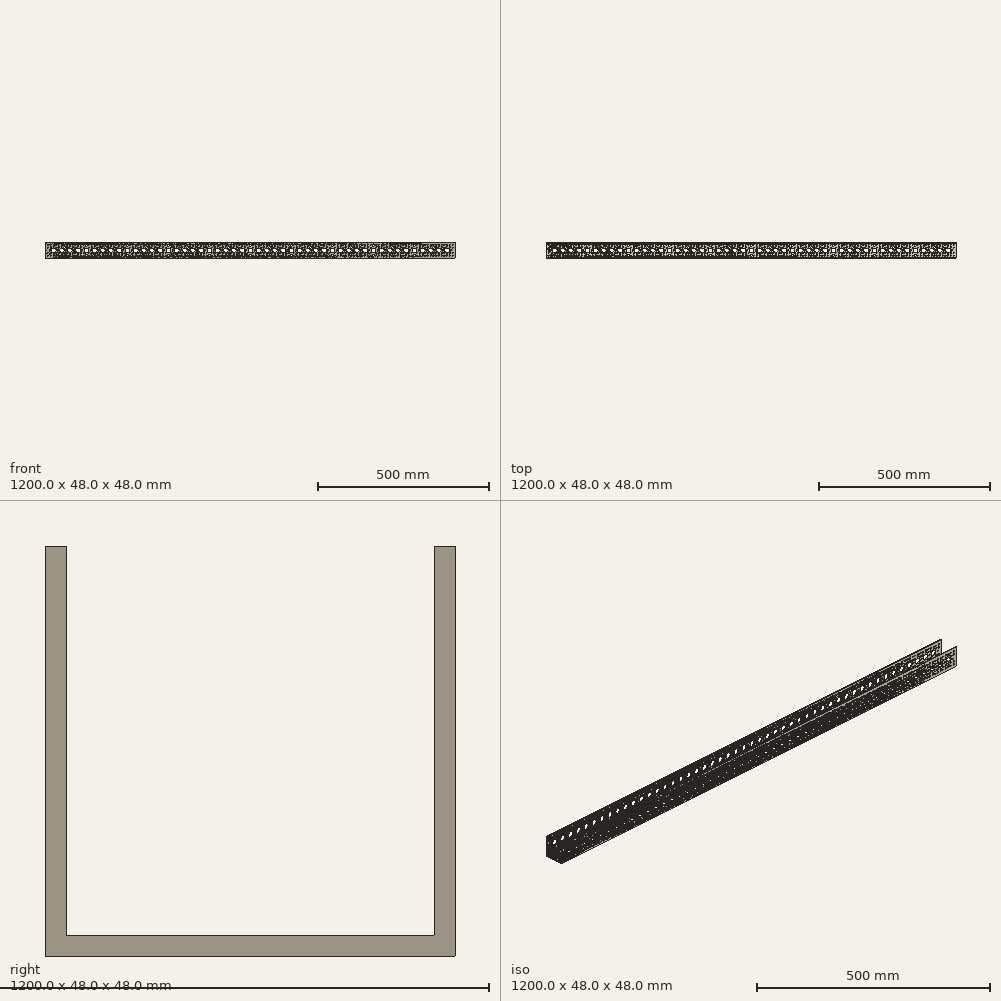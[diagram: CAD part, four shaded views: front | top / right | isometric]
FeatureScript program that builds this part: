
annotation { "Feature Type Name" : "Feature", "Feature Type Description" : "" }
export const myFeature = defineFeature(function(context is Context, id is Id, definition is map)
    precondition{}
    {
        {
            var Q0;
            Q0=qCreatedBy(makeId("Right.planeOp"),FACE);
            var sketch = newSketch(context, id + "F0", { "sketchPlane" : qUnion([Q0]) });
            skLineSegment(sketch, "E0.bottom", {"start": v(24, 24) * mm, "end": v(21.5, 24) * mm});
            skLineSegment(sketch, "E0.top", {"start": v(24, -24) * mm, "end": v(-24, -24) * mm});
            skLineSegment(sketch, "E0.left", {"start": v(24, 24) * mm, "end": v(24, -24) * mm});
            skLineSegment(sketch, "E0.right", {"start": v(-24, 24) * mm, "end": v(-24, -24) * mm});
            skPoint(sketch, "E0.middle", {"position": v(0, 0) * mm});
            skLineSegment(sketch, "E1.top", {"start": v(-21.5, -21.5) * mm, "end": v(21.5, -21.5) * mm});
            skLineSegment(sketch, "E1.left", {"start": v(-21.5, 24) * mm, "end": v(-21.5, -21.5) * mm});
            skLineSegment(sketch, "E1.right", {"start": v(21.5, 24) * mm, "end": v(21.5, -21.5) * mm});
            skLineSegment(sketch, "E2.trimOffspring", {"start": v(-21.5, 24) * mm, "end": v(-24, 24) * mm});
            skSolve(sketch);
        }
        {
            var Q0;
            Q0=qSketchRegion(id+"F0",true);
            extrude(context, id + "F1", {"entities" : qUnion([Q0]), "depth" : 48 * mm, "offsetDistance" : 25 * mm});
        }
        {
            var Q0;
            Q0=qSketchRegion(id+"F0",true);
            extrude(context, id + "F2", {"entities" : qUnion([Q0]), "depth" : 72 * mm, "offsetDistance" : 25 * mm});
        }
        {
            var Q0;
            Q0=qSketchRegion(id+"F0",true);
            extrude(context, id + "F3", {"entities" : qUnion([Q0]), "depth" : 96 * mm, "offsetDistance" : 25 * mm});
        }
        {
            var Q0;
            Q0=qSketchRegion(id+"F0",true);
            extrude(context, id + "F4", {"entities" : qUnion([Q0]), "depth" : 120 * mm, "offsetDistance" : 25 * mm});
        }
        {
            var Q0;
            Q0=qSketchRegion(id+"F0",true);
            extrude(context, id + "F5", {"entities" : qUnion([Q0]), "depth" : 144 * mm, "offsetDistance" : 25 * mm});
        }
        {
            var Q0;
            Q0=qSketchRegion(id+"F0",true);
            extrude(context, id + "F6", {"entities" : qUnion([Q0]), "depth" : 192 * mm, "offsetDistance" : 25 * mm});
        }
        {
            var Q0;
            Q0=qSketchRegion(id+"F0",true);
            extrude(context, id + "F7", {"entities" : qUnion([Q0]), "depth" : 240 * mm, "offsetDistance" : 25 * mm});
        }
        {
            var Q0;
            Q0=qSketchRegion(id+"F0",true);
            extrude(context, id + "F8", {"entities" : qUnion([Q0]), "depth" : 288 * mm, "offsetDistance" : 25 * mm});
        }
        {
            var Q0;
            Q0=qSketchRegion(id+"F0",true);
            extrude(context, id + "F9", {"entities" : qUnion([Q0]), "depth" : 336 * mm, "offsetDistance" : 25 * mm});
        }
        {
            var Q0;
            Q0=qSketchRegion(id+"F0",true);
            extrude(context, id + "F10", {"entities" : qUnion([Q0]), "depth" : 384 * mm, "offsetDistance" : 25 * mm});
        }
        {
            var Q0;
            Q0=qSketchRegion(id+"F0",true);
            extrude(context, id + "F11", {"entities" : qUnion([Q0]), "depth" : 432 * mm, "offsetDistance" : 25 * mm});
        }
        {
            var Q0;
            Q0=qSketchRegion(id+"F0",true);
            extrude(context, id + "F12", {"entities" : qUnion([Q0]), "depth" : 528 * mm, "offsetDistance" : 25 * mm});
        }
        {
            var Q0;
            Q0=qSketchRegion(id+"F0",true);
            extrude(context, id + "F13", {"entities" : qUnion([Q0]), "depth" : 624 * mm, "offsetDistance" : 25 * mm});
        }
        {
            var Q0;
            Q0=qSketchRegion(id+"F0",true);
            extrude(context, id + "F14", {"entities" : qUnion([Q0]), "depth" : 720 * mm, "offsetDistance" : 25 * mm});
        }
        {
            var Q0;
            Q0=qSketchRegion(id+"F0",true);
            extrude(context, id + "F15", {"entities" : qUnion([Q0]), "depth" : 816 * mm, "offsetDistance" : 25 * mm});
        }
        {
            var Q0;
            Q0=qSketchRegion(id+"F0",true);
            extrude(context, id + "F16", {"entities" : qUnion([Q0]), "depth" : 912 * mm, "offsetDistance" : 25 * mm});
        }
        {
            var Q0;
            Q0=qSketchRegion(id+"F0",true);
            extrude(context, id + "F17", {"entities" : qUnion([Q0]), "depth" : 1008 * mm, "offsetDistance" : 25 * mm});
        }
        {
            var Q0;
            Q0=qSketchRegion(id+"F0",true);
            extrude(context, id + "F18", {"entities" : qUnion([Q0]), "depth" : 1104 * mm, "offsetDistance" : 25 * mm});
        }
        {
            var Q0;
            Q0=qSketchRegion(id+"F0",true);
            extrude(context, id + "F19", {"entities" : qUnion([Q0]), "depth" : 1200 * mm, "offsetDistance" : 25 * mm});
        }
        {
            var Q0;
            Q0=qCreatedBy(makeId("Front.planeOp"),FACE);
            var sketch = newSketch(context, id + "F20", { "sketchPlane" : qUnion([Q0]) });
            skCircle(sketch, "E3", {"center": v(24, 0) * mm, "radius": 7 * mm});
            skLineSegment(sketch, "E4.0", {"start": v(48, 24) * mm, "end": v(0, 24) * mm, "construction": true});
            skLineSegment(sketch, "E5.0", {"start": v(48, -24) * mm, "end": v(0, -24) * mm, "construction": true});
            skLineSegment(sketch, "E6", {"start": v(24, 0) * mm, "end": v(24, 24) * mm, "construction": true});
            skLineSegment(sketch, "E7", {"start": v(24, 24) * mm, "end": v(24, -24) * mm, "construction": true});
            skArc(sketch, "E8", {"start": v(26, 16) * mm, "mid": v(24, 18) * mm, "end": v(22, 16) * mm});
            skArc(sketch, "E9", {"start": v(22, 12) * mm, "mid": v(24, 10) * mm, "end": v(26, 12) * mm});
            skLineSegment(sketch, "E10", {"start": v(22, 16) * mm, "end": v(22, 12) * mm});
            skLineSegment(sketch, "E11", {"start": v(26, 16) * mm, "end": v(26, 12) * mm});
            skArc(sketch, "E12", {"start": v(26, -12) * mm, "mid": v(24, -10) * mm, "end": v(22, -12) * mm});
            skArc(sketch, "E13", {"start": v(22, -16) * mm, "mid": v(24, -18) * mm, "end": v(26, -16) * mm});
            skLineSegment(sketch, "E14", {"start": v(22, -12) * mm, "end": v(22, -16) * mm});
            skLineSegment(sketch, "E15", {"start": v(26, -16) * mm, "end": v(26, -12) * mm});
            skLineSegment(sketch, "E16", {"start": v(0, -24) * mm, "end": v(24, 0) * mm, "construction": true});
            skLineSegment(sketch, "E17", {"start": v(0, 24) * mm, "end": v(24, 0) * mm, "construction": true});
            skArc(sketch, "E18", {"start": v(14.1, -7.07) * mm, "mid": v(14.1, -9.9) * mm, "end": v(16.93, -9.9) * mm});
            skArc(sketch, "E19", {"start": v(17.41, -9.41) * mm, "mid": v(17.41, -6.59) * mm, "end": v(14.59, -6.59) * mm});
            skArc(sketch, "E20", {"start": v(14.59, 6.59) * mm, "mid": v(17.41, 6.59) * mm, "end": v(17.41, 9.41) * mm});
            skArc(sketch, "E21", {"start": v(16.93, 9.9) * mm, "mid": v(14.1, 9.9) * mm, "end": v(14.1, 7.07) * mm});
            skLineSegment(sketch, "E22", {"start": v(15.51, 8.49) * mm, "end": v(16.93, 9.9) * mm, "construction": true});
            skLineSegment(sketch, "E23", {"start": v(15.51, 8.49) * mm, "end": v(14.1, 7.07) * mm, "construction": true});
            skLineSegment(sketch, "E24", {"start": v(17.41, 9.41) * mm, "end": v(14.59, 6.59) * mm, "construction": true});
            skLineSegment(sketch, "E25", {"start": v(16.93, 9.9) * mm, "end": v(17.41, 9.41) * mm});
            skLineSegment(sketch, "E26", {"start": v(14.1, 7.07) * mm, "end": v(14.59, 6.59) * mm});
            skLineSegment(sketch, "E27", {"start": v(14.1, -7.07) * mm, "end": v(16.93, -9.9) * mm, "construction": true});
            skLineSegment(sketch, "E28", {"start": v(14.59, -6.59) * mm, "end": v(17.41, -9.41) * mm, "construction": true});
            skLineSegment(sketch, "E29", {"start": v(14.1, -7.07) * mm, "end": v(14.59, -6.59) * mm});
            skLineSegment(sketch, "E30", {"start": v(16.93, -9.9) * mm, "end": v(17.41, -9.41) * mm});
            skCircle(sketch, "E31", {"center": v(8, 16) * mm, "radius": 2 * mm});
            skCircle(sketch, "E32", {"center": v(8, -16) * mm, "radius": 2 * mm});
            skCircle(sketch, "E33", {"center": v(12, 0) * mm, "radius": 2 * mm});
            skLineSegment(sketch, "E34", {"start": v(8, 16) * mm, "end": v(24, 16) * mm, "construction": true});
            skLineSegment(sketch, "E35", {"start": v(8, -16) * mm, "end": v(24, -16) * mm, "construction": true});
            skCircle(sketch, "E36", {"center": v(16, 16) * mm, "radius": 2 * mm});
            skCircle(sketch, "E37", {"center": v(16, -16) * mm, "radius": 2 * mm});
            skLineSegment(sketch, "E38", {"start": v(0, 0) * mm, "end": v(24, -24) * mm, "construction": true});
            skLineSegment(sketch, "E39", {"start": v(24, 24) * mm, "end": v(0, 0) * mm, "construction": true});
            skArc(sketch, "E40", {"start": v(6.59, 9.41) * mm, "mid": v(6.59, 6.59) * mm, "end": v(9.41, 6.59) * mm});
            skArc(sketch, "E41", {"start": v(9.9, 7.07) * mm, "mid": v(9.9, 9.9) * mm, "end": v(7.07, 9.9) * mm});
            skArc(sketch, "E42", {"start": v(7.07, -9.9) * mm, "mid": v(9.9, -9.9) * mm, "end": v(9.9, -7.07) * mm});
            skArc(sketch, "E43", {"start": v(9.41, -6.59) * mm, "mid": v(6.59, -6.59) * mm, "end": v(6.59, -9.41) * mm});
            skLineSegment(sketch, "E44", {"start": v(7.07, 9.9) * mm, "end": v(9.9, 7.07) * mm, "construction": true});
            skLineSegment(sketch, "E45", {"start": v(6.59, 9.41) * mm, "end": v(9.41, 6.59) * mm, "construction": true});
            skLineSegment(sketch, "E46", {"start": v(9.41, -6.59) * mm, "end": v(6.59, -9.41) * mm, "construction": true});
            skLineSegment(sketch, "E47", {"start": v(9.9, -7.07) * mm, "end": v(7.07, -9.9) * mm, "construction": true});
            skLineSegment(sketch, "E48", {"start": v(9.41, -6.59) * mm, "end": v(9.9, -7.07) * mm});
            skLineSegment(sketch, "E49", {"start": v(6.59, -9.41) * mm, "end": v(7.07, -9.9) * mm});
            skLineSegment(sketch, "E50", {"start": v(7.07, 9.9) * mm, "end": v(6.59, 9.41) * mm});
            skLineSegment(sketch, "E51", {"start": v(9.9, 7.07) * mm, "end": v(9.41, 6.59) * mm});
            skArc(sketch, "E52.1.0.0", {"start": v(50, 16) * mm, "mid": v(48, 18) * mm, "end": v(46, 16) * mm});
            skLineSegment(sketch, "E52.1.0.1", {"start": v(50, 16) * mm, "end": v(50, 12) * mm});
            skLineSegment(sketch, "E52.1.0.2", {"start": v(46, 16) * mm, "end": v(46, 12) * mm});
            skArc(sketch, "E52.1.0.3", {"start": v(46, 12) * mm, "mid": v(48, 10) * mm, "end": v(50, 12) * mm});
            skCircle(sketch, "E52.1.0.4", {"center": v(40, 16) * mm, "radius": 2 * mm});
            skCircle(sketch, "E52.1.0.5", {"center": v(32, 16) * mm, "radius": 2 * mm});
            skArc(sketch, "E52.1.0.6", {"start": v(33.9, 7.07) * mm, "mid": v(33.9, 9.9) * mm, "end": v(31.07, 9.9) * mm});
            skArc(sketch, "E52.1.0.7", {"start": v(30.59, 9.41) * mm, "mid": v(30.59, 6.59) * mm, "end": v(33.41, 6.59) * mm});
            skLineSegment(sketch, "E52.1.0.8", {"start": v(31.07, 9.9) * mm, "end": v(30.59, 9.41) * mm});
            skLineSegment(sketch, "E52.1.0.9", {"start": v(33.9, 7.07) * mm, "end": v(33.41, 6.59) * mm});
            skArc(sketch, "E52.1.0.10", {"start": v(40.93, 9.9) * mm, "mid": v(38.1, 9.9) * mm, "end": v(38.1, 7.07) * mm});
            skLineSegment(sketch, "E52.1.0.11", {"start": v(40.93, 9.9) * mm, "end": v(41.41, 9.41) * mm});
            skArc(sketch, "E52.1.0.12", {"start": v(38.59, 6.59) * mm, "mid": v(41.41, 6.59) * mm, "end": v(41.41, 9.41) * mm});
            skLineSegment(sketch, "E52.1.0.13", {"start": v(38.1, 7.07) * mm, "end": v(38.59, 6.59) * mm});
            skCircle(sketch, "E52.1.0.14", {"center": v(48, 0) * mm, "radius": 7 * mm});
            skArc(sketch, "E52.1.0.15", {"start": v(31.07, -9.9) * mm, "mid": v(33.9, -9.9) * mm, "end": v(33.9, -7.07) * mm});
            skArc(sketch, "E52.1.0.16", {"start": v(33.41, -6.59) * mm, "mid": v(30.59, -6.59) * mm, "end": v(30.59, -9.41) * mm});
            skLineSegment(sketch, "E52.1.0.17", {"start": v(33.41, -6.59) * mm, "end": v(33.9, -7.07) * mm});
            skLineSegment(sketch, "E52.1.0.18", {"start": v(30.59, -9.41) * mm, "end": v(31.07, -9.9) * mm});
            skArc(sketch, "E52.1.0.19", {"start": v(38.1, -7.07) * mm, "mid": v(38.1, -9.9) * mm, "end": v(40.93, -9.9) * mm});
            skLineSegment(sketch, "E52.1.0.20", {"start": v(40.93, -9.9) * mm, "end": v(41.41, -9.41) * mm});
            skArc(sketch, "E52.1.0.21", {"start": v(41.41, -9.41) * mm, "mid": v(41.41, -6.59) * mm, "end": v(38.59, -6.59) * mm});
            skCircle(sketch, "E52.1.0.22", {"center": v(40, -16) * mm, "radius": 2 * mm});
            skCircle(sketch, "E52.1.0.23", {"center": v(32, -16) * mm, "radius": 2 * mm});
            skLineSegment(sketch, "E52.1.0.24", {"start": v(38.1, -7.07) * mm, "end": v(38.59, -6.59) * mm});
            skCircle(sketch, "E52.1.0.25", {"center": v(36, 0) * mm, "radius": 2 * mm});
            skArc(sketch, "E52.1.0.26", {"start": v(50, -12) * mm, "mid": v(48, -10) * mm, "end": v(46, -12) * mm});
            skArc(sketch, "E52.1.0.27", {"start": v(46, -16) * mm, "mid": v(48, -18) * mm, "end": v(50, -16) * mm});
            skLineSegment(sketch, "E52.1.0.28", {"start": v(46, -12) * mm, "end": v(46, -16) * mm});
            skLineSegment(sketch, "E52.1.0.29", {"start": v(50, -16) * mm, "end": v(50, -12) * mm});
            skArc(sketch, "E52.2.0.0", {"start": v(74, 16) * mm, "mid": v(72, 18) * mm, "end": v(70, 16) * mm});
            skLineSegment(sketch, "E52.2.0.1", {"start": v(74, 16) * mm, "end": v(74, 12) * mm});
            skLineSegment(sketch, "E52.2.0.2", {"start": v(70, 16) * mm, "end": v(70, 12) * mm});
            skArc(sketch, "E52.2.0.3", {"start": v(70, 12) * mm, "mid": v(72, 10) * mm, "end": v(74, 12) * mm});
            skCircle(sketch, "E52.2.0.4", {"center": v(64, 16) * mm, "radius": 2 * mm});
            skCircle(sketch, "E52.2.0.5", {"center": v(56, 16) * mm, "radius": 2 * mm});
            skArc(sketch, "E52.2.0.6", {"start": v(57.9, 7.07) * mm, "mid": v(57.9, 9.9) * mm, "end": v(55.07, 9.9) * mm});
            skArc(sketch, "E52.2.0.7", {"start": v(54.59, 9.41) * mm, "mid": v(54.59, 6.59) * mm, "end": v(57.41, 6.59) * mm});
            skLineSegment(sketch, "E52.2.0.8", {"start": v(55.07, 9.9) * mm, "end": v(54.59, 9.41) * mm});
            skLineSegment(sketch, "E52.2.0.9", {"start": v(57.9, 7.07) * mm, "end": v(57.41, 6.59) * mm});
            skArc(sketch, "E52.2.0.10", {"start": v(64.93, 9.9) * mm, "mid": v(62.1, 9.9) * mm, "end": v(62.1, 7.07) * mm});
            skLineSegment(sketch, "E52.2.0.11", {"start": v(64.93, 9.9) * mm, "end": v(65.41, 9.41) * mm});
            skArc(sketch, "E52.2.0.12", {"start": v(62.59, 6.59) * mm, "mid": v(65.41, 6.59) * mm, "end": v(65.41, 9.41) * mm});
            skLineSegment(sketch, "E52.2.0.13", {"start": v(62.1, 7.07) * mm, "end": v(62.59, 6.59) * mm});
            skCircle(sketch, "E52.2.0.14", {"center": v(72, 0) * mm, "radius": 7 * mm});
            skArc(sketch, "E52.2.0.15", {"start": v(55.07, -9.9) * mm, "mid": v(57.9, -9.9) * mm, "end": v(57.9, -7.07) * mm});
            skArc(sketch, "E52.2.0.16", {"start": v(57.41, -6.59) * mm, "mid": v(54.59, -6.59) * mm, "end": v(54.59, -9.41) * mm});
            skLineSegment(sketch, "E52.2.0.17", {"start": v(57.41, -6.59) * mm, "end": v(57.9, -7.07) * mm});
            skLineSegment(sketch, "E52.2.0.18", {"start": v(54.59, -9.41) * mm, "end": v(55.07, -9.9) * mm});
            skArc(sketch, "E52.2.0.19", {"start": v(62.1, -7.07) * mm, "mid": v(62.1, -9.9) * mm, "end": v(64.93, -9.9) * mm});
            skLineSegment(sketch, "E52.2.0.20", {"start": v(64.93, -9.9) * mm, "end": v(65.41, -9.41) * mm});
            skArc(sketch, "E52.2.0.21", {"start": v(65.41, -9.41) * mm, "mid": v(65.41, -6.59) * mm, "end": v(62.59, -6.59) * mm});
            skCircle(sketch, "E52.2.0.22", {"center": v(64, -16) * mm, "radius": 2 * mm});
            skCircle(sketch, "E52.2.0.23", {"center": v(56, -16) * mm, "radius": 2 * mm});
            skLineSegment(sketch, "E52.2.0.24", {"start": v(62.1, -7.07) * mm, "end": v(62.59, -6.59) * mm});
            skCircle(sketch, "E52.2.0.25", {"center": v(60, 0) * mm, "radius": 2 * mm});
            skArc(sketch, "E52.2.0.26", {"start": v(74, -12) * mm, "mid": v(72, -10) * mm, "end": v(70, -12) * mm});
            skArc(sketch, "E52.2.0.27", {"start": v(70, -16) * mm, "mid": v(72, -18) * mm, "end": v(74, -16) * mm});
            skLineSegment(sketch, "E52.2.0.28", {"start": v(70, -12) * mm, "end": v(70, -16) * mm});
            skLineSegment(sketch, "E52.2.0.29", {"start": v(74, -16) * mm, "end": v(74, -12) * mm});
            skArc(sketch, "E52.3.0.0", {"start": v(98, 16) * mm, "mid": v(96, 18) * mm, "end": v(94, 16) * mm});
            skLineSegment(sketch, "E52.3.0.1", {"start": v(98, 16) * mm, "end": v(98, 12) * mm});
            skLineSegment(sketch, "E52.3.0.2", {"start": v(94, 16) * mm, "end": v(94, 12) * mm});
            skArc(sketch, "E52.3.0.3", {"start": v(94, 12) * mm, "mid": v(96, 10) * mm, "end": v(98, 12) * mm});
            skCircle(sketch, "E52.3.0.4", {"center": v(88, 16) * mm, "radius": 2 * mm});
            skCircle(sketch, "E52.3.0.5", {"center": v(80, 16) * mm, "radius": 2 * mm});
            skArc(sketch, "E52.3.0.6", {"start": v(81.9, 7.07) * mm, "mid": v(81.9, 9.9) * mm, "end": v(79.07, 9.9) * mm});
            skArc(sketch, "E52.3.0.7", {"start": v(78.59, 9.41) * mm, "mid": v(78.59, 6.59) * mm, "end": v(81.41, 6.59) * mm});
            skLineSegment(sketch, "E52.3.0.8", {"start": v(79.07, 9.9) * mm, "end": v(78.59, 9.41) * mm});
            skLineSegment(sketch, "E52.3.0.9", {"start": v(81.9, 7.07) * mm, "end": v(81.41, 6.59) * mm});
            skArc(sketch, "E52.3.0.10", {"start": v(88.93, 9.9) * mm, "mid": v(86.1, 9.9) * mm, "end": v(86.1, 7.07) * mm});
            skLineSegment(sketch, "E52.3.0.11", {"start": v(88.93, 9.9) * mm, "end": v(89.41, 9.41) * mm});
            skArc(sketch, "E52.3.0.12", {"start": v(86.59, 6.59) * mm, "mid": v(89.41, 6.59) * mm, "end": v(89.41, 9.41) * mm});
            skLineSegment(sketch, "E52.3.0.13", {"start": v(86.1, 7.07) * mm, "end": v(86.59, 6.59) * mm});
            skCircle(sketch, "E52.3.0.14", {"center": v(96, 0) * mm, "radius": 7 * mm});
            skArc(sketch, "E52.3.0.15", {"start": v(79.07, -9.9) * mm, "mid": v(81.9, -9.9) * mm, "end": v(81.9, -7.07) * mm});
            skArc(sketch, "E52.3.0.16", {"start": v(81.41, -6.59) * mm, "mid": v(78.59, -6.59) * mm, "end": v(78.59, -9.41) * mm});
            skLineSegment(sketch, "E52.3.0.17", {"start": v(81.41, -6.59) * mm, "end": v(81.9, -7.07) * mm});
            skLineSegment(sketch, "E52.3.0.18", {"start": v(78.59, -9.41) * mm, "end": v(79.07, -9.9) * mm});
            skArc(sketch, "E52.3.0.19", {"start": v(86.1, -7.07) * mm, "mid": v(86.1, -9.9) * mm, "end": v(88.93, -9.9) * mm});
            skLineSegment(sketch, "E52.3.0.20", {"start": v(88.93, -9.9) * mm, "end": v(89.41, -9.41) * mm});
            skArc(sketch, "E52.3.0.21", {"start": v(89.41, -9.41) * mm, "mid": v(89.41, -6.59) * mm, "end": v(86.59, -6.59) * mm});
            skCircle(sketch, "E52.3.0.22", {"center": v(88, -16) * mm, "radius": 2 * mm});
            skCircle(sketch, "E52.3.0.23", {"center": v(80, -16) * mm, "radius": 2 * mm});
            skLineSegment(sketch, "E52.3.0.24", {"start": v(86.1, -7.07) * mm, "end": v(86.59, -6.59) * mm});
            skCircle(sketch, "E52.3.0.25", {"center": v(84, 0) * mm, "radius": 2 * mm});
            skArc(sketch, "E52.3.0.26", {"start": v(98, -12) * mm, "mid": v(96, -10) * mm, "end": v(94, -12) * mm});
            skArc(sketch, "E52.3.0.27", {"start": v(94, -16) * mm, "mid": v(96, -18) * mm, "end": v(98, -16) * mm});
            skLineSegment(sketch, "E52.3.0.28", {"start": v(94, -12) * mm, "end": v(94, -16) * mm});
            skLineSegment(sketch, "E52.3.0.29", {"start": v(98, -16) * mm, "end": v(98, -12) * mm});
            skArc(sketch, "E52.4.0.0", {"start": v(122, 16) * mm, "mid": v(120, 18) * mm, "end": v(118, 16) * mm});
            skLineSegment(sketch, "E52.4.0.1", {"start": v(122, 16) * mm, "end": v(122, 12) * mm});
            skLineSegment(sketch, "E52.4.0.2", {"start": v(118, 16) * mm, "end": v(118, 12) * mm});
            skArc(sketch, "E52.4.0.3", {"start": v(118, 12) * mm, "mid": v(120, 10) * mm, "end": v(122, 12) * mm});
            skCircle(sketch, "E52.4.0.4", {"center": v(112, 16) * mm, "radius": 2 * mm});
            skCircle(sketch, "E52.4.0.5", {"center": v(104, 16) * mm, "radius": 2 * mm});
            skArc(sketch, "E52.4.0.6", {"start": v(105.9, 7.07) * mm, "mid": v(105.9, 9.9) * mm, "end": v(103.07, 9.9) * mm});
            skArc(sketch, "E52.4.0.7", {"start": v(102.59, 9.41) * mm, "mid": v(102.59, 6.59) * mm, "end": v(105.41, 6.59) * mm});
            skLineSegment(sketch, "E52.4.0.8", {"start": v(103.07, 9.9) * mm, "end": v(102.59, 9.41) * mm});
            skLineSegment(sketch, "E52.4.0.9", {"start": v(105.9, 7.07) * mm, "end": v(105.41, 6.59) * mm});
            skArc(sketch, "E52.4.0.10", {"start": v(112.93, 9.9) * mm, "mid": v(110.1, 9.9) * mm, "end": v(110.1, 7.07) * mm});
            skLineSegment(sketch, "E52.4.0.11", {"start": v(112.93, 9.9) * mm, "end": v(113.41, 9.41) * mm});
            skArc(sketch, "E52.4.0.12", {"start": v(110.59, 6.59) * mm, "mid": v(113.41, 6.59) * mm, "end": v(113.41, 9.41) * mm});
            skLineSegment(sketch, "E52.4.0.13", {"start": v(110.1, 7.07) * mm, "end": v(110.59, 6.59) * mm});
            skCircle(sketch, "E52.4.0.14", {"center": v(120, 0) * mm, "radius": 7 * mm});
            skArc(sketch, "E52.4.0.15", {"start": v(103.07, -9.9) * mm, "mid": v(105.9, -9.9) * mm, "end": v(105.9, -7.07) * mm});
            skArc(sketch, "E52.4.0.16", {"start": v(105.41, -6.59) * mm, "mid": v(102.59, -6.59) * mm, "end": v(102.59, -9.41) * mm});
            skLineSegment(sketch, "E52.4.0.17", {"start": v(105.41, -6.59) * mm, "end": v(105.9, -7.07) * mm});
            skLineSegment(sketch, "E52.4.0.18", {"start": v(102.59, -9.41) * mm, "end": v(103.07, -9.9) * mm});
            skArc(sketch, "E52.4.0.19", {"start": v(110.1, -7.07) * mm, "mid": v(110.1, -9.9) * mm, "end": v(112.93, -9.9) * mm});
            skLineSegment(sketch, "E52.4.0.20", {"start": v(112.93, -9.9) * mm, "end": v(113.41, -9.41) * mm});
            skArc(sketch, "E52.4.0.21", {"start": v(113.41, -9.41) * mm, "mid": v(113.41, -6.59) * mm, "end": v(110.59, -6.59) * mm});
            skCircle(sketch, "E52.4.0.22", {"center": v(112, -16) * mm, "radius": 2 * mm});
            skCircle(sketch, "E52.4.0.23", {"center": v(104, -16) * mm, "radius": 2 * mm});
            skLineSegment(sketch, "E52.4.0.24", {"start": v(110.1, -7.07) * mm, "end": v(110.59, -6.59) * mm});
            skCircle(sketch, "E52.4.0.25", {"center": v(108, 0) * mm, "radius": 2 * mm});
            skArc(sketch, "E52.4.0.26", {"start": v(122, -12) * mm, "mid": v(120, -10) * mm, "end": v(118, -12) * mm});
            skArc(sketch, "E52.4.0.27", {"start": v(118, -16) * mm, "mid": v(120, -18) * mm, "end": v(122, -16) * mm});
            skLineSegment(sketch, "E52.4.0.28", {"start": v(118, -12) * mm, "end": v(118, -16) * mm});
            skLineSegment(sketch, "E52.4.0.29", {"start": v(122, -16) * mm, "end": v(122, -12) * mm});
            skArc(sketch, "E52.5.0.0", {"start": v(146, 16) * mm, "mid": v(144, 18) * mm, "end": v(142, 16) * mm});
            skLineSegment(sketch, "E52.5.0.1", {"start": v(146, 16) * mm, "end": v(146, 12) * mm});
            skLineSegment(sketch, "E52.5.0.2", {"start": v(142, 16) * mm, "end": v(142, 12) * mm});
            skArc(sketch, "E52.5.0.3", {"start": v(142, 12) * mm, "mid": v(144, 10) * mm, "end": v(146, 12) * mm});
            skCircle(sketch, "E52.5.0.4", {"center": v(136, 16) * mm, "radius": 2 * mm});
            skCircle(sketch, "E52.5.0.5", {"center": v(128, 16) * mm, "radius": 2 * mm});
            skArc(sketch, "E52.5.0.6", {"start": v(129.9, 7.07) * mm, "mid": v(129.9, 9.9) * mm, "end": v(127.07, 9.9) * mm});
            skArc(sketch, "E52.5.0.7", {"start": v(126.59, 9.41) * mm, "mid": v(126.59, 6.59) * mm, "end": v(129.41, 6.59) * mm});
            skLineSegment(sketch, "E52.5.0.8", {"start": v(127.07, 9.9) * mm, "end": v(126.59, 9.41) * mm});
            skLineSegment(sketch, "E52.5.0.9", {"start": v(129.9, 7.07) * mm, "end": v(129.41, 6.59) * mm});
            skArc(sketch, "E52.5.0.10", {"start": v(136.93, 9.9) * mm, "mid": v(134.1, 9.9) * mm, "end": v(134.1, 7.07) * mm});
            skLineSegment(sketch, "E52.5.0.11", {"start": v(136.93, 9.9) * mm, "end": v(137.41, 9.41) * mm});
            skArc(sketch, "E52.5.0.12", {"start": v(134.59, 6.59) * mm, "mid": v(137.41, 6.59) * mm, "end": v(137.41, 9.41) * mm});
            skLineSegment(sketch, "E52.5.0.13", {"start": v(134.1, 7.07) * mm, "end": v(134.59, 6.59) * mm});
            skCircle(sketch, "E52.5.0.14", {"center": v(144, 0) * mm, "radius": 7 * mm});
            skArc(sketch, "E52.5.0.15", {"start": v(127.07, -9.9) * mm, "mid": v(129.9, -9.9) * mm, "end": v(129.9, -7.07) * mm});
            skArc(sketch, "E52.5.0.16", {"start": v(129.41, -6.59) * mm, "mid": v(126.59, -6.59) * mm, "end": v(126.59, -9.41) * mm});
            skLineSegment(sketch, "E52.5.0.17", {"start": v(129.41, -6.59) * mm, "end": v(129.9, -7.07) * mm});
            skLineSegment(sketch, "E52.5.0.18", {"start": v(126.59, -9.41) * mm, "end": v(127.07, -9.9) * mm});
            skArc(sketch, "E52.5.0.19", {"start": v(134.1, -7.07) * mm, "mid": v(134.1, -9.9) * mm, "end": v(136.93, -9.9) * mm});
            skLineSegment(sketch, "E52.5.0.20", {"start": v(136.93, -9.9) * mm, "end": v(137.41, -9.41) * mm});
            skArc(sketch, "E52.5.0.21", {"start": v(137.41, -9.41) * mm, "mid": v(137.41, -6.59) * mm, "end": v(134.59, -6.59) * mm});
            skCircle(sketch, "E52.5.0.22", {"center": v(136, -16) * mm, "radius": 2 * mm});
            skCircle(sketch, "E52.5.0.23", {"center": v(128, -16) * mm, "radius": 2 * mm});
            skLineSegment(sketch, "E52.5.0.24", {"start": v(134.1, -7.07) * mm, "end": v(134.59, -6.59) * mm});
            skCircle(sketch, "E52.5.0.25", {"center": v(132, 0) * mm, "radius": 2 * mm});
            skArc(sketch, "E52.5.0.26", {"start": v(146, -12) * mm, "mid": v(144, -10) * mm, "end": v(142, -12) * mm});
            skArc(sketch, "E52.5.0.27", {"start": v(142, -16) * mm, "mid": v(144, -18) * mm, "end": v(146, -16) * mm});
            skLineSegment(sketch, "E52.5.0.28", {"start": v(142, -12) * mm, "end": v(142, -16) * mm});
            skLineSegment(sketch, "E52.5.0.29", {"start": v(146, -16) * mm, "end": v(146, -12) * mm});
            skArc(sketch, "E52.6.0.0", {"start": v(170, 16) * mm, "mid": v(168, 18) * mm, "end": v(166, 16) * mm});
            skLineSegment(sketch, "E52.6.0.1", {"start": v(170, 16) * mm, "end": v(170, 12) * mm});
            skLineSegment(sketch, "E52.6.0.2", {"start": v(166, 16) * mm, "end": v(166, 12) * mm});
            skArc(sketch, "E52.6.0.3", {"start": v(166, 12) * mm, "mid": v(168, 10) * mm, "end": v(170, 12) * mm});
            skCircle(sketch, "E52.6.0.4", {"center": v(160, 16) * mm, "radius": 2 * mm});
            skCircle(sketch, "E52.6.0.5", {"center": v(152, 16) * mm, "radius": 2 * mm});
            skArc(sketch, "E52.6.0.6", {"start": v(153.9, 7.07) * mm, "mid": v(153.9, 9.9) * mm, "end": v(151.07, 9.9) * mm});
            skArc(sketch, "E52.6.0.7", {"start": v(150.59, 9.41) * mm, "mid": v(150.59, 6.59) * mm, "end": v(153.41, 6.59) * mm});
            skLineSegment(sketch, "E52.6.0.8", {"start": v(151.07, 9.9) * mm, "end": v(150.59, 9.41) * mm});
            skLineSegment(sketch, "E52.6.0.9", {"start": v(153.9, 7.07) * mm, "end": v(153.41, 6.59) * mm});
            skArc(sketch, "E52.6.0.10", {"start": v(160.93, 9.9) * mm, "mid": v(158.1, 9.9) * mm, "end": v(158.1, 7.07) * mm});
            skLineSegment(sketch, "E52.6.0.11", {"start": v(160.93, 9.9) * mm, "end": v(161.41, 9.41) * mm});
            skArc(sketch, "E52.6.0.12", {"start": v(158.59, 6.59) * mm, "mid": v(161.41, 6.59) * mm, "end": v(161.41, 9.41) * mm});
            skLineSegment(sketch, "E52.6.0.13", {"start": v(158.1, 7.07) * mm, "end": v(158.59, 6.59) * mm});
            skCircle(sketch, "E52.6.0.14", {"center": v(168, 0) * mm, "radius": 7 * mm});
            skArc(sketch, "E52.6.0.15", {"start": v(151.07, -9.9) * mm, "mid": v(153.9, -9.9) * mm, "end": v(153.9, -7.07) * mm});
            skArc(sketch, "E52.6.0.16", {"start": v(153.41, -6.59) * mm, "mid": v(150.59, -6.59) * mm, "end": v(150.59, -9.41) * mm});
            skLineSegment(sketch, "E52.6.0.17", {"start": v(153.41, -6.59) * mm, "end": v(153.9, -7.07) * mm});
            skLineSegment(sketch, "E52.6.0.18", {"start": v(150.59, -9.41) * mm, "end": v(151.07, -9.9) * mm});
            skArc(sketch, "E52.6.0.19", {"start": v(158.1, -7.07) * mm, "mid": v(158.1, -9.9) * mm, "end": v(160.93, -9.9) * mm});
            skLineSegment(sketch, "E52.6.0.20", {"start": v(160.93, -9.9) * mm, "end": v(161.41, -9.41) * mm});
            skArc(sketch, "E52.6.0.21", {"start": v(161.41, -9.41) * mm, "mid": v(161.41, -6.59) * mm, "end": v(158.59, -6.59) * mm});
            skCircle(sketch, "E52.6.0.22", {"center": v(160, -16) * mm, "radius": 2 * mm});
            skCircle(sketch, "E52.6.0.23", {"center": v(152, -16) * mm, "radius": 2 * mm});
            skLineSegment(sketch, "E52.6.0.24", {"start": v(158.1, -7.07) * mm, "end": v(158.59, -6.59) * mm});
            skCircle(sketch, "E52.6.0.25", {"center": v(156, 0) * mm, "radius": 2 * mm});
            skArc(sketch, "E52.6.0.26", {"start": v(170, -12) * mm, "mid": v(168, -10) * mm, "end": v(166, -12) * mm});
            skArc(sketch, "E52.6.0.27", {"start": v(166, -16) * mm, "mid": v(168, -18) * mm, "end": v(170, -16) * mm});
            skLineSegment(sketch, "E52.6.0.28", {"start": v(166, -12) * mm, "end": v(166, -16) * mm});
            skLineSegment(sketch, "E52.6.0.29", {"start": v(170, -16) * mm, "end": v(170, -12) * mm});
            skArc(sketch, "E52.7.0.0", {"start": v(194, 16) * mm, "mid": v(192, 18) * mm, "end": v(190, 16) * mm});
            skLineSegment(sketch, "E52.7.0.1", {"start": v(194, 16) * mm, "end": v(194, 12) * mm});
            skLineSegment(sketch, "E52.7.0.2", {"start": v(190, 16) * mm, "end": v(190, 12) * mm});
            skArc(sketch, "E52.7.0.3", {"start": v(190, 12) * mm, "mid": v(192, 10) * mm, "end": v(194, 12) * mm});
            skCircle(sketch, "E52.7.0.4", {"center": v(184, 16) * mm, "radius": 2 * mm});
            skCircle(sketch, "E52.7.0.5", {"center": v(176, 16) * mm, "radius": 2 * mm});
            skArc(sketch, "E52.7.0.6", {"start": v(177.9, 7.07) * mm, "mid": v(177.9, 9.9) * mm, "end": v(175.07, 9.9) * mm});
            skArc(sketch, "E52.7.0.7", {"start": v(174.59, 9.41) * mm, "mid": v(174.59, 6.59) * mm, "end": v(177.41, 6.59) * mm});
            skLineSegment(sketch, "E52.7.0.8", {"start": v(175.07, 9.9) * mm, "end": v(174.59, 9.41) * mm});
            skLineSegment(sketch, "E52.7.0.9", {"start": v(177.9, 7.07) * mm, "end": v(177.41, 6.59) * mm});
            skArc(sketch, "E52.7.0.10", {"start": v(184.93, 9.9) * mm, "mid": v(182.1, 9.9) * mm, "end": v(182.1, 7.07) * mm});
            skLineSegment(sketch, "E52.7.0.11", {"start": v(184.93, 9.9) * mm, "end": v(185.41, 9.41) * mm});
            skArc(sketch, "E52.7.0.12", {"start": v(182.59, 6.59) * mm, "mid": v(185.41, 6.59) * mm, "end": v(185.41, 9.41) * mm});
            skLineSegment(sketch, "E52.7.0.13", {"start": v(182.1, 7.07) * mm, "end": v(182.59, 6.59) * mm});
            skCircle(sketch, "E52.7.0.14", {"center": v(192, 0) * mm, "radius": 7 * mm});
            skArc(sketch, "E52.7.0.15", {"start": v(175.07, -9.9) * mm, "mid": v(177.9, -9.9) * mm, "end": v(177.9, -7.07) * mm});
            skArc(sketch, "E52.7.0.16", {"start": v(177.41, -6.59) * mm, "mid": v(174.59, -6.59) * mm, "end": v(174.59, -9.41) * mm});
            skLineSegment(sketch, "E52.7.0.17", {"start": v(177.41, -6.59) * mm, "end": v(177.9, -7.07) * mm});
            skLineSegment(sketch, "E52.7.0.18", {"start": v(174.59, -9.41) * mm, "end": v(175.07, -9.9) * mm});
            skArc(sketch, "E52.7.0.19", {"start": v(182.1, -7.07) * mm, "mid": v(182.1, -9.9) * mm, "end": v(184.93, -9.9) * mm});
            skLineSegment(sketch, "E52.7.0.20", {"start": v(184.93, -9.9) * mm, "end": v(185.41, -9.41) * mm});
            skArc(sketch, "E52.7.0.21", {"start": v(185.41, -9.41) * mm, "mid": v(185.41, -6.59) * mm, "end": v(182.59, -6.59) * mm});
            skCircle(sketch, "E52.7.0.22", {"center": v(184, -16) * mm, "radius": 2 * mm});
            skCircle(sketch, "E52.7.0.23", {"center": v(176, -16) * mm, "radius": 2 * mm});
            skLineSegment(sketch, "E52.7.0.24", {"start": v(182.1, -7.07) * mm, "end": v(182.59, -6.59) * mm});
            skCircle(sketch, "E52.7.0.25", {"center": v(180, 0) * mm, "radius": 2 * mm});
            skArc(sketch, "E52.7.0.26", {"start": v(194, -12) * mm, "mid": v(192, -10) * mm, "end": v(190, -12) * mm});
            skArc(sketch, "E52.7.0.27", {"start": v(190, -16) * mm, "mid": v(192, -18) * mm, "end": v(194, -16) * mm});
            skLineSegment(sketch, "E52.7.0.28", {"start": v(190, -12) * mm, "end": v(190, -16) * mm});
            skLineSegment(sketch, "E52.7.0.29", {"start": v(194, -16) * mm, "end": v(194, -12) * mm});
            skArc(sketch, "E52.8.0.0", {"start": v(218, 16) * mm, "mid": v(216, 18) * mm, "end": v(214, 16) * mm});
            skLineSegment(sketch, "E52.8.0.1", {"start": v(218, 16) * mm, "end": v(218, 12) * mm});
            skLineSegment(sketch, "E52.8.0.2", {"start": v(214, 16) * mm, "end": v(214, 12) * mm});
            skArc(sketch, "E52.8.0.3", {"start": v(214, 12) * mm, "mid": v(216, 10) * mm, "end": v(218, 12) * mm});
            skCircle(sketch, "E52.8.0.4", {"center": v(208, 16) * mm, "radius": 2 * mm});
            skCircle(sketch, "E52.8.0.5", {"center": v(200, 16) * mm, "radius": 2 * mm});
            skArc(sketch, "E52.8.0.6", {"start": v(201.9, 7.07) * mm, "mid": v(201.9, 9.9) * mm, "end": v(199.07, 9.9) * mm});
            skArc(sketch, "E52.8.0.7", {"start": v(198.59, 9.41) * mm, "mid": v(198.59, 6.59) * mm, "end": v(201.41, 6.59) * mm});
            skLineSegment(sketch, "E52.8.0.8", {"start": v(199.07, 9.9) * mm, "end": v(198.59, 9.41) * mm});
            skLineSegment(sketch, "E52.8.0.9", {"start": v(201.9, 7.07) * mm, "end": v(201.41, 6.59) * mm});
            skArc(sketch, "E52.8.0.10", {"start": v(208.93, 9.9) * mm, "mid": v(206.1, 9.9) * mm, "end": v(206.1, 7.07) * mm});
            skLineSegment(sketch, "E52.8.0.11", {"start": v(208.93, 9.9) * mm, "end": v(209.41, 9.41) * mm});
            skArc(sketch, "E52.8.0.12", {"start": v(206.59, 6.59) * mm, "mid": v(209.41, 6.59) * mm, "end": v(209.41, 9.41) * mm});
            skLineSegment(sketch, "E52.8.0.13", {"start": v(206.1, 7.07) * mm, "end": v(206.59, 6.59) * mm});
            skCircle(sketch, "E52.8.0.14", {"center": v(216, 0) * mm, "radius": 7 * mm});
            skArc(sketch, "E52.8.0.15", {"start": v(199.07, -9.9) * mm, "mid": v(201.9, -9.9) * mm, "end": v(201.9, -7.07) * mm});
            skArc(sketch, "E52.8.0.16", {"start": v(201.41, -6.59) * mm, "mid": v(198.59, -6.59) * mm, "end": v(198.59, -9.41) * mm});
            skLineSegment(sketch, "E52.8.0.17", {"start": v(201.41, -6.59) * mm, "end": v(201.9, -7.07) * mm});
            skLineSegment(sketch, "E52.8.0.18", {"start": v(198.59, -9.41) * mm, "end": v(199.07, -9.9) * mm});
            skArc(sketch, "E52.8.0.19", {"start": v(206.1, -7.07) * mm, "mid": v(206.1, -9.9) * mm, "end": v(208.93, -9.9) * mm});
            skLineSegment(sketch, "E52.8.0.20", {"start": v(208.93, -9.9) * mm, "end": v(209.41, -9.41) * mm});
            skArc(sketch, "E52.8.0.21", {"start": v(209.41, -9.41) * mm, "mid": v(209.41, -6.59) * mm, "end": v(206.59, -6.59) * mm});
            skCircle(sketch, "E52.8.0.22", {"center": v(208, -16) * mm, "radius": 2 * mm});
            skCircle(sketch, "E52.8.0.23", {"center": v(200, -16) * mm, "radius": 2 * mm});
            skLineSegment(sketch, "E52.8.0.24", {"start": v(206.1, -7.07) * mm, "end": v(206.59, -6.59) * mm});
            skCircle(sketch, "E52.8.0.25", {"center": v(204, 0) * mm, "radius": 2 * mm});
            skArc(sketch, "E52.8.0.26", {"start": v(218, -12) * mm, "mid": v(216, -10) * mm, "end": v(214, -12) * mm});
            skArc(sketch, "E52.8.0.27", {"start": v(214, -16) * mm, "mid": v(216, -18) * mm, "end": v(218, -16) * mm});
            skLineSegment(sketch, "E52.8.0.28", {"start": v(214, -12) * mm, "end": v(214, -16) * mm});
            skLineSegment(sketch, "E52.8.0.29", {"start": v(218, -16) * mm, "end": v(218, -12) * mm});
            skArc(sketch, "E52.9.0.0", {"start": v(242, 16) * mm, "mid": v(240, 18) * mm, "end": v(238, 16) * mm});
            skLineSegment(sketch, "E52.9.0.1", {"start": v(242, 16) * mm, "end": v(242, 12) * mm});
            skLineSegment(sketch, "E52.9.0.2", {"start": v(238, 16) * mm, "end": v(238, 12) * mm});
            skArc(sketch, "E52.9.0.3", {"start": v(238, 12) * mm, "mid": v(240, 10) * mm, "end": v(242, 12) * mm});
            skCircle(sketch, "E52.9.0.4", {"center": v(232, 16) * mm, "radius": 2 * mm});
            skCircle(sketch, "E52.9.0.5", {"center": v(224, 16) * mm, "radius": 2 * mm});
            skArc(sketch, "E52.9.0.6", {"start": v(225.9, 7.07) * mm, "mid": v(225.9, 9.9) * mm, "end": v(223.07, 9.9) * mm});
            skArc(sketch, "E52.9.0.7", {"start": v(222.59, 9.41) * mm, "mid": v(222.59, 6.59) * mm, "end": v(225.41, 6.59) * mm});
            skLineSegment(sketch, "E52.9.0.8", {"start": v(223.07, 9.9) * mm, "end": v(222.59, 9.41) * mm});
            skLineSegment(sketch, "E52.9.0.9", {"start": v(225.9, 7.07) * mm, "end": v(225.41, 6.59) * mm});
            skArc(sketch, "E52.9.0.10", {"start": v(232.93, 9.9) * mm, "mid": v(230.1, 9.9) * mm, "end": v(230.1, 7.07) * mm});
            skLineSegment(sketch, "E52.9.0.11", {"start": v(232.93, 9.9) * mm, "end": v(233.41, 9.41) * mm});
            skArc(sketch, "E52.9.0.12", {"start": v(230.59, 6.59) * mm, "mid": v(233.41, 6.59) * mm, "end": v(233.41, 9.41) * mm});
            skLineSegment(sketch, "E52.9.0.13", {"start": v(230.1, 7.07) * mm, "end": v(230.59, 6.59) * mm});
            skCircle(sketch, "E52.9.0.14", {"center": v(240, 0) * mm, "radius": 7 * mm});
            skArc(sketch, "E52.9.0.15", {"start": v(223.07, -9.9) * mm, "mid": v(225.9, -9.9) * mm, "end": v(225.9, -7.07) * mm});
            skArc(sketch, "E52.9.0.16", {"start": v(225.41, -6.59) * mm, "mid": v(222.59, -6.59) * mm, "end": v(222.59, -9.41) * mm});
            skLineSegment(sketch, "E52.9.0.17", {"start": v(225.41, -6.59) * mm, "end": v(225.9, -7.07) * mm});
            skLineSegment(sketch, "E52.9.0.18", {"start": v(222.59, -9.41) * mm, "end": v(223.07, -9.9) * mm});
            skArc(sketch, "E52.9.0.19", {"start": v(230.1, -7.07) * mm, "mid": v(230.1, -9.9) * mm, "end": v(232.93, -9.9) * mm});
            skLineSegment(sketch, "E52.9.0.20", {"start": v(232.93, -9.9) * mm, "end": v(233.41, -9.41) * mm});
            skArc(sketch, "E52.9.0.21", {"start": v(233.41, -9.41) * mm, "mid": v(233.41, -6.59) * mm, "end": v(230.59, -6.59) * mm});
            skCircle(sketch, "E52.9.0.22", {"center": v(232, -16) * mm, "radius": 2 * mm});
            skCircle(sketch, "E52.9.0.23", {"center": v(224, -16) * mm, "radius": 2 * mm});
            skLineSegment(sketch, "E52.9.0.24", {"start": v(230.1, -7.07) * mm, "end": v(230.59, -6.59) * mm});
            skCircle(sketch, "E52.9.0.25", {"center": v(228, 0) * mm, "radius": 2 * mm});
            skArc(sketch, "E52.9.0.26", {"start": v(242, -12) * mm, "mid": v(240, -10) * mm, "end": v(238, -12) * mm});
            skArc(sketch, "E52.9.0.27", {"start": v(238, -16) * mm, "mid": v(240, -18) * mm, "end": v(242, -16) * mm});
            skLineSegment(sketch, "E52.9.0.28", {"start": v(238, -12) * mm, "end": v(238, -16) * mm});
            skLineSegment(sketch, "E52.9.0.29", {"start": v(242, -16) * mm, "end": v(242, -12) * mm});
            skArc(sketch, "E52.10.0.0", {"start": v(266, 16) * mm, "mid": v(264, 18) * mm, "end": v(262, 16) * mm});
            skLineSegment(sketch, "E52.10.0.1", {"start": v(266, 16) * mm, "end": v(266, 12) * mm});
            skLineSegment(sketch, "E52.10.0.2", {"start": v(262, 16) * mm, "end": v(262, 12) * mm});
            skArc(sketch, "E52.10.0.3", {"start": v(262, 12) * mm, "mid": v(264, 10) * mm, "end": v(266, 12) * mm});
            skCircle(sketch, "E52.10.0.4", {"center": v(256, 16) * mm, "radius": 2 * mm});
            skCircle(sketch, "E52.10.0.5", {"center": v(248, 16) * mm, "radius": 2 * mm});
            skArc(sketch, "E52.10.0.6", {"start": v(249.9, 7.07) * mm, "mid": v(249.9, 9.9) * mm, "end": v(247.07, 9.9) * mm});
            skArc(sketch, "E52.10.0.7", {"start": v(246.59, 9.41) * mm, "mid": v(246.59, 6.59) * mm, "end": v(249.41, 6.59) * mm});
            skLineSegment(sketch, "E52.10.0.8", {"start": v(247.07, 9.9) * mm, "end": v(246.59, 9.41) * mm});
            skLineSegment(sketch, "E52.10.0.9", {"start": v(249.9, 7.07) * mm, "end": v(249.41, 6.59) * mm});
            skArc(sketch, "E52.10.0.10", {"start": v(256.93, 9.9) * mm, "mid": v(254.1, 9.9) * mm, "end": v(254.1, 7.07) * mm});
            skLineSegment(sketch, "E52.10.0.11", {"start": v(256.93, 9.9) * mm, "end": v(257.41, 9.41) * mm});
            skArc(sketch, "E52.10.0.12", {"start": v(254.59, 6.59) * mm, "mid": v(257.41, 6.59) * mm, "end": v(257.41, 9.41) * mm});
            skLineSegment(sketch, "E52.10.0.13", {"start": v(254.1, 7.07) * mm, "end": v(254.59, 6.59) * mm});
            skCircle(sketch, "E52.10.0.14", {"center": v(264, 0) * mm, "radius": 7 * mm});
            skArc(sketch, "E52.10.0.15", {"start": v(247.07, -9.9) * mm, "mid": v(249.9, -9.9) * mm, "end": v(249.9, -7.07) * mm});
            skArc(sketch, "E52.10.0.16", {"start": v(249.41, -6.59) * mm, "mid": v(246.59, -6.59) * mm, "end": v(246.59, -9.41) * mm});
            skLineSegment(sketch, "E52.10.0.17", {"start": v(249.41, -6.59) * mm, "end": v(249.9, -7.07) * mm});
            skLineSegment(sketch, "E52.10.0.18", {"start": v(246.59, -9.41) * mm, "end": v(247.07, -9.9) * mm});
            skArc(sketch, "E52.10.0.19", {"start": v(254.1, -7.07) * mm, "mid": v(254.1, -9.9) * mm, "end": v(256.93, -9.9) * mm});
            skLineSegment(sketch, "E52.10.0.20", {"start": v(256.93, -9.9) * mm, "end": v(257.41, -9.41) * mm});
            skArc(sketch, "E52.10.0.21", {"start": v(257.41, -9.41) * mm, "mid": v(257.41, -6.59) * mm, "end": v(254.59, -6.59) * mm});
            skCircle(sketch, "E52.10.0.22", {"center": v(256, -16) * mm, "radius": 2 * mm});
            skCircle(sketch, "E52.10.0.23", {"center": v(248, -16) * mm, "radius": 2 * mm});
            skLineSegment(sketch, "E52.10.0.24", {"start": v(254.1, -7.07) * mm, "end": v(254.59, -6.59) * mm});
            skCircle(sketch, "E52.10.0.25", {"center": v(252, 0) * mm, "radius": 2 * mm});
            skArc(sketch, "E52.10.0.26", {"start": v(266, -12) * mm, "mid": v(264, -10) * mm, "end": v(262, -12) * mm});
            skArc(sketch, "E52.10.0.27", {"start": v(262, -16) * mm, "mid": v(264, -18) * mm, "end": v(266, -16) * mm});
            skLineSegment(sketch, "E52.10.0.28", {"start": v(262, -12) * mm, "end": v(262, -16) * mm});
            skLineSegment(sketch, "E52.10.0.29", {"start": v(266, -16) * mm, "end": v(266, -12) * mm});
            skArc(sketch, "E52.11.0.0", {"start": v(290, 16) * mm, "mid": v(288, 18) * mm, "end": v(286, 16) * mm});
            skLineSegment(sketch, "E52.11.0.1", {"start": v(290, 16) * mm, "end": v(290, 12) * mm});
            skLineSegment(sketch, "E52.11.0.2", {"start": v(286, 16) * mm, "end": v(286, 12) * mm});
            skArc(sketch, "E52.11.0.3", {"start": v(286, 12) * mm, "mid": v(288, 10) * mm, "end": v(290, 12) * mm});
            skCircle(sketch, "E52.11.0.4", {"center": v(280, 16) * mm, "radius": 2 * mm});
            skCircle(sketch, "E52.11.0.5", {"center": v(272, 16) * mm, "radius": 2 * mm});
            skArc(sketch, "E52.11.0.6", {"start": v(273.9, 7.07) * mm, "mid": v(273.9, 9.9) * mm, "end": v(271.07, 9.9) * mm});
            skArc(sketch, "E52.11.0.7", {"start": v(270.59, 9.41) * mm, "mid": v(270.59, 6.59) * mm, "end": v(273.41, 6.59) * mm});
            skLineSegment(sketch, "E52.11.0.8", {"start": v(271.07, 9.9) * mm, "end": v(270.59, 9.41) * mm});
            skLineSegment(sketch, "E52.11.0.9", {"start": v(273.9, 7.07) * mm, "end": v(273.41, 6.59) * mm});
            skArc(sketch, "E52.11.0.10", {"start": v(280.93, 9.9) * mm, "mid": v(278.1, 9.9) * mm, "end": v(278.1, 7.07) * mm});
            skLineSegment(sketch, "E52.11.0.11", {"start": v(280.93, 9.9) * mm, "end": v(281.41, 9.41) * mm});
            skArc(sketch, "E52.11.0.12", {"start": v(278.59, 6.59) * mm, "mid": v(281.41, 6.59) * mm, "end": v(281.41, 9.41) * mm});
            skLineSegment(sketch, "E52.11.0.13", {"start": v(278.1, 7.07) * mm, "end": v(278.59, 6.59) * mm});
            skCircle(sketch, "E52.11.0.14", {"center": v(288, 0) * mm, "radius": 7 * mm});
            skArc(sketch, "E52.11.0.15", {"start": v(271.07, -9.9) * mm, "mid": v(273.9, -9.9) * mm, "end": v(273.9, -7.07) * mm});
            skArc(sketch, "E52.11.0.16", {"start": v(273.41, -6.59) * mm, "mid": v(270.59, -6.59) * mm, "end": v(270.59, -9.41) * mm});
            skLineSegment(sketch, "E52.11.0.17", {"start": v(273.41, -6.59) * mm, "end": v(273.9, -7.07) * mm});
            skLineSegment(sketch, "E52.11.0.18", {"start": v(270.59, -9.41) * mm, "end": v(271.07, -9.9) * mm});
            skArc(sketch, "E52.11.0.19", {"start": v(278.1, -7.07) * mm, "mid": v(278.1, -9.9) * mm, "end": v(280.93, -9.9) * mm});
            skLineSegment(sketch, "E52.11.0.20", {"start": v(280.93, -9.9) * mm, "end": v(281.41, -9.41) * mm});
            skArc(sketch, "E52.11.0.21", {"start": v(281.41, -9.41) * mm, "mid": v(281.41, -6.59) * mm, "end": v(278.59, -6.59) * mm});
            skCircle(sketch, "E52.11.0.22", {"center": v(280, -16) * mm, "radius": 2 * mm});
            skCircle(sketch, "E52.11.0.23", {"center": v(272, -16) * mm, "radius": 2 * mm});
            skLineSegment(sketch, "E52.11.0.24", {"start": v(278.1, -7.07) * mm, "end": v(278.59, -6.59) * mm});
            skCircle(sketch, "E52.11.0.25", {"center": v(276, 0) * mm, "radius": 2 * mm});
            skArc(sketch, "E52.11.0.26", {"start": v(290, -12) * mm, "mid": v(288, -10) * mm, "end": v(286, -12) * mm});
            skArc(sketch, "E52.11.0.27", {"start": v(286, -16) * mm, "mid": v(288, -18) * mm, "end": v(290, -16) * mm});
            skLineSegment(sketch, "E52.11.0.28", {"start": v(286, -12) * mm, "end": v(286, -16) * mm});
            skLineSegment(sketch, "E52.11.0.29", {"start": v(290, -16) * mm, "end": v(290, -12) * mm});
            skArc(sketch, "E52.12.0.0", {"start": v(314, 16) * mm, "mid": v(312, 18) * mm, "end": v(310, 16) * mm});
            skLineSegment(sketch, "E52.12.0.1", {"start": v(314, 16) * mm, "end": v(314, 12) * mm});
            skLineSegment(sketch, "E52.12.0.2", {"start": v(310, 16) * mm, "end": v(310, 12) * mm});
            skArc(sketch, "E52.12.0.3", {"start": v(310, 12) * mm, "mid": v(312, 10) * mm, "end": v(314, 12) * mm});
            skCircle(sketch, "E52.12.0.4", {"center": v(304, 16) * mm, "radius": 2 * mm});
            skCircle(sketch, "E52.12.0.5", {"center": v(296, 16) * mm, "radius": 2 * mm});
            skArc(sketch, "E52.12.0.6", {"start": v(297.9, 7.07) * mm, "mid": v(297.9, 9.9) * mm, "end": v(295.07, 9.9) * mm});
            skArc(sketch, "E52.12.0.7", {"start": v(294.59, 9.41) * mm, "mid": v(294.59, 6.59) * mm, "end": v(297.41, 6.59) * mm});
            skLineSegment(sketch, "E52.12.0.8", {"start": v(295.07, 9.9) * mm, "end": v(294.59, 9.41) * mm});
            skLineSegment(sketch, "E52.12.0.9", {"start": v(297.9, 7.07) * mm, "end": v(297.41, 6.59) * mm});
            skArc(sketch, "E52.12.0.10", {"start": v(304.93, 9.9) * mm, "mid": v(302.1, 9.9) * mm, "end": v(302.1, 7.07) * mm});
            skLineSegment(sketch, "E52.12.0.11", {"start": v(304.93, 9.9) * mm, "end": v(305.41, 9.41) * mm});
            skArc(sketch, "E52.12.0.12", {"start": v(302.59, 6.59) * mm, "mid": v(305.41, 6.59) * mm, "end": v(305.41, 9.41) * mm});
            skLineSegment(sketch, "E52.12.0.13", {"start": v(302.1, 7.07) * mm, "end": v(302.59, 6.59) * mm});
            skCircle(sketch, "E52.12.0.14", {"center": v(312, 0) * mm, "radius": 7 * mm});
            skArc(sketch, "E52.12.0.15", {"start": v(295.07, -9.9) * mm, "mid": v(297.9, -9.9) * mm, "end": v(297.9, -7.07) * mm});
            skArc(sketch, "E52.12.0.16", {"start": v(297.41, -6.59) * mm, "mid": v(294.59, -6.59) * mm, "end": v(294.59, -9.41) * mm});
            skLineSegment(sketch, "E52.12.0.17", {"start": v(297.41, -6.59) * mm, "end": v(297.9, -7.07) * mm});
            skLineSegment(sketch, "E52.12.0.18", {"start": v(294.59, -9.41) * mm, "end": v(295.07, -9.9) * mm});
            skArc(sketch, "E52.12.0.19", {"start": v(302.1, -7.07) * mm, "mid": v(302.1, -9.9) * mm, "end": v(304.93, -9.9) * mm});
            skLineSegment(sketch, "E52.12.0.20", {"start": v(304.93, -9.9) * mm, "end": v(305.41, -9.41) * mm});
            skArc(sketch, "E52.12.0.21", {"start": v(305.41, -9.41) * mm, "mid": v(305.41, -6.59) * mm, "end": v(302.59, -6.59) * mm});
            skCircle(sketch, "E52.12.0.22", {"center": v(304, -16) * mm, "radius": 2 * mm});
            skCircle(sketch, "E52.12.0.23", {"center": v(296, -16) * mm, "radius": 2 * mm});
            skLineSegment(sketch, "E52.12.0.24", {"start": v(302.1, -7.07) * mm, "end": v(302.59, -6.59) * mm});
            skCircle(sketch, "E52.12.0.25", {"center": v(300, 0) * mm, "radius": 2 * mm});
            skArc(sketch, "E52.12.0.26", {"start": v(314, -12) * mm, "mid": v(312, -10) * mm, "end": v(310, -12) * mm});
            skArc(sketch, "E52.12.0.27", {"start": v(310, -16) * mm, "mid": v(312, -18) * mm, "end": v(314, -16) * mm});
            skLineSegment(sketch, "E52.12.0.28", {"start": v(310, -12) * mm, "end": v(310, -16) * mm});
            skLineSegment(sketch, "E52.12.0.29", {"start": v(314, -16) * mm, "end": v(314, -12) * mm});
            skArc(sketch, "E52.13.0.0", {"start": v(338, 16) * mm, "mid": v(336, 18) * mm, "end": v(334, 16) * mm});
            skLineSegment(sketch, "E52.13.0.1", {"start": v(338, 16) * mm, "end": v(338, 12) * mm});
            skLineSegment(sketch, "E52.13.0.2", {"start": v(334, 16) * mm, "end": v(334, 12) * mm});
            skArc(sketch, "E52.13.0.3", {"start": v(334, 12) * mm, "mid": v(336, 10) * mm, "end": v(338, 12) * mm});
            skCircle(sketch, "E52.13.0.4", {"center": v(328, 16) * mm, "radius": 2 * mm});
            skCircle(sketch, "E52.13.0.5", {"center": v(320, 16) * mm, "radius": 2 * mm});
            skArc(sketch, "E52.13.0.6", {"start": v(321.9, 7.07) * mm, "mid": v(321.9, 9.9) * mm, "end": v(319.07, 9.9) * mm});
            skArc(sketch, "E52.13.0.7", {"start": v(318.59, 9.41) * mm, "mid": v(318.59, 6.59) * mm, "end": v(321.41, 6.59) * mm});
            skLineSegment(sketch, "E52.13.0.8", {"start": v(319.07, 9.9) * mm, "end": v(318.59, 9.41) * mm});
            skLineSegment(sketch, "E52.13.0.9", {"start": v(321.9, 7.07) * mm, "end": v(321.41, 6.59) * mm});
            skArc(sketch, "E52.13.0.10", {"start": v(328.93, 9.9) * mm, "mid": v(326.1, 9.9) * mm, "end": v(326.1, 7.07) * mm});
            skLineSegment(sketch, "E52.13.0.11", {"start": v(328.93, 9.9) * mm, "end": v(329.41, 9.41) * mm});
            skArc(sketch, "E52.13.0.12", {"start": v(326.59, 6.59) * mm, "mid": v(329.41, 6.59) * mm, "end": v(329.41, 9.41) * mm});
            skLineSegment(sketch, "E52.13.0.13", {"start": v(326.1, 7.07) * mm, "end": v(326.59, 6.59) * mm});
            skCircle(sketch, "E52.13.0.14", {"center": v(336, 0) * mm, "radius": 7 * mm});
            skArc(sketch, "E52.13.0.15", {"start": v(319.07, -9.9) * mm, "mid": v(321.9, -9.9) * mm, "end": v(321.9, -7.07) * mm});
            skArc(sketch, "E52.13.0.16", {"start": v(321.41, -6.59) * mm, "mid": v(318.59, -6.59) * mm, "end": v(318.59, -9.41) * mm});
            skLineSegment(sketch, "E52.13.0.17", {"start": v(321.41, -6.59) * mm, "end": v(321.9, -7.07) * mm});
            skLineSegment(sketch, "E52.13.0.18", {"start": v(318.59, -9.41) * mm, "end": v(319.07, -9.9) * mm});
            skArc(sketch, "E52.13.0.19", {"start": v(326.1, -7.07) * mm, "mid": v(326.1, -9.9) * mm, "end": v(328.93, -9.9) * mm});
            skLineSegment(sketch, "E52.13.0.20", {"start": v(328.93, -9.9) * mm, "end": v(329.41, -9.41) * mm});
            skArc(sketch, "E52.13.0.21", {"start": v(329.41, -9.41) * mm, "mid": v(329.41, -6.59) * mm, "end": v(326.59, -6.59) * mm});
            skCircle(sketch, "E52.13.0.22", {"center": v(328, -16) * mm, "radius": 2 * mm});
            skCircle(sketch, "E52.13.0.23", {"center": v(320, -16) * mm, "radius": 2 * mm});
            skLineSegment(sketch, "E52.13.0.24", {"start": v(326.1, -7.07) * mm, "end": v(326.59, -6.59) * mm});
            skCircle(sketch, "E52.13.0.25", {"center": v(324, 0) * mm, "radius": 2 * mm});
            skArc(sketch, "E52.13.0.26", {"start": v(338, -12) * mm, "mid": v(336, -10) * mm, "end": v(334, -12) * mm});
            skArc(sketch, "E52.13.0.27", {"start": v(334, -16) * mm, "mid": v(336, -18) * mm, "end": v(338, -16) * mm});
            skLineSegment(sketch, "E52.13.0.28", {"start": v(334, -12) * mm, "end": v(334, -16) * mm});
            skLineSegment(sketch, "E52.13.0.29", {"start": v(338, -16) * mm, "end": v(338, -12) * mm});
            skArc(sketch, "E52.14.0.0", {"start": v(362, 16) * mm, "mid": v(360, 18) * mm, "end": v(358, 16) * mm});
            skLineSegment(sketch, "E52.14.0.1", {"start": v(362, 16) * mm, "end": v(362, 12) * mm});
            skLineSegment(sketch, "E52.14.0.2", {"start": v(358, 16) * mm, "end": v(358, 12) * mm});
            skArc(sketch, "E52.14.0.3", {"start": v(358, 12) * mm, "mid": v(360, 10) * mm, "end": v(362, 12) * mm});
            skCircle(sketch, "E52.14.0.4", {"center": v(352, 16) * mm, "radius": 2 * mm});
            skCircle(sketch, "E52.14.0.5", {"center": v(344, 16) * mm, "radius": 2 * mm});
            skArc(sketch, "E52.14.0.6", {"start": v(345.9, 7.07) * mm, "mid": v(345.9, 9.9) * mm, "end": v(343.07, 9.9) * mm});
            skArc(sketch, "E52.14.0.7", {"start": v(342.59, 9.41) * mm, "mid": v(342.59, 6.59) * mm, "end": v(345.41, 6.59) * mm});
            skLineSegment(sketch, "E52.14.0.8", {"start": v(343.07, 9.9) * mm, "end": v(342.59, 9.41) * mm});
            skLineSegment(sketch, "E52.14.0.9", {"start": v(345.9, 7.07) * mm, "end": v(345.41, 6.59) * mm});
            skArc(sketch, "E52.14.0.10", {"start": v(352.93, 9.9) * mm, "mid": v(350.1, 9.9) * mm, "end": v(350.1, 7.07) * mm});
            skLineSegment(sketch, "E52.14.0.11", {"start": v(352.93, 9.9) * mm, "end": v(353.41, 9.41) * mm});
            skArc(sketch, "E52.14.0.12", {"start": v(350.59, 6.59) * mm, "mid": v(353.41, 6.59) * mm, "end": v(353.41, 9.41) * mm});
            skLineSegment(sketch, "E52.14.0.13", {"start": v(350.1, 7.07) * mm, "end": v(350.59, 6.59) * mm});
            skCircle(sketch, "E52.14.0.14", {"center": v(360, 0) * mm, "radius": 7 * mm});
            skArc(sketch, "E52.14.0.15", {"start": v(343.07, -9.9) * mm, "mid": v(345.9, -9.9) * mm, "end": v(345.9, -7.07) * mm});
            skArc(sketch, "E52.14.0.16", {"start": v(345.41, -6.59) * mm, "mid": v(342.59, -6.59) * mm, "end": v(342.59, -9.41) * mm});
            skLineSegment(sketch, "E52.14.0.17", {"start": v(345.41, -6.59) * mm, "end": v(345.9, -7.07) * mm});
            skLineSegment(sketch, "E52.14.0.18", {"start": v(342.59, -9.41) * mm, "end": v(343.07, -9.9) * mm});
            skArc(sketch, "E52.14.0.19", {"start": v(350.1, -7.07) * mm, "mid": v(350.1, -9.9) * mm, "end": v(352.93, -9.9) * mm});
            skLineSegment(sketch, "E52.14.0.20", {"start": v(352.93, -9.9) * mm, "end": v(353.41, -9.41) * mm});
            skArc(sketch, "E52.14.0.21", {"start": v(353.41, -9.41) * mm, "mid": v(353.41, -6.59) * mm, "end": v(350.59, -6.59) * mm});
            skCircle(sketch, "E52.14.0.22", {"center": v(352, -16) * mm, "radius": 2 * mm});
            skCircle(sketch, "E52.14.0.23", {"center": v(344, -16) * mm, "radius": 2 * mm});
            skLineSegment(sketch, "E52.14.0.24", {"start": v(350.1, -7.07) * mm, "end": v(350.59, -6.59) * mm});
            skCircle(sketch, "E52.14.0.25", {"center": v(348, 0) * mm, "radius": 2 * mm});
            skArc(sketch, "E52.14.0.26", {"start": v(362, -12) * mm, "mid": v(360, -10) * mm, "end": v(358, -12) * mm});
            skArc(sketch, "E52.14.0.27", {"start": v(358, -16) * mm, "mid": v(360, -18) * mm, "end": v(362, -16) * mm});
            skLineSegment(sketch, "E52.14.0.28", {"start": v(358, -12) * mm, "end": v(358, -16) * mm});
            skLineSegment(sketch, "E52.14.0.29", {"start": v(362, -16) * mm, "end": v(362, -12) * mm});
            skArc(sketch, "E52.15.0.0", {"start": v(386, 16) * mm, "mid": v(384, 18) * mm, "end": v(382, 16) * mm});
            skLineSegment(sketch, "E52.15.0.1", {"start": v(386, 16) * mm, "end": v(386, 12) * mm});
            skLineSegment(sketch, "E52.15.0.2", {"start": v(382, 16) * mm, "end": v(382, 12) * mm});
            skArc(sketch, "E52.15.0.3", {"start": v(382, 12) * mm, "mid": v(384, 10) * mm, "end": v(386, 12) * mm});
            skCircle(sketch, "E52.15.0.4", {"center": v(376, 16) * mm, "radius": 2 * mm});
            skCircle(sketch, "E52.15.0.5", {"center": v(368, 16) * mm, "radius": 2 * mm});
            skArc(sketch, "E52.15.0.6", {"start": v(369.9, 7.07) * mm, "mid": v(369.9, 9.9) * mm, "end": v(367.07, 9.9) * mm});
            skArc(sketch, "E52.15.0.7", {"start": v(366.59, 9.41) * mm, "mid": v(366.59, 6.59) * mm, "end": v(369.41, 6.59) * mm});
            skLineSegment(sketch, "E52.15.0.8", {"start": v(367.07, 9.9) * mm, "end": v(366.59, 9.41) * mm});
            skLineSegment(sketch, "E52.15.0.9", {"start": v(369.9, 7.07) * mm, "end": v(369.41, 6.59) * mm});
            skArc(sketch, "E52.15.0.10", {"start": v(376.93, 9.9) * mm, "mid": v(374.1, 9.9) * mm, "end": v(374.1, 7.07) * mm});
            skLineSegment(sketch, "E52.15.0.11", {"start": v(376.93, 9.9) * mm, "end": v(377.41, 9.41) * mm});
            skArc(sketch, "E52.15.0.12", {"start": v(374.59, 6.59) * mm, "mid": v(377.41, 6.59) * mm, "end": v(377.41, 9.41) * mm});
            skLineSegment(sketch, "E52.15.0.13", {"start": v(374.1, 7.07) * mm, "end": v(374.59, 6.59) * mm});
            skCircle(sketch, "E52.15.0.14", {"center": v(384, 0) * mm, "radius": 7 * mm});
            skArc(sketch, "E52.15.0.15", {"start": v(367.07, -9.9) * mm, "mid": v(369.9, -9.9) * mm, "end": v(369.9, -7.07) * mm});
            skArc(sketch, "E52.15.0.16", {"start": v(369.41, -6.59) * mm, "mid": v(366.59, -6.59) * mm, "end": v(366.59, -9.41) * mm});
            skLineSegment(sketch, "E52.15.0.17", {"start": v(369.41, -6.59) * mm, "end": v(369.9, -7.07) * mm});
            skLineSegment(sketch, "E52.15.0.18", {"start": v(366.59, -9.41) * mm, "end": v(367.07, -9.9) * mm});
            skArc(sketch, "E52.15.0.19", {"start": v(374.1, -7.07) * mm, "mid": v(374.1, -9.9) * mm, "end": v(376.93, -9.9) * mm});
            skLineSegment(sketch, "E52.15.0.20", {"start": v(376.93, -9.9) * mm, "end": v(377.41, -9.41) * mm});
            skArc(sketch, "E52.15.0.21", {"start": v(377.41, -9.41) * mm, "mid": v(377.41, -6.59) * mm, "end": v(374.59, -6.59) * mm});
            skCircle(sketch, "E52.15.0.22", {"center": v(376, -16) * mm, "radius": 2 * mm});
            skCircle(sketch, "E52.15.0.23", {"center": v(368, -16) * mm, "radius": 2 * mm});
            skLineSegment(sketch, "E52.15.0.24", {"start": v(374.1, -7.07) * mm, "end": v(374.59, -6.59) * mm});
            skCircle(sketch, "E52.15.0.25", {"center": v(372, 0) * mm, "radius": 2 * mm});
            skArc(sketch, "E52.15.0.26", {"start": v(386, -12) * mm, "mid": v(384, -10) * mm, "end": v(382, -12) * mm});
            skArc(sketch, "E52.15.0.27", {"start": v(382, -16) * mm, "mid": v(384, -18) * mm, "end": v(386, -16) * mm});
            skLineSegment(sketch, "E52.15.0.28", {"start": v(382, -12) * mm, "end": v(382, -16) * mm});
            skLineSegment(sketch, "E52.15.0.29", {"start": v(386, -16) * mm, "end": v(386, -12) * mm});
            skArc(sketch, "E52.16.0.0", {"start": v(410, 16) * mm, "mid": v(408, 18) * mm, "end": v(406, 16) * mm});
            skLineSegment(sketch, "E52.16.0.1", {"start": v(410, 16) * mm, "end": v(410, 12) * mm});
            skLineSegment(sketch, "E52.16.0.2", {"start": v(406, 16) * mm, "end": v(406, 12) * mm});
            skArc(sketch, "E52.16.0.3", {"start": v(406, 12) * mm, "mid": v(408, 10) * mm, "end": v(410, 12) * mm});
            skCircle(sketch, "E52.16.0.4", {"center": v(400, 16) * mm, "radius": 2 * mm});
            skCircle(sketch, "E52.16.0.5", {"center": v(392, 16) * mm, "radius": 2 * mm});
            skArc(sketch, "E52.16.0.6", {"start": v(393.9, 7.07) * mm, "mid": v(393.9, 9.9) * mm, "end": v(391.07, 9.9) * mm});
            skArc(sketch, "E52.16.0.7", {"start": v(390.59, 9.41) * mm, "mid": v(390.59, 6.59) * mm, "end": v(393.41, 6.59) * mm});
            skLineSegment(sketch, "E52.16.0.8", {"start": v(391.07, 9.9) * mm, "end": v(390.59, 9.41) * mm});
            skLineSegment(sketch, "E52.16.0.9", {"start": v(393.9, 7.07) * mm, "end": v(393.41, 6.59) * mm});
            skArc(sketch, "E52.16.0.10", {"start": v(400.93, 9.9) * mm, "mid": v(398.1, 9.9) * mm, "end": v(398.1, 7.07) * mm});
            skLineSegment(sketch, "E52.16.0.11", {"start": v(400.93, 9.9) * mm, "end": v(401.41, 9.41) * mm});
            skArc(sketch, "E52.16.0.12", {"start": v(398.59, 6.59) * mm, "mid": v(401.41, 6.59) * mm, "end": v(401.41, 9.41) * mm});
            skLineSegment(sketch, "E52.16.0.13", {"start": v(398.1, 7.07) * mm, "end": v(398.59, 6.59) * mm});
            skCircle(sketch, "E52.16.0.14", {"center": v(408, 0) * mm, "radius": 7 * mm});
            skArc(sketch, "E52.16.0.15", {"start": v(391.07, -9.9) * mm, "mid": v(393.9, -9.9) * mm, "end": v(393.9, -7.07) * mm});
            skArc(sketch, "E52.16.0.16", {"start": v(393.41, -6.59) * mm, "mid": v(390.59, -6.59) * mm, "end": v(390.59, -9.41) * mm});
            skLineSegment(sketch, "E52.16.0.17", {"start": v(393.41, -6.59) * mm, "end": v(393.9, -7.07) * mm});
            skLineSegment(sketch, "E52.16.0.18", {"start": v(390.59, -9.41) * mm, "end": v(391.07, -9.9) * mm});
            skArc(sketch, "E52.16.0.19", {"start": v(398.1, -7.07) * mm, "mid": v(398.1, -9.9) * mm, "end": v(400.93, -9.9) * mm});
            skLineSegment(sketch, "E52.16.0.20", {"start": v(400.93, -9.9) * mm, "end": v(401.41, -9.41) * mm});
            skArc(sketch, "E52.16.0.21", {"start": v(401.41, -9.41) * mm, "mid": v(401.41, -6.59) * mm, "end": v(398.59, -6.59) * mm});
            skCircle(sketch, "E52.16.0.22", {"center": v(400, -16) * mm, "radius": 2 * mm});
            skCircle(sketch, "E52.16.0.23", {"center": v(392, -16) * mm, "radius": 2 * mm});
            skLineSegment(sketch, "E52.16.0.24", {"start": v(398.1, -7.07) * mm, "end": v(398.59, -6.59) * mm});
            skCircle(sketch, "E52.16.0.25", {"center": v(396, 0) * mm, "radius": 2 * mm});
            skArc(sketch, "E52.16.0.26", {"start": v(410, -12) * mm, "mid": v(408, -10) * mm, "end": v(406, -12) * mm});
            skArc(sketch, "E52.16.0.27", {"start": v(406, -16) * mm, "mid": v(408, -18) * mm, "end": v(410, -16) * mm});
            skLineSegment(sketch, "E52.16.0.28", {"start": v(406, -12) * mm, "end": v(406, -16) * mm});
            skLineSegment(sketch, "E52.16.0.29", {"start": v(410, -16) * mm, "end": v(410, -12) * mm});
            skArc(sketch, "E52.17.0.0", {"start": v(434, 16) * mm, "mid": v(432, 18) * mm, "end": v(430, 16) * mm});
            skLineSegment(sketch, "E52.17.0.1", {"start": v(434, 16) * mm, "end": v(434, 12) * mm});
            skLineSegment(sketch, "E52.17.0.2", {"start": v(430, 16) * mm, "end": v(430, 12) * mm});
            skArc(sketch, "E52.17.0.3", {"start": v(430, 12) * mm, "mid": v(432, 10) * mm, "end": v(434, 12) * mm});
            skCircle(sketch, "E52.17.0.4", {"center": v(424, 16) * mm, "radius": 2 * mm});
            skCircle(sketch, "E52.17.0.5", {"center": v(416, 16) * mm, "radius": 2 * mm});
            skArc(sketch, "E52.17.0.6", {"start": v(417.9, 7.07) * mm, "mid": v(417.9, 9.9) * mm, "end": v(415.07, 9.9) * mm});
            skArc(sketch, "E52.17.0.7", {"start": v(414.59, 9.41) * mm, "mid": v(414.59, 6.59) * mm, "end": v(417.41, 6.59) * mm});
            skLineSegment(sketch, "E52.17.0.8", {"start": v(415.07, 9.9) * mm, "end": v(414.59, 9.41) * mm});
            skLineSegment(sketch, "E52.17.0.9", {"start": v(417.9, 7.07) * mm, "end": v(417.41, 6.59) * mm});
            skArc(sketch, "E52.17.0.10", {"start": v(424.93, 9.9) * mm, "mid": v(422.1, 9.9) * mm, "end": v(422.1, 7.07) * mm});
            skLineSegment(sketch, "E52.17.0.11", {"start": v(424.93, 9.9) * mm, "end": v(425.41, 9.41) * mm});
            skArc(sketch, "E52.17.0.12", {"start": v(422.59, 6.59) * mm, "mid": v(425.41, 6.59) * mm, "end": v(425.41, 9.41) * mm});
            skLineSegment(sketch, "E52.17.0.13", {"start": v(422.1, 7.07) * mm, "end": v(422.59, 6.59) * mm});
            skCircle(sketch, "E52.17.0.14", {"center": v(432, 0) * mm, "radius": 7 * mm});
            skArc(sketch, "E52.17.0.15", {"start": v(415.07, -9.9) * mm, "mid": v(417.9, -9.9) * mm, "end": v(417.9, -7.07) * mm});
            skArc(sketch, "E52.17.0.16", {"start": v(417.41, -6.59) * mm, "mid": v(414.59, -6.59) * mm, "end": v(414.59, -9.41) * mm});
            skLineSegment(sketch, "E52.17.0.17", {"start": v(417.41, -6.59) * mm, "end": v(417.9, -7.07) * mm});
            skLineSegment(sketch, "E52.17.0.18", {"start": v(414.59, -9.41) * mm, "end": v(415.07, -9.9) * mm});
            skArc(sketch, "E52.17.0.19", {"start": v(422.1, -7.07) * mm, "mid": v(422.1, -9.9) * mm, "end": v(424.93, -9.9) * mm});
            skLineSegment(sketch, "E52.17.0.20", {"start": v(424.93, -9.9) * mm, "end": v(425.41, -9.41) * mm});
            skArc(sketch, "E52.17.0.21", {"start": v(425.41, -9.41) * mm, "mid": v(425.41, -6.59) * mm, "end": v(422.59, -6.59) * mm});
            skCircle(sketch, "E52.17.0.22", {"center": v(424, -16) * mm, "radius": 2 * mm});
            skCircle(sketch, "E52.17.0.23", {"center": v(416, -16) * mm, "radius": 2 * mm});
            skLineSegment(sketch, "E52.17.0.24", {"start": v(422.1, -7.07) * mm, "end": v(422.59, -6.59) * mm});
            skCircle(sketch, "E52.17.0.25", {"center": v(420, 0) * mm, "radius": 2 * mm});
            skArc(sketch, "E52.17.0.26", {"start": v(434, -12) * mm, "mid": v(432, -10) * mm, "end": v(430, -12) * mm});
            skArc(sketch, "E52.17.0.27", {"start": v(430, -16) * mm, "mid": v(432, -18) * mm, "end": v(434, -16) * mm});
            skLineSegment(sketch, "E52.17.0.28", {"start": v(430, -12) * mm, "end": v(430, -16) * mm});
            skLineSegment(sketch, "E52.17.0.29", {"start": v(434, -16) * mm, "end": v(434, -12) * mm});
            skArc(sketch, "E52.18.0.0", {"start": v(458, 16) * mm, "mid": v(456, 18) * mm, "end": v(454, 16) * mm});
            skLineSegment(sketch, "E52.18.0.1", {"start": v(458, 16) * mm, "end": v(458, 12) * mm});
            skLineSegment(sketch, "E52.18.0.2", {"start": v(454, 16) * mm, "end": v(454, 12) * mm});
            skArc(sketch, "E52.18.0.3", {"start": v(454, 12) * mm, "mid": v(456, 10) * mm, "end": v(458, 12) * mm});
            skCircle(sketch, "E52.18.0.4", {"center": v(448, 16) * mm, "radius": 2 * mm});
            skCircle(sketch, "E52.18.0.5", {"center": v(440, 16) * mm, "radius": 2 * mm});
            skArc(sketch, "E52.18.0.6", {"start": v(441.9, 7.07) * mm, "mid": v(441.9, 9.9) * mm, "end": v(439.07, 9.9) * mm});
            skArc(sketch, "E52.18.0.7", {"start": v(438.59, 9.41) * mm, "mid": v(438.59, 6.59) * mm, "end": v(441.41, 6.59) * mm});
            skLineSegment(sketch, "E52.18.0.8", {"start": v(439.07, 9.9) * mm, "end": v(438.59, 9.41) * mm});
            skLineSegment(sketch, "E52.18.0.9", {"start": v(441.9, 7.07) * mm, "end": v(441.41, 6.59) * mm});
            skArc(sketch, "E52.18.0.10", {"start": v(448.93, 9.9) * mm, "mid": v(446.1, 9.9) * mm, "end": v(446.1, 7.07) * mm});
            skLineSegment(sketch, "E52.18.0.11", {"start": v(448.93, 9.9) * mm, "end": v(449.41, 9.41) * mm});
            skArc(sketch, "E52.18.0.12", {"start": v(446.59, 6.59) * mm, "mid": v(449.41, 6.59) * mm, "end": v(449.41, 9.41) * mm});
            skLineSegment(sketch, "E52.18.0.13", {"start": v(446.1, 7.07) * mm, "end": v(446.59, 6.59) * mm});
            skCircle(sketch, "E52.18.0.14", {"center": v(456, 0) * mm, "radius": 7 * mm});
            skArc(sketch, "E52.18.0.15", {"start": v(439.07, -9.9) * mm, "mid": v(441.9, -9.9) * mm, "end": v(441.9, -7.07) * mm});
            skArc(sketch, "E52.18.0.16", {"start": v(441.41, -6.59) * mm, "mid": v(438.59, -6.59) * mm, "end": v(438.59, -9.41) * mm});
            skLineSegment(sketch, "E52.18.0.17", {"start": v(441.41, -6.59) * mm, "end": v(441.9, -7.07) * mm});
            skLineSegment(sketch, "E52.18.0.18", {"start": v(438.59, -9.41) * mm, "end": v(439.07, -9.9) * mm});
            skArc(sketch, "E52.18.0.19", {"start": v(446.1, -7.07) * mm, "mid": v(446.1, -9.9) * mm, "end": v(448.93, -9.9) * mm});
            skLineSegment(sketch, "E52.18.0.20", {"start": v(448.93, -9.9) * mm, "end": v(449.41, -9.41) * mm});
            skArc(sketch, "E52.18.0.21", {"start": v(449.41, -9.41) * mm, "mid": v(449.41, -6.59) * mm, "end": v(446.59, -6.59) * mm});
            skCircle(sketch, "E52.18.0.22", {"center": v(448, -16) * mm, "radius": 2 * mm});
            skCircle(sketch, "E52.18.0.23", {"center": v(440, -16) * mm, "radius": 2 * mm});
            skLineSegment(sketch, "E52.18.0.24", {"start": v(446.1, -7.07) * mm, "end": v(446.59, -6.59) * mm});
            skCircle(sketch, "E52.18.0.25", {"center": v(444, 0) * mm, "radius": 2 * mm});
            skArc(sketch, "E52.18.0.26", {"start": v(458, -12) * mm, "mid": v(456, -10) * mm, "end": v(454, -12) * mm});
            skArc(sketch, "E52.18.0.27", {"start": v(454, -16) * mm, "mid": v(456, -18) * mm, "end": v(458, -16) * mm});
            skLineSegment(sketch, "E52.18.0.28", {"start": v(454, -12) * mm, "end": v(454, -16) * mm});
            skLineSegment(sketch, "E52.18.0.29", {"start": v(458, -16) * mm, "end": v(458, -12) * mm});
            skArc(sketch, "E52.19.0.0", {"start": v(482, 16) * mm, "mid": v(480, 18) * mm, "end": v(478, 16) * mm});
            skLineSegment(sketch, "E52.19.0.1", {"start": v(482, 16) * mm, "end": v(482, 12) * mm});
            skLineSegment(sketch, "E52.19.0.2", {"start": v(478, 16) * mm, "end": v(478, 12) * mm});
            skArc(sketch, "E52.19.0.3", {"start": v(478, 12) * mm, "mid": v(480, 10) * mm, "end": v(482, 12) * mm});
            skCircle(sketch, "E52.19.0.4", {"center": v(472, 16) * mm, "radius": 2 * mm});
            skCircle(sketch, "E52.19.0.5", {"center": v(464, 16) * mm, "radius": 2 * mm});
            skArc(sketch, "E52.19.0.6", {"start": v(465.9, 7.07) * mm, "mid": v(465.9, 9.9) * mm, "end": v(463.07, 9.9) * mm});
            skArc(sketch, "E52.19.0.7", {"start": v(462.59, 9.41) * mm, "mid": v(462.59, 6.59) * mm, "end": v(465.41, 6.59) * mm});
            skLineSegment(sketch, "E52.19.0.8", {"start": v(463.07, 9.9) * mm, "end": v(462.59, 9.41) * mm});
            skLineSegment(sketch, "E52.19.0.9", {"start": v(465.9, 7.07) * mm, "end": v(465.41, 6.59) * mm});
            skArc(sketch, "E52.19.0.10", {"start": v(472.93, 9.9) * mm, "mid": v(470.1, 9.9) * mm, "end": v(470.1, 7.07) * mm});
            skLineSegment(sketch, "E52.19.0.11", {"start": v(472.93, 9.9) * mm, "end": v(473.41, 9.41) * mm});
            skArc(sketch, "E52.19.0.12", {"start": v(470.59, 6.59) * mm, "mid": v(473.41, 6.59) * mm, "end": v(473.41, 9.41) * mm});
            skLineSegment(sketch, "E52.19.0.13", {"start": v(470.1, 7.07) * mm, "end": v(470.59, 6.59) * mm});
            skCircle(sketch, "E52.19.0.14", {"center": v(480, 0) * mm, "radius": 7 * mm});
            skArc(sketch, "E52.19.0.15", {"start": v(463.07, -9.9) * mm, "mid": v(465.9, -9.9) * mm, "end": v(465.9, -7.07) * mm});
            skArc(sketch, "E52.19.0.16", {"start": v(465.41, -6.59) * mm, "mid": v(462.59, -6.59) * mm, "end": v(462.59, -9.41) * mm});
            skLineSegment(sketch, "E52.19.0.17", {"start": v(465.41, -6.59) * mm, "end": v(465.9, -7.07) * mm});
            skLineSegment(sketch, "E52.19.0.18", {"start": v(462.59, -9.41) * mm, "end": v(463.07, -9.9) * mm});
            skArc(sketch, "E52.19.0.19", {"start": v(470.1, -7.07) * mm, "mid": v(470.1, -9.9) * mm, "end": v(472.93, -9.9) * mm});
            skLineSegment(sketch, "E52.19.0.20", {"start": v(472.93, -9.9) * mm, "end": v(473.41, -9.41) * mm});
            skArc(sketch, "E52.19.0.21", {"start": v(473.41, -9.41) * mm, "mid": v(473.41, -6.59) * mm, "end": v(470.59, -6.59) * mm});
            skCircle(sketch, "E52.19.0.22", {"center": v(472, -16) * mm, "radius": 2 * mm});
            skCircle(sketch, "E52.19.0.23", {"center": v(464, -16) * mm, "radius": 2 * mm});
            skLineSegment(sketch, "E52.19.0.24", {"start": v(470.1, -7.07) * mm, "end": v(470.59, -6.59) * mm});
            skCircle(sketch, "E52.19.0.25", {"center": v(468, 0) * mm, "radius": 2 * mm});
            skArc(sketch, "E52.19.0.26", {"start": v(482, -12) * mm, "mid": v(480, -10) * mm, "end": v(478, -12) * mm});
            skArc(sketch, "E52.19.0.27", {"start": v(478, -16) * mm, "mid": v(480, -18) * mm, "end": v(482, -16) * mm});
            skLineSegment(sketch, "E52.19.0.28", {"start": v(478, -12) * mm, "end": v(478, -16) * mm});
            skLineSegment(sketch, "E52.19.0.29", {"start": v(482, -16) * mm, "end": v(482, -12) * mm});
            skArc(sketch, "E52.20.0.0", {"start": v(506, 16) * mm, "mid": v(504, 18) * mm, "end": v(502, 16) * mm});
            skLineSegment(sketch, "E52.20.0.1", {"start": v(506, 16) * mm, "end": v(506, 12) * mm});
            skLineSegment(sketch, "E52.20.0.2", {"start": v(502, 16) * mm, "end": v(502, 12) * mm});
            skArc(sketch, "E52.20.0.3", {"start": v(502, 12) * mm, "mid": v(504, 10) * mm, "end": v(506, 12) * mm});
            skCircle(sketch, "E52.20.0.4", {"center": v(496, 16) * mm, "radius": 2 * mm});
            skCircle(sketch, "E52.20.0.5", {"center": v(488, 16) * mm, "radius": 2 * mm});
            skArc(sketch, "E52.20.0.6", {"start": v(489.9, 7.07) * mm, "mid": v(489.9, 9.9) * mm, "end": v(487.07, 9.9) * mm});
            skArc(sketch, "E52.20.0.7", {"start": v(486.59, 9.41) * mm, "mid": v(486.59, 6.59) * mm, "end": v(489.41, 6.59) * mm});
            skLineSegment(sketch, "E52.20.0.8", {"start": v(487.07, 9.9) * mm, "end": v(486.59, 9.41) * mm});
            skLineSegment(sketch, "E52.20.0.9", {"start": v(489.9, 7.07) * mm, "end": v(489.41, 6.59) * mm});
            skArc(sketch, "E52.20.0.10", {"start": v(496.93, 9.9) * mm, "mid": v(494.1, 9.9) * mm, "end": v(494.1, 7.07) * mm});
            skLineSegment(sketch, "E52.20.0.11", {"start": v(496.93, 9.9) * mm, "end": v(497.41, 9.41) * mm});
            skArc(sketch, "E52.20.0.12", {"start": v(494.59, 6.59) * mm, "mid": v(497.41, 6.59) * mm, "end": v(497.41, 9.41) * mm});
            skLineSegment(sketch, "E52.20.0.13", {"start": v(494.1, 7.07) * mm, "end": v(494.59, 6.59) * mm});
            skCircle(sketch, "E52.20.0.14", {"center": v(504, 0) * mm, "radius": 7 * mm});
            skArc(sketch, "E52.20.0.15", {"start": v(487.07, -9.9) * mm, "mid": v(489.9, -9.9) * mm, "end": v(489.9, -7.07) * mm});
            skArc(sketch, "E52.20.0.16", {"start": v(489.41, -6.59) * mm, "mid": v(486.59, -6.59) * mm, "end": v(486.59, -9.41) * mm});
            skLineSegment(sketch, "E52.20.0.17", {"start": v(489.41, -6.59) * mm, "end": v(489.9, -7.07) * mm});
            skLineSegment(sketch, "E52.20.0.18", {"start": v(486.59, -9.41) * mm, "end": v(487.07, -9.9) * mm});
            skArc(sketch, "E52.20.0.19", {"start": v(494.1, -7.07) * mm, "mid": v(494.1, -9.9) * mm, "end": v(496.93, -9.9) * mm});
            skLineSegment(sketch, "E52.20.0.20", {"start": v(496.93, -9.9) * mm, "end": v(497.41, -9.41) * mm});
            skArc(sketch, "E52.20.0.21", {"start": v(497.41, -9.41) * mm, "mid": v(497.41, -6.59) * mm, "end": v(494.59, -6.59) * mm});
            skCircle(sketch, "E52.20.0.22", {"center": v(496, -16) * mm, "radius": 2 * mm});
            skCircle(sketch, "E52.20.0.23", {"center": v(488, -16) * mm, "radius": 2 * mm});
            skLineSegment(sketch, "E52.20.0.24", {"start": v(494.1, -7.07) * mm, "end": v(494.59, -6.59) * mm});
            skCircle(sketch, "E52.20.0.25", {"center": v(492, 0) * mm, "radius": 2 * mm});
            skArc(sketch, "E52.20.0.26", {"start": v(506, -12) * mm, "mid": v(504, -10) * mm, "end": v(502, -12) * mm});
            skArc(sketch, "E52.20.0.27", {"start": v(502, -16) * mm, "mid": v(504, -18) * mm, "end": v(506, -16) * mm});
            skLineSegment(sketch, "E52.20.0.28", {"start": v(502, -12) * mm, "end": v(502, -16) * mm});
            skLineSegment(sketch, "E52.20.0.29", {"start": v(506, -16) * mm, "end": v(506, -12) * mm});
            skArc(sketch, "E52.21.0.0", {"start": v(530, 16) * mm, "mid": v(528, 18) * mm, "end": v(526, 16) * mm});
            skLineSegment(sketch, "E52.21.0.1", {"start": v(530, 16) * mm, "end": v(530, 12) * mm});
            skLineSegment(sketch, "E52.21.0.2", {"start": v(526, 16) * mm, "end": v(526, 12) * mm});
            skArc(sketch, "E52.21.0.3", {"start": v(526, 12) * mm, "mid": v(528, 10) * mm, "end": v(530, 12) * mm});
            skCircle(sketch, "E52.21.0.4", {"center": v(520, 16) * mm, "radius": 2 * mm});
            skCircle(sketch, "E52.21.0.5", {"center": v(512, 16) * mm, "radius": 2 * mm});
            skArc(sketch, "E52.21.0.6", {"start": v(513.9, 7.07) * mm, "mid": v(513.9, 9.9) * mm, "end": v(511.07, 9.9) * mm});
            skArc(sketch, "E52.21.0.7", {"start": v(510.59, 9.41) * mm, "mid": v(510.59, 6.59) * mm, "end": v(513.41, 6.59) * mm});
            skLineSegment(sketch, "E52.21.0.8", {"start": v(511.07, 9.9) * mm, "end": v(510.59, 9.41) * mm});
            skLineSegment(sketch, "E52.21.0.9", {"start": v(513.9, 7.07) * mm, "end": v(513.41, 6.59) * mm});
            skArc(sketch, "E52.21.0.10", {"start": v(520.93, 9.9) * mm, "mid": v(518.1, 9.9) * mm, "end": v(518.1, 7.07) * mm});
            skLineSegment(sketch, "E52.21.0.11", {"start": v(520.93, 9.9) * mm, "end": v(521.41, 9.41) * mm});
            skArc(sketch, "E52.21.0.12", {"start": v(518.59, 6.59) * mm, "mid": v(521.41, 6.59) * mm, "end": v(521.41, 9.41) * mm});
            skLineSegment(sketch, "E52.21.0.13", {"start": v(518.1, 7.07) * mm, "end": v(518.59, 6.59) * mm});
            skCircle(sketch, "E52.21.0.14", {"center": v(528, 0) * mm, "radius": 7 * mm});
            skArc(sketch, "E52.21.0.15", {"start": v(511.07, -9.9) * mm, "mid": v(513.9, -9.9) * mm, "end": v(513.9, -7.07) * mm});
            skArc(sketch, "E52.21.0.16", {"start": v(513.41, -6.59) * mm, "mid": v(510.59, -6.59) * mm, "end": v(510.59, -9.41) * mm});
            skLineSegment(sketch, "E52.21.0.17", {"start": v(513.41, -6.59) * mm, "end": v(513.9, -7.07) * mm});
            skLineSegment(sketch, "E52.21.0.18", {"start": v(510.59, -9.41) * mm, "end": v(511.07, -9.9) * mm});
            skArc(sketch, "E52.21.0.19", {"start": v(518.1, -7.07) * mm, "mid": v(518.1, -9.9) * mm, "end": v(520.93, -9.9) * mm});
            skLineSegment(sketch, "E52.21.0.20", {"start": v(520.93, -9.9) * mm, "end": v(521.41, -9.41) * mm});
            skArc(sketch, "E52.21.0.21", {"start": v(521.41, -9.41) * mm, "mid": v(521.41, -6.59) * mm, "end": v(518.59, -6.59) * mm});
            skCircle(sketch, "E52.21.0.22", {"center": v(520, -16) * mm, "radius": 2 * mm});
            skCircle(sketch, "E52.21.0.23", {"center": v(512, -16) * mm, "radius": 2 * mm});
            skLineSegment(sketch, "E52.21.0.24", {"start": v(518.1, -7.07) * mm, "end": v(518.59, -6.59) * mm});
            skCircle(sketch, "E52.21.0.25", {"center": v(516, 0) * mm, "radius": 2 * mm});
            skArc(sketch, "E52.21.0.26", {"start": v(530, -12) * mm, "mid": v(528, -10) * mm, "end": v(526, -12) * mm});
            skArc(sketch, "E52.21.0.27", {"start": v(526, -16) * mm, "mid": v(528, -18) * mm, "end": v(530, -16) * mm});
            skLineSegment(sketch, "E52.21.0.28", {"start": v(526, -12) * mm, "end": v(526, -16) * mm});
            skLineSegment(sketch, "E52.21.0.29", {"start": v(530, -16) * mm, "end": v(530, -12) * mm});
            skArc(sketch, "E52.22.0.0", {"start": v(554, 16) * mm, "mid": v(552, 18) * mm, "end": v(550, 16) * mm});
            skLineSegment(sketch, "E52.22.0.1", {"start": v(554, 16) * mm, "end": v(554, 12) * mm});
            skLineSegment(sketch, "E52.22.0.2", {"start": v(550, 16) * mm, "end": v(550, 12) * mm});
            skArc(sketch, "E52.22.0.3", {"start": v(550, 12) * mm, "mid": v(552, 10) * mm, "end": v(554, 12) * mm});
            skCircle(sketch, "E52.22.0.4", {"center": v(544, 16) * mm, "radius": 2 * mm});
            skCircle(sketch, "E52.22.0.5", {"center": v(536, 16) * mm, "radius": 2 * mm});
            skArc(sketch, "E52.22.0.6", {"start": v(537.9, 7.07) * mm, "mid": v(537.9, 9.9) * mm, "end": v(535.07, 9.9) * mm});
            skArc(sketch, "E52.22.0.7", {"start": v(534.59, 9.41) * mm, "mid": v(534.59, 6.59) * mm, "end": v(537.41, 6.59) * mm});
            skLineSegment(sketch, "E52.22.0.8", {"start": v(535.07, 9.9) * mm, "end": v(534.59, 9.41) * mm});
            skLineSegment(sketch, "E52.22.0.9", {"start": v(537.9, 7.07) * mm, "end": v(537.41, 6.59) * mm});
            skArc(sketch, "E52.22.0.10", {"start": v(544.93, 9.9) * mm, "mid": v(542.1, 9.9) * mm, "end": v(542.1, 7.07) * mm});
            skLineSegment(sketch, "E52.22.0.11", {"start": v(544.93, 9.9) * mm, "end": v(545.41, 9.41) * mm});
            skArc(sketch, "E52.22.0.12", {"start": v(542.59, 6.59) * mm, "mid": v(545.41, 6.59) * mm, "end": v(545.41, 9.41) * mm});
            skLineSegment(sketch, "E52.22.0.13", {"start": v(542.1, 7.07) * mm, "end": v(542.59, 6.59) * mm});
            skCircle(sketch, "E52.22.0.14", {"center": v(552, 0) * mm, "radius": 7 * mm});
            skArc(sketch, "E52.22.0.15", {"start": v(535.07, -9.9) * mm, "mid": v(537.9, -9.9) * mm, "end": v(537.9, -7.07) * mm});
            skArc(sketch, "E52.22.0.16", {"start": v(537.41, -6.59) * mm, "mid": v(534.59, -6.59) * mm, "end": v(534.59, -9.41) * mm});
            skLineSegment(sketch, "E52.22.0.17", {"start": v(537.41, -6.59) * mm, "end": v(537.9, -7.07) * mm});
            skLineSegment(sketch, "E52.22.0.18", {"start": v(534.59, -9.41) * mm, "end": v(535.07, -9.9) * mm});
            skArc(sketch, "E52.22.0.19", {"start": v(542.1, -7.07) * mm, "mid": v(542.1, -9.9) * mm, "end": v(544.93, -9.9) * mm});
            skLineSegment(sketch, "E52.22.0.20", {"start": v(544.93, -9.9) * mm, "end": v(545.41, -9.41) * mm});
            skArc(sketch, "E52.22.0.21", {"start": v(545.41, -9.41) * mm, "mid": v(545.41, -6.59) * mm, "end": v(542.59, -6.59) * mm});
            skCircle(sketch, "E52.22.0.22", {"center": v(544, -16) * mm, "radius": 2 * mm});
            skCircle(sketch, "E52.22.0.23", {"center": v(536, -16) * mm, "radius": 2 * mm});
            skLineSegment(sketch, "E52.22.0.24", {"start": v(542.1, -7.07) * mm, "end": v(542.59, -6.59) * mm});
            skCircle(sketch, "E52.22.0.25", {"center": v(540, 0) * mm, "radius": 2 * mm});
            skArc(sketch, "E52.22.0.26", {"start": v(554, -12) * mm, "mid": v(552, -10) * mm, "end": v(550, -12) * mm});
            skArc(sketch, "E52.22.0.27", {"start": v(550, -16) * mm, "mid": v(552, -18) * mm, "end": v(554, -16) * mm});
            skLineSegment(sketch, "E52.22.0.28", {"start": v(550, -12) * mm, "end": v(550, -16) * mm});
            skLineSegment(sketch, "E52.22.0.29", {"start": v(554, -16) * mm, "end": v(554, -12) * mm});
            skArc(sketch, "E52.23.0.0", {"start": v(578, 16) * mm, "mid": v(576, 18) * mm, "end": v(574, 16) * mm});
            skLineSegment(sketch, "E52.23.0.1", {"start": v(578, 16) * mm, "end": v(578, 12) * mm});
            skLineSegment(sketch, "E52.23.0.2", {"start": v(574, 16) * mm, "end": v(574, 12) * mm});
            skArc(sketch, "E52.23.0.3", {"start": v(574, 12) * mm, "mid": v(576, 10) * mm, "end": v(578, 12) * mm});
            skCircle(sketch, "E52.23.0.4", {"center": v(568, 16) * mm, "radius": 2 * mm});
            skCircle(sketch, "E52.23.0.5", {"center": v(560, 16) * mm, "radius": 2 * mm});
            skArc(sketch, "E52.23.0.6", {"start": v(561.9, 7.07) * mm, "mid": v(561.9, 9.9) * mm, "end": v(559.07, 9.9) * mm});
            skArc(sketch, "E52.23.0.7", {"start": v(558.59, 9.41) * mm, "mid": v(558.59, 6.59) * mm, "end": v(561.41, 6.59) * mm});
            skLineSegment(sketch, "E52.23.0.8", {"start": v(559.07, 9.9) * mm, "end": v(558.59, 9.41) * mm});
            skLineSegment(sketch, "E52.23.0.9", {"start": v(561.9, 7.07) * mm, "end": v(561.41, 6.59) * mm});
            skArc(sketch, "E52.23.0.10", {"start": v(568.93, 9.9) * mm, "mid": v(566.1, 9.9) * mm, "end": v(566.1, 7.07) * mm});
            skLineSegment(sketch, "E52.23.0.11", {"start": v(568.93, 9.9) * mm, "end": v(569.41, 9.41) * mm});
            skArc(sketch, "E52.23.0.12", {"start": v(566.59, 6.59) * mm, "mid": v(569.41, 6.59) * mm, "end": v(569.41, 9.41) * mm});
            skLineSegment(sketch, "E52.23.0.13", {"start": v(566.1, 7.07) * mm, "end": v(566.59, 6.59) * mm});
            skCircle(sketch, "E52.23.0.14", {"center": v(576, 0) * mm, "radius": 7 * mm});
            skArc(sketch, "E52.23.0.15", {"start": v(559.07, -9.9) * mm, "mid": v(561.9, -9.9) * mm, "end": v(561.9, -7.07) * mm});
            skArc(sketch, "E52.23.0.16", {"start": v(561.41, -6.59) * mm, "mid": v(558.59, -6.59) * mm, "end": v(558.59, -9.41) * mm});
            skLineSegment(sketch, "E52.23.0.17", {"start": v(561.41, -6.59) * mm, "end": v(561.9, -7.07) * mm});
            skLineSegment(sketch, "E52.23.0.18", {"start": v(558.59, -9.41) * mm, "end": v(559.07, -9.9) * mm});
            skArc(sketch, "E52.23.0.19", {"start": v(566.1, -7.07) * mm, "mid": v(566.1, -9.9) * mm, "end": v(568.93, -9.9) * mm});
            skLineSegment(sketch, "E52.23.0.20", {"start": v(568.93, -9.9) * mm, "end": v(569.41, -9.41) * mm});
            skArc(sketch, "E52.23.0.21", {"start": v(569.41, -9.41) * mm, "mid": v(569.41, -6.59) * mm, "end": v(566.59, -6.59) * mm});
            skCircle(sketch, "E52.23.0.22", {"center": v(568, -16) * mm, "radius": 2 * mm});
            skCircle(sketch, "E52.23.0.23", {"center": v(560, -16) * mm, "radius": 2 * mm});
            skLineSegment(sketch, "E52.23.0.24", {"start": v(566.1, -7.07) * mm, "end": v(566.59, -6.59) * mm});
            skCircle(sketch, "E52.23.0.25", {"center": v(564, 0) * mm, "radius": 2 * mm});
            skArc(sketch, "E52.23.0.26", {"start": v(578, -12) * mm, "mid": v(576, -10) * mm, "end": v(574, -12) * mm});
            skArc(sketch, "E52.23.0.27", {"start": v(574, -16) * mm, "mid": v(576, -18) * mm, "end": v(578, -16) * mm});
            skLineSegment(sketch, "E52.23.0.28", {"start": v(574, -12) * mm, "end": v(574, -16) * mm});
            skLineSegment(sketch, "E52.23.0.29", {"start": v(578, -16) * mm, "end": v(578, -12) * mm});
            skArc(sketch, "E52.24.0.0", {"start": v(602, 16) * mm, "mid": v(600, 18) * mm, "end": v(598, 16) * mm});
            skLineSegment(sketch, "E52.24.0.1", {"start": v(602, 16) * mm, "end": v(602, 12) * mm});
            skLineSegment(sketch, "E52.24.0.2", {"start": v(598, 16) * mm, "end": v(598, 12) * mm});
            skArc(sketch, "E52.24.0.3", {"start": v(598, 12) * mm, "mid": v(600, 10) * mm, "end": v(602, 12) * mm});
            skCircle(sketch, "E52.24.0.4", {"center": v(592, 16) * mm, "radius": 2 * mm});
            skCircle(sketch, "E52.24.0.5", {"center": v(584, 16) * mm, "radius": 2 * mm});
            skArc(sketch, "E52.24.0.6", {"start": v(585.9, 7.07) * mm, "mid": v(585.9, 9.9) * mm, "end": v(583.07, 9.9) * mm});
            skArc(sketch, "E52.24.0.7", {"start": v(582.59, 9.41) * mm, "mid": v(582.59, 6.59) * mm, "end": v(585.41, 6.59) * mm});
            skLineSegment(sketch, "E52.24.0.8", {"start": v(583.07, 9.9) * mm, "end": v(582.59, 9.41) * mm});
            skLineSegment(sketch, "E52.24.0.9", {"start": v(585.9, 7.07) * mm, "end": v(585.41, 6.59) * mm});
            skArc(sketch, "E52.24.0.10", {"start": v(592.93, 9.9) * mm, "mid": v(590.1, 9.9) * mm, "end": v(590.1, 7.07) * mm});
            skLineSegment(sketch, "E52.24.0.11", {"start": v(592.93, 9.9) * mm, "end": v(593.41, 9.41) * mm});
            skArc(sketch, "E52.24.0.12", {"start": v(590.59, 6.59) * mm, "mid": v(593.41, 6.59) * mm, "end": v(593.41, 9.41) * mm});
            skLineSegment(sketch, "E52.24.0.13", {"start": v(590.1, 7.07) * mm, "end": v(590.59, 6.59) * mm});
            skCircle(sketch, "E52.24.0.14", {"center": v(600, 0) * mm, "radius": 7 * mm});
            skArc(sketch, "E52.24.0.15", {"start": v(583.07, -9.9) * mm, "mid": v(585.9, -9.9) * mm, "end": v(585.9, -7.07) * mm});
            skArc(sketch, "E52.24.0.16", {"start": v(585.41, -6.59) * mm, "mid": v(582.59, -6.59) * mm, "end": v(582.59, -9.41) * mm});
            skLineSegment(sketch, "E52.24.0.17", {"start": v(585.41, -6.59) * mm, "end": v(585.9, -7.07) * mm});
            skLineSegment(sketch, "E52.24.0.18", {"start": v(582.59, -9.41) * mm, "end": v(583.07, -9.9) * mm});
            skArc(sketch, "E52.24.0.19", {"start": v(590.1, -7.07) * mm, "mid": v(590.1, -9.9) * mm, "end": v(592.93, -9.9) * mm});
            skLineSegment(sketch, "E52.24.0.20", {"start": v(592.93, -9.9) * mm, "end": v(593.41, -9.41) * mm});
            skArc(sketch, "E52.24.0.21", {"start": v(593.41, -9.41) * mm, "mid": v(593.41, -6.59) * mm, "end": v(590.59, -6.59) * mm});
            skCircle(sketch, "E52.24.0.22", {"center": v(592, -16) * mm, "radius": 2 * mm});
            skCircle(sketch, "E52.24.0.23", {"center": v(584, -16) * mm, "radius": 2 * mm});
            skLineSegment(sketch, "E52.24.0.24", {"start": v(590.1, -7.07) * mm, "end": v(590.59, -6.59) * mm});
            skCircle(sketch, "E52.24.0.25", {"center": v(588, 0) * mm, "radius": 2 * mm});
            skArc(sketch, "E52.24.0.26", {"start": v(602, -12) * mm, "mid": v(600, -10) * mm, "end": v(598, -12) * mm});
            skArc(sketch, "E52.24.0.27", {"start": v(598, -16) * mm, "mid": v(600, -18) * mm, "end": v(602, -16) * mm});
            skLineSegment(sketch, "E52.24.0.28", {"start": v(598, -12) * mm, "end": v(598, -16) * mm});
            skLineSegment(sketch, "E52.24.0.29", {"start": v(602, -16) * mm, "end": v(602, -12) * mm});
            skArc(sketch, "E52.25.0.0", {"start": v(626, 16) * mm, "mid": v(624, 18) * mm, "end": v(622, 16) * mm});
            skLineSegment(sketch, "E52.25.0.1", {"start": v(626, 16) * mm, "end": v(626, 12) * mm});
            skLineSegment(sketch, "E52.25.0.2", {"start": v(622, 16) * mm, "end": v(622, 12) * mm});
            skArc(sketch, "E52.25.0.3", {"start": v(622, 12) * mm, "mid": v(624, 10) * mm, "end": v(626, 12) * mm});
            skCircle(sketch, "E52.25.0.4", {"center": v(616, 16) * mm, "radius": 2 * mm});
            skCircle(sketch, "E52.25.0.5", {"center": v(608, 16) * mm, "radius": 2 * mm});
            skArc(sketch, "E52.25.0.6", {"start": v(609.9, 7.07) * mm, "mid": v(609.9, 9.9) * mm, "end": v(607.07, 9.9) * mm});
            skArc(sketch, "E52.25.0.7", {"start": v(606.59, 9.41) * mm, "mid": v(606.59, 6.59) * mm, "end": v(609.41, 6.59) * mm});
            skLineSegment(sketch, "E52.25.0.8", {"start": v(607.07, 9.9) * mm, "end": v(606.59, 9.41) * mm});
            skLineSegment(sketch, "E52.25.0.9", {"start": v(609.9, 7.07) * mm, "end": v(609.41, 6.59) * mm});
            skArc(sketch, "E52.25.0.10", {"start": v(616.93, 9.9) * mm, "mid": v(614.1, 9.9) * mm, "end": v(614.1, 7.07) * mm});
            skLineSegment(sketch, "E52.25.0.11", {"start": v(616.93, 9.9) * mm, "end": v(617.41, 9.41) * mm});
            skArc(sketch, "E52.25.0.12", {"start": v(614.59, 6.59) * mm, "mid": v(617.41, 6.59) * mm, "end": v(617.41, 9.41) * mm});
            skLineSegment(sketch, "E52.25.0.13", {"start": v(614.1, 7.07) * mm, "end": v(614.59, 6.59) * mm});
            skCircle(sketch, "E52.25.0.14", {"center": v(624, 0) * mm, "radius": 7 * mm});
            skArc(sketch, "E52.25.0.15", {"start": v(607.07, -9.9) * mm, "mid": v(609.9, -9.9) * mm, "end": v(609.9, -7.07) * mm});
            skArc(sketch, "E52.25.0.16", {"start": v(609.41, -6.59) * mm, "mid": v(606.59, -6.59) * mm, "end": v(606.59, -9.41) * mm});
            skLineSegment(sketch, "E52.25.0.17", {"start": v(609.41, -6.59) * mm, "end": v(609.9, -7.07) * mm});
            skLineSegment(sketch, "E52.25.0.18", {"start": v(606.59, -9.41) * mm, "end": v(607.07, -9.9) * mm});
            skArc(sketch, "E52.25.0.19", {"start": v(614.1, -7.07) * mm, "mid": v(614.1, -9.9) * mm, "end": v(616.93, -9.9) * mm});
            skLineSegment(sketch, "E52.25.0.20", {"start": v(616.93, -9.9) * mm, "end": v(617.41, -9.41) * mm});
            skArc(sketch, "E52.25.0.21", {"start": v(617.41, -9.41) * mm, "mid": v(617.41, -6.59) * mm, "end": v(614.59, -6.59) * mm});
            skCircle(sketch, "E52.25.0.22", {"center": v(616, -16) * mm, "radius": 2 * mm});
            skCircle(sketch, "E52.25.0.23", {"center": v(608, -16) * mm, "radius": 2 * mm});
            skLineSegment(sketch, "E52.25.0.24", {"start": v(614.1, -7.07) * mm, "end": v(614.59, -6.59) * mm});
            skCircle(sketch, "E52.25.0.25", {"center": v(612, 0) * mm, "radius": 2 * mm});
            skArc(sketch, "E52.25.0.26", {"start": v(626, -12) * mm, "mid": v(624, -10) * mm, "end": v(622, -12) * mm});
            skArc(sketch, "E52.25.0.27", {"start": v(622, -16) * mm, "mid": v(624, -18) * mm, "end": v(626, -16) * mm});
            skLineSegment(sketch, "E52.25.0.28", {"start": v(622, -12) * mm, "end": v(622, -16) * mm});
            skLineSegment(sketch, "E52.25.0.29", {"start": v(626, -16) * mm, "end": v(626, -12) * mm});
            skArc(sketch, "E52.26.0.0", {"start": v(650, 16) * mm, "mid": v(648, 18) * mm, "end": v(646, 16) * mm});
            skLineSegment(sketch, "E52.26.0.1", {"start": v(650, 16) * mm, "end": v(650, 12) * mm});
            skLineSegment(sketch, "E52.26.0.2", {"start": v(646, 16) * mm, "end": v(646, 12) * mm});
            skArc(sketch, "E52.26.0.3", {"start": v(646, 12) * mm, "mid": v(648, 10) * mm, "end": v(650, 12) * mm});
            skCircle(sketch, "E52.26.0.4", {"center": v(640, 16) * mm, "radius": 2 * mm});
            skCircle(sketch, "E52.26.0.5", {"center": v(632, 16) * mm, "radius": 2 * mm});
            skArc(sketch, "E52.26.0.6", {"start": v(633.9, 7.07) * mm, "mid": v(633.9, 9.9) * mm, "end": v(631.07, 9.9) * mm});
            skArc(sketch, "E52.26.0.7", {"start": v(630.59, 9.41) * mm, "mid": v(630.59, 6.59) * mm, "end": v(633.41, 6.59) * mm});
            skLineSegment(sketch, "E52.26.0.8", {"start": v(631.07, 9.9) * mm, "end": v(630.59, 9.41) * mm});
            skLineSegment(sketch, "E52.26.0.9", {"start": v(633.9, 7.07) * mm, "end": v(633.41, 6.59) * mm});
            skArc(sketch, "E52.26.0.10", {"start": v(640.93, 9.9) * mm, "mid": v(638.1, 9.9) * mm, "end": v(638.1, 7.07) * mm});
            skLineSegment(sketch, "E52.26.0.11", {"start": v(640.93, 9.9) * mm, "end": v(641.41, 9.41) * mm});
            skArc(sketch, "E52.26.0.12", {"start": v(638.59, 6.59) * mm, "mid": v(641.41, 6.59) * mm, "end": v(641.41, 9.41) * mm});
            skLineSegment(sketch, "E52.26.0.13", {"start": v(638.1, 7.07) * mm, "end": v(638.59, 6.59) * mm});
            skCircle(sketch, "E52.26.0.14", {"center": v(648, 0) * mm, "radius": 7 * mm});
            skArc(sketch, "E52.26.0.15", {"start": v(631.07, -9.9) * mm, "mid": v(633.9, -9.9) * mm, "end": v(633.9, -7.07) * mm});
            skArc(sketch, "E52.26.0.16", {"start": v(633.41, -6.59) * mm, "mid": v(630.59, -6.59) * mm, "end": v(630.59, -9.41) * mm});
            skLineSegment(sketch, "E52.26.0.17", {"start": v(633.41, -6.59) * mm, "end": v(633.9, -7.07) * mm});
            skLineSegment(sketch, "E52.26.0.18", {"start": v(630.59, -9.41) * mm, "end": v(631.07, -9.9) * mm});
            skArc(sketch, "E52.26.0.19", {"start": v(638.1, -7.07) * mm, "mid": v(638.1, -9.9) * mm, "end": v(640.93, -9.9) * mm});
            skLineSegment(sketch, "E52.26.0.20", {"start": v(640.93, -9.9) * mm, "end": v(641.41, -9.41) * mm});
            skArc(sketch, "E52.26.0.21", {"start": v(641.41, -9.41) * mm, "mid": v(641.41, -6.59) * mm, "end": v(638.59, -6.59) * mm});
            skCircle(sketch, "E52.26.0.22", {"center": v(640, -16) * mm, "radius": 2 * mm});
            skCircle(sketch, "E52.26.0.23", {"center": v(632, -16) * mm, "radius": 2 * mm});
            skLineSegment(sketch, "E52.26.0.24", {"start": v(638.1, -7.07) * mm, "end": v(638.59, -6.59) * mm});
            skCircle(sketch, "E52.26.0.25", {"center": v(636, 0) * mm, "radius": 2 * mm});
            skArc(sketch, "E52.26.0.26", {"start": v(650, -12) * mm, "mid": v(648, -10) * mm, "end": v(646, -12) * mm});
            skArc(sketch, "E52.26.0.27", {"start": v(646, -16) * mm, "mid": v(648, -18) * mm, "end": v(650, -16) * mm});
            skLineSegment(sketch, "E52.26.0.28", {"start": v(646, -12) * mm, "end": v(646, -16) * mm});
            skLineSegment(sketch, "E52.26.0.29", {"start": v(650, -16) * mm, "end": v(650, -12) * mm});
            skArc(sketch, "E52.27.0.0", {"start": v(674, 16) * mm, "mid": v(672, 18) * mm, "end": v(670, 16) * mm});
            skLineSegment(sketch, "E52.27.0.1", {"start": v(674, 16) * mm, "end": v(674, 12) * mm});
            skLineSegment(sketch, "E52.27.0.2", {"start": v(670, 16) * mm, "end": v(670, 12) * mm});
            skArc(sketch, "E52.27.0.3", {"start": v(670, 12) * mm, "mid": v(672, 10) * mm, "end": v(674, 12) * mm});
            skCircle(sketch, "E52.27.0.4", {"center": v(664, 16) * mm, "radius": 2 * mm});
            skCircle(sketch, "E52.27.0.5", {"center": v(656, 16) * mm, "radius": 2 * mm});
            skArc(sketch, "E52.27.0.6", {"start": v(657.9, 7.07) * mm, "mid": v(657.9, 9.9) * mm, "end": v(655.07, 9.9) * mm});
            skArc(sketch, "E52.27.0.7", {"start": v(654.59, 9.41) * mm, "mid": v(654.59, 6.59) * mm, "end": v(657.41, 6.59) * mm});
            skLineSegment(sketch, "E52.27.0.8", {"start": v(655.07, 9.9) * mm, "end": v(654.59, 9.41) * mm});
            skLineSegment(sketch, "E52.27.0.9", {"start": v(657.9, 7.07) * mm, "end": v(657.41, 6.59) * mm});
            skArc(sketch, "E52.27.0.10", {"start": v(664.93, 9.9) * mm, "mid": v(662.1, 9.9) * mm, "end": v(662.1, 7.07) * mm});
            skLineSegment(sketch, "E52.27.0.11", {"start": v(664.93, 9.9) * mm, "end": v(665.41, 9.41) * mm});
            skArc(sketch, "E52.27.0.12", {"start": v(662.59, 6.59) * mm, "mid": v(665.41, 6.59) * mm, "end": v(665.41, 9.41) * mm});
            skLineSegment(sketch, "E52.27.0.13", {"start": v(662.1, 7.07) * mm, "end": v(662.59, 6.59) * mm});
            skCircle(sketch, "E52.27.0.14", {"center": v(672, 0) * mm, "radius": 7 * mm});
            skArc(sketch, "E52.27.0.15", {"start": v(655.07, -9.9) * mm, "mid": v(657.9, -9.9) * mm, "end": v(657.9, -7.07) * mm});
            skArc(sketch, "E52.27.0.16", {"start": v(657.41, -6.59) * mm, "mid": v(654.59, -6.59) * mm, "end": v(654.59, -9.41) * mm});
            skLineSegment(sketch, "E52.27.0.17", {"start": v(657.41, -6.59) * mm, "end": v(657.9, -7.07) * mm});
            skLineSegment(sketch, "E52.27.0.18", {"start": v(654.59, -9.41) * mm, "end": v(655.07, -9.9) * mm});
            skArc(sketch, "E52.27.0.19", {"start": v(662.1, -7.07) * mm, "mid": v(662.1, -9.9) * mm, "end": v(664.93, -9.9) * mm});
            skLineSegment(sketch, "E52.27.0.20", {"start": v(664.93, -9.9) * mm, "end": v(665.41, -9.41) * mm});
            skArc(sketch, "E52.27.0.21", {"start": v(665.41, -9.41) * mm, "mid": v(665.41, -6.59) * mm, "end": v(662.59, -6.59) * mm});
            skCircle(sketch, "E52.27.0.22", {"center": v(664, -16) * mm, "radius": 2 * mm});
            skCircle(sketch, "E52.27.0.23", {"center": v(656, -16) * mm, "radius": 2 * mm});
            skLineSegment(sketch, "E52.27.0.24", {"start": v(662.1, -7.07) * mm, "end": v(662.59, -6.59) * mm});
            skCircle(sketch, "E52.27.0.25", {"center": v(660, 0) * mm, "radius": 2 * mm});
            skArc(sketch, "E52.27.0.26", {"start": v(674, -12) * mm, "mid": v(672, -10) * mm, "end": v(670, -12) * mm});
            skArc(sketch, "E52.27.0.27", {"start": v(670, -16) * mm, "mid": v(672, -18) * mm, "end": v(674, -16) * mm});
            skLineSegment(sketch, "E52.27.0.28", {"start": v(670, -12) * mm, "end": v(670, -16) * mm});
            skLineSegment(sketch, "E52.27.0.29", {"start": v(674, -16) * mm, "end": v(674, -12) * mm});
            skArc(sketch, "E52.28.0.0", {"start": v(698, 16) * mm, "mid": v(696, 18) * mm, "end": v(694, 16) * mm});
            skLineSegment(sketch, "E52.28.0.1", {"start": v(698, 16) * mm, "end": v(698, 12) * mm});
            skLineSegment(sketch, "E52.28.0.2", {"start": v(694, 16) * mm, "end": v(694, 12) * mm});
            skArc(sketch, "E52.28.0.3", {"start": v(694, 12) * mm, "mid": v(696, 10) * mm, "end": v(698, 12) * mm});
            skCircle(sketch, "E52.28.0.4", {"center": v(688, 16) * mm, "radius": 2 * mm});
            skCircle(sketch, "E52.28.0.5", {"center": v(680, 16) * mm, "radius": 2 * mm});
            skArc(sketch, "E52.28.0.6", {"start": v(681.9, 7.07) * mm, "mid": v(681.9, 9.9) * mm, "end": v(679.07, 9.9) * mm});
            skArc(sketch, "E52.28.0.7", {"start": v(678.59, 9.41) * mm, "mid": v(678.59, 6.59) * mm, "end": v(681.41, 6.59) * mm});
            skLineSegment(sketch, "E52.28.0.8", {"start": v(679.07, 9.9) * mm, "end": v(678.59, 9.41) * mm});
            skLineSegment(sketch, "E52.28.0.9", {"start": v(681.9, 7.07) * mm, "end": v(681.41, 6.59) * mm});
            skArc(sketch, "E52.28.0.10", {"start": v(688.93, 9.9) * mm, "mid": v(686.1, 9.9) * mm, "end": v(686.1, 7.07) * mm});
            skLineSegment(sketch, "E52.28.0.11", {"start": v(688.93, 9.9) * mm, "end": v(689.41, 9.41) * mm});
            skArc(sketch, "E52.28.0.12", {"start": v(686.59, 6.59) * mm, "mid": v(689.41, 6.59) * mm, "end": v(689.41, 9.41) * mm});
            skLineSegment(sketch, "E52.28.0.13", {"start": v(686.1, 7.07) * mm, "end": v(686.59, 6.59) * mm});
            skCircle(sketch, "E52.28.0.14", {"center": v(696, 0) * mm, "radius": 7 * mm});
            skArc(sketch, "E52.28.0.15", {"start": v(679.07, -9.9) * mm, "mid": v(681.9, -9.9) * mm, "end": v(681.9, -7.07) * mm});
            skArc(sketch, "E52.28.0.16", {"start": v(681.41, -6.59) * mm, "mid": v(678.59, -6.59) * mm, "end": v(678.59, -9.41) * mm});
            skLineSegment(sketch, "E52.28.0.17", {"start": v(681.41, -6.59) * mm, "end": v(681.9, -7.07) * mm});
            skLineSegment(sketch, "E52.28.0.18", {"start": v(678.59, -9.41) * mm, "end": v(679.07, -9.9) * mm});
            skArc(sketch, "E52.28.0.19", {"start": v(686.1, -7.07) * mm, "mid": v(686.1, -9.9) * mm, "end": v(688.93, -9.9) * mm});
            skLineSegment(sketch, "E52.28.0.20", {"start": v(688.93, -9.9) * mm, "end": v(689.41, -9.41) * mm});
            skArc(sketch, "E52.28.0.21", {"start": v(689.41, -9.41) * mm, "mid": v(689.41, -6.59) * mm, "end": v(686.59, -6.59) * mm});
            skCircle(sketch, "E52.28.0.22", {"center": v(688, -16) * mm, "radius": 2 * mm});
            skCircle(sketch, "E52.28.0.23", {"center": v(680, -16) * mm, "radius": 2 * mm});
            skLineSegment(sketch, "E52.28.0.24", {"start": v(686.1, -7.07) * mm, "end": v(686.59, -6.59) * mm});
            skCircle(sketch, "E52.28.0.25", {"center": v(684, 0) * mm, "radius": 2 * mm});
            skArc(sketch, "E52.28.0.26", {"start": v(698, -12) * mm, "mid": v(696, -10) * mm, "end": v(694, -12) * mm});
            skArc(sketch, "E52.28.0.27", {"start": v(694, -16) * mm, "mid": v(696, -18) * mm, "end": v(698, -16) * mm});
            skLineSegment(sketch, "E52.28.0.28", {"start": v(694, -12) * mm, "end": v(694, -16) * mm});
            skLineSegment(sketch, "E52.28.0.29", {"start": v(698, -16) * mm, "end": v(698, -12) * mm});
            skArc(sketch, "E52.29.0.0", {"start": v(722, 16) * mm, "mid": v(720, 18) * mm, "end": v(718, 16) * mm});
            skLineSegment(sketch, "E52.29.0.1", {"start": v(722, 16) * mm, "end": v(722, 12) * mm});
            skLineSegment(sketch, "E52.29.0.2", {"start": v(718, 16) * mm, "end": v(718, 12) * mm});
            skArc(sketch, "E52.29.0.3", {"start": v(718, 12) * mm, "mid": v(720, 10) * mm, "end": v(722, 12) * mm});
            skCircle(sketch, "E52.29.0.4", {"center": v(712, 16) * mm, "radius": 2 * mm});
            skCircle(sketch, "E52.29.0.5", {"center": v(704, 16) * mm, "radius": 2 * mm});
            skArc(sketch, "E52.29.0.6", {"start": v(705.9, 7.07) * mm, "mid": v(705.9, 9.9) * mm, "end": v(703.07, 9.9) * mm});
            skArc(sketch, "E52.29.0.7", {"start": v(702.59, 9.41) * mm, "mid": v(702.59, 6.59) * mm, "end": v(705.41, 6.59) * mm});
            skLineSegment(sketch, "E52.29.0.8", {"start": v(703.07, 9.9) * mm, "end": v(702.59, 9.41) * mm});
            skLineSegment(sketch, "E52.29.0.9", {"start": v(705.9, 7.07) * mm, "end": v(705.41, 6.59) * mm});
            skArc(sketch, "E52.29.0.10", {"start": v(712.93, 9.9) * mm, "mid": v(710.1, 9.9) * mm, "end": v(710.1, 7.07) * mm});
            skLineSegment(sketch, "E52.29.0.11", {"start": v(712.93, 9.9) * mm, "end": v(713.41, 9.41) * mm});
            skArc(sketch, "E52.29.0.12", {"start": v(710.59, 6.59) * mm, "mid": v(713.41, 6.59) * mm, "end": v(713.41, 9.41) * mm});
            skLineSegment(sketch, "E52.29.0.13", {"start": v(710.1, 7.07) * mm, "end": v(710.59, 6.59) * mm});
            skCircle(sketch, "E52.29.0.14", {"center": v(720, 0) * mm, "radius": 7 * mm});
            skArc(sketch, "E52.29.0.15", {"start": v(703.07, -9.9) * mm, "mid": v(705.9, -9.9) * mm, "end": v(705.9, -7.07) * mm});
            skArc(sketch, "E52.29.0.16", {"start": v(705.41, -6.59) * mm, "mid": v(702.59, -6.59) * mm, "end": v(702.59, -9.41) * mm});
            skLineSegment(sketch, "E52.29.0.17", {"start": v(705.41, -6.59) * mm, "end": v(705.9, -7.07) * mm});
            skLineSegment(sketch, "E52.29.0.18", {"start": v(702.59, -9.41) * mm, "end": v(703.07, -9.9) * mm});
            skArc(sketch, "E52.29.0.19", {"start": v(710.1, -7.07) * mm, "mid": v(710.1, -9.9) * mm, "end": v(712.93, -9.9) * mm});
            skLineSegment(sketch, "E52.29.0.20", {"start": v(712.93, -9.9) * mm, "end": v(713.41, -9.41) * mm});
            skArc(sketch, "E52.29.0.21", {"start": v(713.41, -9.41) * mm, "mid": v(713.41, -6.59) * mm, "end": v(710.59, -6.59) * mm});
            skCircle(sketch, "E52.29.0.22", {"center": v(712, -16) * mm, "radius": 2 * mm});
            skCircle(sketch, "E52.29.0.23", {"center": v(704, -16) * mm, "radius": 2 * mm});
            skLineSegment(sketch, "E52.29.0.24", {"start": v(710.1, -7.07) * mm, "end": v(710.59, -6.59) * mm});
            skCircle(sketch, "E52.29.0.25", {"center": v(708, 0) * mm, "radius": 2 * mm});
            skArc(sketch, "E52.29.0.26", {"start": v(722, -12) * mm, "mid": v(720, -10) * mm, "end": v(718, -12) * mm});
            skArc(sketch, "E52.29.0.27", {"start": v(718, -16) * mm, "mid": v(720, -18) * mm, "end": v(722, -16) * mm});
            skLineSegment(sketch, "E52.29.0.28", {"start": v(718, -12) * mm, "end": v(718, -16) * mm});
            skLineSegment(sketch, "E52.29.0.29", {"start": v(722, -16) * mm, "end": v(722, -12) * mm});
            skArc(sketch, "E52.30.0.0", {"start": v(746, 16) * mm, "mid": v(744, 18) * mm, "end": v(742, 16) * mm});
            skLineSegment(sketch, "E52.30.0.1", {"start": v(746, 16) * mm, "end": v(746, 12) * mm});
            skLineSegment(sketch, "E52.30.0.2", {"start": v(742, 16) * mm, "end": v(742, 12) * mm});
            skArc(sketch, "E52.30.0.3", {"start": v(742, 12) * mm, "mid": v(744, 10) * mm, "end": v(746, 12) * mm});
            skCircle(sketch, "E52.30.0.4", {"center": v(736, 16) * mm, "radius": 2 * mm});
            skCircle(sketch, "E52.30.0.5", {"center": v(728, 16) * mm, "radius": 2 * mm});
            skArc(sketch, "E52.30.0.6", {"start": v(729.9, 7.07) * mm, "mid": v(729.9, 9.9) * mm, "end": v(727.07, 9.9) * mm});
            skArc(sketch, "E52.30.0.7", {"start": v(726.59, 9.41) * mm, "mid": v(726.59, 6.59) * mm, "end": v(729.41, 6.59) * mm});
            skLineSegment(sketch, "E52.30.0.8", {"start": v(727.07, 9.9) * mm, "end": v(726.59, 9.41) * mm});
            skLineSegment(sketch, "E52.30.0.9", {"start": v(729.9, 7.07) * mm, "end": v(729.41, 6.59) * mm});
            skArc(sketch, "E52.30.0.10", {"start": v(736.93, 9.9) * mm, "mid": v(734.1, 9.9) * mm, "end": v(734.1, 7.07) * mm});
            skLineSegment(sketch, "E52.30.0.11", {"start": v(736.93, 9.9) * mm, "end": v(737.41, 9.41) * mm});
            skArc(sketch, "E52.30.0.12", {"start": v(734.59, 6.59) * mm, "mid": v(737.41, 6.59) * mm, "end": v(737.41, 9.41) * mm});
            skLineSegment(sketch, "E52.30.0.13", {"start": v(734.1, 7.07) * mm, "end": v(734.59, 6.59) * mm});
            skCircle(sketch, "E52.30.0.14", {"center": v(744, 0) * mm, "radius": 7 * mm});
            skArc(sketch, "E52.30.0.15", {"start": v(727.07, -9.9) * mm, "mid": v(729.9, -9.9) * mm, "end": v(729.9, -7.07) * mm});
            skArc(sketch, "E52.30.0.16", {"start": v(729.41, -6.59) * mm, "mid": v(726.59, -6.59) * mm, "end": v(726.59, -9.41) * mm});
            skLineSegment(sketch, "E52.30.0.17", {"start": v(729.41, -6.59) * mm, "end": v(729.9, -7.07) * mm});
            skLineSegment(sketch, "E52.30.0.18", {"start": v(726.59, -9.41) * mm, "end": v(727.07, -9.9) * mm});
            skArc(sketch, "E52.30.0.19", {"start": v(734.1, -7.07) * mm, "mid": v(734.1, -9.9) * mm, "end": v(736.93, -9.9) * mm});
            skLineSegment(sketch, "E52.30.0.20", {"start": v(736.93, -9.9) * mm, "end": v(737.41, -9.41) * mm});
            skArc(sketch, "E52.30.0.21", {"start": v(737.41, -9.41) * mm, "mid": v(737.41, -6.59) * mm, "end": v(734.59, -6.59) * mm});
            skCircle(sketch, "E52.30.0.22", {"center": v(736, -16) * mm, "radius": 2 * mm});
            skCircle(sketch, "E52.30.0.23", {"center": v(728, -16) * mm, "radius": 2 * mm});
            skLineSegment(sketch, "E52.30.0.24", {"start": v(734.1, -7.07) * mm, "end": v(734.59, -6.59) * mm});
            skCircle(sketch, "E52.30.0.25", {"center": v(732, 0) * mm, "radius": 2 * mm});
            skArc(sketch, "E52.30.0.26", {"start": v(746, -12) * mm, "mid": v(744, -10) * mm, "end": v(742, -12) * mm});
            skArc(sketch, "E52.30.0.27", {"start": v(742, -16) * mm, "mid": v(744, -18) * mm, "end": v(746, -16) * mm});
            skLineSegment(sketch, "E52.30.0.28", {"start": v(742, -12) * mm, "end": v(742, -16) * mm});
            skLineSegment(sketch, "E52.30.0.29", {"start": v(746, -16) * mm, "end": v(746, -12) * mm});
            skArc(sketch, "E52.31.0.0", {"start": v(770, 16) * mm, "mid": v(768, 18) * mm, "end": v(766, 16) * mm});
            skLineSegment(sketch, "E52.31.0.1", {"start": v(770, 16) * mm, "end": v(770, 12) * mm});
            skLineSegment(sketch, "E52.31.0.2", {"start": v(766, 16) * mm, "end": v(766, 12) * mm});
            skArc(sketch, "E52.31.0.3", {"start": v(766, 12) * mm, "mid": v(768, 10) * mm, "end": v(770, 12) * mm});
            skCircle(sketch, "E52.31.0.4", {"center": v(760, 16) * mm, "radius": 2 * mm});
            skCircle(sketch, "E52.31.0.5", {"center": v(752, 16) * mm, "radius": 2 * mm});
            skArc(sketch, "E52.31.0.6", {"start": v(753.9, 7.07) * mm, "mid": v(753.9, 9.9) * mm, "end": v(751.07, 9.9) * mm});
            skArc(sketch, "E52.31.0.7", {"start": v(750.59, 9.41) * mm, "mid": v(750.59, 6.59) * mm, "end": v(753.41, 6.59) * mm});
            skLineSegment(sketch, "E52.31.0.8", {"start": v(751.07, 9.9) * mm, "end": v(750.59, 9.41) * mm});
            skLineSegment(sketch, "E52.31.0.9", {"start": v(753.9, 7.07) * mm, "end": v(753.41, 6.59) * mm});
            skArc(sketch, "E52.31.0.10", {"start": v(760.93, 9.9) * mm, "mid": v(758.1, 9.9) * mm, "end": v(758.1, 7.07) * mm});
            skLineSegment(sketch, "E52.31.0.11", {"start": v(760.93, 9.9) * mm, "end": v(761.41, 9.41) * mm});
            skArc(sketch, "E52.31.0.12", {"start": v(758.59, 6.59) * mm, "mid": v(761.41, 6.59) * mm, "end": v(761.41, 9.41) * mm});
            skLineSegment(sketch, "E52.31.0.13", {"start": v(758.1, 7.07) * mm, "end": v(758.59, 6.59) * mm});
            skCircle(sketch, "E52.31.0.14", {"center": v(768, 0) * mm, "radius": 7 * mm});
            skArc(sketch, "E52.31.0.15", {"start": v(751.07, -9.9) * mm, "mid": v(753.9, -9.9) * mm, "end": v(753.9, -7.07) * mm});
            skArc(sketch, "E52.31.0.16", {"start": v(753.41, -6.59) * mm, "mid": v(750.59, -6.59) * mm, "end": v(750.59, -9.41) * mm});
            skLineSegment(sketch, "E52.31.0.17", {"start": v(753.41, -6.59) * mm, "end": v(753.9, -7.07) * mm});
            skLineSegment(sketch, "E52.31.0.18", {"start": v(750.59, -9.41) * mm, "end": v(751.07, -9.9) * mm});
            skArc(sketch, "E52.31.0.19", {"start": v(758.1, -7.07) * mm, "mid": v(758.1, -9.9) * mm, "end": v(760.93, -9.9) * mm});
            skLineSegment(sketch, "E52.31.0.20", {"start": v(760.93, -9.9) * mm, "end": v(761.41, -9.41) * mm});
            skArc(sketch, "E52.31.0.21", {"start": v(761.41, -9.41) * mm, "mid": v(761.41, -6.59) * mm, "end": v(758.59, -6.59) * mm});
            skCircle(sketch, "E52.31.0.22", {"center": v(760, -16) * mm, "radius": 2 * mm});
            skCircle(sketch, "E52.31.0.23", {"center": v(752, -16) * mm, "radius": 2 * mm});
            skLineSegment(sketch, "E52.31.0.24", {"start": v(758.1, -7.07) * mm, "end": v(758.59, -6.59) * mm});
            skCircle(sketch, "E52.31.0.25", {"center": v(756, 0) * mm, "radius": 2 * mm});
            skArc(sketch, "E52.31.0.26", {"start": v(770, -12) * mm, "mid": v(768, -10) * mm, "end": v(766, -12) * mm});
            skArc(sketch, "E52.31.0.27", {"start": v(766, -16) * mm, "mid": v(768, -18) * mm, "end": v(770, -16) * mm});
            skLineSegment(sketch, "E52.31.0.28", {"start": v(766, -12) * mm, "end": v(766, -16) * mm});
            skLineSegment(sketch, "E52.31.0.29", {"start": v(770, -16) * mm, "end": v(770, -12) * mm});
            skArc(sketch, "E52.32.0.0", {"start": v(794, 16) * mm, "mid": v(792, 18) * mm, "end": v(790, 16) * mm});
            skLineSegment(sketch, "E52.32.0.1", {"start": v(794, 16) * mm, "end": v(794, 12) * mm});
            skLineSegment(sketch, "E52.32.0.2", {"start": v(790, 16) * mm, "end": v(790, 12) * mm});
            skArc(sketch, "E52.32.0.3", {"start": v(790, 12) * mm, "mid": v(792, 10) * mm, "end": v(794, 12) * mm});
            skCircle(sketch, "E52.32.0.4", {"center": v(784, 16) * mm, "radius": 2 * mm});
            skCircle(sketch, "E52.32.0.5", {"center": v(776, 16) * mm, "radius": 2 * mm});
            skArc(sketch, "E52.32.0.6", {"start": v(777.9, 7.07) * mm, "mid": v(777.9, 9.9) * mm, "end": v(775.07, 9.9) * mm});
            skArc(sketch, "E52.32.0.7", {"start": v(774.59, 9.41) * mm, "mid": v(774.59, 6.59) * mm, "end": v(777.41, 6.59) * mm});
            skLineSegment(sketch, "E52.32.0.8", {"start": v(775.07, 9.9) * mm, "end": v(774.59, 9.41) * mm});
            skLineSegment(sketch, "E52.32.0.9", {"start": v(777.9, 7.07) * mm, "end": v(777.41, 6.59) * mm});
            skArc(sketch, "E52.32.0.10", {"start": v(784.93, 9.9) * mm, "mid": v(782.1, 9.9) * mm, "end": v(782.1, 7.07) * mm});
            skLineSegment(sketch, "E52.32.0.11", {"start": v(784.93, 9.9) * mm, "end": v(785.41, 9.41) * mm});
            skArc(sketch, "E52.32.0.12", {"start": v(782.59, 6.59) * mm, "mid": v(785.41, 6.59) * mm, "end": v(785.41, 9.41) * mm});
            skLineSegment(sketch, "E52.32.0.13", {"start": v(782.1, 7.07) * mm, "end": v(782.59, 6.59) * mm});
            skCircle(sketch, "E52.32.0.14", {"center": v(792, 0) * mm, "radius": 7 * mm});
            skArc(sketch, "E52.32.0.15", {"start": v(775.07, -9.9) * mm, "mid": v(777.9, -9.9) * mm, "end": v(777.9, -7.07) * mm});
            skArc(sketch, "E52.32.0.16", {"start": v(777.41, -6.59) * mm, "mid": v(774.59, -6.59) * mm, "end": v(774.59, -9.41) * mm});
            skLineSegment(sketch, "E52.32.0.17", {"start": v(777.41, -6.59) * mm, "end": v(777.9, -7.07) * mm});
            skLineSegment(sketch, "E52.32.0.18", {"start": v(774.59, -9.41) * mm, "end": v(775.07, -9.9) * mm});
            skArc(sketch, "E52.32.0.19", {"start": v(782.1, -7.07) * mm, "mid": v(782.1, -9.9) * mm, "end": v(784.93, -9.9) * mm});
            skLineSegment(sketch, "E52.32.0.20", {"start": v(784.93, -9.9) * mm, "end": v(785.41, -9.41) * mm});
            skArc(sketch, "E52.32.0.21", {"start": v(785.41, -9.41) * mm, "mid": v(785.41, -6.59) * mm, "end": v(782.59, -6.59) * mm});
            skCircle(sketch, "E52.32.0.22", {"center": v(784, -16) * mm, "radius": 2 * mm});
            skCircle(sketch, "E52.32.0.23", {"center": v(776, -16) * mm, "radius": 2 * mm});
            skLineSegment(sketch, "E52.32.0.24", {"start": v(782.1, -7.07) * mm, "end": v(782.59, -6.59) * mm});
            skCircle(sketch, "E52.32.0.25", {"center": v(780, 0) * mm, "radius": 2 * mm});
            skArc(sketch, "E52.32.0.26", {"start": v(794, -12) * mm, "mid": v(792, -10) * mm, "end": v(790, -12) * mm});
            skArc(sketch, "E52.32.0.27", {"start": v(790, -16) * mm, "mid": v(792, -18) * mm, "end": v(794, -16) * mm});
            skLineSegment(sketch, "E52.32.0.28", {"start": v(790, -12) * mm, "end": v(790, -16) * mm});
            skLineSegment(sketch, "E52.32.0.29", {"start": v(794, -16) * mm, "end": v(794, -12) * mm});
            skArc(sketch, "E52.33.0.0", {"start": v(818, 16) * mm, "mid": v(816, 18) * mm, "end": v(814, 16) * mm});
            skLineSegment(sketch, "E52.33.0.1", {"start": v(818, 16) * mm, "end": v(818, 12) * mm});
            skLineSegment(sketch, "E52.33.0.2", {"start": v(814, 16) * mm, "end": v(814, 12) * mm});
            skArc(sketch, "E52.33.0.3", {"start": v(814, 12) * mm, "mid": v(816, 10) * mm, "end": v(818, 12) * mm});
            skCircle(sketch, "E52.33.0.4", {"center": v(808, 16) * mm, "radius": 2 * mm});
            skCircle(sketch, "E52.33.0.5", {"center": v(800, 16) * mm, "radius": 2 * mm});
            skArc(sketch, "E52.33.0.6", {"start": v(801.9, 7.07) * mm, "mid": v(801.9, 9.9) * mm, "end": v(799.07, 9.9) * mm});
            skArc(sketch, "E52.33.0.7", {"start": v(798.59, 9.41) * mm, "mid": v(798.59, 6.59) * mm, "end": v(801.41, 6.59) * mm});
            skLineSegment(sketch, "E52.33.0.8", {"start": v(799.07, 9.9) * mm, "end": v(798.59, 9.41) * mm});
            skLineSegment(sketch, "E52.33.0.9", {"start": v(801.9, 7.07) * mm, "end": v(801.41, 6.59) * mm});
            skArc(sketch, "E52.33.0.10", {"start": v(808.93, 9.9) * mm, "mid": v(806.1, 9.9) * mm, "end": v(806.1, 7.07) * mm});
            skLineSegment(sketch, "E52.33.0.11", {"start": v(808.93, 9.9) * mm, "end": v(809.41, 9.41) * mm});
            skArc(sketch, "E52.33.0.12", {"start": v(806.59, 6.59) * mm, "mid": v(809.41, 6.59) * mm, "end": v(809.41, 9.41) * mm});
            skLineSegment(sketch, "E52.33.0.13", {"start": v(806.1, 7.07) * mm, "end": v(806.59, 6.59) * mm});
            skCircle(sketch, "E52.33.0.14", {"center": v(816, 0) * mm, "radius": 7 * mm});
            skArc(sketch, "E52.33.0.15", {"start": v(799.07, -9.9) * mm, "mid": v(801.9, -9.9) * mm, "end": v(801.9, -7.07) * mm});
            skArc(sketch, "E52.33.0.16", {"start": v(801.41, -6.59) * mm, "mid": v(798.59, -6.59) * mm, "end": v(798.59, -9.41) * mm});
            skLineSegment(sketch, "E52.33.0.17", {"start": v(801.41, -6.59) * mm, "end": v(801.9, -7.07) * mm});
            skLineSegment(sketch, "E52.33.0.18", {"start": v(798.59, -9.41) * mm, "end": v(799.07, -9.9) * mm});
            skArc(sketch, "E52.33.0.19", {"start": v(806.1, -7.07) * mm, "mid": v(806.1, -9.9) * mm, "end": v(808.93, -9.9) * mm});
            skLineSegment(sketch, "E52.33.0.20", {"start": v(808.93, -9.9) * mm, "end": v(809.41, -9.41) * mm});
            skArc(sketch, "E52.33.0.21", {"start": v(809.41, -9.41) * mm, "mid": v(809.41, -6.59) * mm, "end": v(806.59, -6.59) * mm});
            skCircle(sketch, "E52.33.0.22", {"center": v(808, -16) * mm, "radius": 2 * mm});
            skCircle(sketch, "E52.33.0.23", {"center": v(800, -16) * mm, "radius": 2 * mm});
            skLineSegment(sketch, "E52.33.0.24", {"start": v(806.1, -7.07) * mm, "end": v(806.59, -6.59) * mm});
            skCircle(sketch, "E52.33.0.25", {"center": v(804, 0) * mm, "radius": 2 * mm});
            skArc(sketch, "E52.33.0.26", {"start": v(818, -12) * mm, "mid": v(816, -10) * mm, "end": v(814, -12) * mm});
            skArc(sketch, "E52.33.0.27", {"start": v(814, -16) * mm, "mid": v(816, -18) * mm, "end": v(818, -16) * mm});
            skLineSegment(sketch, "E52.33.0.28", {"start": v(814, -12) * mm, "end": v(814, -16) * mm});
            skLineSegment(sketch, "E52.33.0.29", {"start": v(818, -16) * mm, "end": v(818, -12) * mm});
            skArc(sketch, "E52.34.0.0", {"start": v(842, 16) * mm, "mid": v(840, 18) * mm, "end": v(838, 16) * mm});
            skLineSegment(sketch, "E52.34.0.1", {"start": v(842, 16) * mm, "end": v(842, 12) * mm});
            skLineSegment(sketch, "E52.34.0.2", {"start": v(838, 16) * mm, "end": v(838, 12) * mm});
            skArc(sketch, "E52.34.0.3", {"start": v(838, 12) * mm, "mid": v(840, 10) * mm, "end": v(842, 12) * mm});
            skCircle(sketch, "E52.34.0.4", {"center": v(832, 16) * mm, "radius": 2 * mm});
            skCircle(sketch, "E52.34.0.5", {"center": v(824, 16) * mm, "radius": 2 * mm});
            skArc(sketch, "E52.34.0.6", {"start": v(825.9, 7.07) * mm, "mid": v(825.9, 9.9) * mm, "end": v(823.07, 9.9) * mm});
            skArc(sketch, "E52.34.0.7", {"start": v(822.59, 9.41) * mm, "mid": v(822.59, 6.59) * mm, "end": v(825.41, 6.59) * mm});
            skLineSegment(sketch, "E52.34.0.8", {"start": v(823.07, 9.9) * mm, "end": v(822.59, 9.41) * mm});
            skLineSegment(sketch, "E52.34.0.9", {"start": v(825.9, 7.07) * mm, "end": v(825.41, 6.59) * mm});
            skArc(sketch, "E52.34.0.10", {"start": v(832.93, 9.9) * mm, "mid": v(830.1, 9.9) * mm, "end": v(830.1, 7.07) * mm});
            skLineSegment(sketch, "E52.34.0.11", {"start": v(832.93, 9.9) * mm, "end": v(833.41, 9.41) * mm});
            skArc(sketch, "E52.34.0.12", {"start": v(830.59, 6.59) * mm, "mid": v(833.41, 6.59) * mm, "end": v(833.41, 9.41) * mm});
            skLineSegment(sketch, "E52.34.0.13", {"start": v(830.1, 7.07) * mm, "end": v(830.59, 6.59) * mm});
            skCircle(sketch, "E52.34.0.14", {"center": v(840, 0) * mm, "radius": 7 * mm});
            skArc(sketch, "E52.34.0.15", {"start": v(823.07, -9.9) * mm, "mid": v(825.9, -9.9) * mm, "end": v(825.9, -7.07) * mm});
            skArc(sketch, "E52.34.0.16", {"start": v(825.41, -6.59) * mm, "mid": v(822.59, -6.59) * mm, "end": v(822.59, -9.41) * mm});
            skLineSegment(sketch, "E52.34.0.17", {"start": v(825.41, -6.59) * mm, "end": v(825.9, -7.07) * mm});
            skLineSegment(sketch, "E52.34.0.18", {"start": v(822.59, -9.41) * mm, "end": v(823.07, -9.9) * mm});
            skArc(sketch, "E52.34.0.19", {"start": v(830.1, -7.07) * mm, "mid": v(830.1, -9.9) * mm, "end": v(832.93, -9.9) * mm});
            skLineSegment(sketch, "E52.34.0.20", {"start": v(832.93, -9.9) * mm, "end": v(833.41, -9.41) * mm});
            skArc(sketch, "E52.34.0.21", {"start": v(833.41, -9.41) * mm, "mid": v(833.41, -6.59) * mm, "end": v(830.59, -6.59) * mm});
            skCircle(sketch, "E52.34.0.22", {"center": v(832, -16) * mm, "radius": 2 * mm});
            skCircle(sketch, "E52.34.0.23", {"center": v(824, -16) * mm, "radius": 2 * mm});
            skLineSegment(sketch, "E52.34.0.24", {"start": v(830.1, -7.07) * mm, "end": v(830.59, -6.59) * mm});
            skCircle(sketch, "E52.34.0.25", {"center": v(828, 0) * mm, "radius": 2 * mm});
            skArc(sketch, "E52.34.0.26", {"start": v(842, -12) * mm, "mid": v(840, -10) * mm, "end": v(838, -12) * mm});
            skArc(sketch, "E52.34.0.27", {"start": v(838, -16) * mm, "mid": v(840, -18) * mm, "end": v(842, -16) * mm});
            skLineSegment(sketch, "E52.34.0.28", {"start": v(838, -12) * mm, "end": v(838, -16) * mm});
            skLineSegment(sketch, "E52.34.0.29", {"start": v(842, -16) * mm, "end": v(842, -12) * mm});
            skArc(sketch, "E52.35.0.0", {"start": v(866, 16) * mm, "mid": v(864, 18) * mm, "end": v(862, 16) * mm});
            skLineSegment(sketch, "E52.35.0.1", {"start": v(866, 16) * mm, "end": v(866, 12) * mm});
            skLineSegment(sketch, "E52.35.0.2", {"start": v(862, 16) * mm, "end": v(862, 12) * mm});
            skArc(sketch, "E52.35.0.3", {"start": v(862, 12) * mm, "mid": v(864, 10) * mm, "end": v(866, 12) * mm});
            skCircle(sketch, "E52.35.0.4", {"center": v(856, 16) * mm, "radius": 2 * mm});
            skCircle(sketch, "E52.35.0.5", {"center": v(848, 16) * mm, "radius": 2 * mm});
            skArc(sketch, "E52.35.0.6", {"start": v(849.9, 7.07) * mm, "mid": v(849.9, 9.9) * mm, "end": v(847.07, 9.9) * mm});
            skArc(sketch, "E52.35.0.7", {"start": v(846.59, 9.41) * mm, "mid": v(846.59, 6.59) * mm, "end": v(849.41, 6.59) * mm});
            skLineSegment(sketch, "E52.35.0.8", {"start": v(847.07, 9.9) * mm, "end": v(846.59, 9.41) * mm});
            skLineSegment(sketch, "E52.35.0.9", {"start": v(849.9, 7.07) * mm, "end": v(849.41, 6.59) * mm});
            skArc(sketch, "E52.35.0.10", {"start": v(856.93, 9.9) * mm, "mid": v(854.1, 9.9) * mm, "end": v(854.1, 7.07) * mm});
            skLineSegment(sketch, "E52.35.0.11", {"start": v(856.93, 9.9) * mm, "end": v(857.41, 9.41) * mm});
            skArc(sketch, "E52.35.0.12", {"start": v(854.59, 6.59) * mm, "mid": v(857.41, 6.59) * mm, "end": v(857.41, 9.41) * mm});
            skLineSegment(sketch, "E52.35.0.13", {"start": v(854.1, 7.07) * mm, "end": v(854.59, 6.59) * mm});
            skCircle(sketch, "E52.35.0.14", {"center": v(864, 0) * mm, "radius": 7 * mm});
            skArc(sketch, "E52.35.0.15", {"start": v(847.07, -9.9) * mm, "mid": v(849.9, -9.9) * mm, "end": v(849.9, -7.07) * mm});
            skArc(sketch, "E52.35.0.16", {"start": v(849.41, -6.59) * mm, "mid": v(846.59, -6.59) * mm, "end": v(846.59, -9.41) * mm});
            skLineSegment(sketch, "E52.35.0.17", {"start": v(849.41, -6.59) * mm, "end": v(849.9, -7.07) * mm});
            skLineSegment(sketch, "E52.35.0.18", {"start": v(846.59, -9.41) * mm, "end": v(847.07, -9.9) * mm});
            skArc(sketch, "E52.35.0.19", {"start": v(854.1, -7.07) * mm, "mid": v(854.1, -9.9) * mm, "end": v(856.93, -9.9) * mm});
            skLineSegment(sketch, "E52.35.0.20", {"start": v(856.93, -9.9) * mm, "end": v(857.41, -9.41) * mm});
            skArc(sketch, "E52.35.0.21", {"start": v(857.41, -9.41) * mm, "mid": v(857.41, -6.59) * mm, "end": v(854.59, -6.59) * mm});
            skCircle(sketch, "E52.35.0.22", {"center": v(856, -16) * mm, "radius": 2 * mm});
            skCircle(sketch, "E52.35.0.23", {"center": v(848, -16) * mm, "radius": 2 * mm});
            skLineSegment(sketch, "E52.35.0.24", {"start": v(854.1, -7.07) * mm, "end": v(854.59, -6.59) * mm});
            skCircle(sketch, "E52.35.0.25", {"center": v(852, 0) * mm, "radius": 2 * mm});
            skArc(sketch, "E52.35.0.26", {"start": v(866, -12) * mm, "mid": v(864, -10) * mm, "end": v(862, -12) * mm});
            skArc(sketch, "E52.35.0.27", {"start": v(862, -16) * mm, "mid": v(864, -18) * mm, "end": v(866, -16) * mm});
            skLineSegment(sketch, "E52.35.0.28", {"start": v(862, -12) * mm, "end": v(862, -16) * mm});
            skLineSegment(sketch, "E52.35.0.29", {"start": v(866, -16) * mm, "end": v(866, -12) * mm});
            skArc(sketch, "E52.36.0.0", {"start": v(890, 16) * mm, "mid": v(888, 18) * mm, "end": v(886, 16) * mm});
            skLineSegment(sketch, "E52.36.0.1", {"start": v(890, 16) * mm, "end": v(890, 12) * mm});
            skLineSegment(sketch, "E52.36.0.2", {"start": v(886, 16) * mm, "end": v(886, 12) * mm});
            skArc(sketch, "E52.36.0.3", {"start": v(886, 12) * mm, "mid": v(888, 10) * mm, "end": v(890, 12) * mm});
            skCircle(sketch, "E52.36.0.4", {"center": v(880, 16) * mm, "radius": 2 * mm});
            skCircle(sketch, "E52.36.0.5", {"center": v(872, 16) * mm, "radius": 2 * mm});
            skArc(sketch, "E52.36.0.6", {"start": v(873.9, 7.07) * mm, "mid": v(873.9, 9.9) * mm, "end": v(871.07, 9.9) * mm});
            skArc(sketch, "E52.36.0.7", {"start": v(870.59, 9.41) * mm, "mid": v(870.59, 6.59) * mm, "end": v(873.41, 6.59) * mm});
            skLineSegment(sketch, "E52.36.0.8", {"start": v(871.07, 9.9) * mm, "end": v(870.59, 9.41) * mm});
            skLineSegment(sketch, "E52.36.0.9", {"start": v(873.9, 7.07) * mm, "end": v(873.41, 6.59) * mm});
            skArc(sketch, "E52.36.0.10", {"start": v(880.93, 9.9) * mm, "mid": v(878.1, 9.9) * mm, "end": v(878.1, 7.07) * mm});
            skLineSegment(sketch, "E52.36.0.11", {"start": v(880.93, 9.9) * mm, "end": v(881.41, 9.41) * mm});
            skArc(sketch, "E52.36.0.12", {"start": v(878.59, 6.59) * mm, "mid": v(881.41, 6.59) * mm, "end": v(881.41, 9.41) * mm});
            skLineSegment(sketch, "E52.36.0.13", {"start": v(878.1, 7.07) * mm, "end": v(878.59, 6.59) * mm});
            skCircle(sketch, "E52.36.0.14", {"center": v(888, 0) * mm, "radius": 7 * mm});
            skArc(sketch, "E52.36.0.15", {"start": v(871.07, -9.9) * mm, "mid": v(873.9, -9.9) * mm, "end": v(873.9, -7.07) * mm});
            skArc(sketch, "E52.36.0.16", {"start": v(873.41, -6.59) * mm, "mid": v(870.59, -6.59) * mm, "end": v(870.59, -9.41) * mm});
            skLineSegment(sketch, "E52.36.0.17", {"start": v(873.41, -6.59) * mm, "end": v(873.9, -7.07) * mm});
            skLineSegment(sketch, "E52.36.0.18", {"start": v(870.59, -9.41) * mm, "end": v(871.07, -9.9) * mm});
            skArc(sketch, "E52.36.0.19", {"start": v(878.1, -7.07) * mm, "mid": v(878.1, -9.9) * mm, "end": v(880.93, -9.9) * mm});
            skLineSegment(sketch, "E52.36.0.20", {"start": v(880.93, -9.9) * mm, "end": v(881.41, -9.41) * mm});
            skArc(sketch, "E52.36.0.21", {"start": v(881.41, -9.41) * mm, "mid": v(881.41, -6.59) * mm, "end": v(878.59, -6.59) * mm});
            skCircle(sketch, "E52.36.0.22", {"center": v(880, -16) * mm, "radius": 2 * mm});
            skCircle(sketch, "E52.36.0.23", {"center": v(872, -16) * mm, "radius": 2 * mm});
            skLineSegment(sketch, "E52.36.0.24", {"start": v(878.1, -7.07) * mm, "end": v(878.59, -6.59) * mm});
            skCircle(sketch, "E52.36.0.25", {"center": v(876, 0) * mm, "radius": 2 * mm});
            skArc(sketch, "E52.36.0.26", {"start": v(890, -12) * mm, "mid": v(888, -10) * mm, "end": v(886, -12) * mm});
            skArc(sketch, "E52.36.0.27", {"start": v(886, -16) * mm, "mid": v(888, -18) * mm, "end": v(890, -16) * mm});
            skLineSegment(sketch, "E52.36.0.28", {"start": v(886, -12) * mm, "end": v(886, -16) * mm});
            skLineSegment(sketch, "E52.36.0.29", {"start": v(890, -16) * mm, "end": v(890, -12) * mm});
            skArc(sketch, "E52.37.0.0", {"start": v(914, 16) * mm, "mid": v(912, 18) * mm, "end": v(910, 16) * mm});
            skLineSegment(sketch, "E52.37.0.1", {"start": v(914, 16) * mm, "end": v(914, 12) * mm});
            skLineSegment(sketch, "E52.37.0.2", {"start": v(910, 16) * mm, "end": v(910, 12) * mm});
            skArc(sketch, "E52.37.0.3", {"start": v(910, 12) * mm, "mid": v(912, 10) * mm, "end": v(914, 12) * mm});
            skCircle(sketch, "E52.37.0.4", {"center": v(904, 16) * mm, "radius": 2 * mm});
            skCircle(sketch, "E52.37.0.5", {"center": v(896, 16) * mm, "radius": 2 * mm});
            skArc(sketch, "E52.37.0.6", {"start": v(897.9, 7.07) * mm, "mid": v(897.9, 9.9) * mm, "end": v(895.07, 9.9) * mm});
            skArc(sketch, "E52.37.0.7", {"start": v(894.59, 9.41) * mm, "mid": v(894.59, 6.59) * mm, "end": v(897.41, 6.59) * mm});
            skLineSegment(sketch, "E52.37.0.8", {"start": v(895.07, 9.9) * mm, "end": v(894.59, 9.41) * mm});
            skLineSegment(sketch, "E52.37.0.9", {"start": v(897.9, 7.07) * mm, "end": v(897.41, 6.59) * mm});
            skArc(sketch, "E52.37.0.10", {"start": v(904.93, 9.9) * mm, "mid": v(902.1, 9.9) * mm, "end": v(902.1, 7.07) * mm});
            skLineSegment(sketch, "E52.37.0.11", {"start": v(904.93, 9.9) * mm, "end": v(905.41, 9.41) * mm});
            skArc(sketch, "E52.37.0.12", {"start": v(902.59, 6.59) * mm, "mid": v(905.41, 6.59) * mm, "end": v(905.41, 9.41) * mm});
            skLineSegment(sketch, "E52.37.0.13", {"start": v(902.1, 7.07) * mm, "end": v(902.59, 6.59) * mm});
            skCircle(sketch, "E52.37.0.14", {"center": v(912, 0) * mm, "radius": 7 * mm});
            skArc(sketch, "E52.37.0.15", {"start": v(895.07, -9.9) * mm, "mid": v(897.9, -9.9) * mm, "end": v(897.9, -7.07) * mm});
            skArc(sketch, "E52.37.0.16", {"start": v(897.41, -6.59) * mm, "mid": v(894.59, -6.59) * mm, "end": v(894.59, -9.41) * mm});
            skLineSegment(sketch, "E52.37.0.17", {"start": v(897.41, -6.59) * mm, "end": v(897.9, -7.07) * mm});
            skLineSegment(sketch, "E52.37.0.18", {"start": v(894.59, -9.41) * mm, "end": v(895.07, -9.9) * mm});
            skArc(sketch, "E52.37.0.19", {"start": v(902.1, -7.07) * mm, "mid": v(902.1, -9.9) * mm, "end": v(904.93, -9.9) * mm});
            skLineSegment(sketch, "E52.37.0.20", {"start": v(904.93, -9.9) * mm, "end": v(905.41, -9.41) * mm});
            skArc(sketch, "E52.37.0.21", {"start": v(905.41, -9.41) * mm, "mid": v(905.41, -6.59) * mm, "end": v(902.59, -6.59) * mm});
            skCircle(sketch, "E52.37.0.22", {"center": v(904, -16) * mm, "radius": 2 * mm});
            skCircle(sketch, "E52.37.0.23", {"center": v(896, -16) * mm, "radius": 2 * mm});
            skLineSegment(sketch, "E52.37.0.24", {"start": v(902.1, -7.07) * mm, "end": v(902.59, -6.59) * mm});
            skCircle(sketch, "E52.37.0.25", {"center": v(900, 0) * mm, "radius": 2 * mm});
            skArc(sketch, "E52.37.0.26", {"start": v(914, -12) * mm, "mid": v(912, -10) * mm, "end": v(910, -12) * mm});
            skArc(sketch, "E52.37.0.27", {"start": v(910, -16) * mm, "mid": v(912, -18) * mm, "end": v(914, -16) * mm});
            skLineSegment(sketch, "E52.37.0.28", {"start": v(910, -12) * mm, "end": v(910, -16) * mm});
            skLineSegment(sketch, "E52.37.0.29", {"start": v(914, -16) * mm, "end": v(914, -12) * mm});
            skArc(sketch, "E52.38.0.0", {"start": v(938, 16) * mm, "mid": v(936, 18) * mm, "end": v(934, 16) * mm});
            skLineSegment(sketch, "E52.38.0.1", {"start": v(938, 16) * mm, "end": v(938, 12) * mm});
            skLineSegment(sketch, "E52.38.0.2", {"start": v(934, 16) * mm, "end": v(934, 12) * mm});
            skArc(sketch, "E52.38.0.3", {"start": v(934, 12) * mm, "mid": v(936, 10) * mm, "end": v(938, 12) * mm});
            skCircle(sketch, "E52.38.0.4", {"center": v(928, 16) * mm, "radius": 2 * mm});
            skCircle(sketch, "E52.38.0.5", {"center": v(920, 16) * mm, "radius": 2 * mm});
            skArc(sketch, "E52.38.0.6", {"start": v(921.9, 7.07) * mm, "mid": v(921.9, 9.9) * mm, "end": v(919.07, 9.9) * mm});
            skArc(sketch, "E52.38.0.7", {"start": v(918.59, 9.41) * mm, "mid": v(918.59, 6.59) * mm, "end": v(921.41, 6.59) * mm});
            skLineSegment(sketch, "E52.38.0.8", {"start": v(919.07, 9.9) * mm, "end": v(918.59, 9.41) * mm});
            skLineSegment(sketch, "E52.38.0.9", {"start": v(921.9, 7.07) * mm, "end": v(921.41, 6.59) * mm});
            skArc(sketch, "E52.38.0.10", {"start": v(928.93, 9.9) * mm, "mid": v(926.1, 9.9) * mm, "end": v(926.1, 7.07) * mm});
            skLineSegment(sketch, "E52.38.0.11", {"start": v(928.93, 9.9) * mm, "end": v(929.41, 9.41) * mm});
            skArc(sketch, "E52.38.0.12", {"start": v(926.59, 6.59) * mm, "mid": v(929.41, 6.59) * mm, "end": v(929.41, 9.41) * mm});
            skLineSegment(sketch, "E52.38.0.13", {"start": v(926.1, 7.07) * mm, "end": v(926.59, 6.59) * mm});
            skCircle(sketch, "E52.38.0.14", {"center": v(936, 0) * mm, "radius": 7 * mm});
            skArc(sketch, "E52.38.0.15", {"start": v(919.07, -9.9) * mm, "mid": v(921.9, -9.9) * mm, "end": v(921.9, -7.07) * mm});
            skArc(sketch, "E52.38.0.16", {"start": v(921.41, -6.59) * mm, "mid": v(918.59, -6.59) * mm, "end": v(918.59, -9.41) * mm});
            skLineSegment(sketch, "E52.38.0.17", {"start": v(921.41, -6.59) * mm, "end": v(921.9, -7.07) * mm});
            skLineSegment(sketch, "E52.38.0.18", {"start": v(918.59, -9.41) * mm, "end": v(919.07, -9.9) * mm});
            skArc(sketch, "E52.38.0.19", {"start": v(926.1, -7.07) * mm, "mid": v(926.1, -9.9) * mm, "end": v(928.93, -9.9) * mm});
            skLineSegment(sketch, "E52.38.0.20", {"start": v(928.93, -9.9) * mm, "end": v(929.41, -9.41) * mm});
            skArc(sketch, "E52.38.0.21", {"start": v(929.41, -9.41) * mm, "mid": v(929.41, -6.59) * mm, "end": v(926.59, -6.59) * mm});
            skCircle(sketch, "E52.38.0.22", {"center": v(928, -16) * mm, "radius": 2 * mm});
            skCircle(sketch, "E52.38.0.23", {"center": v(920, -16) * mm, "radius": 2 * mm});
            skLineSegment(sketch, "E52.38.0.24", {"start": v(926.1, -7.07) * mm, "end": v(926.59, -6.59) * mm});
            skCircle(sketch, "E52.38.0.25", {"center": v(924, 0) * mm, "radius": 2 * mm});
            skArc(sketch, "E52.38.0.26", {"start": v(938, -12) * mm, "mid": v(936, -10) * mm, "end": v(934, -12) * mm});
            skArc(sketch, "E52.38.0.27", {"start": v(934, -16) * mm, "mid": v(936, -18) * mm, "end": v(938, -16) * mm});
            skLineSegment(sketch, "E52.38.0.28", {"start": v(934, -12) * mm, "end": v(934, -16) * mm});
            skLineSegment(sketch, "E52.38.0.29", {"start": v(938, -16) * mm, "end": v(938, -12) * mm});
            skArc(sketch, "E52.39.0.0", {"start": v(962, 16) * mm, "mid": v(960, 18) * mm, "end": v(958, 16) * mm});
            skLineSegment(sketch, "E52.39.0.1", {"start": v(962, 16) * mm, "end": v(962, 12) * mm});
            skLineSegment(sketch, "E52.39.0.2", {"start": v(958, 16) * mm, "end": v(958, 12) * mm});
            skArc(sketch, "E52.39.0.3", {"start": v(958, 12) * mm, "mid": v(960, 10) * mm, "end": v(962, 12) * mm});
            skCircle(sketch, "E52.39.0.4", {"center": v(952, 16) * mm, "radius": 2 * mm});
            skCircle(sketch, "E52.39.0.5", {"center": v(944, 16) * mm, "radius": 2 * mm});
            skArc(sketch, "E52.39.0.6", {"start": v(945.9, 7.07) * mm, "mid": v(945.9, 9.9) * mm, "end": v(943.07, 9.9) * mm});
            skArc(sketch, "E52.39.0.7", {"start": v(942.59, 9.41) * mm, "mid": v(942.59, 6.59) * mm, "end": v(945.41, 6.59) * mm});
            skLineSegment(sketch, "E52.39.0.8", {"start": v(943.07, 9.9) * mm, "end": v(942.59, 9.41) * mm});
            skLineSegment(sketch, "E52.39.0.9", {"start": v(945.9, 7.07) * mm, "end": v(945.41, 6.59) * mm});
            skArc(sketch, "E52.39.0.10", {"start": v(952.93, 9.9) * mm, "mid": v(950.1, 9.9) * mm, "end": v(950.1, 7.07) * mm});
            skLineSegment(sketch, "E52.39.0.11", {"start": v(952.93, 9.9) * mm, "end": v(953.41, 9.41) * mm});
            skArc(sketch, "E52.39.0.12", {"start": v(950.59, 6.59) * mm, "mid": v(953.41, 6.59) * mm, "end": v(953.41, 9.41) * mm});
            skLineSegment(sketch, "E52.39.0.13", {"start": v(950.1, 7.07) * mm, "end": v(950.59, 6.59) * mm});
            skCircle(sketch, "E52.39.0.14", {"center": v(960, 0) * mm, "radius": 7 * mm});
            skArc(sketch, "E52.39.0.15", {"start": v(943.07, -9.9) * mm, "mid": v(945.9, -9.9) * mm, "end": v(945.9, -7.07) * mm});
            skArc(sketch, "E52.39.0.16", {"start": v(945.41, -6.59) * mm, "mid": v(942.59, -6.59) * mm, "end": v(942.59, -9.41) * mm});
            skLineSegment(sketch, "E52.39.0.17", {"start": v(945.41, -6.59) * mm, "end": v(945.9, -7.07) * mm});
            skLineSegment(sketch, "E52.39.0.18", {"start": v(942.59, -9.41) * mm, "end": v(943.07, -9.9) * mm});
            skArc(sketch, "E52.39.0.19", {"start": v(950.1, -7.07) * mm, "mid": v(950.1, -9.9) * mm, "end": v(952.93, -9.9) * mm});
            skLineSegment(sketch, "E52.39.0.20", {"start": v(952.93, -9.9) * mm, "end": v(953.41, -9.41) * mm});
            skArc(sketch, "E52.39.0.21", {"start": v(953.41, -9.41) * mm, "mid": v(953.41, -6.59) * mm, "end": v(950.59, -6.59) * mm});
            skCircle(sketch, "E52.39.0.22", {"center": v(952, -16) * mm, "radius": 2 * mm});
            skCircle(sketch, "E52.39.0.23", {"center": v(944, -16) * mm, "radius": 2 * mm});
            skLineSegment(sketch, "E52.39.0.24", {"start": v(950.1, -7.07) * mm, "end": v(950.59, -6.59) * mm});
            skCircle(sketch, "E52.39.0.25", {"center": v(948, 0) * mm, "radius": 2 * mm});
            skArc(sketch, "E52.39.0.26", {"start": v(962, -12) * mm, "mid": v(960, -10) * mm, "end": v(958, -12) * mm});
            skArc(sketch, "E52.39.0.27", {"start": v(958, -16) * mm, "mid": v(960, -18) * mm, "end": v(962, -16) * mm});
            skLineSegment(sketch, "E52.39.0.28", {"start": v(958, -12) * mm, "end": v(958, -16) * mm});
            skLineSegment(sketch, "E52.39.0.29", {"start": v(962, -16) * mm, "end": v(962, -12) * mm});
            skArc(sketch, "E52.40.0.0", {"start": v(986, 16) * mm, "mid": v(984, 18) * mm, "end": v(982, 16) * mm});
            skLineSegment(sketch, "E52.40.0.1", {"start": v(986, 16) * mm, "end": v(986, 12) * mm});
            skLineSegment(sketch, "E52.40.0.2", {"start": v(982, 16) * mm, "end": v(982, 12) * mm});
            skArc(sketch, "E52.40.0.3", {"start": v(982, 12) * mm, "mid": v(984, 10) * mm, "end": v(986, 12) * mm});
            skCircle(sketch, "E52.40.0.4", {"center": v(976, 16) * mm, "radius": 2 * mm});
            skCircle(sketch, "E52.40.0.5", {"center": v(968, 16) * mm, "radius": 2 * mm});
            skArc(sketch, "E52.40.0.6", {"start": v(969.9, 7.07) * mm, "mid": v(969.9, 9.9) * mm, "end": v(967.07, 9.9) * mm});
            skArc(sketch, "E52.40.0.7", {"start": v(966.59, 9.41) * mm, "mid": v(966.59, 6.59) * mm, "end": v(969.41, 6.59) * mm});
            skLineSegment(sketch, "E52.40.0.8", {"start": v(967.07, 9.9) * mm, "end": v(966.59, 9.41) * mm});
            skLineSegment(sketch, "E52.40.0.9", {"start": v(969.9, 7.07) * mm, "end": v(969.41, 6.59) * mm});
            skArc(sketch, "E52.40.0.10", {"start": v(976.93, 9.9) * mm, "mid": v(974.1, 9.9) * mm, "end": v(974.1, 7.07) * mm});
            skLineSegment(sketch, "E52.40.0.11", {"start": v(976.93, 9.9) * mm, "end": v(977.41, 9.41) * mm});
            skArc(sketch, "E52.40.0.12", {"start": v(974.59, 6.59) * mm, "mid": v(977.41, 6.59) * mm, "end": v(977.41, 9.41) * mm});
            skLineSegment(sketch, "E52.40.0.13", {"start": v(974.1, 7.07) * mm, "end": v(974.59, 6.59) * mm});
            skCircle(sketch, "E52.40.0.14", {"center": v(984, 0) * mm, "radius": 7 * mm});
            skArc(sketch, "E52.40.0.15", {"start": v(967.07, -9.9) * mm, "mid": v(969.9, -9.9) * mm, "end": v(969.9, -7.07) * mm});
            skArc(sketch, "E52.40.0.16", {"start": v(969.41, -6.59) * mm, "mid": v(966.59, -6.59) * mm, "end": v(966.59, -9.41) * mm});
            skLineSegment(sketch, "E52.40.0.17", {"start": v(969.41, -6.59) * mm, "end": v(969.9, -7.07) * mm});
            skLineSegment(sketch, "E52.40.0.18", {"start": v(966.59, -9.41) * mm, "end": v(967.07, -9.9) * mm});
            skArc(sketch, "E52.40.0.19", {"start": v(974.1, -7.07) * mm, "mid": v(974.1, -9.9) * mm, "end": v(976.93, -9.9) * mm});
            skLineSegment(sketch, "E52.40.0.20", {"start": v(976.93, -9.9) * mm, "end": v(977.41, -9.41) * mm});
            skArc(sketch, "E52.40.0.21", {"start": v(977.41, -9.41) * mm, "mid": v(977.41, -6.59) * mm, "end": v(974.59, -6.59) * mm});
            skCircle(sketch, "E52.40.0.22", {"center": v(976, -16) * mm, "radius": 2 * mm});
            skCircle(sketch, "E52.40.0.23", {"center": v(968, -16) * mm, "radius": 2 * mm});
            skLineSegment(sketch, "E52.40.0.24", {"start": v(974.1, -7.07) * mm, "end": v(974.59, -6.59) * mm});
            skCircle(sketch, "E52.40.0.25", {"center": v(972, 0) * mm, "radius": 2 * mm});
            skArc(sketch, "E52.40.0.26", {"start": v(986, -12) * mm, "mid": v(984, -10) * mm, "end": v(982, -12) * mm});
            skArc(sketch, "E52.40.0.27", {"start": v(982, -16) * mm, "mid": v(984, -18) * mm, "end": v(986, -16) * mm});
            skLineSegment(sketch, "E52.40.0.28", {"start": v(982, -12) * mm, "end": v(982, -16) * mm});
            skLineSegment(sketch, "E52.40.0.29", {"start": v(986, -16) * mm, "end": v(986, -12) * mm});
            skArc(sketch, "E52.41.0.0", {"start": v(1010, 16) * mm, "mid": v(1008, 18) * mm, "end": v(1006, 16) * mm});
            skLineSegment(sketch, "E52.41.0.1", {"start": v(1010, 16) * mm, "end": v(1010, 12) * mm});
            skLineSegment(sketch, "E52.41.0.2", {"start": v(1006, 16) * mm, "end": v(1006, 12) * mm});
            skArc(sketch, "E52.41.0.3", {"start": v(1006, 12) * mm, "mid": v(1008, 10) * mm, "end": v(1010, 12) * mm});
            skCircle(sketch, "E52.41.0.4", {"center": v(1000, 16) * mm, "radius": 2 * mm});
            skCircle(sketch, "E52.41.0.5", {"center": v(992, 16) * mm, "radius": 2 * mm});
            skArc(sketch, "E52.41.0.6", {"start": v(993.9, 7.07) * mm, "mid": v(993.9, 9.9) * mm, "end": v(991.07, 9.9) * mm});
            skArc(sketch, "E52.41.0.7", {"start": v(990.59, 9.41) * mm, "mid": v(990.59, 6.59) * mm, "end": v(993.41, 6.59) * mm});
            skLineSegment(sketch, "E52.41.0.8", {"start": v(991.07, 9.9) * mm, "end": v(990.59, 9.41) * mm});
            skLineSegment(sketch, "E52.41.0.9", {"start": v(993.9, 7.07) * mm, "end": v(993.41, 6.59) * mm});
            skArc(sketch, "E52.41.0.10", {"start": v(1000.93, 9.9) * mm, "mid": v(998.1, 9.9) * mm, "end": v(998.1, 7.07) * mm});
            skLineSegment(sketch, "E52.41.0.11", {"start": v(1000.93, 9.9) * mm, "end": v(1001.41, 9.41) * mm});
            skArc(sketch, "E52.41.0.12", {"start": v(998.59, 6.59) * mm, "mid": v(1001.41, 6.59) * mm, "end": v(1001.41, 9.41) * mm});
            skLineSegment(sketch, "E52.41.0.13", {"start": v(998.1, 7.07) * mm, "end": v(998.59, 6.59) * mm});
            skCircle(sketch, "E52.41.0.14", {"center": v(1008, 0) * mm, "radius": 7 * mm});
            skArc(sketch, "E52.41.0.15", {"start": v(991.07, -9.9) * mm, "mid": v(993.9, -9.9) * mm, "end": v(993.9, -7.07) * mm});
            skArc(sketch, "E52.41.0.16", {"start": v(993.41, -6.59) * mm, "mid": v(990.59, -6.59) * mm, "end": v(990.59, -9.41) * mm});
            skLineSegment(sketch, "E52.41.0.17", {"start": v(993.41, -6.59) * mm, "end": v(993.9, -7.07) * mm});
            skLineSegment(sketch, "E52.41.0.18", {"start": v(990.59, -9.41) * mm, "end": v(991.07, -9.9) * mm});
            skArc(sketch, "E52.41.0.19", {"start": v(998.1, -7.07) * mm, "mid": v(998.1, -9.9) * mm, "end": v(1000.93, -9.9) * mm});
            skLineSegment(sketch, "E52.41.0.20", {"start": v(1000.93, -9.9) * mm, "end": v(1001.41, -9.41) * mm});
            skArc(sketch, "E52.41.0.21", {"start": v(1001.41, -9.41) * mm, "mid": v(1001.41, -6.59) * mm, "end": v(998.59, -6.59) * mm});
            skCircle(sketch, "E52.41.0.22", {"center": v(1000, -16) * mm, "radius": 2 * mm});
            skCircle(sketch, "E52.41.0.23", {"center": v(992, -16) * mm, "radius": 2 * mm});
            skLineSegment(sketch, "E52.41.0.24", {"start": v(998.1, -7.07) * mm, "end": v(998.59, -6.59) * mm});
            skCircle(sketch, "E52.41.0.25", {"center": v(996, 0) * mm, "radius": 2 * mm});
            skArc(sketch, "E52.41.0.26", {"start": v(1010, -12) * mm, "mid": v(1008, -10) * mm, "end": v(1006, -12) * mm});
            skArc(sketch, "E52.41.0.27", {"start": v(1006, -16) * mm, "mid": v(1008, -18) * mm, "end": v(1010, -16) * mm});
            skLineSegment(sketch, "E52.41.0.28", {"start": v(1006, -12) * mm, "end": v(1006, -16) * mm});
            skLineSegment(sketch, "E52.41.0.29", {"start": v(1010, -16) * mm, "end": v(1010, -12) * mm});
            skArc(sketch, "E52.42.0.0", {"start": v(1034, 16) * mm, "mid": v(1032, 18) * mm, "end": v(1030, 16) * mm});
            skLineSegment(sketch, "E52.42.0.1", {"start": v(1034, 16) * mm, "end": v(1034, 12) * mm});
            skLineSegment(sketch, "E52.42.0.2", {"start": v(1030, 16) * mm, "end": v(1030, 12) * mm});
            skArc(sketch, "E52.42.0.3", {"start": v(1030, 12) * mm, "mid": v(1032, 10) * mm, "end": v(1034, 12) * mm});
            skCircle(sketch, "E52.42.0.4", {"center": v(1024, 16) * mm, "radius": 2 * mm});
            skCircle(sketch, "E52.42.0.5", {"center": v(1016, 16) * mm, "radius": 2 * mm});
            skArc(sketch, "E52.42.0.6", {"start": v(1017.9, 7.07) * mm, "mid": v(1017.9, 9.9) * mm, "end": v(1015.07, 9.9) * mm});
            skArc(sketch, "E52.42.0.7", {"start": v(1014.59, 9.41) * mm, "mid": v(1014.59, 6.59) * mm, "end": v(1017.41, 6.59) * mm});
            skLineSegment(sketch, "E52.42.0.8", {"start": v(1015.07, 9.9) * mm, "end": v(1014.59, 9.41) * mm});
            skLineSegment(sketch, "E52.42.0.9", {"start": v(1017.9, 7.07) * mm, "end": v(1017.41, 6.59) * mm});
            skArc(sketch, "E52.42.0.10", {"start": v(1024.93, 9.9) * mm, "mid": v(1022.1, 9.9) * mm, "end": v(1022.1, 7.07) * mm});
            skLineSegment(sketch, "E52.42.0.11", {"start": v(1024.93, 9.9) * mm, "end": v(1025.41, 9.41) * mm});
            skArc(sketch, "E52.42.0.12", {"start": v(1022.59, 6.59) * mm, "mid": v(1025.41, 6.59) * mm, "end": v(1025.41, 9.41) * mm});
            skLineSegment(sketch, "E52.42.0.13", {"start": v(1022.1, 7.07) * mm, "end": v(1022.59, 6.59) * mm});
            skCircle(sketch, "E52.42.0.14", {"center": v(1032, 0) * mm, "radius": 7 * mm});
            skArc(sketch, "E52.42.0.15", {"start": v(1015.07, -9.9) * mm, "mid": v(1017.9, -9.9) * mm, "end": v(1017.9, -7.07) * mm});
            skArc(sketch, "E52.42.0.16", {"start": v(1017.41, -6.59) * mm, "mid": v(1014.59, -6.59) * mm, "end": v(1014.59, -9.41) * mm});
            skLineSegment(sketch, "E52.42.0.17", {"start": v(1017.41, -6.59) * mm, "end": v(1017.9, -7.07) * mm});
            skLineSegment(sketch, "E52.42.0.18", {"start": v(1014.59, -9.41) * mm, "end": v(1015.07, -9.9) * mm});
            skArc(sketch, "E52.42.0.19", {"start": v(1022.1, -7.07) * mm, "mid": v(1022.1, -9.9) * mm, "end": v(1024.93, -9.9) * mm});
            skLineSegment(sketch, "E52.42.0.20", {"start": v(1024.93, -9.9) * mm, "end": v(1025.41, -9.41) * mm});
            skArc(sketch, "E52.42.0.21", {"start": v(1025.41, -9.41) * mm, "mid": v(1025.41, -6.59) * mm, "end": v(1022.59, -6.59) * mm});
            skCircle(sketch, "E52.42.0.22", {"center": v(1024, -16) * mm, "radius": 2 * mm});
            skCircle(sketch, "E52.42.0.23", {"center": v(1016, -16) * mm, "radius": 2 * mm});
            skLineSegment(sketch, "E52.42.0.24", {"start": v(1022.1, -7.07) * mm, "end": v(1022.59, -6.59) * mm});
            skCircle(sketch, "E52.42.0.25", {"center": v(1020, 0) * mm, "radius": 2 * mm});
            skArc(sketch, "E52.42.0.26", {"start": v(1034, -12) * mm, "mid": v(1032, -10) * mm, "end": v(1030, -12) * mm});
            skArc(sketch, "E52.42.0.27", {"start": v(1030, -16) * mm, "mid": v(1032, -18) * mm, "end": v(1034, -16) * mm});
            skLineSegment(sketch, "E52.42.0.28", {"start": v(1030, -12) * mm, "end": v(1030, -16) * mm});
            skLineSegment(sketch, "E52.42.0.29", {"start": v(1034, -16) * mm, "end": v(1034, -12) * mm});
            skArc(sketch, "E52.43.0.0", {"start": v(1058, 16) * mm, "mid": v(1056, 18) * mm, "end": v(1054, 16) * mm});
            skLineSegment(sketch, "E52.43.0.1", {"start": v(1058, 16) * mm, "end": v(1058, 12) * mm});
            skLineSegment(sketch, "E52.43.0.2", {"start": v(1054, 16) * mm, "end": v(1054, 12) * mm});
            skArc(sketch, "E52.43.0.3", {"start": v(1054, 12) * mm, "mid": v(1056, 10) * mm, "end": v(1058, 12) * mm});
            skCircle(sketch, "E52.43.0.4", {"center": v(1048, 16) * mm, "radius": 2 * mm});
            skCircle(sketch, "E52.43.0.5", {"center": v(1040, 16) * mm, "radius": 2 * mm});
            skArc(sketch, "E52.43.0.6", {"start": v(1041.9, 7.07) * mm, "mid": v(1041.9, 9.9) * mm, "end": v(1039.07, 9.9) * mm});
            skArc(sketch, "E52.43.0.7", {"start": v(1038.59, 9.41) * mm, "mid": v(1038.59, 6.59) * mm, "end": v(1041.41, 6.59) * mm});
            skLineSegment(sketch, "E52.43.0.8", {"start": v(1039.07, 9.9) * mm, "end": v(1038.59, 9.41) * mm});
            skLineSegment(sketch, "E52.43.0.9", {"start": v(1041.9, 7.07) * mm, "end": v(1041.41, 6.59) * mm});
            skArc(sketch, "E52.43.0.10", {"start": v(1048.93, 9.9) * mm, "mid": v(1046.1, 9.9) * mm, "end": v(1046.1, 7.07) * mm});
            skLineSegment(sketch, "E52.43.0.11", {"start": v(1048.93, 9.9) * mm, "end": v(1049.41, 9.41) * mm});
            skArc(sketch, "E52.43.0.12", {"start": v(1046.59, 6.59) * mm, "mid": v(1049.41, 6.59) * mm, "end": v(1049.41, 9.41) * mm});
            skLineSegment(sketch, "E52.43.0.13", {"start": v(1046.1, 7.07) * mm, "end": v(1046.59, 6.59) * mm});
            skCircle(sketch, "E52.43.0.14", {"center": v(1056, 0) * mm, "radius": 7 * mm});
            skArc(sketch, "E52.43.0.15", {"start": v(1039.07, -9.9) * mm, "mid": v(1041.9, -9.9) * mm, "end": v(1041.9, -7.07) * mm});
            skArc(sketch, "E52.43.0.16", {"start": v(1041.41, -6.59) * mm, "mid": v(1038.59, -6.59) * mm, "end": v(1038.59, -9.41) * mm});
            skLineSegment(sketch, "E52.43.0.17", {"start": v(1041.41, -6.59) * mm, "end": v(1041.9, -7.07) * mm});
            skLineSegment(sketch, "E52.43.0.18", {"start": v(1038.59, -9.41) * mm, "end": v(1039.07, -9.9) * mm});
            skArc(sketch, "E52.43.0.19", {"start": v(1046.1, -7.07) * mm, "mid": v(1046.1, -9.9) * mm, "end": v(1048.93, -9.9) * mm});
            skLineSegment(sketch, "E52.43.0.20", {"start": v(1048.93, -9.9) * mm, "end": v(1049.41, -9.41) * mm});
            skArc(sketch, "E52.43.0.21", {"start": v(1049.41, -9.41) * mm, "mid": v(1049.41, -6.59) * mm, "end": v(1046.59, -6.59) * mm});
            skCircle(sketch, "E52.43.0.22", {"center": v(1048, -16) * mm, "radius": 2 * mm});
            skCircle(sketch, "E52.43.0.23", {"center": v(1040, -16) * mm, "radius": 2 * mm});
            skLineSegment(sketch, "E52.43.0.24", {"start": v(1046.1, -7.07) * mm, "end": v(1046.59, -6.59) * mm});
            skCircle(sketch, "E52.43.0.25", {"center": v(1044, 0) * mm, "radius": 2 * mm});
            skArc(sketch, "E52.43.0.26", {"start": v(1058, -12) * mm, "mid": v(1056, -10) * mm, "end": v(1054, -12) * mm});
            skArc(sketch, "E52.43.0.27", {"start": v(1054, -16) * mm, "mid": v(1056, -18) * mm, "end": v(1058, -16) * mm});
            skLineSegment(sketch, "E52.43.0.28", {"start": v(1054, -12) * mm, "end": v(1054, -16) * mm});
            skLineSegment(sketch, "E52.43.0.29", {"start": v(1058, -16) * mm, "end": v(1058, -12) * mm});
            skArc(sketch, "E52.44.0.0", {"start": v(1082, 16) * mm, "mid": v(1080, 18) * mm, "end": v(1078, 16) * mm});
            skLineSegment(sketch, "E52.44.0.1", {"start": v(1082, 16) * mm, "end": v(1082, 12) * mm});
            skLineSegment(sketch, "E52.44.0.2", {"start": v(1078, 16) * mm, "end": v(1078, 12) * mm});
            skArc(sketch, "E52.44.0.3", {"start": v(1078, 12) * mm, "mid": v(1080, 10) * mm, "end": v(1082, 12) * mm});
            skCircle(sketch, "E52.44.0.4", {"center": v(1072, 16) * mm, "radius": 2 * mm});
            skCircle(sketch, "E52.44.0.5", {"center": v(1064, 16) * mm, "radius": 2 * mm});
            skArc(sketch, "E52.44.0.6", {"start": v(1065.9, 7.07) * mm, "mid": v(1065.9, 9.9) * mm, "end": v(1063.07, 9.9) * mm});
            skArc(sketch, "E52.44.0.7", {"start": v(1062.59, 9.41) * mm, "mid": v(1062.59, 6.59) * mm, "end": v(1065.41, 6.59) * mm});
            skLineSegment(sketch, "E52.44.0.8", {"start": v(1063.07, 9.9) * mm, "end": v(1062.59, 9.41) * mm});
            skLineSegment(sketch, "E52.44.0.9", {"start": v(1065.9, 7.07) * mm, "end": v(1065.41, 6.59) * mm});
            skArc(sketch, "E52.44.0.10", {"start": v(1072.93, 9.9) * mm, "mid": v(1070.1, 9.9) * mm, "end": v(1070.1, 7.07) * mm});
            skLineSegment(sketch, "E52.44.0.11", {"start": v(1072.93, 9.9) * mm, "end": v(1073.41, 9.41) * mm});
            skArc(sketch, "E52.44.0.12", {"start": v(1070.59, 6.59) * mm, "mid": v(1073.41, 6.59) * mm, "end": v(1073.41, 9.41) * mm});
            skLineSegment(sketch, "E52.44.0.13", {"start": v(1070.1, 7.07) * mm, "end": v(1070.59, 6.59) * mm});
            skCircle(sketch, "E52.44.0.14", {"center": v(1080, 0) * mm, "radius": 7 * mm});
            skArc(sketch, "E52.44.0.15", {"start": v(1063.07, -9.9) * mm, "mid": v(1065.9, -9.9) * mm, "end": v(1065.9, -7.07) * mm});
            skArc(sketch, "E52.44.0.16", {"start": v(1065.41, -6.59) * mm, "mid": v(1062.59, -6.59) * mm, "end": v(1062.59, -9.41) * mm});
            skLineSegment(sketch, "E52.44.0.17", {"start": v(1065.41, -6.59) * mm, "end": v(1065.9, -7.07) * mm});
            skLineSegment(sketch, "E52.44.0.18", {"start": v(1062.59, -9.41) * mm, "end": v(1063.07, -9.9) * mm});
            skArc(sketch, "E52.44.0.19", {"start": v(1070.1, -7.07) * mm, "mid": v(1070.1, -9.9) * mm, "end": v(1072.93, -9.9) * mm});
            skLineSegment(sketch, "E52.44.0.20", {"start": v(1072.93, -9.9) * mm, "end": v(1073.41, -9.41) * mm});
            skArc(sketch, "E52.44.0.21", {"start": v(1073.41, -9.41) * mm, "mid": v(1073.41, -6.59) * mm, "end": v(1070.59, -6.59) * mm});
            skCircle(sketch, "E52.44.0.22", {"center": v(1072, -16) * mm, "radius": 2 * mm});
            skCircle(sketch, "E52.44.0.23", {"center": v(1064, -16) * mm, "radius": 2 * mm});
            skLineSegment(sketch, "E52.44.0.24", {"start": v(1070.1, -7.07) * mm, "end": v(1070.59, -6.59) * mm});
            skCircle(sketch, "E52.44.0.25", {"center": v(1068, 0) * mm, "radius": 2 * mm});
            skArc(sketch, "E52.44.0.26", {"start": v(1082, -12) * mm, "mid": v(1080, -10) * mm, "end": v(1078, -12) * mm});
            skArc(sketch, "E52.44.0.27", {"start": v(1078, -16) * mm, "mid": v(1080, -18) * mm, "end": v(1082, -16) * mm});
            skLineSegment(sketch, "E52.44.0.28", {"start": v(1078, -12) * mm, "end": v(1078, -16) * mm});
            skLineSegment(sketch, "E52.44.0.29", {"start": v(1082, -16) * mm, "end": v(1082, -12) * mm});
            skArc(sketch, "E52.45.0.0", {"start": v(1106, 16) * mm, "mid": v(1104, 18) * mm, "end": v(1102, 16) * mm});
            skLineSegment(sketch, "E52.45.0.1", {"start": v(1106, 16) * mm, "end": v(1106, 12) * mm});
            skLineSegment(sketch, "E52.45.0.2", {"start": v(1102, 16) * mm, "end": v(1102, 12) * mm});
            skArc(sketch, "E52.45.0.3", {"start": v(1102, 12) * mm, "mid": v(1104, 10) * mm, "end": v(1106, 12) * mm});
            skCircle(sketch, "E52.45.0.4", {"center": v(1096, 16) * mm, "radius": 2 * mm});
            skCircle(sketch, "E52.45.0.5", {"center": v(1088, 16) * mm, "radius": 2 * mm});
            skArc(sketch, "E52.45.0.6", {"start": v(1089.9, 7.07) * mm, "mid": v(1089.9, 9.9) * mm, "end": v(1087.07, 9.9) * mm});
            skArc(sketch, "E52.45.0.7", {"start": v(1086.59, 9.41) * mm, "mid": v(1086.59, 6.59) * mm, "end": v(1089.41, 6.59) * mm});
            skLineSegment(sketch, "E52.45.0.8", {"start": v(1087.07, 9.9) * mm, "end": v(1086.59, 9.41) * mm});
            skLineSegment(sketch, "E52.45.0.9", {"start": v(1089.9, 7.07) * mm, "end": v(1089.41, 6.59) * mm});
            skArc(sketch, "E52.45.0.10", {"start": v(1096.93, 9.9) * mm, "mid": v(1094.1, 9.9) * mm, "end": v(1094.1, 7.07) * mm});
            skLineSegment(sketch, "E52.45.0.11", {"start": v(1096.93, 9.9) * mm, "end": v(1097.41, 9.41) * mm});
            skArc(sketch, "E52.45.0.12", {"start": v(1094.59, 6.59) * mm, "mid": v(1097.41, 6.59) * mm, "end": v(1097.41, 9.41) * mm});
            skLineSegment(sketch, "E52.45.0.13", {"start": v(1094.1, 7.07) * mm, "end": v(1094.59, 6.59) * mm});
            skCircle(sketch, "E52.45.0.14", {"center": v(1104, 0) * mm, "radius": 7 * mm});
            skArc(sketch, "E52.45.0.15", {"start": v(1087.07, -9.9) * mm, "mid": v(1089.9, -9.9) * mm, "end": v(1089.9, -7.07) * mm});
            skArc(sketch, "E52.45.0.16", {"start": v(1089.41, -6.59) * mm, "mid": v(1086.59, -6.59) * mm, "end": v(1086.59, -9.41) * mm});
            skLineSegment(sketch, "E52.45.0.17", {"start": v(1089.41, -6.59) * mm, "end": v(1089.9, -7.07) * mm});
            skLineSegment(sketch, "E52.45.0.18", {"start": v(1086.59, -9.41) * mm, "end": v(1087.07, -9.9) * mm});
            skArc(sketch, "E52.45.0.19", {"start": v(1094.1, -7.07) * mm, "mid": v(1094.1, -9.9) * mm, "end": v(1096.93, -9.9) * mm});
            skLineSegment(sketch, "E52.45.0.20", {"start": v(1096.93, -9.9) * mm, "end": v(1097.41, -9.41) * mm});
            skArc(sketch, "E52.45.0.21", {"start": v(1097.41, -9.41) * mm, "mid": v(1097.41, -6.59) * mm, "end": v(1094.59, -6.59) * mm});
            skCircle(sketch, "E52.45.0.22", {"center": v(1096, -16) * mm, "radius": 2 * mm});
            skCircle(sketch, "E52.45.0.23", {"center": v(1088, -16) * mm, "radius": 2 * mm});
            skLineSegment(sketch, "E52.45.0.24", {"start": v(1094.1, -7.07) * mm, "end": v(1094.59, -6.59) * mm});
            skCircle(sketch, "E52.45.0.25", {"center": v(1092, 0) * mm, "radius": 2 * mm});
            skArc(sketch, "E52.45.0.26", {"start": v(1106, -12) * mm, "mid": v(1104, -10) * mm, "end": v(1102, -12) * mm});
            skArc(sketch, "E52.45.0.27", {"start": v(1102, -16) * mm, "mid": v(1104, -18) * mm, "end": v(1106, -16) * mm});
            skLineSegment(sketch, "E52.45.0.28", {"start": v(1102, -12) * mm, "end": v(1102, -16) * mm});
            skLineSegment(sketch, "E52.45.0.29", {"start": v(1106, -16) * mm, "end": v(1106, -12) * mm});
            skArc(sketch, "E52.46.0.0", {"start": v(1130, 16) * mm, "mid": v(1128, 18) * mm, "end": v(1126, 16) * mm});
            skLineSegment(sketch, "E52.46.0.1", {"start": v(1130, 16) * mm, "end": v(1130, 12) * mm});
            skLineSegment(sketch, "E52.46.0.2", {"start": v(1126, 16) * mm, "end": v(1126, 12) * mm});
            skArc(sketch, "E52.46.0.3", {"start": v(1126, 12) * mm, "mid": v(1128, 10) * mm, "end": v(1130, 12) * mm});
            skCircle(sketch, "E52.46.0.4", {"center": v(1120, 16) * mm, "radius": 2 * mm});
            skCircle(sketch, "E52.46.0.5", {"center": v(1112, 16) * mm, "radius": 2 * mm});
            skArc(sketch, "E52.46.0.6", {"start": v(1113.9, 7.07) * mm, "mid": v(1113.9, 9.9) * mm, "end": v(1111.07, 9.9) * mm});
            skArc(sketch, "E52.46.0.7", {"start": v(1110.59, 9.41) * mm, "mid": v(1110.59, 6.59) * mm, "end": v(1113.41, 6.59) * mm});
            skLineSegment(sketch, "E52.46.0.8", {"start": v(1111.07, 9.9) * mm, "end": v(1110.59, 9.41) * mm});
            skLineSegment(sketch, "E52.46.0.9", {"start": v(1113.9, 7.07) * mm, "end": v(1113.41, 6.59) * mm});
            skArc(sketch, "E52.46.0.10", {"start": v(1120.93, 9.9) * mm, "mid": v(1118.1, 9.9) * mm, "end": v(1118.1, 7.07) * mm});
            skLineSegment(sketch, "E52.46.0.11", {"start": v(1120.93, 9.9) * mm, "end": v(1121.41, 9.41) * mm});
            skArc(sketch, "E52.46.0.12", {"start": v(1118.59, 6.59) * mm, "mid": v(1121.41, 6.59) * mm, "end": v(1121.41, 9.41) * mm});
            skLineSegment(sketch, "E52.46.0.13", {"start": v(1118.1, 7.07) * mm, "end": v(1118.59, 6.59) * mm});
            skCircle(sketch, "E52.46.0.14", {"center": v(1128, 0) * mm, "radius": 7 * mm});
            skArc(sketch, "E52.46.0.15", {"start": v(1111.07, -9.9) * mm, "mid": v(1113.9, -9.9) * mm, "end": v(1113.9, -7.07) * mm});
            skArc(sketch, "E52.46.0.16", {"start": v(1113.41, -6.59) * mm, "mid": v(1110.59, -6.59) * mm, "end": v(1110.59, -9.41) * mm});
            skLineSegment(sketch, "E52.46.0.17", {"start": v(1113.41, -6.59) * mm, "end": v(1113.9, -7.07) * mm});
            skLineSegment(sketch, "E52.46.0.18", {"start": v(1110.59, -9.41) * mm, "end": v(1111.07, -9.9) * mm});
            skArc(sketch, "E52.46.0.19", {"start": v(1118.1, -7.07) * mm, "mid": v(1118.1, -9.9) * mm, "end": v(1120.93, -9.9) * mm});
            skLineSegment(sketch, "E52.46.0.20", {"start": v(1120.93, -9.9) * mm, "end": v(1121.41, -9.41) * mm});
            skArc(sketch, "E52.46.0.21", {"start": v(1121.41, -9.41) * mm, "mid": v(1121.41, -6.59) * mm, "end": v(1118.59, -6.59) * mm});
            skCircle(sketch, "E52.46.0.22", {"center": v(1120, -16) * mm, "radius": 2 * mm});
            skCircle(sketch, "E52.46.0.23", {"center": v(1112, -16) * mm, "radius": 2 * mm});
            skLineSegment(sketch, "E52.46.0.24", {"start": v(1118.1, -7.07) * mm, "end": v(1118.59, -6.59) * mm});
            skCircle(sketch, "E52.46.0.25", {"center": v(1116, 0) * mm, "radius": 2 * mm});
            skArc(sketch, "E52.46.0.26", {"start": v(1130, -12) * mm, "mid": v(1128, -10) * mm, "end": v(1126, -12) * mm});
            skArc(sketch, "E52.46.0.27", {"start": v(1126, -16) * mm, "mid": v(1128, -18) * mm, "end": v(1130, -16) * mm});
            skLineSegment(sketch, "E52.46.0.28", {"start": v(1126, -12) * mm, "end": v(1126, -16) * mm});
            skLineSegment(sketch, "E52.46.0.29", {"start": v(1130, -16) * mm, "end": v(1130, -12) * mm});
            skArc(sketch, "E52.47.0.0", {"start": v(1154, 16) * mm, "mid": v(1152, 18) * mm, "end": v(1150, 16) * mm});
            skLineSegment(sketch, "E52.47.0.1", {"start": v(1154, 16) * mm, "end": v(1154, 12) * mm});
            skLineSegment(sketch, "E52.47.0.2", {"start": v(1150, 16) * mm, "end": v(1150, 12) * mm});
            skArc(sketch, "E52.47.0.3", {"start": v(1150, 12) * mm, "mid": v(1152, 10) * mm, "end": v(1154, 12) * mm});
            skCircle(sketch, "E52.47.0.4", {"center": v(1144, 16) * mm, "radius": 2 * mm});
            skCircle(sketch, "E52.47.0.5", {"center": v(1136, 16) * mm, "radius": 2 * mm});
            skArc(sketch, "E52.47.0.6", {"start": v(1137.9, 7.07) * mm, "mid": v(1137.9, 9.9) * mm, "end": v(1135.07, 9.9) * mm});
            skArc(sketch, "E52.47.0.7", {"start": v(1134.59, 9.41) * mm, "mid": v(1134.59, 6.59) * mm, "end": v(1137.41, 6.59) * mm});
            skLineSegment(sketch, "E52.47.0.8", {"start": v(1135.07, 9.9) * mm, "end": v(1134.59, 9.41) * mm});
            skLineSegment(sketch, "E52.47.0.9", {"start": v(1137.9, 7.07) * mm, "end": v(1137.41, 6.59) * mm});
            skArc(sketch, "E52.47.0.10", {"start": v(1144.93, 9.9) * mm, "mid": v(1142.1, 9.9) * mm, "end": v(1142.1, 7.07) * mm});
            skLineSegment(sketch, "E52.47.0.11", {"start": v(1144.93, 9.9) * mm, "end": v(1145.41, 9.41) * mm});
            skArc(sketch, "E52.47.0.12", {"start": v(1142.59, 6.59) * mm, "mid": v(1145.41, 6.59) * mm, "end": v(1145.41, 9.41) * mm});
            skLineSegment(sketch, "E52.47.0.13", {"start": v(1142.1, 7.07) * mm, "end": v(1142.59, 6.59) * mm});
            skCircle(sketch, "E52.47.0.14", {"center": v(1152, 0) * mm, "radius": 7 * mm});
            skArc(sketch, "E52.47.0.15", {"start": v(1135.07, -9.9) * mm, "mid": v(1137.9, -9.9) * mm, "end": v(1137.9, -7.07) * mm});
            skArc(sketch, "E52.47.0.16", {"start": v(1137.41, -6.59) * mm, "mid": v(1134.59, -6.59) * mm, "end": v(1134.59, -9.41) * mm});
            skLineSegment(sketch, "E52.47.0.17", {"start": v(1137.41, -6.59) * mm, "end": v(1137.9, -7.07) * mm});
            skLineSegment(sketch, "E52.47.0.18", {"start": v(1134.59, -9.41) * mm, "end": v(1135.07, -9.9) * mm});
            skArc(sketch, "E52.47.0.19", {"start": v(1142.1, -7.07) * mm, "mid": v(1142.1, -9.9) * mm, "end": v(1144.93, -9.9) * mm});
            skLineSegment(sketch, "E52.47.0.20", {"start": v(1144.93, -9.9) * mm, "end": v(1145.41, -9.41) * mm});
            skArc(sketch, "E52.47.0.21", {"start": v(1145.41, -9.41) * mm, "mid": v(1145.41, -6.59) * mm, "end": v(1142.59, -6.59) * mm});
            skCircle(sketch, "E52.47.0.22", {"center": v(1144, -16) * mm, "radius": 2 * mm});
            skCircle(sketch, "E52.47.0.23", {"center": v(1136, -16) * mm, "radius": 2 * mm});
            skLineSegment(sketch, "E52.47.0.24", {"start": v(1142.1, -7.07) * mm, "end": v(1142.59, -6.59) * mm});
            skCircle(sketch, "E52.47.0.25", {"center": v(1140, 0) * mm, "radius": 2 * mm});
            skArc(sketch, "E52.47.0.26", {"start": v(1154, -12) * mm, "mid": v(1152, -10) * mm, "end": v(1150, -12) * mm});
            skArc(sketch, "E52.47.0.27", {"start": v(1150, -16) * mm, "mid": v(1152, -18) * mm, "end": v(1154, -16) * mm});
            skLineSegment(sketch, "E52.47.0.28", {"start": v(1150, -12) * mm, "end": v(1150, -16) * mm});
            skLineSegment(sketch, "E52.47.0.29", {"start": v(1154, -16) * mm, "end": v(1154, -12) * mm});
            skArc(sketch, "E52.48.0.0", {"start": v(1178, 16) * mm, "mid": v(1176, 18) * mm, "end": v(1174, 16) * mm});
            skLineSegment(sketch, "E52.48.0.1", {"start": v(1178, 16) * mm, "end": v(1178, 12) * mm});
            skLineSegment(sketch, "E52.48.0.2", {"start": v(1174, 16) * mm, "end": v(1174, 12) * mm});
            skArc(sketch, "E52.48.0.3", {"start": v(1174, 12) * mm, "mid": v(1176, 10) * mm, "end": v(1178, 12) * mm});
            skCircle(sketch, "E52.48.0.4", {"center": v(1168, 16) * mm, "radius": 2 * mm});
            skCircle(sketch, "E52.48.0.5", {"center": v(1160, 16) * mm, "radius": 2 * mm});
            skArc(sketch, "E52.48.0.6", {"start": v(1161.9, 7.07) * mm, "mid": v(1161.9, 9.9) * mm, "end": v(1159.07, 9.9) * mm});
            skArc(sketch, "E52.48.0.7", {"start": v(1158.59, 9.41) * mm, "mid": v(1158.59, 6.59) * mm, "end": v(1161.41, 6.59) * mm});
            skLineSegment(sketch, "E52.48.0.8", {"start": v(1159.07, 9.9) * mm, "end": v(1158.59, 9.41) * mm});
            skLineSegment(sketch, "E52.48.0.9", {"start": v(1161.9, 7.07) * mm, "end": v(1161.41, 6.59) * mm});
            skArc(sketch, "E52.48.0.10", {"start": v(1168.93, 9.9) * mm, "mid": v(1166.1, 9.9) * mm, "end": v(1166.1, 7.07) * mm});
            skLineSegment(sketch, "E52.48.0.11", {"start": v(1168.93, 9.9) * mm, "end": v(1169.41, 9.41) * mm});
            skArc(sketch, "E52.48.0.12", {"start": v(1166.59, 6.59) * mm, "mid": v(1169.41, 6.59) * mm, "end": v(1169.41, 9.41) * mm});
            skLineSegment(sketch, "E52.48.0.13", {"start": v(1166.1, 7.07) * mm, "end": v(1166.59, 6.59) * mm});
            skCircle(sketch, "E52.48.0.14", {"center": v(1176, 0) * mm, "radius": 7 * mm});
            skArc(sketch, "E52.48.0.15", {"start": v(1159.07, -9.9) * mm, "mid": v(1161.9, -9.9) * mm, "end": v(1161.9, -7.07) * mm});
            skArc(sketch, "E52.48.0.16", {"start": v(1161.41, -6.59) * mm, "mid": v(1158.59, -6.59) * mm, "end": v(1158.59, -9.41) * mm});
            skLineSegment(sketch, "E52.48.0.17", {"start": v(1161.41, -6.59) * mm, "end": v(1161.9, -7.07) * mm});
            skLineSegment(sketch, "E52.48.0.18", {"start": v(1158.59, -9.41) * mm, "end": v(1159.07, -9.9) * mm});
            skArc(sketch, "E52.48.0.19", {"start": v(1166.1, -7.07) * mm, "mid": v(1166.1, -9.9) * mm, "end": v(1168.93, -9.9) * mm});
            skLineSegment(sketch, "E52.48.0.20", {"start": v(1168.93, -9.9) * mm, "end": v(1169.41, -9.41) * mm});
            skArc(sketch, "E52.48.0.21", {"start": v(1169.41, -9.41) * mm, "mid": v(1169.41, -6.59) * mm, "end": v(1166.59, -6.59) * mm});
            skCircle(sketch, "E52.48.0.22", {"center": v(1168, -16) * mm, "radius": 2 * mm});
            skCircle(sketch, "E52.48.0.23", {"center": v(1160, -16) * mm, "radius": 2 * mm});
            skLineSegment(sketch, "E52.48.0.24", {"start": v(1166.1, -7.07) * mm, "end": v(1166.59, -6.59) * mm});
            skCircle(sketch, "E52.48.0.25", {"center": v(1164, 0) * mm, "radius": 2 * mm});
            skArc(sketch, "E52.48.0.26", {"start": v(1178, -12) * mm, "mid": v(1176, -10) * mm, "end": v(1174, -12) * mm});
            skArc(sketch, "E52.48.0.27", {"start": v(1174, -16) * mm, "mid": v(1176, -18) * mm, "end": v(1178, -16) * mm});
            skLineSegment(sketch, "E52.48.0.28", {"start": v(1174, -12) * mm, "end": v(1174, -16) * mm});
            skLineSegment(sketch, "E52.48.0.29", {"start": v(1178, -16) * mm, "end": v(1178, -12) * mm});
            skArc(sketch, "E52.49.0.0", {"start": v(1202, 16) * mm, "mid": v(1200, 18) * mm, "end": v(1198, 16) * mm});
            skLineSegment(sketch, "E52.49.0.1", {"start": v(1202, 16) * mm, "end": v(1202, 12) * mm});
            skLineSegment(sketch, "E52.49.0.2", {"start": v(1198, 16) * mm, "end": v(1198, 12) * mm});
            skArc(sketch, "E52.49.0.3", {"start": v(1198, 12) * mm, "mid": v(1200, 10) * mm, "end": v(1202, 12) * mm});
            skCircle(sketch, "E52.49.0.4", {"center": v(1192, 16) * mm, "radius": 2 * mm});
            skCircle(sketch, "E52.49.0.5", {"center": v(1184, 16) * mm, "radius": 2 * mm});
            skArc(sketch, "E52.49.0.6", {"start": v(1185.9, 7.07) * mm, "mid": v(1185.9, 9.9) * mm, "end": v(1183.07, 9.9) * mm});
            skArc(sketch, "E52.49.0.7", {"start": v(1182.59, 9.41) * mm, "mid": v(1182.59, 6.59) * mm, "end": v(1185.41, 6.59) * mm});
            skLineSegment(sketch, "E52.49.0.8", {"start": v(1183.07, 9.9) * mm, "end": v(1182.59, 9.41) * mm});
            skLineSegment(sketch, "E52.49.0.9", {"start": v(1185.9, 7.07) * mm, "end": v(1185.41, 6.59) * mm});
            skArc(sketch, "E52.49.0.10", {"start": v(1192.93, 9.9) * mm, "mid": v(1190.1, 9.9) * mm, "end": v(1190.1, 7.07) * mm});
            skLineSegment(sketch, "E52.49.0.11", {"start": v(1192.93, 9.9) * mm, "end": v(1193.41, 9.41) * mm});
            skArc(sketch, "E52.49.0.12", {"start": v(1190.59, 6.59) * mm, "mid": v(1193.41, 6.59) * mm, "end": v(1193.41, 9.41) * mm});
            skLineSegment(sketch, "E52.49.0.13", {"start": v(1190.1, 7.07) * mm, "end": v(1190.59, 6.59) * mm});
            skCircle(sketch, "E52.49.0.14", {"center": v(1200, 0) * mm, "radius": 7 * mm});
            skArc(sketch, "E52.49.0.15", {"start": v(1183.07, -9.9) * mm, "mid": v(1185.9, -9.9) * mm, "end": v(1185.9, -7.07) * mm});
            skArc(sketch, "E52.49.0.16", {"start": v(1185.41, -6.59) * mm, "mid": v(1182.59, -6.59) * mm, "end": v(1182.59, -9.41) * mm});
            skLineSegment(sketch, "E52.49.0.17", {"start": v(1185.41, -6.59) * mm, "end": v(1185.9, -7.07) * mm});
            skLineSegment(sketch, "E52.49.0.18", {"start": v(1182.59, -9.41) * mm, "end": v(1183.07, -9.9) * mm});
            skArc(sketch, "E52.49.0.19", {"start": v(1190.1, -7.07) * mm, "mid": v(1190.1, -9.9) * mm, "end": v(1192.93, -9.9) * mm});
            skLineSegment(sketch, "E52.49.0.20", {"start": v(1192.93, -9.9) * mm, "end": v(1193.41, -9.41) * mm});
            skArc(sketch, "E52.49.0.21", {"start": v(1193.41, -9.41) * mm, "mid": v(1193.41, -6.59) * mm, "end": v(1190.59, -6.59) * mm});
            skCircle(sketch, "E52.49.0.22", {"center": v(1192, -16) * mm, "radius": 2 * mm});
            skCircle(sketch, "E52.49.0.23", {"center": v(1184, -16) * mm, "radius": 2 * mm});
            skLineSegment(sketch, "E52.49.0.24", {"start": v(1190.1, -7.07) * mm, "end": v(1190.59, -6.59) * mm});
            skCircle(sketch, "E52.49.0.25", {"center": v(1188, 0) * mm, "radius": 2 * mm});
            skArc(sketch, "E52.49.0.26", {"start": v(1202, -12) * mm, "mid": v(1200, -10) * mm, "end": v(1198, -12) * mm});
            skArc(sketch, "E52.49.0.27", {"start": v(1198, -16) * mm, "mid": v(1200, -18) * mm, "end": v(1202, -16) * mm});
            skLineSegment(sketch, "E52.49.0.28", {"start": v(1198, -12) * mm, "end": v(1198, -16) * mm});
            skLineSegment(sketch, "E52.49.0.29", {"start": v(1202, -16) * mm, "end": v(1202, -12) * mm});
            skLineSegment(sketch, "E52.direction1", {"start": v(8, -16) * mm, "end": v(32, -16) * mm, "construction": true});
            skSolve(sketch);
        }
        {
            var Q0;
            Q0=makeQuery(id+"F20.imprint","IMPRINT",FACE,{"disambiguationData":[TD([[makeQuery(id+"F20.imprint","IMPRINT",EDGE,{"derivedFrom":sQuery(id+"F20.wireOp",EDGE,"E52.1.0.4")}),1.0]])]});
            var Q1;
            Q1=makeQuery(id+"F20.imprint","IMPRINT",FACE,{"disambiguationData":[TD([[makeQuery(id+"F20.imprint","IMPRINT",EDGE,{"derivedFrom":sQuery(id+"F20.wireOp",EDGE,"E52.1.0.10")}),1.0]])]});
            var Q2;
            Q2=makeQuery(id+"F20.imprint","IMPRINT",FACE,{"disambiguationData":[TD([[makeQuery(id+"F20.imprint","IMPRINT",EDGE,{"derivedFrom":sQuery(id+"F20.wireOp",EDGE,"E52.1.0.25")}),1.0]])]});
            var Q3;
            Q3=makeQuery(id+"F20.imprint","IMPRINT",FACE,{"disambiguationData":[TD([[makeQuery(id+"F20.imprint","IMPRINT",EDGE,{"derivedFrom":sQuery(id+"F20.wireOp",EDGE,"E52.1.0.15")}),1.0]])]});
            var Q4;
            Q4=makeQuery(id+"F20.imprint","IMPRINT",FACE,{"disambiguationData":[TD([[makeQuery(id+"F20.imprint","IMPRINT",EDGE,{"derivedFrom":sQuery(id+"F20.wireOp",EDGE,"E52.1.0.23")}),1.0]])]});
            var Q5;
            Q5=makeQuery(id+"F20.imprint","IMPRINT",FACE,{"disambiguationData":[TD([[makeQuery(id+"F20.imprint","IMPRINT",EDGE,{"derivedFrom":sQuery(id+"F20.wireOp",EDGE,"E12")}),1.0]])]});
            var Q6;
            Q6=makeQuery(id+"F20.imprint","IMPRINT",FACE,{"disambiguationData":[TD([[makeQuery(id+"F20.imprint","IMPRINT",EDGE,{"derivedFrom":sQuery(id+"F20.wireOp",EDGE,"E3")}),1.0]])]});
            var Q7;
            Q7=makeQuery(id+"F20.imprint","IMPRINT",FACE,{"disambiguationData":[TD([[makeQuery(id+"F20.imprint","IMPRINT",EDGE,{"derivedFrom":sQuery(id+"F20.wireOp",EDGE,"E8")}),1.0]])]});
            var Q8;
            Q8=makeQuery(id+"F20.imprint","IMPRINT",FACE,{"disambiguationData":[TD([[makeQuery(id+"F20.imprint","IMPRINT",EDGE,{"derivedFrom":sQuery(id+"F20.wireOp",EDGE,"E36")}),1.0]])]});
            var Q9;
            Q9=makeQuery(id+"F20.imprint","IMPRINT",FACE,{"disambiguationData":[TD([[makeQuery(id+"F20.imprint","IMPRINT",EDGE,{"derivedFrom":sQuery(id+"F20.wireOp",EDGE,"E52.1.0.19")}),1.0]])]});
            var Q10;
            Q10=makeQuery(id+"F20.imprint","IMPRINT",FACE,{"disambiguationData":[TD([[makeQuery(id+"F20.imprint","IMPRINT",EDGE,{"derivedFrom":sQuery(id+"F20.wireOp",EDGE,"E52.1.0.6")}),1.0]])]});
            var Q11;
            Q11=makeQuery(id+"F20.imprint","IMPRINT",FACE,{"disambiguationData":[TD([[makeQuery(id+"F20.imprint","IMPRINT",EDGE,{"derivedFrom":sQuery(id+"F20.wireOp",EDGE,"E31")}),1.0]])]});
            var Q12;
            Q12=makeQuery(id+"F20.imprint","IMPRINT",FACE,{"disambiguationData":[TD([[makeQuery(id+"F20.imprint","IMPRINT",EDGE,{"derivedFrom":sQuery(id+"F20.wireOp",EDGE,"E40")}),1.0]])]});
            var Q13;
            Q13=makeQuery(id+"F20.imprint","IMPRINT",FACE,{"disambiguationData":[TD([[makeQuery(id+"F20.imprint","IMPRINT",EDGE,{"derivedFrom":sQuery(id+"F20.wireOp",EDGE,"E42")}),1.0]])]});
            var Q14;
            Q14=makeQuery(id+"F20.imprint","IMPRINT",FACE,{"disambiguationData":[TD([[makeQuery(id+"F20.imprint","IMPRINT",EDGE,{"derivedFrom":sQuery(id+"F20.wireOp",EDGE,"E32")}),1.0]])]});
            var Q15;
            Q15=makeQuery(id+"F20.imprint","IMPRINT",FACE,{"disambiguationData":[TD([[makeQuery(id+"F20.imprint","IMPRINT",EDGE,{"derivedFrom":sQuery(id+"F20.wireOp",EDGE,"E37")}),1.0]])]});
            var Q16;
            Q16=makeQuery(id+"F20.imprint","IMPRINT",FACE,{"disambiguationData":[TD([[makeQuery(id+"F20.imprint","IMPRINT",EDGE,{"derivedFrom":sQuery(id+"F20.wireOp",EDGE,"E18")}),1.0]])]});
            var Q17;
            Q17=makeQuery(id+"F20.imprint","IMPRINT",FACE,{"disambiguationData":[TD([[makeQuery(id+"F20.imprint","IMPRINT",EDGE,{"derivedFrom":sQuery(id+"F20.wireOp",EDGE,"E33")}),1.0]])]});
            var Q18;
            Q18=makeQuery(id+"F20.imprint","IMPRINT",FACE,{"disambiguationData":[TD([[makeQuery(id+"F20.imprint","IMPRINT",EDGE,{"derivedFrom":sQuery(id+"F20.wireOp",EDGE,"E20")}),1.0]])]});
            var Q19;
            Q19=makeQuery(id+"F20.imprint","IMPRINT",FACE,{"disambiguationData":[TD([[makeQuery(id+"F20.imprint","IMPRINT",EDGE,{"derivedFrom":sQuery(id+"F20.wireOp",EDGE,"E52.1.0.5")}),1.0]])]});
            var Q20;
            Q20=makeQuery(id+"F20.imprint","IMPRINT",FACE,{"disambiguationData":[TD([[makeQuery(id+"F20.imprint","IMPRINT",EDGE,{"derivedFrom":sQuery(id+"F20.wireOp",EDGE,"E52.1.0.22")}),1.0]])]});
            extrude(context, id + "F21", {"entities" : qUnion([Q0, Q1, Q2, Q3, Q4, Q5, Q6, Q7, Q8, Q9, Q10, Q11, Q12, Q13, Q14, Q15, Q16, Q17, Q18, Q19, Q20]), "operationType" : NewBodyOperationType.REMOVE, "endBound" : BoundingType.SYMMETRIC, "oppositeDirection" : true, "depth" : 50 * mm, "offsetDistance" : 25 * mm});
        }
        {
            var Q0;
            Q0=makeQuery(id+"F20.imprint","IMPRINT",FACE,{"disambiguationData":[TD([[makeQuery(id+"F20.imprint","IMPRINT",EDGE,{"derivedFrom":sQuery(id+"F20.wireOp",EDGE,"E52.1.0.0")}),1.0]])]});
            var Q1;
            Q1=makeQuery(id+"F20.imprint","IMPRINT",FACE,{"disambiguationData":[TD([[makeQuery(id+"F20.imprint","IMPRINT",EDGE,{"derivedFrom":sQuery(id+"F20.wireOp",EDGE,"E52.2.0.6")}),1.0]])]});
            var Q2;
            Q2=makeQuery(id+"F20.imprint","IMPRINT",FACE,{"disambiguationData":[TD([[makeQuery(id+"F20.imprint","IMPRINT",EDGE,{"derivedFrom":sQuery(id+"F20.wireOp",EDGE,"E52.2.0.5")}),1.0]])]});
            var Q3;
            Q3=makeQuery(id+"F20.imprint","IMPRINT",FACE,{"disambiguationData":[TD([[makeQuery(id+"F20.imprint","IMPRINT",EDGE,{"derivedFrom":sQuery(id+"F20.wireOp",EDGE,"E52.1.0.14")}),1.0]])]});
            var Q4;
            Q4=makeQuery(id+"F20.imprint","IMPRINT",FACE,{"disambiguationData":[TD([[makeQuery(id+"F20.imprint","IMPRINT",EDGE,{"derivedFrom":sQuery(id+"F20.wireOp",EDGE,"E52.1.0.26")}),1.0]])]});
            var Q5;
            Q5=makeQuery(id+"F20.imprint","IMPRINT",FACE,{"disambiguationData":[TD([[makeQuery(id+"F20.imprint","IMPRINT",EDGE,{"derivedFrom":sQuery(id+"F20.wireOp",EDGE,"E52.2.0.23")}),1.0]])]});
            var Q6;
            Q6=makeQuery(id+"F20.imprint","IMPRINT",FACE,{"disambiguationData":[TD([[makeQuery(id+"F20.imprint","IMPRINT",EDGE,{"derivedFrom":sQuery(id+"F20.wireOp",EDGE,"E52.2.0.22")}),1.0]])]});
            var Q7;
            Q7=makeQuery(id+"F20.imprint","IMPRINT",FACE,{"disambiguationData":[TD([[makeQuery(id+"F20.imprint","IMPRINT",EDGE,{"derivedFrom":sQuery(id+"F20.wireOp",EDGE,"E52.2.0.19")}),1.0]])]});
            var Q8;
            Q8=makeQuery(id+"F20.imprint","IMPRINT",FACE,{"disambiguationData":[TD([[makeQuery(id+"F20.imprint","IMPRINT",EDGE,{"derivedFrom":sQuery(id+"F20.wireOp",EDGE,"E52.2.0.15")}),1.0]])]});
            var Q9;
            Q9=makeQuery(id+"F20.imprint","IMPRINT",FACE,{"disambiguationData":[TD([[makeQuery(id+"F20.imprint","IMPRINT",EDGE,{"derivedFrom":sQuery(id+"F20.wireOp",EDGE,"E52.2.0.25")}),1.0]])]});
            var Q10;
            Q10=makeQuery(id+"F20.imprint","IMPRINT",FACE,{"disambiguationData":[TD([[makeQuery(id+"F20.imprint","IMPRINT",EDGE,{"derivedFrom":sQuery(id+"F20.wireOp",EDGE,"E52.2.0.10")}),1.0]])]});
            var Q11;
            Q11=makeQuery(id+"F20.imprint","IMPRINT",FACE,{"disambiguationData":[TD([[makeQuery(id+"F20.imprint","IMPRINT",EDGE,{"derivedFrom":sQuery(id+"F20.wireOp",EDGE,"E52.2.0.4")}),1.0]])]});
            extrude(context, id + "F22", {"entities" : qUnion([Q0, Q1, Q2, Q3, Q4, Q5, Q6, Q7, Q8, Q9, Q10, Q11]), "operationType" : NewBodyOperationType.REMOVE, "endBound" : BoundingType.SYMMETRIC, "oppositeDirection" : true, "depth" : 50 * mm, "offsetDistance" : 25 * mm});
        }
        {
            var Q0;
            Q0=makeQuery(id+"F20.imprint","IMPRINT",FACE,{"disambiguationData":[TD([[makeQuery(id+"F20.imprint","IMPRINT",EDGE,{"derivedFrom":sQuery(id+"F20.wireOp",EDGE,"E52.2.0.26")}),1.0]])]});
            var Q1;
            Q1=makeQuery(id+"F20.imprint","IMPRINT",FACE,{"disambiguationData":[TD([[makeQuery(id+"F20.imprint","IMPRINT",EDGE,{"derivedFrom":sQuery(id+"F20.wireOp",EDGE,"E52.3.0.23")}),1.0]])]});
            var Q2;
            Q2=makeQuery(id+"F20.imprint","IMPRINT",FACE,{"disambiguationData":[TD([[makeQuery(id+"F20.imprint","IMPRINT",EDGE,{"derivedFrom":sQuery(id+"F20.wireOp",EDGE,"E52.3.0.22")}),1.0]])]});
            var Q3;
            Q3=makeQuery(id+"F20.imprint","IMPRINT",FACE,{"disambiguationData":[TD([[makeQuery(id+"F20.imprint","IMPRINT",EDGE,{"derivedFrom":sQuery(id+"F20.wireOp",EDGE,"E52.3.0.19")}),1.0]])]});
            var Q4;
            Q4=makeQuery(id+"F20.imprint","IMPRINT",FACE,{"disambiguationData":[TD([[makeQuery(id+"F20.imprint","IMPRINT",EDGE,{"derivedFrom":sQuery(id+"F20.wireOp",EDGE,"E52.3.0.15")}),1.0]])]});
            var Q5;
            Q5=makeQuery(id+"F20.imprint","IMPRINT",FACE,{"disambiguationData":[TD([[makeQuery(id+"F20.imprint","IMPRINT",EDGE,{"derivedFrom":sQuery(id+"F20.wireOp",EDGE,"E52.2.0.14")}),1.0]])]});
            var Q6;
            Q6=makeQuery(id+"F20.imprint","IMPRINT",FACE,{"disambiguationData":[TD([[makeQuery(id+"F20.imprint","IMPRINT",EDGE,{"derivedFrom":sQuery(id+"F20.wireOp",EDGE,"E52.3.0.25")}),1.0]])]});
            var Q7;
            Q7=makeQuery(id+"F20.imprint","IMPRINT",FACE,{"disambiguationData":[TD([[makeQuery(id+"F20.imprint","IMPRINT",EDGE,{"derivedFrom":sQuery(id+"F20.wireOp",EDGE,"E52.2.0.0")}),1.0]])]});
            var Q8;
            Q8=makeQuery(id+"F20.imprint","IMPRINT",FACE,{"disambiguationData":[TD([[makeQuery(id+"F20.imprint","IMPRINT",EDGE,{"derivedFrom":sQuery(id+"F20.wireOp",EDGE,"E52.3.0.6")}),1.0]])]});
            var Q9;
            Q9=makeQuery(id+"F20.imprint","IMPRINT",FACE,{"disambiguationData":[TD([[makeQuery(id+"F20.imprint","IMPRINT",EDGE,{"derivedFrom":sQuery(id+"F20.wireOp",EDGE,"E52.3.0.5")}),1.0]])]});
            var Q10;
            Q10=makeQuery(id+"F20.imprint","IMPRINT",FACE,{"disambiguationData":[TD([[makeQuery(id+"F20.imprint","IMPRINT",EDGE,{"derivedFrom":sQuery(id+"F20.wireOp",EDGE,"E52.3.0.10")}),1.0]])]});
            var Q11;
            Q11=makeQuery(id+"F20.imprint","IMPRINT",FACE,{"disambiguationData":[TD([[makeQuery(id+"F20.imprint","IMPRINT",EDGE,{"derivedFrom":sQuery(id+"F20.wireOp",EDGE,"E52.3.0.4")}),1.0]])]});
            extrude(context, id + "F23", {"entities" : qUnion([Q0, Q1, Q2, Q3, Q4, Q5, Q6, Q7, Q8, Q9, Q10, Q11]), "operationType" : NewBodyOperationType.REMOVE, "endBound" : BoundingType.SYMMETRIC, "oppositeDirection" : true, "depth" : 50 * mm, "offsetDistance" : 25 * mm});
        }
        {
            var Q0;
            Q0=makeQuery(id+"F20.imprint","IMPRINT",FACE,{"disambiguationData":[TD([[makeQuery(id+"F20.imprint","IMPRINT",EDGE,{"derivedFrom":sQuery(id+"F20.wireOp",EDGE,"E52.3.0.26")}),1.0]])]});
            var Q1;
            Q1=makeQuery(id+"F20.imprint","IMPRINT",FACE,{"disambiguationData":[TD([[makeQuery(id+"F20.imprint","IMPRINT",EDGE,{"derivedFrom":sQuery(id+"F20.wireOp",EDGE,"E52.4.0.23")}),1.0]])]});
            var Q2;
            Q2=makeQuery(id+"F20.imprint","IMPRINT",FACE,{"disambiguationData":[TD([[makeQuery(id+"F20.imprint","IMPRINT",EDGE,{"derivedFrom":sQuery(id+"F20.wireOp",EDGE,"E52.4.0.22")}),1.0]])]});
            var Q3;
            Q3=makeQuery(id+"F20.imprint","IMPRINT",FACE,{"disambiguationData":[TD([[makeQuery(id+"F20.imprint","IMPRINT",EDGE,{"derivedFrom":sQuery(id+"F20.wireOp",EDGE,"E52.4.0.19")}),1.0]])]});
            var Q4;
            Q4=makeQuery(id+"F20.imprint","IMPRINT",FACE,{"disambiguationData":[TD([[makeQuery(id+"F20.imprint","IMPRINT",EDGE,{"derivedFrom":sQuery(id+"F20.wireOp",EDGE,"E52.4.0.15")}),1.0]])]});
            var Q5;
            Q5=makeQuery(id+"F20.imprint","IMPRINT",FACE,{"disambiguationData":[TD([[makeQuery(id+"F20.imprint","IMPRINT",EDGE,{"derivedFrom":sQuery(id+"F20.wireOp",EDGE,"E52.3.0.14")}),1.0]])]});
            var Q6;
            Q6=makeQuery(id+"F20.imprint","IMPRINT",FACE,{"disambiguationData":[TD([[makeQuery(id+"F20.imprint","IMPRINT",EDGE,{"derivedFrom":sQuery(id+"F20.wireOp",EDGE,"E52.3.0.0")}),1.0]])]});
            var Q7;
            Q7=makeQuery(id+"F20.imprint","IMPRINT",FACE,{"disambiguationData":[TD([[makeQuery(id+"F20.imprint","IMPRINT",EDGE,{"derivedFrom":sQuery(id+"F20.wireOp",EDGE,"E52.4.0.5")}),1.0]])]});
            var Q8;
            Q8=makeQuery(id+"F20.imprint","IMPRINT",FACE,{"disambiguationData":[TD([[makeQuery(id+"F20.imprint","IMPRINT",EDGE,{"derivedFrom":sQuery(id+"F20.wireOp",EDGE,"E52.4.0.6")}),1.0]])]});
            var Q9;
            Q9=makeQuery(id+"F20.imprint","IMPRINT",FACE,{"disambiguationData":[TD([[makeQuery(id+"F20.imprint","IMPRINT",EDGE,{"derivedFrom":sQuery(id+"F20.wireOp",EDGE,"E52.4.0.10")}),1.0]])]});
            var Q10;
            Q10=makeQuery(id+"F20.imprint","IMPRINT",FACE,{"disambiguationData":[TD([[makeQuery(id+"F20.imprint","IMPRINT",EDGE,{"derivedFrom":sQuery(id+"F20.wireOp",EDGE,"E52.4.0.4")}),1.0]])]});
            var Q11;
            Q11=makeQuery(id+"F20.imprint","IMPRINT",FACE,{"disambiguationData":[TD([[makeQuery(id+"F20.imprint","IMPRINT",EDGE,{"derivedFrom":sQuery(id+"F20.wireOp",EDGE,"E52.4.0.25")}),1.0]])]});
            extrude(context, id + "F24", {"entities" : qUnion([Q0, Q1, Q2, Q3, Q4, Q5, Q6, Q7, Q8, Q9, Q10, Q11]), "operationType" : NewBodyOperationType.REMOVE, "endBound" : BoundingType.SYMMETRIC, "oppositeDirection" : true, "depth" : 50 * mm, "offsetDistance" : 25 * mm});
        }
        {
            var Q0;
            Q0=makeQuery(id+"F20.imprint","IMPRINT",FACE,{"disambiguationData":[TD([[makeQuery(id+"F20.imprint","IMPRINT",EDGE,{"derivedFrom":sQuery(id+"F20.wireOp",EDGE,"E52.4.0.26")}),1.0]])]});
            var Q1;
            Q1=makeQuery(id+"F20.imprint","IMPRINT",FACE,{"disambiguationData":[TD([[makeQuery(id+"F20.imprint","IMPRINT",EDGE,{"derivedFrom":sQuery(id+"F20.wireOp",EDGE,"E52.5.0.23")}),1.0]])]});
            var Q2;
            Q2=makeQuery(id+"F20.imprint","IMPRINT",FACE,{"disambiguationData":[TD([[makeQuery(id+"F20.imprint","IMPRINT",EDGE,{"derivedFrom":sQuery(id+"F20.wireOp",EDGE,"E52.5.0.22")}),1.0]])]});
            var Q3;
            Q3=makeQuery(id+"F20.imprint","IMPRINT",FACE,{"disambiguationData":[TD([[makeQuery(id+"F20.imprint","IMPRINT",EDGE,{"derivedFrom":sQuery(id+"F20.wireOp",EDGE,"E52.5.0.19")}),1.0]])]});
            var Q4;
            Q4=makeQuery(id+"F20.imprint","IMPRINT",FACE,{"disambiguationData":[TD([[makeQuery(id+"F20.imprint","IMPRINT",EDGE,{"derivedFrom":sQuery(id+"F20.wireOp",EDGE,"E52.5.0.15")}),1.0]])]});
            var Q5;
            Q5=makeQuery(id+"F20.imprint","IMPRINT",FACE,{"disambiguationData":[TD([[makeQuery(id+"F20.imprint","IMPRINT",EDGE,{"derivedFrom":sQuery(id+"F20.wireOp",EDGE,"E52.4.0.14")}),1.0]])]});
            var Q6;
            Q6=makeQuery(id+"F20.imprint","IMPRINT",FACE,{"disambiguationData":[TD([[makeQuery(id+"F20.imprint","IMPRINT",EDGE,{"derivedFrom":sQuery(id+"F20.wireOp",EDGE,"E52.5.0.25")}),1.0]])]});
            var Q7;
            Q7=makeQuery(id+"F20.imprint","IMPRINT",FACE,{"disambiguationData":[TD([[makeQuery(id+"F20.imprint","IMPRINT",EDGE,{"derivedFrom":sQuery(id+"F20.wireOp",EDGE,"E52.5.0.6")}),1.0]])]});
            var Q8;
            Q8=makeQuery(id+"F20.imprint","IMPRINT",FACE,{"disambiguationData":[TD([[makeQuery(id+"F20.imprint","IMPRINT",EDGE,{"derivedFrom":sQuery(id+"F20.wireOp",EDGE,"E52.4.0.0")}),1.0]])]});
            var Q9;
            Q9=makeQuery(id+"F20.imprint","IMPRINT",FACE,{"disambiguationData":[TD([[makeQuery(id+"F20.imprint","IMPRINT",EDGE,{"derivedFrom":sQuery(id+"F20.wireOp",EDGE,"E52.5.0.5")}),1.0]])]});
            var Q10;
            Q10=makeQuery(id+"F20.imprint","IMPRINT",FACE,{"disambiguationData":[TD([[makeQuery(id+"F20.imprint","IMPRINT",EDGE,{"derivedFrom":sQuery(id+"F20.wireOp",EDGE,"E52.5.0.4")}),1.0]])]});
            var Q11;
            Q11=makeQuery(id+"F20.imprint","IMPRINT",FACE,{"disambiguationData":[TD([[makeQuery(id+"F20.imprint","IMPRINT",EDGE,{"derivedFrom":sQuery(id+"F20.wireOp",EDGE,"E52.5.0.10")}),1.0]])]});
            extrude(context, id + "F25", {"entities" : qUnion([Q0, Q1, Q2, Q3, Q4, Q5, Q6, Q7, Q8, Q9, Q10, Q11]), "operationType" : NewBodyOperationType.REMOVE, "endBound" : BoundingType.SYMMETRIC, "oppositeDirection" : true, "depth" : 50 * mm, "offsetDistance" : 25 * mm});
        }
        {
            var Q0;
            Q0=makeQuery(id+"F20.imprint","IMPRINT",FACE,{"disambiguationData":[TD([[makeQuery(id+"F20.imprint","IMPRINT",EDGE,{"derivedFrom":sQuery(id+"F20.wireOp",EDGE,"E52.7.0.22")}),1.0]])]});
            var Q1;
            Q1=makeQuery(id+"F20.imprint","IMPRINT",FACE,{"disambiguationData":[TD([[makeQuery(id+"F20.imprint","IMPRINT",EDGE,{"derivedFrom":sQuery(id+"F20.wireOp",EDGE,"E52.7.0.23")}),1.0]])]});
            var Q2;
            Q2=makeQuery(id+"F20.imprint","IMPRINT",FACE,{"disambiguationData":[TD([[makeQuery(id+"F20.imprint","IMPRINT",EDGE,{"derivedFrom":sQuery(id+"F20.wireOp",EDGE,"E52.6.0.26")}),1.0]])]});
            var Q3;
            Q3=makeQuery(id+"F20.imprint","IMPRINT",FACE,{"disambiguationData":[TD([[makeQuery(id+"F20.imprint","IMPRINT",EDGE,{"derivedFrom":sQuery(id+"F20.wireOp",EDGE,"E52.6.0.22")}),1.0]])]});
            var Q4;
            Q4=makeQuery(id+"F20.imprint","IMPRINT",FACE,{"disambiguationData":[TD([[makeQuery(id+"F20.imprint","IMPRINT",EDGE,{"derivedFrom":sQuery(id+"F20.wireOp",EDGE,"E52.6.0.23")}),1.0]])]});
            var Q5;
            Q5=makeQuery(id+"F20.imprint","IMPRINT",FACE,{"disambiguationData":[TD([[makeQuery(id+"F20.imprint","IMPRINT",EDGE,{"derivedFrom":sQuery(id+"F20.wireOp",EDGE,"E52.5.0.26")}),1.0]])]});
            var Q6;
            Q6=makeQuery(id+"F20.imprint","IMPRINT",FACE,{"disambiguationData":[TD([[makeQuery(id+"F20.imprint","IMPRINT",EDGE,{"derivedFrom":sQuery(id+"F20.wireOp",EDGE,"E52.6.0.15")}),1.0]])]});
            var Q7;
            Q7=makeQuery(id+"F20.imprint","IMPRINT",FACE,{"disambiguationData":[TD([[makeQuery(id+"F20.imprint","IMPRINT",EDGE,{"derivedFrom":sQuery(id+"F20.wireOp",EDGE,"E52.6.0.19")}),1.0]])]});
            var Q8;
            Q8=makeQuery(id+"F20.imprint","IMPRINT",FACE,{"disambiguationData":[TD([[makeQuery(id+"F20.imprint","IMPRINT",EDGE,{"derivedFrom":sQuery(id+"F20.wireOp",EDGE,"E52.7.0.15")}),1.0]])]});
            var Q9;
            Q9=makeQuery(id+"F20.imprint","IMPRINT",FACE,{"disambiguationData":[TD([[makeQuery(id+"F20.imprint","IMPRINT",EDGE,{"derivedFrom":sQuery(id+"F20.wireOp",EDGE,"E52.7.0.19")}),1.0]])]});
            var Q10;
            Q10=makeQuery(id+"F20.imprint","IMPRINT",FACE,{"disambiguationData":[TD([[makeQuery(id+"F20.imprint","IMPRINT",EDGE,{"derivedFrom":sQuery(id+"F20.wireOp",EDGE,"E52.7.0.25")}),1.0]])]});
            var Q11;
            Q11=makeQuery(id+"F20.imprint","IMPRINT",FACE,{"disambiguationData":[TD([[makeQuery(id+"F20.imprint","IMPRINT",EDGE,{"derivedFrom":sQuery(id+"F20.wireOp",EDGE,"E52.6.0.14")}),1.0]])]});
            var Q12;
            Q12=makeQuery(id+"F20.imprint","IMPRINT",FACE,{"disambiguationData":[TD([[makeQuery(id+"F20.imprint","IMPRINT",EDGE,{"derivedFrom":sQuery(id+"F20.wireOp",EDGE,"E52.6.0.25")}),1.0]])]});
            var Q13;
            Q13=makeQuery(id+"F20.imprint","IMPRINT",FACE,{"disambiguationData":[TD([[makeQuery(id+"F20.imprint","IMPRINT",EDGE,{"derivedFrom":sQuery(id+"F20.wireOp",EDGE,"E52.5.0.14")}),1.0]])]});
            var Q14;
            Q14=makeQuery(id+"F20.imprint","IMPRINT",FACE,{"disambiguationData":[TD([[makeQuery(id+"F20.imprint","IMPRINT",EDGE,{"derivedFrom":sQuery(id+"F20.wireOp",EDGE,"E52.5.0.0")}),1.0]])]});
            var Q15;
            Q15=makeQuery(id+"F20.imprint","IMPRINT",FACE,{"disambiguationData":[TD([[makeQuery(id+"F20.imprint","IMPRINT",EDGE,{"derivedFrom":sQuery(id+"F20.wireOp",EDGE,"E52.6.0.6")}),1.0]])]});
            var Q16;
            Q16=makeQuery(id+"F20.imprint","IMPRINT",FACE,{"disambiguationData":[TD([[makeQuery(id+"F20.imprint","IMPRINT",EDGE,{"derivedFrom":sQuery(id+"F20.wireOp",EDGE,"E52.6.0.5")}),1.0]])]});
            var Q17;
            Q17=makeQuery(id+"F20.imprint","IMPRINT",FACE,{"disambiguationData":[TD([[makeQuery(id+"F20.imprint","IMPRINT",EDGE,{"derivedFrom":sQuery(id+"F20.wireOp",EDGE,"E52.6.0.10")}),1.0]])]});
            var Q18;
            Q18=makeQuery(id+"F20.imprint","IMPRINT",FACE,{"disambiguationData":[TD([[makeQuery(id+"F20.imprint","IMPRINT",EDGE,{"derivedFrom":sQuery(id+"F20.wireOp",EDGE,"E52.6.0.4")}),1.0]])]});
            var Q19;
            Q19=makeQuery(id+"F20.imprint","IMPRINT",FACE,{"disambiguationData":[TD([[makeQuery(id+"F20.imprint","IMPRINT",EDGE,{"derivedFrom":sQuery(id+"F20.wireOp",EDGE,"E52.6.0.0")}),1.0]])]});
            var Q20;
            Q20=makeQuery(id+"F20.imprint","IMPRINT",FACE,{"disambiguationData":[TD([[makeQuery(id+"F20.imprint","IMPRINT",EDGE,{"derivedFrom":sQuery(id+"F20.wireOp",EDGE,"E52.7.0.5")}),1.0]])]});
            var Q21;
            Q21=makeQuery(id+"F20.imprint","IMPRINT",FACE,{"disambiguationData":[TD([[makeQuery(id+"F20.imprint","IMPRINT",EDGE,{"derivedFrom":sQuery(id+"F20.wireOp",EDGE,"E52.7.0.6")}),1.0]])]});
            var Q22;
            Q22=makeQuery(id+"F20.imprint","IMPRINT",FACE,{"disambiguationData":[TD([[makeQuery(id+"F20.imprint","IMPRINT",EDGE,{"derivedFrom":sQuery(id+"F20.wireOp",EDGE,"E52.7.0.10")}),1.0]])]});
            var Q23;
            Q23=makeQuery(id+"F20.imprint","IMPRINT",FACE,{"disambiguationData":[TD([[makeQuery(id+"F20.imprint","IMPRINT",EDGE,{"derivedFrom":sQuery(id+"F20.wireOp",EDGE,"E52.7.0.4")}),1.0]])]});
            extrude(context, id + "F26", {"entities" : qUnion([Q0, Q1, Q2, Q3, Q4, Q5, Q6, Q7, Q8, Q9, Q10, Q11, Q12, Q13, Q14, Q15, Q16, Q17, Q18, Q19, Q20, Q21, Q22, Q23]), "operationType" : NewBodyOperationType.REMOVE, "endBound" : BoundingType.SYMMETRIC, "depth" : 50 * mm, "offsetDistance" : 25 * mm});
        }
        {
            var Q0;
            Q0=makeQuery(id+"F20.imprint","IMPRINT",FACE,{"disambiguationData":[TD([[makeQuery(id+"F20.imprint","IMPRINT",EDGE,{"derivedFrom":sQuery(id+"F20.wireOp",EDGE,"E52.7.0.26")}),1.0]])]});
            var Q1;
            Q1=makeQuery(id+"F20.imprint","IMPRINT",FACE,{"disambiguationData":[TD([[makeQuery(id+"F20.imprint","IMPRINT",EDGE,{"derivedFrom":sQuery(id+"F20.wireOp",EDGE,"E52.8.0.23")}),1.0]])]});
            var Q2;
            Q2=makeQuery(id+"F20.imprint","IMPRINT",FACE,{"disambiguationData":[TD([[makeQuery(id+"F20.imprint","IMPRINT",EDGE,{"derivedFrom":sQuery(id+"F20.wireOp",EDGE,"E52.8.0.22")}),1.0]])]});
            var Q3;
            Q3=makeQuery(id+"F20.imprint","IMPRINT",FACE,{"disambiguationData":[TD([[makeQuery(id+"F20.imprint","IMPRINT",EDGE,{"derivedFrom":sQuery(id+"F20.wireOp",EDGE,"E52.8.0.26")}),1.0]])]});
            var Q4;
            Q4=makeQuery(id+"F20.imprint","IMPRINT",FACE,{"disambiguationData":[TD([[makeQuery(id+"F20.imprint","IMPRINT",EDGE,{"derivedFrom":sQuery(id+"F20.wireOp",EDGE,"E52.9.0.23")}),1.0]])]});
            var Q5;
            Q5=makeQuery(id+"F20.imprint","IMPRINT",FACE,{"disambiguationData":[TD([[makeQuery(id+"F20.imprint","IMPRINT",EDGE,{"derivedFrom":sQuery(id+"F20.wireOp",EDGE,"E52.9.0.22")}),1.0]])]});
            var Q6;
            Q6=makeQuery(id+"F20.imprint","IMPRINT",FACE,{"disambiguationData":[TD([[makeQuery(id+"F20.imprint","IMPRINT",EDGE,{"derivedFrom":sQuery(id+"F20.wireOp",EDGE,"E52.9.0.19")}),1.0]])]});
            var Q7;
            Q7=makeQuery(id+"F20.imprint","IMPRINT",FACE,{"disambiguationData":[TD([[makeQuery(id+"F20.imprint","IMPRINT",EDGE,{"derivedFrom":sQuery(id+"F20.wireOp",EDGE,"E52.9.0.15")}),1.0]])]});
            var Q8;
            Q8=makeQuery(id+"F20.imprint","IMPRINT",FACE,{"disambiguationData":[TD([[makeQuery(id+"F20.imprint","IMPRINT",EDGE,{"derivedFrom":sQuery(id+"F20.wireOp",EDGE,"E52.8.0.19")}),1.0]])]});
            var Q9;
            Q9=makeQuery(id+"F20.imprint","IMPRINT",FACE,{"disambiguationData":[TD([[makeQuery(id+"F20.imprint","IMPRINT",EDGE,{"derivedFrom":sQuery(id+"F20.wireOp",EDGE,"E52.8.0.15")}),1.0]])]});
            var Q10;
            Q10=makeQuery(id+"F20.imprint","IMPRINT",FACE,{"disambiguationData":[TD([[makeQuery(id+"F20.imprint","IMPRINT",EDGE,{"derivedFrom":sQuery(id+"F20.wireOp",EDGE,"E52.7.0.14")}),1.0]])]});
            var Q11;
            Q11=makeQuery(id+"F20.imprint","IMPRINT",FACE,{"disambiguationData":[TD([[makeQuery(id+"F20.imprint","IMPRINT",EDGE,{"derivedFrom":sQuery(id+"F20.wireOp",EDGE,"E52.8.0.25")}),1.0]])]});
            var Q12;
            Q12=makeQuery(id+"F20.imprint","IMPRINT",FACE,{"disambiguationData":[TD([[makeQuery(id+"F20.imprint","IMPRINT",EDGE,{"derivedFrom":sQuery(id+"F20.wireOp",EDGE,"E52.8.0.14")}),1.0]])]});
            var Q13;
            Q13=makeQuery(id+"F20.imprint","IMPRINT",FACE,{"disambiguationData":[TD([[makeQuery(id+"F20.imprint","IMPRINT",EDGE,{"derivedFrom":sQuery(id+"F20.wireOp",EDGE,"E52.9.0.25")}),1.0]])]});
            var Q14;
            Q14=makeQuery(id+"F20.imprint","IMPRINT",FACE,{"disambiguationData":[TD([[makeQuery(id+"F20.imprint","IMPRINT",EDGE,{"derivedFrom":sQuery(id+"F20.wireOp",EDGE,"E52.9.0.10")}),1.0]])]});
            var Q15;
            Q15=makeQuery(id+"F20.imprint","IMPRINT",FACE,{"disambiguationData":[TD([[makeQuery(id+"F20.imprint","IMPRINT",EDGE,{"derivedFrom":sQuery(id+"F20.wireOp",EDGE,"E52.9.0.4")}),1.0]])]});
            var Q16;
            Q16=makeQuery(id+"F20.imprint","IMPRINT",FACE,{"disambiguationData":[TD([[makeQuery(id+"F20.imprint","IMPRINT",EDGE,{"derivedFrom":sQuery(id+"F20.wireOp",EDGE,"E52.9.0.6")}),1.0]])]});
            var Q17;
            Q17=makeQuery(id+"F20.imprint","IMPRINT",FACE,{"disambiguationData":[TD([[makeQuery(id+"F20.imprint","IMPRINT",EDGE,{"derivedFrom":sQuery(id+"F20.wireOp",EDGE,"E52.9.0.5")}),1.0]])]});
            var Q18;
            Q18=makeQuery(id+"F20.imprint","IMPRINT",FACE,{"disambiguationData":[TD([[makeQuery(id+"F20.imprint","IMPRINT",EDGE,{"derivedFrom":sQuery(id+"F20.wireOp",EDGE,"E52.8.0.0")}),1.0]])]});
            var Q19;
            Q19=makeQuery(id+"F20.imprint","IMPRINT",FACE,{"disambiguationData":[TD([[makeQuery(id+"F20.imprint","IMPRINT",EDGE,{"derivedFrom":sQuery(id+"F20.wireOp",EDGE,"E52.8.0.10")}),1.0]])]});
            var Q20;
            Q20=makeQuery(id+"F20.imprint","IMPRINT",FACE,{"disambiguationData":[TD([[makeQuery(id+"F20.imprint","IMPRINT",EDGE,{"derivedFrom":sQuery(id+"F20.wireOp",EDGE,"E52.8.0.4")}),1.0]])]});
            var Q21;
            Q21=makeQuery(id+"F20.imprint","IMPRINT",FACE,{"disambiguationData":[TD([[makeQuery(id+"F20.imprint","IMPRINT",EDGE,{"derivedFrom":sQuery(id+"F20.wireOp",EDGE,"E52.8.0.6")}),1.0]])]});
            var Q22;
            Q22=makeQuery(id+"F20.imprint","IMPRINT",FACE,{"disambiguationData":[TD([[makeQuery(id+"F20.imprint","IMPRINT",EDGE,{"derivedFrom":sQuery(id+"F20.wireOp",EDGE,"E52.8.0.5")}),1.0]])]});
            var Q23;
            Q23=makeQuery(id+"F20.imprint","IMPRINT",FACE,{"disambiguationData":[TD([[makeQuery(id+"F20.imprint","IMPRINT",EDGE,{"derivedFrom":sQuery(id+"F20.wireOp",EDGE,"E52.7.0.0")}),1.0]])]});
            extrude(context, id + "F27", {"entities" : qUnion([Q0, Q1, Q2, Q3, Q4, Q5, Q6, Q7, Q8, Q9, Q10, Q11, Q12, Q13, Q14, Q15, Q16, Q17, Q18, Q19, Q20, Q21, Q22, Q23]), "operationType" : NewBodyOperationType.REMOVE, "endBound" : BoundingType.SYMMETRIC, "oppositeDirection" : true, "depth" : 56 * mm, "offsetDistance" : 25 * mm});
        }
        {
            var Q0;
            Q0=makeQuery(id+"F20.imprint","IMPRINT",FACE,{"disambiguationData":[TD([[makeQuery(id+"F20.imprint","IMPRINT",EDGE,{"derivedFrom":sQuery(id+"F20.wireOp",EDGE,"E52.9.0.26")}),1.0]])]});
            var Q1;
            Q1=makeQuery(id+"F20.imprint","IMPRINT",FACE,{"disambiguationData":[TD([[makeQuery(id+"F20.imprint","IMPRINT",EDGE,{"derivedFrom":sQuery(id+"F20.wireOp",EDGE,"E52.10.0.23")}),1.0]])]});
            var Q2;
            Q2=makeQuery(id+"F20.imprint","IMPRINT",FACE,{"disambiguationData":[TD([[makeQuery(id+"F20.imprint","IMPRINT",EDGE,{"derivedFrom":sQuery(id+"F20.wireOp",EDGE,"E52.10.0.22")}),1.0]])]});
            var Q3;
            Q3=makeQuery(id+"F20.imprint","IMPRINT",FACE,{"disambiguationData":[TD([[makeQuery(id+"F20.imprint","IMPRINT",EDGE,{"derivedFrom":sQuery(id+"F20.wireOp",EDGE,"E52.10.0.26")}),1.0]])]});
            var Q4;
            Q4=makeQuery(id+"F20.imprint","IMPRINT",FACE,{"disambiguationData":[TD([[makeQuery(id+"F20.imprint","IMPRINT",EDGE,{"derivedFrom":sQuery(id+"F20.wireOp",EDGE,"E52.11.0.23")}),1.0]])]});
            var Q5;
            Q5=makeQuery(id+"F20.imprint","IMPRINT",FACE,{"disambiguationData":[TD([[makeQuery(id+"F20.imprint","IMPRINT",EDGE,{"derivedFrom":sQuery(id+"F20.wireOp",EDGE,"E52.11.0.22")}),1.0]])]});
            var Q6;
            Q6=makeQuery(id+"F20.imprint","IMPRINT",FACE,{"disambiguationData":[TD([[makeQuery(id+"F20.imprint","IMPRINT",EDGE,{"derivedFrom":sQuery(id+"F20.wireOp",EDGE,"E52.11.0.19")}),1.0]])]});
            var Q7;
            Q7=makeQuery(id+"F20.imprint","IMPRINT",FACE,{"disambiguationData":[TD([[makeQuery(id+"F20.imprint","IMPRINT",EDGE,{"derivedFrom":sQuery(id+"F20.wireOp",EDGE,"E52.11.0.15")}),1.0]])]});
            var Q8;
            Q8=makeQuery(id+"F20.imprint","IMPRINT",FACE,{"disambiguationData":[TD([[makeQuery(id+"F20.imprint","IMPRINT",EDGE,{"derivedFrom":sQuery(id+"F20.wireOp",EDGE,"E52.11.0.25")}),1.0]])]});
            var Q9;
            Q9=makeQuery(id+"F20.imprint","IMPRINT",FACE,{"disambiguationData":[TD([[makeQuery(id+"F20.imprint","IMPRINT",EDGE,{"derivedFrom":sQuery(id+"F20.wireOp",EDGE,"E52.11.0.10")}),1.0]])]});
            var Q10;
            Q10=makeQuery(id+"F20.imprint","IMPRINT",FACE,{"disambiguationData":[TD([[makeQuery(id+"F20.imprint","IMPRINT",EDGE,{"derivedFrom":sQuery(id+"F20.wireOp",EDGE,"E52.11.0.4")}),1.0]])]});
            var Q11;
            Q11=makeQuery(id+"F20.imprint","IMPRINT",FACE,{"disambiguationData":[TD([[makeQuery(id+"F20.imprint","IMPRINT",EDGE,{"derivedFrom":sQuery(id+"F20.wireOp",EDGE,"E52.11.0.6")}),1.0]])]});
            var Q12;
            Q12=makeQuery(id+"F20.imprint","IMPRINT",FACE,{"disambiguationData":[TD([[makeQuery(id+"F20.imprint","IMPRINT",EDGE,{"derivedFrom":sQuery(id+"F20.wireOp",EDGE,"E52.11.0.5")}),1.0]])]});
            var Q13;
            Q13=makeQuery(id+"F20.imprint","IMPRINT",FACE,{"disambiguationData":[TD([[makeQuery(id+"F20.imprint","IMPRINT",EDGE,{"derivedFrom":sQuery(id+"F20.wireOp",EDGE,"E52.10.0.14")}),1.0]])]});
            var Q14;
            Q14=makeQuery(id+"F20.imprint","IMPRINT",FACE,{"disambiguationData":[TD([[makeQuery(id+"F20.imprint","IMPRINT",EDGE,{"derivedFrom":sQuery(id+"F20.wireOp",EDGE,"E52.10.0.0")}),1.0]])]});
            var Q15;
            Q15=makeQuery(id+"F20.imprint","IMPRINT",FACE,{"disambiguationData":[TD([[makeQuery(id+"F20.imprint","IMPRINT",EDGE,{"derivedFrom":sQuery(id+"F20.wireOp",EDGE,"E52.10.0.10")}),1.0]])]});
            var Q16;
            Q16=makeQuery(id+"F20.imprint","IMPRINT",FACE,{"disambiguationData":[TD([[makeQuery(id+"F20.imprint","IMPRINT",EDGE,{"derivedFrom":sQuery(id+"F20.wireOp",EDGE,"E52.10.0.4")}),1.0]])]});
            var Q17;
            Q17=makeQuery(id+"F20.imprint","IMPRINT",FACE,{"disambiguationData":[TD([[makeQuery(id+"F20.imprint","IMPRINT",EDGE,{"derivedFrom":sQuery(id+"F20.wireOp",EDGE,"E52.10.0.25")}),1.0]])]});
            var Q18;
            Q18=makeQuery(id+"F20.imprint","IMPRINT",FACE,{"disambiguationData":[TD([[makeQuery(id+"F20.imprint","IMPRINT",EDGE,{"derivedFrom":sQuery(id+"F20.wireOp",EDGE,"E52.10.0.19")}),1.0]])]});
            var Q19;
            Q19=makeQuery(id+"F20.imprint","IMPRINT",FACE,{"disambiguationData":[TD([[makeQuery(id+"F20.imprint","IMPRINT",EDGE,{"derivedFrom":sQuery(id+"F20.wireOp",EDGE,"E52.10.0.15")}),1.0]])]});
            var Q20;
            Q20=makeQuery(id+"F20.imprint","IMPRINT",FACE,{"disambiguationData":[TD([[makeQuery(id+"F20.imprint","IMPRINT",EDGE,{"derivedFrom":sQuery(id+"F20.wireOp",EDGE,"E52.10.0.6")}),1.0]])]});
            var Q21;
            Q21=makeQuery(id+"F20.imprint","IMPRINT",FACE,{"disambiguationData":[TD([[makeQuery(id+"F20.imprint","IMPRINT",EDGE,{"derivedFrom":sQuery(id+"F20.wireOp",EDGE,"E52.10.0.5")}),1.0]])]});
            var Q22;
            Q22=makeQuery(id+"F20.imprint","IMPRINT",FACE,{"disambiguationData":[TD([[makeQuery(id+"F20.imprint","IMPRINT",EDGE,{"derivedFrom":sQuery(id+"F20.wireOp",EDGE,"E52.9.0.14")}),1.0]])]});
            var Q23;
            Q23=makeQuery(id+"F20.imprint","IMPRINT",FACE,{"disambiguationData":[TD([[makeQuery(id+"F20.imprint","IMPRINT",EDGE,{"derivedFrom":sQuery(id+"F20.wireOp",EDGE,"E52.9.0.0")}),1.0]])]});
            extrude(context, id + "F28", {"entities" : qUnion([Q0, Q1, Q2, Q3, Q4, Q5, Q6, Q7, Q8, Q9, Q10, Q11, Q12, Q13, Q14, Q15, Q16, Q17, Q18, Q19, Q20, Q21, Q22, Q23]), "operationType" : NewBodyOperationType.REMOVE, "endBound" : BoundingType.SYMMETRIC, "oppositeDirection" : true, "depth" : 50 * mm, "offsetDistance" : 25 * mm});
        }
        {
            var Q0;
            Q0=makeQuery(id+"F20.imprint","IMPRINT",FACE,{"disambiguationData":[TD([[makeQuery(id+"F20.imprint","IMPRINT",EDGE,{"derivedFrom":sQuery(id+"F20.wireOp",EDGE,"E52.13.0.22")}),1.0]])]});
            var Q1;
            Q1=makeQuery(id+"F20.imprint","IMPRINT",FACE,{"disambiguationData":[TD([[makeQuery(id+"F20.imprint","IMPRINT",EDGE,{"derivedFrom":sQuery(id+"F20.wireOp",EDGE,"E52.13.0.23")}),1.0]])]});
            var Q2;
            Q2=makeQuery(id+"F20.imprint","IMPRINT",FACE,{"disambiguationData":[TD([[makeQuery(id+"F20.imprint","IMPRINT",EDGE,{"derivedFrom":sQuery(id+"F20.wireOp",EDGE,"E52.12.0.26")}),1.0]])]});
            var Q3;
            Q3=makeQuery(id+"F20.imprint","IMPRINT",FACE,{"disambiguationData":[TD([[makeQuery(id+"F20.imprint","IMPRINT",EDGE,{"derivedFrom":sQuery(id+"F20.wireOp",EDGE,"E52.12.0.22")}),1.0]])]});
            var Q4;
            Q4=makeQuery(id+"F20.imprint","IMPRINT",FACE,{"disambiguationData":[TD([[makeQuery(id+"F20.imprint","IMPRINT",EDGE,{"derivedFrom":sQuery(id+"F20.wireOp",EDGE,"E52.12.0.23")}),1.0]])]});
            var Q5;
            Q5=makeQuery(id+"F20.imprint","IMPRINT",FACE,{"disambiguationData":[TD([[makeQuery(id+"F20.imprint","IMPRINT",EDGE,{"derivedFrom":sQuery(id+"F20.wireOp",EDGE,"E52.11.0.26")}),1.0]])]});
            var Q6;
            Q6=makeQuery(id+"F20.imprint","IMPRINT",FACE,{"disambiguationData":[TD([[makeQuery(id+"F20.imprint","IMPRINT",EDGE,{"derivedFrom":sQuery(id+"F20.wireOp",EDGE,"E52.11.0.14")}),1.0]])]});
            var Q7;
            Q7=makeQuery(id+"F20.imprint","IMPRINT",FACE,{"disambiguationData":[TD([[makeQuery(id+"F20.imprint","IMPRINT",EDGE,{"derivedFrom":sQuery(id+"F20.wireOp",EDGE,"E52.12.0.15")}),1.0]])]});
            var Q8;
            Q8=makeQuery(id+"F20.imprint","IMPRINT",FACE,{"disambiguationData":[TD([[makeQuery(id+"F20.imprint","IMPRINT",EDGE,{"derivedFrom":sQuery(id+"F20.wireOp",EDGE,"E52.12.0.25")}),1.0]])]});
            var Q9;
            Q9=makeQuery(id+"F20.imprint","IMPRINT",FACE,{"disambiguationData":[TD([[makeQuery(id+"F20.imprint","IMPRINT",EDGE,{"derivedFrom":sQuery(id+"F20.wireOp",EDGE,"E52.12.0.19")}),1.0]])]});
            var Q10;
            Q10=makeQuery(id+"F20.imprint","IMPRINT",FACE,{"disambiguationData":[TD([[makeQuery(id+"F20.imprint","IMPRINT",EDGE,{"derivedFrom":sQuery(id+"F20.wireOp",EDGE,"E52.12.0.14")}),1.0]])]});
            var Q11;
            Q11=makeQuery(id+"F20.imprint","IMPRINT",FACE,{"disambiguationData":[TD([[makeQuery(id+"F20.imprint","IMPRINT",EDGE,{"derivedFrom":sQuery(id+"F20.wireOp",EDGE,"E52.13.0.15")}),1.0]])]});
            var Q12;
            Q12=makeQuery(id+"F20.imprint","IMPRINT",FACE,{"disambiguationData":[TD([[makeQuery(id+"F20.imprint","IMPRINT",EDGE,{"derivedFrom":sQuery(id+"F20.wireOp",EDGE,"E52.13.0.25")}),1.0]])]});
            var Q13;
            Q13=makeQuery(id+"F20.imprint","IMPRINT",FACE,{"disambiguationData":[TD([[makeQuery(id+"F20.imprint","IMPRINT",EDGE,{"derivedFrom":sQuery(id+"F20.wireOp",EDGE,"E52.13.0.19")}),1.0]])]});
            var Q14;
            Q14=makeQuery(id+"F20.imprint","IMPRINT",FACE,{"disambiguationData":[TD([[makeQuery(id+"F20.imprint","IMPRINT",EDGE,{"derivedFrom":sQuery(id+"F20.wireOp",EDGE,"E52.13.0.10")}),1.0]])]});
            var Q15;
            Q15=makeQuery(id+"F20.imprint","IMPRINT",FACE,{"disambiguationData":[TD([[makeQuery(id+"F20.imprint","IMPRINT",EDGE,{"derivedFrom":sQuery(id+"F20.wireOp",EDGE,"E52.13.0.4")}),1.0]])]});
            var Q16;
            Q16=makeQuery(id+"F20.imprint","IMPRINT",FACE,{"disambiguationData":[TD([[makeQuery(id+"F20.imprint","IMPRINT",EDGE,{"derivedFrom":sQuery(id+"F20.wireOp",EDGE,"E52.13.0.5")}),1.0]])]});
            var Q17;
            Q17=makeQuery(id+"F20.imprint","IMPRINT",FACE,{"disambiguationData":[TD([[makeQuery(id+"F20.imprint","IMPRINT",EDGE,{"derivedFrom":sQuery(id+"F20.wireOp",EDGE,"E52.13.0.6")}),1.0]])]});
            var Q18;
            Q18=makeQuery(id+"F20.imprint","IMPRINT",FACE,{"disambiguationData":[TD([[makeQuery(id+"F20.imprint","IMPRINT",EDGE,{"derivedFrom":sQuery(id+"F20.wireOp",EDGE,"E52.12.0.0")}),1.0]])]});
            var Q19;
            Q19=makeQuery(id+"F20.imprint","IMPRINT",FACE,{"disambiguationData":[TD([[makeQuery(id+"F20.imprint","IMPRINT",EDGE,{"derivedFrom":sQuery(id+"F20.wireOp",EDGE,"E52.12.0.4")}),1.0]])]});
            var Q20;
            Q20=makeQuery(id+"F20.imprint","IMPRINT",FACE,{"disambiguationData":[TD([[makeQuery(id+"F20.imprint","IMPRINT",EDGE,{"derivedFrom":sQuery(id+"F20.wireOp",EDGE,"E52.12.0.10")}),1.0]])]});
            var Q21;
            Q21=makeQuery(id+"F20.imprint","IMPRINT",FACE,{"disambiguationData":[TD([[makeQuery(id+"F20.imprint","IMPRINT",EDGE,{"derivedFrom":sQuery(id+"F20.wireOp",EDGE,"E52.12.0.6")}),1.0]])]});
            var Q22;
            Q22=makeQuery(id+"F20.imprint","IMPRINT",FACE,{"disambiguationData":[TD([[makeQuery(id+"F20.imprint","IMPRINT",EDGE,{"derivedFrom":sQuery(id+"F20.wireOp",EDGE,"E52.12.0.5")}),1.0]])]});
            var Q23;
            Q23=makeQuery(id+"F20.imprint","IMPRINT",FACE,{"disambiguationData":[TD([[makeQuery(id+"F20.imprint","IMPRINT",EDGE,{"derivedFrom":sQuery(id+"F20.wireOp",EDGE,"E52.11.0.0")}),1.0]])]});
            extrude(context, id + "F29", {"entities" : qUnion([Q0, Q1, Q2, Q3, Q4, Q5, Q6, Q7, Q8, Q9, Q10, Q11, Q12, Q13, Q14, Q15, Q16, Q17, Q18, Q19, Q20, Q21, Q22, Q23]), "operationType" : NewBodyOperationType.REMOVE, "endBound" : BoundingType.SYMMETRIC, "oppositeDirection" : true, "depth" : 50 * mm, "offsetDistance" : 25 * mm});
        }
        {
            var Q0;
            Q0=makeQuery(id+"F20.imprint","IMPRINT",FACE,{"disambiguationData":[TD([[makeQuery(id+"F20.imprint","IMPRINT",EDGE,{"derivedFrom":sQuery(id+"F20.wireOp",EDGE,"E52.15.0.22")}),1.0]])]});
            var Q1;
            Q1=makeQuery(id+"F20.imprint","IMPRINT",FACE,{"disambiguationData":[TD([[makeQuery(id+"F20.imprint","IMPRINT",EDGE,{"derivedFrom":sQuery(id+"F20.wireOp",EDGE,"E52.15.0.23")}),1.0]])]});
            var Q2;
            Q2=makeQuery(id+"F20.imprint","IMPRINT",FACE,{"disambiguationData":[TD([[makeQuery(id+"F20.imprint","IMPRINT",EDGE,{"derivedFrom":sQuery(id+"F20.wireOp",EDGE,"E52.14.0.26")}),1.0]])]});
            var Q3;
            Q3=makeQuery(id+"F20.imprint","IMPRINT",FACE,{"disambiguationData":[TD([[makeQuery(id+"F20.imprint","IMPRINT",EDGE,{"derivedFrom":sQuery(id+"F20.wireOp",EDGE,"E52.14.0.22")}),1.0]])]});
            var Q4;
            Q4=makeQuery(id+"F20.imprint","IMPRINT",FACE,{"disambiguationData":[TD([[makeQuery(id+"F20.imprint","IMPRINT",EDGE,{"derivedFrom":sQuery(id+"F20.wireOp",EDGE,"E52.14.0.23")}),1.0]])]});
            var Q5;
            Q5=makeQuery(id+"F20.imprint","IMPRINT",FACE,{"disambiguationData":[TD([[makeQuery(id+"F20.imprint","IMPRINT",EDGE,{"derivedFrom":sQuery(id+"F20.wireOp",EDGE,"E52.13.0.26")}),1.0]])]});
            var Q6;
            Q6=makeQuery(id+"F20.imprint","IMPRINT",FACE,{"disambiguationData":[TD([[makeQuery(id+"F20.imprint","IMPRINT",EDGE,{"derivedFrom":sQuery(id+"F20.wireOp",EDGE,"E52.13.0.14")}),1.0]])]});
            var Q7;
            Q7=makeQuery(id+"F20.imprint","IMPRINT",FACE,{"disambiguationData":[TD([[makeQuery(id+"F20.imprint","IMPRINT",EDGE,{"derivedFrom":sQuery(id+"F20.wireOp",EDGE,"E52.14.0.15")}),1.0]])]});
            var Q8;
            Q8=makeQuery(id+"F20.imprint","IMPRINT",FACE,{"disambiguationData":[TD([[makeQuery(id+"F20.imprint","IMPRINT",EDGE,{"derivedFrom":sQuery(id+"F20.wireOp",EDGE,"E52.14.0.25")}),1.0]])]});
            var Q9;
            Q9=makeQuery(id+"F20.imprint","IMPRINT",FACE,{"disambiguationData":[TD([[makeQuery(id+"F20.imprint","IMPRINT",EDGE,{"derivedFrom":sQuery(id+"F20.wireOp",EDGE,"E52.14.0.19")}),1.0]])]});
            var Q10;
            Q10=makeQuery(id+"F20.imprint","IMPRINT",FACE,{"disambiguationData":[TD([[makeQuery(id+"F20.imprint","IMPRINT",EDGE,{"derivedFrom":sQuery(id+"F20.wireOp",EDGE,"E52.14.0.14")}),1.0]])]});
            var Q11;
            Q11=makeQuery(id+"F20.imprint","IMPRINT",FACE,{"disambiguationData":[TD([[makeQuery(id+"F20.imprint","IMPRINT",EDGE,{"derivedFrom":sQuery(id+"F20.wireOp",EDGE,"E52.15.0.15")}),1.0]])]});
            var Q12;
            Q12=makeQuery(id+"F20.imprint","IMPRINT",FACE,{"disambiguationData":[TD([[makeQuery(id+"F20.imprint","IMPRINT",EDGE,{"derivedFrom":sQuery(id+"F20.wireOp",EDGE,"E52.15.0.25")}),1.0]])]});
            var Q13;
            Q13=makeQuery(id+"F20.imprint","IMPRINT",FACE,{"disambiguationData":[TD([[makeQuery(id+"F20.imprint","IMPRINT",EDGE,{"derivedFrom":sQuery(id+"F20.wireOp",EDGE,"E52.15.0.19")}),1.0]])]});
            var Q14;
            Q14=makeQuery(id+"F20.imprint","IMPRINT",FACE,{"disambiguationData":[TD([[makeQuery(id+"F20.imprint","IMPRINT",EDGE,{"derivedFrom":sQuery(id+"F20.wireOp",EDGE,"E52.15.0.10")}),1.0]])]});
            var Q15;
            Q15=makeQuery(id+"F20.imprint","IMPRINT",FACE,{"disambiguationData":[TD([[makeQuery(id+"F20.imprint","IMPRINT",EDGE,{"derivedFrom":sQuery(id+"F20.wireOp",EDGE,"E52.15.0.4")}),1.0]])]});
            var Q16;
            Q16=makeQuery(id+"F20.imprint","IMPRINT",FACE,{"disambiguationData":[TD([[makeQuery(id+"F20.imprint","IMPRINT",EDGE,{"derivedFrom":sQuery(id+"F20.wireOp",EDGE,"E52.15.0.5")}),1.0]])]});
            var Q17;
            Q17=makeQuery(id+"F20.imprint","IMPRINT",FACE,{"disambiguationData":[TD([[makeQuery(id+"F20.imprint","IMPRINT",EDGE,{"derivedFrom":sQuery(id+"F20.wireOp",EDGE,"E52.15.0.6")}),1.0]])]});
            var Q18;
            Q18=makeQuery(id+"F20.imprint","IMPRINT",FACE,{"disambiguationData":[TD([[makeQuery(id+"F20.imprint","IMPRINT",EDGE,{"derivedFrom":sQuery(id+"F20.wireOp",EDGE,"E52.14.0.0")}),1.0]])]});
            var Q19;
            Q19=makeQuery(id+"F20.imprint","IMPRINT",FACE,{"disambiguationData":[TD([[makeQuery(id+"F20.imprint","IMPRINT",EDGE,{"derivedFrom":sQuery(id+"F20.wireOp",EDGE,"E52.14.0.4")}),1.0]])]});
            var Q20;
            Q20=makeQuery(id+"F20.imprint","IMPRINT",FACE,{"disambiguationData":[TD([[makeQuery(id+"F20.imprint","IMPRINT",EDGE,{"derivedFrom":sQuery(id+"F20.wireOp",EDGE,"E52.14.0.10")}),1.0]])]});
            var Q21;
            Q21=makeQuery(id+"F20.imprint","IMPRINT",FACE,{"disambiguationData":[TD([[makeQuery(id+"F20.imprint","IMPRINT",EDGE,{"derivedFrom":sQuery(id+"F20.wireOp",EDGE,"E52.14.0.6")}),1.0]])]});
            var Q22;
            Q22=makeQuery(id+"F20.imprint","IMPRINT",FACE,{"disambiguationData":[TD([[makeQuery(id+"F20.imprint","IMPRINT",EDGE,{"derivedFrom":sQuery(id+"F20.wireOp",EDGE,"E52.14.0.5")}),1.0]])]});
            var Q23;
            Q23=makeQuery(id+"F20.imprint","IMPRINT",FACE,{"disambiguationData":[TD([[makeQuery(id+"F20.imprint","IMPRINT",EDGE,{"derivedFrom":sQuery(id+"F20.wireOp",EDGE,"E52.13.0.0")}),1.0]])]});
            extrude(context, id + "F30", {"entities" : qUnion([Q0, Q1, Q2, Q3, Q4, Q5, Q6, Q7, Q8, Q9, Q10, Q11, Q12, Q13, Q14, Q15, Q16, Q17, Q18, Q19, Q20, Q21, Q22, Q23]), "operationType" : NewBodyOperationType.REMOVE, "endBound" : BoundingType.SYMMETRIC, "oppositeDirection" : true, "depth" : 50 * mm, "offsetDistance" : 25 * mm});
        }
        {
            var Q0;
            Q0=makeQuery(id+"F20.imprint","IMPRINT",FACE,{"disambiguationData":[TD([[makeQuery(id+"F20.imprint","IMPRINT",EDGE,{"derivedFrom":sQuery(id+"F20.wireOp",EDGE,"E52.15.0.26")}),1.0]])]});
            var Q1;
            Q1=makeQuery(id+"F20.imprint","IMPRINT",FACE,{"disambiguationData":[TD([[makeQuery(id+"F20.imprint","IMPRINT",EDGE,{"derivedFrom":sQuery(id+"F20.wireOp",EDGE,"E52.16.0.23")}),1.0]])]});
            var Q2;
            Q2=makeQuery(id+"F20.imprint","IMPRINT",FACE,{"disambiguationData":[TD([[makeQuery(id+"F20.imprint","IMPRINT",EDGE,{"derivedFrom":sQuery(id+"F20.wireOp",EDGE,"E52.16.0.22")}),1.0]])]});
            var Q3;
            Q3=makeQuery(id+"F20.imprint","IMPRINT",FACE,{"disambiguationData":[TD([[makeQuery(id+"F20.imprint","IMPRINT",EDGE,{"derivedFrom":sQuery(id+"F20.wireOp",EDGE,"E52.16.0.26")}),1.0]])]});
            var Q4;
            Q4=makeQuery(id+"F20.imprint","IMPRINT",FACE,{"disambiguationData":[TD([[makeQuery(id+"F20.imprint","IMPRINT",EDGE,{"derivedFrom":sQuery(id+"F20.wireOp",EDGE,"E52.17.0.23")}),1.0]])]});
            var Q5;
            Q5=makeQuery(id+"F20.imprint","IMPRINT",FACE,{"disambiguationData":[TD([[makeQuery(id+"F20.imprint","IMPRINT",EDGE,{"derivedFrom":sQuery(id+"F20.wireOp",EDGE,"E52.17.0.22")}),1.0]])]});
            var Q6;
            Q6=makeQuery(id+"F20.imprint","IMPRINT",FACE,{"disambiguationData":[TD([[makeQuery(id+"F20.imprint","IMPRINT",EDGE,{"derivedFrom":sQuery(id+"F20.wireOp",EDGE,"E52.17.0.19")}),1.0]])]});
            var Q7;
            Q7=makeQuery(id+"F20.imprint","IMPRINT",FACE,{"disambiguationData":[TD([[makeQuery(id+"F20.imprint","IMPRINT",EDGE,{"derivedFrom":sQuery(id+"F20.wireOp",EDGE,"E52.17.0.15")}),1.0]])]});
            var Q8;
            Q8=makeQuery(id+"F20.imprint","IMPRINT",FACE,{"disambiguationData":[TD([[makeQuery(id+"F20.imprint","IMPRINT",EDGE,{"derivedFrom":sQuery(id+"F20.wireOp",EDGE,"E52.17.0.25")}),1.0]])]});
            var Q9;
            Q9=makeQuery(id+"F20.imprint","IMPRINT",FACE,{"disambiguationData":[TD([[makeQuery(id+"F20.imprint","IMPRINT",EDGE,{"derivedFrom":sQuery(id+"F20.wireOp",EDGE,"E52.16.0.14")}),1.0]])]});
            var Q10;
            Q10=makeQuery(id+"F20.imprint","IMPRINT",FACE,{"disambiguationData":[TD([[makeQuery(id+"F20.imprint","IMPRINT",EDGE,{"derivedFrom":sQuery(id+"F20.wireOp",EDGE,"E52.16.0.19")}),1.0]])]});
            var Q11;
            Q11=makeQuery(id+"F20.imprint","IMPRINT",FACE,{"disambiguationData":[TD([[makeQuery(id+"F20.imprint","IMPRINT",EDGE,{"derivedFrom":sQuery(id+"F20.wireOp",EDGE,"E52.16.0.25")}),1.0]])]});
            var Q12;
            Q12=makeQuery(id+"F20.imprint","IMPRINT",FACE,{"disambiguationData":[TD([[makeQuery(id+"F20.imprint","IMPRINT",EDGE,{"derivedFrom":sQuery(id+"F20.wireOp",EDGE,"E52.16.0.15")}),1.0]])]});
            var Q13;
            Q13=makeQuery(id+"F20.imprint","IMPRINT",FACE,{"disambiguationData":[TD([[makeQuery(id+"F20.imprint","IMPRINT",EDGE,{"derivedFrom":sQuery(id+"F20.wireOp",EDGE,"E52.15.0.14")}),1.0]])]});
            var Q14;
            Q14=makeQuery(id+"F20.imprint","IMPRINT",FACE,{"disambiguationData":[TD([[makeQuery(id+"F20.imprint","IMPRINT",EDGE,{"derivedFrom":sQuery(id+"F20.wireOp",EDGE,"E52.15.0.0")}),1.0]])]});
            var Q15;
            Q15=makeQuery(id+"F20.imprint","IMPRINT",FACE,{"disambiguationData":[TD([[makeQuery(id+"F20.imprint","IMPRINT",EDGE,{"derivedFrom":sQuery(id+"F20.wireOp",EDGE,"E52.16.0.5")}),1.0]])]});
            var Q16;
            Q16=makeQuery(id+"F20.imprint","IMPRINT",FACE,{"disambiguationData":[TD([[makeQuery(id+"F20.imprint","IMPRINT",EDGE,{"derivedFrom":sQuery(id+"F20.wireOp",EDGE,"E52.16.0.6")}),1.0]])]});
            var Q17;
            Q17=makeQuery(id+"F20.imprint","IMPRINT",FACE,{"disambiguationData":[TD([[makeQuery(id+"F20.imprint","IMPRINT",EDGE,{"derivedFrom":sQuery(id+"F20.wireOp",EDGE,"E52.16.0.10")}),1.0]])]});
            var Q18;
            Q18=makeQuery(id+"F20.imprint","IMPRINT",FACE,{"disambiguationData":[TD([[makeQuery(id+"F20.imprint","IMPRINT",EDGE,{"derivedFrom":sQuery(id+"F20.wireOp",EDGE,"E52.16.0.4")}),1.0]])]});
            var Q19;
            Q19=makeQuery(id+"F20.imprint","IMPRINT",FACE,{"disambiguationData":[TD([[makeQuery(id+"F20.imprint","IMPRINT",EDGE,{"derivedFrom":sQuery(id+"F20.wireOp",EDGE,"E52.16.0.0")}),1.0]])]});
            var Q20;
            Q20=makeQuery(id+"F20.imprint","IMPRINT",FACE,{"disambiguationData":[TD([[makeQuery(id+"F20.imprint","IMPRINT",EDGE,{"derivedFrom":sQuery(id+"F20.wireOp",EDGE,"E52.17.0.5")}),1.0]])]});
            var Q21;
            Q21=makeQuery(id+"F20.imprint","IMPRINT",FACE,{"disambiguationData":[TD([[makeQuery(id+"F20.imprint","IMPRINT",EDGE,{"derivedFrom":sQuery(id+"F20.wireOp",EDGE,"E52.17.0.6")}),1.0]])]});
            var Q22;
            Q22=makeQuery(id+"F20.imprint","IMPRINT",FACE,{"disambiguationData":[TD([[makeQuery(id+"F20.imprint","IMPRINT",EDGE,{"derivedFrom":sQuery(id+"F20.wireOp",EDGE,"E52.17.0.10")}),1.0]])]});
            var Q23;
            Q23=makeQuery(id+"F20.imprint","IMPRINT",FACE,{"disambiguationData":[TD([[makeQuery(id+"F20.imprint","IMPRINT",EDGE,{"derivedFrom":sQuery(id+"F20.wireOp",EDGE,"E52.17.0.4")}),1.0]])]});
            extrude(context, id + "F31", {"entities" : qUnion([Q0, Q1, Q2, Q3, Q4, Q5, Q6, Q7, Q8, Q9, Q10, Q11, Q12, Q13, Q14, Q15, Q16, Q17, Q18, Q19, Q20, Q21, Q22, Q23]), "operationType" : NewBodyOperationType.REMOVE, "endBound" : BoundingType.SYMMETRIC, "oppositeDirection" : true, "depth" : 50 * mm, "offsetDistance" : 25 * mm});
        }
        {
            var Q0;
            Q0=makeQuery(id+"F20.imprint","IMPRINT",FACE,{"disambiguationData":[TD([[makeQuery(id+"F20.imprint","IMPRINT",EDGE,{"derivedFrom":sQuery(id+"F20.wireOp",EDGE,"E52.18.0.19")}),1.0]])]});
            var Q1;
            Q1=makeQuery(id+"F20.imprint","IMPRINT",FACE,{"disambiguationData":[TD([[makeQuery(id+"F20.imprint","IMPRINT",EDGE,{"derivedFrom":sQuery(id+"F20.wireOp",EDGE,"E52.21.0.6")}),1.0]])]});
            var Q2;
            Q2=makeQuery(id+"F20.imprint","IMPRINT",FACE,{"disambiguationData":[TD([[makeQuery(id+"F20.imprint","IMPRINT",EDGE,{"derivedFrom":sQuery(id+"F20.wireOp",EDGE,"E52.19.0.26")}),1.0]])]});
            var Q3;
            Q3=makeQuery(id+"F20.imprint","IMPRINT",FACE,{"disambiguationData":[TD([[makeQuery(id+"F20.imprint","IMPRINT",EDGE,{"derivedFrom":sQuery(id+"F20.wireOp",EDGE,"E52.18.0.14")}),1.0]])]});
            var Q4;
            Q4=makeQuery(id+"F20.imprint","IMPRINT",FACE,{"disambiguationData":[TD([[makeQuery(id+"F20.imprint","IMPRINT",EDGE,{"derivedFrom":sQuery(id+"F20.wireOp",EDGE,"E52.21.0.4")}),1.0]])]});
            var Q5;
            Q5=makeQuery(id+"F20.imprint","IMPRINT",FACE,{"disambiguationData":[TD([[makeQuery(id+"F20.imprint","IMPRINT",EDGE,{"derivedFrom":sQuery(id+"F20.wireOp",EDGE,"E52.19.0.23")}),1.0]])]});
            var Q6;
            Q6=makeQuery(id+"F20.imprint","IMPRINT",FACE,{"disambiguationData":[TD([[makeQuery(id+"F20.imprint","IMPRINT",EDGE,{"derivedFrom":sQuery(id+"F20.wireOp",EDGE,"E52.18.0.15")}),1.0]])]});
            var Q7;
            Q7=makeQuery(id+"F20.imprint","IMPRINT",FACE,{"disambiguationData":[TD([[makeQuery(id+"F20.imprint","IMPRINT",EDGE,{"derivedFrom":sQuery(id+"F20.wireOp",EDGE,"E52.21.0.5")}),1.0]])]});
            var Q8;
            Q8=makeQuery(id+"F20.imprint","IMPRINT",FACE,{"disambiguationData":[TD([[makeQuery(id+"F20.imprint","IMPRINT",EDGE,{"derivedFrom":sQuery(id+"F20.wireOp",EDGE,"E52.19.0.25")}),1.0]])]});
            var Q9;
            Q9=makeQuery(id+"F20.imprint","IMPRINT",FACE,{"disambiguationData":[TD([[makeQuery(id+"F20.imprint","IMPRINT",EDGE,{"derivedFrom":sQuery(id+"F20.wireOp",EDGE,"E52.18.0.22")}),1.0]])]});
            var Q10;
            Q10=makeQuery(id+"F20.imprint","IMPRINT",FACE,{"disambiguationData":[TD([[makeQuery(id+"F20.imprint","IMPRINT",EDGE,{"derivedFrom":sQuery(id+"F20.wireOp",EDGE,"E52.21.0.10")}),1.0]])]});
            var Q11;
            Q11=makeQuery(id+"F20.imprint","IMPRINT",FACE,{"disambiguationData":[TD([[makeQuery(id+"F20.imprint","IMPRINT",EDGE,{"derivedFrom":sQuery(id+"F20.wireOp",EDGE,"E52.20.0.0")}),1.0]])]});
            var Q12;
            Q12=makeQuery(id+"F20.imprint","IMPRINT",FACE,{"disambiguationData":[TD([[makeQuery(id+"F20.imprint","IMPRINT",EDGE,{"derivedFrom":sQuery(id+"F20.wireOp",EDGE,"E52.18.0.23")}),1.0]])]});
            var Q13;
            Q13=makeQuery(id+"F20.imprint","IMPRINT",FACE,{"disambiguationData":[TD([[makeQuery(id+"F20.imprint","IMPRINT",EDGE,{"derivedFrom":sQuery(id+"F20.wireOp",EDGE,"E52.17.0.14")}),1.0]])]});
            var Q14;
            Q14=makeQuery(id+"F20.imprint","IMPRINT",FACE,{"disambiguationData":[TD([[makeQuery(id+"F20.imprint","IMPRINT",EDGE,{"derivedFrom":sQuery(id+"F20.wireOp",EDGE,"E52.20.0.4")}),1.0]])]});
            var Q15;
            Q15=makeQuery(id+"F20.imprint","IMPRINT",FACE,{"disambiguationData":[TD([[makeQuery(id+"F20.imprint","IMPRINT",EDGE,{"derivedFrom":sQuery(id+"F20.wireOp",EDGE,"E52.18.0.25")}),1.0]])]});
            var Q16;
            Q16=makeQuery(id+"F20.imprint","IMPRINT",FACE,{"disambiguationData":[TD([[makeQuery(id+"F20.imprint","IMPRINT",EDGE,{"derivedFrom":sQuery(id+"F20.wireOp",EDGE,"E52.21.0.15")}),1.0]])]});
            var Q17;
            Q17=makeQuery(id+"F20.imprint","IMPRINT",FACE,{"disambiguationData":[TD([[makeQuery(id+"F20.imprint","IMPRINT",EDGE,{"derivedFrom":sQuery(id+"F20.wireOp",EDGE,"E52.20.0.5")}),1.0]])]});
            var Q18;
            Q18=makeQuery(id+"F20.imprint","IMPRINT",FACE,{"disambiguationData":[TD([[makeQuery(id+"F20.imprint","IMPRINT",EDGE,{"derivedFrom":sQuery(id+"F20.wireOp",EDGE,"E52.18.0.26")}),1.0]])]});
            var Q19;
            Q19=makeQuery(id+"F20.imprint","IMPRINT",FACE,{"disambiguationData":[TD([[makeQuery(id+"F20.imprint","IMPRINT",EDGE,{"derivedFrom":sQuery(id+"F20.wireOp",EDGE,"E52.21.0.19")}),1.0]])]});
            var Q20;
            Q20=makeQuery(id+"F20.imprint","IMPRINT",FACE,{"disambiguationData":[TD([[makeQuery(id+"F20.imprint","IMPRINT",EDGE,{"derivedFrom":sQuery(id+"F20.wireOp",EDGE,"E52.20.0.6")}),1.0]])]});
            var Q21;
            Q21=makeQuery(id+"F20.imprint","IMPRINT",FACE,{"disambiguationData":[TD([[makeQuery(id+"F20.imprint","IMPRINT",EDGE,{"derivedFrom":sQuery(id+"F20.wireOp",EDGE,"E52.19.0.0")}),1.0]])]});
            var Q22;
            Q22=makeQuery(id+"F20.imprint","IMPRINT",FACE,{"disambiguationData":[TD([[makeQuery(id+"F20.imprint","IMPRINT",EDGE,{"derivedFrom":sQuery(id+"F20.wireOp",EDGE,"E52.21.0.22")}),1.0]])]});
            var Q23;
            Q23=makeQuery(id+"F20.imprint","IMPRINT",FACE,{"disambiguationData":[TD([[makeQuery(id+"F20.imprint","IMPRINT",EDGE,{"derivedFrom":sQuery(id+"F20.wireOp",EDGE,"E52.20.0.10")}),1.0]])]});
            var Q24;
            Q24=makeQuery(id+"F20.imprint","IMPRINT",FACE,{"disambiguationData":[TD([[makeQuery(id+"F20.imprint","IMPRINT",EDGE,{"derivedFrom":sQuery(id+"F20.wireOp",EDGE,"E52.19.0.4")}),1.0]])]});
            var Q25;
            Q25=makeQuery(id+"F20.imprint","IMPRINT",FACE,{"disambiguationData":[TD([[makeQuery(id+"F20.imprint","IMPRINT",EDGE,{"derivedFrom":sQuery(id+"F20.wireOp",EDGE,"E52.21.0.23")}),1.0]])]});
            var Q26;
            Q26=makeQuery(id+"F20.imprint","IMPRINT",FACE,{"disambiguationData":[TD([[makeQuery(id+"F20.imprint","IMPRINT",EDGE,{"derivedFrom":sQuery(id+"F20.wireOp",EDGE,"E52.20.0.14")}),1.0]])]});
            var Q27;
            Q27=makeQuery(id+"F20.imprint","IMPRINT",FACE,{"disambiguationData":[TD([[makeQuery(id+"F20.imprint","IMPRINT",EDGE,{"derivedFrom":sQuery(id+"F20.wireOp",EDGE,"E52.21.0.25")}),1.0]])]});
            var Q28;
            Q28=makeQuery(id+"F20.imprint","IMPRINT",FACE,{"disambiguationData":[TD([[makeQuery(id+"F20.imprint","IMPRINT",EDGE,{"derivedFrom":sQuery(id+"F20.wireOp",EDGE,"E52.20.0.15")}),1.0]])]});
            var Q29;
            Q29=makeQuery(id+"F20.imprint","IMPRINT",FACE,{"disambiguationData":[TD([[makeQuery(id+"F20.imprint","IMPRINT",EDGE,{"derivedFrom":sQuery(id+"F20.wireOp",EDGE,"E52.19.0.5")}),1.0]])]});
            var Q30;
            Q30=makeQuery(id+"F20.imprint","IMPRINT",FACE,{"disambiguationData":[TD([[makeQuery(id+"F20.imprint","IMPRINT",EDGE,{"derivedFrom":sQuery(id+"F20.wireOp",EDGE,"E52.20.0.19")}),1.0]])]});
            var Q31;
            Q31=makeQuery(id+"F20.imprint","IMPRINT",FACE,{"disambiguationData":[TD([[makeQuery(id+"F20.imprint","IMPRINT",EDGE,{"derivedFrom":sQuery(id+"F20.wireOp",EDGE,"E52.19.0.6")}),1.0]])]});
            var Q32;
            Q32=makeQuery(id+"F20.imprint","IMPRINT",FACE,{"disambiguationData":[TD([[makeQuery(id+"F20.imprint","IMPRINT",EDGE,{"derivedFrom":sQuery(id+"F20.wireOp",EDGE,"E52.17.0.26")}),1.0]])]});
            var Q33;
            Q33=makeQuery(id+"F20.imprint","IMPRINT",FACE,{"disambiguationData":[TD([[makeQuery(id+"F20.imprint","IMPRINT",EDGE,{"derivedFrom":sQuery(id+"F20.wireOp",EDGE,"E52.20.0.22")}),1.0]])]});
            var Q34;
            Q34=makeQuery(id+"F20.imprint","IMPRINT",FACE,{"disambiguationData":[TD([[makeQuery(id+"F20.imprint","IMPRINT",EDGE,{"derivedFrom":sQuery(id+"F20.wireOp",EDGE,"E52.19.0.10")}),1.0]])]});
            var Q35;
            Q35=makeQuery(id+"F20.imprint","IMPRINT",FACE,{"disambiguationData":[TD([[makeQuery(id+"F20.imprint","IMPRINT",EDGE,{"derivedFrom":sQuery(id+"F20.wireOp",EDGE,"E52.18.0.0")}),1.0]])]});
            var Q36;
            Q36=makeQuery(id+"F20.imprint","IMPRINT",FACE,{"disambiguationData":[TD([[makeQuery(id+"F20.imprint","IMPRINT",EDGE,{"derivedFrom":sQuery(id+"F20.wireOp",EDGE,"E52.20.0.23")}),1.0]])]});
            var Q37;
            Q37=makeQuery(id+"F20.imprint","IMPRINT",FACE,{"disambiguationData":[TD([[makeQuery(id+"F20.imprint","IMPRINT",EDGE,{"derivedFrom":sQuery(id+"F20.wireOp",EDGE,"E52.19.0.14")}),1.0]])]});
            var Q38;
            Q38=makeQuery(id+"F20.imprint","IMPRINT",FACE,{"disambiguationData":[TD([[makeQuery(id+"F20.imprint","IMPRINT",EDGE,{"derivedFrom":sQuery(id+"F20.wireOp",EDGE,"E52.18.0.4")}),1.0]])]});
            var Q39;
            Q39=makeQuery(id+"F20.imprint","IMPRINT",FACE,{"disambiguationData":[TD([[makeQuery(id+"F20.imprint","IMPRINT",EDGE,{"derivedFrom":sQuery(id+"F20.wireOp",EDGE,"E52.20.0.25")}),1.0]])]});
            var Q40;
            Q40=makeQuery(id+"F20.imprint","IMPRINT",FACE,{"disambiguationData":[TD([[makeQuery(id+"F20.imprint","IMPRINT",EDGE,{"derivedFrom":sQuery(id+"F20.wireOp",EDGE,"E52.19.0.15")}),1.0]])]});
            var Q41;
            Q41=makeQuery(id+"F20.imprint","IMPRINT",FACE,{"disambiguationData":[TD([[makeQuery(id+"F20.imprint","IMPRINT",EDGE,{"derivedFrom":sQuery(id+"F20.wireOp",EDGE,"E52.18.0.5")}),1.0]])]});
            var Q42;
            Q42=makeQuery(id+"F20.imprint","IMPRINT",FACE,{"disambiguationData":[TD([[makeQuery(id+"F20.imprint","IMPRINT",EDGE,{"derivedFrom":sQuery(id+"F20.wireOp",EDGE,"E52.20.0.26")}),1.0]])]});
            var Q43;
            Q43=makeQuery(id+"F20.imprint","IMPRINT",FACE,{"disambiguationData":[TD([[makeQuery(id+"F20.imprint","IMPRINT",EDGE,{"derivedFrom":sQuery(id+"F20.wireOp",EDGE,"E52.19.0.19")}),1.0]])]});
            var Q44;
            Q44=makeQuery(id+"F20.imprint","IMPRINT",FACE,{"disambiguationData":[TD([[makeQuery(id+"F20.imprint","IMPRINT",EDGE,{"derivedFrom":sQuery(id+"F20.wireOp",EDGE,"E52.18.0.6")}),1.0]])]});
            var Q45;
            Q45=makeQuery(id+"F20.imprint","IMPRINT",FACE,{"disambiguationData":[TD([[makeQuery(id+"F20.imprint","IMPRINT",EDGE,{"derivedFrom":sQuery(id+"F20.wireOp",EDGE,"E52.17.0.0")}),1.0]])]});
            var Q46;
            Q46=makeQuery(id+"F20.imprint","IMPRINT",FACE,{"disambiguationData":[TD([[makeQuery(id+"F20.imprint","IMPRINT",EDGE,{"derivedFrom":sQuery(id+"F20.wireOp",EDGE,"E52.19.0.22")}),1.0]])]});
            var Q47;
            Q47=makeQuery(id+"F20.imprint","IMPRINT",FACE,{"disambiguationData":[TD([[makeQuery(id+"F20.imprint","IMPRINT",EDGE,{"derivedFrom":sQuery(id+"F20.wireOp",EDGE,"E52.18.0.10")}),1.0]])]});
            extrude(context, id + "F32", {"entities" : qUnion([Q0, Q1, Q2, Q3, Q4, Q5, Q6, Q7, Q8, Q9, Q10, Q11, Q12, Q13, Q14, Q15, Q16, Q17, Q18, Q19, Q20, Q21, Q22, Q23, Q24, Q25, Q26, Q27, Q28, Q29, Q30, Q31, Q32, Q33, Q34, Q35, Q36, Q37, Q38, Q39, Q40, Q41, Q42, Q43, Q44, Q45, Q46, Q47]), "operationType" : NewBodyOperationType.REMOVE, "endBound" : BoundingType.SYMMETRIC, "oppositeDirection" : true, "depth" : 56 * mm, "offsetDistance" : 25 * mm});
        }
        {
            var Q0;
            Q0=makeQuery(id+"F20.imprint","IMPRINT",FACE,{"disambiguationData":[TD([[makeQuery(id+"F20.imprint","IMPRINT",EDGE,{"derivedFrom":sQuery(id+"F20.wireOp",EDGE,"E52.21.0.26")}),1.0]])]});
            var Q1;
            Q1=makeQuery(id+"F20.imprint","IMPRINT",FACE,{"disambiguationData":[TD([[makeQuery(id+"F20.imprint","IMPRINT",EDGE,{"derivedFrom":sQuery(id+"F20.wireOp",EDGE,"E52.21.0.14")}),1.0]])]});
            var Q2;
            Q2=makeQuery(id+"F20.imprint","IMPRINT",FACE,{"disambiguationData":[TD([[makeQuery(id+"F20.imprint","IMPRINT",EDGE,{"derivedFrom":sQuery(id+"F20.wireOp",EDGE,"E52.21.0.0")}),1.0]])]});
            var Q3;
            Q3=makeQuery(id+"F20.imprint","IMPRINT",FACE,{"disambiguationData":[TD([[makeQuery(id+"F20.imprint","IMPRINT",EDGE,{"derivedFrom":sQuery(id+"F20.wireOp",EDGE,"E52.22.0.5")}),1.0]])]});
            var Q4;
            Q4=makeQuery(id+"F20.imprint","IMPRINT",FACE,{"disambiguationData":[TD([[makeQuery(id+"F20.imprint","IMPRINT",EDGE,{"derivedFrom":sQuery(id+"F20.wireOp",EDGE,"E52.22.0.6")}),1.0]])]});
            var Q5;
            Q5=makeQuery(id+"F20.imprint","IMPRINT",FACE,{"disambiguationData":[TD([[makeQuery(id+"F20.imprint","IMPRINT",EDGE,{"derivedFrom":sQuery(id+"F20.wireOp",EDGE,"E52.22.0.15")}),1.0]])]});
            var Q6;
            Q6=makeQuery(id+"F20.imprint","IMPRINT",FACE,{"disambiguationData":[TD([[makeQuery(id+"F20.imprint","IMPRINT",EDGE,{"derivedFrom":sQuery(id+"F20.wireOp",EDGE,"E52.22.0.23")}),1.0]])]});
            var Q7;
            Q7=makeQuery(id+"F20.imprint","IMPRINT",FACE,{"disambiguationData":[TD([[makeQuery(id+"F20.imprint","IMPRINT",EDGE,{"derivedFrom":sQuery(id+"F20.wireOp",EDGE,"E52.22.0.22")}),1.0]])]});
            var Q8;
            Q8=makeQuery(id+"F20.imprint","IMPRINT",FACE,{"disambiguationData":[TD([[makeQuery(id+"F20.imprint","IMPRINT",EDGE,{"derivedFrom":sQuery(id+"F20.wireOp",EDGE,"E52.22.0.19")}),1.0]])]});
            var Q9;
            Q9=makeQuery(id+"F20.imprint","IMPRINT",FACE,{"disambiguationData":[TD([[makeQuery(id+"F20.imprint","IMPRINT",EDGE,{"derivedFrom":sQuery(id+"F20.wireOp",EDGE,"E52.22.0.25")}),1.0]])]});
            var Q10;
            Q10=makeQuery(id+"F20.imprint","IMPRINT",FACE,{"disambiguationData":[TD([[makeQuery(id+"F20.imprint","IMPRINT",EDGE,{"derivedFrom":sQuery(id+"F20.wireOp",EDGE,"E52.22.0.10")}),1.0]])]});
            var Q11;
            Q11=makeQuery(id+"F20.imprint","IMPRINT",FACE,{"disambiguationData":[TD([[makeQuery(id+"F20.imprint","IMPRINT",EDGE,{"derivedFrom":sQuery(id+"F20.wireOp",EDGE,"E52.22.0.4")}),1.0]])]});
            var Q12;
            Q12=makeQuery(id+"F20.imprint","IMPRINT",FACE,{"disambiguationData":[TD([[makeQuery(id+"F20.imprint","IMPRINT",EDGE,{"derivedFrom":sQuery(id+"F20.wireOp",EDGE,"E52.22.0.14")}),1.0]])]});
            var Q13;
            Q13=makeQuery(id+"F20.imprint","IMPRINT",FACE,{"disambiguationData":[TD([[makeQuery(id+"F20.imprint","IMPRINT",EDGE,{"derivedFrom":sQuery(id+"F20.wireOp",EDGE,"E52.22.0.0")}),1.0]])]});
            var Q14;
            Q14=makeQuery(id+"F20.imprint","IMPRINT",FACE,{"disambiguationData":[TD([[makeQuery(id+"F20.imprint","IMPRINT",EDGE,{"derivedFrom":sQuery(id+"F20.wireOp",EDGE,"E52.22.0.26")}),1.0]])]});
            var Q15;
            Q15=makeQuery(id+"F20.imprint","IMPRINT",FACE,{"disambiguationData":[TD([[makeQuery(id+"F20.imprint","IMPRINT",EDGE,{"derivedFrom":sQuery(id+"F20.wireOp",EDGE,"E52.23.0.23")}),1.0]])]});
            var Q16;
            Q16=makeQuery(id+"F20.imprint","IMPRINT",FACE,{"disambiguationData":[TD([[makeQuery(id+"F20.imprint","IMPRINT",EDGE,{"derivedFrom":sQuery(id+"F20.wireOp",EDGE,"E52.23.0.15")}),1.0]])]});
            var Q17;
            Q17=makeQuery(id+"F20.imprint","IMPRINT",FACE,{"disambiguationData":[TD([[makeQuery(id+"F20.imprint","IMPRINT",EDGE,{"derivedFrom":sQuery(id+"F20.wireOp",EDGE,"E52.23.0.6")}),1.0]])]});
            var Q18;
            Q18=makeQuery(id+"F20.imprint","IMPRINT",FACE,{"disambiguationData":[TD([[makeQuery(id+"F20.imprint","IMPRINT",EDGE,{"derivedFrom":sQuery(id+"F20.wireOp",EDGE,"E52.23.0.5")}),1.0]])]});
            var Q19;
            Q19=makeQuery(id+"F20.imprint","IMPRINT",FACE,{"disambiguationData":[TD([[makeQuery(id+"F20.imprint","IMPRINT",EDGE,{"derivedFrom":sQuery(id+"F20.wireOp",EDGE,"E52.23.0.25")}),1.0]])]});
            var Q20;
            Q20=makeQuery(id+"F20.imprint","IMPRINT",FACE,{"disambiguationData":[TD([[makeQuery(id+"F20.imprint","IMPRINT",EDGE,{"derivedFrom":sQuery(id+"F20.wireOp",EDGE,"E52.23.0.10")}),1.0]])]});
            var Q21;
            Q21=makeQuery(id+"F20.imprint","IMPRINT",FACE,{"disambiguationData":[TD([[makeQuery(id+"F20.imprint","IMPRINT",EDGE,{"derivedFrom":sQuery(id+"F20.wireOp",EDGE,"E52.23.0.4")}),1.0]])]});
            var Q22;
            Q22=makeQuery(id+"F20.imprint","IMPRINT",FACE,{"disambiguationData":[TD([[makeQuery(id+"F20.imprint","IMPRINT",EDGE,{"derivedFrom":sQuery(id+"F20.wireOp",EDGE,"E52.23.0.19")}),1.0]])]});
            var Q23;
            Q23=makeQuery(id+"F20.imprint","IMPRINT",FACE,{"disambiguationData":[TD([[makeQuery(id+"F20.imprint","IMPRINT",EDGE,{"derivedFrom":sQuery(id+"F20.wireOp",EDGE,"E52.23.0.22")}),1.0]])]});
            var Q24;
            Q24=makeQuery(id+"F20.imprint","IMPRINT",FACE,{"disambiguationData":[TD([[makeQuery(id+"F20.imprint","IMPRINT",EDGE,{"derivedFrom":sQuery(id+"F20.wireOp",EDGE,"E52.23.0.14")}),1.0]])]});
            var Q25;
            Q25=makeQuery(id+"F20.imprint","IMPRINT",FACE,{"disambiguationData":[TD([[makeQuery(id+"F20.imprint","IMPRINT",EDGE,{"derivedFrom":sQuery(id+"F20.wireOp",EDGE,"E52.23.0.0")}),1.0]])]});
            var Q26;
            Q26=makeQuery(id+"F20.imprint","IMPRINT",FACE,{"disambiguationData":[TD([[makeQuery(id+"F20.imprint","IMPRINT",EDGE,{"derivedFrom":sQuery(id+"F20.wireOp",EDGE,"E52.23.0.26")}),1.0]])]});
            var Q27;
            Q27=makeQuery(id+"F20.imprint","IMPRINT",FACE,{"disambiguationData":[TD([[makeQuery(id+"F20.imprint","IMPRINT",EDGE,{"derivedFrom":sQuery(id+"F20.wireOp",EDGE,"E52.24.0.23")}),1.0]])]});
            var Q28;
            Q28=makeQuery(id+"F20.imprint","IMPRINT",FACE,{"disambiguationData":[TD([[makeQuery(id+"F20.imprint","IMPRINT",EDGE,{"derivedFrom":sQuery(id+"F20.wireOp",EDGE,"E52.24.0.15")}),1.0]])]});
            var Q29;
            Q29=makeQuery(id+"F20.imprint","IMPRINT",FACE,{"disambiguationData":[TD([[makeQuery(id+"F20.imprint","IMPRINT",EDGE,{"derivedFrom":sQuery(id+"F20.wireOp",EDGE,"E52.24.0.6")}),1.0]])]});
            var Q30;
            Q30=makeQuery(id+"F20.imprint","IMPRINT",FACE,{"disambiguationData":[TD([[makeQuery(id+"F20.imprint","IMPRINT",EDGE,{"derivedFrom":sQuery(id+"F20.wireOp",EDGE,"E52.24.0.5")}),1.0]])]});
            var Q31;
            Q31=makeQuery(id+"F20.imprint","IMPRINT",FACE,{"disambiguationData":[TD([[makeQuery(id+"F20.imprint","IMPRINT",EDGE,{"derivedFrom":sQuery(id+"F20.wireOp",EDGE,"E52.24.0.25")}),1.0]])]});
            var Q32;
            Q32=makeQuery(id+"F20.imprint","IMPRINT",FACE,{"disambiguationData":[TD([[makeQuery(id+"F20.imprint","IMPRINT",EDGE,{"derivedFrom":sQuery(id+"F20.wireOp",EDGE,"E52.24.0.19")}),1.0]])]});
            var Q33;
            Q33=makeQuery(id+"F20.imprint","IMPRINT",FACE,{"disambiguationData":[TD([[makeQuery(id+"F20.imprint","IMPRINT",EDGE,{"derivedFrom":sQuery(id+"F20.wireOp",EDGE,"E52.24.0.22")}),1.0]])]});
            var Q34;
            Q34=makeQuery(id+"F20.imprint","IMPRINT",FACE,{"disambiguationData":[TD([[makeQuery(id+"F20.imprint","IMPRINT",EDGE,{"derivedFrom":sQuery(id+"F20.wireOp",EDGE,"E52.24.0.10")}),1.0]])]});
            var Q35;
            Q35=makeQuery(id+"F20.imprint","IMPRINT",FACE,{"disambiguationData":[TD([[makeQuery(id+"F20.imprint","IMPRINT",EDGE,{"derivedFrom":sQuery(id+"F20.wireOp",EDGE,"E52.24.0.4")}),1.0]])]});
            var Q36;
            Q36=makeQuery(id+"F20.imprint","IMPRINT",FACE,{"disambiguationData":[TD([[makeQuery(id+"F20.imprint","IMPRINT",EDGE,{"derivedFrom":sQuery(id+"F20.wireOp",EDGE,"E52.24.0.14")}),1.0]])]});
            var Q37;
            Q37=makeQuery(id+"F20.imprint","IMPRINT",FACE,{"disambiguationData":[TD([[makeQuery(id+"F20.imprint","IMPRINT",EDGE,{"derivedFrom":sQuery(id+"F20.wireOp",EDGE,"E52.24.0.0")}),1.0]])]});
            var Q38;
            Q38=makeQuery(id+"F20.imprint","IMPRINT",FACE,{"disambiguationData":[TD([[makeQuery(id+"F20.imprint","IMPRINT",EDGE,{"derivedFrom":sQuery(id+"F20.wireOp",EDGE,"E52.24.0.26")}),1.0]])]});
            var Q39;
            Q39=makeQuery(id+"F20.imprint","IMPRINT",FACE,{"disambiguationData":[TD([[makeQuery(id+"F20.imprint","IMPRINT",EDGE,{"derivedFrom":sQuery(id+"F20.wireOp",EDGE,"E52.25.0.23")}),1.0]])]});
            var Q40;
            Q40=makeQuery(id+"F20.imprint","IMPRINT",FACE,{"disambiguationData":[TD([[makeQuery(id+"F20.imprint","IMPRINT",EDGE,{"derivedFrom":sQuery(id+"F20.wireOp",EDGE,"E52.25.0.15")}),1.0]])]});
            var Q41;
            Q41=makeQuery(id+"F20.imprint","IMPRINT",FACE,{"disambiguationData":[TD([[makeQuery(id+"F20.imprint","IMPRINT",EDGE,{"derivedFrom":sQuery(id+"F20.wireOp",EDGE,"E52.25.0.6")}),1.0]])]});
            var Q42;
            Q42=makeQuery(id+"F20.imprint","IMPRINT",FACE,{"disambiguationData":[TD([[makeQuery(id+"F20.imprint","IMPRINT",EDGE,{"derivedFrom":sQuery(id+"F20.wireOp",EDGE,"E52.25.0.5")}),1.0]])]});
            var Q43;
            Q43=makeQuery(id+"F20.imprint","IMPRINT",FACE,{"disambiguationData":[TD([[makeQuery(id+"F20.imprint","IMPRINT",EDGE,{"derivedFrom":sQuery(id+"F20.wireOp",EDGE,"E52.25.0.25")}),1.0]])]});
            var Q44;
            Q44=makeQuery(id+"F20.imprint","IMPRINT",FACE,{"disambiguationData":[TD([[makeQuery(id+"F20.imprint","IMPRINT",EDGE,{"derivedFrom":sQuery(id+"F20.wireOp",EDGE,"E52.25.0.10")}),1.0]])]});
            var Q45;
            Q45=makeQuery(id+"F20.imprint","IMPRINT",FACE,{"disambiguationData":[TD([[makeQuery(id+"F20.imprint","IMPRINT",EDGE,{"derivedFrom":sQuery(id+"F20.wireOp",EDGE,"E52.25.0.4")}),1.0]])]});
            var Q46;
            Q46=makeQuery(id+"F20.imprint","IMPRINT",FACE,{"disambiguationData":[TD([[makeQuery(id+"F20.imprint","IMPRINT",EDGE,{"derivedFrom":sQuery(id+"F20.wireOp",EDGE,"E52.25.0.22")}),1.0]])]});
            var Q47;
            Q47=makeQuery(id+"F20.imprint","IMPRINT",FACE,{"disambiguationData":[TD([[makeQuery(id+"F20.imprint","IMPRINT",EDGE,{"derivedFrom":sQuery(id+"F20.wireOp",EDGE,"E52.25.0.19")}),1.0]])]});
            extrude(context, id + "F33", {"entities" : qUnion([Q0, Q1, Q2, Q3, Q4, Q5, Q6, Q7, Q8, Q9, Q10, Q11, Q12, Q13, Q14, Q15, Q16, Q17, Q18, Q19, Q20, Q21, Q22, Q23, Q24, Q25, Q26, Q27, Q28, Q29, Q30, Q31, Q32, Q33, Q34, Q35, Q36, Q37, Q38, Q39, Q40, Q41, Q42, Q43, Q44, Q45, Q46, Q47]), "operationType" : NewBodyOperationType.REMOVE, "endBound" : BoundingType.SYMMETRIC, "depth" : 56 * mm, "offsetDistance" : 25 * mm});
        }
        {
            var Q0;
            Q0=makeQuery(id+"F20.imprint","IMPRINT",FACE,{"disambiguationData":[TD([[makeQuery(id+"F20.imprint","IMPRINT",EDGE,{"derivedFrom":sQuery(id+"F20.wireOp",EDGE,"E52.29.0.4")}),1.0]])]});
            var Q1;
            Q1=makeQuery(id+"F20.imprint","IMPRINT",FACE,{"disambiguationData":[TD([[makeQuery(id+"F20.imprint","IMPRINT",EDGE,{"derivedFrom":sQuery(id+"F20.wireOp",EDGE,"E52.26.0.14")}),1.0]])]});
            var Q2;
            Q2=makeQuery(id+"F20.imprint","IMPRINT",FACE,{"disambiguationData":[TD([[makeQuery(id+"F20.imprint","IMPRINT",EDGE,{"derivedFrom":sQuery(id+"F20.wireOp",EDGE,"E52.29.0.5")}),1.0]])]});
            var Q3;
            Q3=makeQuery(id+"F20.imprint","IMPRINT",FACE,{"disambiguationData":[TD([[makeQuery(id+"F20.imprint","IMPRINT",EDGE,{"derivedFrom":sQuery(id+"F20.wireOp",EDGE,"E52.27.0.25")}),1.0]])]});
            var Q4;
            Q4=makeQuery(id+"F20.imprint","IMPRINT",FACE,{"disambiguationData":[TD([[makeQuery(id+"F20.imprint","IMPRINT",EDGE,{"derivedFrom":sQuery(id+"F20.wireOp",EDGE,"E52.26.0.23")}),1.0]])]});
            var Q5;
            Q5=makeQuery(id+"F20.imprint","IMPRINT",FACE,{"disambiguationData":[TD([[makeQuery(id+"F20.imprint","IMPRINT",EDGE,{"derivedFrom":sQuery(id+"F20.wireOp",EDGE,"E52.25.0.14")}),1.0]])]});
            var Q6;
            Q6=makeQuery(id+"F20.imprint","IMPRINT",FACE,{"disambiguationData":[TD([[makeQuery(id+"F20.imprint","IMPRINT",EDGE,{"derivedFrom":sQuery(id+"F20.wireOp",EDGE,"E52.28.0.5")}),1.0]])]});
            var Q7;
            Q7=makeQuery(id+"F20.imprint","IMPRINT",FACE,{"disambiguationData":[TD([[makeQuery(id+"F20.imprint","IMPRINT",EDGE,{"derivedFrom":sQuery(id+"F20.wireOp",EDGE,"E52.26.0.25")}),1.0]])]});
            var Q8;
            Q8=makeQuery(id+"F20.imprint","IMPRINT",FACE,{"disambiguationData":[TD([[makeQuery(id+"F20.imprint","IMPRINT",EDGE,{"derivedFrom":sQuery(id+"F20.wireOp",EDGE,"E52.29.0.23")}),1.0]])]});
            var Q9;
            Q9=makeQuery(id+"F20.imprint","IMPRINT",FACE,{"disambiguationData":[TD([[makeQuery(id+"F20.imprint","IMPRINT",EDGE,{"derivedFrom":sQuery(id+"F20.wireOp",EDGE,"E52.28.0.14")}),1.0]])]});
            var Q10;
            Q10=makeQuery(id+"F20.imprint","IMPRINT",FACE,{"disambiguationData":[TD([[makeQuery(id+"F20.imprint","IMPRINT",EDGE,{"derivedFrom":sQuery(id+"F20.wireOp",EDGE,"E52.27.0.4")}),1.0]])]});
            var Q11;
            Q11=makeQuery(id+"F20.imprint","IMPRINT",FACE,{"disambiguationData":[TD([[makeQuery(id+"F20.imprint","IMPRINT",EDGE,{"derivedFrom":sQuery(id+"F20.wireOp",EDGE,"E52.27.0.5")}),1.0]])]});
            var Q12;
            Q12=makeQuery(id+"F20.imprint","IMPRINT",FACE,{"disambiguationData":[TD([[makeQuery(id+"F20.imprint","IMPRINT",EDGE,{"derivedFrom":sQuery(id+"F20.wireOp",EDGE,"E52.29.0.25")}),1.0]])]});
            var Q13;
            Q13=makeQuery(id+"F20.imprint","IMPRINT",FACE,{"disambiguationData":[TD([[makeQuery(id+"F20.imprint","IMPRINT",EDGE,{"derivedFrom":sQuery(id+"F20.wireOp",EDGE,"E52.28.0.22")}),1.0]])]});
            var Q14;
            Q14=makeQuery(id+"F20.imprint","IMPRINT",FACE,{"disambiguationData":[TD([[makeQuery(id+"F20.imprint","IMPRINT",EDGE,{"derivedFrom":sQuery(id+"F20.wireOp",EDGE,"E52.28.0.23")}),1.0]])]});
            var Q15;
            Q15=makeQuery(id+"F20.imprint","IMPRINT",FACE,{"disambiguationData":[TD([[makeQuery(id+"F20.imprint","IMPRINT",EDGE,{"derivedFrom":sQuery(id+"F20.wireOp",EDGE,"E52.27.0.14")}),1.0]])]});
            var Q16;
            Q16=makeQuery(id+"F20.imprint","IMPRINT",FACE,{"disambiguationData":[TD([[makeQuery(id+"F20.imprint","IMPRINT",EDGE,{"derivedFrom":sQuery(id+"F20.wireOp",EDGE,"E52.26.0.4")}),1.0]])]});
            var Q17;
            Q17=makeQuery(id+"F20.imprint","IMPRINT",FACE,{"disambiguationData":[TD([[makeQuery(id+"F20.imprint","IMPRINT",EDGE,{"derivedFrom":sQuery(id+"F20.wireOp",EDGE,"E52.26.0.5")}),1.0]])]});
            var Q18;
            Q18=makeQuery(id+"F20.imprint","IMPRINT",FACE,{"disambiguationData":[TD([[makeQuery(id+"F20.imprint","IMPRINT",EDGE,{"derivedFrom":sQuery(id+"F20.wireOp",EDGE,"E52.28.0.25")}),1.0]])]});
            var Q19;
            Q19=makeQuery(id+"F20.imprint","IMPRINT",FACE,{"disambiguationData":[TD([[makeQuery(id+"F20.imprint","IMPRINT",EDGE,{"derivedFrom":sQuery(id+"F20.wireOp",EDGE,"E52.27.0.22")}),1.0]])]});
            var Q20;
            Q20=makeQuery(id+"F20.imprint","IMPRINT",FACE,{"disambiguationData":[TD([[makeQuery(id+"F20.imprint","IMPRINT",EDGE,{"derivedFrom":sQuery(id+"F20.wireOp",EDGE,"E52.29.0.6")}),1.0]])]});
            var Q21;
            Q21=makeQuery(id+"F20.imprint","IMPRINT",FACE,{"disambiguationData":[TD([[makeQuery(id+"F20.imprint","IMPRINT",EDGE,{"derivedFrom":sQuery(id+"F20.wireOp",EDGE,"E52.27.0.26")}),1.0]])]});
            var Q22;
            Q22=makeQuery(id+"F20.imprint","IMPRINT",FACE,{"disambiguationData":[TD([[makeQuery(id+"F20.imprint","IMPRINT",EDGE,{"derivedFrom":sQuery(id+"F20.wireOp",EDGE,"E52.26.0.19")}),1.0]])]});
            var Q23;
            Q23=makeQuery(id+"F20.imprint","IMPRINT",FACE,{"disambiguationData":[TD([[makeQuery(id+"F20.imprint","IMPRINT",EDGE,{"derivedFrom":sQuery(id+"F20.wireOp",EDGE,"E52.27.0.23")}),1.0]])]});
            var Q24;
            Q24=makeQuery(id+"F20.imprint","IMPRINT",FACE,{"disambiguationData":[TD([[makeQuery(id+"F20.imprint","IMPRINT",EDGE,{"derivedFrom":sQuery(id+"F20.wireOp",EDGE,"E52.26.0.15")}),1.0]])]});
            var Q25;
            Q25=makeQuery(id+"F20.imprint","IMPRINT",FACE,{"disambiguationData":[TD([[makeQuery(id+"F20.imprint","IMPRINT",EDGE,{"derivedFrom":sQuery(id+"F20.wireOp",EDGE,"E52.29.0.10")}),1.0]])]});
            var Q26;
            Q26=makeQuery(id+"F20.imprint","IMPRINT",FACE,{"disambiguationData":[TD([[makeQuery(id+"F20.imprint","IMPRINT",EDGE,{"derivedFrom":sQuery(id+"F20.wireOp",EDGE,"E52.28.0.0")}),1.0]])]});
            var Q27;
            Q27=makeQuery(id+"F20.imprint","IMPRINT",FACE,{"disambiguationData":[TD([[makeQuery(id+"F20.imprint","IMPRINT",EDGE,{"derivedFrom":sQuery(id+"F20.wireOp",EDGE,"E52.26.0.22")}),1.0]])]});
            var Q28;
            Q28=makeQuery(id+"F20.imprint","IMPRINT",FACE,{"disambiguationData":[TD([[makeQuery(id+"F20.imprint","IMPRINT",EDGE,{"derivedFrom":sQuery(id+"F20.wireOp",EDGE,"E52.28.0.4")}),1.0]])]});
            var Q29;
            Q29=makeQuery(id+"F20.imprint","IMPRINT",FACE,{"disambiguationData":[TD([[makeQuery(id+"F20.imprint","IMPRINT",EDGE,{"derivedFrom":sQuery(id+"F20.wireOp",EDGE,"E52.29.0.15")}),1.0]])]});
            var Q30;
            Q30=makeQuery(id+"F20.imprint","IMPRINT",FACE,{"disambiguationData":[TD([[makeQuery(id+"F20.imprint","IMPRINT",EDGE,{"derivedFrom":sQuery(id+"F20.wireOp",EDGE,"E52.29.0.19")}),1.0]])]});
            var Q31;
            Q31=makeQuery(id+"F20.imprint","IMPRINT",FACE,{"disambiguationData":[TD([[makeQuery(id+"F20.imprint","IMPRINT",EDGE,{"derivedFrom":sQuery(id+"F20.wireOp",EDGE,"E52.28.0.6")}),1.0]])]});
            var Q32;
            Q32=makeQuery(id+"F20.imprint","IMPRINT",FACE,{"disambiguationData":[TD([[makeQuery(id+"F20.imprint","IMPRINT",EDGE,{"derivedFrom":sQuery(id+"F20.wireOp",EDGE,"E52.26.0.26")}),1.0]])]});
            var Q33;
            Q33=makeQuery(id+"F20.imprint","IMPRINT",FACE,{"disambiguationData":[TD([[makeQuery(id+"F20.imprint","IMPRINT",EDGE,{"derivedFrom":sQuery(id+"F20.wireOp",EDGE,"E52.29.0.22")}),1.0]])]});
            var Q34;
            Q34=makeQuery(id+"F20.imprint","IMPRINT",FACE,{"disambiguationData":[TD([[makeQuery(id+"F20.imprint","IMPRINT",EDGE,{"derivedFrom":sQuery(id+"F20.wireOp",EDGE,"E52.28.0.10")}),1.0]])]});
            var Q35;
            Q35=makeQuery(id+"F20.imprint","IMPRINT",FACE,{"disambiguationData":[TD([[makeQuery(id+"F20.imprint","IMPRINT",EDGE,{"derivedFrom":sQuery(id+"F20.wireOp",EDGE,"E52.27.0.0")}),1.0]])]});
            var Q36;
            Q36=makeQuery(id+"F20.imprint","IMPRINT",FACE,{"disambiguationData":[TD([[makeQuery(id+"F20.imprint","IMPRINT",EDGE,{"derivedFrom":sQuery(id+"F20.wireOp",EDGE,"E52.28.0.15")}),1.0]])]});
            var Q37;
            Q37=makeQuery(id+"F20.imprint","IMPRINT",FACE,{"disambiguationData":[TD([[makeQuery(id+"F20.imprint","IMPRINT",EDGE,{"derivedFrom":sQuery(id+"F20.wireOp",EDGE,"E52.27.0.6")}),1.0]])]});
            var Q38;
            Q38=makeQuery(id+"F20.imprint","IMPRINT",FACE,{"disambiguationData":[TD([[makeQuery(id+"F20.imprint","IMPRINT",EDGE,{"derivedFrom":sQuery(id+"F20.wireOp",EDGE,"E52.28.0.19")}),1.0]])]});
            var Q39;
            Q39=makeQuery(id+"F20.imprint","IMPRINT",FACE,{"disambiguationData":[TD([[makeQuery(id+"F20.imprint","IMPRINT",EDGE,{"derivedFrom":sQuery(id+"F20.wireOp",EDGE,"E52.27.0.10")}),1.0]])]});
            var Q40;
            Q40=makeQuery(id+"F20.imprint","IMPRINT",FACE,{"disambiguationData":[TD([[makeQuery(id+"F20.imprint","IMPRINT",EDGE,{"derivedFrom":sQuery(id+"F20.wireOp",EDGE,"E52.26.0.0")}),1.0]])]});
            var Q41;
            Q41=makeQuery(id+"F20.imprint","IMPRINT",FACE,{"disambiguationData":[TD([[makeQuery(id+"F20.imprint","IMPRINT",EDGE,{"derivedFrom":sQuery(id+"F20.wireOp",EDGE,"E52.27.0.15")}),1.0]])]});
            var Q42;
            Q42=makeQuery(id+"F20.imprint","IMPRINT",FACE,{"disambiguationData":[TD([[makeQuery(id+"F20.imprint","IMPRINT",EDGE,{"derivedFrom":sQuery(id+"F20.wireOp",EDGE,"E52.27.0.19")}),1.0]])]});
            var Q43;
            Q43=makeQuery(id+"F20.imprint","IMPRINT",FACE,{"disambiguationData":[TD([[makeQuery(id+"F20.imprint","IMPRINT",EDGE,{"derivedFrom":sQuery(id+"F20.wireOp",EDGE,"E52.26.0.6")}),1.0]])]});
            var Q44;
            Q44=makeQuery(id+"F20.imprint","IMPRINT",FACE,{"disambiguationData":[TD([[makeQuery(id+"F20.imprint","IMPRINT",EDGE,{"derivedFrom":sQuery(id+"F20.wireOp",EDGE,"E52.28.0.26")}),1.0]])]});
            var Q45;
            Q45=makeQuery(id+"F20.imprint","IMPRINT",FACE,{"disambiguationData":[TD([[makeQuery(id+"F20.imprint","IMPRINT",EDGE,{"derivedFrom":sQuery(id+"F20.wireOp",EDGE,"E52.26.0.10")}),1.0]])]});
            var Q46;
            Q46=makeQuery(id+"F20.imprint","IMPRINT",FACE,{"disambiguationData":[TD([[makeQuery(id+"F20.imprint","IMPRINT",EDGE,{"derivedFrom":sQuery(id+"F20.wireOp",EDGE,"E52.25.0.26")}),1.0]])]});
            var Q47;
            Q47=makeQuery(id+"F20.imprint","IMPRINT",FACE,{"disambiguationData":[TD([[makeQuery(id+"F20.imprint","IMPRINT",EDGE,{"derivedFrom":sQuery(id+"F20.wireOp",EDGE,"E52.25.0.0")}),1.0]])]});
            extrude(context, id + "F34", {"entities" : qUnion([Q0, Q1, Q2, Q3, Q4, Q5, Q6, Q7, Q8, Q9, Q10, Q11, Q12, Q13, Q14, Q15, Q16, Q17, Q18, Q19, Q20, Q21, Q22, Q23, Q24, Q25, Q26, Q27, Q28, Q29, Q30, Q31, Q32, Q33, Q34, Q35, Q36, Q37, Q38, Q39, Q40, Q41, Q42, Q43, Q44, Q45, Q46, Q47]), "operationType" : NewBodyOperationType.REMOVE, "endBound" : BoundingType.SYMMETRIC, "oppositeDirection" : true, "depth" : 56 * mm, "offsetDistance" : 25 * mm});
        }
        {
            var Q0;
            Q0=makeQuery(id+"F20.imprint","IMPRINT",FACE,{"disambiguationData":[TD([[makeQuery(id+"F20.imprint","IMPRINT",EDGE,{"derivedFrom":sQuery(id+"F20.wireOp",EDGE,"E52.30.0.14")}),1.0]])]});
            var Q1;
            Q1=makeQuery(id+"F20.imprint","IMPRINT",FACE,{"disambiguationData":[TD([[makeQuery(id+"F20.imprint","IMPRINT",EDGE,{"derivedFrom":sQuery(id+"F20.wireOp",EDGE,"E52.29.0.14")}),1.0]])]});
            var Q2;
            Q2=makeQuery(id+"F20.imprint","IMPRINT",FACE,{"disambiguationData":[TD([[makeQuery(id+"F20.imprint","IMPRINT",EDGE,{"derivedFrom":sQuery(id+"F20.wireOp",EDGE,"E52.32.0.14")}),1.0]])]});
            var Q3;
            Q3=makeQuery(id+"F20.imprint","IMPRINT",FACE,{"disambiguationData":[TD([[makeQuery(id+"F20.imprint","IMPRINT",EDGE,{"derivedFrom":sQuery(id+"F20.wireOp",EDGE,"E52.31.0.14")}),1.0]])]});
            var Q4;
            Q4=makeQuery(id+"F20.imprint","IMPRINT",FACE,{"disambiguationData":[TD([[makeQuery(id+"F20.imprint","IMPRINT",EDGE,{"derivedFrom":sQuery(id+"F20.wireOp",EDGE,"E52.33.0.6")}),1.0]])]});
            var Q5;
            Q5=makeQuery(id+"F20.imprint","IMPRINT",FACE,{"disambiguationData":[TD([[makeQuery(id+"F20.imprint","IMPRINT",EDGE,{"derivedFrom":sQuery(id+"F20.wireOp",EDGE,"E52.31.0.26")}),1.0]])]});
            var Q6;
            Q6=makeQuery(id+"F20.imprint","IMPRINT",FACE,{"disambiguationData":[TD([[makeQuery(id+"F20.imprint","IMPRINT",EDGE,{"derivedFrom":sQuery(id+"F20.wireOp",EDGE,"E52.33.0.4")}),1.0]])]});
            var Q7;
            Q7=makeQuery(id+"F20.imprint","IMPRINT",FACE,{"disambiguationData":[TD([[makeQuery(id+"F20.imprint","IMPRINT",EDGE,{"derivedFrom":sQuery(id+"F20.wireOp",EDGE,"E52.31.0.23")}),1.0]])]});
            var Q8;
            Q8=makeQuery(id+"F20.imprint","IMPRINT",FACE,{"disambiguationData":[TD([[makeQuery(id+"F20.imprint","IMPRINT",EDGE,{"derivedFrom":sQuery(id+"F20.wireOp",EDGE,"E52.33.0.5")}),1.0]])]});
            var Q9;
            Q9=makeQuery(id+"F20.imprint","IMPRINT",FACE,{"disambiguationData":[TD([[makeQuery(id+"F20.imprint","IMPRINT",EDGE,{"derivedFrom":sQuery(id+"F20.wireOp",EDGE,"E52.31.0.25")}),1.0]])]});
            var Q10;
            Q10=makeQuery(id+"F20.imprint","IMPRINT",FACE,{"disambiguationData":[TD([[makeQuery(id+"F20.imprint","IMPRINT",EDGE,{"derivedFrom":sQuery(id+"F20.wireOp",EDGE,"E52.30.0.22")}),1.0]])]});
            var Q11;
            Q11=makeQuery(id+"F20.imprint","IMPRINT",FACE,{"disambiguationData":[TD([[makeQuery(id+"F20.imprint","IMPRINT",EDGE,{"derivedFrom":sQuery(id+"F20.wireOp",EDGE,"E52.32.0.4")}),1.0]])]});
            var Q12;
            Q12=makeQuery(id+"F20.imprint","IMPRINT",FACE,{"disambiguationData":[TD([[makeQuery(id+"F20.imprint","IMPRINT",EDGE,{"derivedFrom":sQuery(id+"F20.wireOp",EDGE,"E52.30.0.23")}),1.0]])]});
            var Q13;
            Q13=makeQuery(id+"F20.imprint","IMPRINT",FACE,{"disambiguationData":[TD([[makeQuery(id+"F20.imprint","IMPRINT",EDGE,{"derivedFrom":sQuery(id+"F20.wireOp",EDGE,"E52.33.0.15")}),1.0]])]});
            var Q14;
            Q14=makeQuery(id+"F20.imprint","IMPRINT",FACE,{"disambiguationData":[TD([[makeQuery(id+"F20.imprint","IMPRINT",EDGE,{"derivedFrom":sQuery(id+"F20.wireOp",EDGE,"E52.32.0.5")}),1.0]])]});
            var Q15;
            Q15=makeQuery(id+"F20.imprint","IMPRINT",FACE,{"disambiguationData":[TD([[makeQuery(id+"F20.imprint","IMPRINT",EDGE,{"derivedFrom":sQuery(id+"F20.wireOp",EDGE,"E52.30.0.25")}),1.0]])]});
            var Q16;
            Q16=makeQuery(id+"F20.imprint","IMPRINT",FACE,{"disambiguationData":[TD([[makeQuery(id+"F20.imprint","IMPRINT",EDGE,{"derivedFrom":sQuery(id+"F20.wireOp",EDGE,"E52.33.0.22")}),1.0]])]});
            var Q17;
            Q17=makeQuery(id+"F20.imprint","IMPRINT",FACE,{"disambiguationData":[TD([[makeQuery(id+"F20.imprint","IMPRINT",EDGE,{"derivedFrom":sQuery(id+"F20.wireOp",EDGE,"E52.32.0.10")}),1.0]])]});
            var Q18;
            Q18=makeQuery(id+"F20.imprint","IMPRINT",FACE,{"disambiguationData":[TD([[makeQuery(id+"F20.imprint","IMPRINT",EDGE,{"derivedFrom":sQuery(id+"F20.wireOp",EDGE,"E52.31.0.0")}),1.0]])]});
            var Q19;
            Q19=makeQuery(id+"F20.imprint","IMPRINT",FACE,{"disambiguationData":[TD([[makeQuery(id+"F20.imprint","IMPRINT",EDGE,{"derivedFrom":sQuery(id+"F20.wireOp",EDGE,"E52.33.0.23")}),1.0]])]});
            var Q20;
            Q20=makeQuery(id+"F20.imprint","IMPRINT",FACE,{"disambiguationData":[TD([[makeQuery(id+"F20.imprint","IMPRINT",EDGE,{"derivedFrom":sQuery(id+"F20.wireOp",EDGE,"E52.31.0.4")}),1.0]])]});
            var Q21;
            Q21=makeQuery(id+"F20.imprint","IMPRINT",FACE,{"disambiguationData":[TD([[makeQuery(id+"F20.imprint","IMPRINT",EDGE,{"derivedFrom":sQuery(id+"F20.wireOp",EDGE,"E52.31.0.5")}),1.0]])]});
            var Q22;
            Q22=makeQuery(id+"F20.imprint","IMPRINT",FACE,{"disambiguationData":[TD([[makeQuery(id+"F20.imprint","IMPRINT",EDGE,{"derivedFrom":sQuery(id+"F20.wireOp",EDGE,"E52.33.0.25")}),1.0]])]});
            var Q23;
            Q23=makeQuery(id+"F20.imprint","IMPRINT",FACE,{"disambiguationData":[TD([[makeQuery(id+"F20.imprint","IMPRINT",EDGE,{"derivedFrom":sQuery(id+"F20.wireOp",EDGE,"E52.32.0.19")}),1.0]])]});
            var Q24;
            Q24=makeQuery(id+"F20.imprint","IMPRINT",FACE,{"disambiguationData":[TD([[makeQuery(id+"F20.imprint","IMPRINT",EDGE,{"derivedFrom":sQuery(id+"F20.wireOp",EDGE,"E52.31.0.6")}),1.0]])]});
            var Q25;
            Q25=makeQuery(id+"F20.imprint","IMPRINT",FACE,{"disambiguationData":[TD([[makeQuery(id+"F20.imprint","IMPRINT",EDGE,{"derivedFrom":sQuery(id+"F20.wireOp",EDGE,"E52.32.0.22")}),1.0]])]});
            var Q26;
            Q26=makeQuery(id+"F20.imprint","IMPRINT",FACE,{"disambiguationData":[TD([[makeQuery(id+"F20.imprint","IMPRINT",EDGE,{"derivedFrom":sQuery(id+"F20.wireOp",EDGE,"E52.32.0.23")}),1.0]])]});
            var Q27;
            Q27=makeQuery(id+"F20.imprint","IMPRINT",FACE,{"disambiguationData":[TD([[makeQuery(id+"F20.imprint","IMPRINT",EDGE,{"derivedFrom":sQuery(id+"F20.wireOp",EDGE,"E52.30.0.4")}),1.0]])]});
            var Q28;
            Q28=makeQuery(id+"F20.imprint","IMPRINT",FACE,{"disambiguationData":[TD([[makeQuery(id+"F20.imprint","IMPRINT",EDGE,{"derivedFrom":sQuery(id+"F20.wireOp",EDGE,"E52.32.0.25")}),1.0]])]});
            var Q29;
            Q29=makeQuery(id+"F20.imprint","IMPRINT",FACE,{"disambiguationData":[TD([[makeQuery(id+"F20.imprint","IMPRINT",EDGE,{"derivedFrom":sQuery(id+"F20.wireOp",EDGE,"E52.31.0.15")}),1.0]])]});
            var Q30;
            Q30=makeQuery(id+"F20.imprint","IMPRINT",FACE,{"disambiguationData":[TD([[makeQuery(id+"F20.imprint","IMPRINT",EDGE,{"derivedFrom":sQuery(id+"F20.wireOp",EDGE,"E52.30.0.5")}),1.0]])]});
            var Q31;
            Q31=makeQuery(id+"F20.imprint","IMPRINT",FACE,{"disambiguationData":[TD([[makeQuery(id+"F20.imprint","IMPRINT",EDGE,{"derivedFrom":sQuery(id+"F20.wireOp",EDGE,"E52.31.0.22")}),1.0]])]});
            var Q32;
            Q32=makeQuery(id+"F20.imprint","IMPRINT",FACE,{"disambiguationData":[TD([[makeQuery(id+"F20.imprint","IMPRINT",EDGE,{"derivedFrom":sQuery(id+"F20.wireOp",EDGE,"E52.30.0.19")}),1.0]])]});
            var Q33;
            Q33=makeQuery(id+"F20.imprint","IMPRINT",FACE,{"disambiguationData":[TD([[makeQuery(id+"F20.imprint","IMPRINT",EDGE,{"derivedFrom":sQuery(id+"F20.wireOp",EDGE,"E52.30.0.15")}),1.0]])]});
            var Q34;
            Q34=makeQuery(id+"F20.imprint","IMPRINT",FACE,{"disambiguationData":[TD([[makeQuery(id+"F20.imprint","IMPRINT",EDGE,{"derivedFrom":sQuery(id+"F20.wireOp",EDGE,"E52.33.0.10")}),1.0]])]});
            var Q35;
            Q35=makeQuery(id+"F20.imprint","IMPRINT",FACE,{"disambiguationData":[TD([[makeQuery(id+"F20.imprint","IMPRINT",EDGE,{"derivedFrom":sQuery(id+"F20.wireOp",EDGE,"E52.32.0.0")}),1.0]])]});
            var Q36;
            Q36=makeQuery(id+"F20.imprint","IMPRINT",FACE,{"disambiguationData":[TD([[makeQuery(id+"F20.imprint","IMPRINT",EDGE,{"derivedFrom":sQuery(id+"F20.wireOp",EDGE,"E52.33.0.19")}),1.0]])]});
            var Q37;
            Q37=makeQuery(id+"F20.imprint","IMPRINT",FACE,{"disambiguationData":[TD([[makeQuery(id+"F20.imprint","IMPRINT",EDGE,{"derivedFrom":sQuery(id+"F20.wireOp",EDGE,"E52.32.0.6")}),1.0]])]});
            var Q38;
            Q38=makeQuery(id+"F20.imprint","IMPRINT",FACE,{"disambiguationData":[TD([[makeQuery(id+"F20.imprint","IMPRINT",EDGE,{"derivedFrom":sQuery(id+"F20.wireOp",EDGE,"E52.30.0.26")}),1.0]])]});
            var Q39;
            Q39=makeQuery(id+"F20.imprint","IMPRINT",FACE,{"disambiguationData":[TD([[makeQuery(id+"F20.imprint","IMPRINT",EDGE,{"derivedFrom":sQuery(id+"F20.wireOp",EDGE,"E52.32.0.15")}),1.0]])]});
            var Q40;
            Q40=makeQuery(id+"F20.imprint","IMPRINT",FACE,{"disambiguationData":[TD([[makeQuery(id+"F20.imprint","IMPRINT",EDGE,{"derivedFrom":sQuery(id+"F20.wireOp",EDGE,"E52.31.0.10")}),1.0]])]});
            var Q41;
            Q41=makeQuery(id+"F20.imprint","IMPRINT",FACE,{"disambiguationData":[TD([[makeQuery(id+"F20.imprint","IMPRINT",EDGE,{"derivedFrom":sQuery(id+"F20.wireOp",EDGE,"E52.30.0.0")}),1.0]])]});
            var Q42;
            Q42=makeQuery(id+"F20.imprint","IMPRINT",FACE,{"disambiguationData":[TD([[makeQuery(id+"F20.imprint","IMPRINT",EDGE,{"derivedFrom":sQuery(id+"F20.wireOp",EDGE,"E52.32.0.26")}),1.0]])]});
            var Q43;
            Q43=makeQuery(id+"F20.imprint","IMPRINT",FACE,{"disambiguationData":[TD([[makeQuery(id+"F20.imprint","IMPRINT",EDGE,{"derivedFrom":sQuery(id+"F20.wireOp",EDGE,"E52.31.0.19")}),1.0]])]});
            var Q44;
            Q44=makeQuery(id+"F20.imprint","IMPRINT",FACE,{"disambiguationData":[TD([[makeQuery(id+"F20.imprint","IMPRINT",EDGE,{"derivedFrom":sQuery(id+"F20.wireOp",EDGE,"E52.30.0.6")}),1.0]])]});
            var Q45;
            Q45=makeQuery(id+"F20.imprint","IMPRINT",FACE,{"disambiguationData":[TD([[makeQuery(id+"F20.imprint","IMPRINT",EDGE,{"derivedFrom":sQuery(id+"F20.wireOp",EDGE,"E52.30.0.10")}),1.0]])]});
            var Q46;
            Q46=makeQuery(id+"F20.imprint","IMPRINT",FACE,{"disambiguationData":[TD([[makeQuery(id+"F20.imprint","IMPRINT",EDGE,{"derivedFrom":sQuery(id+"F20.wireOp",EDGE,"E52.29.0.26")}),1.0]])]});
            var Q47;
            Q47=makeQuery(id+"F20.imprint","IMPRINT",FACE,{"disambiguationData":[TD([[makeQuery(id+"F20.imprint","IMPRINT",EDGE,{"derivedFrom":sQuery(id+"F20.wireOp",EDGE,"E52.29.0.0")}),1.0]])]});
            extrude(context, id + "F35", {"entities" : qUnion([Q0, Q1, Q2, Q3, Q4, Q5, Q6, Q7, Q8, Q9, Q10, Q11, Q12, Q13, Q14, Q15, Q16, Q17, Q18, Q19, Q20, Q21, Q22, Q23, Q24, Q25, Q26, Q27, Q28, Q29, Q30, Q31, Q32, Q33, Q34, Q35, Q36, Q37, Q38, Q39, Q40, Q41, Q42, Q43, Q44, Q45, Q46, Q47]), "operationType" : NewBodyOperationType.REMOVE, "endBound" : BoundingType.SYMMETRIC, "oppositeDirection" : true, "depth" : 50 * mm, "offsetDistance" : 25 * mm});
        }
        {
            var Q0;
            Q0=makeQuery(id+"F20.imprint","IMPRINT",FACE,{"disambiguationData":[TD([[makeQuery(id+"F20.imprint","IMPRINT",EDGE,{"derivedFrom":sQuery(id+"F20.wireOp",EDGE,"E52.34.0.14")}),1.0]])]});
            var Q1;
            Q1=makeQuery(id+"F20.imprint","IMPRINT",FACE,{"disambiguationData":[TD([[makeQuery(id+"F20.imprint","IMPRINT",EDGE,{"derivedFrom":sQuery(id+"F20.wireOp",EDGE,"E52.33.0.14")}),1.0]])]});
            var Q2;
            Q2=makeQuery(id+"F20.imprint","IMPRINT",FACE,{"disambiguationData":[TD([[makeQuery(id+"F20.imprint","IMPRINT",EDGE,{"derivedFrom":sQuery(id+"F20.wireOp",EDGE,"E52.36.0.14")}),1.0]])]});
            var Q3;
            Q3=makeQuery(id+"F20.imprint","IMPRINT",FACE,{"disambiguationData":[TD([[makeQuery(id+"F20.imprint","IMPRINT",EDGE,{"derivedFrom":sQuery(id+"F20.wireOp",EDGE,"E52.35.0.14")}),1.0]])]});
            var Q4;
            Q4=makeQuery(id+"F20.imprint","IMPRINT",FACE,{"disambiguationData":[TD([[makeQuery(id+"F20.imprint","IMPRINT",EDGE,{"derivedFrom":sQuery(id+"F20.wireOp",EDGE,"E52.37.0.4")}),1.0]])]});
            var Q5;
            Q5=makeQuery(id+"F20.imprint","IMPRINT",FACE,{"disambiguationData":[TD([[makeQuery(id+"F20.imprint","IMPRINT",EDGE,{"derivedFrom":sQuery(id+"F20.wireOp",EDGE,"E52.35.0.23")}),1.0]])]});
            var Q6;
            Q6=makeQuery(id+"F20.imprint","IMPRINT",FACE,{"disambiguationData":[TD([[makeQuery(id+"F20.imprint","IMPRINT",EDGE,{"derivedFrom":sQuery(id+"F20.wireOp",EDGE,"E52.37.0.5")}),1.0]])]});
            var Q7;
            Q7=makeQuery(id+"F20.imprint","IMPRINT",FACE,{"disambiguationData":[TD([[makeQuery(id+"F20.imprint","IMPRINT",EDGE,{"derivedFrom":sQuery(id+"F20.wireOp",EDGE,"E52.35.0.25")}),1.0]])]});
            var Q8;
            Q8=makeQuery(id+"F20.imprint","IMPRINT",FACE,{"disambiguationData":[TD([[makeQuery(id+"F20.imprint","IMPRINT",EDGE,{"derivedFrom":sQuery(id+"F20.wireOp",EDGE,"E52.37.0.10")}),1.0]])]});
            var Q9;
            Q9=makeQuery(id+"F20.imprint","IMPRINT",FACE,{"disambiguationData":[TD([[makeQuery(id+"F20.imprint","IMPRINT",EDGE,{"derivedFrom":sQuery(id+"F20.wireOp",EDGE,"E52.36.0.0")}),1.0]])]});
            var Q10;
            Q10=makeQuery(id+"F20.imprint","IMPRINT",FACE,{"disambiguationData":[TD([[makeQuery(id+"F20.imprint","IMPRINT",EDGE,{"derivedFrom":sQuery(id+"F20.wireOp",EDGE,"E52.34.0.22")}),1.0]])]});
            var Q11;
            Q11=makeQuery(id+"F20.imprint","IMPRINT",FACE,{"disambiguationData":[TD([[makeQuery(id+"F20.imprint","IMPRINT",EDGE,{"derivedFrom":sQuery(id+"F20.wireOp",EDGE,"E52.36.0.4")}),1.0]])]});
            var Q12;
            Q12=makeQuery(id+"F20.imprint","IMPRINT",FACE,{"disambiguationData":[TD([[makeQuery(id+"F20.imprint","IMPRINT",EDGE,{"derivedFrom":sQuery(id+"F20.wireOp",EDGE,"E52.34.0.23")}),1.0]])]});
            var Q13;
            Q13=makeQuery(id+"F20.imprint","IMPRINT",FACE,{"disambiguationData":[TD([[makeQuery(id+"F20.imprint","IMPRINT",EDGE,{"derivedFrom":sQuery(id+"F20.wireOp",EDGE,"E52.37.0.15")}),1.0]])]});
            var Q14;
            Q14=makeQuery(id+"F20.imprint","IMPRINT",FACE,{"disambiguationData":[TD([[makeQuery(id+"F20.imprint","IMPRINT",EDGE,{"derivedFrom":sQuery(id+"F20.wireOp",EDGE,"E52.36.0.5")}),1.0]])]});
            var Q15;
            Q15=makeQuery(id+"F20.imprint","IMPRINT",FACE,{"disambiguationData":[TD([[makeQuery(id+"F20.imprint","IMPRINT",EDGE,{"derivedFrom":sQuery(id+"F20.wireOp",EDGE,"E52.34.0.25")}),1.0]])]});
            var Q16;
            Q16=makeQuery(id+"F20.imprint","IMPRINT",FACE,{"disambiguationData":[TD([[makeQuery(id+"F20.imprint","IMPRINT",EDGE,{"derivedFrom":sQuery(id+"F20.wireOp",EDGE,"E52.36.0.6")}),1.0]])]});
            var Q17;
            Q17=makeQuery(id+"F20.imprint","IMPRINT",FACE,{"disambiguationData":[TD([[makeQuery(id+"F20.imprint","IMPRINT",EDGE,{"derivedFrom":sQuery(id+"F20.wireOp",EDGE,"E52.34.0.26")}),1.0]])]});
            var Q18;
            Q18=makeQuery(id+"F20.imprint","IMPRINT",FACE,{"disambiguationData":[TD([[makeQuery(id+"F20.imprint","IMPRINT",EDGE,{"derivedFrom":sQuery(id+"F20.wireOp",EDGE,"E52.37.0.22")}),1.0]])]});
            var Q19;
            Q19=makeQuery(id+"F20.imprint","IMPRINT",FACE,{"disambiguationData":[TD([[makeQuery(id+"F20.imprint","IMPRINT",EDGE,{"derivedFrom":sQuery(id+"F20.wireOp",EDGE,"E52.37.0.23")}),1.0]])]});
            var Q20;
            Q20=makeQuery(id+"F20.imprint","IMPRINT",FACE,{"disambiguationData":[TD([[makeQuery(id+"F20.imprint","IMPRINT",EDGE,{"derivedFrom":sQuery(id+"F20.wireOp",EDGE,"E52.35.0.4")}),1.0]])]});
            var Q21;
            Q21=makeQuery(id+"F20.imprint","IMPRINT",FACE,{"disambiguationData":[TD([[makeQuery(id+"F20.imprint","IMPRINT",EDGE,{"derivedFrom":sQuery(id+"F20.wireOp",EDGE,"E52.35.0.5")}),1.0]])]});
            var Q22;
            Q22=makeQuery(id+"F20.imprint","IMPRINT",FACE,{"disambiguationData":[TD([[makeQuery(id+"F20.imprint","IMPRINT",EDGE,{"derivedFrom":sQuery(id+"F20.wireOp",EDGE,"E52.37.0.25")}),1.0]])]});
            var Q23;
            Q23=makeQuery(id+"F20.imprint","IMPRINT",FACE,{"disambiguationData":[TD([[makeQuery(id+"F20.imprint","IMPRINT",EDGE,{"derivedFrom":sQuery(id+"F20.wireOp",EDGE,"E52.36.0.15")}),1.0]])]});
            var Q24;
            Q24=makeQuery(id+"F20.imprint","IMPRINT",FACE,{"disambiguationData":[TD([[makeQuery(id+"F20.imprint","IMPRINT",EDGE,{"derivedFrom":sQuery(id+"F20.wireOp",EDGE,"E52.34.0.0")}),1.0]])]});
            var Q25;
            Q25=makeQuery(id+"F20.imprint","IMPRINT",FACE,{"disambiguationData":[TD([[makeQuery(id+"F20.imprint","IMPRINT",EDGE,{"derivedFrom":sQuery(id+"F20.wireOp",EDGE,"E52.35.0.10")}),1.0]])]});
            var Q26;
            Q26=makeQuery(id+"F20.imprint","IMPRINT",FACE,{"disambiguationData":[TD([[makeQuery(id+"F20.imprint","IMPRINT",EDGE,{"derivedFrom":sQuery(id+"F20.wireOp",EDGE,"E52.36.0.22")}),1.0]])]});
            var Q27;
            Q27=makeQuery(id+"F20.imprint","IMPRINT",FACE,{"disambiguationData":[TD([[makeQuery(id+"F20.imprint","IMPRINT",EDGE,{"derivedFrom":sQuery(id+"F20.wireOp",EDGE,"E52.34.0.4")}),1.0]])]});
            var Q28;
            Q28=makeQuery(id+"F20.imprint","IMPRINT",FACE,{"disambiguationData":[TD([[makeQuery(id+"F20.imprint","IMPRINT",EDGE,{"derivedFrom":sQuery(id+"F20.wireOp",EDGE,"E52.36.0.23")}),1.0]])]});
            var Q29;
            Q29=makeQuery(id+"F20.imprint","IMPRINT",FACE,{"disambiguationData":[TD([[makeQuery(id+"F20.imprint","IMPRINT",EDGE,{"derivedFrom":sQuery(id+"F20.wireOp",EDGE,"E52.34.0.5")}),1.0]])]});
            var Q30;
            Q30=makeQuery(id+"F20.imprint","IMPRINT",FACE,{"disambiguationData":[TD([[makeQuery(id+"F20.imprint","IMPRINT",EDGE,{"derivedFrom":sQuery(id+"F20.wireOp",EDGE,"E52.36.0.25")}),1.0]])]});
            var Q31;
            Q31=makeQuery(id+"F20.imprint","IMPRINT",FACE,{"disambiguationData":[TD([[makeQuery(id+"F20.imprint","IMPRINT",EDGE,{"derivedFrom":sQuery(id+"F20.wireOp",EDGE,"E52.35.0.19")}),1.0]])]});
            var Q32;
            Q32=makeQuery(id+"F20.imprint","IMPRINT",FACE,{"disambiguationData":[TD([[makeQuery(id+"F20.imprint","IMPRINT",EDGE,{"derivedFrom":sQuery(id+"F20.wireOp",EDGE,"E52.36.0.26")}),1.0]])]});
            var Q33;
            Q33=makeQuery(id+"F20.imprint","IMPRINT",FACE,{"disambiguationData":[TD([[makeQuery(id+"F20.imprint","IMPRINT",EDGE,{"derivedFrom":sQuery(id+"F20.wireOp",EDGE,"E52.34.0.6")}),1.0]])]});
            var Q34;
            Q34=makeQuery(id+"F20.imprint","IMPRINT",FACE,{"disambiguationData":[TD([[makeQuery(id+"F20.imprint","IMPRINT",EDGE,{"derivedFrom":sQuery(id+"F20.wireOp",EDGE,"E52.35.0.22")}),1.0]])]});
            var Q35;
            Q35=makeQuery(id+"F20.imprint","IMPRINT",FACE,{"disambiguationData":[TD([[makeQuery(id+"F20.imprint","IMPRINT",EDGE,{"derivedFrom":sQuery(id+"F20.wireOp",EDGE,"E52.34.0.19")}),1.0]])]});
            var Q36;
            Q36=makeQuery(id+"F20.imprint","IMPRINT",FACE,{"disambiguationData":[TD([[makeQuery(id+"F20.imprint","IMPRINT",EDGE,{"derivedFrom":sQuery(id+"F20.wireOp",EDGE,"E52.37.0.6")}),1.0]])]});
            var Q37;
            Q37=makeQuery(id+"F20.imprint","IMPRINT",FACE,{"disambiguationData":[TD([[makeQuery(id+"F20.imprint","IMPRINT",EDGE,{"derivedFrom":sQuery(id+"F20.wireOp",EDGE,"E52.35.0.26")}),1.0]])]});
            var Q38;
            Q38=makeQuery(id+"F20.imprint","IMPRINT",FACE,{"disambiguationData":[TD([[makeQuery(id+"F20.imprint","IMPRINT",EDGE,{"derivedFrom":sQuery(id+"F20.wireOp",EDGE,"E52.34.0.15")}),1.0]])]});
            var Q39;
            Q39=makeQuery(id+"F20.imprint","IMPRINT",FACE,{"disambiguationData":[TD([[makeQuery(id+"F20.imprint","IMPRINT",EDGE,{"derivedFrom":sQuery(id+"F20.wireOp",EDGE,"E52.37.0.19")}),1.0]])]});
            var Q40;
            Q40=makeQuery(id+"F20.imprint","IMPRINT",FACE,{"disambiguationData":[TD([[makeQuery(id+"F20.imprint","IMPRINT",EDGE,{"derivedFrom":sQuery(id+"F20.wireOp",EDGE,"E52.36.0.10")}),1.0]])]});
            var Q41;
            Q41=makeQuery(id+"F20.imprint","IMPRINT",FACE,{"disambiguationData":[TD([[makeQuery(id+"F20.imprint","IMPRINT",EDGE,{"derivedFrom":sQuery(id+"F20.wireOp",EDGE,"E52.35.0.0")}),1.0]])]});
            var Q42;
            Q42=makeQuery(id+"F20.imprint","IMPRINT",FACE,{"disambiguationData":[TD([[makeQuery(id+"F20.imprint","IMPRINT",EDGE,{"derivedFrom":sQuery(id+"F20.wireOp",EDGE,"E52.35.0.6")}),1.0]])]});
            var Q43;
            Q43=makeQuery(id+"F20.imprint","IMPRINT",FACE,{"disambiguationData":[TD([[makeQuery(id+"F20.imprint","IMPRINT",EDGE,{"derivedFrom":sQuery(id+"F20.wireOp",EDGE,"E52.36.0.19")}),1.0]])]});
            var Q44;
            Q44=makeQuery(id+"F20.imprint","IMPRINT",FACE,{"disambiguationData":[TD([[makeQuery(id+"F20.imprint","IMPRINT",EDGE,{"derivedFrom":sQuery(id+"F20.wireOp",EDGE,"E52.35.0.15")}),1.0]])]});
            var Q45;
            Q45=makeQuery(id+"F20.imprint","IMPRINT",FACE,{"disambiguationData":[TD([[makeQuery(id+"F20.imprint","IMPRINT",EDGE,{"derivedFrom":sQuery(id+"F20.wireOp",EDGE,"E52.34.0.10")}),1.0]])]});
            var Q46;
            Q46=makeQuery(id+"F20.imprint","IMPRINT",FACE,{"disambiguationData":[TD([[makeQuery(id+"F20.imprint","IMPRINT",EDGE,{"derivedFrom":sQuery(id+"F20.wireOp",EDGE,"E52.33.0.26")}),1.0]])]});
            var Q47;
            Q47=makeQuery(id+"F20.imprint","IMPRINT",FACE,{"disambiguationData":[TD([[makeQuery(id+"F20.imprint","IMPRINT",EDGE,{"derivedFrom":sQuery(id+"F20.wireOp",EDGE,"E52.33.0.0")}),1.0]])]});
            extrude(context, id + "F36", {"entities" : qUnion([Q0, Q1, Q2, Q3, Q4, Q5, Q6, Q7, Q8, Q9, Q10, Q11, Q12, Q13, Q14, Q15, Q16, Q17, Q18, Q19, Q20, Q21, Q22, Q23, Q24, Q25, Q26, Q27, Q28, Q29, Q30, Q31, Q32, Q33, Q34, Q35, Q36, Q37, Q38, Q39, Q40, Q41, Q42, Q43, Q44, Q45, Q46, Q47]), "operationType" : NewBodyOperationType.REMOVE, "endBound" : BoundingType.SYMMETRIC, "oppositeDirection" : true, "depth" : 50 * mm, "offsetDistance" : 25 * mm});
        }
        {
            var Q0;
            Q0=makeQuery(id+"F20.imprint","IMPRINT",FACE,{"disambiguationData":[TD([[makeQuery(id+"F20.imprint","IMPRINT",EDGE,{"derivedFrom":sQuery(id+"F20.wireOp",EDGE,"E52.38.0.14")}),1.0]])]});
            var Q1;
            Q1=makeQuery(id+"F20.imprint","IMPRINT",FACE,{"disambiguationData":[TD([[makeQuery(id+"F20.imprint","IMPRINT",EDGE,{"derivedFrom":sQuery(id+"F20.wireOp",EDGE,"E52.37.0.14")}),1.0]])]});
            var Q2;
            Q2=makeQuery(id+"F20.imprint","IMPRINT",FACE,{"disambiguationData":[TD([[makeQuery(id+"F20.imprint","IMPRINT",EDGE,{"derivedFrom":sQuery(id+"F20.wireOp",EDGE,"E52.38.0.23")}),1.0]])]});
            var Q3;
            Q3=makeQuery(id+"F20.imprint","IMPRINT",FACE,{"disambiguationData":[TD([[makeQuery(id+"F20.imprint","IMPRINT",EDGE,{"derivedFrom":sQuery(id+"F20.wireOp",EDGE,"E52.40.0.14")}),1.0]])]});
            var Q4;
            Q4=makeQuery(id+"F20.imprint","IMPRINT",FACE,{"disambiguationData":[TD([[makeQuery(id+"F20.imprint","IMPRINT",EDGE,{"derivedFrom":sQuery(id+"F20.wireOp",EDGE,"E52.39.0.14")}),1.0]])]});
            var Q5;
            Q5=makeQuery(id+"F20.imprint","IMPRINT",FACE,{"disambiguationData":[TD([[makeQuery(id+"F20.imprint","IMPRINT",EDGE,{"derivedFrom":sQuery(id+"F20.wireOp",EDGE,"E52.39.0.26")}),1.0]])]});
            var Q6;
            Q6=makeQuery(id+"F20.imprint","IMPRINT",FACE,{"disambiguationData":[TD([[makeQuery(id+"F20.imprint","IMPRINT",EDGE,{"derivedFrom":sQuery(id+"F20.wireOp",EDGE,"E52.38.0.19")}),1.0]])]});
            var Q7;
            Q7=makeQuery(id+"F20.imprint","IMPRINT",FACE,{"disambiguationData":[TD([[makeQuery(id+"F20.imprint","IMPRINT",EDGE,{"derivedFrom":sQuery(id+"F20.wireOp",EDGE,"E52.41.0.4")}),1.0]])]});
            var Q8;
            Q8=makeQuery(id+"F20.imprint","IMPRINT",FACE,{"disambiguationData":[TD([[makeQuery(id+"F20.imprint","IMPRINT",EDGE,{"derivedFrom":sQuery(id+"F20.wireOp",EDGE,"E52.39.0.23")}),1.0]])]});
            var Q9;
            Q9=makeQuery(id+"F20.imprint","IMPRINT",FACE,{"disambiguationData":[TD([[makeQuery(id+"F20.imprint","IMPRINT",EDGE,{"derivedFrom":sQuery(id+"F20.wireOp",EDGE,"E52.41.0.5")}),1.0]])]});
            var Q10;
            Q10=makeQuery(id+"F20.imprint","IMPRINT",FACE,{"disambiguationData":[TD([[makeQuery(id+"F20.imprint","IMPRINT",EDGE,{"derivedFrom":sQuery(id+"F20.wireOp",EDGE,"E52.39.0.25")}),1.0]])]});
            var Q11;
            Q11=makeQuery(id+"F20.imprint","IMPRINT",FACE,{"disambiguationData":[TD([[makeQuery(id+"F20.imprint","IMPRINT",EDGE,{"derivedFrom":sQuery(id+"F20.wireOp",EDGE,"E52.38.0.15")}),1.0]])]});
            var Q12;
            Q12=makeQuery(id+"F20.imprint","IMPRINT",FACE,{"disambiguationData":[TD([[makeQuery(id+"F20.imprint","IMPRINT",EDGE,{"derivedFrom":sQuery(id+"F20.wireOp",EDGE,"E52.40.0.0")}),1.0]])]});
            var Q13;
            Q13=makeQuery(id+"F20.imprint","IMPRINT",FACE,{"disambiguationData":[TD([[makeQuery(id+"F20.imprint","IMPRINT",EDGE,{"derivedFrom":sQuery(id+"F20.wireOp",EDGE,"E52.38.0.22")}),1.0]])]});
            var Q14;
            Q14=makeQuery(id+"F20.imprint","IMPRINT",FACE,{"disambiguationData":[TD([[makeQuery(id+"F20.imprint","IMPRINT",EDGE,{"derivedFrom":sQuery(id+"F20.wireOp",EDGE,"E52.40.0.4")}),1.0]])]});
            var Q15;
            Q15=makeQuery(id+"F20.imprint","IMPRINT",FACE,{"disambiguationData":[TD([[makeQuery(id+"F20.imprint","IMPRINT",EDGE,{"derivedFrom":sQuery(id+"F20.wireOp",EDGE,"E52.41.0.15")}),1.0]])]});
            var Q16;
            Q16=makeQuery(id+"F20.imprint","IMPRINT",FACE,{"disambiguationData":[TD([[makeQuery(id+"F20.imprint","IMPRINT",EDGE,{"derivedFrom":sQuery(id+"F20.wireOp",EDGE,"E52.40.0.5")}),1.0]])]});
            var Q17;
            Q17=makeQuery(id+"F20.imprint","IMPRINT",FACE,{"disambiguationData":[TD([[makeQuery(id+"F20.imprint","IMPRINT",EDGE,{"derivedFrom":sQuery(id+"F20.wireOp",EDGE,"E52.38.0.25")}),1.0]])]});
            var Q18;
            Q18=makeQuery(id+"F20.imprint","IMPRINT",FACE,{"disambiguationData":[TD([[makeQuery(id+"F20.imprint","IMPRINT",EDGE,{"derivedFrom":sQuery(id+"F20.wireOp",EDGE,"E52.41.0.19")}),1.0]])]});
            var Q19;
            Q19=makeQuery(id+"F20.imprint","IMPRINT",FACE,{"disambiguationData":[TD([[makeQuery(id+"F20.imprint","IMPRINT",EDGE,{"derivedFrom":sQuery(id+"F20.wireOp",EDGE,"E52.40.0.6")}),1.0]])]});
            var Q20;
            Q20=makeQuery(id+"F20.imprint","IMPRINT",FACE,{"disambiguationData":[TD([[makeQuery(id+"F20.imprint","IMPRINT",EDGE,{"derivedFrom":sQuery(id+"F20.wireOp",EDGE,"E52.38.0.26")}),1.0]])]});
            var Q21;
            Q21=makeQuery(id+"F20.imprint","IMPRINT",FACE,{"disambiguationData":[TD([[makeQuery(id+"F20.imprint","IMPRINT",EDGE,{"derivedFrom":sQuery(id+"F20.wireOp",EDGE,"E52.41.0.22")}),1.0]])]});
            var Q22;
            Q22=makeQuery(id+"F20.imprint","IMPRINT",FACE,{"disambiguationData":[TD([[makeQuery(id+"F20.imprint","IMPRINT",EDGE,{"derivedFrom":sQuery(id+"F20.wireOp",EDGE,"E52.40.0.10")}),1.0]])]});
            var Q23;
            Q23=makeQuery(id+"F20.imprint","IMPRINT",FACE,{"disambiguationData":[TD([[makeQuery(id+"F20.imprint","IMPRINT",EDGE,{"derivedFrom":sQuery(id+"F20.wireOp",EDGE,"E52.39.0.0")}),1.0]])]});
            var Q24;
            Q24=makeQuery(id+"F20.imprint","IMPRINT",FACE,{"disambiguationData":[TD([[makeQuery(id+"F20.imprint","IMPRINT",EDGE,{"derivedFrom":sQuery(id+"F20.wireOp",EDGE,"E52.41.0.23")}),1.0]])]});
            var Q25;
            Q25=makeQuery(id+"F20.imprint","IMPRINT",FACE,{"disambiguationData":[TD([[makeQuery(id+"F20.imprint","IMPRINT",EDGE,{"derivedFrom":sQuery(id+"F20.wireOp",EDGE,"E52.39.0.4")}),1.0]])]});
            var Q26;
            Q26=makeQuery(id+"F20.imprint","IMPRINT",FACE,{"disambiguationData":[TD([[makeQuery(id+"F20.imprint","IMPRINT",EDGE,{"derivedFrom":sQuery(id+"F20.wireOp",EDGE,"E52.40.0.15")}),1.0]])]});
            var Q27;
            Q27=makeQuery(id+"F20.imprint","IMPRINT",FACE,{"disambiguationData":[TD([[makeQuery(id+"F20.imprint","IMPRINT",EDGE,{"derivedFrom":sQuery(id+"F20.wireOp",EDGE,"E52.39.0.5")}),1.0]])]});
            var Q28;
            Q28=makeQuery(id+"F20.imprint","IMPRINT",FACE,{"disambiguationData":[TD([[makeQuery(id+"F20.imprint","IMPRINT",EDGE,{"derivedFrom":sQuery(id+"F20.wireOp",EDGE,"E52.41.0.25")}),1.0]])]});
            var Q29;
            Q29=makeQuery(id+"F20.imprint","IMPRINT",FACE,{"disambiguationData":[TD([[makeQuery(id+"F20.imprint","IMPRINT",EDGE,{"derivedFrom":sQuery(id+"F20.wireOp",EDGE,"E52.40.0.19")}),1.0]])]});
            var Q30;
            Q30=makeQuery(id+"F20.imprint","IMPRINT",FACE,{"disambiguationData":[TD([[makeQuery(id+"F20.imprint","IMPRINT",EDGE,{"derivedFrom":sQuery(id+"F20.wireOp",EDGE,"E52.39.0.6")}),1.0]])]});
            var Q31;
            Q31=makeQuery(id+"F20.imprint","IMPRINT",FACE,{"disambiguationData":[TD([[makeQuery(id+"F20.imprint","IMPRINT",EDGE,{"derivedFrom":sQuery(id+"F20.wireOp",EDGE,"E52.40.0.22")}),1.0]])]});
            var Q32;
            Q32=makeQuery(id+"F20.imprint","IMPRINT",FACE,{"disambiguationData":[TD([[makeQuery(id+"F20.imprint","IMPRINT",EDGE,{"derivedFrom":sQuery(id+"F20.wireOp",EDGE,"E52.39.0.10")}),1.0]])]});
            var Q33;
            Q33=makeQuery(id+"F20.imprint","IMPRINT",FACE,{"disambiguationData":[TD([[makeQuery(id+"F20.imprint","IMPRINT",EDGE,{"derivedFrom":sQuery(id+"F20.wireOp",EDGE,"E52.38.0.0")}),1.0]])]});
            var Q34;
            Q34=makeQuery(id+"F20.imprint","IMPRINT",FACE,{"disambiguationData":[TD([[makeQuery(id+"F20.imprint","IMPRINT",EDGE,{"derivedFrom":sQuery(id+"F20.wireOp",EDGE,"E52.40.0.23")}),1.0]])]});
            var Q35;
            Q35=makeQuery(id+"F20.imprint","IMPRINT",FACE,{"disambiguationData":[TD([[makeQuery(id+"F20.imprint","IMPRINT",EDGE,{"derivedFrom":sQuery(id+"F20.wireOp",EDGE,"E52.38.0.4")}),1.0]])]});
            var Q36;
            Q36=makeQuery(id+"F20.imprint","IMPRINT",FACE,{"disambiguationData":[TD([[makeQuery(id+"F20.imprint","IMPRINT",EDGE,{"derivedFrom":sQuery(id+"F20.wireOp",EDGE,"E52.40.0.25")}),1.0]])]});
            var Q37;
            Q37=makeQuery(id+"F20.imprint","IMPRINT",FACE,{"disambiguationData":[TD([[makeQuery(id+"F20.imprint","IMPRINT",EDGE,{"derivedFrom":sQuery(id+"F20.wireOp",EDGE,"E52.39.0.15")}),1.0]])]});
            var Q38;
            Q38=makeQuery(id+"F20.imprint","IMPRINT",FACE,{"disambiguationData":[TD([[makeQuery(id+"F20.imprint","IMPRINT",EDGE,{"derivedFrom":sQuery(id+"F20.wireOp",EDGE,"E52.38.0.5")}),1.0]])]});
            var Q39;
            Q39=makeQuery(id+"F20.imprint","IMPRINT",FACE,{"disambiguationData":[TD([[makeQuery(id+"F20.imprint","IMPRINT",EDGE,{"derivedFrom":sQuery(id+"F20.wireOp",EDGE,"E52.40.0.26")}),1.0]])]});
            var Q40;
            Q40=makeQuery(id+"F20.imprint","IMPRINT",FACE,{"disambiguationData":[TD([[makeQuery(id+"F20.imprint","IMPRINT",EDGE,{"derivedFrom":sQuery(id+"F20.wireOp",EDGE,"E52.39.0.19")}),1.0]])]});
            var Q41;
            Q41=makeQuery(id+"F20.imprint","IMPRINT",FACE,{"disambiguationData":[TD([[makeQuery(id+"F20.imprint","IMPRINT",EDGE,{"derivedFrom":sQuery(id+"F20.wireOp",EDGE,"E52.38.0.6")}),1.0]])]});
            var Q42;
            Q42=makeQuery(id+"F20.imprint","IMPRINT",FACE,{"disambiguationData":[TD([[makeQuery(id+"F20.imprint","IMPRINT",EDGE,{"derivedFrom":sQuery(id+"F20.wireOp",EDGE,"E52.39.0.22")}),1.0]])]});
            var Q43;
            Q43=makeQuery(id+"F20.imprint","IMPRINT",FACE,{"disambiguationData":[TD([[makeQuery(id+"F20.imprint","IMPRINT",EDGE,{"derivedFrom":sQuery(id+"F20.wireOp",EDGE,"E52.38.0.10")}),1.0]])]});
            var Q44;
            Q44=makeQuery(id+"F20.imprint","IMPRINT",FACE,{"disambiguationData":[TD([[makeQuery(id+"F20.imprint","IMPRINT",EDGE,{"derivedFrom":sQuery(id+"F20.wireOp",EDGE,"E52.41.0.6")}),1.0]])]});
            var Q45;
            Q45=makeQuery(id+"F20.imprint","IMPRINT",FACE,{"disambiguationData":[TD([[makeQuery(id+"F20.imprint","IMPRINT",EDGE,{"derivedFrom":sQuery(id+"F20.wireOp",EDGE,"E52.41.0.10")}),1.0]])]});
            var Q46;
            Q46=makeQuery(id+"F20.imprint","IMPRINT",FACE,{"disambiguationData":[TD([[makeQuery(id+"F20.imprint","IMPRINT",EDGE,{"derivedFrom":sQuery(id+"F20.wireOp",EDGE,"E52.37.0.26")}),1.0]])]});
            var Q47;
            Q47=makeQuery(id+"F20.imprint","IMPRINT",FACE,{"disambiguationData":[TD([[makeQuery(id+"F20.imprint","IMPRINT",EDGE,{"derivedFrom":sQuery(id+"F20.wireOp",EDGE,"E52.37.0.0")}),1.0]])]});
            extrude(context, id + "F37", {"entities" : qUnion([Q0, Q1, Q2, Q3, Q4, Q5, Q6, Q7, Q8, Q9, Q10, Q11, Q12, Q13, Q14, Q15, Q16, Q17, Q18, Q19, Q20, Q21, Q22, Q23, Q24, Q25, Q26, Q27, Q28, Q29, Q30, Q31, Q32, Q33, Q34, Q35, Q36, Q37, Q38, Q39, Q40, Q41, Q42, Q43, Q44, Q45, Q46, Q47]), "operationType" : NewBodyOperationType.REMOVE, "endBound" : BoundingType.SYMMETRIC, "depth" : 50 * mm, "offsetDistance" : 25 * mm});
        }
        {
            var Q0;
            Q0=makeQuery(id+"F20.imprint","IMPRINT",FACE,{"disambiguationData":[TD([[makeQuery(id+"F20.imprint","IMPRINT",EDGE,{"derivedFrom":sQuery(id+"F20.wireOp",EDGE,"E52.42.0.14")}),1.0]])]});
            var Q1;
            Q1=makeQuery(id+"F20.imprint","IMPRINT",FACE,{"disambiguationData":[TD([[makeQuery(id+"F20.imprint","IMPRINT",EDGE,{"derivedFrom":sQuery(id+"F20.wireOp",EDGE,"E52.41.0.14")}),1.0]])]});
            var Q2;
            Q2=makeQuery(id+"F20.imprint","IMPRINT",FACE,{"disambiguationData":[TD([[makeQuery(id+"F20.imprint","IMPRINT",EDGE,{"derivedFrom":sQuery(id+"F20.wireOp",EDGE,"E52.44.0.10")}),1.0]])]});
            var Q3;
            Q3=makeQuery(id+"F20.imprint","IMPRINT",FACE,{"disambiguationData":[TD([[makeQuery(id+"F20.imprint","IMPRINT",EDGE,{"derivedFrom":sQuery(id+"F20.wireOp",EDGE,"E52.44.0.14")}),1.0]])]});
            var Q4;
            Q4=makeQuery(id+"F20.imprint","IMPRINT",FACE,{"disambiguationData":[TD([[makeQuery(id+"F20.imprint","IMPRINT",EDGE,{"derivedFrom":sQuery(id+"F20.wireOp",EDGE,"E52.44.0.23")}),1.0]])]});
            var Q5;
            Q5=makeQuery(id+"F20.imprint","IMPRINT",FACE,{"disambiguationData":[TD([[makeQuery(id+"F20.imprint","IMPRINT",EDGE,{"derivedFrom":sQuery(id+"F20.wireOp",EDGE,"E52.43.0.14")}),1.0]])]});
            var Q6;
            Q6=makeQuery(id+"F20.imprint","IMPRINT",FACE,{"disambiguationData":[TD([[makeQuery(id+"F20.imprint","IMPRINT",EDGE,{"derivedFrom":sQuery(id+"F20.wireOp",EDGE,"E52.45.0.6")}),1.0]])]});
            var Q7;
            Q7=makeQuery(id+"F20.imprint","IMPRINT",FACE,{"disambiguationData":[TD([[makeQuery(id+"F20.imprint","IMPRINT",EDGE,{"derivedFrom":sQuery(id+"F20.wireOp",EDGE,"E52.43.0.26")}),1.0]])]});
            var Q8;
            Q8=makeQuery(id+"F20.imprint","IMPRINT",FACE,{"disambiguationData":[TD([[makeQuery(id+"F20.imprint","IMPRINT",EDGE,{"derivedFrom":sQuery(id+"F20.wireOp",EDGE,"E52.45.0.4")}),1.0]])]});
            var Q9;
            Q9=makeQuery(id+"F20.imprint","IMPRINT",FACE,{"disambiguationData":[TD([[makeQuery(id+"F20.imprint","IMPRINT",EDGE,{"derivedFrom":sQuery(id+"F20.wireOp",EDGE,"E52.43.0.23")}),1.0]])]});
            var Q10;
            Q10=makeQuery(id+"F20.imprint","IMPRINT",FACE,{"disambiguationData":[TD([[makeQuery(id+"F20.imprint","IMPRINT",EDGE,{"derivedFrom":sQuery(id+"F20.wireOp",EDGE,"E52.42.0.15")}),1.0]])]});
            var Q11;
            Q11=makeQuery(id+"F20.imprint","IMPRINT",FACE,{"disambiguationData":[TD([[makeQuery(id+"F20.imprint","IMPRINT",EDGE,{"derivedFrom":sQuery(id+"F20.wireOp",EDGE,"E52.45.0.5")}),1.0]])]});
            var Q12;
            Q12=makeQuery(id+"F20.imprint","IMPRINT",FACE,{"disambiguationData":[TD([[makeQuery(id+"F20.imprint","IMPRINT",EDGE,{"derivedFrom":sQuery(id+"F20.wireOp",EDGE,"E52.43.0.25")}),1.0]])]});
            var Q13;
            Q13=makeQuery(id+"F20.imprint","IMPRINT",FACE,{"disambiguationData":[TD([[makeQuery(id+"F20.imprint","IMPRINT",EDGE,{"derivedFrom":sQuery(id+"F20.wireOp",EDGE,"E52.42.0.22")}),1.0]])]});
            var Q14;
            Q14=makeQuery(id+"F20.imprint","IMPRINT",FACE,{"disambiguationData":[TD([[makeQuery(id+"F20.imprint","IMPRINT",EDGE,{"derivedFrom":sQuery(id+"F20.wireOp",EDGE,"E52.45.0.10")}),1.0]])]});
            var Q15;
            Q15=makeQuery(id+"F20.imprint","IMPRINT",FACE,{"disambiguationData":[TD([[makeQuery(id+"F20.imprint","IMPRINT",EDGE,{"derivedFrom":sQuery(id+"F20.wireOp",EDGE,"E52.44.0.0")}),1.0]])]});
            var Q16;
            Q16=makeQuery(id+"F20.imprint","IMPRINT",FACE,{"disambiguationData":[TD([[makeQuery(id+"F20.imprint","IMPRINT",EDGE,{"derivedFrom":sQuery(id+"F20.wireOp",EDGE,"E52.42.0.23")}),1.0]])]});
            var Q17;
            Q17=makeQuery(id+"F20.imprint","IMPRINT",FACE,{"disambiguationData":[TD([[makeQuery(id+"F20.imprint","IMPRINT",EDGE,{"derivedFrom":sQuery(id+"F20.wireOp",EDGE,"E52.44.0.4")}),1.0]])]});
            var Q18;
            Q18=makeQuery(id+"F20.imprint","IMPRINT",FACE,{"disambiguationData":[TD([[makeQuery(id+"F20.imprint","IMPRINT",EDGE,{"derivedFrom":sQuery(id+"F20.wireOp",EDGE,"E52.42.0.25")}),1.0]])]});
            var Q19;
            Q19=makeQuery(id+"F20.imprint","IMPRINT",FACE,{"disambiguationData":[TD([[makeQuery(id+"F20.imprint","IMPRINT",EDGE,{"derivedFrom":sQuery(id+"F20.wireOp",EDGE,"E52.45.0.15")}),1.0]])]});
            var Q20;
            Q20=makeQuery(id+"F20.imprint","IMPRINT",FACE,{"disambiguationData":[TD([[makeQuery(id+"F20.imprint","IMPRINT",EDGE,{"derivedFrom":sQuery(id+"F20.wireOp",EDGE,"E52.44.0.5")}),1.0]])]});
            var Q21;
            Q21=makeQuery(id+"F20.imprint","IMPRINT",FACE,{"disambiguationData":[TD([[makeQuery(id+"F20.imprint","IMPRINT",EDGE,{"derivedFrom":sQuery(id+"F20.wireOp",EDGE,"E52.42.0.26")}),1.0]])]});
            var Q22;
            Q22=makeQuery(id+"F20.imprint","IMPRINT",FACE,{"disambiguationData":[TD([[makeQuery(id+"F20.imprint","IMPRINT",EDGE,{"derivedFrom":sQuery(id+"F20.wireOp",EDGE,"E52.45.0.19")}),1.0]])]});
            var Q23;
            Q23=makeQuery(id+"F20.imprint","IMPRINT",FACE,{"disambiguationData":[TD([[makeQuery(id+"F20.imprint","IMPRINT",EDGE,{"derivedFrom":sQuery(id+"F20.wireOp",EDGE,"E52.44.0.6")}),1.0]])]});
            var Q24;
            Q24=makeQuery(id+"F20.imprint","IMPRINT",FACE,{"disambiguationData":[TD([[makeQuery(id+"F20.imprint","IMPRINT",EDGE,{"derivedFrom":sQuery(id+"F20.wireOp",EDGE,"E52.43.0.0")}),1.0]])]});
            var Q25;
            Q25=makeQuery(id+"F20.imprint","IMPRINT",FACE,{"disambiguationData":[TD([[makeQuery(id+"F20.imprint","IMPRINT",EDGE,{"derivedFrom":sQuery(id+"F20.wireOp",EDGE,"E52.45.0.22")}),1.0]])]});
            var Q26;
            Q26=makeQuery(id+"F20.imprint","IMPRINT",FACE,{"disambiguationData":[TD([[makeQuery(id+"F20.imprint","IMPRINT",EDGE,{"derivedFrom":sQuery(id+"F20.wireOp",EDGE,"E52.43.0.4")}),1.0]])]});
            var Q27;
            Q27=makeQuery(id+"F20.imprint","IMPRINT",FACE,{"disambiguationData":[TD([[makeQuery(id+"F20.imprint","IMPRINT",EDGE,{"derivedFrom":sQuery(id+"F20.wireOp",EDGE,"E52.45.0.23")}),1.0]])]});
            var Q28;
            Q28=makeQuery(id+"F20.imprint","IMPRINT",FACE,{"disambiguationData":[TD([[makeQuery(id+"F20.imprint","IMPRINT",EDGE,{"derivedFrom":sQuery(id+"F20.wireOp",EDGE,"E52.45.0.25")}),1.0]])]});
            var Q29;
            Q29=makeQuery(id+"F20.imprint","IMPRINT",FACE,{"disambiguationData":[TD([[makeQuery(id+"F20.imprint","IMPRINT",EDGE,{"derivedFrom":sQuery(id+"F20.wireOp",EDGE,"E52.44.0.15")}),1.0]])]});
            var Q30;
            Q30=makeQuery(id+"F20.imprint","IMPRINT",FACE,{"disambiguationData":[TD([[makeQuery(id+"F20.imprint","IMPRINT",EDGE,{"derivedFrom":sQuery(id+"F20.wireOp",EDGE,"E52.43.0.5")}),1.0]])]});
            var Q31;
            Q31=makeQuery(id+"F20.imprint","IMPRINT",FACE,{"disambiguationData":[TD([[makeQuery(id+"F20.imprint","IMPRINT",EDGE,{"derivedFrom":sQuery(id+"F20.wireOp",EDGE,"E52.44.0.19")}),1.0]])]});
            var Q32;
            Q32=makeQuery(id+"F20.imprint","IMPRINT",FACE,{"disambiguationData":[TD([[makeQuery(id+"F20.imprint","IMPRINT",EDGE,{"derivedFrom":sQuery(id+"F20.wireOp",EDGE,"E52.43.0.6")}),1.0]])]});
            var Q33;
            Q33=makeQuery(id+"F20.imprint","IMPRINT",FACE,{"disambiguationData":[TD([[makeQuery(id+"F20.imprint","IMPRINT",EDGE,{"derivedFrom":sQuery(id+"F20.wireOp",EDGE,"E52.44.0.22")}),1.0]])]});
            var Q34;
            Q34=makeQuery(id+"F20.imprint","IMPRINT",FACE,{"disambiguationData":[TD([[makeQuery(id+"F20.imprint","IMPRINT",EDGE,{"derivedFrom":sQuery(id+"F20.wireOp",EDGE,"E52.43.0.10")}),1.0]])]});
            var Q35;
            Q35=makeQuery(id+"F20.imprint","IMPRINT",FACE,{"disambiguationData":[TD([[makeQuery(id+"F20.imprint","IMPRINT",EDGE,{"derivedFrom":sQuery(id+"F20.wireOp",EDGE,"E52.42.0.0")}),1.0]])]});
            var Q36;
            Q36=makeQuery(id+"F20.imprint","IMPRINT",FACE,{"disambiguationData":[TD([[makeQuery(id+"F20.imprint","IMPRINT",EDGE,{"derivedFrom":sQuery(id+"F20.wireOp",EDGE,"E52.42.0.4")}),1.0]])]});
            var Q37;
            Q37=makeQuery(id+"F20.imprint","IMPRINT",FACE,{"disambiguationData":[TD([[makeQuery(id+"F20.imprint","IMPRINT",EDGE,{"derivedFrom":sQuery(id+"F20.wireOp",EDGE,"E52.44.0.25")}),1.0]])]});
            var Q38;
            Q38=makeQuery(id+"F20.imprint","IMPRINT",FACE,{"disambiguationData":[TD([[makeQuery(id+"F20.imprint","IMPRINT",EDGE,{"derivedFrom":sQuery(id+"F20.wireOp",EDGE,"E52.43.0.15")}),1.0]])]});
            var Q39;
            Q39=makeQuery(id+"F20.imprint","IMPRINT",FACE,{"disambiguationData":[TD([[makeQuery(id+"F20.imprint","IMPRINT",EDGE,{"derivedFrom":sQuery(id+"F20.wireOp",EDGE,"E52.42.0.5")}),1.0]])]});
            var Q40;
            Q40=makeQuery(id+"F20.imprint","IMPRINT",FACE,{"disambiguationData":[TD([[makeQuery(id+"F20.imprint","IMPRINT",EDGE,{"derivedFrom":sQuery(id+"F20.wireOp",EDGE,"E52.44.0.26")}),1.0]])]});
            var Q41;
            Q41=makeQuery(id+"F20.imprint","IMPRINT",FACE,{"disambiguationData":[TD([[makeQuery(id+"F20.imprint","IMPRINT",EDGE,{"derivedFrom":sQuery(id+"F20.wireOp",EDGE,"E52.43.0.19")}),1.0]])]});
            var Q42;
            Q42=makeQuery(id+"F20.imprint","IMPRINT",FACE,{"disambiguationData":[TD([[makeQuery(id+"F20.imprint","IMPRINT",EDGE,{"derivedFrom":sQuery(id+"F20.wireOp",EDGE,"E52.42.0.6")}),1.0]])]});
            var Q43;
            Q43=makeQuery(id+"F20.imprint","IMPRINT",FACE,{"disambiguationData":[TD([[makeQuery(id+"F20.imprint","IMPRINT",EDGE,{"derivedFrom":sQuery(id+"F20.wireOp",EDGE,"E52.43.0.22")}),1.0]])]});
            var Q44;
            Q44=makeQuery(id+"F20.imprint","IMPRINT",FACE,{"disambiguationData":[TD([[makeQuery(id+"F20.imprint","IMPRINT",EDGE,{"derivedFrom":sQuery(id+"F20.wireOp",EDGE,"E52.42.0.10")}),1.0]])]});
            var Q45;
            Q45=makeQuery(id+"F20.imprint","IMPRINT",FACE,{"disambiguationData":[TD([[makeQuery(id+"F20.imprint","IMPRINT",EDGE,{"derivedFrom":sQuery(id+"F20.wireOp",EDGE,"E52.42.0.19")}),1.0]])]});
            var Q46;
            Q46=makeQuery(id+"F20.imprint","IMPRINT",FACE,{"disambiguationData":[TD([[makeQuery(id+"F20.imprint","IMPRINT",EDGE,{"derivedFrom":sQuery(id+"F20.wireOp",EDGE,"E52.41.0.26")}),1.0]])]});
            var Q47;
            Q47=makeQuery(id+"F20.imprint","IMPRINT",FACE,{"disambiguationData":[TD([[makeQuery(id+"F20.imprint","IMPRINT",EDGE,{"derivedFrom":sQuery(id+"F20.wireOp",EDGE,"E52.41.0.0")}),1.0]])]});
            extrude(context, id + "F38", {"entities" : qUnion([Q0, Q1, Q2, Q3, Q4, Q5, Q6, Q7, Q8, Q9, Q10, Q11, Q12, Q13, Q14, Q15, Q16, Q17, Q18, Q19, Q20, Q21, Q22, Q23, Q24, Q25, Q26, Q27, Q28, Q29, Q30, Q31, Q32, Q33, Q34, Q35, Q36, Q37, Q38, Q39, Q40, Q41, Q42, Q43, Q44, Q45, Q46, Q47]), "operationType" : NewBodyOperationType.REMOVE, "endBound" : BoundingType.SYMMETRIC, "depth" : 50 * mm, "offsetDistance" : 25 * mm});
        }
        {
            var Q0;
            Q0=makeQuery(id+"F20.imprint","IMPRINT",FACE,{"disambiguationData":[TD([[makeQuery(id+"F20.imprint","IMPRINT",EDGE,{"derivedFrom":sQuery(id+"F20.wireOp",EDGE,"E52.47.0.26")}),1.0]])]});
            var Q1;
            Q1=makeQuery(id+"F20.imprint","IMPRINT",FACE,{"disambiguationData":[TD([[makeQuery(id+"F20.imprint","IMPRINT",EDGE,{"derivedFrom":sQuery(id+"F20.wireOp",EDGE,"E52.46.0.19")}),1.0]])]});
            var Q2;
            Q2=makeQuery(id+"F20.imprint","IMPRINT",FACE,{"disambiguationData":[TD([[makeQuery(id+"F20.imprint","IMPRINT",EDGE,{"derivedFrom":sQuery(id+"F20.wireOp",EDGE,"E52.47.0.23")}),1.0]])]});
            var Q3;
            Q3=makeQuery(id+"F20.imprint","IMPRINT",FACE,{"disambiguationData":[TD([[makeQuery(id+"F20.imprint","IMPRINT",EDGE,{"derivedFrom":sQuery(id+"F20.wireOp",EDGE,"E52.46.0.14")}),1.0]])]});
            var Q4;
            Q4=makeQuery(id+"F20.imprint","IMPRINT",FACE,{"disambiguationData":[TD([[makeQuery(id+"F20.imprint","IMPRINT",EDGE,{"derivedFrom":sQuery(id+"F20.wireOp",EDGE,"E52.47.0.25")}),1.0]])]});
            var Q5;
            Q5=makeQuery(id+"F20.imprint","IMPRINT",FACE,{"disambiguationData":[TD([[makeQuery(id+"F20.imprint","IMPRINT",EDGE,{"derivedFrom":sQuery(id+"F20.wireOp",EDGE,"E52.49.0.5")}),1.0]])]});
            var Q6;
            Q6=makeQuery(id+"F20.imprint","IMPRINT",FACE,{"disambiguationData":[TD([[makeQuery(id+"F20.imprint","IMPRINT",EDGE,{"derivedFrom":sQuery(id+"F20.wireOp",EDGE,"E52.48.0.0")}),1.0]])]});
            var Q7;
            Q7=makeQuery(id+"F20.imprint","IMPRINT",FACE,{"disambiguationData":[TD([[makeQuery(id+"F20.imprint","IMPRINT",EDGE,{"derivedFrom":sQuery(id+"F20.wireOp",EDGE,"E52.46.0.22")}),1.0]])]});
            var Q8;
            Q8=makeQuery(id+"F20.imprint","IMPRINT",FACE,{"disambiguationData":[TD([[makeQuery(id+"F20.imprint","IMPRINT",EDGE,{"derivedFrom":sQuery(id+"F20.wireOp",EDGE,"E52.48.0.4")}),1.0]])]});
            var Q9;
            Q9=makeQuery(id+"F20.imprint","IMPRINT",FACE,{"disambiguationData":[TD([[makeQuery(id+"F20.imprint","IMPRINT",EDGE,{"derivedFrom":sQuery(id+"F20.wireOp",EDGE,"E52.45.0.14")}),1.0]])]});
            var Q10;
            Q10=makeQuery(id+"F20.imprint","IMPRINT",FACE,{"disambiguationData":[TD([[makeQuery(id+"F20.imprint","IMPRINT",EDGE,{"derivedFrom":sQuery(id+"F20.wireOp",EDGE,"E52.48.0.5")}),1.0]])]});
            var Q11;
            Q11=makeQuery(id+"F20.imprint","IMPRINT",FACE,{"disambiguationData":[TD([[makeQuery(id+"F20.imprint","IMPRINT",EDGE,{"derivedFrom":sQuery(id+"F20.wireOp",EDGE,"E52.46.0.25")}),1.0]])]});
            var Q12;
            Q12=makeQuery(id+"F20.imprint","IMPRINT",FACE,{"disambiguationData":[TD([[makeQuery(id+"F20.imprint","IMPRINT",EDGE,{"derivedFrom":sQuery(id+"F20.wireOp",EDGE,"E52.46.0.26")}),1.0]])]});
            var Q13;
            Q13=makeQuery(id+"F20.imprint","IMPRINT",FACE,{"disambiguationData":[TD([[makeQuery(id+"F20.imprint","IMPRINT",EDGE,{"derivedFrom":sQuery(id+"F20.wireOp",EDGE,"E52.47.0.0")}),1.0]])]});
            var Q14;
            Q14=makeQuery(id+"F20.imprint","IMPRINT",FACE,{"disambiguationData":[TD([[makeQuery(id+"F20.imprint","IMPRINT",EDGE,{"derivedFrom":sQuery(id+"F20.wireOp",EDGE,"E52.48.0.14")}),1.0]])]});
            var Q15;
            Q15=makeQuery(id+"F20.imprint","IMPRINT",FACE,{"disambiguationData":[TD([[makeQuery(id+"F20.imprint","IMPRINT",EDGE,{"derivedFrom":sQuery(id+"F20.wireOp",EDGE,"E52.47.0.4")}),1.0]])]});
            var Q16;
            Q16=makeQuery(id+"F20.imprint","IMPRINT",FACE,{"disambiguationData":[TD([[makeQuery(id+"F20.imprint","IMPRINT",EDGE,{"derivedFrom":sQuery(id+"F20.wireOp",EDGE,"E52.49.0.23")}),1.0]])]});
            var Q17;
            Q17=makeQuery(id+"F20.imprint","IMPRINT",FACE,{"disambiguationData":[TD([[makeQuery(id+"F20.imprint","IMPRINT",EDGE,{"derivedFrom":sQuery(id+"F20.wireOp",EDGE,"E52.49.0.25")}),1.0]])]});
            var Q18;
            Q18=makeQuery(id+"F20.imprint","IMPRINT",FACE,{"disambiguationData":[TD([[makeQuery(id+"F20.imprint","IMPRINT",EDGE,{"derivedFrom":sQuery(id+"F20.wireOp",EDGE,"E52.48.0.15")}),1.0]])]});
            var Q19;
            Q19=makeQuery(id+"F20.imprint","IMPRINT",FACE,{"disambiguationData":[TD([[makeQuery(id+"F20.imprint","IMPRINT",EDGE,{"derivedFrom":sQuery(id+"F20.wireOp",EDGE,"E52.47.0.5")}),1.0]])]});
            var Q20;
            Q20=makeQuery(id+"F20.imprint","IMPRINT",FACE,{"disambiguationData":[TD([[makeQuery(id+"F20.imprint","IMPRINT",EDGE,{"derivedFrom":sQuery(id+"F20.wireOp",EDGE,"E52.46.0.0")}),1.0]])]});
            var Q21;
            Q21=makeQuery(id+"F20.imprint","IMPRINT",FACE,{"disambiguationData":[TD([[makeQuery(id+"F20.imprint","IMPRINT",EDGE,{"derivedFrom":sQuery(id+"F20.wireOp",EDGE,"E52.46.0.4")}),1.0]])]});
            var Q22;
            Q22=makeQuery(id+"F20.imprint","IMPRINT",FACE,{"disambiguationData":[TD([[makeQuery(id+"F20.imprint","IMPRINT",EDGE,{"derivedFrom":sQuery(id+"F20.wireOp",EDGE,"E52.48.0.23")}),1.0]])]});
            var Q23;
            Q23=makeQuery(id+"F20.imprint","IMPRINT",FACE,{"disambiguationData":[TD([[makeQuery(id+"F20.imprint","IMPRINT",EDGE,{"derivedFrom":sQuery(id+"F20.wireOp",EDGE,"E52.47.0.14")}),1.0]])]});
            var Q24;
            Q24=makeQuery(id+"F20.imprint","IMPRINT",FACE,{"disambiguationData":[TD([[makeQuery(id+"F20.imprint","IMPRINT",EDGE,{"derivedFrom":sQuery(id+"F20.wireOp",EDGE,"E52.46.0.5")}),1.0]])]});
            var Q25;
            Q25=makeQuery(id+"F20.imprint","IMPRINT",FACE,{"disambiguationData":[TD([[makeQuery(id+"F20.imprint","IMPRINT",EDGE,{"derivedFrom":sQuery(id+"F20.wireOp",EDGE,"E52.48.0.25")}),1.0]])]});
            var Q26;
            Q26=makeQuery(id+"F20.imprint","IMPRINT",FACE,{"disambiguationData":[TD([[makeQuery(id+"F20.imprint","IMPRINT",EDGE,{"derivedFrom":sQuery(id+"F20.wireOp",EDGE,"E52.48.0.26")}),1.0]])]});
            var Q27;
            Q27=makeQuery(id+"F20.imprint","IMPRINT",FACE,{"disambiguationData":[TD([[makeQuery(id+"F20.imprint","IMPRINT",EDGE,{"derivedFrom":sQuery(id+"F20.wireOp",EDGE,"E52.47.0.22")}),1.0]])]});
            var Q28;
            Q28=makeQuery(id+"F20.imprint","IMPRINT",FACE,{"disambiguationData":[TD([[makeQuery(id+"F20.imprint","IMPRINT",EDGE,{"derivedFrom":sQuery(id+"F20.wireOp",EDGE,"E52.49.0.6")}),1.0]])]});
            var Q29;
            Q29=makeQuery(id+"F20.imprint","IMPRINT",FACE,{"disambiguationData":[TD([[makeQuery(id+"F20.imprint","IMPRINT",EDGE,{"derivedFrom":sQuery(id+"F20.wireOp",EDGE,"E52.49.0.4")}),1.0]])]});
            var Q30;
            Q30=makeQuery(id+"F20.imprint","IMPRINT",FACE,{"disambiguationData":[TD([[makeQuery(id+"F20.imprint","IMPRINT",EDGE,{"derivedFrom":sQuery(id+"F20.wireOp",EDGE,"E52.46.0.15")}),1.0]])]});
            var Q31;
            Q31=makeQuery(id+"F20.imprint","IMPRINT",FACE,{"disambiguationData":[TD([[makeQuery(id+"F20.imprint","IMPRINT",EDGE,{"derivedFrom":sQuery(id+"F20.wireOp",EDGE,"E52.49.0.10")}),1.0]])]});
            var Q32;
            Q32=makeQuery(id+"F20.imprint","IMPRINT",FACE,{"disambiguationData":[TD([[makeQuery(id+"F20.imprint","IMPRINT",EDGE,{"derivedFrom":sQuery(id+"F20.wireOp",EDGE,"E52.46.0.23")}),1.0]])]});
            var Q33;
            Q33=makeQuery(id+"F20.imprint","IMPRINT",FACE,{"disambiguationData":[TD([[makeQuery(id+"F20.imprint","IMPRINT",EDGE,{"derivedFrom":sQuery(id+"F20.wireOp",EDGE,"E52.49.0.15")}),1.0]])]});
            var Q34;
            Q34=makeQuery(id+"F20.imprint","IMPRINT",FACE,{"disambiguationData":[TD([[makeQuery(id+"F20.imprint","IMPRINT",EDGE,{"derivedFrom":sQuery(id+"F20.wireOp",EDGE,"E52.48.0.6")}),1.0]])]});
            var Q35;
            Q35=makeQuery(id+"F20.imprint","IMPRINT",FACE,{"disambiguationData":[TD([[makeQuery(id+"F20.imprint","IMPRINT",EDGE,{"derivedFrom":sQuery(id+"F20.wireOp",EDGE,"E52.49.0.19")}),1.0]])]});
            var Q36;
            Q36=makeQuery(id+"F20.imprint","IMPRINT",FACE,{"disambiguationData":[TD([[makeQuery(id+"F20.imprint","IMPRINT",EDGE,{"derivedFrom":sQuery(id+"F20.wireOp",EDGE,"E52.48.0.10")}),1.0]])]});
            var Q37;
            Q37=makeQuery(id+"F20.imprint","IMPRINT",FACE,{"disambiguationData":[TD([[makeQuery(id+"F20.imprint","IMPRINT",EDGE,{"derivedFrom":sQuery(id+"F20.wireOp",EDGE,"E52.49.0.22")}),1.0]])]});
            var Q38;
            Q38=makeQuery(id+"F20.imprint","IMPRINT",FACE,{"disambiguationData":[TD([[makeQuery(id+"F20.imprint","IMPRINT",EDGE,{"derivedFrom":sQuery(id+"F20.wireOp",EDGE,"E52.45.0.26")}),1.0]])]});
            var Q39;
            Q39=makeQuery(id+"F20.imprint","IMPRINT",FACE,{"disambiguationData":[TD([[makeQuery(id+"F20.imprint","IMPRINT",EDGE,{"derivedFrom":sQuery(id+"F20.wireOp",EDGE,"E52.48.0.19")}),1.0]])]});
            var Q40;
            Q40=makeQuery(id+"F20.imprint","IMPRINT",FACE,{"disambiguationData":[TD([[makeQuery(id+"F20.imprint","IMPRINT",EDGE,{"derivedFrom":sQuery(id+"F20.wireOp",EDGE,"E52.47.0.6")}),1.0]])]});
            var Q41;
            Q41=makeQuery(id+"F20.imprint","IMPRINT",FACE,{"disambiguationData":[TD([[makeQuery(id+"F20.imprint","IMPRINT",EDGE,{"derivedFrom":sQuery(id+"F20.wireOp",EDGE,"E52.48.0.22")}),1.0]])]});
            var Q42;
            Q42=makeQuery(id+"F20.imprint","IMPRINT",FACE,{"disambiguationData":[TD([[makeQuery(id+"F20.imprint","IMPRINT",EDGE,{"derivedFrom":sQuery(id+"F20.wireOp",EDGE,"E52.47.0.10")}),1.0]])]});
            var Q43;
            Q43=makeQuery(id+"F20.imprint","IMPRINT",FACE,{"disambiguationData":[TD([[makeQuery(id+"F20.imprint","IMPRINT",EDGE,{"derivedFrom":sQuery(id+"F20.wireOp",EDGE,"E52.47.0.15")}),1.0]])]});
            var Q44;
            Q44=makeQuery(id+"F20.imprint","IMPRINT",FACE,{"disambiguationData":[TD([[makeQuery(id+"F20.imprint","IMPRINT",EDGE,{"derivedFrom":sQuery(id+"F20.wireOp",EDGE,"E52.46.0.6")}),1.0]])]});
            var Q45;
            Q45=makeQuery(id+"F20.imprint","IMPRINT",FACE,{"disambiguationData":[TD([[makeQuery(id+"F20.imprint","IMPRINT",EDGE,{"derivedFrom":sQuery(id+"F20.wireOp",EDGE,"E52.47.0.19")}),1.0]])]});
            var Q46;
            Q46=makeQuery(id+"F20.imprint","IMPRINT",FACE,{"disambiguationData":[TD([[makeQuery(id+"F20.imprint","IMPRINT",EDGE,{"derivedFrom":sQuery(id+"F20.wireOp",EDGE,"E52.46.0.10")}),1.0]])]});
            var Q47;
            Q47=makeQuery(id+"F20.imprint","IMPRINT",FACE,{"disambiguationData":[TD([[makeQuery(id+"F20.imprint","IMPRINT",EDGE,{"derivedFrom":sQuery(id+"F20.wireOp",EDGE,"E52.45.0.0")}),1.0]])]});
            extrude(context, id + "F39", {"entities" : qUnion([Q0, Q1, Q2, Q3, Q4, Q5, Q6, Q7, Q8, Q9, Q10, Q11, Q12, Q13, Q14, Q15, Q16, Q17, Q18, Q19, Q20, Q21, Q22, Q23, Q24, Q25, Q26, Q27, Q28, Q29, Q30, Q31, Q32, Q33, Q34, Q35, Q36, Q37, Q38, Q39, Q40, Q41, Q42, Q43, Q44, Q45, Q46, Q47]), "operationType" : NewBodyOperationType.REMOVE, "endBound" : BoundingType.SYMMETRIC, "depth" : 50 * mm, "offsetDistance" : 25 * mm});
        }
        {
            var Q0;
            Q0=qCreatedBy(makeId("Top.planeOp"),FACE);
            var sketch = newSketch(context, id + "F40", { "sketchPlane" : qUnion([Q0]) });
            skPoint(sketch, "E53.0", {"position": v(0, 24) * mm});
            skPoint(sketch, "E54.0", {"position": v(0, -24) * mm});
            skLineSegment(sketch, "E55", {"start": v(0, 24) * mm, "end": v(24, 0) * mm, "construction": true});
            skLineSegment(sketch, "E56", {"start": v(24, 0) * mm, "end": v(0, -24) * mm, "construction": true});
            skCircle(sketch, "E57", {"center": v(8, 16) * mm, "radius": 2 * mm});
            skArc(sketch, "E58", {"start": v(16.93, 9.9) * mm, "mid": v(14.1, 9.9) * mm, "end": v(14.1, 7.07) * mm});
            skArc(sketch, "E59", {"start": v(14.59, 6.59) * mm, "mid": v(17.41, 6.59) * mm, "end": v(17.41, 9.41) * mm});
            skCircle(sketch, "E60", {"center": v(8, -16) * mm, "radius": 2 * mm});
            skArc(sketch, "E61", {"start": v(17.41, -9.41) * mm, "mid": v(17.41, -6.59) * mm, "end": v(14.59, -6.59) * mm});
            skArc(sketch, "E62", {"start": v(14.1, -7.07) * mm, "mid": v(14.1, -9.9) * mm, "end": v(16.93, -9.9) * mm});
            skLineSegment(sketch, "E63", {"start": v(14.1, -7.07) * mm, "end": v(16.93, -9.9) * mm, "construction": true});
            skLineSegment(sketch, "E64", {"start": v(14.59, -6.59) * mm, "end": v(17.41, -9.41) * mm, "construction": true});
            skLineSegment(sketch, "E65", {"start": v(14.1, -7.07) * mm, "end": v(14.59, -6.59) * mm});
            skLineSegment(sketch, "E66", {"start": v(16.93, -9.9) * mm, "end": v(17.41, -9.41) * mm});
            skLineSegment(sketch, "E67", {"start": v(16.93, 9.9) * mm, "end": v(14.1, 7.07) * mm, "construction": true});
            skLineSegment(sketch, "E68", {"start": v(14.59, 6.59) * mm, "end": v(17.41, 9.41) * mm, "construction": true});
            skLineSegment(sketch, "E69", {"start": v(14.1, 7.07) * mm, "end": v(14.59, 6.59) * mm});
            skLineSegment(sketch, "E70", {"start": v(16.93, 9.9) * mm, "end": v(17.41, 9.41) * mm});
            skLineSegment(sketch, "E71", {"start": v(8, 16) * mm, "end": v(16, 16) * mm, "construction": true});
            skLineSegment(sketch, "E72", {"start": v(8, -16) * mm, "end": v(16, -16) * mm, "construction": true});
            skCircle(sketch, "E73", {"center": v(16, -16) * mm, "radius": 2 * mm});
            skCircle(sketch, "E74", {"center": v(12, 0) * mm, "radius": 2 * mm});
            skCircle(sketch, "E75", {"center": v(16, 16) * mm, "radius": 2 * mm});
            skLineSegment(sketch, "E76.bottom", {"start": v(0, 24) * mm, "end": v(24, 24) * mm, "construction": true});
            skLineSegment(sketch, "E76.top", {"start": v(0, 0) * mm, "end": v(24, 0) * mm, "construction": true});
            skLineSegment(sketch, "E76.left", {"start": v(0, 24) * mm, "end": v(0, 0) * mm, "construction": true});
            skLineSegment(sketch, "E76.right", {"start": v(24, 24) * mm, "end": v(24, 0) * mm, "construction": true});
            skLineSegment(sketch, "E77.bottom", {"start": v(24, 0) * mm, "end": v(0, 0) * mm, "construction": true});
            skLineSegment(sketch, "E77.top", {"start": v(24, -24) * mm, "end": v(0, -24) * mm, "construction": true});
            skLineSegment(sketch, "E77.left", {"start": v(24, 0) * mm, "end": v(24, -24) * mm, "construction": true});
            skLineSegment(sketch, "E77.right", {"start": v(0, 0) * mm, "end": v(0, -24) * mm, "construction": true});
            skLineSegment(sketch, "E78", {"start": v(24, 24) * mm, "end": v(0, 0) * mm, "construction": true});
            skLineSegment(sketch, "E79", {"start": v(24, -24) * mm, "end": v(0, 0) * mm, "construction": true});
            skArc(sketch, "E80", {"start": v(7.07, -9.9) * mm, "mid": v(9.9, -9.9) * mm, "end": v(9.9, -7.07) * mm});
            skArc(sketch, "E81", {"start": v(9.9, 7.07) * mm, "mid": v(9.9, 9.9) * mm, "end": v(7.07, 9.9) * mm});
            skArc(sketch, "E82", {"start": v(6.59, 9.41) * mm, "mid": v(6.59, 6.59) * mm, "end": v(9.41, 6.59) * mm});
            skLineSegment(sketch, "E83", {"start": v(7.07, 9.9) * mm, "end": v(9.9, 7.07) * mm, "construction": true});
            skLineSegment(sketch, "E84", {"start": v(6.59, 9.41) * mm, "end": v(9.41, 6.59) * mm, "construction": true});
            skLineSegment(sketch, "E85", {"start": v(7.07, -9.9) * mm, "end": v(9.9, -7.07) * mm, "construction": true});
            skLineSegment(sketch, "E86", {"start": v(9.41, -6.59) * mm, "end": v(6.59, -9.41) * mm, "construction": true});
            skLineSegment(sketch, "E87", {"start": v(9.41, -6.59) * mm, "end": v(9.9, -7.07) * mm});
            skLineSegment(sketch, "E88", {"start": v(6.59, -9.41) * mm, "end": v(7.07, -9.9) * mm});
            skLineSegment(sketch, "E89", {"start": v(6.59, 9.41) * mm, "end": v(7.07, 9.9) * mm});
            skLineSegment(sketch, "E90", {"start": v(9.41, 6.59) * mm, "end": v(9.9, 7.07) * mm});
            skArc(sketch, "E91.trimOffspring", {"start": v(9.41, -6.59) * mm, "mid": v(6.59, -6.59) * mm, "end": v(6.59, -9.41) * mm});
            skArc(sketch, "E92.1.0.0", {"start": v(30.59, 9.41) * mm, "mid": v(30.59, 6.59) * mm, "end": v(33.41, 6.59) * mm});
            skArc(sketch, "E92.1.0.1", {"start": v(33.41, -6.59) * mm, "mid": v(30.59, -6.59) * mm, "end": v(30.59, -9.41) * mm});
            skLineSegment(sketch, "E92.1.0.2", {"start": v(24, 24) * mm, "end": v(48, 24) * mm, "construction": true});
            skLineSegment(sketch, "E92.1.0.3", {"start": v(32, 16) * mm, "end": v(40, 16) * mm, "construction": true});
            skArc(sketch, "E92.1.0.4", {"start": v(31.07, -9.9) * mm, "mid": v(33.9, -9.9) * mm, "end": v(33.9, -7.07) * mm});
            skLineSegment(sketch, "E92.1.0.5", {"start": v(48, 0) * mm, "end": v(24, -24) * mm, "construction": true});
            skCircle(sketch, "E92.1.0.6", {"center": v(40, -16) * mm, "radius": 2 * mm});
            skLineSegment(sketch, "E92.1.0.7", {"start": v(48, -24) * mm, "end": v(24, -24) * mm, "construction": true});
            skCircle(sketch, "E92.1.0.8", {"center": v(32, 16) * mm, "radius": 2 * mm});
            skCircle(sketch, "E92.1.0.9", {"center": v(40, 16) * mm, "radius": 2 * mm});
            skLineSegment(sketch, "E92.1.0.10", {"start": v(48, -24) * mm, "end": v(24, 0) * mm, "construction": true});
            skLineSegment(sketch, "E92.1.0.11", {"start": v(24, 24) * mm, "end": v(48, 0) * mm, "construction": true});
            skLineSegment(sketch, "E92.1.0.12", {"start": v(48, 24) * mm, "end": v(24, 0) * mm, "construction": true});
            skArc(sketch, "E92.1.0.13", {"start": v(40.93, 9.9) * mm, "mid": v(38.1, 9.9) * mm, "end": v(38.1, 7.07) * mm});
            skArc(sketch, "E92.1.0.14", {"start": v(33.9, 7.07) * mm, "mid": v(33.9, 9.9) * mm, "end": v(31.07, 9.9) * mm});
            skArc(sketch, "E92.1.0.15", {"start": v(38.1, -7.07) * mm, "mid": v(38.1, -9.9) * mm, "end": v(40.93, -9.9) * mm});
            skArc(sketch, "E92.1.0.16", {"start": v(38.59, 6.59) * mm, "mid": v(41.41, 6.59) * mm, "end": v(41.41, 9.41) * mm});
            skLineSegment(sketch, "E92.1.0.17", {"start": v(32, -16) * mm, "end": v(40, -16) * mm, "construction": true});
            skLineSegment(sketch, "E92.1.0.18", {"start": v(24, 0) * mm, "end": v(48, 0) * mm, "construction": true});
            skArc(sketch, "E92.1.0.19", {"start": v(41.41, -9.41) * mm, "mid": v(41.41, -6.59) * mm, "end": v(38.59, -6.59) * mm});
            skCircle(sketch, "E92.1.0.20", {"center": v(32, -16) * mm, "radius": 2 * mm});
            skCircle(sketch, "E92.1.0.21", {"center": v(36, 0) * mm, "radius": 2 * mm});
            skPoint(sketch, "E92.1.0.22", {"position": v(32, -8) * mm});
            skLineSegment(sketch, "E92.1.0.23", {"start": v(48, 0) * mm, "end": v(24, 0) * mm, "construction": true});
            skLineSegment(sketch, "E92.1.0.24", {"start": v(38.59, 6.59) * mm, "end": v(41.41, 9.41) * mm, "construction": true});
            skLineSegment(sketch, "E92.1.0.25", {"start": v(38.1, -7.07) * mm, "end": v(40.93, -9.9) * mm, "construction": true});
            skLineSegment(sketch, "E92.1.0.26", {"start": v(30.59, 9.41) * mm, "end": v(33.41, 6.59) * mm, "construction": true});
            skLineSegment(sketch, "E92.1.0.27", {"start": v(31.07, 9.9) * mm, "end": v(33.9, 7.07) * mm, "construction": true});
            skLineSegment(sketch, "E92.1.0.28", {"start": v(40.93, 9.9) * mm, "end": v(38.1, 7.07) * mm, "construction": true});
            skLineSegment(sketch, "E92.1.0.29", {"start": v(38.59, -6.59) * mm, "end": v(41.41, -9.41) * mm, "construction": true});
            skLineSegment(sketch, "E92.1.0.30", {"start": v(31.07, -9.9) * mm, "end": v(33.9, -7.07) * mm, "construction": true});
            skLineSegment(sketch, "E92.1.0.31", {"start": v(33.41, -6.59) * mm, "end": v(30.59, -9.41) * mm, "construction": true});
            skLineSegment(sketch, "E92.1.0.32", {"start": v(38.1, -7.07) * mm, "end": v(38.59, -6.59) * mm});
            skLineSegment(sketch, "E92.1.0.33", {"start": v(30.59, 9.41) * mm, "end": v(31.07, 9.9) * mm});
            skLineSegment(sketch, "E92.1.0.34", {"start": v(30.59, -9.41) * mm, "end": v(31.07, -9.9) * mm});
            skLineSegment(sketch, "E92.1.0.35", {"start": v(40.93, -9.9) * mm, "end": v(41.41, -9.41) * mm});
            skLineSegment(sketch, "E92.1.0.36", {"start": v(33.41, 6.59) * mm, "end": v(33.9, 7.07) * mm});
            skLineSegment(sketch, "E92.1.0.37", {"start": v(40.93, 9.9) * mm, "end": v(41.41, 9.41) * mm});
            skLineSegment(sketch, "E92.1.0.38", {"start": v(38.1, 7.07) * mm, "end": v(38.59, 6.59) * mm});
            skLineSegment(sketch, "E92.1.0.39", {"start": v(33.41, -6.59) * mm, "end": v(33.9, -7.07) * mm});
            skArc(sketch, "E92.2.0.0", {"start": v(54.59, 9.41) * mm, "mid": v(54.59, 6.59) * mm, "end": v(57.41, 6.59) * mm});
            skArc(sketch, "E92.2.0.1", {"start": v(57.41, -6.59) * mm, "mid": v(54.59, -6.59) * mm, "end": v(54.59, -9.41) * mm});
            skLineSegment(sketch, "E92.2.0.2", {"start": v(48, 24) * mm, "end": v(72, 24) * mm, "construction": true});
            skLineSegment(sketch, "E92.2.0.3", {"start": v(56, 16) * mm, "end": v(64, 16) * mm, "construction": true});
            skArc(sketch, "E92.2.0.4", {"start": v(55.07, -9.9) * mm, "mid": v(57.9, -9.9) * mm, "end": v(57.9, -7.07) * mm});
            skLineSegment(sketch, "E92.2.0.5", {"start": v(72, 0) * mm, "end": v(48, -24) * mm, "construction": true});
            skCircle(sketch, "E92.2.0.6", {"center": v(64, -16) * mm, "radius": 2 * mm});
            skLineSegment(sketch, "E92.2.0.7", {"start": v(72, -24) * mm, "end": v(48, -24) * mm, "construction": true});
            skCircle(sketch, "E92.2.0.8", {"center": v(56, 16) * mm, "radius": 2 * mm});
            skCircle(sketch, "E92.2.0.9", {"center": v(64, 16) * mm, "radius": 2 * mm});
            skLineSegment(sketch, "E92.2.0.10", {"start": v(72, -24) * mm, "end": v(48, 0) * mm, "construction": true});
            skLineSegment(sketch, "E92.2.0.11", {"start": v(48, 24) * mm, "end": v(72, 0) * mm, "construction": true});
            skLineSegment(sketch, "E92.2.0.12", {"start": v(72, 24) * mm, "end": v(48, 0) * mm, "construction": true});
            skArc(sketch, "E92.2.0.13", {"start": v(64.93, 9.9) * mm, "mid": v(62.1, 9.9) * mm, "end": v(62.1, 7.07) * mm});
            skArc(sketch, "E92.2.0.14", {"start": v(57.9, 7.07) * mm, "mid": v(57.9, 9.9) * mm, "end": v(55.07, 9.9) * mm});
            skArc(sketch, "E92.2.0.15", {"start": v(62.1, -7.07) * mm, "mid": v(62.1, -9.9) * mm, "end": v(64.93, -9.9) * mm});
            skArc(sketch, "E92.2.0.16", {"start": v(62.59, 6.59) * mm, "mid": v(65.41, 6.59) * mm, "end": v(65.41, 9.41) * mm});
            skLineSegment(sketch, "E92.2.0.17", {"start": v(56, -16) * mm, "end": v(64, -16) * mm, "construction": true});
            skLineSegment(sketch, "E92.2.0.18", {"start": v(48, 0) * mm, "end": v(72, 0) * mm, "construction": true});
            skArc(sketch, "E92.2.0.19", {"start": v(65.41, -9.41) * mm, "mid": v(65.41, -6.59) * mm, "end": v(62.59, -6.59) * mm});
            skCircle(sketch, "E92.2.0.20", {"center": v(56, -16) * mm, "radius": 2 * mm});
            skCircle(sketch, "E92.2.0.21", {"center": v(60, 0) * mm, "radius": 2 * mm});
            skPoint(sketch, "E92.2.0.22", {"position": v(56, -8) * mm});
            skLineSegment(sketch, "E92.2.0.23", {"start": v(72, 0) * mm, "end": v(48, 0) * mm, "construction": true});
            skLineSegment(sketch, "E92.2.0.24", {"start": v(62.59, 6.59) * mm, "end": v(65.41, 9.41) * mm, "construction": true});
            skLineSegment(sketch, "E92.2.0.25", {"start": v(62.1, -7.07) * mm, "end": v(64.93, -9.9) * mm, "construction": true});
            skLineSegment(sketch, "E92.2.0.26", {"start": v(54.59, 9.41) * mm, "end": v(57.41, 6.59) * mm, "construction": true});
            skLineSegment(sketch, "E92.2.0.27", {"start": v(55.07, 9.9) * mm, "end": v(57.9, 7.07) * mm, "construction": true});
            skLineSegment(sketch, "E92.2.0.28", {"start": v(64.93, 9.9) * mm, "end": v(62.1, 7.07) * mm, "construction": true});
            skLineSegment(sketch, "E92.2.0.29", {"start": v(62.59, -6.59) * mm, "end": v(65.41, -9.41) * mm, "construction": true});
            skLineSegment(sketch, "E92.2.0.30", {"start": v(55.07, -9.9) * mm, "end": v(57.9, -7.07) * mm, "construction": true});
            skLineSegment(sketch, "E92.2.0.31", {"start": v(57.41, -6.59) * mm, "end": v(54.59, -9.41) * mm, "construction": true});
            skLineSegment(sketch, "E92.2.0.32", {"start": v(62.1, -7.07) * mm, "end": v(62.59, -6.59) * mm});
            skLineSegment(sketch, "E92.2.0.33", {"start": v(54.59, 9.41) * mm, "end": v(55.07, 9.9) * mm});
            skLineSegment(sketch, "E92.2.0.34", {"start": v(54.59, -9.41) * mm, "end": v(55.07, -9.9) * mm});
            skLineSegment(sketch, "E92.2.0.35", {"start": v(64.93, -9.9) * mm, "end": v(65.41, -9.41) * mm});
            skLineSegment(sketch, "E92.2.0.36", {"start": v(57.41, 6.59) * mm, "end": v(57.9, 7.07) * mm});
            skLineSegment(sketch, "E92.2.0.37", {"start": v(64.93, 9.9) * mm, "end": v(65.41, 9.41) * mm});
            skLineSegment(sketch, "E92.2.0.38", {"start": v(62.1, 7.07) * mm, "end": v(62.59, 6.59) * mm});
            skLineSegment(sketch, "E92.2.0.39", {"start": v(57.41, -6.59) * mm, "end": v(57.9, -7.07) * mm});
            skArc(sketch, "E92.3.0.0", {"start": v(78.59, 9.41) * mm, "mid": v(78.59, 6.59) * mm, "end": v(81.41, 6.59) * mm});
            skArc(sketch, "E92.3.0.1", {"start": v(81.41, -6.59) * mm, "mid": v(78.59, -6.59) * mm, "end": v(78.59, -9.41) * mm});
            skLineSegment(sketch, "E92.3.0.2", {"start": v(72, 24) * mm, "end": v(96, 24) * mm, "construction": true});
            skLineSegment(sketch, "E92.3.0.3", {"start": v(80, 16) * mm, "end": v(88, 16) * mm, "construction": true});
            skArc(sketch, "E92.3.0.4", {"start": v(79.07, -9.9) * mm, "mid": v(81.9, -9.9) * mm, "end": v(81.9, -7.07) * mm});
            skLineSegment(sketch, "E92.3.0.5", {"start": v(96, 0) * mm, "end": v(72, -24) * mm, "construction": true});
            skCircle(sketch, "E92.3.0.6", {"center": v(88, -16) * mm, "radius": 2 * mm});
            skLineSegment(sketch, "E92.3.0.7", {"start": v(96, -24) * mm, "end": v(72, -24) * mm, "construction": true});
            skCircle(sketch, "E92.3.0.8", {"center": v(80, 16) * mm, "radius": 2 * mm});
            skCircle(sketch, "E92.3.0.9", {"center": v(88, 16) * mm, "radius": 2 * mm});
            skLineSegment(sketch, "E92.3.0.10", {"start": v(96, -24) * mm, "end": v(72, 0) * mm, "construction": true});
            skLineSegment(sketch, "E92.3.0.11", {"start": v(72, 24) * mm, "end": v(96, 0) * mm, "construction": true});
            skLineSegment(sketch, "E92.3.0.12", {"start": v(96, 24) * mm, "end": v(72, 0) * mm, "construction": true});
            skArc(sketch, "E92.3.0.13", {"start": v(88.93, 9.9) * mm, "mid": v(86.1, 9.9) * mm, "end": v(86.1, 7.07) * mm});
            skArc(sketch, "E92.3.0.14", {"start": v(81.9, 7.07) * mm, "mid": v(81.9, 9.9) * mm, "end": v(79.07, 9.9) * mm});
            skArc(sketch, "E92.3.0.15", {"start": v(86.1, -7.07) * mm, "mid": v(86.1, -9.9) * mm, "end": v(88.93, -9.9) * mm});
            skArc(sketch, "E92.3.0.16", {"start": v(86.59, 6.59) * mm, "mid": v(89.41, 6.59) * mm, "end": v(89.41, 9.41) * mm});
            skLineSegment(sketch, "E92.3.0.17", {"start": v(80, -16) * mm, "end": v(88, -16) * mm, "construction": true});
            skLineSegment(sketch, "E92.3.0.18", {"start": v(72, 0) * mm, "end": v(96, 0) * mm, "construction": true});
            skArc(sketch, "E92.3.0.19", {"start": v(89.41, -9.41) * mm, "mid": v(89.41, -6.59) * mm, "end": v(86.59, -6.59) * mm});
            skCircle(sketch, "E92.3.0.20", {"center": v(80, -16) * mm, "radius": 2 * mm});
            skCircle(sketch, "E92.3.0.21", {"center": v(84, 0) * mm, "radius": 2 * mm});
            skPoint(sketch, "E92.3.0.22", {"position": v(80, -8) * mm});
            skLineSegment(sketch, "E92.3.0.23", {"start": v(96, 0) * mm, "end": v(72, 0) * mm, "construction": true});
            skLineSegment(sketch, "E92.3.0.24", {"start": v(86.59, 6.59) * mm, "end": v(89.41, 9.41) * mm, "construction": true});
            skLineSegment(sketch, "E92.3.0.25", {"start": v(86.1, -7.07) * mm, "end": v(88.93, -9.9) * mm, "construction": true});
            skLineSegment(sketch, "E92.3.0.26", {"start": v(78.59, 9.41) * mm, "end": v(81.41, 6.59) * mm, "construction": true});
            skLineSegment(sketch, "E92.3.0.27", {"start": v(79.07, 9.9) * mm, "end": v(81.9, 7.07) * mm, "construction": true});
            skLineSegment(sketch, "E92.3.0.28", {"start": v(88.93, 9.9) * mm, "end": v(86.1, 7.07) * mm, "construction": true});
            skLineSegment(sketch, "E92.3.0.29", {"start": v(86.59, -6.59) * mm, "end": v(89.41, -9.41) * mm, "construction": true});
            skLineSegment(sketch, "E92.3.0.30", {"start": v(79.07, -9.9) * mm, "end": v(81.9, -7.07) * mm, "construction": true});
            skLineSegment(sketch, "E92.3.0.31", {"start": v(81.41, -6.59) * mm, "end": v(78.59, -9.41) * mm, "construction": true});
            skLineSegment(sketch, "E92.3.0.32", {"start": v(86.1, -7.07) * mm, "end": v(86.59, -6.59) * mm});
            skLineSegment(sketch, "E92.3.0.33", {"start": v(78.59, 9.41) * mm, "end": v(79.07, 9.9) * mm});
            skLineSegment(sketch, "E92.3.0.34", {"start": v(78.59, -9.41) * mm, "end": v(79.07, -9.9) * mm});
            skLineSegment(sketch, "E92.3.0.35", {"start": v(88.93, -9.9) * mm, "end": v(89.41, -9.41) * mm});
            skLineSegment(sketch, "E92.3.0.36", {"start": v(81.41, 6.59) * mm, "end": v(81.9, 7.07) * mm});
            skLineSegment(sketch, "E92.3.0.37", {"start": v(88.93, 9.9) * mm, "end": v(89.41, 9.41) * mm});
            skLineSegment(sketch, "E92.3.0.38", {"start": v(86.1, 7.07) * mm, "end": v(86.59, 6.59) * mm});
            skLineSegment(sketch, "E92.3.0.39", {"start": v(81.41, -6.59) * mm, "end": v(81.9, -7.07) * mm});
            skArc(sketch, "E92.4.0.0", {"start": v(102.59, 9.41) * mm, "mid": v(102.59, 6.59) * mm, "end": v(105.41, 6.59) * mm});
            skArc(sketch, "E92.4.0.1", {"start": v(105.41, -6.59) * mm, "mid": v(102.59, -6.59) * mm, "end": v(102.59, -9.41) * mm});
            skLineSegment(sketch, "E92.4.0.2", {"start": v(96, 24) * mm, "end": v(120, 24) * mm, "construction": true});
            skLineSegment(sketch, "E92.4.0.3", {"start": v(104, 16) * mm, "end": v(112, 16) * mm, "construction": true});
            skArc(sketch, "E92.4.0.4", {"start": v(103.07, -9.9) * mm, "mid": v(105.9, -9.9) * mm, "end": v(105.9, -7.07) * mm});
            skLineSegment(sketch, "E92.4.0.5", {"start": v(120, 0) * mm, "end": v(96, -24) * mm, "construction": true});
            skCircle(sketch, "E92.4.0.6", {"center": v(112, -16) * mm, "radius": 2 * mm});
            skLineSegment(sketch, "E92.4.0.7", {"start": v(120, -24) * mm, "end": v(96, -24) * mm, "construction": true});
            skCircle(sketch, "E92.4.0.8", {"center": v(104, 16) * mm, "radius": 2 * mm});
            skCircle(sketch, "E92.4.0.9", {"center": v(112, 16) * mm, "radius": 2 * mm});
            skLineSegment(sketch, "E92.4.0.10", {"start": v(120, -24) * mm, "end": v(96, 0) * mm, "construction": true});
            skLineSegment(sketch, "E92.4.0.11", {"start": v(96, 24) * mm, "end": v(120, 0) * mm, "construction": true});
            skLineSegment(sketch, "E92.4.0.12", {"start": v(120, 24) * mm, "end": v(96, 0) * mm, "construction": true});
            skArc(sketch, "E92.4.0.13", {"start": v(112.93, 9.9) * mm, "mid": v(110.1, 9.9) * mm, "end": v(110.1, 7.07) * mm});
            skArc(sketch, "E92.4.0.14", {"start": v(105.9, 7.07) * mm, "mid": v(105.9, 9.9) * mm, "end": v(103.07, 9.9) * mm});
            skArc(sketch, "E92.4.0.15", {"start": v(110.1, -7.07) * mm, "mid": v(110.1, -9.9) * mm, "end": v(112.93, -9.9) * mm});
            skArc(sketch, "E92.4.0.16", {"start": v(110.59, 6.59) * mm, "mid": v(113.41, 6.59) * mm, "end": v(113.41, 9.41) * mm});
            skLineSegment(sketch, "E92.4.0.17", {"start": v(104, -16) * mm, "end": v(112, -16) * mm, "construction": true});
            skLineSegment(sketch, "E92.4.0.18", {"start": v(96, 0) * mm, "end": v(120, 0) * mm, "construction": true});
            skArc(sketch, "E92.4.0.19", {"start": v(113.41, -9.41) * mm, "mid": v(113.41, -6.59) * mm, "end": v(110.59, -6.59) * mm});
            skCircle(sketch, "E92.4.0.20", {"center": v(104, -16) * mm, "radius": 2 * mm});
            skCircle(sketch, "E92.4.0.21", {"center": v(108, 0) * mm, "radius": 2 * mm});
            skPoint(sketch, "E92.4.0.22", {"position": v(104, -8) * mm});
            skLineSegment(sketch, "E92.4.0.23", {"start": v(120, 0) * mm, "end": v(96, 0) * mm, "construction": true});
            skLineSegment(sketch, "E92.4.0.24", {"start": v(110.59, 6.59) * mm, "end": v(113.41, 9.41) * mm, "construction": true});
            skLineSegment(sketch, "E92.4.0.25", {"start": v(110.1, -7.07) * mm, "end": v(112.93, -9.9) * mm, "construction": true});
            skLineSegment(sketch, "E92.4.0.26", {"start": v(102.59, 9.41) * mm, "end": v(105.41, 6.59) * mm, "construction": true});
            skLineSegment(sketch, "E92.4.0.27", {"start": v(103.07, 9.9) * mm, "end": v(105.9, 7.07) * mm, "construction": true});
            skLineSegment(sketch, "E92.4.0.28", {"start": v(112.93, 9.9) * mm, "end": v(110.1, 7.07) * mm, "construction": true});
            skLineSegment(sketch, "E92.4.0.29", {"start": v(110.59, -6.59) * mm, "end": v(113.41, -9.41) * mm, "construction": true});
            skLineSegment(sketch, "E92.4.0.30", {"start": v(103.07, -9.9) * mm, "end": v(105.9, -7.07) * mm, "construction": true});
            skLineSegment(sketch, "E92.4.0.31", {"start": v(105.41, -6.59) * mm, "end": v(102.59, -9.41) * mm, "construction": true});
            skLineSegment(sketch, "E92.4.0.32", {"start": v(110.1, -7.07) * mm, "end": v(110.59, -6.59) * mm});
            skLineSegment(sketch, "E92.4.0.33", {"start": v(102.59, 9.41) * mm, "end": v(103.07, 9.9) * mm});
            skLineSegment(sketch, "E92.4.0.34", {"start": v(102.59, -9.41) * mm, "end": v(103.07, -9.9) * mm});
            skLineSegment(sketch, "E92.4.0.35", {"start": v(112.93, -9.9) * mm, "end": v(113.41, -9.41) * mm});
            skLineSegment(sketch, "E92.4.0.36", {"start": v(105.41, 6.59) * mm, "end": v(105.9, 7.07) * mm});
            skLineSegment(sketch, "E92.4.0.37", {"start": v(112.93, 9.9) * mm, "end": v(113.41, 9.41) * mm});
            skLineSegment(sketch, "E92.4.0.38", {"start": v(110.1, 7.07) * mm, "end": v(110.59, 6.59) * mm});
            skLineSegment(sketch, "E92.4.0.39", {"start": v(105.41, -6.59) * mm, "end": v(105.9, -7.07) * mm});
            skArc(sketch, "E92.5.0.0", {"start": v(126.59, 9.41) * mm, "mid": v(126.59, 6.59) * mm, "end": v(129.41, 6.59) * mm});
            skArc(sketch, "E92.5.0.1", {"start": v(129.41, -6.59) * mm, "mid": v(126.59, -6.59) * mm, "end": v(126.59, -9.41) * mm});
            skLineSegment(sketch, "E92.5.0.2", {"start": v(120, 24) * mm, "end": v(144, 24) * mm, "construction": true});
            skLineSegment(sketch, "E92.5.0.3", {"start": v(128, 16) * mm, "end": v(136, 16) * mm, "construction": true});
            skArc(sketch, "E92.5.0.4", {"start": v(127.07, -9.9) * mm, "mid": v(129.9, -9.9) * mm, "end": v(129.9, -7.07) * mm});
            skLineSegment(sketch, "E92.5.0.5", {"start": v(144, 0) * mm, "end": v(120, -24) * mm, "construction": true});
            skCircle(sketch, "E92.5.0.6", {"center": v(136, -16) * mm, "radius": 2 * mm});
            skLineSegment(sketch, "E92.5.0.7", {"start": v(144, -24) * mm, "end": v(120, -24) * mm, "construction": true});
            skCircle(sketch, "E92.5.0.8", {"center": v(128, 16) * mm, "radius": 2 * mm});
            skCircle(sketch, "E92.5.0.9", {"center": v(136, 16) * mm, "radius": 2 * mm});
            skLineSegment(sketch, "E92.5.0.10", {"start": v(144, -24) * mm, "end": v(120, 0) * mm, "construction": true});
            skLineSegment(sketch, "E92.5.0.11", {"start": v(120, 24) * mm, "end": v(144, 0) * mm, "construction": true});
            skLineSegment(sketch, "E92.5.0.12", {"start": v(144, 24) * mm, "end": v(120, 0) * mm, "construction": true});
            skArc(sketch, "E92.5.0.13", {"start": v(136.93, 9.9) * mm, "mid": v(134.1, 9.9) * mm, "end": v(134.1, 7.07) * mm});
            skArc(sketch, "E92.5.0.14", {"start": v(129.9, 7.07) * mm, "mid": v(129.9, 9.9) * mm, "end": v(127.07, 9.9) * mm});
            skArc(sketch, "E92.5.0.15", {"start": v(134.1, -7.07) * mm, "mid": v(134.1, -9.9) * mm, "end": v(136.93, -9.9) * mm});
            skArc(sketch, "E92.5.0.16", {"start": v(134.59, 6.59) * mm, "mid": v(137.41, 6.59) * mm, "end": v(137.41, 9.41) * mm});
            skLineSegment(sketch, "E92.5.0.17", {"start": v(128, -16) * mm, "end": v(136, -16) * mm, "construction": true});
            skLineSegment(sketch, "E92.5.0.18", {"start": v(120, 0) * mm, "end": v(144, 0) * mm, "construction": true});
            skArc(sketch, "E92.5.0.19", {"start": v(137.41, -9.41) * mm, "mid": v(137.41, -6.59) * mm, "end": v(134.59, -6.59) * mm});
            skCircle(sketch, "E92.5.0.20", {"center": v(128, -16) * mm, "radius": 2 * mm});
            skCircle(sketch, "E92.5.0.21", {"center": v(132, 0) * mm, "radius": 2 * mm});
            skPoint(sketch, "E92.5.0.22", {"position": v(128, -8) * mm});
            skLineSegment(sketch, "E92.5.0.23", {"start": v(144, 0) * mm, "end": v(120, 0) * mm, "construction": true});
            skLineSegment(sketch, "E92.5.0.24", {"start": v(134.59, 6.59) * mm, "end": v(137.41, 9.41) * mm, "construction": true});
            skLineSegment(sketch, "E92.5.0.25", {"start": v(134.1, -7.07) * mm, "end": v(136.93, -9.9) * mm, "construction": true});
            skLineSegment(sketch, "E92.5.0.26", {"start": v(126.59, 9.41) * mm, "end": v(129.41, 6.59) * mm, "construction": true});
            skLineSegment(sketch, "E92.5.0.27", {"start": v(127.07, 9.9) * mm, "end": v(129.9, 7.07) * mm, "construction": true});
            skLineSegment(sketch, "E92.5.0.28", {"start": v(136.93, 9.9) * mm, "end": v(134.1, 7.07) * mm, "construction": true});
            skLineSegment(sketch, "E92.5.0.29", {"start": v(134.59, -6.59) * mm, "end": v(137.41, -9.41) * mm, "construction": true});
            skLineSegment(sketch, "E92.5.0.30", {"start": v(127.07, -9.9) * mm, "end": v(129.9, -7.07) * mm, "construction": true});
            skLineSegment(sketch, "E92.5.0.31", {"start": v(129.41, -6.59) * mm, "end": v(126.59, -9.41) * mm, "construction": true});
            skLineSegment(sketch, "E92.5.0.32", {"start": v(134.1, -7.07) * mm, "end": v(134.59, -6.59) * mm});
            skLineSegment(sketch, "E92.5.0.33", {"start": v(126.59, 9.41) * mm, "end": v(127.07, 9.9) * mm});
            skLineSegment(sketch, "E92.5.0.34", {"start": v(126.59, -9.41) * mm, "end": v(127.07, -9.9) * mm});
            skLineSegment(sketch, "E92.5.0.35", {"start": v(136.93, -9.9) * mm, "end": v(137.41, -9.41) * mm});
            skLineSegment(sketch, "E92.5.0.36", {"start": v(129.41, 6.59) * mm, "end": v(129.9, 7.07) * mm});
            skLineSegment(sketch, "E92.5.0.37", {"start": v(136.93, 9.9) * mm, "end": v(137.41, 9.41) * mm});
            skLineSegment(sketch, "E92.5.0.38", {"start": v(134.1, 7.07) * mm, "end": v(134.59, 6.59) * mm});
            skLineSegment(sketch, "E92.5.0.39", {"start": v(129.41, -6.59) * mm, "end": v(129.9, -7.07) * mm});
            skArc(sketch, "E92.6.0.0", {"start": v(150.59, 9.41) * mm, "mid": v(150.59, 6.59) * mm, "end": v(153.41, 6.59) * mm});
            skArc(sketch, "E92.6.0.1", {"start": v(153.41, -6.59) * mm, "mid": v(150.59, -6.59) * mm, "end": v(150.59, -9.41) * mm});
            skLineSegment(sketch, "E92.6.0.2", {"start": v(144, 24) * mm, "end": v(168, 24) * mm, "construction": true});
            skLineSegment(sketch, "E92.6.0.3", {"start": v(152, 16) * mm, "end": v(160, 16) * mm, "construction": true});
            skArc(sketch, "E92.6.0.4", {"start": v(151.07, -9.9) * mm, "mid": v(153.9, -9.9) * mm, "end": v(153.9, -7.07) * mm});
            skLineSegment(sketch, "E92.6.0.5", {"start": v(168, 0) * mm, "end": v(144, -24) * mm, "construction": true});
            skCircle(sketch, "E92.6.0.6", {"center": v(160, -16) * mm, "radius": 2 * mm});
            skLineSegment(sketch, "E92.6.0.7", {"start": v(168, -24) * mm, "end": v(144, -24) * mm, "construction": true});
            skCircle(sketch, "E92.6.0.8", {"center": v(152, 16) * mm, "radius": 2 * mm});
            skCircle(sketch, "E92.6.0.9", {"center": v(160, 16) * mm, "radius": 2 * mm});
            skLineSegment(sketch, "E92.6.0.10", {"start": v(168, -24) * mm, "end": v(144, 0) * mm, "construction": true});
            skLineSegment(sketch, "E92.6.0.11", {"start": v(144, 24) * mm, "end": v(168, 0) * mm, "construction": true});
            skLineSegment(sketch, "E92.6.0.12", {"start": v(168, 24) * mm, "end": v(144, 0) * mm, "construction": true});
            skArc(sketch, "E92.6.0.13", {"start": v(160.93, 9.9) * mm, "mid": v(158.1, 9.9) * mm, "end": v(158.1, 7.07) * mm});
            skArc(sketch, "E92.6.0.14", {"start": v(153.9, 7.07) * mm, "mid": v(153.9, 9.9) * mm, "end": v(151.07, 9.9) * mm});
            skArc(sketch, "E92.6.0.15", {"start": v(158.1, -7.07) * mm, "mid": v(158.1, -9.9) * mm, "end": v(160.93, -9.9) * mm});
            skArc(sketch, "E92.6.0.16", {"start": v(158.59, 6.59) * mm, "mid": v(161.41, 6.59) * mm, "end": v(161.41, 9.41) * mm});
            skLineSegment(sketch, "E92.6.0.17", {"start": v(152, -16) * mm, "end": v(160, -16) * mm, "construction": true});
            skLineSegment(sketch, "E92.6.0.18", {"start": v(144, 0) * mm, "end": v(168, 0) * mm, "construction": true});
            skArc(sketch, "E92.6.0.19", {"start": v(161.41, -9.41) * mm, "mid": v(161.41, -6.59) * mm, "end": v(158.59, -6.59) * mm});
            skCircle(sketch, "E92.6.0.20", {"center": v(152, -16) * mm, "radius": 2 * mm});
            skCircle(sketch, "E92.6.0.21", {"center": v(156, 0) * mm, "radius": 2 * mm});
            skPoint(sketch, "E92.6.0.22", {"position": v(152, -8) * mm});
            skLineSegment(sketch, "E92.6.0.23", {"start": v(168, 0) * mm, "end": v(144, 0) * mm, "construction": true});
            skLineSegment(sketch, "E92.6.0.24", {"start": v(158.59, 6.59) * mm, "end": v(161.41, 9.41) * mm, "construction": true});
            skLineSegment(sketch, "E92.6.0.25", {"start": v(158.1, -7.07) * mm, "end": v(160.93, -9.9) * mm, "construction": true});
            skLineSegment(sketch, "E92.6.0.26", {"start": v(150.59, 9.41) * mm, "end": v(153.41, 6.59) * mm, "construction": true});
            skLineSegment(sketch, "E92.6.0.27", {"start": v(151.07, 9.9) * mm, "end": v(153.9, 7.07) * mm, "construction": true});
            skLineSegment(sketch, "E92.6.0.28", {"start": v(160.93, 9.9) * mm, "end": v(158.1, 7.07) * mm, "construction": true});
            skLineSegment(sketch, "E92.6.0.29", {"start": v(158.59, -6.59) * mm, "end": v(161.41, -9.41) * mm, "construction": true});
            skLineSegment(sketch, "E92.6.0.30", {"start": v(151.07, -9.9) * mm, "end": v(153.9, -7.07) * mm, "construction": true});
            skLineSegment(sketch, "E92.6.0.31", {"start": v(153.41, -6.59) * mm, "end": v(150.59, -9.41) * mm, "construction": true});
            skLineSegment(sketch, "E92.6.0.32", {"start": v(158.1, -7.07) * mm, "end": v(158.59, -6.59) * mm});
            skLineSegment(sketch, "E92.6.0.33", {"start": v(150.59, 9.41) * mm, "end": v(151.07, 9.9) * mm});
            skLineSegment(sketch, "E92.6.0.34", {"start": v(150.59, -9.41) * mm, "end": v(151.07, -9.9) * mm});
            skLineSegment(sketch, "E92.6.0.35", {"start": v(160.93, -9.9) * mm, "end": v(161.41, -9.41) * mm});
            skLineSegment(sketch, "E92.6.0.36", {"start": v(153.41, 6.59) * mm, "end": v(153.9, 7.07) * mm});
            skLineSegment(sketch, "E92.6.0.37", {"start": v(160.93, 9.9) * mm, "end": v(161.41, 9.41) * mm});
            skLineSegment(sketch, "E92.6.0.38", {"start": v(158.1, 7.07) * mm, "end": v(158.59, 6.59) * mm});
            skLineSegment(sketch, "E92.6.0.39", {"start": v(153.41, -6.59) * mm, "end": v(153.9, -7.07) * mm});
            skArc(sketch, "E92.7.0.0", {"start": v(174.59, 9.41) * mm, "mid": v(174.59, 6.59) * mm, "end": v(177.41, 6.59) * mm});
            skArc(sketch, "E92.7.0.1", {"start": v(177.41, -6.59) * mm, "mid": v(174.59, -6.59) * mm, "end": v(174.59, -9.41) * mm});
            skLineSegment(sketch, "E92.7.0.2", {"start": v(168, 24) * mm, "end": v(192, 24) * mm, "construction": true});
            skLineSegment(sketch, "E92.7.0.3", {"start": v(176, 16) * mm, "end": v(184, 16) * mm, "construction": true});
            skArc(sketch, "E92.7.0.4", {"start": v(175.07, -9.9) * mm, "mid": v(177.9, -9.9) * mm, "end": v(177.9, -7.07) * mm});
            skLineSegment(sketch, "E92.7.0.5", {"start": v(192, 0) * mm, "end": v(168, -24) * mm, "construction": true});
            skCircle(sketch, "E92.7.0.6", {"center": v(184, -16) * mm, "radius": 2 * mm});
            skLineSegment(sketch, "E92.7.0.7", {"start": v(192, -24) * mm, "end": v(168, -24) * mm, "construction": true});
            skCircle(sketch, "E92.7.0.8", {"center": v(176, 16) * mm, "radius": 2 * mm});
            skCircle(sketch, "E92.7.0.9", {"center": v(184, 16) * mm, "radius": 2 * mm});
            skLineSegment(sketch, "E92.7.0.10", {"start": v(192, -24) * mm, "end": v(168, 0) * mm, "construction": true});
            skLineSegment(sketch, "E92.7.0.11", {"start": v(168, 24) * mm, "end": v(192, 0) * mm, "construction": true});
            skLineSegment(sketch, "E92.7.0.12", {"start": v(192, 24) * mm, "end": v(168, 0) * mm, "construction": true});
            skArc(sketch, "E92.7.0.13", {"start": v(184.93, 9.9) * mm, "mid": v(182.1, 9.9) * mm, "end": v(182.1, 7.07) * mm});
            skArc(sketch, "E92.7.0.14", {"start": v(177.9, 7.07) * mm, "mid": v(177.9, 9.9) * mm, "end": v(175.07, 9.9) * mm});
            skArc(sketch, "E92.7.0.15", {"start": v(182.1, -7.07) * mm, "mid": v(182.1, -9.9) * mm, "end": v(184.93, -9.9) * mm});
            skArc(sketch, "E92.7.0.16", {"start": v(182.59, 6.59) * mm, "mid": v(185.41, 6.59) * mm, "end": v(185.41, 9.41) * mm});
            skLineSegment(sketch, "E92.7.0.17", {"start": v(176, -16) * mm, "end": v(184, -16) * mm, "construction": true});
            skLineSegment(sketch, "E92.7.0.18", {"start": v(168, 0) * mm, "end": v(192, 0) * mm, "construction": true});
            skArc(sketch, "E92.7.0.19", {"start": v(185.41, -9.41) * mm, "mid": v(185.41, -6.59) * mm, "end": v(182.59, -6.59) * mm});
            skCircle(sketch, "E92.7.0.20", {"center": v(176, -16) * mm, "radius": 2 * mm});
            skCircle(sketch, "E92.7.0.21", {"center": v(180, 0) * mm, "radius": 2 * mm});
            skPoint(sketch, "E92.7.0.22", {"position": v(176, -8) * mm});
            skLineSegment(sketch, "E92.7.0.23", {"start": v(192, 0) * mm, "end": v(168, 0) * mm, "construction": true});
            skLineSegment(sketch, "E92.7.0.24", {"start": v(182.59, 6.59) * mm, "end": v(185.41, 9.41) * mm, "construction": true});
            skLineSegment(sketch, "E92.7.0.25", {"start": v(182.1, -7.07) * mm, "end": v(184.93, -9.9) * mm, "construction": true});
            skLineSegment(sketch, "E92.7.0.26", {"start": v(174.59, 9.41) * mm, "end": v(177.41, 6.59) * mm, "construction": true});
            skLineSegment(sketch, "E92.7.0.27", {"start": v(175.07, 9.9) * mm, "end": v(177.9, 7.07) * mm, "construction": true});
            skLineSegment(sketch, "E92.7.0.28", {"start": v(184.93, 9.9) * mm, "end": v(182.1, 7.07) * mm, "construction": true});
            skLineSegment(sketch, "E92.7.0.29", {"start": v(182.59, -6.59) * mm, "end": v(185.41, -9.41) * mm, "construction": true});
            skLineSegment(sketch, "E92.7.0.30", {"start": v(175.07, -9.9) * mm, "end": v(177.9, -7.07) * mm, "construction": true});
            skLineSegment(sketch, "E92.7.0.31", {"start": v(177.41, -6.59) * mm, "end": v(174.59, -9.41) * mm, "construction": true});
            skLineSegment(sketch, "E92.7.0.32", {"start": v(182.1, -7.07) * mm, "end": v(182.59, -6.59) * mm});
            skLineSegment(sketch, "E92.7.0.33", {"start": v(174.59, 9.41) * mm, "end": v(175.07, 9.9) * mm});
            skLineSegment(sketch, "E92.7.0.34", {"start": v(174.59, -9.41) * mm, "end": v(175.07, -9.9) * mm});
            skLineSegment(sketch, "E92.7.0.35", {"start": v(184.93, -9.9) * mm, "end": v(185.41, -9.41) * mm});
            skLineSegment(sketch, "E92.7.0.36", {"start": v(177.41, 6.59) * mm, "end": v(177.9, 7.07) * mm});
            skLineSegment(sketch, "E92.7.0.37", {"start": v(184.93, 9.9) * mm, "end": v(185.41, 9.41) * mm});
            skLineSegment(sketch, "E92.7.0.38", {"start": v(182.1, 7.07) * mm, "end": v(182.59, 6.59) * mm});
            skLineSegment(sketch, "E92.7.0.39", {"start": v(177.41, -6.59) * mm, "end": v(177.9, -7.07) * mm});
            skArc(sketch, "E92.8.0.0", {"start": v(198.59, 9.41) * mm, "mid": v(198.59, 6.59) * mm, "end": v(201.41, 6.59) * mm});
            skArc(sketch, "E92.8.0.1", {"start": v(201.41, -6.59) * mm, "mid": v(198.59, -6.59) * mm, "end": v(198.59, -9.41) * mm});
            skLineSegment(sketch, "E92.8.0.2", {"start": v(192, 24) * mm, "end": v(216, 24) * mm, "construction": true});
            skLineSegment(sketch, "E92.8.0.3", {"start": v(200, 16) * mm, "end": v(208, 16) * mm, "construction": true});
            skArc(sketch, "E92.8.0.4", {"start": v(199.07, -9.9) * mm, "mid": v(201.9, -9.9) * mm, "end": v(201.9, -7.07) * mm});
            skLineSegment(sketch, "E92.8.0.5", {"start": v(216, 0) * mm, "end": v(192, -24) * mm, "construction": true});
            skCircle(sketch, "E92.8.0.6", {"center": v(208, -16) * mm, "radius": 2 * mm});
            skLineSegment(sketch, "E92.8.0.7", {"start": v(216, -24) * mm, "end": v(192, -24) * mm, "construction": true});
            skCircle(sketch, "E92.8.0.8", {"center": v(200, 16) * mm, "radius": 2 * mm});
            skCircle(sketch, "E92.8.0.9", {"center": v(208, 16) * mm, "radius": 2 * mm});
            skLineSegment(sketch, "E92.8.0.10", {"start": v(216, -24) * mm, "end": v(192, 0) * mm, "construction": true});
            skLineSegment(sketch, "E92.8.0.11", {"start": v(192, 24) * mm, "end": v(216, 0) * mm, "construction": true});
            skLineSegment(sketch, "E92.8.0.12", {"start": v(216, 24) * mm, "end": v(192, 0) * mm, "construction": true});
            skArc(sketch, "E92.8.0.13", {"start": v(208.93, 9.9) * mm, "mid": v(206.1, 9.9) * mm, "end": v(206.1, 7.07) * mm});
            skArc(sketch, "E92.8.0.14", {"start": v(201.9, 7.07) * mm, "mid": v(201.9, 9.9) * mm, "end": v(199.07, 9.9) * mm});
            skArc(sketch, "E92.8.0.15", {"start": v(206.1, -7.07) * mm, "mid": v(206.1, -9.9) * mm, "end": v(208.93, -9.9) * mm});
            skArc(sketch, "E92.8.0.16", {"start": v(206.59, 6.59) * mm, "mid": v(209.41, 6.59) * mm, "end": v(209.41, 9.41) * mm});
            skLineSegment(sketch, "E92.8.0.17", {"start": v(200, -16) * mm, "end": v(208, -16) * mm, "construction": true});
            skLineSegment(sketch, "E92.8.0.18", {"start": v(192, 0) * mm, "end": v(216, 0) * mm, "construction": true});
            skArc(sketch, "E92.8.0.19", {"start": v(209.41, -9.41) * mm, "mid": v(209.41, -6.59) * mm, "end": v(206.59, -6.59) * mm});
            skCircle(sketch, "E92.8.0.20", {"center": v(200, -16) * mm, "radius": 2 * mm});
            skCircle(sketch, "E92.8.0.21", {"center": v(204, 0) * mm, "radius": 2 * mm});
            skPoint(sketch, "E92.8.0.22", {"position": v(200, -8) * mm});
            skLineSegment(sketch, "E92.8.0.23", {"start": v(216, 0) * mm, "end": v(192, 0) * mm, "construction": true});
            skLineSegment(sketch, "E92.8.0.24", {"start": v(206.59, 6.59) * mm, "end": v(209.41, 9.41) * mm, "construction": true});
            skLineSegment(sketch, "E92.8.0.25", {"start": v(206.1, -7.07) * mm, "end": v(208.93, -9.9) * mm, "construction": true});
            skLineSegment(sketch, "E92.8.0.26", {"start": v(198.59, 9.41) * mm, "end": v(201.41, 6.59) * mm, "construction": true});
            skLineSegment(sketch, "E92.8.0.27", {"start": v(199.07, 9.9) * mm, "end": v(201.9, 7.07) * mm, "construction": true});
            skLineSegment(sketch, "E92.8.0.28", {"start": v(208.93, 9.9) * mm, "end": v(206.1, 7.07) * mm, "construction": true});
            skLineSegment(sketch, "E92.8.0.29", {"start": v(206.59, -6.59) * mm, "end": v(209.41, -9.41) * mm, "construction": true});
            skLineSegment(sketch, "E92.8.0.30", {"start": v(199.07, -9.9) * mm, "end": v(201.9, -7.07) * mm, "construction": true});
            skLineSegment(sketch, "E92.8.0.31", {"start": v(201.41, -6.59) * mm, "end": v(198.59, -9.41) * mm, "construction": true});
            skLineSegment(sketch, "E92.8.0.32", {"start": v(206.1, -7.07) * mm, "end": v(206.59, -6.59) * mm});
            skLineSegment(sketch, "E92.8.0.33", {"start": v(198.59, 9.41) * mm, "end": v(199.07, 9.9) * mm});
            skLineSegment(sketch, "E92.8.0.34", {"start": v(198.59, -9.41) * mm, "end": v(199.07, -9.9) * mm});
            skLineSegment(sketch, "E92.8.0.35", {"start": v(208.93, -9.9) * mm, "end": v(209.41, -9.41) * mm});
            skLineSegment(sketch, "E92.8.0.36", {"start": v(201.41, 6.59) * mm, "end": v(201.9, 7.07) * mm});
            skLineSegment(sketch, "E92.8.0.37", {"start": v(208.93, 9.9) * mm, "end": v(209.41, 9.41) * mm});
            skLineSegment(sketch, "E92.8.0.38", {"start": v(206.1, 7.07) * mm, "end": v(206.59, 6.59) * mm});
            skLineSegment(sketch, "E92.8.0.39", {"start": v(201.41, -6.59) * mm, "end": v(201.9, -7.07) * mm});
            skArc(sketch, "E92.9.0.0", {"start": v(222.59, 9.41) * mm, "mid": v(222.59, 6.59) * mm, "end": v(225.41, 6.59) * mm});
            skArc(sketch, "E92.9.0.1", {"start": v(225.41, -6.59) * mm, "mid": v(222.59, -6.59) * mm, "end": v(222.59, -9.41) * mm});
            skLineSegment(sketch, "E92.9.0.2", {"start": v(216, 24) * mm, "end": v(240, 24) * mm, "construction": true});
            skLineSegment(sketch, "E92.9.0.3", {"start": v(224, 16) * mm, "end": v(232, 16) * mm, "construction": true});
            skArc(sketch, "E92.9.0.4", {"start": v(223.07, -9.9) * mm, "mid": v(225.9, -9.9) * mm, "end": v(225.9, -7.07) * mm});
            skLineSegment(sketch, "E92.9.0.5", {"start": v(240, 0) * mm, "end": v(216, -24) * mm, "construction": true});
            skCircle(sketch, "E92.9.0.6", {"center": v(232, -16) * mm, "radius": 2 * mm});
            skLineSegment(sketch, "E92.9.0.7", {"start": v(240, -24) * mm, "end": v(216, -24) * mm, "construction": true});
            skCircle(sketch, "E92.9.0.8", {"center": v(224, 16) * mm, "radius": 2 * mm});
            skCircle(sketch, "E92.9.0.9", {"center": v(232, 16) * mm, "radius": 2 * mm});
            skLineSegment(sketch, "E92.9.0.10", {"start": v(240, -24) * mm, "end": v(216, 0) * mm, "construction": true});
            skLineSegment(sketch, "E92.9.0.11", {"start": v(216, 24) * mm, "end": v(240, 0) * mm, "construction": true});
            skLineSegment(sketch, "E92.9.0.12", {"start": v(240, 24) * mm, "end": v(216, 0) * mm, "construction": true});
            skArc(sketch, "E92.9.0.13", {"start": v(232.93, 9.9) * mm, "mid": v(230.1, 9.9) * mm, "end": v(230.1, 7.07) * mm});
            skArc(sketch, "E92.9.0.14", {"start": v(225.9, 7.07) * mm, "mid": v(225.9, 9.9) * mm, "end": v(223.07, 9.9) * mm});
            skArc(sketch, "E92.9.0.15", {"start": v(230.1, -7.07) * mm, "mid": v(230.1, -9.9) * mm, "end": v(232.93, -9.9) * mm});
            skArc(sketch, "E92.9.0.16", {"start": v(230.59, 6.59) * mm, "mid": v(233.41, 6.59) * mm, "end": v(233.41, 9.41) * mm});
            skLineSegment(sketch, "E92.9.0.17", {"start": v(224, -16) * mm, "end": v(232, -16) * mm, "construction": true});
            skLineSegment(sketch, "E92.9.0.18", {"start": v(216, 0) * mm, "end": v(240, 0) * mm, "construction": true});
            skArc(sketch, "E92.9.0.19", {"start": v(233.41, -9.41) * mm, "mid": v(233.41, -6.59) * mm, "end": v(230.59, -6.59) * mm});
            skCircle(sketch, "E92.9.0.20", {"center": v(224, -16) * mm, "radius": 2 * mm});
            skCircle(sketch, "E92.9.0.21", {"center": v(228, 0) * mm, "radius": 2 * mm});
            skPoint(sketch, "E92.9.0.22", {"position": v(224, -8) * mm});
            skLineSegment(sketch, "E92.9.0.23", {"start": v(240, 0) * mm, "end": v(216, 0) * mm, "construction": true});
            skLineSegment(sketch, "E92.9.0.24", {"start": v(230.59, 6.59) * mm, "end": v(233.41, 9.41) * mm, "construction": true});
            skLineSegment(sketch, "E92.9.0.25", {"start": v(230.1, -7.07) * mm, "end": v(232.93, -9.9) * mm, "construction": true});
            skLineSegment(sketch, "E92.9.0.26", {"start": v(222.59, 9.41) * mm, "end": v(225.41, 6.59) * mm, "construction": true});
            skLineSegment(sketch, "E92.9.0.27", {"start": v(223.07, 9.9) * mm, "end": v(225.9, 7.07) * mm, "construction": true});
            skLineSegment(sketch, "E92.9.0.28", {"start": v(232.93, 9.9) * mm, "end": v(230.1, 7.07) * mm, "construction": true});
            skLineSegment(sketch, "E92.9.0.29", {"start": v(230.59, -6.59) * mm, "end": v(233.41, -9.41) * mm, "construction": true});
            skLineSegment(sketch, "E92.9.0.30", {"start": v(223.07, -9.9) * mm, "end": v(225.9, -7.07) * mm, "construction": true});
            skLineSegment(sketch, "E92.9.0.31", {"start": v(225.41, -6.59) * mm, "end": v(222.59, -9.41) * mm, "construction": true});
            skLineSegment(sketch, "E92.9.0.32", {"start": v(230.1, -7.07) * mm, "end": v(230.59, -6.59) * mm});
            skLineSegment(sketch, "E92.9.0.33", {"start": v(222.59, 9.41) * mm, "end": v(223.07, 9.9) * mm});
            skLineSegment(sketch, "E92.9.0.34", {"start": v(222.59, -9.41) * mm, "end": v(223.07, -9.9) * mm});
            skLineSegment(sketch, "E92.9.0.35", {"start": v(232.93, -9.9) * mm, "end": v(233.41, -9.41) * mm});
            skLineSegment(sketch, "E92.9.0.36", {"start": v(225.41, 6.59) * mm, "end": v(225.9, 7.07) * mm});
            skLineSegment(sketch, "E92.9.0.37", {"start": v(232.93, 9.9) * mm, "end": v(233.41, 9.41) * mm});
            skLineSegment(sketch, "E92.9.0.38", {"start": v(230.1, 7.07) * mm, "end": v(230.59, 6.59) * mm});
            skLineSegment(sketch, "E92.9.0.39", {"start": v(225.41, -6.59) * mm, "end": v(225.9, -7.07) * mm});
            skArc(sketch, "E92.10.0.0", {"start": v(246.59, 9.41) * mm, "mid": v(246.59, 6.59) * mm, "end": v(249.41, 6.59) * mm});
            skArc(sketch, "E92.10.0.1", {"start": v(249.41, -6.59) * mm, "mid": v(246.59, -6.59) * mm, "end": v(246.59, -9.41) * mm});
            skLineSegment(sketch, "E92.10.0.2", {"start": v(240, 24) * mm, "end": v(264, 24) * mm, "construction": true});
            skLineSegment(sketch, "E92.10.0.3", {"start": v(248, 16) * mm, "end": v(256, 16) * mm, "construction": true});
            skArc(sketch, "E92.10.0.4", {"start": v(247.07, -9.9) * mm, "mid": v(249.9, -9.9) * mm, "end": v(249.9, -7.07) * mm});
            skLineSegment(sketch, "E92.10.0.5", {"start": v(264, 0) * mm, "end": v(240, -24) * mm, "construction": true});
            skCircle(sketch, "E92.10.0.6", {"center": v(256, -16) * mm, "radius": 2 * mm});
            skLineSegment(sketch, "E92.10.0.7", {"start": v(264, -24) * mm, "end": v(240, -24) * mm, "construction": true});
            skCircle(sketch, "E92.10.0.8", {"center": v(248, 16) * mm, "radius": 2 * mm});
            skCircle(sketch, "E92.10.0.9", {"center": v(256, 16) * mm, "radius": 2 * mm});
            skLineSegment(sketch, "E92.10.0.10", {"start": v(264, -24) * mm, "end": v(240, 0) * mm, "construction": true});
            skLineSegment(sketch, "E92.10.0.11", {"start": v(240, 24) * mm, "end": v(264, 0) * mm, "construction": true});
            skLineSegment(sketch, "E92.10.0.12", {"start": v(264, 24) * mm, "end": v(240, 0) * mm, "construction": true});
            skArc(sketch, "E92.10.0.13", {"start": v(256.93, 9.9) * mm, "mid": v(254.1, 9.9) * mm, "end": v(254.1, 7.07) * mm});
            skArc(sketch, "E92.10.0.14", {"start": v(249.9, 7.07) * mm, "mid": v(249.9, 9.9) * mm, "end": v(247.07, 9.9) * mm});
            skArc(sketch, "E92.10.0.15", {"start": v(254.1, -7.07) * mm, "mid": v(254.1, -9.9) * mm, "end": v(256.93, -9.9) * mm});
            skArc(sketch, "E92.10.0.16", {"start": v(254.59, 6.59) * mm, "mid": v(257.41, 6.59) * mm, "end": v(257.41, 9.41) * mm});
            skLineSegment(sketch, "E92.10.0.17", {"start": v(248, -16) * mm, "end": v(256, -16) * mm, "construction": true});
            skLineSegment(sketch, "E92.10.0.18", {"start": v(240, 0) * mm, "end": v(264, 0) * mm, "construction": true});
            skArc(sketch, "E92.10.0.19", {"start": v(257.41, -9.41) * mm, "mid": v(257.41, -6.59) * mm, "end": v(254.59, -6.59) * mm});
            skCircle(sketch, "E92.10.0.20", {"center": v(248, -16) * mm, "radius": 2 * mm});
            skCircle(sketch, "E92.10.0.21", {"center": v(252, 0) * mm, "radius": 2 * mm});
            skPoint(sketch, "E92.10.0.22", {"position": v(248, -8) * mm});
            skLineSegment(sketch, "E92.10.0.23", {"start": v(264, 0) * mm, "end": v(240, 0) * mm, "construction": true});
            skLineSegment(sketch, "E92.10.0.24", {"start": v(254.59, 6.59) * mm, "end": v(257.41, 9.41) * mm, "construction": true});
            skLineSegment(sketch, "E92.10.0.25", {"start": v(254.1, -7.07) * mm, "end": v(256.93, -9.9) * mm, "construction": true});
            skLineSegment(sketch, "E92.10.0.26", {"start": v(246.59, 9.41) * mm, "end": v(249.41, 6.59) * mm, "construction": true});
            skLineSegment(sketch, "E92.10.0.27", {"start": v(247.07, 9.9) * mm, "end": v(249.9, 7.07) * mm, "construction": true});
            skLineSegment(sketch, "E92.10.0.28", {"start": v(256.93, 9.9) * mm, "end": v(254.1, 7.07) * mm, "construction": true});
            skLineSegment(sketch, "E92.10.0.29", {"start": v(254.59, -6.59) * mm, "end": v(257.41, -9.41) * mm, "construction": true});
            skLineSegment(sketch, "E92.10.0.30", {"start": v(247.07, -9.9) * mm, "end": v(249.9, -7.07) * mm, "construction": true});
            skLineSegment(sketch, "E92.10.0.31", {"start": v(249.41, -6.59) * mm, "end": v(246.59, -9.41) * mm, "construction": true});
            skLineSegment(sketch, "E92.10.0.32", {"start": v(254.1, -7.07) * mm, "end": v(254.59, -6.59) * mm});
            skLineSegment(sketch, "E92.10.0.33", {"start": v(246.59, 9.41) * mm, "end": v(247.07, 9.9) * mm});
            skLineSegment(sketch, "E92.10.0.34", {"start": v(246.59, -9.41) * mm, "end": v(247.07, -9.9) * mm});
            skLineSegment(sketch, "E92.10.0.35", {"start": v(256.93, -9.9) * mm, "end": v(257.41, -9.41) * mm});
            skLineSegment(sketch, "E92.10.0.36", {"start": v(249.41, 6.59) * mm, "end": v(249.9, 7.07) * mm});
            skLineSegment(sketch, "E92.10.0.37", {"start": v(256.93, 9.9) * mm, "end": v(257.41, 9.41) * mm});
            skLineSegment(sketch, "E92.10.0.38", {"start": v(254.1, 7.07) * mm, "end": v(254.59, 6.59) * mm});
            skLineSegment(sketch, "E92.10.0.39", {"start": v(249.41, -6.59) * mm, "end": v(249.9, -7.07) * mm});
            skArc(sketch, "E92.11.0.0", {"start": v(270.59, 9.41) * mm, "mid": v(270.59, 6.59) * mm, "end": v(273.41, 6.59) * mm});
            skArc(sketch, "E92.11.0.1", {"start": v(273.41, -6.59) * mm, "mid": v(270.59, -6.59) * mm, "end": v(270.59, -9.41) * mm});
            skLineSegment(sketch, "E92.11.0.2", {"start": v(264, 24) * mm, "end": v(288, 24) * mm, "construction": true});
            skLineSegment(sketch, "E92.11.0.3", {"start": v(272, 16) * mm, "end": v(280, 16) * mm, "construction": true});
            skArc(sketch, "E92.11.0.4", {"start": v(271.07, -9.9) * mm, "mid": v(273.9, -9.9) * mm, "end": v(273.9, -7.07) * mm});
            skLineSegment(sketch, "E92.11.0.5", {"start": v(288, 0) * mm, "end": v(264, -24) * mm, "construction": true});
            skCircle(sketch, "E92.11.0.6", {"center": v(280, -16) * mm, "radius": 2 * mm});
            skLineSegment(sketch, "E92.11.0.7", {"start": v(288, -24) * mm, "end": v(264, -24) * mm, "construction": true});
            skCircle(sketch, "E92.11.0.8", {"center": v(272, 16) * mm, "radius": 2 * mm});
            skCircle(sketch, "E92.11.0.9", {"center": v(280, 16) * mm, "radius": 2 * mm});
            skLineSegment(sketch, "E92.11.0.10", {"start": v(288, -24) * mm, "end": v(264, 0) * mm, "construction": true});
            skLineSegment(sketch, "E92.11.0.11", {"start": v(264, 24) * mm, "end": v(288, 0) * mm, "construction": true});
            skLineSegment(sketch, "E92.11.0.12", {"start": v(288, 24) * mm, "end": v(264, 0) * mm, "construction": true});
            skArc(sketch, "E92.11.0.13", {"start": v(280.93, 9.9) * mm, "mid": v(278.1, 9.9) * mm, "end": v(278.1, 7.07) * mm});
            skArc(sketch, "E92.11.0.14", {"start": v(273.9, 7.07) * mm, "mid": v(273.9, 9.9) * mm, "end": v(271.07, 9.9) * mm});
            skArc(sketch, "E92.11.0.15", {"start": v(278.1, -7.07) * mm, "mid": v(278.1, -9.9) * mm, "end": v(280.93, -9.9) * mm});
            skArc(sketch, "E92.11.0.16", {"start": v(278.59, 6.59) * mm, "mid": v(281.41, 6.59) * mm, "end": v(281.41, 9.41) * mm});
            skLineSegment(sketch, "E92.11.0.17", {"start": v(272, -16) * mm, "end": v(280, -16) * mm, "construction": true});
            skLineSegment(sketch, "E92.11.0.18", {"start": v(264, 0) * mm, "end": v(288, 0) * mm, "construction": true});
            skArc(sketch, "E92.11.0.19", {"start": v(281.41, -9.41) * mm, "mid": v(281.41, -6.59) * mm, "end": v(278.59, -6.59) * mm});
            skCircle(sketch, "E92.11.0.20", {"center": v(272, -16) * mm, "radius": 2 * mm});
            skCircle(sketch, "E92.11.0.21", {"center": v(276, 0) * mm, "radius": 2 * mm});
            skPoint(sketch, "E92.11.0.22", {"position": v(272, -8) * mm});
            skLineSegment(sketch, "E92.11.0.23", {"start": v(288, 0) * mm, "end": v(264, 0) * mm, "construction": true});
            skLineSegment(sketch, "E92.11.0.24", {"start": v(278.59, 6.59) * mm, "end": v(281.41, 9.41) * mm, "construction": true});
            skLineSegment(sketch, "E92.11.0.25", {"start": v(278.1, -7.07) * mm, "end": v(280.93, -9.9) * mm, "construction": true});
            skLineSegment(sketch, "E92.11.0.26", {"start": v(270.59, 9.41) * mm, "end": v(273.41, 6.59) * mm, "construction": true});
            skLineSegment(sketch, "E92.11.0.27", {"start": v(271.07, 9.9) * mm, "end": v(273.9, 7.07) * mm, "construction": true});
            skLineSegment(sketch, "E92.11.0.28", {"start": v(280.93, 9.9) * mm, "end": v(278.1, 7.07) * mm, "construction": true});
            skLineSegment(sketch, "E92.11.0.29", {"start": v(278.59, -6.59) * mm, "end": v(281.41, -9.41) * mm, "construction": true});
            skLineSegment(sketch, "E92.11.0.30", {"start": v(271.07, -9.9) * mm, "end": v(273.9, -7.07) * mm, "construction": true});
            skLineSegment(sketch, "E92.11.0.31", {"start": v(273.41, -6.59) * mm, "end": v(270.59, -9.41) * mm, "construction": true});
            skLineSegment(sketch, "E92.11.0.32", {"start": v(278.1, -7.07) * mm, "end": v(278.59, -6.59) * mm});
            skLineSegment(sketch, "E92.11.0.33", {"start": v(270.59, 9.41) * mm, "end": v(271.07, 9.9) * mm});
            skLineSegment(sketch, "E92.11.0.34", {"start": v(270.59, -9.41) * mm, "end": v(271.07, -9.9) * mm});
            skLineSegment(sketch, "E92.11.0.35", {"start": v(280.93, -9.9) * mm, "end": v(281.41, -9.41) * mm});
            skLineSegment(sketch, "E92.11.0.36", {"start": v(273.41, 6.59) * mm, "end": v(273.9, 7.07) * mm});
            skLineSegment(sketch, "E92.11.0.37", {"start": v(280.93, 9.9) * mm, "end": v(281.41, 9.41) * mm});
            skLineSegment(sketch, "E92.11.0.38", {"start": v(278.1, 7.07) * mm, "end": v(278.59, 6.59) * mm});
            skLineSegment(sketch, "E92.11.0.39", {"start": v(273.41, -6.59) * mm, "end": v(273.9, -7.07) * mm});
            skArc(sketch, "E92.12.0.0", {"start": v(294.59, 9.41) * mm, "mid": v(294.59, 6.59) * mm, "end": v(297.41, 6.59) * mm});
            skArc(sketch, "E92.12.0.1", {"start": v(297.41, -6.59) * mm, "mid": v(294.59, -6.59) * mm, "end": v(294.59, -9.41) * mm});
            skLineSegment(sketch, "E92.12.0.2", {"start": v(288, 24) * mm, "end": v(312, 24) * mm, "construction": true});
            skLineSegment(sketch, "E92.12.0.3", {"start": v(296, 16) * mm, "end": v(304, 16) * mm, "construction": true});
            skArc(sketch, "E92.12.0.4", {"start": v(295.07, -9.9) * mm, "mid": v(297.9, -9.9) * mm, "end": v(297.9, -7.07) * mm});
            skLineSegment(sketch, "E92.12.0.5", {"start": v(312, 0) * mm, "end": v(288, -24) * mm, "construction": true});
            skCircle(sketch, "E92.12.0.6", {"center": v(304, -16) * mm, "radius": 2 * mm});
            skLineSegment(sketch, "E92.12.0.7", {"start": v(312, -24) * mm, "end": v(288, -24) * mm, "construction": true});
            skCircle(sketch, "E92.12.0.8", {"center": v(296, 16) * mm, "radius": 2 * mm});
            skCircle(sketch, "E92.12.0.9", {"center": v(304, 16) * mm, "radius": 2 * mm});
            skLineSegment(sketch, "E92.12.0.10", {"start": v(312, -24) * mm, "end": v(288, 0) * mm, "construction": true});
            skLineSegment(sketch, "E92.12.0.11", {"start": v(288, 24) * mm, "end": v(312, 0) * mm, "construction": true});
            skLineSegment(sketch, "E92.12.0.12", {"start": v(312, 24) * mm, "end": v(288, 0) * mm, "construction": true});
            skArc(sketch, "E92.12.0.13", {"start": v(304.93, 9.9) * mm, "mid": v(302.1, 9.9) * mm, "end": v(302.1, 7.07) * mm});
            skArc(sketch, "E92.12.0.14", {"start": v(297.9, 7.07) * mm, "mid": v(297.9, 9.9) * mm, "end": v(295.07, 9.9) * mm});
            skArc(sketch, "E92.12.0.15", {"start": v(302.1, -7.07) * mm, "mid": v(302.1, -9.9) * mm, "end": v(304.93, -9.9) * mm});
            skArc(sketch, "E92.12.0.16", {"start": v(302.59, 6.59) * mm, "mid": v(305.41, 6.59) * mm, "end": v(305.41, 9.41) * mm});
            skLineSegment(sketch, "E92.12.0.17", {"start": v(296, -16) * mm, "end": v(304, -16) * mm, "construction": true});
            skLineSegment(sketch, "E92.12.0.18", {"start": v(288, 0) * mm, "end": v(312, 0) * mm, "construction": true});
            skArc(sketch, "E92.12.0.19", {"start": v(305.41, -9.41) * mm, "mid": v(305.41, -6.59) * mm, "end": v(302.59, -6.59) * mm});
            skCircle(sketch, "E92.12.0.20", {"center": v(296, -16) * mm, "radius": 2 * mm});
            skCircle(sketch, "E92.12.0.21", {"center": v(300, 0) * mm, "radius": 2 * mm});
            skPoint(sketch, "E92.12.0.22", {"position": v(296, -8) * mm});
            skLineSegment(sketch, "E92.12.0.23", {"start": v(312, 0) * mm, "end": v(288, 0) * mm, "construction": true});
            skLineSegment(sketch, "E92.12.0.24", {"start": v(302.59, 6.59) * mm, "end": v(305.41, 9.41) * mm, "construction": true});
            skLineSegment(sketch, "E92.12.0.25", {"start": v(302.1, -7.07) * mm, "end": v(304.93, -9.9) * mm, "construction": true});
            skLineSegment(sketch, "E92.12.0.26", {"start": v(294.59, 9.41) * mm, "end": v(297.41, 6.59) * mm, "construction": true});
            skLineSegment(sketch, "E92.12.0.27", {"start": v(295.07, 9.9) * mm, "end": v(297.9, 7.07) * mm, "construction": true});
            skLineSegment(sketch, "E92.12.0.28", {"start": v(304.93, 9.9) * mm, "end": v(302.1, 7.07) * mm, "construction": true});
            skLineSegment(sketch, "E92.12.0.29", {"start": v(302.59, -6.59) * mm, "end": v(305.41, -9.41) * mm, "construction": true});
            skLineSegment(sketch, "E92.12.0.30", {"start": v(295.07, -9.9) * mm, "end": v(297.9, -7.07) * mm, "construction": true});
            skLineSegment(sketch, "E92.12.0.31", {"start": v(297.41, -6.59) * mm, "end": v(294.59, -9.41) * mm, "construction": true});
            skLineSegment(sketch, "E92.12.0.32", {"start": v(302.1, -7.07) * mm, "end": v(302.59, -6.59) * mm});
            skLineSegment(sketch, "E92.12.0.33", {"start": v(294.59, 9.41) * mm, "end": v(295.07, 9.9) * mm});
            skLineSegment(sketch, "E92.12.0.34", {"start": v(294.59, -9.41) * mm, "end": v(295.07, -9.9) * mm});
            skLineSegment(sketch, "E92.12.0.35", {"start": v(304.93, -9.9) * mm, "end": v(305.41, -9.41) * mm});
            skLineSegment(sketch, "E92.12.0.36", {"start": v(297.41, 6.59) * mm, "end": v(297.9, 7.07) * mm});
            skLineSegment(sketch, "E92.12.0.37", {"start": v(304.93, 9.9) * mm, "end": v(305.41, 9.41) * mm});
            skLineSegment(sketch, "E92.12.0.38", {"start": v(302.1, 7.07) * mm, "end": v(302.59, 6.59) * mm});
            skLineSegment(sketch, "E92.12.0.39", {"start": v(297.41, -6.59) * mm, "end": v(297.9, -7.07) * mm});
            skArc(sketch, "E92.13.0.0", {"start": v(318.59, 9.41) * mm, "mid": v(318.59, 6.59) * mm, "end": v(321.41, 6.59) * mm});
            skArc(sketch, "E92.13.0.1", {"start": v(321.41, -6.59) * mm, "mid": v(318.59, -6.59) * mm, "end": v(318.59, -9.41) * mm});
            skLineSegment(sketch, "E92.13.0.2", {"start": v(312, 24) * mm, "end": v(336, 24) * mm, "construction": true});
            skLineSegment(sketch, "E92.13.0.3", {"start": v(320, 16) * mm, "end": v(328, 16) * mm, "construction": true});
            skArc(sketch, "E92.13.0.4", {"start": v(319.07, -9.9) * mm, "mid": v(321.9, -9.9) * mm, "end": v(321.9, -7.07) * mm});
            skLineSegment(sketch, "E92.13.0.5", {"start": v(336, 0) * mm, "end": v(312, -24) * mm, "construction": true});
            skCircle(sketch, "E92.13.0.6", {"center": v(328, -16) * mm, "radius": 2 * mm});
            skLineSegment(sketch, "E92.13.0.7", {"start": v(336, -24) * mm, "end": v(312, -24) * mm, "construction": true});
            skCircle(sketch, "E92.13.0.8", {"center": v(320, 16) * mm, "radius": 2 * mm});
            skCircle(sketch, "E92.13.0.9", {"center": v(328, 16) * mm, "radius": 2 * mm});
            skLineSegment(sketch, "E92.13.0.10", {"start": v(336, -24) * mm, "end": v(312, 0) * mm, "construction": true});
            skLineSegment(sketch, "E92.13.0.11", {"start": v(312, 24) * mm, "end": v(336, 0) * mm, "construction": true});
            skLineSegment(sketch, "E92.13.0.12", {"start": v(336, 24) * mm, "end": v(312, 0) * mm, "construction": true});
            skArc(sketch, "E92.13.0.13", {"start": v(328.93, 9.9) * mm, "mid": v(326.1, 9.9) * mm, "end": v(326.1, 7.07) * mm});
            skArc(sketch, "E92.13.0.14", {"start": v(321.9, 7.07) * mm, "mid": v(321.9, 9.9) * mm, "end": v(319.07, 9.9) * mm});
            skArc(sketch, "E92.13.0.15", {"start": v(326.1, -7.07) * mm, "mid": v(326.1, -9.9) * mm, "end": v(328.93, -9.9) * mm});
            skArc(sketch, "E92.13.0.16", {"start": v(326.59, 6.59) * mm, "mid": v(329.41, 6.59) * mm, "end": v(329.41, 9.41) * mm});
            skLineSegment(sketch, "E92.13.0.17", {"start": v(320, -16) * mm, "end": v(328, -16) * mm, "construction": true});
            skLineSegment(sketch, "E92.13.0.18", {"start": v(312, 0) * mm, "end": v(336, 0) * mm, "construction": true});
            skArc(sketch, "E92.13.0.19", {"start": v(329.41, -9.41) * mm, "mid": v(329.41, -6.59) * mm, "end": v(326.59, -6.59) * mm});
            skCircle(sketch, "E92.13.0.20", {"center": v(320, -16) * mm, "radius": 2 * mm});
            skCircle(sketch, "E92.13.0.21", {"center": v(324, 0) * mm, "radius": 2 * mm});
            skPoint(sketch, "E92.13.0.22", {"position": v(320, -8) * mm});
            skLineSegment(sketch, "E92.13.0.23", {"start": v(336, 0) * mm, "end": v(312, 0) * mm, "construction": true});
            skLineSegment(sketch, "E92.13.0.24", {"start": v(326.59, 6.59) * mm, "end": v(329.41, 9.41) * mm, "construction": true});
            skLineSegment(sketch, "E92.13.0.25", {"start": v(326.1, -7.07) * mm, "end": v(328.93, -9.9) * mm, "construction": true});
            skLineSegment(sketch, "E92.13.0.26", {"start": v(318.59, 9.41) * mm, "end": v(321.41, 6.59) * mm, "construction": true});
            skLineSegment(sketch, "E92.13.0.27", {"start": v(319.07, 9.9) * mm, "end": v(321.9, 7.07) * mm, "construction": true});
            skLineSegment(sketch, "E92.13.0.28", {"start": v(328.93, 9.9) * mm, "end": v(326.1, 7.07) * mm, "construction": true});
            skLineSegment(sketch, "E92.13.0.29", {"start": v(326.59, -6.59) * mm, "end": v(329.41, -9.41) * mm, "construction": true});
            skLineSegment(sketch, "E92.13.0.30", {"start": v(319.07, -9.9) * mm, "end": v(321.9, -7.07) * mm, "construction": true});
            skLineSegment(sketch, "E92.13.0.31", {"start": v(321.41, -6.59) * mm, "end": v(318.59, -9.41) * mm, "construction": true});
            skLineSegment(sketch, "E92.13.0.32", {"start": v(326.1, -7.07) * mm, "end": v(326.59, -6.59) * mm});
            skLineSegment(sketch, "E92.13.0.33", {"start": v(318.59, 9.41) * mm, "end": v(319.07, 9.9) * mm});
            skLineSegment(sketch, "E92.13.0.34", {"start": v(318.59, -9.41) * mm, "end": v(319.07, -9.9) * mm});
            skLineSegment(sketch, "E92.13.0.35", {"start": v(328.93, -9.9) * mm, "end": v(329.41, -9.41) * mm});
            skLineSegment(sketch, "E92.13.0.36", {"start": v(321.41, 6.59) * mm, "end": v(321.9, 7.07) * mm});
            skLineSegment(sketch, "E92.13.0.37", {"start": v(328.93, 9.9) * mm, "end": v(329.41, 9.41) * mm});
            skLineSegment(sketch, "E92.13.0.38", {"start": v(326.1, 7.07) * mm, "end": v(326.59, 6.59) * mm});
            skLineSegment(sketch, "E92.13.0.39", {"start": v(321.41, -6.59) * mm, "end": v(321.9, -7.07) * mm});
            skArc(sketch, "E92.14.0.0", {"start": v(342.59, 9.41) * mm, "mid": v(342.59, 6.59) * mm, "end": v(345.41, 6.59) * mm});
            skArc(sketch, "E92.14.0.1", {"start": v(345.41, -6.59) * mm, "mid": v(342.59, -6.59) * mm, "end": v(342.59, -9.41) * mm});
            skLineSegment(sketch, "E92.14.0.2", {"start": v(336, 24) * mm, "end": v(360, 24) * mm, "construction": true});
            skLineSegment(sketch, "E92.14.0.3", {"start": v(344, 16) * mm, "end": v(352, 16) * mm, "construction": true});
            skArc(sketch, "E92.14.0.4", {"start": v(343.07, -9.9) * mm, "mid": v(345.9, -9.9) * mm, "end": v(345.9, -7.07) * mm});
            skLineSegment(sketch, "E92.14.0.5", {"start": v(360, 0) * mm, "end": v(336, -24) * mm, "construction": true});
            skCircle(sketch, "E92.14.0.6", {"center": v(352, -16) * mm, "radius": 2 * mm});
            skLineSegment(sketch, "E92.14.0.7", {"start": v(360, -24) * mm, "end": v(336, -24) * mm, "construction": true});
            skCircle(sketch, "E92.14.0.8", {"center": v(344, 16) * mm, "radius": 2 * mm});
            skCircle(sketch, "E92.14.0.9", {"center": v(352, 16) * mm, "radius": 2 * mm});
            skLineSegment(sketch, "E92.14.0.10", {"start": v(360, -24) * mm, "end": v(336, 0) * mm, "construction": true});
            skLineSegment(sketch, "E92.14.0.11", {"start": v(336, 24) * mm, "end": v(360, 0) * mm, "construction": true});
            skLineSegment(sketch, "E92.14.0.12", {"start": v(360, 24) * mm, "end": v(336, 0) * mm, "construction": true});
            skArc(sketch, "E92.14.0.13", {"start": v(352.93, 9.9) * mm, "mid": v(350.1, 9.9) * mm, "end": v(350.1, 7.07) * mm});
            skArc(sketch, "E92.14.0.14", {"start": v(345.9, 7.07) * mm, "mid": v(345.9, 9.9) * mm, "end": v(343.07, 9.9) * mm});
            skArc(sketch, "E92.14.0.15", {"start": v(350.1, -7.07) * mm, "mid": v(350.1, -9.9) * mm, "end": v(352.93, -9.9) * mm});
            skArc(sketch, "E92.14.0.16", {"start": v(350.59, 6.59) * mm, "mid": v(353.41, 6.59) * mm, "end": v(353.41, 9.41) * mm});
            skLineSegment(sketch, "E92.14.0.17", {"start": v(344, -16) * mm, "end": v(352, -16) * mm, "construction": true});
            skLineSegment(sketch, "E92.14.0.18", {"start": v(336, 0) * mm, "end": v(360, 0) * mm, "construction": true});
            skArc(sketch, "E92.14.0.19", {"start": v(353.41, -9.41) * mm, "mid": v(353.41, -6.59) * mm, "end": v(350.59, -6.59) * mm});
            skCircle(sketch, "E92.14.0.20", {"center": v(344, -16) * mm, "radius": 2 * mm});
            skCircle(sketch, "E92.14.0.21", {"center": v(348, 0) * mm, "radius": 2 * mm});
            skPoint(sketch, "E92.14.0.22", {"position": v(344, -8) * mm});
            skLineSegment(sketch, "E92.14.0.23", {"start": v(360, 0) * mm, "end": v(336, 0) * mm, "construction": true});
            skLineSegment(sketch, "E92.14.0.24", {"start": v(350.59, 6.59) * mm, "end": v(353.41, 9.41) * mm, "construction": true});
            skLineSegment(sketch, "E92.14.0.25", {"start": v(350.1, -7.07) * mm, "end": v(352.93, -9.9) * mm, "construction": true});
            skLineSegment(sketch, "E92.14.0.26", {"start": v(342.59, 9.41) * mm, "end": v(345.41, 6.59) * mm, "construction": true});
            skLineSegment(sketch, "E92.14.0.27", {"start": v(343.07, 9.9) * mm, "end": v(345.9, 7.07) * mm, "construction": true});
            skLineSegment(sketch, "E92.14.0.28", {"start": v(352.93, 9.9) * mm, "end": v(350.1, 7.07) * mm, "construction": true});
            skLineSegment(sketch, "E92.14.0.29", {"start": v(350.59, -6.59) * mm, "end": v(353.41, -9.41) * mm, "construction": true});
            skLineSegment(sketch, "E92.14.0.30", {"start": v(343.07, -9.9) * mm, "end": v(345.9, -7.07) * mm, "construction": true});
            skLineSegment(sketch, "E92.14.0.31", {"start": v(345.41, -6.59) * mm, "end": v(342.59, -9.41) * mm, "construction": true});
            skLineSegment(sketch, "E92.14.0.32", {"start": v(350.1, -7.07) * mm, "end": v(350.59, -6.59) * mm});
            skLineSegment(sketch, "E92.14.0.33", {"start": v(342.59, 9.41) * mm, "end": v(343.07, 9.9) * mm});
            skLineSegment(sketch, "E92.14.0.34", {"start": v(342.59, -9.41) * mm, "end": v(343.07, -9.9) * mm});
            skLineSegment(sketch, "E92.14.0.35", {"start": v(352.93, -9.9) * mm, "end": v(353.41, -9.41) * mm});
            skLineSegment(sketch, "E92.14.0.36", {"start": v(345.41, 6.59) * mm, "end": v(345.9, 7.07) * mm});
            skLineSegment(sketch, "E92.14.0.37", {"start": v(352.93, 9.9) * mm, "end": v(353.41, 9.41) * mm});
            skLineSegment(sketch, "E92.14.0.38", {"start": v(350.1, 7.07) * mm, "end": v(350.59, 6.59) * mm});
            skLineSegment(sketch, "E92.14.0.39", {"start": v(345.41, -6.59) * mm, "end": v(345.9, -7.07) * mm});
            skArc(sketch, "E92.15.0.0", {"start": v(366.59, 9.41) * mm, "mid": v(366.59, 6.59) * mm, "end": v(369.41, 6.59) * mm});
            skArc(sketch, "E92.15.0.1", {"start": v(369.41, -6.59) * mm, "mid": v(366.59, -6.59) * mm, "end": v(366.59, -9.41) * mm});
            skLineSegment(sketch, "E92.15.0.2", {"start": v(360, 24) * mm, "end": v(384, 24) * mm, "construction": true});
            skLineSegment(sketch, "E92.15.0.3", {"start": v(368, 16) * mm, "end": v(376, 16) * mm, "construction": true});
            skArc(sketch, "E92.15.0.4", {"start": v(367.07, -9.9) * mm, "mid": v(369.9, -9.9) * mm, "end": v(369.9, -7.07) * mm});
            skLineSegment(sketch, "E92.15.0.5", {"start": v(384, 0) * mm, "end": v(360, -24) * mm, "construction": true});
            skCircle(sketch, "E92.15.0.6", {"center": v(376, -16) * mm, "radius": 2 * mm});
            skLineSegment(sketch, "E92.15.0.7", {"start": v(384, -24) * mm, "end": v(360, -24) * mm, "construction": true});
            skCircle(sketch, "E92.15.0.8", {"center": v(368, 16) * mm, "radius": 2 * mm});
            skCircle(sketch, "E92.15.0.9", {"center": v(376, 16) * mm, "radius": 2 * mm});
            skLineSegment(sketch, "E92.15.0.10", {"start": v(384, -24) * mm, "end": v(360, 0) * mm, "construction": true});
            skLineSegment(sketch, "E92.15.0.11", {"start": v(360, 24) * mm, "end": v(384, 0) * mm, "construction": true});
            skLineSegment(sketch, "E92.15.0.12", {"start": v(384, 24) * mm, "end": v(360, 0) * mm, "construction": true});
            skArc(sketch, "E92.15.0.13", {"start": v(376.93, 9.9) * mm, "mid": v(374.1, 9.9) * mm, "end": v(374.1, 7.07) * mm});
            skArc(sketch, "E92.15.0.14", {"start": v(369.9, 7.07) * mm, "mid": v(369.9, 9.9) * mm, "end": v(367.07, 9.9) * mm});
            skArc(sketch, "E92.15.0.15", {"start": v(374.1, -7.07) * mm, "mid": v(374.1, -9.9) * mm, "end": v(376.93, -9.9) * mm});
            skArc(sketch, "E92.15.0.16", {"start": v(374.59, 6.59) * mm, "mid": v(377.41, 6.59) * mm, "end": v(377.41, 9.41) * mm});
            skLineSegment(sketch, "E92.15.0.17", {"start": v(368, -16) * mm, "end": v(376, -16) * mm, "construction": true});
            skLineSegment(sketch, "E92.15.0.18", {"start": v(360, 0) * mm, "end": v(384, 0) * mm, "construction": true});
            skArc(sketch, "E92.15.0.19", {"start": v(377.41, -9.41) * mm, "mid": v(377.41, -6.59) * mm, "end": v(374.59, -6.59) * mm});
            skCircle(sketch, "E92.15.0.20", {"center": v(368, -16) * mm, "radius": 2 * mm});
            skCircle(sketch, "E92.15.0.21", {"center": v(372, 0) * mm, "radius": 2 * mm});
            skPoint(sketch, "E92.15.0.22", {"position": v(368, -8) * mm});
            skLineSegment(sketch, "E92.15.0.23", {"start": v(384, 0) * mm, "end": v(360, 0) * mm, "construction": true});
            skLineSegment(sketch, "E92.15.0.24", {"start": v(374.59, 6.59) * mm, "end": v(377.41, 9.41) * mm, "construction": true});
            skLineSegment(sketch, "E92.15.0.25", {"start": v(374.1, -7.07) * mm, "end": v(376.93, -9.9) * mm, "construction": true});
            skLineSegment(sketch, "E92.15.0.26", {"start": v(366.59, 9.41) * mm, "end": v(369.41, 6.59) * mm, "construction": true});
            skLineSegment(sketch, "E92.15.0.27", {"start": v(367.07, 9.9) * mm, "end": v(369.9, 7.07) * mm, "construction": true});
            skLineSegment(sketch, "E92.15.0.28", {"start": v(376.93, 9.9) * mm, "end": v(374.1, 7.07) * mm, "construction": true});
            skLineSegment(sketch, "E92.15.0.29", {"start": v(374.59, -6.59) * mm, "end": v(377.41, -9.41) * mm, "construction": true});
            skLineSegment(sketch, "E92.15.0.30", {"start": v(367.07, -9.9) * mm, "end": v(369.9, -7.07) * mm, "construction": true});
            skLineSegment(sketch, "E92.15.0.31", {"start": v(369.41, -6.59) * mm, "end": v(366.59, -9.41) * mm, "construction": true});
            skLineSegment(sketch, "E92.15.0.32", {"start": v(374.1, -7.07) * mm, "end": v(374.59, -6.59) * mm});
            skLineSegment(sketch, "E92.15.0.33", {"start": v(366.59, 9.41) * mm, "end": v(367.07, 9.9) * mm});
            skLineSegment(sketch, "E92.15.0.34", {"start": v(366.59, -9.41) * mm, "end": v(367.07, -9.9) * mm});
            skLineSegment(sketch, "E92.15.0.35", {"start": v(376.93, -9.9) * mm, "end": v(377.41, -9.41) * mm});
            skLineSegment(sketch, "E92.15.0.36", {"start": v(369.41, 6.59) * mm, "end": v(369.9, 7.07) * mm});
            skLineSegment(sketch, "E92.15.0.37", {"start": v(376.93, 9.9) * mm, "end": v(377.41, 9.41) * mm});
            skLineSegment(sketch, "E92.15.0.38", {"start": v(374.1, 7.07) * mm, "end": v(374.59, 6.59) * mm});
            skLineSegment(sketch, "E92.15.0.39", {"start": v(369.41, -6.59) * mm, "end": v(369.9, -7.07) * mm});
            skArc(sketch, "E92.16.0.0", {"start": v(390.59, 9.41) * mm, "mid": v(390.59, 6.59) * mm, "end": v(393.41, 6.59) * mm});
            skArc(sketch, "E92.16.0.1", {"start": v(393.41, -6.59) * mm, "mid": v(390.59, -6.59) * mm, "end": v(390.59, -9.41) * mm});
            skLineSegment(sketch, "E92.16.0.2", {"start": v(384, 24) * mm, "end": v(408, 24) * mm, "construction": true});
            skLineSegment(sketch, "E92.16.0.3", {"start": v(392, 16) * mm, "end": v(400, 16) * mm, "construction": true});
            skArc(sketch, "E92.16.0.4", {"start": v(391.07, -9.9) * mm, "mid": v(393.9, -9.9) * mm, "end": v(393.9, -7.07) * mm});
            skLineSegment(sketch, "E92.16.0.5", {"start": v(408, 0) * mm, "end": v(384, -24) * mm, "construction": true});
            skCircle(sketch, "E92.16.0.6", {"center": v(400, -16) * mm, "radius": 2 * mm});
            skLineSegment(sketch, "E92.16.0.7", {"start": v(408, -24) * mm, "end": v(384, -24) * mm, "construction": true});
            skCircle(sketch, "E92.16.0.8", {"center": v(392, 16) * mm, "radius": 2 * mm});
            skCircle(sketch, "E92.16.0.9", {"center": v(400, 16) * mm, "radius": 2 * mm});
            skLineSegment(sketch, "E92.16.0.10", {"start": v(408, -24) * mm, "end": v(384, 0) * mm, "construction": true});
            skLineSegment(sketch, "E92.16.0.11", {"start": v(384, 24) * mm, "end": v(408, 0) * mm, "construction": true});
            skLineSegment(sketch, "E92.16.0.12", {"start": v(408, 24) * mm, "end": v(384, 0) * mm, "construction": true});
            skArc(sketch, "E92.16.0.13", {"start": v(400.93, 9.9) * mm, "mid": v(398.1, 9.9) * mm, "end": v(398.1, 7.07) * mm});
            skArc(sketch, "E92.16.0.14", {"start": v(393.9, 7.07) * mm, "mid": v(393.9, 9.9) * mm, "end": v(391.07, 9.9) * mm});
            skArc(sketch, "E92.16.0.15", {"start": v(398.1, -7.07) * mm, "mid": v(398.1, -9.9) * mm, "end": v(400.93, -9.9) * mm});
            skArc(sketch, "E92.16.0.16", {"start": v(398.59, 6.59) * mm, "mid": v(401.41, 6.59) * mm, "end": v(401.41, 9.41) * mm});
            skLineSegment(sketch, "E92.16.0.17", {"start": v(392, -16) * mm, "end": v(400, -16) * mm, "construction": true});
            skLineSegment(sketch, "E92.16.0.18", {"start": v(384, 0) * mm, "end": v(408, 0) * mm, "construction": true});
            skArc(sketch, "E92.16.0.19", {"start": v(401.41, -9.41) * mm, "mid": v(401.41, -6.59) * mm, "end": v(398.59, -6.59) * mm});
            skCircle(sketch, "E92.16.0.20", {"center": v(392, -16) * mm, "radius": 2 * mm});
            skCircle(sketch, "E92.16.0.21", {"center": v(396, 0) * mm, "radius": 2 * mm});
            skPoint(sketch, "E92.16.0.22", {"position": v(392, -8) * mm});
            skLineSegment(sketch, "E92.16.0.23", {"start": v(408, 0) * mm, "end": v(384, 0) * mm, "construction": true});
            skLineSegment(sketch, "E92.16.0.24", {"start": v(398.59, 6.59) * mm, "end": v(401.41, 9.41) * mm, "construction": true});
            skLineSegment(sketch, "E92.16.0.25", {"start": v(398.1, -7.07) * mm, "end": v(400.93, -9.9) * mm, "construction": true});
            skLineSegment(sketch, "E92.16.0.26", {"start": v(390.59, 9.41) * mm, "end": v(393.41, 6.59) * mm, "construction": true});
            skLineSegment(sketch, "E92.16.0.27", {"start": v(391.07, 9.9) * mm, "end": v(393.9, 7.07) * mm, "construction": true});
            skLineSegment(sketch, "E92.16.0.28", {"start": v(400.93, 9.9) * mm, "end": v(398.1, 7.07) * mm, "construction": true});
            skLineSegment(sketch, "E92.16.0.29", {"start": v(398.59, -6.59) * mm, "end": v(401.41, -9.41) * mm, "construction": true});
            skLineSegment(sketch, "E92.16.0.30", {"start": v(391.07, -9.9) * mm, "end": v(393.9, -7.07) * mm, "construction": true});
            skLineSegment(sketch, "E92.16.0.31", {"start": v(393.41, -6.59) * mm, "end": v(390.59, -9.41) * mm, "construction": true});
            skLineSegment(sketch, "E92.16.0.32", {"start": v(398.1, -7.07) * mm, "end": v(398.59, -6.59) * mm});
            skLineSegment(sketch, "E92.16.0.33", {"start": v(390.59, 9.41) * mm, "end": v(391.07, 9.9) * mm});
            skLineSegment(sketch, "E92.16.0.34", {"start": v(390.59, -9.41) * mm, "end": v(391.07, -9.9) * mm});
            skLineSegment(sketch, "E92.16.0.35", {"start": v(400.93, -9.9) * mm, "end": v(401.41, -9.41) * mm});
            skLineSegment(sketch, "E92.16.0.36", {"start": v(393.41, 6.59) * mm, "end": v(393.9, 7.07) * mm});
            skLineSegment(sketch, "E92.16.0.37", {"start": v(400.93, 9.9) * mm, "end": v(401.41, 9.41) * mm});
            skLineSegment(sketch, "E92.16.0.38", {"start": v(398.1, 7.07) * mm, "end": v(398.59, 6.59) * mm});
            skLineSegment(sketch, "E92.16.0.39", {"start": v(393.41, -6.59) * mm, "end": v(393.9, -7.07) * mm});
            skArc(sketch, "E92.17.0.0", {"start": v(414.59, 9.41) * mm, "mid": v(414.59, 6.59) * mm, "end": v(417.41, 6.59) * mm});
            skArc(sketch, "E92.17.0.1", {"start": v(417.41, -6.59) * mm, "mid": v(414.59, -6.59) * mm, "end": v(414.59, -9.41) * mm});
            skLineSegment(sketch, "E92.17.0.2", {"start": v(408, 24) * mm, "end": v(432, 24) * mm, "construction": true});
            skLineSegment(sketch, "E92.17.0.3", {"start": v(416, 16) * mm, "end": v(424, 16) * mm, "construction": true});
            skArc(sketch, "E92.17.0.4", {"start": v(415.07, -9.9) * mm, "mid": v(417.9, -9.9) * mm, "end": v(417.9, -7.07) * mm});
            skLineSegment(sketch, "E92.17.0.5", {"start": v(432, 0) * mm, "end": v(408, -24) * mm, "construction": true});
            skCircle(sketch, "E92.17.0.6", {"center": v(424, -16) * mm, "radius": 2 * mm});
            skLineSegment(sketch, "E92.17.0.7", {"start": v(432, -24) * mm, "end": v(408, -24) * mm, "construction": true});
            skCircle(sketch, "E92.17.0.8", {"center": v(416, 16) * mm, "radius": 2 * mm});
            skCircle(sketch, "E92.17.0.9", {"center": v(424, 16) * mm, "radius": 2 * mm});
            skLineSegment(sketch, "E92.17.0.10", {"start": v(432, -24) * mm, "end": v(408, 0) * mm, "construction": true});
            skLineSegment(sketch, "E92.17.0.11", {"start": v(408, 24) * mm, "end": v(432, 0) * mm, "construction": true});
            skLineSegment(sketch, "E92.17.0.12", {"start": v(432, 24) * mm, "end": v(408, 0) * mm, "construction": true});
            skArc(sketch, "E92.17.0.13", {"start": v(424.93, 9.9) * mm, "mid": v(422.1, 9.9) * mm, "end": v(422.1, 7.07) * mm});
            skArc(sketch, "E92.17.0.14", {"start": v(417.9, 7.07) * mm, "mid": v(417.9, 9.9) * mm, "end": v(415.07, 9.9) * mm});
            skArc(sketch, "E92.17.0.15", {"start": v(422.1, -7.07) * mm, "mid": v(422.1, -9.9) * mm, "end": v(424.93, -9.9) * mm});
            skArc(sketch, "E92.17.0.16", {"start": v(422.59, 6.59) * mm, "mid": v(425.41, 6.59) * mm, "end": v(425.41, 9.41) * mm});
            skLineSegment(sketch, "E92.17.0.17", {"start": v(416, -16) * mm, "end": v(424, -16) * mm, "construction": true});
            skLineSegment(sketch, "E92.17.0.18", {"start": v(408, 0) * mm, "end": v(432, 0) * mm, "construction": true});
            skArc(sketch, "E92.17.0.19", {"start": v(425.41, -9.41) * mm, "mid": v(425.41, -6.59) * mm, "end": v(422.59, -6.59) * mm});
            skCircle(sketch, "E92.17.0.20", {"center": v(416, -16) * mm, "radius": 2 * mm});
            skCircle(sketch, "E92.17.0.21", {"center": v(420, 0) * mm, "radius": 2 * mm});
            skPoint(sketch, "E92.17.0.22", {"position": v(416, -8) * mm});
            skLineSegment(sketch, "E92.17.0.23", {"start": v(432, 0) * mm, "end": v(408, 0) * mm, "construction": true});
            skLineSegment(sketch, "E92.17.0.24", {"start": v(422.59, 6.59) * mm, "end": v(425.41, 9.41) * mm, "construction": true});
            skLineSegment(sketch, "E92.17.0.25", {"start": v(422.1, -7.07) * mm, "end": v(424.93, -9.9) * mm, "construction": true});
            skLineSegment(sketch, "E92.17.0.26", {"start": v(414.59, 9.41) * mm, "end": v(417.41, 6.59) * mm, "construction": true});
            skLineSegment(sketch, "E92.17.0.27", {"start": v(415.07, 9.9) * mm, "end": v(417.9, 7.07) * mm, "construction": true});
            skLineSegment(sketch, "E92.17.0.28", {"start": v(424.93, 9.9) * mm, "end": v(422.1, 7.07) * mm, "construction": true});
            skLineSegment(sketch, "E92.17.0.29", {"start": v(422.59, -6.59) * mm, "end": v(425.41, -9.41) * mm, "construction": true});
            skLineSegment(sketch, "E92.17.0.30", {"start": v(415.07, -9.9) * mm, "end": v(417.9, -7.07) * mm, "construction": true});
            skLineSegment(sketch, "E92.17.0.31", {"start": v(417.41, -6.59) * mm, "end": v(414.59, -9.41) * mm, "construction": true});
            skLineSegment(sketch, "E92.17.0.32", {"start": v(422.1, -7.07) * mm, "end": v(422.59, -6.59) * mm});
            skLineSegment(sketch, "E92.17.0.33", {"start": v(414.59, 9.41) * mm, "end": v(415.07, 9.9) * mm});
            skLineSegment(sketch, "E92.17.0.34", {"start": v(414.59, -9.41) * mm, "end": v(415.07, -9.9) * mm});
            skLineSegment(sketch, "E92.17.0.35", {"start": v(424.93, -9.9) * mm, "end": v(425.41, -9.41) * mm});
            skLineSegment(sketch, "E92.17.0.36", {"start": v(417.41, 6.59) * mm, "end": v(417.9, 7.07) * mm});
            skLineSegment(sketch, "E92.17.0.37", {"start": v(424.93, 9.9) * mm, "end": v(425.41, 9.41) * mm});
            skLineSegment(sketch, "E92.17.0.38", {"start": v(422.1, 7.07) * mm, "end": v(422.59, 6.59) * mm});
            skLineSegment(sketch, "E92.17.0.39", {"start": v(417.41, -6.59) * mm, "end": v(417.9, -7.07) * mm});
            skArc(sketch, "E92.18.0.0", {"start": v(438.59, 9.41) * mm, "mid": v(438.59, 6.59) * mm, "end": v(441.41, 6.59) * mm});
            skArc(sketch, "E92.18.0.1", {"start": v(441.41, -6.59) * mm, "mid": v(438.59, -6.59) * mm, "end": v(438.59, -9.41) * mm});
            skLineSegment(sketch, "E92.18.0.2", {"start": v(432, 24) * mm, "end": v(456, 24) * mm, "construction": true});
            skLineSegment(sketch, "E92.18.0.3", {"start": v(440, 16) * mm, "end": v(448, 16) * mm, "construction": true});
            skArc(sketch, "E92.18.0.4", {"start": v(439.07, -9.9) * mm, "mid": v(441.9, -9.9) * mm, "end": v(441.9, -7.07) * mm});
            skLineSegment(sketch, "E92.18.0.5", {"start": v(456, 0) * mm, "end": v(432, -24) * mm, "construction": true});
            skCircle(sketch, "E92.18.0.6", {"center": v(448, -16) * mm, "radius": 2 * mm});
            skLineSegment(sketch, "E92.18.0.7", {"start": v(456, -24) * mm, "end": v(432, -24) * mm, "construction": true});
            skCircle(sketch, "E92.18.0.8", {"center": v(440, 16) * mm, "radius": 2 * mm});
            skCircle(sketch, "E92.18.0.9", {"center": v(448, 16) * mm, "radius": 2 * mm});
            skLineSegment(sketch, "E92.18.0.10", {"start": v(456, -24) * mm, "end": v(432, 0) * mm, "construction": true});
            skLineSegment(sketch, "E92.18.0.11", {"start": v(432, 24) * mm, "end": v(456, 0) * mm, "construction": true});
            skLineSegment(sketch, "E92.18.0.12", {"start": v(456, 24) * mm, "end": v(432, 0) * mm, "construction": true});
            skArc(sketch, "E92.18.0.13", {"start": v(448.93, 9.9) * mm, "mid": v(446.1, 9.9) * mm, "end": v(446.1, 7.07) * mm});
            skArc(sketch, "E92.18.0.14", {"start": v(441.9, 7.07) * mm, "mid": v(441.9, 9.9) * mm, "end": v(439.07, 9.9) * mm});
            skArc(sketch, "E92.18.0.15", {"start": v(446.1, -7.07) * mm, "mid": v(446.1, -9.9) * mm, "end": v(448.93, -9.9) * mm});
            skArc(sketch, "E92.18.0.16", {"start": v(446.59, 6.59) * mm, "mid": v(449.41, 6.59) * mm, "end": v(449.41, 9.41) * mm});
            skLineSegment(sketch, "E92.18.0.17", {"start": v(440, -16) * mm, "end": v(448, -16) * mm, "construction": true});
            skLineSegment(sketch, "E92.18.0.18", {"start": v(432, 0) * mm, "end": v(456, 0) * mm, "construction": true});
            skArc(sketch, "E92.18.0.19", {"start": v(449.41, -9.41) * mm, "mid": v(449.41, -6.59) * mm, "end": v(446.59, -6.59) * mm});
            skCircle(sketch, "E92.18.0.20", {"center": v(440, -16) * mm, "radius": 2 * mm});
            skCircle(sketch, "E92.18.0.21", {"center": v(444, 0) * mm, "radius": 2 * mm});
            skPoint(sketch, "E92.18.0.22", {"position": v(440, -8) * mm});
            skLineSegment(sketch, "E92.18.0.23", {"start": v(456, 0) * mm, "end": v(432, 0) * mm, "construction": true});
            skLineSegment(sketch, "E92.18.0.24", {"start": v(446.59, 6.59) * mm, "end": v(449.41, 9.41) * mm, "construction": true});
            skLineSegment(sketch, "E92.18.0.25", {"start": v(446.1, -7.07) * mm, "end": v(448.93, -9.9) * mm, "construction": true});
            skLineSegment(sketch, "E92.18.0.26", {"start": v(438.59, 9.41) * mm, "end": v(441.41, 6.59) * mm, "construction": true});
            skLineSegment(sketch, "E92.18.0.27", {"start": v(439.07, 9.9) * mm, "end": v(441.9, 7.07) * mm, "construction": true});
            skLineSegment(sketch, "E92.18.0.28", {"start": v(448.93, 9.9) * mm, "end": v(446.1, 7.07) * mm, "construction": true});
            skLineSegment(sketch, "E92.18.0.29", {"start": v(446.59, -6.59) * mm, "end": v(449.41, -9.41) * mm, "construction": true});
            skLineSegment(sketch, "E92.18.0.30", {"start": v(439.07, -9.9) * mm, "end": v(441.9, -7.07) * mm, "construction": true});
            skLineSegment(sketch, "E92.18.0.31", {"start": v(441.41, -6.59) * mm, "end": v(438.59, -9.41) * mm, "construction": true});
            skLineSegment(sketch, "E92.18.0.32", {"start": v(446.1, -7.07) * mm, "end": v(446.59, -6.59) * mm});
            skLineSegment(sketch, "E92.18.0.33", {"start": v(438.59, 9.41) * mm, "end": v(439.07, 9.9) * mm});
            skLineSegment(sketch, "E92.18.0.34", {"start": v(438.59, -9.41) * mm, "end": v(439.07, -9.9) * mm});
            skLineSegment(sketch, "E92.18.0.35", {"start": v(448.93, -9.9) * mm, "end": v(449.41, -9.41) * mm});
            skLineSegment(sketch, "E92.18.0.36", {"start": v(441.41, 6.59) * mm, "end": v(441.9, 7.07) * mm});
            skLineSegment(sketch, "E92.18.0.37", {"start": v(448.93, 9.9) * mm, "end": v(449.41, 9.41) * mm});
            skLineSegment(sketch, "E92.18.0.38", {"start": v(446.1, 7.07) * mm, "end": v(446.59, 6.59) * mm});
            skLineSegment(sketch, "E92.18.0.39", {"start": v(441.41, -6.59) * mm, "end": v(441.9, -7.07) * mm});
            skArc(sketch, "E92.19.0.0", {"start": v(462.59, 9.41) * mm, "mid": v(462.59, 6.59) * mm, "end": v(465.41, 6.59) * mm});
            skArc(sketch, "E92.19.0.1", {"start": v(465.41, -6.59) * mm, "mid": v(462.59, -6.59) * mm, "end": v(462.59, -9.41) * mm});
            skLineSegment(sketch, "E92.19.0.2", {"start": v(456, 24) * mm, "end": v(480, 24) * mm, "construction": true});
            skLineSegment(sketch, "E92.19.0.3", {"start": v(464, 16) * mm, "end": v(472, 16) * mm, "construction": true});
            skArc(sketch, "E92.19.0.4", {"start": v(463.07, -9.9) * mm, "mid": v(465.9, -9.9) * mm, "end": v(465.9, -7.07) * mm});
            skLineSegment(sketch, "E92.19.0.5", {"start": v(480, 0) * mm, "end": v(456, -24) * mm, "construction": true});
            skCircle(sketch, "E92.19.0.6", {"center": v(472, -16) * mm, "radius": 2 * mm});
            skLineSegment(sketch, "E92.19.0.7", {"start": v(480, -24) * mm, "end": v(456, -24) * mm, "construction": true});
            skCircle(sketch, "E92.19.0.8", {"center": v(464, 16) * mm, "radius": 2 * mm});
            skCircle(sketch, "E92.19.0.9", {"center": v(472, 16) * mm, "radius": 2 * mm});
            skLineSegment(sketch, "E92.19.0.10", {"start": v(480, -24) * mm, "end": v(456, 0) * mm, "construction": true});
            skLineSegment(sketch, "E92.19.0.11", {"start": v(456, 24) * mm, "end": v(480, 0) * mm, "construction": true});
            skLineSegment(sketch, "E92.19.0.12", {"start": v(480, 24) * mm, "end": v(456, 0) * mm, "construction": true});
            skArc(sketch, "E92.19.0.13", {"start": v(472.93, 9.9) * mm, "mid": v(470.1, 9.9) * mm, "end": v(470.1, 7.07) * mm});
            skArc(sketch, "E92.19.0.14", {"start": v(465.9, 7.07) * mm, "mid": v(465.9, 9.9) * mm, "end": v(463.07, 9.9) * mm});
            skArc(sketch, "E92.19.0.15", {"start": v(470.1, -7.07) * mm, "mid": v(470.1, -9.9) * mm, "end": v(472.93, -9.9) * mm});
            skArc(sketch, "E92.19.0.16", {"start": v(470.59, 6.59) * mm, "mid": v(473.41, 6.59) * mm, "end": v(473.41, 9.41) * mm});
            skLineSegment(sketch, "E92.19.0.17", {"start": v(464, -16) * mm, "end": v(472, -16) * mm, "construction": true});
            skLineSegment(sketch, "E92.19.0.18", {"start": v(456, 0) * mm, "end": v(480, 0) * mm, "construction": true});
            skArc(sketch, "E92.19.0.19", {"start": v(473.41, -9.41) * mm, "mid": v(473.41, -6.59) * mm, "end": v(470.59, -6.59) * mm});
            skCircle(sketch, "E92.19.0.20", {"center": v(464, -16) * mm, "radius": 2 * mm});
            skCircle(sketch, "E92.19.0.21", {"center": v(468, 0) * mm, "radius": 2 * mm});
            skPoint(sketch, "E92.19.0.22", {"position": v(464, -8) * mm});
            skLineSegment(sketch, "E92.19.0.23", {"start": v(480, 0) * mm, "end": v(456, 0) * mm, "construction": true});
            skLineSegment(sketch, "E92.19.0.24", {"start": v(470.59, 6.59) * mm, "end": v(473.41, 9.41) * mm, "construction": true});
            skLineSegment(sketch, "E92.19.0.25", {"start": v(470.1, -7.07) * mm, "end": v(472.93, -9.9) * mm, "construction": true});
            skLineSegment(sketch, "E92.19.0.26", {"start": v(462.59, 9.41) * mm, "end": v(465.41, 6.59) * mm, "construction": true});
            skLineSegment(sketch, "E92.19.0.27", {"start": v(463.07, 9.9) * mm, "end": v(465.9, 7.07) * mm, "construction": true});
            skLineSegment(sketch, "E92.19.0.28", {"start": v(472.93, 9.9) * mm, "end": v(470.1, 7.07) * mm, "construction": true});
            skLineSegment(sketch, "E92.19.0.29", {"start": v(470.59, -6.59) * mm, "end": v(473.41, -9.41) * mm, "construction": true});
            skLineSegment(sketch, "E92.19.0.30", {"start": v(463.07, -9.9) * mm, "end": v(465.9, -7.07) * mm, "construction": true});
            skLineSegment(sketch, "E92.19.0.31", {"start": v(465.41, -6.59) * mm, "end": v(462.59, -9.41) * mm, "construction": true});
            skLineSegment(sketch, "E92.19.0.32", {"start": v(470.1, -7.07) * mm, "end": v(470.59, -6.59) * mm});
            skLineSegment(sketch, "E92.19.0.33", {"start": v(462.59, 9.41) * mm, "end": v(463.07, 9.9) * mm});
            skLineSegment(sketch, "E92.19.0.34", {"start": v(462.59, -9.41) * mm, "end": v(463.07, -9.9) * mm});
            skLineSegment(sketch, "E92.19.0.35", {"start": v(472.93, -9.9) * mm, "end": v(473.41, -9.41) * mm});
            skLineSegment(sketch, "E92.19.0.36", {"start": v(465.41, 6.59) * mm, "end": v(465.9, 7.07) * mm});
            skLineSegment(sketch, "E92.19.0.37", {"start": v(472.93, 9.9) * mm, "end": v(473.41, 9.41) * mm});
            skLineSegment(sketch, "E92.19.0.38", {"start": v(470.1, 7.07) * mm, "end": v(470.59, 6.59) * mm});
            skLineSegment(sketch, "E92.19.0.39", {"start": v(465.41, -6.59) * mm, "end": v(465.9, -7.07) * mm});
            skArc(sketch, "E92.20.0.0", {"start": v(486.59, 9.41) * mm, "mid": v(486.59, 6.59) * mm, "end": v(489.41, 6.59) * mm});
            skArc(sketch, "E92.20.0.1", {"start": v(489.41, -6.59) * mm, "mid": v(486.59, -6.59) * mm, "end": v(486.59, -9.41) * mm});
            skLineSegment(sketch, "E92.20.0.2", {"start": v(480, 24) * mm, "end": v(504, 24) * mm, "construction": true});
            skLineSegment(sketch, "E92.20.0.3", {"start": v(488, 16) * mm, "end": v(496, 16) * mm, "construction": true});
            skArc(sketch, "E92.20.0.4", {"start": v(487.07, -9.9) * mm, "mid": v(489.9, -9.9) * mm, "end": v(489.9, -7.07) * mm});
            skLineSegment(sketch, "E92.20.0.5", {"start": v(504, 0) * mm, "end": v(480, -24) * mm, "construction": true});
            skCircle(sketch, "E92.20.0.6", {"center": v(496, -16) * mm, "radius": 2 * mm});
            skLineSegment(sketch, "E92.20.0.7", {"start": v(504, -24) * mm, "end": v(480, -24) * mm, "construction": true});
            skCircle(sketch, "E92.20.0.8", {"center": v(488, 16) * mm, "radius": 2 * mm});
            skCircle(sketch, "E92.20.0.9", {"center": v(496, 16) * mm, "radius": 2 * mm});
            skLineSegment(sketch, "E92.20.0.10", {"start": v(504, -24) * mm, "end": v(480, 0) * mm, "construction": true});
            skLineSegment(sketch, "E92.20.0.11", {"start": v(480, 24) * mm, "end": v(504, 0) * mm, "construction": true});
            skLineSegment(sketch, "E92.20.0.12", {"start": v(504, 24) * mm, "end": v(480, 0) * mm, "construction": true});
            skArc(sketch, "E92.20.0.13", {"start": v(496.93, 9.9) * mm, "mid": v(494.1, 9.9) * mm, "end": v(494.1, 7.07) * mm});
            skArc(sketch, "E92.20.0.14", {"start": v(489.9, 7.07) * mm, "mid": v(489.9, 9.9) * mm, "end": v(487.07, 9.9) * mm});
            skArc(sketch, "E92.20.0.15", {"start": v(494.1, -7.07) * mm, "mid": v(494.1, -9.9) * mm, "end": v(496.93, -9.9) * mm});
            skArc(sketch, "E92.20.0.16", {"start": v(494.59, 6.59) * mm, "mid": v(497.41, 6.59) * mm, "end": v(497.41, 9.41) * mm});
            skLineSegment(sketch, "E92.20.0.17", {"start": v(488, -16) * mm, "end": v(496, -16) * mm, "construction": true});
            skLineSegment(sketch, "E92.20.0.18", {"start": v(480, 0) * mm, "end": v(504, 0) * mm, "construction": true});
            skArc(sketch, "E92.20.0.19", {"start": v(497.41, -9.41) * mm, "mid": v(497.41, -6.59) * mm, "end": v(494.59, -6.59) * mm});
            skCircle(sketch, "E92.20.0.20", {"center": v(488, -16) * mm, "radius": 2 * mm});
            skCircle(sketch, "E92.20.0.21", {"center": v(492, 0) * mm, "radius": 2 * mm});
            skPoint(sketch, "E92.20.0.22", {"position": v(488, -8) * mm});
            skLineSegment(sketch, "E92.20.0.23", {"start": v(504, 0) * mm, "end": v(480, 0) * mm, "construction": true});
            skLineSegment(sketch, "E92.20.0.24", {"start": v(494.59, 6.59) * mm, "end": v(497.41, 9.41) * mm, "construction": true});
            skLineSegment(sketch, "E92.20.0.25", {"start": v(494.1, -7.07) * mm, "end": v(496.93, -9.9) * mm, "construction": true});
            skLineSegment(sketch, "E92.20.0.26", {"start": v(486.59, 9.41) * mm, "end": v(489.41, 6.59) * mm, "construction": true});
            skLineSegment(sketch, "E92.20.0.27", {"start": v(487.07, 9.9) * mm, "end": v(489.9, 7.07) * mm, "construction": true});
            skLineSegment(sketch, "E92.20.0.28", {"start": v(496.93, 9.9) * mm, "end": v(494.1, 7.07) * mm, "construction": true});
            skLineSegment(sketch, "E92.20.0.29", {"start": v(494.59, -6.59) * mm, "end": v(497.41, -9.41) * mm, "construction": true});
            skLineSegment(sketch, "E92.20.0.30", {"start": v(487.07, -9.9) * mm, "end": v(489.9, -7.07) * mm, "construction": true});
            skLineSegment(sketch, "E92.20.0.31", {"start": v(489.41, -6.59) * mm, "end": v(486.59, -9.41) * mm, "construction": true});
            skLineSegment(sketch, "E92.20.0.32", {"start": v(494.1, -7.07) * mm, "end": v(494.59, -6.59) * mm});
            skLineSegment(sketch, "E92.20.0.33", {"start": v(486.59, 9.41) * mm, "end": v(487.07, 9.9) * mm});
            skLineSegment(sketch, "E92.20.0.34", {"start": v(486.59, -9.41) * mm, "end": v(487.07, -9.9) * mm});
            skLineSegment(sketch, "E92.20.0.35", {"start": v(496.93, -9.9) * mm, "end": v(497.41, -9.41) * mm});
            skLineSegment(sketch, "E92.20.0.36", {"start": v(489.41, 6.59) * mm, "end": v(489.9, 7.07) * mm});
            skLineSegment(sketch, "E92.20.0.37", {"start": v(496.93, 9.9) * mm, "end": v(497.41, 9.41) * mm});
            skLineSegment(sketch, "E92.20.0.38", {"start": v(494.1, 7.07) * mm, "end": v(494.59, 6.59) * mm});
            skLineSegment(sketch, "E92.20.0.39", {"start": v(489.41, -6.59) * mm, "end": v(489.9, -7.07) * mm});
            skArc(sketch, "E92.21.0.0", {"start": v(510.59, 9.41) * mm, "mid": v(510.59, 6.59) * mm, "end": v(513.41, 6.59) * mm});
            skArc(sketch, "E92.21.0.1", {"start": v(513.41, -6.59) * mm, "mid": v(510.59, -6.59) * mm, "end": v(510.59, -9.41) * mm});
            skLineSegment(sketch, "E92.21.0.2", {"start": v(504, 24) * mm, "end": v(528, 24) * mm, "construction": true});
            skLineSegment(sketch, "E92.21.0.3", {"start": v(512, 16) * mm, "end": v(520, 16) * mm, "construction": true});
            skArc(sketch, "E92.21.0.4", {"start": v(511.07, -9.9) * mm, "mid": v(513.9, -9.9) * mm, "end": v(513.9, -7.07) * mm});
            skLineSegment(sketch, "E92.21.0.5", {"start": v(528, 0) * mm, "end": v(504, -24) * mm, "construction": true});
            skCircle(sketch, "E92.21.0.6", {"center": v(520, -16) * mm, "radius": 2 * mm});
            skLineSegment(sketch, "E92.21.0.7", {"start": v(528, -24) * mm, "end": v(504, -24) * mm, "construction": true});
            skCircle(sketch, "E92.21.0.8", {"center": v(512, 16) * mm, "radius": 2 * mm});
            skCircle(sketch, "E92.21.0.9", {"center": v(520, 16) * mm, "radius": 2 * mm});
            skLineSegment(sketch, "E92.21.0.10", {"start": v(528, -24) * mm, "end": v(504, 0) * mm, "construction": true});
            skLineSegment(sketch, "E92.21.0.11", {"start": v(504, 24) * mm, "end": v(528, 0) * mm, "construction": true});
            skLineSegment(sketch, "E92.21.0.12", {"start": v(528, 24) * mm, "end": v(504, 0) * mm, "construction": true});
            skArc(sketch, "E92.21.0.13", {"start": v(520.93, 9.9) * mm, "mid": v(518.1, 9.9) * mm, "end": v(518.1, 7.07) * mm});
            skArc(sketch, "E92.21.0.14", {"start": v(513.9, 7.07) * mm, "mid": v(513.9, 9.9) * mm, "end": v(511.07, 9.9) * mm});
            skArc(sketch, "E92.21.0.15", {"start": v(518.1, -7.07) * mm, "mid": v(518.1, -9.9) * mm, "end": v(520.93, -9.9) * mm});
            skArc(sketch, "E92.21.0.16", {"start": v(518.59, 6.59) * mm, "mid": v(521.41, 6.59) * mm, "end": v(521.41, 9.41) * mm});
            skLineSegment(sketch, "E92.21.0.17", {"start": v(512, -16) * mm, "end": v(520, -16) * mm, "construction": true});
            skLineSegment(sketch, "E92.21.0.18", {"start": v(504, 0) * mm, "end": v(528, 0) * mm, "construction": true});
            skArc(sketch, "E92.21.0.19", {"start": v(521.41, -9.41) * mm, "mid": v(521.41, -6.59) * mm, "end": v(518.59, -6.59) * mm});
            skCircle(sketch, "E92.21.0.20", {"center": v(512, -16) * mm, "radius": 2 * mm});
            skCircle(sketch, "E92.21.0.21", {"center": v(516, 0) * mm, "radius": 2 * mm});
            skPoint(sketch, "E92.21.0.22", {"position": v(512, -8) * mm});
            skLineSegment(sketch, "E92.21.0.23", {"start": v(528, 0) * mm, "end": v(504, 0) * mm, "construction": true});
            skLineSegment(sketch, "E92.21.0.24", {"start": v(518.59, 6.59) * mm, "end": v(521.41, 9.41) * mm, "construction": true});
            skLineSegment(sketch, "E92.21.0.25", {"start": v(518.1, -7.07) * mm, "end": v(520.93, -9.9) * mm, "construction": true});
            skLineSegment(sketch, "E92.21.0.26", {"start": v(510.59, 9.41) * mm, "end": v(513.41, 6.59) * mm, "construction": true});
            skLineSegment(sketch, "E92.21.0.27", {"start": v(511.07, 9.9) * mm, "end": v(513.9, 7.07) * mm, "construction": true});
            skLineSegment(sketch, "E92.21.0.28", {"start": v(520.93, 9.9) * mm, "end": v(518.1, 7.07) * mm, "construction": true});
            skLineSegment(sketch, "E92.21.0.29", {"start": v(518.59, -6.59) * mm, "end": v(521.41, -9.41) * mm, "construction": true});
            skLineSegment(sketch, "E92.21.0.30", {"start": v(511.07, -9.9) * mm, "end": v(513.9, -7.07) * mm, "construction": true});
            skLineSegment(sketch, "E92.21.0.31", {"start": v(513.41, -6.59) * mm, "end": v(510.59, -9.41) * mm, "construction": true});
            skLineSegment(sketch, "E92.21.0.32", {"start": v(518.1, -7.07) * mm, "end": v(518.59, -6.59) * mm});
            skLineSegment(sketch, "E92.21.0.33", {"start": v(510.59, 9.41) * mm, "end": v(511.07, 9.9) * mm});
            skLineSegment(sketch, "E92.21.0.34", {"start": v(510.59, -9.41) * mm, "end": v(511.07, -9.9) * mm});
            skLineSegment(sketch, "E92.21.0.35", {"start": v(520.93, -9.9) * mm, "end": v(521.41, -9.41) * mm});
            skLineSegment(sketch, "E92.21.0.36", {"start": v(513.41, 6.59) * mm, "end": v(513.9, 7.07) * mm});
            skLineSegment(sketch, "E92.21.0.37", {"start": v(520.93, 9.9) * mm, "end": v(521.41, 9.41) * mm});
            skLineSegment(sketch, "E92.21.0.38", {"start": v(518.1, 7.07) * mm, "end": v(518.59, 6.59) * mm});
            skLineSegment(sketch, "E92.21.0.39", {"start": v(513.41, -6.59) * mm, "end": v(513.9, -7.07) * mm});
            skArc(sketch, "E92.22.0.0", {"start": v(534.59, 9.41) * mm, "mid": v(534.59, 6.59) * mm, "end": v(537.41, 6.59) * mm});
            skArc(sketch, "E92.22.0.1", {"start": v(537.41, -6.59) * mm, "mid": v(534.59, -6.59) * mm, "end": v(534.59, -9.41) * mm});
            skLineSegment(sketch, "E92.22.0.2", {"start": v(528, 24) * mm, "end": v(552, 24) * mm, "construction": true});
            skLineSegment(sketch, "E92.22.0.3", {"start": v(536, 16) * mm, "end": v(544, 16) * mm, "construction": true});
            skArc(sketch, "E92.22.0.4", {"start": v(535.07, -9.9) * mm, "mid": v(537.9, -9.9) * mm, "end": v(537.9, -7.07) * mm});
            skLineSegment(sketch, "E92.22.0.5", {"start": v(552, 0) * mm, "end": v(528, -24) * mm, "construction": true});
            skCircle(sketch, "E92.22.0.6", {"center": v(544, -16) * mm, "radius": 2 * mm});
            skLineSegment(sketch, "E92.22.0.7", {"start": v(552, -24) * mm, "end": v(528, -24) * mm, "construction": true});
            skCircle(sketch, "E92.22.0.8", {"center": v(536, 16) * mm, "radius": 2 * mm});
            skCircle(sketch, "E92.22.0.9", {"center": v(544, 16) * mm, "radius": 2 * mm});
            skLineSegment(sketch, "E92.22.0.10", {"start": v(552, -24) * mm, "end": v(528, 0) * mm, "construction": true});
            skLineSegment(sketch, "E92.22.0.11", {"start": v(528, 24) * mm, "end": v(552, 0) * mm, "construction": true});
            skLineSegment(sketch, "E92.22.0.12", {"start": v(552, 24) * mm, "end": v(528, 0) * mm, "construction": true});
            skArc(sketch, "E92.22.0.13", {"start": v(544.93, 9.9) * mm, "mid": v(542.1, 9.9) * mm, "end": v(542.1, 7.07) * mm});
            skArc(sketch, "E92.22.0.14", {"start": v(537.9, 7.07) * mm, "mid": v(537.9, 9.9) * mm, "end": v(535.07, 9.9) * mm});
            skArc(sketch, "E92.22.0.15", {"start": v(542.1, -7.07) * mm, "mid": v(542.1, -9.9) * mm, "end": v(544.93, -9.9) * mm});
            skArc(sketch, "E92.22.0.16", {"start": v(542.59, 6.59) * mm, "mid": v(545.41, 6.59) * mm, "end": v(545.41, 9.41) * mm});
            skLineSegment(sketch, "E92.22.0.17", {"start": v(536, -16) * mm, "end": v(544, -16) * mm, "construction": true});
            skLineSegment(sketch, "E92.22.0.18", {"start": v(528, 0) * mm, "end": v(552, 0) * mm, "construction": true});
            skArc(sketch, "E92.22.0.19", {"start": v(545.41, -9.41) * mm, "mid": v(545.41, -6.59) * mm, "end": v(542.59, -6.59) * mm});
            skCircle(sketch, "E92.22.0.20", {"center": v(536, -16) * mm, "radius": 2 * mm});
            skCircle(sketch, "E92.22.0.21", {"center": v(540, 0) * mm, "radius": 2 * mm});
            skPoint(sketch, "E92.22.0.22", {"position": v(536, -8) * mm});
            skLineSegment(sketch, "E92.22.0.23", {"start": v(552, 0) * mm, "end": v(528, 0) * mm, "construction": true});
            skLineSegment(sketch, "E92.22.0.24", {"start": v(542.59, 6.59) * mm, "end": v(545.41, 9.41) * mm, "construction": true});
            skLineSegment(sketch, "E92.22.0.25", {"start": v(542.1, -7.07) * mm, "end": v(544.93, -9.9) * mm, "construction": true});
            skLineSegment(sketch, "E92.22.0.26", {"start": v(534.59, 9.41) * mm, "end": v(537.41, 6.59) * mm, "construction": true});
            skLineSegment(sketch, "E92.22.0.27", {"start": v(535.07, 9.9) * mm, "end": v(537.9, 7.07) * mm, "construction": true});
            skLineSegment(sketch, "E92.22.0.28", {"start": v(544.93, 9.9) * mm, "end": v(542.1, 7.07) * mm, "construction": true});
            skLineSegment(sketch, "E92.22.0.29", {"start": v(542.59, -6.59) * mm, "end": v(545.41, -9.41) * mm, "construction": true});
            skLineSegment(sketch, "E92.22.0.30", {"start": v(535.07, -9.9) * mm, "end": v(537.9, -7.07) * mm, "construction": true});
            skLineSegment(sketch, "E92.22.0.31", {"start": v(537.41, -6.59) * mm, "end": v(534.59, -9.41) * mm, "construction": true});
            skLineSegment(sketch, "E92.22.0.32", {"start": v(542.1, -7.07) * mm, "end": v(542.59, -6.59) * mm});
            skLineSegment(sketch, "E92.22.0.33", {"start": v(534.59, 9.41) * mm, "end": v(535.07, 9.9) * mm});
            skLineSegment(sketch, "E92.22.0.34", {"start": v(534.59, -9.41) * mm, "end": v(535.07, -9.9) * mm});
            skLineSegment(sketch, "E92.22.0.35", {"start": v(544.93, -9.9) * mm, "end": v(545.41, -9.41) * mm});
            skLineSegment(sketch, "E92.22.0.36", {"start": v(537.41, 6.59) * mm, "end": v(537.9, 7.07) * mm});
            skLineSegment(sketch, "E92.22.0.37", {"start": v(544.93, 9.9) * mm, "end": v(545.41, 9.41) * mm});
            skLineSegment(sketch, "E92.22.0.38", {"start": v(542.1, 7.07) * mm, "end": v(542.59, 6.59) * mm});
            skLineSegment(sketch, "E92.22.0.39", {"start": v(537.41, -6.59) * mm, "end": v(537.9, -7.07) * mm});
            skArc(sketch, "E92.23.0.0", {"start": v(558.59, 9.41) * mm, "mid": v(558.59, 6.59) * mm, "end": v(561.41, 6.59) * mm});
            skArc(sketch, "E92.23.0.1", {"start": v(561.41, -6.59) * mm, "mid": v(558.59, -6.59) * mm, "end": v(558.59, -9.41) * mm});
            skLineSegment(sketch, "E92.23.0.2", {"start": v(552, 24) * mm, "end": v(576, 24) * mm, "construction": true});
            skLineSegment(sketch, "E92.23.0.3", {"start": v(560, 16) * mm, "end": v(568, 16) * mm, "construction": true});
            skArc(sketch, "E92.23.0.4", {"start": v(559.07, -9.9) * mm, "mid": v(561.9, -9.9) * mm, "end": v(561.9, -7.07) * mm});
            skLineSegment(sketch, "E92.23.0.5", {"start": v(576, 0) * mm, "end": v(552, -24) * mm, "construction": true});
            skCircle(sketch, "E92.23.0.6", {"center": v(568, -16) * mm, "radius": 2 * mm});
            skLineSegment(sketch, "E92.23.0.7", {"start": v(576, -24) * mm, "end": v(552, -24) * mm, "construction": true});
            skCircle(sketch, "E92.23.0.8", {"center": v(560, 16) * mm, "radius": 2 * mm});
            skCircle(sketch, "E92.23.0.9", {"center": v(568, 16) * mm, "radius": 2 * mm});
            skLineSegment(sketch, "E92.23.0.10", {"start": v(576, -24) * mm, "end": v(552, 0) * mm, "construction": true});
            skLineSegment(sketch, "E92.23.0.11", {"start": v(552, 24) * mm, "end": v(576, 0) * mm, "construction": true});
            skLineSegment(sketch, "E92.23.0.12", {"start": v(576, 24) * mm, "end": v(552, 0) * mm, "construction": true});
            skArc(sketch, "E92.23.0.13", {"start": v(568.93, 9.9) * mm, "mid": v(566.1, 9.9) * mm, "end": v(566.1, 7.07) * mm});
            skArc(sketch, "E92.23.0.14", {"start": v(561.9, 7.07) * mm, "mid": v(561.9, 9.9) * mm, "end": v(559.07, 9.9) * mm});
            skArc(sketch, "E92.23.0.15", {"start": v(566.1, -7.07) * mm, "mid": v(566.1, -9.9) * mm, "end": v(568.93, -9.9) * mm});
            skArc(sketch, "E92.23.0.16", {"start": v(566.59, 6.59) * mm, "mid": v(569.41, 6.59) * mm, "end": v(569.41, 9.41) * mm});
            skLineSegment(sketch, "E92.23.0.17", {"start": v(560, -16) * mm, "end": v(568, -16) * mm, "construction": true});
            skLineSegment(sketch, "E92.23.0.18", {"start": v(552, 0) * mm, "end": v(576, 0) * mm, "construction": true});
            skArc(sketch, "E92.23.0.19", {"start": v(569.41, -9.41) * mm, "mid": v(569.41, -6.59) * mm, "end": v(566.59, -6.59) * mm});
            skCircle(sketch, "E92.23.0.20", {"center": v(560, -16) * mm, "radius": 2 * mm});
            skCircle(sketch, "E92.23.0.21", {"center": v(564, 0) * mm, "radius": 2 * mm});
            skPoint(sketch, "E92.23.0.22", {"position": v(560, -8) * mm});
            skLineSegment(sketch, "E92.23.0.23", {"start": v(576, 0) * mm, "end": v(552, 0) * mm, "construction": true});
            skLineSegment(sketch, "E92.23.0.24", {"start": v(566.59, 6.59) * mm, "end": v(569.41, 9.41) * mm, "construction": true});
            skLineSegment(sketch, "E92.23.0.25", {"start": v(566.1, -7.07) * mm, "end": v(568.93, -9.9) * mm, "construction": true});
            skLineSegment(sketch, "E92.23.0.26", {"start": v(558.59, 9.41) * mm, "end": v(561.41, 6.59) * mm, "construction": true});
            skLineSegment(sketch, "E92.23.0.27", {"start": v(559.07, 9.9) * mm, "end": v(561.9, 7.07) * mm, "construction": true});
            skLineSegment(sketch, "E92.23.0.28", {"start": v(568.93, 9.9) * mm, "end": v(566.1, 7.07) * mm, "construction": true});
            skLineSegment(sketch, "E92.23.0.29", {"start": v(566.59, -6.59) * mm, "end": v(569.41, -9.41) * mm, "construction": true});
            skLineSegment(sketch, "E92.23.0.30", {"start": v(559.07, -9.9) * mm, "end": v(561.9, -7.07) * mm, "construction": true});
            skLineSegment(sketch, "E92.23.0.31", {"start": v(561.41, -6.59) * mm, "end": v(558.59, -9.41) * mm, "construction": true});
            skLineSegment(sketch, "E92.23.0.32", {"start": v(566.1, -7.07) * mm, "end": v(566.59, -6.59) * mm});
            skLineSegment(sketch, "E92.23.0.33", {"start": v(558.59, 9.41) * mm, "end": v(559.07, 9.9) * mm});
            skLineSegment(sketch, "E92.23.0.34", {"start": v(558.59, -9.41) * mm, "end": v(559.07, -9.9) * mm});
            skLineSegment(sketch, "E92.23.0.35", {"start": v(568.93, -9.9) * mm, "end": v(569.41, -9.41) * mm});
            skLineSegment(sketch, "E92.23.0.36", {"start": v(561.41, 6.59) * mm, "end": v(561.9, 7.07) * mm});
            skLineSegment(sketch, "E92.23.0.37", {"start": v(568.93, 9.9) * mm, "end": v(569.41, 9.41) * mm});
            skLineSegment(sketch, "E92.23.0.38", {"start": v(566.1, 7.07) * mm, "end": v(566.59, 6.59) * mm});
            skLineSegment(sketch, "E92.23.0.39", {"start": v(561.41, -6.59) * mm, "end": v(561.9, -7.07) * mm});
            skArc(sketch, "E92.24.0.0", {"start": v(582.59, 9.41) * mm, "mid": v(582.59, 6.59) * mm, "end": v(585.41, 6.59) * mm});
            skArc(sketch, "E92.24.0.1", {"start": v(585.41, -6.59) * mm, "mid": v(582.59, -6.59) * mm, "end": v(582.59, -9.41) * mm});
            skLineSegment(sketch, "E92.24.0.2", {"start": v(576, 24) * mm, "end": v(600, 24) * mm, "construction": true});
            skLineSegment(sketch, "E92.24.0.3", {"start": v(584, 16) * mm, "end": v(592, 16) * mm, "construction": true});
            skArc(sketch, "E92.24.0.4", {"start": v(583.07, -9.9) * mm, "mid": v(585.9, -9.9) * mm, "end": v(585.9, -7.07) * mm});
            skLineSegment(sketch, "E92.24.0.5", {"start": v(600, 0) * mm, "end": v(576, -24) * mm, "construction": true});
            skCircle(sketch, "E92.24.0.6", {"center": v(592, -16) * mm, "radius": 2 * mm});
            skLineSegment(sketch, "E92.24.0.7", {"start": v(600, -24) * mm, "end": v(576, -24) * mm, "construction": true});
            skCircle(sketch, "E92.24.0.8", {"center": v(584, 16) * mm, "radius": 2 * mm});
            skCircle(sketch, "E92.24.0.9", {"center": v(592, 16) * mm, "radius": 2 * mm});
            skLineSegment(sketch, "E92.24.0.10", {"start": v(600, -24) * mm, "end": v(576, 0) * mm, "construction": true});
            skLineSegment(sketch, "E92.24.0.11", {"start": v(576, 24) * mm, "end": v(600, 0) * mm, "construction": true});
            skLineSegment(sketch, "E92.24.0.12", {"start": v(600, 24) * mm, "end": v(576, 0) * mm, "construction": true});
            skArc(sketch, "E92.24.0.13", {"start": v(592.93, 9.9) * mm, "mid": v(590.1, 9.9) * mm, "end": v(590.1, 7.07) * mm});
            skArc(sketch, "E92.24.0.14", {"start": v(585.9, 7.07) * mm, "mid": v(585.9, 9.9) * mm, "end": v(583.07, 9.9) * mm});
            skArc(sketch, "E92.24.0.15", {"start": v(590.1, -7.07) * mm, "mid": v(590.1, -9.9) * mm, "end": v(592.93, -9.9) * mm});
            skArc(sketch, "E92.24.0.16", {"start": v(590.59, 6.59) * mm, "mid": v(593.41, 6.59) * mm, "end": v(593.41, 9.41) * mm});
            skLineSegment(sketch, "E92.24.0.17", {"start": v(584, -16) * mm, "end": v(592, -16) * mm, "construction": true});
            skLineSegment(sketch, "E92.24.0.18", {"start": v(576, 0) * mm, "end": v(600, 0) * mm, "construction": true});
            skArc(sketch, "E92.24.0.19", {"start": v(593.41, -9.41) * mm, "mid": v(593.41, -6.59) * mm, "end": v(590.59, -6.59) * mm});
            skCircle(sketch, "E92.24.0.20", {"center": v(584, -16) * mm, "radius": 2 * mm});
            skCircle(sketch, "E92.24.0.21", {"center": v(588, 0) * mm, "radius": 2 * mm});
            skPoint(sketch, "E92.24.0.22", {"position": v(584, -8) * mm});
            skLineSegment(sketch, "E92.24.0.23", {"start": v(600, 0) * mm, "end": v(576, 0) * mm, "construction": true});
            skLineSegment(sketch, "E92.24.0.24", {"start": v(590.59, 6.59) * mm, "end": v(593.41, 9.41) * mm, "construction": true});
            skLineSegment(sketch, "E92.24.0.25", {"start": v(590.1, -7.07) * mm, "end": v(592.93, -9.9) * mm, "construction": true});
            skLineSegment(sketch, "E92.24.0.26", {"start": v(582.59, 9.41) * mm, "end": v(585.41, 6.59) * mm, "construction": true});
            skLineSegment(sketch, "E92.24.0.27", {"start": v(583.07, 9.9) * mm, "end": v(585.9, 7.07) * mm, "construction": true});
            skLineSegment(sketch, "E92.24.0.28", {"start": v(592.93, 9.9) * mm, "end": v(590.1, 7.07) * mm, "construction": true});
            skLineSegment(sketch, "E92.24.0.29", {"start": v(590.59, -6.59) * mm, "end": v(593.41, -9.41) * mm, "construction": true});
            skLineSegment(sketch, "E92.24.0.30", {"start": v(583.07, -9.9) * mm, "end": v(585.9, -7.07) * mm, "construction": true});
            skLineSegment(sketch, "E92.24.0.31", {"start": v(585.41, -6.59) * mm, "end": v(582.59, -9.41) * mm, "construction": true});
            skLineSegment(sketch, "E92.24.0.32", {"start": v(590.1, -7.07) * mm, "end": v(590.59, -6.59) * mm});
            skLineSegment(sketch, "E92.24.0.33", {"start": v(582.59, 9.41) * mm, "end": v(583.07, 9.9) * mm});
            skLineSegment(sketch, "E92.24.0.34", {"start": v(582.59, -9.41) * mm, "end": v(583.07, -9.9) * mm});
            skLineSegment(sketch, "E92.24.0.35", {"start": v(592.93, -9.9) * mm, "end": v(593.41, -9.41) * mm});
            skLineSegment(sketch, "E92.24.0.36", {"start": v(585.41, 6.59) * mm, "end": v(585.9, 7.07) * mm});
            skLineSegment(sketch, "E92.24.0.37", {"start": v(592.93, 9.9) * mm, "end": v(593.41, 9.41) * mm});
            skLineSegment(sketch, "E92.24.0.38", {"start": v(590.1, 7.07) * mm, "end": v(590.59, 6.59) * mm});
            skLineSegment(sketch, "E92.24.0.39", {"start": v(585.41, -6.59) * mm, "end": v(585.9, -7.07) * mm});
            skArc(sketch, "E92.25.0.0", {"start": v(606.59, 9.41) * mm, "mid": v(606.59, 6.59) * mm, "end": v(609.41, 6.59) * mm});
            skArc(sketch, "E92.25.0.1", {"start": v(609.41, -6.59) * mm, "mid": v(606.59, -6.59) * mm, "end": v(606.59, -9.41) * mm});
            skLineSegment(sketch, "E92.25.0.2", {"start": v(600, 24) * mm, "end": v(624, 24) * mm, "construction": true});
            skLineSegment(sketch, "E92.25.0.3", {"start": v(608, 16) * mm, "end": v(616, 16) * mm, "construction": true});
            skArc(sketch, "E92.25.0.4", {"start": v(607.07, -9.9) * mm, "mid": v(609.9, -9.9) * mm, "end": v(609.9, -7.07) * mm});
            skLineSegment(sketch, "E92.25.0.5", {"start": v(624, 0) * mm, "end": v(600, -24) * mm, "construction": true});
            skCircle(sketch, "E92.25.0.6", {"center": v(616, -16) * mm, "radius": 2 * mm});
            skLineSegment(sketch, "E92.25.0.7", {"start": v(624, -24) * mm, "end": v(600, -24) * mm, "construction": true});
            skCircle(sketch, "E92.25.0.8", {"center": v(608, 16) * mm, "radius": 2 * mm});
            skCircle(sketch, "E92.25.0.9", {"center": v(616, 16) * mm, "radius": 2 * mm});
            skLineSegment(sketch, "E92.25.0.10", {"start": v(624, -24) * mm, "end": v(600, 0) * mm, "construction": true});
            skLineSegment(sketch, "E92.25.0.11", {"start": v(600, 24) * mm, "end": v(624, 0) * mm, "construction": true});
            skLineSegment(sketch, "E92.25.0.12", {"start": v(624, 24) * mm, "end": v(600, 0) * mm, "construction": true});
            skArc(sketch, "E92.25.0.13", {"start": v(616.93, 9.9) * mm, "mid": v(614.1, 9.9) * mm, "end": v(614.1, 7.07) * mm});
            skArc(sketch, "E92.25.0.14", {"start": v(609.9, 7.07) * mm, "mid": v(609.9, 9.9) * mm, "end": v(607.07, 9.9) * mm});
            skArc(sketch, "E92.25.0.15", {"start": v(614.1, -7.07) * mm, "mid": v(614.1, -9.9) * mm, "end": v(616.93, -9.9) * mm});
            skArc(sketch, "E92.25.0.16", {"start": v(614.59, 6.59) * mm, "mid": v(617.41, 6.59) * mm, "end": v(617.41, 9.41) * mm});
            skLineSegment(sketch, "E92.25.0.17", {"start": v(608, -16) * mm, "end": v(616, -16) * mm, "construction": true});
            skLineSegment(sketch, "E92.25.0.18", {"start": v(600, 0) * mm, "end": v(624, 0) * mm, "construction": true});
            skArc(sketch, "E92.25.0.19", {"start": v(617.41, -9.41) * mm, "mid": v(617.41, -6.59) * mm, "end": v(614.59, -6.59) * mm});
            skCircle(sketch, "E92.25.0.20", {"center": v(608, -16) * mm, "radius": 2 * mm});
            skCircle(sketch, "E92.25.0.21", {"center": v(612, 0) * mm, "radius": 2 * mm});
            skPoint(sketch, "E92.25.0.22", {"position": v(608, -8) * mm});
            skLineSegment(sketch, "E92.25.0.23", {"start": v(624, 0) * mm, "end": v(600, 0) * mm, "construction": true});
            skLineSegment(sketch, "E92.25.0.24", {"start": v(614.59, 6.59) * mm, "end": v(617.41, 9.41) * mm, "construction": true});
            skLineSegment(sketch, "E92.25.0.25", {"start": v(614.1, -7.07) * mm, "end": v(616.93, -9.9) * mm, "construction": true});
            skLineSegment(sketch, "E92.25.0.26", {"start": v(606.59, 9.41) * mm, "end": v(609.41, 6.59) * mm, "construction": true});
            skLineSegment(sketch, "E92.25.0.27", {"start": v(607.07, 9.9) * mm, "end": v(609.9, 7.07) * mm, "construction": true});
            skLineSegment(sketch, "E92.25.0.28", {"start": v(616.93, 9.9) * mm, "end": v(614.1, 7.07) * mm, "construction": true});
            skLineSegment(sketch, "E92.25.0.29", {"start": v(614.59, -6.59) * mm, "end": v(617.41, -9.41) * mm, "construction": true});
            skLineSegment(sketch, "E92.25.0.30", {"start": v(607.07, -9.9) * mm, "end": v(609.9, -7.07) * mm, "construction": true});
            skLineSegment(sketch, "E92.25.0.31", {"start": v(609.41, -6.59) * mm, "end": v(606.59, -9.41) * mm, "construction": true});
            skLineSegment(sketch, "E92.25.0.32", {"start": v(614.1, -7.07) * mm, "end": v(614.59, -6.59) * mm});
            skLineSegment(sketch, "E92.25.0.33", {"start": v(606.59, 9.41) * mm, "end": v(607.07, 9.9) * mm});
            skLineSegment(sketch, "E92.25.0.34", {"start": v(606.59, -9.41) * mm, "end": v(607.07, -9.9) * mm});
            skLineSegment(sketch, "E92.25.0.35", {"start": v(616.93, -9.9) * mm, "end": v(617.41, -9.41) * mm});
            skLineSegment(sketch, "E92.25.0.36", {"start": v(609.41, 6.59) * mm, "end": v(609.9, 7.07) * mm});
            skLineSegment(sketch, "E92.25.0.37", {"start": v(616.93, 9.9) * mm, "end": v(617.41, 9.41) * mm});
            skLineSegment(sketch, "E92.25.0.38", {"start": v(614.1, 7.07) * mm, "end": v(614.59, 6.59) * mm});
            skLineSegment(sketch, "E92.25.0.39", {"start": v(609.41, -6.59) * mm, "end": v(609.9, -7.07) * mm});
            skArc(sketch, "E92.26.0.0", {"start": v(630.59, 9.41) * mm, "mid": v(630.59, 6.59) * mm, "end": v(633.41, 6.59) * mm});
            skArc(sketch, "E92.26.0.1", {"start": v(633.41, -6.59) * mm, "mid": v(630.59, -6.59) * mm, "end": v(630.59, -9.41) * mm});
            skLineSegment(sketch, "E92.26.0.2", {"start": v(624, 24) * mm, "end": v(648, 24) * mm, "construction": true});
            skLineSegment(sketch, "E92.26.0.3", {"start": v(632, 16) * mm, "end": v(640, 16) * mm, "construction": true});
            skArc(sketch, "E92.26.0.4", {"start": v(631.07, -9.9) * mm, "mid": v(633.9, -9.9) * mm, "end": v(633.9, -7.07) * mm});
            skLineSegment(sketch, "E92.26.0.5", {"start": v(648, 0) * mm, "end": v(624, -24) * mm, "construction": true});
            skCircle(sketch, "E92.26.0.6", {"center": v(640, -16) * mm, "radius": 2 * mm});
            skLineSegment(sketch, "E92.26.0.7", {"start": v(648, -24) * mm, "end": v(624, -24) * mm, "construction": true});
            skCircle(sketch, "E92.26.0.8", {"center": v(632, 16) * mm, "radius": 2 * mm});
            skCircle(sketch, "E92.26.0.9", {"center": v(640, 16) * mm, "radius": 2 * mm});
            skLineSegment(sketch, "E92.26.0.10", {"start": v(648, -24) * mm, "end": v(624, 0) * mm, "construction": true});
            skLineSegment(sketch, "E92.26.0.11", {"start": v(624, 24) * mm, "end": v(648, 0) * mm, "construction": true});
            skLineSegment(sketch, "E92.26.0.12", {"start": v(648, 24) * mm, "end": v(624, 0) * mm, "construction": true});
            skArc(sketch, "E92.26.0.13", {"start": v(640.93, 9.9) * mm, "mid": v(638.1, 9.9) * mm, "end": v(638.1, 7.07) * mm});
            skArc(sketch, "E92.26.0.14", {"start": v(633.9, 7.07) * mm, "mid": v(633.9, 9.9) * mm, "end": v(631.07, 9.9) * mm});
            skArc(sketch, "E92.26.0.15", {"start": v(638.1, -7.07) * mm, "mid": v(638.1, -9.9) * mm, "end": v(640.93, -9.9) * mm});
            skArc(sketch, "E92.26.0.16", {"start": v(638.59, 6.59) * mm, "mid": v(641.41, 6.59) * mm, "end": v(641.41, 9.41) * mm});
            skLineSegment(sketch, "E92.26.0.17", {"start": v(632, -16) * mm, "end": v(640, -16) * mm, "construction": true});
            skLineSegment(sketch, "E92.26.0.18", {"start": v(624, 0) * mm, "end": v(648, 0) * mm, "construction": true});
            skArc(sketch, "E92.26.0.19", {"start": v(641.41, -9.41) * mm, "mid": v(641.41, -6.59) * mm, "end": v(638.59, -6.59) * mm});
            skCircle(sketch, "E92.26.0.20", {"center": v(632, -16) * mm, "radius": 2 * mm});
            skCircle(sketch, "E92.26.0.21", {"center": v(636, 0) * mm, "radius": 2 * mm});
            skPoint(sketch, "E92.26.0.22", {"position": v(632, -8) * mm});
            skLineSegment(sketch, "E92.26.0.23", {"start": v(648, 0) * mm, "end": v(624, 0) * mm, "construction": true});
            skLineSegment(sketch, "E92.26.0.24", {"start": v(638.59, 6.59) * mm, "end": v(641.41, 9.41) * mm, "construction": true});
            skLineSegment(sketch, "E92.26.0.25", {"start": v(638.1, -7.07) * mm, "end": v(640.93, -9.9) * mm, "construction": true});
            skLineSegment(sketch, "E92.26.0.26", {"start": v(630.59, 9.41) * mm, "end": v(633.41, 6.59) * mm, "construction": true});
            skLineSegment(sketch, "E92.26.0.27", {"start": v(631.07, 9.9) * mm, "end": v(633.9, 7.07) * mm, "construction": true});
            skLineSegment(sketch, "E92.26.0.28", {"start": v(640.93, 9.9) * mm, "end": v(638.1, 7.07) * mm, "construction": true});
            skLineSegment(sketch, "E92.26.0.29", {"start": v(638.59, -6.59) * mm, "end": v(641.41, -9.41) * mm, "construction": true});
            skLineSegment(sketch, "E92.26.0.30", {"start": v(631.07, -9.9) * mm, "end": v(633.9, -7.07) * mm, "construction": true});
            skLineSegment(sketch, "E92.26.0.31", {"start": v(633.41, -6.59) * mm, "end": v(630.59, -9.41) * mm, "construction": true});
            skLineSegment(sketch, "E92.26.0.32", {"start": v(638.1, -7.07) * mm, "end": v(638.59, -6.59) * mm});
            skLineSegment(sketch, "E92.26.0.33", {"start": v(630.59, 9.41) * mm, "end": v(631.07, 9.9) * mm});
            skLineSegment(sketch, "E92.26.0.34", {"start": v(630.59, -9.41) * mm, "end": v(631.07, -9.9) * mm});
            skLineSegment(sketch, "E92.26.0.35", {"start": v(640.93, -9.9) * mm, "end": v(641.41, -9.41) * mm});
            skLineSegment(sketch, "E92.26.0.36", {"start": v(633.41, 6.59) * mm, "end": v(633.9, 7.07) * mm});
            skLineSegment(sketch, "E92.26.0.37", {"start": v(640.93, 9.9) * mm, "end": v(641.41, 9.41) * mm});
            skLineSegment(sketch, "E92.26.0.38", {"start": v(638.1, 7.07) * mm, "end": v(638.59, 6.59) * mm});
            skLineSegment(sketch, "E92.26.0.39", {"start": v(633.41, -6.59) * mm, "end": v(633.9, -7.07) * mm});
            skArc(sketch, "E92.27.0.0", {"start": v(654.59, 9.41) * mm, "mid": v(654.59, 6.59) * mm, "end": v(657.41, 6.59) * mm});
            skArc(sketch, "E92.27.0.1", {"start": v(657.41, -6.59) * mm, "mid": v(654.59, -6.59) * mm, "end": v(654.59, -9.41) * mm});
            skLineSegment(sketch, "E92.27.0.2", {"start": v(648, 24) * mm, "end": v(672, 24) * mm, "construction": true});
            skLineSegment(sketch, "E92.27.0.3", {"start": v(656, 16) * mm, "end": v(664, 16) * mm, "construction": true});
            skArc(sketch, "E92.27.0.4", {"start": v(655.07, -9.9) * mm, "mid": v(657.9, -9.9) * mm, "end": v(657.9, -7.07) * mm});
            skLineSegment(sketch, "E92.27.0.5", {"start": v(672, 0) * mm, "end": v(648, -24) * mm, "construction": true});
            skCircle(sketch, "E92.27.0.6", {"center": v(664, -16) * mm, "radius": 2 * mm});
            skLineSegment(sketch, "E92.27.0.7", {"start": v(672, -24) * mm, "end": v(648, -24) * mm, "construction": true});
            skCircle(sketch, "E92.27.0.8", {"center": v(656, 16) * mm, "radius": 2 * mm});
            skCircle(sketch, "E92.27.0.9", {"center": v(664, 16) * mm, "radius": 2 * mm});
            skLineSegment(sketch, "E92.27.0.10", {"start": v(672, -24) * mm, "end": v(648, 0) * mm, "construction": true});
            skLineSegment(sketch, "E92.27.0.11", {"start": v(648, 24) * mm, "end": v(672, 0) * mm, "construction": true});
            skLineSegment(sketch, "E92.27.0.12", {"start": v(672, 24) * mm, "end": v(648, 0) * mm, "construction": true});
            skArc(sketch, "E92.27.0.13", {"start": v(664.93, 9.9) * mm, "mid": v(662.1, 9.9) * mm, "end": v(662.1, 7.07) * mm});
            skArc(sketch, "E92.27.0.14", {"start": v(657.9, 7.07) * mm, "mid": v(657.9, 9.9) * mm, "end": v(655.07, 9.9) * mm});
            skArc(sketch, "E92.27.0.15", {"start": v(662.1, -7.07) * mm, "mid": v(662.1, -9.9) * mm, "end": v(664.93, -9.9) * mm});
            skArc(sketch, "E92.27.0.16", {"start": v(662.59, 6.59) * mm, "mid": v(665.41, 6.59) * mm, "end": v(665.41, 9.41) * mm});
            skLineSegment(sketch, "E92.27.0.17", {"start": v(656, -16) * mm, "end": v(664, -16) * mm, "construction": true});
            skLineSegment(sketch, "E92.27.0.18", {"start": v(648, 0) * mm, "end": v(672, 0) * mm, "construction": true});
            skArc(sketch, "E92.27.0.19", {"start": v(665.41, -9.41) * mm, "mid": v(665.41, -6.59) * mm, "end": v(662.59, -6.59) * mm});
            skCircle(sketch, "E92.27.0.20", {"center": v(656, -16) * mm, "radius": 2 * mm});
            skCircle(sketch, "E92.27.0.21", {"center": v(660, 0) * mm, "radius": 2 * mm});
            skPoint(sketch, "E92.27.0.22", {"position": v(656, -8) * mm});
            skLineSegment(sketch, "E92.27.0.23", {"start": v(672, 0) * mm, "end": v(648, 0) * mm, "construction": true});
            skLineSegment(sketch, "E92.27.0.24", {"start": v(662.59, 6.59) * mm, "end": v(665.41, 9.41) * mm, "construction": true});
            skLineSegment(sketch, "E92.27.0.25", {"start": v(662.1, -7.07) * mm, "end": v(664.93, -9.9) * mm, "construction": true});
            skLineSegment(sketch, "E92.27.0.26", {"start": v(654.59, 9.41) * mm, "end": v(657.41, 6.59) * mm, "construction": true});
            skLineSegment(sketch, "E92.27.0.27", {"start": v(655.07, 9.9) * mm, "end": v(657.9, 7.07) * mm, "construction": true});
            skLineSegment(sketch, "E92.27.0.28", {"start": v(664.93, 9.9) * mm, "end": v(662.1, 7.07) * mm, "construction": true});
            skLineSegment(sketch, "E92.27.0.29", {"start": v(662.59, -6.59) * mm, "end": v(665.41, -9.41) * mm, "construction": true});
            skLineSegment(sketch, "E92.27.0.30", {"start": v(655.07, -9.9) * mm, "end": v(657.9, -7.07) * mm, "construction": true});
            skLineSegment(sketch, "E92.27.0.31", {"start": v(657.41, -6.59) * mm, "end": v(654.59, -9.41) * mm, "construction": true});
            skLineSegment(sketch, "E92.27.0.32", {"start": v(662.1, -7.07) * mm, "end": v(662.59, -6.59) * mm});
            skLineSegment(sketch, "E92.27.0.33", {"start": v(654.59, 9.41) * mm, "end": v(655.07, 9.9) * mm});
            skLineSegment(sketch, "E92.27.0.34", {"start": v(654.59, -9.41) * mm, "end": v(655.07, -9.9) * mm});
            skLineSegment(sketch, "E92.27.0.35", {"start": v(664.93, -9.9) * mm, "end": v(665.41, -9.41) * mm});
            skLineSegment(sketch, "E92.27.0.36", {"start": v(657.41, 6.59) * mm, "end": v(657.9, 7.07) * mm});
            skLineSegment(sketch, "E92.27.0.37", {"start": v(664.93, 9.9) * mm, "end": v(665.41, 9.41) * mm});
            skLineSegment(sketch, "E92.27.0.38", {"start": v(662.1, 7.07) * mm, "end": v(662.59, 6.59) * mm});
            skLineSegment(sketch, "E92.27.0.39", {"start": v(657.41, -6.59) * mm, "end": v(657.9, -7.07) * mm});
            skArc(sketch, "E92.28.0.0", {"start": v(678.59, 9.41) * mm, "mid": v(678.59, 6.59) * mm, "end": v(681.41, 6.59) * mm});
            skArc(sketch, "E92.28.0.1", {"start": v(681.41, -6.59) * mm, "mid": v(678.59, -6.59) * mm, "end": v(678.59, -9.41) * mm});
            skLineSegment(sketch, "E92.28.0.2", {"start": v(672, 24) * mm, "end": v(696, 24) * mm, "construction": true});
            skLineSegment(sketch, "E92.28.0.3", {"start": v(680, 16) * mm, "end": v(688, 16) * mm, "construction": true});
            skArc(sketch, "E92.28.0.4", {"start": v(679.07, -9.9) * mm, "mid": v(681.9, -9.9) * mm, "end": v(681.9, -7.07) * mm});
            skLineSegment(sketch, "E92.28.0.5", {"start": v(696, 0) * mm, "end": v(672, -24) * mm, "construction": true});
            skCircle(sketch, "E92.28.0.6", {"center": v(688, -16) * mm, "radius": 2 * mm});
            skLineSegment(sketch, "E92.28.0.7", {"start": v(696, -24) * mm, "end": v(672, -24) * mm, "construction": true});
            skCircle(sketch, "E92.28.0.8", {"center": v(680, 16) * mm, "radius": 2 * mm});
            skCircle(sketch, "E92.28.0.9", {"center": v(688, 16) * mm, "radius": 2 * mm});
            skLineSegment(sketch, "E92.28.0.10", {"start": v(696, -24) * mm, "end": v(672, 0) * mm, "construction": true});
            skLineSegment(sketch, "E92.28.0.11", {"start": v(672, 24) * mm, "end": v(696, 0) * mm, "construction": true});
            skLineSegment(sketch, "E92.28.0.12", {"start": v(696, 24) * mm, "end": v(672, 0) * mm, "construction": true});
            skArc(sketch, "E92.28.0.13", {"start": v(688.93, 9.9) * mm, "mid": v(686.1, 9.9) * mm, "end": v(686.1, 7.07) * mm});
            skArc(sketch, "E92.28.0.14", {"start": v(681.9, 7.07) * mm, "mid": v(681.9, 9.9) * mm, "end": v(679.07, 9.9) * mm});
            skArc(sketch, "E92.28.0.15", {"start": v(686.1, -7.07) * mm, "mid": v(686.1, -9.9) * mm, "end": v(688.93, -9.9) * mm});
            skArc(sketch, "E92.28.0.16", {"start": v(686.59, 6.59) * mm, "mid": v(689.41, 6.59) * mm, "end": v(689.41, 9.41) * mm});
            skLineSegment(sketch, "E92.28.0.17", {"start": v(680, -16) * mm, "end": v(688, -16) * mm, "construction": true});
            skLineSegment(sketch, "E92.28.0.18", {"start": v(672, 0) * mm, "end": v(696, 0) * mm, "construction": true});
            skArc(sketch, "E92.28.0.19", {"start": v(689.41, -9.41) * mm, "mid": v(689.41, -6.59) * mm, "end": v(686.59, -6.59) * mm});
            skCircle(sketch, "E92.28.0.20", {"center": v(680, -16) * mm, "radius": 2 * mm});
            skCircle(sketch, "E92.28.0.21", {"center": v(684, 0) * mm, "radius": 2 * mm});
            skPoint(sketch, "E92.28.0.22", {"position": v(680, -8) * mm});
            skLineSegment(sketch, "E92.28.0.23", {"start": v(696, 0) * mm, "end": v(672, 0) * mm, "construction": true});
            skLineSegment(sketch, "E92.28.0.24", {"start": v(686.59, 6.59) * mm, "end": v(689.41, 9.41) * mm, "construction": true});
            skLineSegment(sketch, "E92.28.0.25", {"start": v(686.1, -7.07) * mm, "end": v(688.93, -9.9) * mm, "construction": true});
            skLineSegment(sketch, "E92.28.0.26", {"start": v(678.59, 9.41) * mm, "end": v(681.41, 6.59) * mm, "construction": true});
            skLineSegment(sketch, "E92.28.0.27", {"start": v(679.07, 9.9) * mm, "end": v(681.9, 7.07) * mm, "construction": true});
            skLineSegment(sketch, "E92.28.0.28", {"start": v(688.93, 9.9) * mm, "end": v(686.1, 7.07) * mm, "construction": true});
            skLineSegment(sketch, "E92.28.0.29", {"start": v(686.59, -6.59) * mm, "end": v(689.41, -9.41) * mm, "construction": true});
            skLineSegment(sketch, "E92.28.0.30", {"start": v(679.07, -9.9) * mm, "end": v(681.9, -7.07) * mm, "construction": true});
            skLineSegment(sketch, "E92.28.0.31", {"start": v(681.41, -6.59) * mm, "end": v(678.59, -9.41) * mm, "construction": true});
            skLineSegment(sketch, "E92.28.0.32", {"start": v(686.1, -7.07) * mm, "end": v(686.59, -6.59) * mm});
            skLineSegment(sketch, "E92.28.0.33", {"start": v(678.59, 9.41) * mm, "end": v(679.07, 9.9) * mm});
            skLineSegment(sketch, "E92.28.0.34", {"start": v(678.59, -9.41) * mm, "end": v(679.07, -9.9) * mm});
            skLineSegment(sketch, "E92.28.0.35", {"start": v(688.93, -9.9) * mm, "end": v(689.41, -9.41) * mm});
            skLineSegment(sketch, "E92.28.0.36", {"start": v(681.41, 6.59) * mm, "end": v(681.9, 7.07) * mm});
            skLineSegment(sketch, "E92.28.0.37", {"start": v(688.93, 9.9) * mm, "end": v(689.41, 9.41) * mm});
            skLineSegment(sketch, "E92.28.0.38", {"start": v(686.1, 7.07) * mm, "end": v(686.59, 6.59) * mm});
            skLineSegment(sketch, "E92.28.0.39", {"start": v(681.41, -6.59) * mm, "end": v(681.9, -7.07) * mm});
            skArc(sketch, "E92.29.0.0", {"start": v(702.59, 9.41) * mm, "mid": v(702.59, 6.59) * mm, "end": v(705.41, 6.59) * mm});
            skArc(sketch, "E92.29.0.1", {"start": v(705.41, -6.59) * mm, "mid": v(702.59, -6.59) * mm, "end": v(702.59, -9.41) * mm});
            skLineSegment(sketch, "E92.29.0.2", {"start": v(696, 24) * mm, "end": v(720, 24) * mm, "construction": true});
            skLineSegment(sketch, "E92.29.0.3", {"start": v(704, 16) * mm, "end": v(712, 16) * mm, "construction": true});
            skArc(sketch, "E92.29.0.4", {"start": v(703.07, -9.9) * mm, "mid": v(705.9, -9.9) * mm, "end": v(705.9, -7.07) * mm});
            skLineSegment(sketch, "E92.29.0.5", {"start": v(720, 0) * mm, "end": v(696, -24) * mm, "construction": true});
            skCircle(sketch, "E92.29.0.6", {"center": v(712, -16) * mm, "radius": 2 * mm});
            skLineSegment(sketch, "E92.29.0.7", {"start": v(720, -24) * mm, "end": v(696, -24) * mm, "construction": true});
            skCircle(sketch, "E92.29.0.8", {"center": v(704, 16) * mm, "radius": 2 * mm});
            skCircle(sketch, "E92.29.0.9", {"center": v(712, 16) * mm, "radius": 2 * mm});
            skLineSegment(sketch, "E92.29.0.10", {"start": v(720, -24) * mm, "end": v(696, 0) * mm, "construction": true});
            skLineSegment(sketch, "E92.29.0.11", {"start": v(696, 24) * mm, "end": v(720, 0) * mm, "construction": true});
            skLineSegment(sketch, "E92.29.0.12", {"start": v(720, 24) * mm, "end": v(696, 0) * mm, "construction": true});
            skArc(sketch, "E92.29.0.13", {"start": v(712.93, 9.9) * mm, "mid": v(710.1, 9.9) * mm, "end": v(710.1, 7.07) * mm});
            skArc(sketch, "E92.29.0.14", {"start": v(705.9, 7.07) * mm, "mid": v(705.9, 9.9) * mm, "end": v(703.07, 9.9) * mm});
            skArc(sketch, "E92.29.0.15", {"start": v(710.1, -7.07) * mm, "mid": v(710.1, -9.9) * mm, "end": v(712.93, -9.9) * mm});
            skArc(sketch, "E92.29.0.16", {"start": v(710.59, 6.59) * mm, "mid": v(713.41, 6.59) * mm, "end": v(713.41, 9.41) * mm});
            skLineSegment(sketch, "E92.29.0.17", {"start": v(704, -16) * mm, "end": v(712, -16) * mm, "construction": true});
            skLineSegment(sketch, "E92.29.0.18", {"start": v(696, 0) * mm, "end": v(720, 0) * mm, "construction": true});
            skArc(sketch, "E92.29.0.19", {"start": v(713.41, -9.41) * mm, "mid": v(713.41, -6.59) * mm, "end": v(710.59, -6.59) * mm});
            skCircle(sketch, "E92.29.0.20", {"center": v(704, -16) * mm, "radius": 2 * mm});
            skCircle(sketch, "E92.29.0.21", {"center": v(708, 0) * mm, "radius": 2 * mm});
            skPoint(sketch, "E92.29.0.22", {"position": v(704, -8) * mm});
            skLineSegment(sketch, "E92.29.0.23", {"start": v(720, 0) * mm, "end": v(696, 0) * mm, "construction": true});
            skLineSegment(sketch, "E92.29.0.24", {"start": v(710.59, 6.59) * mm, "end": v(713.41, 9.41) * mm, "construction": true});
            skLineSegment(sketch, "E92.29.0.25", {"start": v(710.1, -7.07) * mm, "end": v(712.93, -9.9) * mm, "construction": true});
            skLineSegment(sketch, "E92.29.0.26", {"start": v(702.59, 9.41) * mm, "end": v(705.41, 6.59) * mm, "construction": true});
            skLineSegment(sketch, "E92.29.0.27", {"start": v(703.07, 9.9) * mm, "end": v(705.9, 7.07) * mm, "construction": true});
            skLineSegment(sketch, "E92.29.0.28", {"start": v(712.93, 9.9) * mm, "end": v(710.1, 7.07) * mm, "construction": true});
            skLineSegment(sketch, "E92.29.0.29", {"start": v(710.59, -6.59) * mm, "end": v(713.41, -9.41) * mm, "construction": true});
            skLineSegment(sketch, "E92.29.0.30", {"start": v(703.07, -9.9) * mm, "end": v(705.9, -7.07) * mm, "construction": true});
            skLineSegment(sketch, "E92.29.0.31", {"start": v(705.41, -6.59) * mm, "end": v(702.59, -9.41) * mm, "construction": true});
            skLineSegment(sketch, "E92.29.0.32", {"start": v(710.1, -7.07) * mm, "end": v(710.59, -6.59) * mm});
            skLineSegment(sketch, "E92.29.0.33", {"start": v(702.59, 9.41) * mm, "end": v(703.07, 9.9) * mm});
            skLineSegment(sketch, "E92.29.0.34", {"start": v(702.59, -9.41) * mm, "end": v(703.07, -9.9) * mm});
            skLineSegment(sketch, "E92.29.0.35", {"start": v(712.93, -9.9) * mm, "end": v(713.41, -9.41) * mm});
            skLineSegment(sketch, "E92.29.0.36", {"start": v(705.41, 6.59) * mm, "end": v(705.9, 7.07) * mm});
            skLineSegment(sketch, "E92.29.0.37", {"start": v(712.93, 9.9) * mm, "end": v(713.41, 9.41) * mm});
            skLineSegment(sketch, "E92.29.0.38", {"start": v(710.1, 7.07) * mm, "end": v(710.59, 6.59) * mm});
            skLineSegment(sketch, "E92.29.0.39", {"start": v(705.41, -6.59) * mm, "end": v(705.9, -7.07) * mm});
            skArc(sketch, "E92.30.0.0", {"start": v(726.59, 9.41) * mm, "mid": v(726.59, 6.59) * mm, "end": v(729.41, 6.59) * mm});
            skArc(sketch, "E92.30.0.1", {"start": v(729.41, -6.59) * mm, "mid": v(726.59, -6.59) * mm, "end": v(726.59, -9.41) * mm});
            skLineSegment(sketch, "E92.30.0.2", {"start": v(720, 24) * mm, "end": v(744, 24) * mm, "construction": true});
            skLineSegment(sketch, "E92.30.0.3", {"start": v(728, 16) * mm, "end": v(736, 16) * mm, "construction": true});
            skArc(sketch, "E92.30.0.4", {"start": v(727.07, -9.9) * mm, "mid": v(729.9, -9.9) * mm, "end": v(729.9, -7.07) * mm});
            skLineSegment(sketch, "E92.30.0.5", {"start": v(744, 0) * mm, "end": v(720, -24) * mm, "construction": true});
            skCircle(sketch, "E92.30.0.6", {"center": v(736, -16) * mm, "radius": 2 * mm});
            skLineSegment(sketch, "E92.30.0.7", {"start": v(744, -24) * mm, "end": v(720, -24) * mm, "construction": true});
            skCircle(sketch, "E92.30.0.8", {"center": v(728, 16) * mm, "radius": 2 * mm});
            skCircle(sketch, "E92.30.0.9", {"center": v(736, 16) * mm, "radius": 2 * mm});
            skLineSegment(sketch, "E92.30.0.10", {"start": v(744, -24) * mm, "end": v(720, 0) * mm, "construction": true});
            skLineSegment(sketch, "E92.30.0.11", {"start": v(720, 24) * mm, "end": v(744, 0) * mm, "construction": true});
            skLineSegment(sketch, "E92.30.0.12", {"start": v(744, 24) * mm, "end": v(720, 0) * mm, "construction": true});
            skArc(sketch, "E92.30.0.13", {"start": v(736.93, 9.9) * mm, "mid": v(734.1, 9.9) * mm, "end": v(734.1, 7.07) * mm});
            skArc(sketch, "E92.30.0.14", {"start": v(729.9, 7.07) * mm, "mid": v(729.9, 9.9) * mm, "end": v(727.07, 9.9) * mm});
            skArc(sketch, "E92.30.0.15", {"start": v(734.1, -7.07) * mm, "mid": v(734.1, -9.9) * mm, "end": v(736.93, -9.9) * mm});
            skArc(sketch, "E92.30.0.16", {"start": v(734.59, 6.59) * mm, "mid": v(737.41, 6.59) * mm, "end": v(737.41, 9.41) * mm});
            skLineSegment(sketch, "E92.30.0.17", {"start": v(728, -16) * mm, "end": v(736, -16) * mm, "construction": true});
            skLineSegment(sketch, "E92.30.0.18", {"start": v(720, 0) * mm, "end": v(744, 0) * mm, "construction": true});
            skArc(sketch, "E92.30.0.19", {"start": v(737.41, -9.41) * mm, "mid": v(737.41, -6.59) * mm, "end": v(734.59, -6.59) * mm});
            skCircle(sketch, "E92.30.0.20", {"center": v(728, -16) * mm, "radius": 2 * mm});
            skCircle(sketch, "E92.30.0.21", {"center": v(732, 0) * mm, "radius": 2 * mm});
            skPoint(sketch, "E92.30.0.22", {"position": v(728, -8) * mm});
            skLineSegment(sketch, "E92.30.0.23", {"start": v(744, 0) * mm, "end": v(720, 0) * mm, "construction": true});
            skLineSegment(sketch, "E92.30.0.24", {"start": v(734.59, 6.59) * mm, "end": v(737.41, 9.41) * mm, "construction": true});
            skLineSegment(sketch, "E92.30.0.25", {"start": v(734.1, -7.07) * mm, "end": v(736.93, -9.9) * mm, "construction": true});
            skLineSegment(sketch, "E92.30.0.26", {"start": v(726.59, 9.41) * mm, "end": v(729.41, 6.59) * mm, "construction": true});
            skLineSegment(sketch, "E92.30.0.27", {"start": v(727.07, 9.9) * mm, "end": v(729.9, 7.07) * mm, "construction": true});
            skLineSegment(sketch, "E92.30.0.28", {"start": v(736.93, 9.9) * mm, "end": v(734.1, 7.07) * mm, "construction": true});
            skLineSegment(sketch, "E92.30.0.29", {"start": v(734.59, -6.59) * mm, "end": v(737.41, -9.41) * mm, "construction": true});
            skLineSegment(sketch, "E92.30.0.30", {"start": v(727.07, -9.9) * mm, "end": v(729.9, -7.07) * mm, "construction": true});
            skLineSegment(sketch, "E92.30.0.31", {"start": v(729.41, -6.59) * mm, "end": v(726.59, -9.41) * mm, "construction": true});
            skLineSegment(sketch, "E92.30.0.32", {"start": v(734.1, -7.07) * mm, "end": v(734.59, -6.59) * mm});
            skLineSegment(sketch, "E92.30.0.33", {"start": v(726.59, 9.41) * mm, "end": v(727.07, 9.9) * mm});
            skLineSegment(sketch, "E92.30.0.34", {"start": v(726.59, -9.41) * mm, "end": v(727.07, -9.9) * mm});
            skLineSegment(sketch, "E92.30.0.35", {"start": v(736.93, -9.9) * mm, "end": v(737.41, -9.41) * mm});
            skLineSegment(sketch, "E92.30.0.36", {"start": v(729.41, 6.59) * mm, "end": v(729.9, 7.07) * mm});
            skLineSegment(sketch, "E92.30.0.37", {"start": v(736.93, 9.9) * mm, "end": v(737.41, 9.41) * mm});
            skLineSegment(sketch, "E92.30.0.38", {"start": v(734.1, 7.07) * mm, "end": v(734.59, 6.59) * mm});
            skLineSegment(sketch, "E92.30.0.39", {"start": v(729.41, -6.59) * mm, "end": v(729.9, -7.07) * mm});
            skArc(sketch, "E92.31.0.0", {"start": v(750.59, 9.41) * mm, "mid": v(750.59, 6.59) * mm, "end": v(753.41, 6.59) * mm});
            skArc(sketch, "E92.31.0.1", {"start": v(753.41, -6.59) * mm, "mid": v(750.59, -6.59) * mm, "end": v(750.59, -9.41) * mm});
            skLineSegment(sketch, "E92.31.0.2", {"start": v(744, 24) * mm, "end": v(768, 24) * mm, "construction": true});
            skLineSegment(sketch, "E92.31.0.3", {"start": v(752, 16) * mm, "end": v(760, 16) * mm, "construction": true});
            skArc(sketch, "E92.31.0.4", {"start": v(751.07, -9.9) * mm, "mid": v(753.9, -9.9) * mm, "end": v(753.9, -7.07) * mm});
            skLineSegment(sketch, "E92.31.0.5", {"start": v(768, 0) * mm, "end": v(744, -24) * mm, "construction": true});
            skCircle(sketch, "E92.31.0.6", {"center": v(760, -16) * mm, "radius": 2 * mm});
            skLineSegment(sketch, "E92.31.0.7", {"start": v(768, -24) * mm, "end": v(744, -24) * mm, "construction": true});
            skCircle(sketch, "E92.31.0.8", {"center": v(752, 16) * mm, "radius": 2 * mm});
            skCircle(sketch, "E92.31.0.9", {"center": v(760, 16) * mm, "radius": 2 * mm});
            skLineSegment(sketch, "E92.31.0.10", {"start": v(768, -24) * mm, "end": v(744, 0) * mm, "construction": true});
            skLineSegment(sketch, "E92.31.0.11", {"start": v(744, 24) * mm, "end": v(768, 0) * mm, "construction": true});
            skLineSegment(sketch, "E92.31.0.12", {"start": v(768, 24) * mm, "end": v(744, 0) * mm, "construction": true});
            skArc(sketch, "E92.31.0.13", {"start": v(760.93, 9.9) * mm, "mid": v(758.1, 9.9) * mm, "end": v(758.1, 7.07) * mm});
            skArc(sketch, "E92.31.0.14", {"start": v(753.9, 7.07) * mm, "mid": v(753.9, 9.9) * mm, "end": v(751.07, 9.9) * mm});
            skArc(sketch, "E92.31.0.15", {"start": v(758.1, -7.07) * mm, "mid": v(758.1, -9.9) * mm, "end": v(760.93, -9.9) * mm});
            skArc(sketch, "E92.31.0.16", {"start": v(758.59, 6.59) * mm, "mid": v(761.41, 6.59) * mm, "end": v(761.41, 9.41) * mm});
            skLineSegment(sketch, "E92.31.0.17", {"start": v(752, -16) * mm, "end": v(760, -16) * mm, "construction": true});
            skLineSegment(sketch, "E92.31.0.18", {"start": v(744, 0) * mm, "end": v(768, 0) * mm, "construction": true});
            skArc(sketch, "E92.31.0.19", {"start": v(761.41, -9.41) * mm, "mid": v(761.41, -6.59) * mm, "end": v(758.59, -6.59) * mm});
            skCircle(sketch, "E92.31.0.20", {"center": v(752, -16) * mm, "radius": 2 * mm});
            skCircle(sketch, "E92.31.0.21", {"center": v(756, 0) * mm, "radius": 2 * mm});
            skPoint(sketch, "E92.31.0.22", {"position": v(752, -8) * mm});
            skLineSegment(sketch, "E92.31.0.23", {"start": v(768, 0) * mm, "end": v(744, 0) * mm, "construction": true});
            skLineSegment(sketch, "E92.31.0.24", {"start": v(758.59, 6.59) * mm, "end": v(761.41, 9.41) * mm, "construction": true});
            skLineSegment(sketch, "E92.31.0.25", {"start": v(758.1, -7.07) * mm, "end": v(760.93, -9.9) * mm, "construction": true});
            skLineSegment(sketch, "E92.31.0.26", {"start": v(750.59, 9.41) * mm, "end": v(753.41, 6.59) * mm, "construction": true});
            skLineSegment(sketch, "E92.31.0.27", {"start": v(751.07, 9.9) * mm, "end": v(753.9, 7.07) * mm, "construction": true});
            skLineSegment(sketch, "E92.31.0.28", {"start": v(760.93, 9.9) * mm, "end": v(758.1, 7.07) * mm, "construction": true});
            skLineSegment(sketch, "E92.31.0.29", {"start": v(758.59, -6.59) * mm, "end": v(761.41, -9.41) * mm, "construction": true});
            skLineSegment(sketch, "E92.31.0.30", {"start": v(751.07, -9.9) * mm, "end": v(753.9, -7.07) * mm, "construction": true});
            skLineSegment(sketch, "E92.31.0.31", {"start": v(753.41, -6.59) * mm, "end": v(750.59, -9.41) * mm, "construction": true});
            skLineSegment(sketch, "E92.31.0.32", {"start": v(758.1, -7.07) * mm, "end": v(758.59, -6.59) * mm});
            skLineSegment(sketch, "E92.31.0.33", {"start": v(750.59, 9.41) * mm, "end": v(751.07, 9.9) * mm});
            skLineSegment(sketch, "E92.31.0.34", {"start": v(750.59, -9.41) * mm, "end": v(751.07, -9.9) * mm});
            skLineSegment(sketch, "E92.31.0.35", {"start": v(760.93, -9.9) * mm, "end": v(761.41, -9.41) * mm});
            skLineSegment(sketch, "E92.31.0.36", {"start": v(753.41, 6.59) * mm, "end": v(753.9, 7.07) * mm});
            skLineSegment(sketch, "E92.31.0.37", {"start": v(760.93, 9.9) * mm, "end": v(761.41, 9.41) * mm});
            skLineSegment(sketch, "E92.31.0.38", {"start": v(758.1, 7.07) * mm, "end": v(758.59, 6.59) * mm});
            skLineSegment(sketch, "E92.31.0.39", {"start": v(753.41, -6.59) * mm, "end": v(753.9, -7.07) * mm});
            skArc(sketch, "E92.32.0.0", {"start": v(774.59, 9.41) * mm, "mid": v(774.59, 6.59) * mm, "end": v(777.41, 6.59) * mm});
            skArc(sketch, "E92.32.0.1", {"start": v(777.41, -6.59) * mm, "mid": v(774.59, -6.59) * mm, "end": v(774.59, -9.41) * mm});
            skLineSegment(sketch, "E92.32.0.2", {"start": v(768, 24) * mm, "end": v(792, 24) * mm, "construction": true});
            skLineSegment(sketch, "E92.32.0.3", {"start": v(776, 16) * mm, "end": v(784, 16) * mm, "construction": true});
            skArc(sketch, "E92.32.0.4", {"start": v(775.07, -9.9) * mm, "mid": v(777.9, -9.9) * mm, "end": v(777.9, -7.07) * mm});
            skLineSegment(sketch, "E92.32.0.5", {"start": v(792, 0) * mm, "end": v(768, -24) * mm, "construction": true});
            skCircle(sketch, "E92.32.0.6", {"center": v(784, -16) * mm, "radius": 2 * mm});
            skLineSegment(sketch, "E92.32.0.7", {"start": v(792, -24) * mm, "end": v(768, -24) * mm, "construction": true});
            skCircle(sketch, "E92.32.0.8", {"center": v(776, 16) * mm, "radius": 2 * mm});
            skCircle(sketch, "E92.32.0.9", {"center": v(784, 16) * mm, "radius": 2 * mm});
            skLineSegment(sketch, "E92.32.0.10", {"start": v(792, -24) * mm, "end": v(768, 0) * mm, "construction": true});
            skLineSegment(sketch, "E92.32.0.11", {"start": v(768, 24) * mm, "end": v(792, 0) * mm, "construction": true});
            skLineSegment(sketch, "E92.32.0.12", {"start": v(792, 24) * mm, "end": v(768, 0) * mm, "construction": true});
            skArc(sketch, "E92.32.0.13", {"start": v(784.93, 9.9) * mm, "mid": v(782.1, 9.9) * mm, "end": v(782.1, 7.07) * mm});
            skArc(sketch, "E92.32.0.14", {"start": v(777.9, 7.07) * mm, "mid": v(777.9, 9.9) * mm, "end": v(775.07, 9.9) * mm});
            skArc(sketch, "E92.32.0.15", {"start": v(782.1, -7.07) * mm, "mid": v(782.1, -9.9) * mm, "end": v(784.93, -9.9) * mm});
            skArc(sketch, "E92.32.0.16", {"start": v(782.59, 6.59) * mm, "mid": v(785.41, 6.59) * mm, "end": v(785.41, 9.41) * mm});
            skLineSegment(sketch, "E92.32.0.17", {"start": v(776, -16) * mm, "end": v(784, -16) * mm, "construction": true});
            skLineSegment(sketch, "E92.32.0.18", {"start": v(768, 0) * mm, "end": v(792, 0) * mm, "construction": true});
            skArc(sketch, "E92.32.0.19", {"start": v(785.41, -9.41) * mm, "mid": v(785.41, -6.59) * mm, "end": v(782.59, -6.59) * mm});
            skCircle(sketch, "E92.32.0.20", {"center": v(776, -16) * mm, "radius": 2 * mm});
            skCircle(sketch, "E92.32.0.21", {"center": v(780, 0) * mm, "radius": 2 * mm});
            skPoint(sketch, "E92.32.0.22", {"position": v(776, -8) * mm});
            skLineSegment(sketch, "E92.32.0.23", {"start": v(792, 0) * mm, "end": v(768, 0) * mm, "construction": true});
            skLineSegment(sketch, "E92.32.0.24", {"start": v(782.59, 6.59) * mm, "end": v(785.41, 9.41) * mm, "construction": true});
            skLineSegment(sketch, "E92.32.0.25", {"start": v(782.1, -7.07) * mm, "end": v(784.93, -9.9) * mm, "construction": true});
            skLineSegment(sketch, "E92.32.0.26", {"start": v(774.59, 9.41) * mm, "end": v(777.41, 6.59) * mm, "construction": true});
            skLineSegment(sketch, "E92.32.0.27", {"start": v(775.07, 9.9) * mm, "end": v(777.9, 7.07) * mm, "construction": true});
            skLineSegment(sketch, "E92.32.0.28", {"start": v(784.93, 9.9) * mm, "end": v(782.1, 7.07) * mm, "construction": true});
            skLineSegment(sketch, "E92.32.0.29", {"start": v(782.59, -6.59) * mm, "end": v(785.41, -9.41) * mm, "construction": true});
            skLineSegment(sketch, "E92.32.0.30", {"start": v(775.07, -9.9) * mm, "end": v(777.9, -7.07) * mm, "construction": true});
            skLineSegment(sketch, "E92.32.0.31", {"start": v(777.41, -6.59) * mm, "end": v(774.59, -9.41) * mm, "construction": true});
            skLineSegment(sketch, "E92.32.0.32", {"start": v(782.1, -7.07) * mm, "end": v(782.59, -6.59) * mm});
            skLineSegment(sketch, "E92.32.0.33", {"start": v(774.59, 9.41) * mm, "end": v(775.07, 9.9) * mm});
            skLineSegment(sketch, "E92.32.0.34", {"start": v(774.59, -9.41) * mm, "end": v(775.07, -9.9) * mm});
            skLineSegment(sketch, "E92.32.0.35", {"start": v(784.93, -9.9) * mm, "end": v(785.41, -9.41) * mm});
            skLineSegment(sketch, "E92.32.0.36", {"start": v(777.41, 6.59) * mm, "end": v(777.9, 7.07) * mm});
            skLineSegment(sketch, "E92.32.0.37", {"start": v(784.93, 9.9) * mm, "end": v(785.41, 9.41) * mm});
            skLineSegment(sketch, "E92.32.0.38", {"start": v(782.1, 7.07) * mm, "end": v(782.59, 6.59) * mm});
            skLineSegment(sketch, "E92.32.0.39", {"start": v(777.41, -6.59) * mm, "end": v(777.9, -7.07) * mm});
            skArc(sketch, "E92.33.0.0", {"start": v(798.59, 9.41) * mm, "mid": v(798.59, 6.59) * mm, "end": v(801.41, 6.59) * mm});
            skArc(sketch, "E92.33.0.1", {"start": v(801.41, -6.59) * mm, "mid": v(798.59, -6.59) * mm, "end": v(798.59, -9.41) * mm});
            skLineSegment(sketch, "E92.33.0.2", {"start": v(792, 24) * mm, "end": v(816, 24) * mm, "construction": true});
            skLineSegment(sketch, "E92.33.0.3", {"start": v(800, 16) * mm, "end": v(808, 16) * mm, "construction": true});
            skArc(sketch, "E92.33.0.4", {"start": v(799.07, -9.9) * mm, "mid": v(801.9, -9.9) * mm, "end": v(801.9, -7.07) * mm});
            skLineSegment(sketch, "E92.33.0.5", {"start": v(816, 0) * mm, "end": v(792, -24) * mm, "construction": true});
            skCircle(sketch, "E92.33.0.6", {"center": v(808, -16) * mm, "radius": 2 * mm});
            skLineSegment(sketch, "E92.33.0.7", {"start": v(816, -24) * mm, "end": v(792, -24) * mm, "construction": true});
            skCircle(sketch, "E92.33.0.8", {"center": v(800, 16) * mm, "radius": 2 * mm});
            skCircle(sketch, "E92.33.0.9", {"center": v(808, 16) * mm, "radius": 2 * mm});
            skLineSegment(sketch, "E92.33.0.10", {"start": v(816, -24) * mm, "end": v(792, 0) * mm, "construction": true});
            skLineSegment(sketch, "E92.33.0.11", {"start": v(792, 24) * mm, "end": v(816, 0) * mm, "construction": true});
            skLineSegment(sketch, "E92.33.0.12", {"start": v(816, 24) * mm, "end": v(792, 0) * mm, "construction": true});
            skArc(sketch, "E92.33.0.13", {"start": v(808.93, 9.9) * mm, "mid": v(806.1, 9.9) * mm, "end": v(806.1, 7.07) * mm});
            skArc(sketch, "E92.33.0.14", {"start": v(801.9, 7.07) * mm, "mid": v(801.9, 9.9) * mm, "end": v(799.07, 9.9) * mm});
            skArc(sketch, "E92.33.0.15", {"start": v(806.1, -7.07) * mm, "mid": v(806.1, -9.9) * mm, "end": v(808.93, -9.9) * mm});
            skArc(sketch, "E92.33.0.16", {"start": v(806.59, 6.59) * mm, "mid": v(809.41, 6.59) * mm, "end": v(809.41, 9.41) * mm});
            skLineSegment(sketch, "E92.33.0.17", {"start": v(800, -16) * mm, "end": v(808, -16) * mm, "construction": true});
            skLineSegment(sketch, "E92.33.0.18", {"start": v(792, 0) * mm, "end": v(816, 0) * mm, "construction": true});
            skArc(sketch, "E92.33.0.19", {"start": v(809.41, -9.41) * mm, "mid": v(809.41, -6.59) * mm, "end": v(806.59, -6.59) * mm});
            skCircle(sketch, "E92.33.0.20", {"center": v(800, -16) * mm, "radius": 2 * mm});
            skCircle(sketch, "E92.33.0.21", {"center": v(804, 0) * mm, "radius": 2 * mm});
            skPoint(sketch, "E92.33.0.22", {"position": v(800, -8) * mm});
            skLineSegment(sketch, "E92.33.0.23", {"start": v(816, 0) * mm, "end": v(792, 0) * mm, "construction": true});
            skLineSegment(sketch, "E92.33.0.24", {"start": v(806.59, 6.59) * mm, "end": v(809.41, 9.41) * mm, "construction": true});
            skLineSegment(sketch, "E92.33.0.25", {"start": v(806.1, -7.07) * mm, "end": v(808.93, -9.9) * mm, "construction": true});
            skLineSegment(sketch, "E92.33.0.26", {"start": v(798.59, 9.41) * mm, "end": v(801.41, 6.59) * mm, "construction": true});
            skLineSegment(sketch, "E92.33.0.27", {"start": v(799.07, 9.9) * mm, "end": v(801.9, 7.07) * mm, "construction": true});
            skLineSegment(sketch, "E92.33.0.28", {"start": v(808.93, 9.9) * mm, "end": v(806.1, 7.07) * mm, "construction": true});
            skLineSegment(sketch, "E92.33.0.29", {"start": v(806.59, -6.59) * mm, "end": v(809.41, -9.41) * mm, "construction": true});
            skLineSegment(sketch, "E92.33.0.30", {"start": v(799.07, -9.9) * mm, "end": v(801.9, -7.07) * mm, "construction": true});
            skLineSegment(sketch, "E92.33.0.31", {"start": v(801.41, -6.59) * mm, "end": v(798.59, -9.41) * mm, "construction": true});
            skLineSegment(sketch, "E92.33.0.32", {"start": v(806.1, -7.07) * mm, "end": v(806.59, -6.59) * mm});
            skLineSegment(sketch, "E92.33.0.33", {"start": v(798.59, 9.41) * mm, "end": v(799.07, 9.9) * mm});
            skLineSegment(sketch, "E92.33.0.34", {"start": v(798.59, -9.41) * mm, "end": v(799.07, -9.9) * mm});
            skLineSegment(sketch, "E92.33.0.35", {"start": v(808.93, -9.9) * mm, "end": v(809.41, -9.41) * mm});
            skLineSegment(sketch, "E92.33.0.36", {"start": v(801.41, 6.59) * mm, "end": v(801.9, 7.07) * mm});
            skLineSegment(sketch, "E92.33.0.37", {"start": v(808.93, 9.9) * mm, "end": v(809.41, 9.41) * mm});
            skLineSegment(sketch, "E92.33.0.38", {"start": v(806.1, 7.07) * mm, "end": v(806.59, 6.59) * mm});
            skLineSegment(sketch, "E92.33.0.39", {"start": v(801.41, -6.59) * mm, "end": v(801.9, -7.07) * mm});
            skArc(sketch, "E92.34.0.0", {"start": v(822.59, 9.41) * mm, "mid": v(822.59, 6.59) * mm, "end": v(825.41, 6.59) * mm});
            skArc(sketch, "E92.34.0.1", {"start": v(825.41, -6.59) * mm, "mid": v(822.59, -6.59) * mm, "end": v(822.59, -9.41) * mm});
            skLineSegment(sketch, "E92.34.0.2", {"start": v(816, 24) * mm, "end": v(840, 24) * mm, "construction": true});
            skLineSegment(sketch, "E92.34.0.3", {"start": v(824, 16) * mm, "end": v(832, 16) * mm, "construction": true});
            skArc(sketch, "E92.34.0.4", {"start": v(823.07, -9.9) * mm, "mid": v(825.9, -9.9) * mm, "end": v(825.9, -7.07) * mm});
            skLineSegment(sketch, "E92.34.0.5", {"start": v(840, 0) * mm, "end": v(816, -24) * mm, "construction": true});
            skCircle(sketch, "E92.34.0.6", {"center": v(832, -16) * mm, "radius": 2 * mm});
            skLineSegment(sketch, "E92.34.0.7", {"start": v(840, -24) * mm, "end": v(816, -24) * mm, "construction": true});
            skCircle(sketch, "E92.34.0.8", {"center": v(824, 16) * mm, "radius": 2 * mm});
            skCircle(sketch, "E92.34.0.9", {"center": v(832, 16) * mm, "radius": 2 * mm});
            skLineSegment(sketch, "E92.34.0.10", {"start": v(840, -24) * mm, "end": v(816, 0) * mm, "construction": true});
            skLineSegment(sketch, "E92.34.0.11", {"start": v(816, 24) * mm, "end": v(840, 0) * mm, "construction": true});
            skLineSegment(sketch, "E92.34.0.12", {"start": v(840, 24) * mm, "end": v(816, 0) * mm, "construction": true});
            skArc(sketch, "E92.34.0.13", {"start": v(832.93, 9.9) * mm, "mid": v(830.1, 9.9) * mm, "end": v(830.1, 7.07) * mm});
            skArc(sketch, "E92.34.0.14", {"start": v(825.9, 7.07) * mm, "mid": v(825.9, 9.9) * mm, "end": v(823.07, 9.9) * mm});
            skArc(sketch, "E92.34.0.15", {"start": v(830.1, -7.07) * mm, "mid": v(830.1, -9.9) * mm, "end": v(832.93, -9.9) * mm});
            skArc(sketch, "E92.34.0.16", {"start": v(830.59, 6.59) * mm, "mid": v(833.41, 6.59) * mm, "end": v(833.41, 9.41) * mm});
            skLineSegment(sketch, "E92.34.0.17", {"start": v(824, -16) * mm, "end": v(832, -16) * mm, "construction": true});
            skLineSegment(sketch, "E92.34.0.18", {"start": v(816, 0) * mm, "end": v(840, 0) * mm, "construction": true});
            skArc(sketch, "E92.34.0.19", {"start": v(833.41, -9.41) * mm, "mid": v(833.41, -6.59) * mm, "end": v(830.59, -6.59) * mm});
            skCircle(sketch, "E92.34.0.20", {"center": v(824, -16) * mm, "radius": 2 * mm});
            skCircle(sketch, "E92.34.0.21", {"center": v(828, 0) * mm, "radius": 2 * mm});
            skPoint(sketch, "E92.34.0.22", {"position": v(824, -8) * mm});
            skLineSegment(sketch, "E92.34.0.23", {"start": v(840, 0) * mm, "end": v(816, 0) * mm, "construction": true});
            skLineSegment(sketch, "E92.34.0.24", {"start": v(830.59, 6.59) * mm, "end": v(833.41, 9.41) * mm, "construction": true});
            skLineSegment(sketch, "E92.34.0.25", {"start": v(830.1, -7.07) * mm, "end": v(832.93, -9.9) * mm, "construction": true});
            skLineSegment(sketch, "E92.34.0.26", {"start": v(822.59, 9.41) * mm, "end": v(825.41, 6.59) * mm, "construction": true});
            skLineSegment(sketch, "E92.34.0.27", {"start": v(823.07, 9.9) * mm, "end": v(825.9, 7.07) * mm, "construction": true});
            skLineSegment(sketch, "E92.34.0.28", {"start": v(832.93, 9.9) * mm, "end": v(830.1, 7.07) * mm, "construction": true});
            skLineSegment(sketch, "E92.34.0.29", {"start": v(830.59, -6.59) * mm, "end": v(833.41, -9.41) * mm, "construction": true});
            skLineSegment(sketch, "E92.34.0.30", {"start": v(823.07, -9.9) * mm, "end": v(825.9, -7.07) * mm, "construction": true});
            skLineSegment(sketch, "E92.34.0.31", {"start": v(825.41, -6.59) * mm, "end": v(822.59, -9.41) * mm, "construction": true});
            skLineSegment(sketch, "E92.34.0.32", {"start": v(830.1, -7.07) * mm, "end": v(830.59, -6.59) * mm});
            skLineSegment(sketch, "E92.34.0.33", {"start": v(822.59, 9.41) * mm, "end": v(823.07, 9.9) * mm});
            skLineSegment(sketch, "E92.34.0.34", {"start": v(822.59, -9.41) * mm, "end": v(823.07, -9.9) * mm});
            skLineSegment(sketch, "E92.34.0.35", {"start": v(832.93, -9.9) * mm, "end": v(833.41, -9.41) * mm});
            skLineSegment(sketch, "E92.34.0.36", {"start": v(825.41, 6.59) * mm, "end": v(825.9, 7.07) * mm});
            skLineSegment(sketch, "E92.34.0.37", {"start": v(832.93, 9.9) * mm, "end": v(833.41, 9.41) * mm});
            skLineSegment(sketch, "E92.34.0.38", {"start": v(830.1, 7.07) * mm, "end": v(830.59, 6.59) * mm});
            skLineSegment(sketch, "E92.34.0.39", {"start": v(825.41, -6.59) * mm, "end": v(825.9, -7.07) * mm});
            skArc(sketch, "E92.35.0.0", {"start": v(846.59, 9.41) * mm, "mid": v(846.59, 6.59) * mm, "end": v(849.41, 6.59) * mm});
            skArc(sketch, "E92.35.0.1", {"start": v(849.41, -6.59) * mm, "mid": v(846.59, -6.59) * mm, "end": v(846.59, -9.41) * mm});
            skLineSegment(sketch, "E92.35.0.2", {"start": v(840, 24) * mm, "end": v(864, 24) * mm, "construction": true});
            skLineSegment(sketch, "E92.35.0.3", {"start": v(848, 16) * mm, "end": v(856, 16) * mm, "construction": true});
            skArc(sketch, "E92.35.0.4", {"start": v(847.07, -9.9) * mm, "mid": v(849.9, -9.9) * mm, "end": v(849.9, -7.07) * mm});
            skLineSegment(sketch, "E92.35.0.5", {"start": v(864, 0) * mm, "end": v(840, -24) * mm, "construction": true});
            skCircle(sketch, "E92.35.0.6", {"center": v(856, -16) * mm, "radius": 2 * mm});
            skLineSegment(sketch, "E92.35.0.7", {"start": v(864, -24) * mm, "end": v(840, -24) * mm, "construction": true});
            skCircle(sketch, "E92.35.0.8", {"center": v(848, 16) * mm, "radius": 2 * mm});
            skCircle(sketch, "E92.35.0.9", {"center": v(856, 16) * mm, "radius": 2 * mm});
            skLineSegment(sketch, "E92.35.0.10", {"start": v(864, -24) * mm, "end": v(840, 0) * mm, "construction": true});
            skLineSegment(sketch, "E92.35.0.11", {"start": v(840, 24) * mm, "end": v(864, 0) * mm, "construction": true});
            skLineSegment(sketch, "E92.35.0.12", {"start": v(864, 24) * mm, "end": v(840, 0) * mm, "construction": true});
            skArc(sketch, "E92.35.0.13", {"start": v(856.93, 9.9) * mm, "mid": v(854.1, 9.9) * mm, "end": v(854.1, 7.07) * mm});
            skArc(sketch, "E92.35.0.14", {"start": v(849.9, 7.07) * mm, "mid": v(849.9, 9.9) * mm, "end": v(847.07, 9.9) * mm});
            skArc(sketch, "E92.35.0.15", {"start": v(854.1, -7.07) * mm, "mid": v(854.1, -9.9) * mm, "end": v(856.93, -9.9) * mm});
            skArc(sketch, "E92.35.0.16", {"start": v(854.59, 6.59) * mm, "mid": v(857.41, 6.59) * mm, "end": v(857.41, 9.41) * mm});
            skLineSegment(sketch, "E92.35.0.17", {"start": v(848, -16) * mm, "end": v(856, -16) * mm, "construction": true});
            skLineSegment(sketch, "E92.35.0.18", {"start": v(840, 0) * mm, "end": v(864, 0) * mm, "construction": true});
            skArc(sketch, "E92.35.0.19", {"start": v(857.41, -9.41) * mm, "mid": v(857.41, -6.59) * mm, "end": v(854.59, -6.59) * mm});
            skCircle(sketch, "E92.35.0.20", {"center": v(848, -16) * mm, "radius": 2 * mm});
            skCircle(sketch, "E92.35.0.21", {"center": v(852, 0) * mm, "radius": 2 * mm});
            skPoint(sketch, "E92.35.0.22", {"position": v(848, -8) * mm});
            skLineSegment(sketch, "E92.35.0.23", {"start": v(864, 0) * mm, "end": v(840, 0) * mm, "construction": true});
            skLineSegment(sketch, "E92.35.0.24", {"start": v(854.59, 6.59) * mm, "end": v(857.41, 9.41) * mm, "construction": true});
            skLineSegment(sketch, "E92.35.0.25", {"start": v(854.1, -7.07) * mm, "end": v(856.93, -9.9) * mm, "construction": true});
            skLineSegment(sketch, "E92.35.0.26", {"start": v(846.59, 9.41) * mm, "end": v(849.41, 6.59) * mm, "construction": true});
            skLineSegment(sketch, "E92.35.0.27", {"start": v(847.07, 9.9) * mm, "end": v(849.9, 7.07) * mm, "construction": true});
            skLineSegment(sketch, "E92.35.0.28", {"start": v(856.93, 9.9) * mm, "end": v(854.1, 7.07) * mm, "construction": true});
            skLineSegment(sketch, "E92.35.0.29", {"start": v(854.59, -6.59) * mm, "end": v(857.41, -9.41) * mm, "construction": true});
            skLineSegment(sketch, "E92.35.0.30", {"start": v(847.07, -9.9) * mm, "end": v(849.9, -7.07) * mm, "construction": true});
            skLineSegment(sketch, "E92.35.0.31", {"start": v(849.41, -6.59) * mm, "end": v(846.59, -9.41) * mm, "construction": true});
            skLineSegment(sketch, "E92.35.0.32", {"start": v(854.1, -7.07) * mm, "end": v(854.59, -6.59) * mm});
            skLineSegment(sketch, "E92.35.0.33", {"start": v(846.59, 9.41) * mm, "end": v(847.07, 9.9) * mm});
            skLineSegment(sketch, "E92.35.0.34", {"start": v(846.59, -9.41) * mm, "end": v(847.07, -9.9) * mm});
            skLineSegment(sketch, "E92.35.0.35", {"start": v(856.93, -9.9) * mm, "end": v(857.41, -9.41) * mm});
            skLineSegment(sketch, "E92.35.0.36", {"start": v(849.41, 6.59) * mm, "end": v(849.9, 7.07) * mm});
            skLineSegment(sketch, "E92.35.0.37", {"start": v(856.93, 9.9) * mm, "end": v(857.41, 9.41) * mm});
            skLineSegment(sketch, "E92.35.0.38", {"start": v(854.1, 7.07) * mm, "end": v(854.59, 6.59) * mm});
            skLineSegment(sketch, "E92.35.0.39", {"start": v(849.41, -6.59) * mm, "end": v(849.9, -7.07) * mm});
            skArc(sketch, "E92.36.0.0", {"start": v(870.59, 9.41) * mm, "mid": v(870.59, 6.59) * mm, "end": v(873.41, 6.59) * mm});
            skArc(sketch, "E92.36.0.1", {"start": v(873.41, -6.59) * mm, "mid": v(870.59, -6.59) * mm, "end": v(870.59, -9.41) * mm});
            skLineSegment(sketch, "E92.36.0.2", {"start": v(864, 24) * mm, "end": v(888, 24) * mm, "construction": true});
            skLineSegment(sketch, "E92.36.0.3", {"start": v(872, 16) * mm, "end": v(880, 16) * mm, "construction": true});
            skArc(sketch, "E92.36.0.4", {"start": v(871.07, -9.9) * mm, "mid": v(873.9, -9.9) * mm, "end": v(873.9, -7.07) * mm});
            skLineSegment(sketch, "E92.36.0.5", {"start": v(888, 0) * mm, "end": v(864, -24) * mm, "construction": true});
            skCircle(sketch, "E92.36.0.6", {"center": v(880, -16) * mm, "radius": 2 * mm});
            skLineSegment(sketch, "E92.36.0.7", {"start": v(888, -24) * mm, "end": v(864, -24) * mm, "construction": true});
            skCircle(sketch, "E92.36.0.8", {"center": v(872, 16) * mm, "radius": 2 * mm});
            skCircle(sketch, "E92.36.0.9", {"center": v(880, 16) * mm, "radius": 2 * mm});
            skLineSegment(sketch, "E92.36.0.10", {"start": v(888, -24) * mm, "end": v(864, 0) * mm, "construction": true});
            skLineSegment(sketch, "E92.36.0.11", {"start": v(864, 24) * mm, "end": v(888, 0) * mm, "construction": true});
            skLineSegment(sketch, "E92.36.0.12", {"start": v(888, 24) * mm, "end": v(864, 0) * mm, "construction": true});
            skArc(sketch, "E92.36.0.13", {"start": v(880.93, 9.9) * mm, "mid": v(878.1, 9.9) * mm, "end": v(878.1, 7.07) * mm});
            skArc(sketch, "E92.36.0.14", {"start": v(873.9, 7.07) * mm, "mid": v(873.9, 9.9) * mm, "end": v(871.07, 9.9) * mm});
            skArc(sketch, "E92.36.0.15", {"start": v(878.1, -7.07) * mm, "mid": v(878.1, -9.9) * mm, "end": v(880.93, -9.9) * mm});
            skArc(sketch, "E92.36.0.16", {"start": v(878.59, 6.59) * mm, "mid": v(881.41, 6.59) * mm, "end": v(881.41, 9.41) * mm});
            skLineSegment(sketch, "E92.36.0.17", {"start": v(872, -16) * mm, "end": v(880, -16) * mm, "construction": true});
            skLineSegment(sketch, "E92.36.0.18", {"start": v(864, 0) * mm, "end": v(888, 0) * mm, "construction": true});
            skArc(sketch, "E92.36.0.19", {"start": v(881.41, -9.41) * mm, "mid": v(881.41, -6.59) * mm, "end": v(878.59, -6.59) * mm});
            skCircle(sketch, "E92.36.0.20", {"center": v(872, -16) * mm, "radius": 2 * mm});
            skCircle(sketch, "E92.36.0.21", {"center": v(876, 0) * mm, "radius": 2 * mm});
            skPoint(sketch, "E92.36.0.22", {"position": v(872, -8) * mm});
            skLineSegment(sketch, "E92.36.0.23", {"start": v(888, 0) * mm, "end": v(864, 0) * mm, "construction": true});
            skLineSegment(sketch, "E92.36.0.24", {"start": v(878.59, 6.59) * mm, "end": v(881.41, 9.41) * mm, "construction": true});
            skLineSegment(sketch, "E92.36.0.25", {"start": v(878.1, -7.07) * mm, "end": v(880.93, -9.9) * mm, "construction": true});
            skLineSegment(sketch, "E92.36.0.26", {"start": v(870.59, 9.41) * mm, "end": v(873.41, 6.59) * mm, "construction": true});
            skLineSegment(sketch, "E92.36.0.27", {"start": v(871.07, 9.9) * mm, "end": v(873.9, 7.07) * mm, "construction": true});
            skLineSegment(sketch, "E92.36.0.28", {"start": v(880.93, 9.9) * mm, "end": v(878.1, 7.07) * mm, "construction": true});
            skLineSegment(sketch, "E92.36.0.29", {"start": v(878.59, -6.59) * mm, "end": v(881.41, -9.41) * mm, "construction": true});
            skLineSegment(sketch, "E92.36.0.30", {"start": v(871.07, -9.9) * mm, "end": v(873.9, -7.07) * mm, "construction": true});
            skLineSegment(sketch, "E92.36.0.31", {"start": v(873.41, -6.59) * mm, "end": v(870.59, -9.41) * mm, "construction": true});
            skLineSegment(sketch, "E92.36.0.32", {"start": v(878.1, -7.07) * mm, "end": v(878.59, -6.59) * mm});
            skLineSegment(sketch, "E92.36.0.33", {"start": v(870.59, 9.41) * mm, "end": v(871.07, 9.9) * mm});
            skLineSegment(sketch, "E92.36.0.34", {"start": v(870.59, -9.41) * mm, "end": v(871.07, -9.9) * mm});
            skLineSegment(sketch, "E92.36.0.35", {"start": v(880.93, -9.9) * mm, "end": v(881.41, -9.41) * mm});
            skLineSegment(sketch, "E92.36.0.36", {"start": v(873.41, 6.59) * mm, "end": v(873.9, 7.07) * mm});
            skLineSegment(sketch, "E92.36.0.37", {"start": v(880.93, 9.9) * mm, "end": v(881.41, 9.41) * mm});
            skLineSegment(sketch, "E92.36.0.38", {"start": v(878.1, 7.07) * mm, "end": v(878.59, 6.59) * mm});
            skLineSegment(sketch, "E92.36.0.39", {"start": v(873.41, -6.59) * mm, "end": v(873.9, -7.07) * mm});
            skArc(sketch, "E92.37.0.0", {"start": v(894.59, 9.41) * mm, "mid": v(894.59, 6.59) * mm, "end": v(897.41, 6.59) * mm});
            skArc(sketch, "E92.37.0.1", {"start": v(897.41, -6.59) * mm, "mid": v(894.59, -6.59) * mm, "end": v(894.59, -9.41) * mm});
            skLineSegment(sketch, "E92.37.0.2", {"start": v(888, 24) * mm, "end": v(912, 24) * mm, "construction": true});
            skLineSegment(sketch, "E92.37.0.3", {"start": v(896, 16) * mm, "end": v(904, 16) * mm, "construction": true});
            skArc(sketch, "E92.37.0.4", {"start": v(895.07, -9.9) * mm, "mid": v(897.9, -9.9) * mm, "end": v(897.9, -7.07) * mm});
            skLineSegment(sketch, "E92.37.0.5", {"start": v(912, 0) * mm, "end": v(888, -24) * mm, "construction": true});
            skCircle(sketch, "E92.37.0.6", {"center": v(904, -16) * mm, "radius": 2 * mm});
            skLineSegment(sketch, "E92.37.0.7", {"start": v(912, -24) * mm, "end": v(888, -24) * mm, "construction": true});
            skCircle(sketch, "E92.37.0.8", {"center": v(896, 16) * mm, "radius": 2 * mm});
            skCircle(sketch, "E92.37.0.9", {"center": v(904, 16) * mm, "radius": 2 * mm});
            skLineSegment(sketch, "E92.37.0.10", {"start": v(912, -24) * mm, "end": v(888, 0) * mm, "construction": true});
            skLineSegment(sketch, "E92.37.0.11", {"start": v(888, 24) * mm, "end": v(912, 0) * mm, "construction": true});
            skLineSegment(sketch, "E92.37.0.12", {"start": v(912, 24) * mm, "end": v(888, 0) * mm, "construction": true});
            skArc(sketch, "E92.37.0.13", {"start": v(904.93, 9.9) * mm, "mid": v(902.1, 9.9) * mm, "end": v(902.1, 7.07) * mm});
            skArc(sketch, "E92.37.0.14", {"start": v(897.9, 7.07) * mm, "mid": v(897.9, 9.9) * mm, "end": v(895.07, 9.9) * mm});
            skArc(sketch, "E92.37.0.15", {"start": v(902.1, -7.07) * mm, "mid": v(902.1, -9.9) * mm, "end": v(904.93, -9.9) * mm});
            skArc(sketch, "E92.37.0.16", {"start": v(902.59, 6.59) * mm, "mid": v(905.41, 6.59) * mm, "end": v(905.41, 9.41) * mm});
            skLineSegment(sketch, "E92.37.0.17", {"start": v(896, -16) * mm, "end": v(904, -16) * mm, "construction": true});
            skLineSegment(sketch, "E92.37.0.18", {"start": v(888, 0) * mm, "end": v(912, 0) * mm, "construction": true});
            skArc(sketch, "E92.37.0.19", {"start": v(905.41, -9.41) * mm, "mid": v(905.41, -6.59) * mm, "end": v(902.59, -6.59) * mm});
            skCircle(sketch, "E92.37.0.20", {"center": v(896, -16) * mm, "radius": 2 * mm});
            skCircle(sketch, "E92.37.0.21", {"center": v(900, 0) * mm, "radius": 2 * mm});
            skPoint(sketch, "E92.37.0.22", {"position": v(896, -8) * mm});
            skLineSegment(sketch, "E92.37.0.23", {"start": v(912, 0) * mm, "end": v(888, 0) * mm, "construction": true});
            skLineSegment(sketch, "E92.37.0.24", {"start": v(902.59, 6.59) * mm, "end": v(905.41, 9.41) * mm, "construction": true});
            skLineSegment(sketch, "E92.37.0.25", {"start": v(902.1, -7.07) * mm, "end": v(904.93, -9.9) * mm, "construction": true});
            skLineSegment(sketch, "E92.37.0.26", {"start": v(894.59, 9.41) * mm, "end": v(897.41, 6.59) * mm, "construction": true});
            skLineSegment(sketch, "E92.37.0.27", {"start": v(895.07, 9.9) * mm, "end": v(897.9, 7.07) * mm, "construction": true});
            skLineSegment(sketch, "E92.37.0.28", {"start": v(904.93, 9.9) * mm, "end": v(902.1, 7.07) * mm, "construction": true});
            skLineSegment(sketch, "E92.37.0.29", {"start": v(902.59, -6.59) * mm, "end": v(905.41, -9.41) * mm, "construction": true});
            skLineSegment(sketch, "E92.37.0.30", {"start": v(895.07, -9.9) * mm, "end": v(897.9, -7.07) * mm, "construction": true});
            skLineSegment(sketch, "E92.37.0.31", {"start": v(897.41, -6.59) * mm, "end": v(894.59, -9.41) * mm, "construction": true});
            skLineSegment(sketch, "E92.37.0.32", {"start": v(902.1, -7.07) * mm, "end": v(902.59, -6.59) * mm});
            skLineSegment(sketch, "E92.37.0.33", {"start": v(894.59, 9.41) * mm, "end": v(895.07, 9.9) * mm});
            skLineSegment(sketch, "E92.37.0.34", {"start": v(894.59, -9.41) * mm, "end": v(895.07, -9.9) * mm});
            skLineSegment(sketch, "E92.37.0.35", {"start": v(904.93, -9.9) * mm, "end": v(905.41, -9.41) * mm});
            skLineSegment(sketch, "E92.37.0.36", {"start": v(897.41, 6.59) * mm, "end": v(897.9, 7.07) * mm});
            skLineSegment(sketch, "E92.37.0.37", {"start": v(904.93, 9.9) * mm, "end": v(905.41, 9.41) * mm});
            skLineSegment(sketch, "E92.37.0.38", {"start": v(902.1, 7.07) * mm, "end": v(902.59, 6.59) * mm});
            skLineSegment(sketch, "E92.37.0.39", {"start": v(897.41, -6.59) * mm, "end": v(897.9, -7.07) * mm});
            skArc(sketch, "E92.38.0.0", {"start": v(918.59, 9.41) * mm, "mid": v(918.59, 6.59) * mm, "end": v(921.41, 6.59) * mm});
            skArc(sketch, "E92.38.0.1", {"start": v(921.41, -6.59) * mm, "mid": v(918.59, -6.59) * mm, "end": v(918.59, -9.41) * mm});
            skLineSegment(sketch, "E92.38.0.2", {"start": v(912, 24) * mm, "end": v(936, 24) * mm, "construction": true});
            skLineSegment(sketch, "E92.38.0.3", {"start": v(920, 16) * mm, "end": v(928, 16) * mm, "construction": true});
            skArc(sketch, "E92.38.0.4", {"start": v(919.07, -9.9) * mm, "mid": v(921.9, -9.9) * mm, "end": v(921.9, -7.07) * mm});
            skLineSegment(sketch, "E92.38.0.5", {"start": v(936, 0) * mm, "end": v(912, -24) * mm, "construction": true});
            skCircle(sketch, "E92.38.0.6", {"center": v(928, -16) * mm, "radius": 2 * mm});
            skLineSegment(sketch, "E92.38.0.7", {"start": v(936, -24) * mm, "end": v(912, -24) * mm, "construction": true});
            skCircle(sketch, "E92.38.0.8", {"center": v(920, 16) * mm, "radius": 2 * mm});
            skCircle(sketch, "E92.38.0.9", {"center": v(928, 16) * mm, "radius": 2 * mm});
            skLineSegment(sketch, "E92.38.0.10", {"start": v(936, -24) * mm, "end": v(912, 0) * mm, "construction": true});
            skLineSegment(sketch, "E92.38.0.11", {"start": v(912, 24) * mm, "end": v(936, 0) * mm, "construction": true});
            skLineSegment(sketch, "E92.38.0.12", {"start": v(936, 24) * mm, "end": v(912, 0) * mm, "construction": true});
            skArc(sketch, "E92.38.0.13", {"start": v(928.93, 9.9) * mm, "mid": v(926.1, 9.9) * mm, "end": v(926.1, 7.07) * mm});
            skArc(sketch, "E92.38.0.14", {"start": v(921.9, 7.07) * mm, "mid": v(921.9, 9.9) * mm, "end": v(919.07, 9.9) * mm});
            skArc(sketch, "E92.38.0.15", {"start": v(926.1, -7.07) * mm, "mid": v(926.1, -9.9) * mm, "end": v(928.93, -9.9) * mm});
            skArc(sketch, "E92.38.0.16", {"start": v(926.59, 6.59) * mm, "mid": v(929.41, 6.59) * mm, "end": v(929.41, 9.41) * mm});
            skLineSegment(sketch, "E92.38.0.17", {"start": v(920, -16) * mm, "end": v(928, -16) * mm, "construction": true});
            skLineSegment(sketch, "E92.38.0.18", {"start": v(912, 0) * mm, "end": v(936, 0) * mm, "construction": true});
            skArc(sketch, "E92.38.0.19", {"start": v(929.41, -9.41) * mm, "mid": v(929.41, -6.59) * mm, "end": v(926.59, -6.59) * mm});
            skCircle(sketch, "E92.38.0.20", {"center": v(920, -16) * mm, "radius": 2 * mm});
            skCircle(sketch, "E92.38.0.21", {"center": v(924, 0) * mm, "radius": 2 * mm});
            skPoint(sketch, "E92.38.0.22", {"position": v(920, -8) * mm});
            skLineSegment(sketch, "E92.38.0.23", {"start": v(936, 0) * mm, "end": v(912, 0) * mm, "construction": true});
            skLineSegment(sketch, "E92.38.0.24", {"start": v(926.59, 6.59) * mm, "end": v(929.41, 9.41) * mm, "construction": true});
            skLineSegment(sketch, "E92.38.0.25", {"start": v(926.1, -7.07) * mm, "end": v(928.93, -9.9) * mm, "construction": true});
            skLineSegment(sketch, "E92.38.0.26", {"start": v(918.59, 9.41) * mm, "end": v(921.41, 6.59) * mm, "construction": true});
            skLineSegment(sketch, "E92.38.0.27", {"start": v(919.07, 9.9) * mm, "end": v(921.9, 7.07) * mm, "construction": true});
            skLineSegment(sketch, "E92.38.0.28", {"start": v(928.93, 9.9) * mm, "end": v(926.1, 7.07) * mm, "construction": true});
            skLineSegment(sketch, "E92.38.0.29", {"start": v(926.59, -6.59) * mm, "end": v(929.41, -9.41) * mm, "construction": true});
            skLineSegment(sketch, "E92.38.0.30", {"start": v(919.07, -9.9) * mm, "end": v(921.9, -7.07) * mm, "construction": true});
            skLineSegment(sketch, "E92.38.0.31", {"start": v(921.41, -6.59) * mm, "end": v(918.59, -9.41) * mm, "construction": true});
            skLineSegment(sketch, "E92.38.0.32", {"start": v(926.1, -7.07) * mm, "end": v(926.59, -6.59) * mm});
            skLineSegment(sketch, "E92.38.0.33", {"start": v(918.59, 9.41) * mm, "end": v(919.07, 9.9) * mm});
            skLineSegment(sketch, "E92.38.0.34", {"start": v(918.59, -9.41) * mm, "end": v(919.07, -9.9) * mm});
            skLineSegment(sketch, "E92.38.0.35", {"start": v(928.93, -9.9) * mm, "end": v(929.41, -9.41) * mm});
            skLineSegment(sketch, "E92.38.0.36", {"start": v(921.41, 6.59) * mm, "end": v(921.9, 7.07) * mm});
            skLineSegment(sketch, "E92.38.0.37", {"start": v(928.93, 9.9) * mm, "end": v(929.41, 9.41) * mm});
            skLineSegment(sketch, "E92.38.0.38", {"start": v(926.1, 7.07) * mm, "end": v(926.59, 6.59) * mm});
            skLineSegment(sketch, "E92.38.0.39", {"start": v(921.41, -6.59) * mm, "end": v(921.9, -7.07) * mm});
            skArc(sketch, "E92.39.0.0", {"start": v(942.59, 9.41) * mm, "mid": v(942.59, 6.59) * mm, "end": v(945.41, 6.59) * mm});
            skArc(sketch, "E92.39.0.1", {"start": v(945.41, -6.59) * mm, "mid": v(942.59, -6.59) * mm, "end": v(942.59, -9.41) * mm});
            skLineSegment(sketch, "E92.39.0.2", {"start": v(936, 24) * mm, "end": v(960, 24) * mm, "construction": true});
            skLineSegment(sketch, "E92.39.0.3", {"start": v(944, 16) * mm, "end": v(952, 16) * mm, "construction": true});
            skArc(sketch, "E92.39.0.4", {"start": v(943.07, -9.9) * mm, "mid": v(945.9, -9.9) * mm, "end": v(945.9, -7.07) * mm});
            skLineSegment(sketch, "E92.39.0.5", {"start": v(960, 0) * mm, "end": v(936, -24) * mm, "construction": true});
            skCircle(sketch, "E92.39.0.6", {"center": v(952, -16) * mm, "radius": 2 * mm});
            skLineSegment(sketch, "E92.39.0.7", {"start": v(960, -24) * mm, "end": v(936, -24) * mm, "construction": true});
            skCircle(sketch, "E92.39.0.8", {"center": v(944, 16) * mm, "radius": 2 * mm});
            skCircle(sketch, "E92.39.0.9", {"center": v(952, 16) * mm, "radius": 2 * mm});
            skLineSegment(sketch, "E92.39.0.10", {"start": v(960, -24) * mm, "end": v(936, 0) * mm, "construction": true});
            skLineSegment(sketch, "E92.39.0.11", {"start": v(936, 24) * mm, "end": v(960, 0) * mm, "construction": true});
            skLineSegment(sketch, "E92.39.0.12", {"start": v(960, 24) * mm, "end": v(936, 0) * mm, "construction": true});
            skArc(sketch, "E92.39.0.13", {"start": v(952.93, 9.9) * mm, "mid": v(950.1, 9.9) * mm, "end": v(950.1, 7.07) * mm});
            skArc(sketch, "E92.39.0.14", {"start": v(945.9, 7.07) * mm, "mid": v(945.9, 9.9) * mm, "end": v(943.07, 9.9) * mm});
            skArc(sketch, "E92.39.0.15", {"start": v(950.1, -7.07) * mm, "mid": v(950.1, -9.9) * mm, "end": v(952.93, -9.9) * mm});
            skArc(sketch, "E92.39.0.16", {"start": v(950.59, 6.59) * mm, "mid": v(953.41, 6.59) * mm, "end": v(953.41, 9.41) * mm});
            skLineSegment(sketch, "E92.39.0.17", {"start": v(944, -16) * mm, "end": v(952, -16) * mm, "construction": true});
            skLineSegment(sketch, "E92.39.0.18", {"start": v(936, 0) * mm, "end": v(960, 0) * mm, "construction": true});
            skArc(sketch, "E92.39.0.19", {"start": v(953.41, -9.41) * mm, "mid": v(953.41, -6.59) * mm, "end": v(950.59, -6.59) * mm});
            skCircle(sketch, "E92.39.0.20", {"center": v(944, -16) * mm, "radius": 2 * mm});
            skCircle(sketch, "E92.39.0.21", {"center": v(948, 0) * mm, "radius": 2 * mm});
            skPoint(sketch, "E92.39.0.22", {"position": v(944, -8) * mm});
            skLineSegment(sketch, "E92.39.0.23", {"start": v(960, 0) * mm, "end": v(936, 0) * mm, "construction": true});
            skLineSegment(sketch, "E92.39.0.24", {"start": v(950.59, 6.59) * mm, "end": v(953.41, 9.41) * mm, "construction": true});
            skLineSegment(sketch, "E92.39.0.25", {"start": v(950.1, -7.07) * mm, "end": v(952.93, -9.9) * mm, "construction": true});
            skLineSegment(sketch, "E92.39.0.26", {"start": v(942.59, 9.41) * mm, "end": v(945.41, 6.59) * mm, "construction": true});
            skLineSegment(sketch, "E92.39.0.27", {"start": v(943.07, 9.9) * mm, "end": v(945.9, 7.07) * mm, "construction": true});
            skLineSegment(sketch, "E92.39.0.28", {"start": v(952.93, 9.9) * mm, "end": v(950.1, 7.07) * mm, "construction": true});
            skLineSegment(sketch, "E92.39.0.29", {"start": v(950.59, -6.59) * mm, "end": v(953.41, -9.41) * mm, "construction": true});
            skLineSegment(sketch, "E92.39.0.30", {"start": v(943.07, -9.9) * mm, "end": v(945.9, -7.07) * mm, "construction": true});
            skLineSegment(sketch, "E92.39.0.31", {"start": v(945.41, -6.59) * mm, "end": v(942.59, -9.41) * mm, "construction": true});
            skLineSegment(sketch, "E92.39.0.32", {"start": v(950.1, -7.07) * mm, "end": v(950.59, -6.59) * mm});
            skLineSegment(sketch, "E92.39.0.33", {"start": v(942.59, 9.41) * mm, "end": v(943.07, 9.9) * mm});
            skLineSegment(sketch, "E92.39.0.34", {"start": v(942.59, -9.41) * mm, "end": v(943.07, -9.9) * mm});
            skLineSegment(sketch, "E92.39.0.35", {"start": v(952.93, -9.9) * mm, "end": v(953.41, -9.41) * mm});
            skLineSegment(sketch, "E92.39.0.36", {"start": v(945.41, 6.59) * mm, "end": v(945.9, 7.07) * mm});
            skLineSegment(sketch, "E92.39.0.37", {"start": v(952.93, 9.9) * mm, "end": v(953.41, 9.41) * mm});
            skLineSegment(sketch, "E92.39.0.38", {"start": v(950.1, 7.07) * mm, "end": v(950.59, 6.59) * mm});
            skLineSegment(sketch, "E92.39.0.39", {"start": v(945.41, -6.59) * mm, "end": v(945.9, -7.07) * mm});
            skArc(sketch, "E92.40.0.0", {"start": v(966.59, 9.41) * mm, "mid": v(966.59, 6.59) * mm, "end": v(969.41, 6.59) * mm});
            skArc(sketch, "E92.40.0.1", {"start": v(969.41, -6.59) * mm, "mid": v(966.59, -6.59) * mm, "end": v(966.59, -9.41) * mm});
            skLineSegment(sketch, "E92.40.0.2", {"start": v(960, 24) * mm, "end": v(984, 24) * mm, "construction": true});
            skLineSegment(sketch, "E92.40.0.3", {"start": v(968, 16) * mm, "end": v(976, 16) * mm, "construction": true});
            skArc(sketch, "E92.40.0.4", {"start": v(967.07, -9.9) * mm, "mid": v(969.9, -9.9) * mm, "end": v(969.9, -7.07) * mm});
            skLineSegment(sketch, "E92.40.0.5", {"start": v(984, 0) * mm, "end": v(960, -24) * mm, "construction": true});
            skCircle(sketch, "E92.40.0.6", {"center": v(976, -16) * mm, "radius": 2 * mm});
            skLineSegment(sketch, "E92.40.0.7", {"start": v(984, -24) * mm, "end": v(960, -24) * mm, "construction": true});
            skCircle(sketch, "E92.40.0.8", {"center": v(968, 16) * mm, "radius": 2 * mm});
            skCircle(sketch, "E92.40.0.9", {"center": v(976, 16) * mm, "radius": 2 * mm});
            skLineSegment(sketch, "E92.40.0.10", {"start": v(984, -24) * mm, "end": v(960, 0) * mm, "construction": true});
            skLineSegment(sketch, "E92.40.0.11", {"start": v(960, 24) * mm, "end": v(984, 0) * mm, "construction": true});
            skLineSegment(sketch, "E92.40.0.12", {"start": v(984, 24) * mm, "end": v(960, 0) * mm, "construction": true});
            skArc(sketch, "E92.40.0.13", {"start": v(976.93, 9.9) * mm, "mid": v(974.1, 9.9) * mm, "end": v(974.1, 7.07) * mm});
            skArc(sketch, "E92.40.0.14", {"start": v(969.9, 7.07) * mm, "mid": v(969.9, 9.9) * mm, "end": v(967.07, 9.9) * mm});
            skArc(sketch, "E92.40.0.15", {"start": v(974.1, -7.07) * mm, "mid": v(974.1, -9.9) * mm, "end": v(976.93, -9.9) * mm});
            skArc(sketch, "E92.40.0.16", {"start": v(974.59, 6.59) * mm, "mid": v(977.41, 6.59) * mm, "end": v(977.41, 9.41) * mm});
            skLineSegment(sketch, "E92.40.0.17", {"start": v(968, -16) * mm, "end": v(976, -16) * mm, "construction": true});
            skLineSegment(sketch, "E92.40.0.18", {"start": v(960, 0) * mm, "end": v(984, 0) * mm, "construction": true});
            skArc(sketch, "E92.40.0.19", {"start": v(977.41, -9.41) * mm, "mid": v(977.41, -6.59) * mm, "end": v(974.59, -6.59) * mm});
            skCircle(sketch, "E92.40.0.20", {"center": v(968, -16) * mm, "radius": 2 * mm});
            skCircle(sketch, "E92.40.0.21", {"center": v(972, 0) * mm, "radius": 2 * mm});
            skPoint(sketch, "E92.40.0.22", {"position": v(968, -8) * mm});
            skLineSegment(sketch, "E92.40.0.23", {"start": v(984, 0) * mm, "end": v(960, 0) * mm, "construction": true});
            skLineSegment(sketch, "E92.40.0.24", {"start": v(974.59, 6.59) * mm, "end": v(977.41, 9.41) * mm, "construction": true});
            skLineSegment(sketch, "E92.40.0.25", {"start": v(974.1, -7.07) * mm, "end": v(976.93, -9.9) * mm, "construction": true});
            skLineSegment(sketch, "E92.40.0.26", {"start": v(966.59, 9.41) * mm, "end": v(969.41, 6.59) * mm, "construction": true});
            skLineSegment(sketch, "E92.40.0.27", {"start": v(967.07, 9.9) * mm, "end": v(969.9, 7.07) * mm, "construction": true});
            skLineSegment(sketch, "E92.40.0.28", {"start": v(976.93, 9.9) * mm, "end": v(974.1, 7.07) * mm, "construction": true});
            skLineSegment(sketch, "E92.40.0.29", {"start": v(974.59, -6.59) * mm, "end": v(977.41, -9.41) * mm, "construction": true});
            skLineSegment(sketch, "E92.40.0.30", {"start": v(967.07, -9.9) * mm, "end": v(969.9, -7.07) * mm, "construction": true});
            skLineSegment(sketch, "E92.40.0.31", {"start": v(969.41, -6.59) * mm, "end": v(966.59, -9.41) * mm, "construction": true});
            skLineSegment(sketch, "E92.40.0.32", {"start": v(974.1, -7.07) * mm, "end": v(974.59, -6.59) * mm});
            skLineSegment(sketch, "E92.40.0.33", {"start": v(966.59, 9.41) * mm, "end": v(967.07, 9.9) * mm});
            skLineSegment(sketch, "E92.40.0.34", {"start": v(966.59, -9.41) * mm, "end": v(967.07, -9.9) * mm});
            skLineSegment(sketch, "E92.40.0.35", {"start": v(976.93, -9.9) * mm, "end": v(977.41, -9.41) * mm});
            skLineSegment(sketch, "E92.40.0.36", {"start": v(969.41, 6.59) * mm, "end": v(969.9, 7.07) * mm});
            skLineSegment(sketch, "E92.40.0.37", {"start": v(976.93, 9.9) * mm, "end": v(977.41, 9.41) * mm});
            skLineSegment(sketch, "E92.40.0.38", {"start": v(974.1, 7.07) * mm, "end": v(974.59, 6.59) * mm});
            skLineSegment(sketch, "E92.40.0.39", {"start": v(969.41, -6.59) * mm, "end": v(969.9, -7.07) * mm});
            skArc(sketch, "E92.41.0.0", {"start": v(990.59, 9.41) * mm, "mid": v(990.59, 6.59) * mm, "end": v(993.41, 6.59) * mm});
            skArc(sketch, "E92.41.0.1", {"start": v(993.41, -6.59) * mm, "mid": v(990.59, -6.59) * mm, "end": v(990.59, -9.41) * mm});
            skLineSegment(sketch, "E92.41.0.2", {"start": v(984, 24) * mm, "end": v(1008, 24) * mm, "construction": true});
            skLineSegment(sketch, "E92.41.0.3", {"start": v(992, 16) * mm, "end": v(1000, 16) * mm, "construction": true});
            skArc(sketch, "E92.41.0.4", {"start": v(991.07, -9.9) * mm, "mid": v(993.9, -9.9) * mm, "end": v(993.9, -7.07) * mm});
            skLineSegment(sketch, "E92.41.0.5", {"start": v(1008, 0) * mm, "end": v(984, -24) * mm, "construction": true});
            skCircle(sketch, "E92.41.0.6", {"center": v(1000, -16) * mm, "radius": 2 * mm});
            skLineSegment(sketch, "E92.41.0.7", {"start": v(1008, -24) * mm, "end": v(984, -24) * mm, "construction": true});
            skCircle(sketch, "E92.41.0.8", {"center": v(992, 16) * mm, "radius": 2 * mm});
            skCircle(sketch, "E92.41.0.9", {"center": v(1000, 16) * mm, "radius": 2 * mm});
            skLineSegment(sketch, "E92.41.0.10", {"start": v(1008, -24) * mm, "end": v(984, 0) * mm, "construction": true});
            skLineSegment(sketch, "E92.41.0.11", {"start": v(984, 24) * mm, "end": v(1008, 0) * mm, "construction": true});
            skLineSegment(sketch, "E92.41.0.12", {"start": v(1008, 24) * mm, "end": v(984, 0) * mm, "construction": true});
            skArc(sketch, "E92.41.0.13", {"start": v(1000.93, 9.9) * mm, "mid": v(998.1, 9.9) * mm, "end": v(998.1, 7.07) * mm});
            skArc(sketch, "E92.41.0.14", {"start": v(993.9, 7.07) * mm, "mid": v(993.9, 9.9) * mm, "end": v(991.07, 9.9) * mm});
            skArc(sketch, "E92.41.0.15", {"start": v(998.1, -7.07) * mm, "mid": v(998.1, -9.9) * mm, "end": v(1000.93, -9.9) * mm});
            skArc(sketch, "E92.41.0.16", {"start": v(998.59, 6.59) * mm, "mid": v(1001.41, 6.59) * mm, "end": v(1001.41, 9.41) * mm});
            skLineSegment(sketch, "E92.41.0.17", {"start": v(992, -16) * mm, "end": v(1000, -16) * mm, "construction": true});
            skLineSegment(sketch, "E92.41.0.18", {"start": v(984, 0) * mm, "end": v(1008, 0) * mm, "construction": true});
            skArc(sketch, "E92.41.0.19", {"start": v(1001.41, -9.41) * mm, "mid": v(1001.41, -6.59) * mm, "end": v(998.59, -6.59) * mm});
            skCircle(sketch, "E92.41.0.20", {"center": v(992, -16) * mm, "radius": 2 * mm});
            skCircle(sketch, "E92.41.0.21", {"center": v(996, 0) * mm, "radius": 2 * mm});
            skPoint(sketch, "E92.41.0.22", {"position": v(992, -8) * mm});
            skLineSegment(sketch, "E92.41.0.23", {"start": v(1008, 0) * mm, "end": v(984, 0) * mm, "construction": true});
            skLineSegment(sketch, "E92.41.0.24", {"start": v(998.59, 6.59) * mm, "end": v(1001.41, 9.41) * mm, "construction": true});
            skLineSegment(sketch, "E92.41.0.25", {"start": v(998.1, -7.07) * mm, "end": v(1000.93, -9.9) * mm, "construction": true});
            skLineSegment(sketch, "E92.41.0.26", {"start": v(990.59, 9.41) * mm, "end": v(993.41, 6.59) * mm, "construction": true});
            skLineSegment(sketch, "E92.41.0.27", {"start": v(991.07, 9.9) * mm, "end": v(993.9, 7.07) * mm, "construction": true});
            skLineSegment(sketch, "E92.41.0.28", {"start": v(1000.93, 9.9) * mm, "end": v(998.1, 7.07) * mm, "construction": true});
            skLineSegment(sketch, "E92.41.0.29", {"start": v(998.59, -6.59) * mm, "end": v(1001.41, -9.41) * mm, "construction": true});
            skLineSegment(sketch, "E92.41.0.30", {"start": v(991.07, -9.9) * mm, "end": v(993.9, -7.07) * mm, "construction": true});
            skLineSegment(sketch, "E92.41.0.31", {"start": v(993.41, -6.59) * mm, "end": v(990.59, -9.41) * mm, "construction": true});
            skLineSegment(sketch, "E92.41.0.32", {"start": v(998.1, -7.07) * mm, "end": v(998.59, -6.59) * mm});
            skLineSegment(sketch, "E92.41.0.33", {"start": v(990.59, 9.41) * mm, "end": v(991.07, 9.9) * mm});
            skLineSegment(sketch, "E92.41.0.34", {"start": v(990.59, -9.41) * mm, "end": v(991.07, -9.9) * mm});
            skLineSegment(sketch, "E92.41.0.35", {"start": v(1000.93, -9.9) * mm, "end": v(1001.41, -9.41) * mm});
            skLineSegment(sketch, "E92.41.0.36", {"start": v(993.41, 6.59) * mm, "end": v(993.9, 7.07) * mm});
            skLineSegment(sketch, "E92.41.0.37", {"start": v(1000.93, 9.9) * mm, "end": v(1001.41, 9.41) * mm});
            skLineSegment(sketch, "E92.41.0.38", {"start": v(998.1, 7.07) * mm, "end": v(998.59, 6.59) * mm});
            skLineSegment(sketch, "E92.41.0.39", {"start": v(993.41, -6.59) * mm, "end": v(993.9, -7.07) * mm});
            skArc(sketch, "E92.42.0.0", {"start": v(1014.59, 9.41) * mm, "mid": v(1014.59, 6.59) * mm, "end": v(1017.41, 6.59) * mm});
            skArc(sketch, "E92.42.0.1", {"start": v(1017.41, -6.59) * mm, "mid": v(1014.59, -6.59) * mm, "end": v(1014.59, -9.41) * mm});
            skLineSegment(sketch, "E92.42.0.2", {"start": v(1008, 24) * mm, "end": v(1032, 24) * mm, "construction": true});
            skLineSegment(sketch, "E92.42.0.3", {"start": v(1016, 16) * mm, "end": v(1024, 16) * mm, "construction": true});
            skArc(sketch, "E92.42.0.4", {"start": v(1015.07, -9.9) * mm, "mid": v(1017.9, -9.9) * mm, "end": v(1017.9, -7.07) * mm});
            skLineSegment(sketch, "E92.42.0.5", {"start": v(1032, 0) * mm, "end": v(1008, -24) * mm, "construction": true});
            skCircle(sketch, "E92.42.0.6", {"center": v(1024, -16) * mm, "radius": 2 * mm});
            skLineSegment(sketch, "E92.42.0.7", {"start": v(1032, -24) * mm, "end": v(1008, -24) * mm, "construction": true});
            skCircle(sketch, "E92.42.0.8", {"center": v(1016, 16) * mm, "radius": 2 * mm});
            skCircle(sketch, "E92.42.0.9", {"center": v(1024, 16) * mm, "radius": 2 * mm});
            skLineSegment(sketch, "E92.42.0.10", {"start": v(1032, -24) * mm, "end": v(1008, 0) * mm, "construction": true});
            skLineSegment(sketch, "E92.42.0.11", {"start": v(1008, 24) * mm, "end": v(1032, 0) * mm, "construction": true});
            skLineSegment(sketch, "E92.42.0.12", {"start": v(1032, 24) * mm, "end": v(1008, 0) * mm, "construction": true});
            skArc(sketch, "E92.42.0.13", {"start": v(1024.93, 9.9) * mm, "mid": v(1022.1, 9.9) * mm, "end": v(1022.1, 7.07) * mm});
            skArc(sketch, "E92.42.0.14", {"start": v(1017.9, 7.07) * mm, "mid": v(1017.9, 9.9) * mm, "end": v(1015.07, 9.9) * mm});
            skArc(sketch, "E92.42.0.15", {"start": v(1022.1, -7.07) * mm, "mid": v(1022.1, -9.9) * mm, "end": v(1024.93, -9.9) * mm});
            skArc(sketch, "E92.42.0.16", {"start": v(1022.59, 6.59) * mm, "mid": v(1025.41, 6.59) * mm, "end": v(1025.41, 9.41) * mm});
            skLineSegment(sketch, "E92.42.0.17", {"start": v(1016, -16) * mm, "end": v(1024, -16) * mm, "construction": true});
            skLineSegment(sketch, "E92.42.0.18", {"start": v(1008, 0) * mm, "end": v(1032, 0) * mm, "construction": true});
            skArc(sketch, "E92.42.0.19", {"start": v(1025.41, -9.41) * mm, "mid": v(1025.41, -6.59) * mm, "end": v(1022.59, -6.59) * mm});
            skCircle(sketch, "E92.42.0.20", {"center": v(1016, -16) * mm, "radius": 2 * mm});
            skCircle(sketch, "E92.42.0.21", {"center": v(1020, 0) * mm, "radius": 2 * mm});
            skPoint(sketch, "E92.42.0.22", {"position": v(1016, -8) * mm});
            skLineSegment(sketch, "E92.42.0.23", {"start": v(1032, 0) * mm, "end": v(1008, 0) * mm, "construction": true});
            skLineSegment(sketch, "E92.42.0.24", {"start": v(1022.59, 6.59) * mm, "end": v(1025.41, 9.41) * mm, "construction": true});
            skLineSegment(sketch, "E92.42.0.25", {"start": v(1022.1, -7.07) * mm, "end": v(1024.93, -9.9) * mm, "construction": true});
            skLineSegment(sketch, "E92.42.0.26", {"start": v(1014.59, 9.41) * mm, "end": v(1017.41, 6.59) * mm, "construction": true});
            skLineSegment(sketch, "E92.42.0.27", {"start": v(1015.07, 9.9) * mm, "end": v(1017.9, 7.07) * mm, "construction": true});
            skLineSegment(sketch, "E92.42.0.28", {"start": v(1024.93, 9.9) * mm, "end": v(1022.1, 7.07) * mm, "construction": true});
            skLineSegment(sketch, "E92.42.0.29", {"start": v(1022.59, -6.59) * mm, "end": v(1025.41, -9.41) * mm, "construction": true});
            skLineSegment(sketch, "E92.42.0.30", {"start": v(1015.07, -9.9) * mm, "end": v(1017.9, -7.07) * mm, "construction": true});
            skLineSegment(sketch, "E92.42.0.31", {"start": v(1017.41, -6.59) * mm, "end": v(1014.59, -9.41) * mm, "construction": true});
            skLineSegment(sketch, "E92.42.0.32", {"start": v(1022.1, -7.07) * mm, "end": v(1022.59, -6.59) * mm});
            skLineSegment(sketch, "E92.42.0.33", {"start": v(1014.59, 9.41) * mm, "end": v(1015.07, 9.9) * mm});
            skLineSegment(sketch, "E92.42.0.34", {"start": v(1014.59, -9.41) * mm, "end": v(1015.07, -9.9) * mm});
            skLineSegment(sketch, "E92.42.0.35", {"start": v(1024.93, -9.9) * mm, "end": v(1025.41, -9.41) * mm});
            skLineSegment(sketch, "E92.42.0.36", {"start": v(1017.41, 6.59) * mm, "end": v(1017.9, 7.07) * mm});
            skLineSegment(sketch, "E92.42.0.37", {"start": v(1024.93, 9.9) * mm, "end": v(1025.41, 9.41) * mm});
            skLineSegment(sketch, "E92.42.0.38", {"start": v(1022.1, 7.07) * mm, "end": v(1022.59, 6.59) * mm});
            skLineSegment(sketch, "E92.42.0.39", {"start": v(1017.41, -6.59) * mm, "end": v(1017.9, -7.07) * mm});
            skArc(sketch, "E92.43.0.0", {"start": v(1038.59, 9.41) * mm, "mid": v(1038.59, 6.59) * mm, "end": v(1041.41, 6.59) * mm});
            skArc(sketch, "E92.43.0.1", {"start": v(1041.41, -6.59) * mm, "mid": v(1038.59, -6.59) * mm, "end": v(1038.59, -9.41) * mm});
            skLineSegment(sketch, "E92.43.0.2", {"start": v(1032, 24) * mm, "end": v(1056, 24) * mm, "construction": true});
            skLineSegment(sketch, "E92.43.0.3", {"start": v(1040, 16) * mm, "end": v(1048, 16) * mm, "construction": true});
            skArc(sketch, "E92.43.0.4", {"start": v(1039.07, -9.9) * mm, "mid": v(1041.9, -9.9) * mm, "end": v(1041.9, -7.07) * mm});
            skLineSegment(sketch, "E92.43.0.5", {"start": v(1056, 0) * mm, "end": v(1032, -24) * mm, "construction": true});
            skCircle(sketch, "E92.43.0.6", {"center": v(1048, -16) * mm, "radius": 2 * mm});
            skLineSegment(sketch, "E92.43.0.7", {"start": v(1056, -24) * mm, "end": v(1032, -24) * mm, "construction": true});
            skCircle(sketch, "E92.43.0.8", {"center": v(1040, 16) * mm, "radius": 2 * mm});
            skCircle(sketch, "E92.43.0.9", {"center": v(1048, 16) * mm, "radius": 2 * mm});
            skLineSegment(sketch, "E92.43.0.10", {"start": v(1056, -24) * mm, "end": v(1032, 0) * mm, "construction": true});
            skLineSegment(sketch, "E92.43.0.11", {"start": v(1032, 24) * mm, "end": v(1056, 0) * mm, "construction": true});
            skLineSegment(sketch, "E92.43.0.12", {"start": v(1056, 24) * mm, "end": v(1032, 0) * mm, "construction": true});
            skArc(sketch, "E92.43.0.13", {"start": v(1048.93, 9.9) * mm, "mid": v(1046.1, 9.9) * mm, "end": v(1046.1, 7.07) * mm});
            skArc(sketch, "E92.43.0.14", {"start": v(1041.9, 7.07) * mm, "mid": v(1041.9, 9.9) * mm, "end": v(1039.07, 9.9) * mm});
            skArc(sketch, "E92.43.0.15", {"start": v(1046.1, -7.07) * mm, "mid": v(1046.1, -9.9) * mm, "end": v(1048.93, -9.9) * mm});
            skArc(sketch, "E92.43.0.16", {"start": v(1046.59, 6.59) * mm, "mid": v(1049.41, 6.59) * mm, "end": v(1049.41, 9.41) * mm});
            skLineSegment(sketch, "E92.43.0.17", {"start": v(1040, -16) * mm, "end": v(1048, -16) * mm, "construction": true});
            skLineSegment(sketch, "E92.43.0.18", {"start": v(1032, 0) * mm, "end": v(1056, 0) * mm, "construction": true});
            skArc(sketch, "E92.43.0.19", {"start": v(1049.41, -9.41) * mm, "mid": v(1049.41, -6.59) * mm, "end": v(1046.59, -6.59) * mm});
            skCircle(sketch, "E92.43.0.20", {"center": v(1040, -16) * mm, "radius": 2 * mm});
            skCircle(sketch, "E92.43.0.21", {"center": v(1044, 0) * mm, "radius": 2 * mm});
            skPoint(sketch, "E92.43.0.22", {"position": v(1040, -8) * mm});
            skLineSegment(sketch, "E92.43.0.23", {"start": v(1056, 0) * mm, "end": v(1032, 0) * mm, "construction": true});
            skLineSegment(sketch, "E92.43.0.24", {"start": v(1046.59, 6.59) * mm, "end": v(1049.41, 9.41) * mm, "construction": true});
            skLineSegment(sketch, "E92.43.0.25", {"start": v(1046.1, -7.07) * mm, "end": v(1048.93, -9.9) * mm, "construction": true});
            skLineSegment(sketch, "E92.43.0.26", {"start": v(1038.59, 9.41) * mm, "end": v(1041.41, 6.59) * mm, "construction": true});
            skLineSegment(sketch, "E92.43.0.27", {"start": v(1039.07, 9.9) * mm, "end": v(1041.9, 7.07) * mm, "construction": true});
            skLineSegment(sketch, "E92.43.0.28", {"start": v(1048.93, 9.9) * mm, "end": v(1046.1, 7.07) * mm, "construction": true});
            skLineSegment(sketch, "E92.43.0.29", {"start": v(1046.59, -6.59) * mm, "end": v(1049.41, -9.41) * mm, "construction": true});
            skLineSegment(sketch, "E92.43.0.30", {"start": v(1039.07, -9.9) * mm, "end": v(1041.9, -7.07) * mm, "construction": true});
            skLineSegment(sketch, "E92.43.0.31", {"start": v(1041.41, -6.59) * mm, "end": v(1038.59, -9.41) * mm, "construction": true});
            skLineSegment(sketch, "E92.43.0.32", {"start": v(1046.1, -7.07) * mm, "end": v(1046.59, -6.59) * mm});
            skLineSegment(sketch, "E92.43.0.33", {"start": v(1038.59, 9.41) * mm, "end": v(1039.07, 9.9) * mm});
            skLineSegment(sketch, "E92.43.0.34", {"start": v(1038.59, -9.41) * mm, "end": v(1039.07, -9.9) * mm});
            skLineSegment(sketch, "E92.43.0.35", {"start": v(1048.93, -9.9) * mm, "end": v(1049.41, -9.41) * mm});
            skLineSegment(sketch, "E92.43.0.36", {"start": v(1041.41, 6.59) * mm, "end": v(1041.9, 7.07) * mm});
            skLineSegment(sketch, "E92.43.0.37", {"start": v(1048.93, 9.9) * mm, "end": v(1049.41, 9.41) * mm});
            skLineSegment(sketch, "E92.43.0.38", {"start": v(1046.1, 7.07) * mm, "end": v(1046.59, 6.59) * mm});
            skLineSegment(sketch, "E92.43.0.39", {"start": v(1041.41, -6.59) * mm, "end": v(1041.9, -7.07) * mm});
            skArc(sketch, "E92.44.0.0", {"start": v(1062.59, 9.41) * mm, "mid": v(1062.59, 6.59) * mm, "end": v(1065.41, 6.59) * mm});
            skArc(sketch, "E92.44.0.1", {"start": v(1065.41, -6.59) * mm, "mid": v(1062.59, -6.59) * mm, "end": v(1062.59, -9.41) * mm});
            skLineSegment(sketch, "E92.44.0.2", {"start": v(1056, 24) * mm, "end": v(1080, 24) * mm, "construction": true});
            skLineSegment(sketch, "E92.44.0.3", {"start": v(1064, 16) * mm, "end": v(1072, 16) * mm, "construction": true});
            skArc(sketch, "E92.44.0.4", {"start": v(1063.07, -9.9) * mm, "mid": v(1065.9, -9.9) * mm, "end": v(1065.9, -7.07) * mm});
            skLineSegment(sketch, "E92.44.0.5", {"start": v(1080, 0) * mm, "end": v(1056, -24) * mm, "construction": true});
            skCircle(sketch, "E92.44.0.6", {"center": v(1072, -16) * mm, "radius": 2 * mm});
            skLineSegment(sketch, "E92.44.0.7", {"start": v(1080, -24) * mm, "end": v(1056, -24) * mm, "construction": true});
            skCircle(sketch, "E92.44.0.8", {"center": v(1064, 16) * mm, "radius": 2 * mm});
            skCircle(sketch, "E92.44.0.9", {"center": v(1072, 16) * mm, "radius": 2 * mm});
            skLineSegment(sketch, "E92.44.0.10", {"start": v(1080, -24) * mm, "end": v(1056, 0) * mm, "construction": true});
            skLineSegment(sketch, "E92.44.0.11", {"start": v(1056, 24) * mm, "end": v(1080, 0) * mm, "construction": true});
            skLineSegment(sketch, "E92.44.0.12", {"start": v(1080, 24) * mm, "end": v(1056, 0) * mm, "construction": true});
            skArc(sketch, "E92.44.0.13", {"start": v(1072.93, 9.9) * mm, "mid": v(1070.1, 9.9) * mm, "end": v(1070.1, 7.07) * mm});
            skArc(sketch, "E92.44.0.14", {"start": v(1065.9, 7.07) * mm, "mid": v(1065.9, 9.9) * mm, "end": v(1063.07, 9.9) * mm});
            skArc(sketch, "E92.44.0.15", {"start": v(1070.1, -7.07) * mm, "mid": v(1070.1, -9.9) * mm, "end": v(1072.93, -9.9) * mm});
            skArc(sketch, "E92.44.0.16", {"start": v(1070.59, 6.59) * mm, "mid": v(1073.41, 6.59) * mm, "end": v(1073.41, 9.41) * mm});
            skLineSegment(sketch, "E92.44.0.17", {"start": v(1064, -16) * mm, "end": v(1072, -16) * mm, "construction": true});
            skLineSegment(sketch, "E92.44.0.18", {"start": v(1056, 0) * mm, "end": v(1080, 0) * mm, "construction": true});
            skArc(sketch, "E92.44.0.19", {"start": v(1073.41, -9.41) * mm, "mid": v(1073.41, -6.59) * mm, "end": v(1070.59, -6.59) * mm});
            skCircle(sketch, "E92.44.0.20", {"center": v(1064, -16) * mm, "radius": 2 * mm});
            skCircle(sketch, "E92.44.0.21", {"center": v(1068, 0) * mm, "radius": 2 * mm});
            skPoint(sketch, "E92.44.0.22", {"position": v(1064, -8) * mm});
            skLineSegment(sketch, "E92.44.0.23", {"start": v(1080, 0) * mm, "end": v(1056, 0) * mm, "construction": true});
            skLineSegment(sketch, "E92.44.0.24", {"start": v(1070.59, 6.59) * mm, "end": v(1073.41, 9.41) * mm, "construction": true});
            skLineSegment(sketch, "E92.44.0.25", {"start": v(1070.1, -7.07) * mm, "end": v(1072.93, -9.9) * mm, "construction": true});
            skLineSegment(sketch, "E92.44.0.26", {"start": v(1062.59, 9.41) * mm, "end": v(1065.41, 6.59) * mm, "construction": true});
            skLineSegment(sketch, "E92.44.0.27", {"start": v(1063.07, 9.9) * mm, "end": v(1065.9, 7.07) * mm, "construction": true});
            skLineSegment(sketch, "E92.44.0.28", {"start": v(1072.93, 9.9) * mm, "end": v(1070.1, 7.07) * mm, "construction": true});
            skLineSegment(sketch, "E92.44.0.29", {"start": v(1070.59, -6.59) * mm, "end": v(1073.41, -9.41) * mm, "construction": true});
            skLineSegment(sketch, "E92.44.0.30", {"start": v(1063.07, -9.9) * mm, "end": v(1065.9, -7.07) * mm, "construction": true});
            skLineSegment(sketch, "E92.44.0.31", {"start": v(1065.41, -6.59) * mm, "end": v(1062.59, -9.41) * mm, "construction": true});
            skLineSegment(sketch, "E92.44.0.32", {"start": v(1070.1, -7.07) * mm, "end": v(1070.59, -6.59) * mm});
            skLineSegment(sketch, "E92.44.0.33", {"start": v(1062.59, 9.41) * mm, "end": v(1063.07, 9.9) * mm});
            skLineSegment(sketch, "E92.44.0.34", {"start": v(1062.59, -9.41) * mm, "end": v(1063.07, -9.9) * mm});
            skLineSegment(sketch, "E92.44.0.35", {"start": v(1072.93, -9.9) * mm, "end": v(1073.41, -9.41) * mm});
            skLineSegment(sketch, "E92.44.0.36", {"start": v(1065.41, 6.59) * mm, "end": v(1065.9, 7.07) * mm});
            skLineSegment(sketch, "E92.44.0.37", {"start": v(1072.93, 9.9) * mm, "end": v(1073.41, 9.41) * mm});
            skLineSegment(sketch, "E92.44.0.38", {"start": v(1070.1, 7.07) * mm, "end": v(1070.59, 6.59) * mm});
            skLineSegment(sketch, "E92.44.0.39", {"start": v(1065.41, -6.59) * mm, "end": v(1065.9, -7.07) * mm});
            skArc(sketch, "E92.45.0.0", {"start": v(1086.59, 9.41) * mm, "mid": v(1086.59, 6.59) * mm, "end": v(1089.41, 6.59) * mm});
            skArc(sketch, "E92.45.0.1", {"start": v(1089.41, -6.59) * mm, "mid": v(1086.59, -6.59) * mm, "end": v(1086.59, -9.41) * mm});
            skLineSegment(sketch, "E92.45.0.2", {"start": v(1080, 24) * mm, "end": v(1104, 24) * mm, "construction": true});
            skLineSegment(sketch, "E92.45.0.3", {"start": v(1088, 16) * mm, "end": v(1096, 16) * mm, "construction": true});
            skArc(sketch, "E92.45.0.4", {"start": v(1087.07, -9.9) * mm, "mid": v(1089.9, -9.9) * mm, "end": v(1089.9, -7.07) * mm});
            skLineSegment(sketch, "E92.45.0.5", {"start": v(1104, 0) * mm, "end": v(1080, -24) * mm, "construction": true});
            skCircle(sketch, "E92.45.0.6", {"center": v(1096, -16) * mm, "radius": 2 * mm});
            skLineSegment(sketch, "E92.45.0.7", {"start": v(1104, -24) * mm, "end": v(1080, -24) * mm, "construction": true});
            skCircle(sketch, "E92.45.0.8", {"center": v(1088, 16) * mm, "radius": 2 * mm});
            skCircle(sketch, "E92.45.0.9", {"center": v(1096, 16) * mm, "radius": 2 * mm});
            skLineSegment(sketch, "E92.45.0.10", {"start": v(1104, -24) * mm, "end": v(1080, 0) * mm, "construction": true});
            skLineSegment(sketch, "E92.45.0.11", {"start": v(1080, 24) * mm, "end": v(1104, 0) * mm, "construction": true});
            skLineSegment(sketch, "E92.45.0.12", {"start": v(1104, 24) * mm, "end": v(1080, 0) * mm, "construction": true});
            skArc(sketch, "E92.45.0.13", {"start": v(1096.93, 9.9) * mm, "mid": v(1094.1, 9.9) * mm, "end": v(1094.1, 7.07) * mm});
            skArc(sketch, "E92.45.0.14", {"start": v(1089.9, 7.07) * mm, "mid": v(1089.9, 9.9) * mm, "end": v(1087.07, 9.9) * mm});
            skArc(sketch, "E92.45.0.15", {"start": v(1094.1, -7.07) * mm, "mid": v(1094.1, -9.9) * mm, "end": v(1096.93, -9.9) * mm});
            skArc(sketch, "E92.45.0.16", {"start": v(1094.59, 6.59) * mm, "mid": v(1097.41, 6.59) * mm, "end": v(1097.41, 9.41) * mm});
            skLineSegment(sketch, "E92.45.0.17", {"start": v(1088, -16) * mm, "end": v(1096, -16) * mm, "construction": true});
            skLineSegment(sketch, "E92.45.0.18", {"start": v(1080, 0) * mm, "end": v(1104, 0) * mm, "construction": true});
            skArc(sketch, "E92.45.0.19", {"start": v(1097.41, -9.41) * mm, "mid": v(1097.41, -6.59) * mm, "end": v(1094.59, -6.59) * mm});
            skCircle(sketch, "E92.45.0.20", {"center": v(1088, -16) * mm, "radius": 2 * mm});
            skCircle(sketch, "E92.45.0.21", {"center": v(1092, 0) * mm, "radius": 2 * mm});
            skPoint(sketch, "E92.45.0.22", {"position": v(1088, -8) * mm});
            skLineSegment(sketch, "E92.45.0.23", {"start": v(1104, 0) * mm, "end": v(1080, 0) * mm, "construction": true});
            skLineSegment(sketch, "E92.45.0.24", {"start": v(1094.59, 6.59) * mm, "end": v(1097.41, 9.41) * mm, "construction": true});
            skLineSegment(sketch, "E92.45.0.25", {"start": v(1094.1, -7.07) * mm, "end": v(1096.93, -9.9) * mm, "construction": true});
            skLineSegment(sketch, "E92.45.0.26", {"start": v(1086.59, 9.41) * mm, "end": v(1089.41, 6.59) * mm, "construction": true});
            skLineSegment(sketch, "E92.45.0.27", {"start": v(1087.07, 9.9) * mm, "end": v(1089.9, 7.07) * mm, "construction": true});
            skLineSegment(sketch, "E92.45.0.28", {"start": v(1096.93, 9.9) * mm, "end": v(1094.1, 7.07) * mm, "construction": true});
            skLineSegment(sketch, "E92.45.0.29", {"start": v(1094.59, -6.59) * mm, "end": v(1097.41, -9.41) * mm, "construction": true});
            skLineSegment(sketch, "E92.45.0.30", {"start": v(1087.07, -9.9) * mm, "end": v(1089.9, -7.07) * mm, "construction": true});
            skLineSegment(sketch, "E92.45.0.31", {"start": v(1089.41, -6.59) * mm, "end": v(1086.59, -9.41) * mm, "construction": true});
            skLineSegment(sketch, "E92.45.0.32", {"start": v(1094.1, -7.07) * mm, "end": v(1094.59, -6.59) * mm});
            skLineSegment(sketch, "E92.45.0.33", {"start": v(1086.59, 9.41) * mm, "end": v(1087.07, 9.9) * mm});
            skLineSegment(sketch, "E92.45.0.34", {"start": v(1086.59, -9.41) * mm, "end": v(1087.07, -9.9) * mm});
            skLineSegment(sketch, "E92.45.0.35", {"start": v(1096.93, -9.9) * mm, "end": v(1097.41, -9.41) * mm});
            skLineSegment(sketch, "E92.45.0.36", {"start": v(1089.41, 6.59) * mm, "end": v(1089.9, 7.07) * mm});
            skLineSegment(sketch, "E92.45.0.37", {"start": v(1096.93, 9.9) * mm, "end": v(1097.41, 9.41) * mm});
            skLineSegment(sketch, "E92.45.0.38", {"start": v(1094.1, 7.07) * mm, "end": v(1094.59, 6.59) * mm});
            skLineSegment(sketch, "E92.45.0.39", {"start": v(1089.41, -6.59) * mm, "end": v(1089.9, -7.07) * mm});
            skArc(sketch, "E92.46.0.0", {"start": v(1110.59, 9.41) * mm, "mid": v(1110.59, 6.59) * mm, "end": v(1113.41, 6.59) * mm});
            skArc(sketch, "E92.46.0.1", {"start": v(1113.41, -6.59) * mm, "mid": v(1110.59, -6.59) * mm, "end": v(1110.59, -9.41) * mm});
            skLineSegment(sketch, "E92.46.0.2", {"start": v(1104, 24) * mm, "end": v(1128, 24) * mm, "construction": true});
            skLineSegment(sketch, "E92.46.0.3", {"start": v(1112, 16) * mm, "end": v(1120, 16) * mm, "construction": true});
            skArc(sketch, "E92.46.0.4", {"start": v(1111.07, -9.9) * mm, "mid": v(1113.9, -9.9) * mm, "end": v(1113.9, -7.07) * mm});
            skLineSegment(sketch, "E92.46.0.5", {"start": v(1128, 0) * mm, "end": v(1104, -24) * mm, "construction": true});
            skCircle(sketch, "E92.46.0.6", {"center": v(1120, -16) * mm, "radius": 2 * mm});
            skLineSegment(sketch, "E92.46.0.7", {"start": v(1128, -24) * mm, "end": v(1104, -24) * mm, "construction": true});
            skCircle(sketch, "E92.46.0.8", {"center": v(1112, 16) * mm, "radius": 2 * mm});
            skCircle(sketch, "E92.46.0.9", {"center": v(1120, 16) * mm, "radius": 2 * mm});
            skLineSegment(sketch, "E92.46.0.10", {"start": v(1128, -24) * mm, "end": v(1104, 0) * mm, "construction": true});
            skLineSegment(sketch, "E92.46.0.11", {"start": v(1104, 24) * mm, "end": v(1128, 0) * mm, "construction": true});
            skLineSegment(sketch, "E92.46.0.12", {"start": v(1128, 24) * mm, "end": v(1104, 0) * mm, "construction": true});
            skArc(sketch, "E92.46.0.13", {"start": v(1120.93, 9.9) * mm, "mid": v(1118.1, 9.9) * mm, "end": v(1118.1, 7.07) * mm});
            skArc(sketch, "E92.46.0.14", {"start": v(1113.9, 7.07) * mm, "mid": v(1113.9, 9.9) * mm, "end": v(1111.07, 9.9) * mm});
            skArc(sketch, "E92.46.0.15", {"start": v(1118.1, -7.07) * mm, "mid": v(1118.1, -9.9) * mm, "end": v(1120.93, -9.9) * mm});
            skArc(sketch, "E92.46.0.16", {"start": v(1118.59, 6.59) * mm, "mid": v(1121.41, 6.59) * mm, "end": v(1121.41, 9.41) * mm});
            skLineSegment(sketch, "E92.46.0.17", {"start": v(1112, -16) * mm, "end": v(1120, -16) * mm, "construction": true});
            skLineSegment(sketch, "E92.46.0.18", {"start": v(1104, 0) * mm, "end": v(1128, 0) * mm, "construction": true});
            skArc(sketch, "E92.46.0.19", {"start": v(1121.41, -9.41) * mm, "mid": v(1121.41, -6.59) * mm, "end": v(1118.59, -6.59) * mm});
            skCircle(sketch, "E92.46.0.20", {"center": v(1112, -16) * mm, "radius": 2 * mm});
            skCircle(sketch, "E92.46.0.21", {"center": v(1116, 0) * mm, "radius": 2 * mm});
            skPoint(sketch, "E92.46.0.22", {"position": v(1112, -8) * mm});
            skLineSegment(sketch, "E92.46.0.23", {"start": v(1128, 0) * mm, "end": v(1104, 0) * mm, "construction": true});
            skLineSegment(sketch, "E92.46.0.24", {"start": v(1118.59, 6.59) * mm, "end": v(1121.41, 9.41) * mm, "construction": true});
            skLineSegment(sketch, "E92.46.0.25", {"start": v(1118.1, -7.07) * mm, "end": v(1120.93, -9.9) * mm, "construction": true});
            skLineSegment(sketch, "E92.46.0.26", {"start": v(1110.59, 9.41) * mm, "end": v(1113.41, 6.59) * mm, "construction": true});
            skLineSegment(sketch, "E92.46.0.27", {"start": v(1111.07, 9.9) * mm, "end": v(1113.9, 7.07) * mm, "construction": true});
            skLineSegment(sketch, "E92.46.0.28", {"start": v(1120.93, 9.9) * mm, "end": v(1118.1, 7.07) * mm, "construction": true});
            skLineSegment(sketch, "E92.46.0.29", {"start": v(1118.59, -6.59) * mm, "end": v(1121.41, -9.41) * mm, "construction": true});
            skLineSegment(sketch, "E92.46.0.30", {"start": v(1111.07, -9.9) * mm, "end": v(1113.9, -7.07) * mm, "construction": true});
            skLineSegment(sketch, "E92.46.0.31", {"start": v(1113.41, -6.59) * mm, "end": v(1110.59, -9.41) * mm, "construction": true});
            skLineSegment(sketch, "E92.46.0.32", {"start": v(1118.1, -7.07) * mm, "end": v(1118.59, -6.59) * mm});
            skLineSegment(sketch, "E92.46.0.33", {"start": v(1110.59, 9.41) * mm, "end": v(1111.07, 9.9) * mm});
            skLineSegment(sketch, "E92.46.0.34", {"start": v(1110.59, -9.41) * mm, "end": v(1111.07, -9.9) * mm});
            skLineSegment(sketch, "E92.46.0.35", {"start": v(1120.93, -9.9) * mm, "end": v(1121.41, -9.41) * mm});
            skLineSegment(sketch, "E92.46.0.36", {"start": v(1113.41, 6.59) * mm, "end": v(1113.9, 7.07) * mm});
            skLineSegment(sketch, "E92.46.0.37", {"start": v(1120.93, 9.9) * mm, "end": v(1121.41, 9.41) * mm});
            skLineSegment(sketch, "E92.46.0.38", {"start": v(1118.1, 7.07) * mm, "end": v(1118.59, 6.59) * mm});
            skLineSegment(sketch, "E92.46.0.39", {"start": v(1113.41, -6.59) * mm, "end": v(1113.9, -7.07) * mm});
            skArc(sketch, "E92.47.0.0", {"start": v(1134.59, 9.41) * mm, "mid": v(1134.59, 6.59) * mm, "end": v(1137.41, 6.59) * mm});
            skArc(sketch, "E92.47.0.1", {"start": v(1137.41, -6.59) * mm, "mid": v(1134.59, -6.59) * mm, "end": v(1134.59, -9.41) * mm});
            skLineSegment(sketch, "E92.47.0.2", {"start": v(1128, 24) * mm, "end": v(1152, 24) * mm, "construction": true});
            skLineSegment(sketch, "E92.47.0.3", {"start": v(1136, 16) * mm, "end": v(1144, 16) * mm, "construction": true});
            skArc(sketch, "E92.47.0.4", {"start": v(1135.07, -9.9) * mm, "mid": v(1137.9, -9.9) * mm, "end": v(1137.9, -7.07) * mm});
            skLineSegment(sketch, "E92.47.0.5", {"start": v(1152, 0) * mm, "end": v(1128, -24) * mm, "construction": true});
            skCircle(sketch, "E92.47.0.6", {"center": v(1144, -16) * mm, "radius": 2 * mm});
            skLineSegment(sketch, "E92.47.0.7", {"start": v(1152, -24) * mm, "end": v(1128, -24) * mm, "construction": true});
            skCircle(sketch, "E92.47.0.8", {"center": v(1136, 16) * mm, "radius": 2 * mm});
            skCircle(sketch, "E92.47.0.9", {"center": v(1144, 16) * mm, "radius": 2 * mm});
            skLineSegment(sketch, "E92.47.0.10", {"start": v(1152, -24) * mm, "end": v(1128, 0) * mm, "construction": true});
            skLineSegment(sketch, "E92.47.0.11", {"start": v(1128, 24) * mm, "end": v(1152, 0) * mm, "construction": true});
            skLineSegment(sketch, "E92.47.0.12", {"start": v(1152, 24) * mm, "end": v(1128, 0) * mm, "construction": true});
            skArc(sketch, "E92.47.0.13", {"start": v(1144.93, 9.9) * mm, "mid": v(1142.1, 9.9) * mm, "end": v(1142.1, 7.07) * mm});
            skArc(sketch, "E92.47.0.14", {"start": v(1137.9, 7.07) * mm, "mid": v(1137.9, 9.9) * mm, "end": v(1135.07, 9.9) * mm});
            skArc(sketch, "E92.47.0.15", {"start": v(1142.1, -7.07) * mm, "mid": v(1142.1, -9.9) * mm, "end": v(1144.93, -9.9) * mm});
            skArc(sketch, "E92.47.0.16", {"start": v(1142.59, 6.59) * mm, "mid": v(1145.41, 6.59) * mm, "end": v(1145.41, 9.41) * mm});
            skLineSegment(sketch, "E92.47.0.17", {"start": v(1136, -16) * mm, "end": v(1144, -16) * mm, "construction": true});
            skLineSegment(sketch, "E92.47.0.18", {"start": v(1128, 0) * mm, "end": v(1152, 0) * mm, "construction": true});
            skArc(sketch, "E92.47.0.19", {"start": v(1145.41, -9.41) * mm, "mid": v(1145.41, -6.59) * mm, "end": v(1142.59, -6.59) * mm});
            skCircle(sketch, "E92.47.0.20", {"center": v(1136, -16) * mm, "radius": 2 * mm});
            skCircle(sketch, "E92.47.0.21", {"center": v(1140, 0) * mm, "radius": 2 * mm});
            skPoint(sketch, "E92.47.0.22", {"position": v(1136, -8) * mm});
            skLineSegment(sketch, "E92.47.0.23", {"start": v(1152, 0) * mm, "end": v(1128, 0) * mm, "construction": true});
            skLineSegment(sketch, "E92.47.0.24", {"start": v(1142.59, 6.59) * mm, "end": v(1145.41, 9.41) * mm, "construction": true});
            skLineSegment(sketch, "E92.47.0.25", {"start": v(1142.1, -7.07) * mm, "end": v(1144.93, -9.9) * mm, "construction": true});
            skLineSegment(sketch, "E92.47.0.26", {"start": v(1134.59, 9.41) * mm, "end": v(1137.41, 6.59) * mm, "construction": true});
            skLineSegment(sketch, "E92.47.0.27", {"start": v(1135.07, 9.9) * mm, "end": v(1137.9, 7.07) * mm, "construction": true});
            skLineSegment(sketch, "E92.47.0.28", {"start": v(1144.93, 9.9) * mm, "end": v(1142.1, 7.07) * mm, "construction": true});
            skLineSegment(sketch, "E92.47.0.29", {"start": v(1142.59, -6.59) * mm, "end": v(1145.41, -9.41) * mm, "construction": true});
            skLineSegment(sketch, "E92.47.0.30", {"start": v(1135.07, -9.9) * mm, "end": v(1137.9, -7.07) * mm, "construction": true});
            skLineSegment(sketch, "E92.47.0.31", {"start": v(1137.41, -6.59) * mm, "end": v(1134.59, -9.41) * mm, "construction": true});
            skLineSegment(sketch, "E92.47.0.32", {"start": v(1142.1, -7.07) * mm, "end": v(1142.59, -6.59) * mm});
            skLineSegment(sketch, "E92.47.0.33", {"start": v(1134.59, 9.41) * mm, "end": v(1135.07, 9.9) * mm});
            skLineSegment(sketch, "E92.47.0.34", {"start": v(1134.59, -9.41) * mm, "end": v(1135.07, -9.9) * mm});
            skLineSegment(sketch, "E92.47.0.35", {"start": v(1144.93, -9.9) * mm, "end": v(1145.41, -9.41) * mm});
            skLineSegment(sketch, "E92.47.0.36", {"start": v(1137.41, 6.59) * mm, "end": v(1137.9, 7.07) * mm});
            skLineSegment(sketch, "E92.47.0.37", {"start": v(1144.93, 9.9) * mm, "end": v(1145.41, 9.41) * mm});
            skLineSegment(sketch, "E92.47.0.38", {"start": v(1142.1, 7.07) * mm, "end": v(1142.59, 6.59) * mm});
            skLineSegment(sketch, "E92.47.0.39", {"start": v(1137.41, -6.59) * mm, "end": v(1137.9, -7.07) * mm});
            skArc(sketch, "E92.48.0.0", {"start": v(1158.59, 9.41) * mm, "mid": v(1158.59, 6.59) * mm, "end": v(1161.41, 6.59) * mm});
            skArc(sketch, "E92.48.0.1", {"start": v(1161.41, -6.59) * mm, "mid": v(1158.59, -6.59) * mm, "end": v(1158.59, -9.41) * mm});
            skLineSegment(sketch, "E92.48.0.2", {"start": v(1152, 24) * mm, "end": v(1176, 24) * mm, "construction": true});
            skLineSegment(sketch, "E92.48.0.3", {"start": v(1160, 16) * mm, "end": v(1168, 16) * mm, "construction": true});
            skArc(sketch, "E92.48.0.4", {"start": v(1159.07, -9.9) * mm, "mid": v(1161.9, -9.9) * mm, "end": v(1161.9, -7.07) * mm});
            skLineSegment(sketch, "E92.48.0.5", {"start": v(1176, 0) * mm, "end": v(1152, -24) * mm, "construction": true});
            skCircle(sketch, "E92.48.0.6", {"center": v(1168, -16) * mm, "radius": 2 * mm});
            skLineSegment(sketch, "E92.48.0.7", {"start": v(1176, -24) * mm, "end": v(1152, -24) * mm, "construction": true});
            skCircle(sketch, "E92.48.0.8", {"center": v(1160, 16) * mm, "radius": 2 * mm});
            skCircle(sketch, "E92.48.0.9", {"center": v(1168, 16) * mm, "radius": 2 * mm});
            skLineSegment(sketch, "E92.48.0.10", {"start": v(1176, -24) * mm, "end": v(1152, 0) * mm, "construction": true});
            skLineSegment(sketch, "E92.48.0.11", {"start": v(1152, 24) * mm, "end": v(1176, 0) * mm, "construction": true});
            skLineSegment(sketch, "E92.48.0.12", {"start": v(1176, 24) * mm, "end": v(1152, 0) * mm, "construction": true});
            skArc(sketch, "E92.48.0.13", {"start": v(1168.93, 9.9) * mm, "mid": v(1166.1, 9.9) * mm, "end": v(1166.1, 7.07) * mm});
            skArc(sketch, "E92.48.0.14", {"start": v(1161.9, 7.07) * mm, "mid": v(1161.9, 9.9) * mm, "end": v(1159.07, 9.9) * mm});
            skArc(sketch, "E92.48.0.15", {"start": v(1166.1, -7.07) * mm, "mid": v(1166.1, -9.9) * mm, "end": v(1168.93, -9.9) * mm});
            skArc(sketch, "E92.48.0.16", {"start": v(1166.59, 6.59) * mm, "mid": v(1169.41, 6.59) * mm, "end": v(1169.41, 9.41) * mm});
            skLineSegment(sketch, "E92.48.0.17", {"start": v(1160, -16) * mm, "end": v(1168, -16) * mm, "construction": true});
            skLineSegment(sketch, "E92.48.0.18", {"start": v(1152, 0) * mm, "end": v(1176, 0) * mm, "construction": true});
            skArc(sketch, "E92.48.0.19", {"start": v(1169.41, -9.41) * mm, "mid": v(1169.41, -6.59) * mm, "end": v(1166.59, -6.59) * mm});
            skCircle(sketch, "E92.48.0.20", {"center": v(1160, -16) * mm, "radius": 2 * mm});
            skCircle(sketch, "E92.48.0.21", {"center": v(1164, 0) * mm, "radius": 2 * mm});
            skPoint(sketch, "E92.48.0.22", {"position": v(1160, -8) * mm});
            skLineSegment(sketch, "E92.48.0.23", {"start": v(1176, 0) * mm, "end": v(1152, 0) * mm, "construction": true});
            skLineSegment(sketch, "E92.48.0.24", {"start": v(1166.59, 6.59) * mm, "end": v(1169.41, 9.41) * mm, "construction": true});
            skLineSegment(sketch, "E92.48.0.25", {"start": v(1166.1, -7.07) * mm, "end": v(1168.93, -9.9) * mm, "construction": true});
            skLineSegment(sketch, "E92.48.0.26", {"start": v(1158.59, 9.41) * mm, "end": v(1161.41, 6.59) * mm, "construction": true});
            skLineSegment(sketch, "E92.48.0.27", {"start": v(1159.07, 9.9) * mm, "end": v(1161.9, 7.07) * mm, "construction": true});
            skLineSegment(sketch, "E92.48.0.28", {"start": v(1168.93, 9.9) * mm, "end": v(1166.1, 7.07) * mm, "construction": true});
            skLineSegment(sketch, "E92.48.0.29", {"start": v(1166.59, -6.59) * mm, "end": v(1169.41, -9.41) * mm, "construction": true});
            skLineSegment(sketch, "E92.48.0.30", {"start": v(1159.07, -9.9) * mm, "end": v(1161.9, -7.07) * mm, "construction": true});
            skLineSegment(sketch, "E92.48.0.31", {"start": v(1161.41, -6.59) * mm, "end": v(1158.59, -9.41) * mm, "construction": true});
            skLineSegment(sketch, "E92.48.0.32", {"start": v(1166.1, -7.07) * mm, "end": v(1166.59, -6.59) * mm});
            skLineSegment(sketch, "E92.48.0.33", {"start": v(1158.59, 9.41) * mm, "end": v(1159.07, 9.9) * mm});
            skLineSegment(sketch, "E92.48.0.34", {"start": v(1158.59, -9.41) * mm, "end": v(1159.07, -9.9) * mm});
            skLineSegment(sketch, "E92.48.0.35", {"start": v(1168.93, -9.9) * mm, "end": v(1169.41, -9.41) * mm});
            skLineSegment(sketch, "E92.48.0.36", {"start": v(1161.41, 6.59) * mm, "end": v(1161.9, 7.07) * mm});
            skLineSegment(sketch, "E92.48.0.37", {"start": v(1168.93, 9.9) * mm, "end": v(1169.41, 9.41) * mm});
            skLineSegment(sketch, "E92.48.0.38", {"start": v(1166.1, 7.07) * mm, "end": v(1166.59, 6.59) * mm});
            skLineSegment(sketch, "E92.48.0.39", {"start": v(1161.41, -6.59) * mm, "end": v(1161.9, -7.07) * mm});
            skArc(sketch, "E92.49.0.0", {"start": v(1182.59, 9.41) * mm, "mid": v(1182.59, 6.59) * mm, "end": v(1185.41, 6.59) * mm});
            skArc(sketch, "E92.49.0.1", {"start": v(1185.41, -6.59) * mm, "mid": v(1182.59, -6.59) * mm, "end": v(1182.59, -9.41) * mm});
            skLineSegment(sketch, "E92.49.0.2", {"start": v(1176, 24) * mm, "end": v(1200, 24) * mm, "construction": true});
            skLineSegment(sketch, "E92.49.0.3", {"start": v(1184, 16) * mm, "end": v(1192, 16) * mm, "construction": true});
            skArc(sketch, "E92.49.0.4", {"start": v(1183.07, -9.9) * mm, "mid": v(1185.9, -9.9) * mm, "end": v(1185.9, -7.07) * mm});
            skLineSegment(sketch, "E92.49.0.5", {"start": v(1200, 0) * mm, "end": v(1176, -24) * mm, "construction": true});
            skCircle(sketch, "E92.49.0.6", {"center": v(1192, -16) * mm, "radius": 2 * mm});
            skLineSegment(sketch, "E92.49.0.7", {"start": v(1200, -24) * mm, "end": v(1176, -24) * mm, "construction": true});
            skCircle(sketch, "E92.49.0.8", {"center": v(1184, 16) * mm, "radius": 2 * mm});
            skCircle(sketch, "E92.49.0.9", {"center": v(1192, 16) * mm, "radius": 2 * mm});
            skLineSegment(sketch, "E92.49.0.10", {"start": v(1200, -24) * mm, "end": v(1176, 0) * mm, "construction": true});
            skLineSegment(sketch, "E92.49.0.11", {"start": v(1176, 24) * mm, "end": v(1200, 0) * mm, "construction": true});
            skLineSegment(sketch, "E92.49.0.12", {"start": v(1200, 24) * mm, "end": v(1176, 0) * mm, "construction": true});
            skArc(sketch, "E92.49.0.13", {"start": v(1192.93, 9.9) * mm, "mid": v(1190.1, 9.9) * mm, "end": v(1190.1, 7.07) * mm});
            skArc(sketch, "E92.49.0.14", {"start": v(1185.9, 7.07) * mm, "mid": v(1185.9, 9.9) * mm, "end": v(1183.07, 9.9) * mm});
            skArc(sketch, "E92.49.0.15", {"start": v(1190.1, -7.07) * mm, "mid": v(1190.1, -9.9) * mm, "end": v(1192.93, -9.9) * mm});
            skArc(sketch, "E92.49.0.16", {"start": v(1190.59, 6.59) * mm, "mid": v(1193.41, 6.59) * mm, "end": v(1193.41, 9.41) * mm});
            skLineSegment(sketch, "E92.49.0.17", {"start": v(1184, -16) * mm, "end": v(1192, -16) * mm, "construction": true});
            skLineSegment(sketch, "E92.49.0.18", {"start": v(1176, 0) * mm, "end": v(1200, 0) * mm, "construction": true});
            skArc(sketch, "E92.49.0.19", {"start": v(1193.41, -9.41) * mm, "mid": v(1193.41, -6.59) * mm, "end": v(1190.59, -6.59) * mm});
            skCircle(sketch, "E92.49.0.20", {"center": v(1184, -16) * mm, "radius": 2 * mm});
            skCircle(sketch, "E92.49.0.21", {"center": v(1188, 0) * mm, "radius": 2 * mm});
            skPoint(sketch, "E92.49.0.22", {"position": v(1184, -8) * mm});
            skLineSegment(sketch, "E92.49.0.23", {"start": v(1200, 0) * mm, "end": v(1176, 0) * mm, "construction": true});
            skLineSegment(sketch, "E92.49.0.24", {"start": v(1190.59, 6.59) * mm, "end": v(1193.41, 9.41) * mm, "construction": true});
            skLineSegment(sketch, "E92.49.0.25", {"start": v(1190.1, -7.07) * mm, "end": v(1192.93, -9.9) * mm, "construction": true});
            skLineSegment(sketch, "E92.49.0.26", {"start": v(1182.59, 9.41) * mm, "end": v(1185.41, 6.59) * mm, "construction": true});
            skLineSegment(sketch, "E92.49.0.27", {"start": v(1183.07, 9.9) * mm, "end": v(1185.9, 7.07) * mm, "construction": true});
            skLineSegment(sketch, "E92.49.0.28", {"start": v(1192.93, 9.9) * mm, "end": v(1190.1, 7.07) * mm, "construction": true});
            skLineSegment(sketch, "E92.49.0.29", {"start": v(1190.59, -6.59) * mm, "end": v(1193.41, -9.41) * mm, "construction": true});
            skLineSegment(sketch, "E92.49.0.30", {"start": v(1183.07, -9.9) * mm, "end": v(1185.9, -7.07) * mm, "construction": true});
            skLineSegment(sketch, "E92.49.0.31", {"start": v(1185.41, -6.59) * mm, "end": v(1182.59, -9.41) * mm, "construction": true});
            skLineSegment(sketch, "E92.49.0.32", {"start": v(1190.1, -7.07) * mm, "end": v(1190.59, -6.59) * mm});
            skLineSegment(sketch, "E92.49.0.33", {"start": v(1182.59, 9.41) * mm, "end": v(1183.07, 9.9) * mm});
            skLineSegment(sketch, "E92.49.0.34", {"start": v(1182.59, -9.41) * mm, "end": v(1183.07, -9.9) * mm});
            skLineSegment(sketch, "E92.49.0.35", {"start": v(1192.93, -9.9) * mm, "end": v(1193.41, -9.41) * mm});
            skLineSegment(sketch, "E92.49.0.36", {"start": v(1185.41, 6.59) * mm, "end": v(1185.9, 7.07) * mm});
            skLineSegment(sketch, "E92.49.0.37", {"start": v(1192.93, 9.9) * mm, "end": v(1193.41, 9.41) * mm});
            skLineSegment(sketch, "E92.49.0.38", {"start": v(1190.1, 7.07) * mm, "end": v(1190.59, 6.59) * mm});
            skLineSegment(sketch, "E92.49.0.39", {"start": v(1185.41, -6.59) * mm, "end": v(1185.9, -7.07) * mm});
            skLineSegment(sketch, "E92.direction1", {"start": v(0, -24) * mm, "end": v(24, -24) * mm, "construction": true});
            skSolve(sketch);
        }
        {
            var Q0;
            Q0=qSketchRegion(id+"F40",true);
            extrude(context, id + "F41", {"entities" : qUnion([Q0]), "operationType" : NewBodyOperationType.REMOVE, "oppositeDirection" : true, "depth" : 25 * mm, "offsetDistance" : 25 * mm});
        }
        {
            var Q0;
            Q0=qCreatedBy(makeId("Top.planeOp"),FACE);
            var sketch = newSketch(context, id + "F42", { "sketchPlane" : qUnion([Q0]) });
            skCircle(sketch, "E93.0", {"center": v(16, 16) * mm, "radius": 2 * mm, "construction": true});
            skCircle(sketch, "E94.0", {"center": v(32, -16) * mm, "radius": 2 * mm, "construction": true});
            skLineSegment(sketch, "E95.bottom", {"start": v(16, 16) * mm, "end": v(32, 16) * mm, "construction": true});
            skLineSegment(sketch, "E95.top", {"start": v(16, -16) * mm, "end": v(32, -16) * mm, "construction": true});
            skLineSegment(sketch, "E95.left", {"start": v(16, 16) * mm, "end": v(16, -16) * mm, "construction": true});
            skLineSegment(sketch, "E95.right", {"start": v(32, 16) * mm, "end": v(32, -16) * mm, "construction": true});
            skLineSegment(sketch, "E96", {"start": v(24, 16) * mm, "end": v(24, -16) * mm, "construction": true});
            skCircle(sketch, "E97", {"center": v(24, 0) * mm, "radius": 7 * mm});
            skArc(sketch, "E98", {"start": v(26, 16) * mm, "mid": v(24, 18) * mm, "end": v(22, 16) * mm});
            skArc(sketch, "E99", {"start": v(22, -16) * mm, "mid": v(24, -18) * mm, "end": v(26, -16) * mm});
            skArc(sketch, "E100", {"start": v(22, 12) * mm, "mid": v(24, 10) * mm, "end": v(26, 12) * mm});
            skArc(sketch, "E101", {"start": v(26, -12) * mm, "mid": v(24, -10) * mm, "end": v(22, -12) * mm});
            skLineSegment(sketch, "E102", {"start": v(22, 16) * mm, "end": v(22, 12) * mm});
            skLineSegment(sketch, "E103", {"start": v(26, 16) * mm, "end": v(26, 12) * mm});
            skLineSegment(sketch, "E104", {"start": v(26, -16) * mm, "end": v(26, -12) * mm});
            skLineSegment(sketch, "E105", {"start": v(22, -16) * mm, "end": v(22, -12) * mm});
            skArc(sketch, "E106.1.0.0", {"start": v(50, -12) * mm, "mid": v(48, -10) * mm, "end": v(46, -12) * mm});
            skArc(sketch, "E106.1.0.1", {"start": v(46, 12) * mm, "mid": v(48, 10) * mm, "end": v(50, 12) * mm});
            skLineSegment(sketch, "E106.1.0.2", {"start": v(46, 16) * mm, "end": v(46, 12) * mm});
            skLineSegment(sketch, "E106.1.0.3", {"start": v(50, -16) * mm, "end": v(50, -12) * mm});
            skLineSegment(sketch, "E106.1.0.4", {"start": v(46, -16) * mm, "end": v(46, -12) * mm});
            skArc(sketch, "E106.1.0.5", {"start": v(46, -16) * mm, "mid": v(48, -18) * mm, "end": v(50, -16) * mm});
            skLineSegment(sketch, "E106.1.0.6", {"start": v(50, 16) * mm, "end": v(50, 12) * mm});
            skArc(sketch, "E106.1.0.7", {"start": v(50, 16) * mm, "mid": v(48, 18) * mm, "end": v(46, 16) * mm});
            skCircle(sketch, "E106.1.0.8", {"center": v(48, 0) * mm, "radius": 7 * mm});
            skArc(sketch, "E106.2.0.0", {"start": v(74, -12) * mm, "mid": v(72, -10) * mm, "end": v(70, -12) * mm});
            skArc(sketch, "E106.2.0.1", {"start": v(70, 12) * mm, "mid": v(72, 10) * mm, "end": v(74, 12) * mm});
            skLineSegment(sketch, "E106.2.0.2", {"start": v(70, 16) * mm, "end": v(70, 12) * mm});
            skLineSegment(sketch, "E106.2.0.3", {"start": v(74, -16) * mm, "end": v(74, -12) * mm});
            skLineSegment(sketch, "E106.2.0.4", {"start": v(70, -16) * mm, "end": v(70, -12) * mm});
            skArc(sketch, "E106.2.0.5", {"start": v(70, -16) * mm, "mid": v(72, -18) * mm, "end": v(74, -16) * mm});
            skLineSegment(sketch, "E106.2.0.6", {"start": v(74, 16) * mm, "end": v(74, 12) * mm});
            skArc(sketch, "E106.2.0.7", {"start": v(74, 16) * mm, "mid": v(72, 18) * mm, "end": v(70, 16) * mm});
            skCircle(sketch, "E106.2.0.8", {"center": v(72, 0) * mm, "radius": 7 * mm});
            skArc(sketch, "E106.3.0.0", {"start": v(98, -12) * mm, "mid": v(96, -10) * mm, "end": v(94, -12) * mm});
            skArc(sketch, "E106.3.0.1", {"start": v(94, 12) * mm, "mid": v(96, 10) * mm, "end": v(98, 12) * mm});
            skLineSegment(sketch, "E106.3.0.2", {"start": v(94, 16) * mm, "end": v(94, 12) * mm});
            skLineSegment(sketch, "E106.3.0.3", {"start": v(98, -16) * mm, "end": v(98, -12) * mm});
            skLineSegment(sketch, "E106.3.0.4", {"start": v(94, -16) * mm, "end": v(94, -12) * mm});
            skArc(sketch, "E106.3.0.5", {"start": v(94, -16) * mm, "mid": v(96, -18) * mm, "end": v(98, -16) * mm});
            skLineSegment(sketch, "E106.3.0.6", {"start": v(98, 16) * mm, "end": v(98, 12) * mm});
            skArc(sketch, "E106.3.0.7", {"start": v(98, 16) * mm, "mid": v(96, 18) * mm, "end": v(94, 16) * mm});
            skCircle(sketch, "E106.3.0.8", {"center": v(96, 0) * mm, "radius": 7 * mm});
            skArc(sketch, "E106.4.0.0", {"start": v(122, -12) * mm, "mid": v(120, -10) * mm, "end": v(118, -12) * mm});
            skArc(sketch, "E106.4.0.1", {"start": v(118, 12) * mm, "mid": v(120, 10) * mm, "end": v(122, 12) * mm});
            skLineSegment(sketch, "E106.4.0.2", {"start": v(118, 16) * mm, "end": v(118, 12) * mm});
            skLineSegment(sketch, "E106.4.0.3", {"start": v(122, -16) * mm, "end": v(122, -12) * mm});
            skLineSegment(sketch, "E106.4.0.4", {"start": v(118, -16) * mm, "end": v(118, -12) * mm});
            skArc(sketch, "E106.4.0.5", {"start": v(118, -16) * mm, "mid": v(120, -18) * mm, "end": v(122, -16) * mm});
            skLineSegment(sketch, "E106.4.0.6", {"start": v(122, 16) * mm, "end": v(122, 12) * mm});
            skArc(sketch, "E106.4.0.7", {"start": v(122, 16) * mm, "mid": v(120, 18) * mm, "end": v(118, 16) * mm});
            skCircle(sketch, "E106.4.0.8", {"center": v(120, 0) * mm, "radius": 7 * mm});
            skArc(sketch, "E106.5.0.0", {"start": v(146, -12) * mm, "mid": v(144, -10) * mm, "end": v(142, -12) * mm});
            skArc(sketch, "E106.5.0.1", {"start": v(142, 12) * mm, "mid": v(144, 10) * mm, "end": v(146, 12) * mm});
            skLineSegment(sketch, "E106.5.0.2", {"start": v(142, 16) * mm, "end": v(142, 12) * mm});
            skLineSegment(sketch, "E106.5.0.3", {"start": v(146, -16) * mm, "end": v(146, -12) * mm});
            skLineSegment(sketch, "E106.5.0.4", {"start": v(142, -16) * mm, "end": v(142, -12) * mm});
            skArc(sketch, "E106.5.0.5", {"start": v(142, -16) * mm, "mid": v(144, -18) * mm, "end": v(146, -16) * mm});
            skLineSegment(sketch, "E106.5.0.6", {"start": v(146, 16) * mm, "end": v(146, 12) * mm});
            skArc(sketch, "E106.5.0.7", {"start": v(146, 16) * mm, "mid": v(144, 18) * mm, "end": v(142, 16) * mm});
            skCircle(sketch, "E106.5.0.8", {"center": v(144, 0) * mm, "radius": 7 * mm});
            skArc(sketch, "E106.6.0.0", {"start": v(170, -12) * mm, "mid": v(168, -10) * mm, "end": v(166, -12) * mm});
            skArc(sketch, "E106.6.0.1", {"start": v(166, 12) * mm, "mid": v(168, 10) * mm, "end": v(170, 12) * mm});
            skLineSegment(sketch, "E106.6.0.2", {"start": v(166, 16) * mm, "end": v(166, 12) * mm});
            skLineSegment(sketch, "E106.6.0.3", {"start": v(170, -16) * mm, "end": v(170, -12) * mm});
            skLineSegment(sketch, "E106.6.0.4", {"start": v(166, -16) * mm, "end": v(166, -12) * mm});
            skArc(sketch, "E106.6.0.5", {"start": v(166, -16) * mm, "mid": v(168, -18) * mm, "end": v(170, -16) * mm});
            skLineSegment(sketch, "E106.6.0.6", {"start": v(170, 16) * mm, "end": v(170, 12) * mm});
            skArc(sketch, "E106.6.0.7", {"start": v(170, 16) * mm, "mid": v(168, 18) * mm, "end": v(166, 16) * mm});
            skCircle(sketch, "E106.6.0.8", {"center": v(168, 0) * mm, "radius": 7 * mm});
            skArc(sketch, "E106.7.0.0", {"start": v(194, -12) * mm, "mid": v(192, -10) * mm, "end": v(190, -12) * mm});
            skArc(sketch, "E106.7.0.1", {"start": v(190, 12) * mm, "mid": v(192, 10) * mm, "end": v(194, 12) * mm});
            skLineSegment(sketch, "E106.7.0.2", {"start": v(190, 16) * mm, "end": v(190, 12) * mm});
            skLineSegment(sketch, "E106.7.0.3", {"start": v(194, -16) * mm, "end": v(194, -12) * mm});
            skLineSegment(sketch, "E106.7.0.4", {"start": v(190, -16) * mm, "end": v(190, -12) * mm});
            skArc(sketch, "E106.7.0.5", {"start": v(190, -16) * mm, "mid": v(192, -18) * mm, "end": v(194, -16) * mm});
            skLineSegment(sketch, "E106.7.0.6", {"start": v(194, 16) * mm, "end": v(194, 12) * mm});
            skArc(sketch, "E106.7.0.7", {"start": v(194, 16) * mm, "mid": v(192, 18) * mm, "end": v(190, 16) * mm});
            skCircle(sketch, "E106.7.0.8", {"center": v(192, 0) * mm, "radius": 7 * mm});
            skArc(sketch, "E106.8.0.0", {"start": v(218, -12) * mm, "mid": v(216, -10) * mm, "end": v(214, -12) * mm});
            skArc(sketch, "E106.8.0.1", {"start": v(214, 12) * mm, "mid": v(216, 10) * mm, "end": v(218, 12) * mm});
            skLineSegment(sketch, "E106.8.0.2", {"start": v(214, 16) * mm, "end": v(214, 12) * mm});
            skLineSegment(sketch, "E106.8.0.3", {"start": v(218, -16) * mm, "end": v(218, -12) * mm});
            skLineSegment(sketch, "E106.8.0.4", {"start": v(214, -16) * mm, "end": v(214, -12) * mm});
            skArc(sketch, "E106.8.0.5", {"start": v(214, -16) * mm, "mid": v(216, -18) * mm, "end": v(218, -16) * mm});
            skLineSegment(sketch, "E106.8.0.6", {"start": v(218, 16) * mm, "end": v(218, 12) * mm});
            skArc(sketch, "E106.8.0.7", {"start": v(218, 16) * mm, "mid": v(216, 18) * mm, "end": v(214, 16) * mm});
            skCircle(sketch, "E106.8.0.8", {"center": v(216, 0) * mm, "radius": 7 * mm});
            skArc(sketch, "E106.9.0.0", {"start": v(242, -12) * mm, "mid": v(240, -10) * mm, "end": v(238, -12) * mm});
            skArc(sketch, "E106.9.0.1", {"start": v(238, 12) * mm, "mid": v(240, 10) * mm, "end": v(242, 12) * mm});
            skLineSegment(sketch, "E106.9.0.2", {"start": v(238, 16) * mm, "end": v(238, 12) * mm});
            skLineSegment(sketch, "E106.9.0.3", {"start": v(242, -16) * mm, "end": v(242, -12) * mm});
            skLineSegment(sketch, "E106.9.0.4", {"start": v(238, -16) * mm, "end": v(238, -12) * mm});
            skArc(sketch, "E106.9.0.5", {"start": v(238, -16) * mm, "mid": v(240, -18) * mm, "end": v(242, -16) * mm});
            skLineSegment(sketch, "E106.9.0.6", {"start": v(242, 16) * mm, "end": v(242, 12) * mm});
            skArc(sketch, "E106.9.0.7", {"start": v(242, 16) * mm, "mid": v(240, 18) * mm, "end": v(238, 16) * mm});
            skCircle(sketch, "E106.9.0.8", {"center": v(240, 0) * mm, "radius": 7 * mm});
            skArc(sketch, "E106.10.0.0", {"start": v(266, -12) * mm, "mid": v(264, -10) * mm, "end": v(262, -12) * mm});
            skArc(sketch, "E106.10.0.1", {"start": v(262, 12) * mm, "mid": v(264, 10) * mm, "end": v(266, 12) * mm});
            skLineSegment(sketch, "E106.10.0.2", {"start": v(262, 16) * mm, "end": v(262, 12) * mm});
            skLineSegment(sketch, "E106.10.0.3", {"start": v(266, -16) * mm, "end": v(266, -12) * mm});
            skLineSegment(sketch, "E106.10.0.4", {"start": v(262, -16) * mm, "end": v(262, -12) * mm});
            skArc(sketch, "E106.10.0.5", {"start": v(262, -16) * mm, "mid": v(264, -18) * mm, "end": v(266, -16) * mm});
            skLineSegment(sketch, "E106.10.0.6", {"start": v(266, 16) * mm, "end": v(266, 12) * mm});
            skArc(sketch, "E106.10.0.7", {"start": v(266, 16) * mm, "mid": v(264, 18) * mm, "end": v(262, 16) * mm});
            skCircle(sketch, "E106.10.0.8", {"center": v(264, 0) * mm, "radius": 7 * mm});
            skArc(sketch, "E106.11.0.0", {"start": v(290, -12) * mm, "mid": v(288, -10) * mm, "end": v(286, -12) * mm});
            skArc(sketch, "E106.11.0.1", {"start": v(286, 12) * mm, "mid": v(288, 10) * mm, "end": v(290, 12) * mm});
            skLineSegment(sketch, "E106.11.0.2", {"start": v(286, 16) * mm, "end": v(286, 12) * mm});
            skLineSegment(sketch, "E106.11.0.3", {"start": v(290, -16) * mm, "end": v(290, -12) * mm});
            skLineSegment(sketch, "E106.11.0.4", {"start": v(286, -16) * mm, "end": v(286, -12) * mm});
            skArc(sketch, "E106.11.0.5", {"start": v(286, -16) * mm, "mid": v(288, -18) * mm, "end": v(290, -16) * mm});
            skLineSegment(sketch, "E106.11.0.6", {"start": v(290, 16) * mm, "end": v(290, 12) * mm});
            skArc(sketch, "E106.11.0.7", {"start": v(290, 16) * mm, "mid": v(288, 18) * mm, "end": v(286, 16) * mm});
            skCircle(sketch, "E106.11.0.8", {"center": v(288, 0) * mm, "radius": 7 * mm});
            skArc(sketch, "E106.12.0.0", {"start": v(314, -12) * mm, "mid": v(312, -10) * mm, "end": v(310, -12) * mm});
            skArc(sketch, "E106.12.0.1", {"start": v(310, 12) * mm, "mid": v(312, 10) * mm, "end": v(314, 12) * mm});
            skLineSegment(sketch, "E106.12.0.2", {"start": v(310, 16) * mm, "end": v(310, 12) * mm});
            skLineSegment(sketch, "E106.12.0.3", {"start": v(314, -16) * mm, "end": v(314, -12) * mm});
            skLineSegment(sketch, "E106.12.0.4", {"start": v(310, -16) * mm, "end": v(310, -12) * mm});
            skArc(sketch, "E106.12.0.5", {"start": v(310, -16) * mm, "mid": v(312, -18) * mm, "end": v(314, -16) * mm});
            skLineSegment(sketch, "E106.12.0.6", {"start": v(314, 16) * mm, "end": v(314, 12) * mm});
            skArc(sketch, "E106.12.0.7", {"start": v(314, 16) * mm, "mid": v(312, 18) * mm, "end": v(310, 16) * mm});
            skCircle(sketch, "E106.12.0.8", {"center": v(312, 0) * mm, "radius": 7 * mm});
            skArc(sketch, "E106.13.0.0", {"start": v(338, -12) * mm, "mid": v(336, -10) * mm, "end": v(334, -12) * mm});
            skArc(sketch, "E106.13.0.1", {"start": v(334, 12) * mm, "mid": v(336, 10) * mm, "end": v(338, 12) * mm});
            skLineSegment(sketch, "E106.13.0.2", {"start": v(334, 16) * mm, "end": v(334, 12) * mm});
            skLineSegment(sketch, "E106.13.0.3", {"start": v(338, -16) * mm, "end": v(338, -12) * mm});
            skLineSegment(sketch, "E106.13.0.4", {"start": v(334, -16) * mm, "end": v(334, -12) * mm});
            skArc(sketch, "E106.13.0.5", {"start": v(334, -16) * mm, "mid": v(336, -18) * mm, "end": v(338, -16) * mm});
            skLineSegment(sketch, "E106.13.0.6", {"start": v(338, 16) * mm, "end": v(338, 12) * mm});
            skArc(sketch, "E106.13.0.7", {"start": v(338, 16) * mm, "mid": v(336, 18) * mm, "end": v(334, 16) * mm});
            skCircle(sketch, "E106.13.0.8", {"center": v(336, 0) * mm, "radius": 7 * mm});
            skArc(sketch, "E106.14.0.0", {"start": v(362, -12) * mm, "mid": v(360, -10) * mm, "end": v(358, -12) * mm});
            skArc(sketch, "E106.14.0.1", {"start": v(358, 12) * mm, "mid": v(360, 10) * mm, "end": v(362, 12) * mm});
            skLineSegment(sketch, "E106.14.0.2", {"start": v(358, 16) * mm, "end": v(358, 12) * mm});
            skLineSegment(sketch, "E106.14.0.3", {"start": v(362, -16) * mm, "end": v(362, -12) * mm});
            skLineSegment(sketch, "E106.14.0.4", {"start": v(358, -16) * mm, "end": v(358, -12) * mm});
            skArc(sketch, "E106.14.0.5", {"start": v(358, -16) * mm, "mid": v(360, -18) * mm, "end": v(362, -16) * mm});
            skLineSegment(sketch, "E106.14.0.6", {"start": v(362, 16) * mm, "end": v(362, 12) * mm});
            skArc(sketch, "E106.14.0.7", {"start": v(362, 16) * mm, "mid": v(360, 18) * mm, "end": v(358, 16) * mm});
            skCircle(sketch, "E106.14.0.8", {"center": v(360, 0) * mm, "radius": 7 * mm});
            skArc(sketch, "E106.15.0.0", {"start": v(386, -12) * mm, "mid": v(384, -10) * mm, "end": v(382, -12) * mm});
            skArc(sketch, "E106.15.0.1", {"start": v(382, 12) * mm, "mid": v(384, 10) * mm, "end": v(386, 12) * mm});
            skLineSegment(sketch, "E106.15.0.2", {"start": v(382, 16) * mm, "end": v(382, 12) * mm});
            skLineSegment(sketch, "E106.15.0.3", {"start": v(386, -16) * mm, "end": v(386, -12) * mm});
            skLineSegment(sketch, "E106.15.0.4", {"start": v(382, -16) * mm, "end": v(382, -12) * mm});
            skArc(sketch, "E106.15.0.5", {"start": v(382, -16) * mm, "mid": v(384, -18) * mm, "end": v(386, -16) * mm});
            skLineSegment(sketch, "E106.15.0.6", {"start": v(386, 16) * mm, "end": v(386, 12) * mm});
            skArc(sketch, "E106.15.0.7", {"start": v(386, 16) * mm, "mid": v(384, 18) * mm, "end": v(382, 16) * mm});
            skCircle(sketch, "E106.15.0.8", {"center": v(384, 0) * mm, "radius": 7 * mm});
            skArc(sketch, "E106.16.0.0", {"start": v(410, -12) * mm, "mid": v(408, -10) * mm, "end": v(406, -12) * mm});
            skArc(sketch, "E106.16.0.1", {"start": v(406, 12) * mm, "mid": v(408, 10) * mm, "end": v(410, 12) * mm});
            skLineSegment(sketch, "E106.16.0.2", {"start": v(406, 16) * mm, "end": v(406, 12) * mm});
            skLineSegment(sketch, "E106.16.0.3", {"start": v(410, -16) * mm, "end": v(410, -12) * mm});
            skLineSegment(sketch, "E106.16.0.4", {"start": v(406, -16) * mm, "end": v(406, -12) * mm});
            skArc(sketch, "E106.16.0.5", {"start": v(406, -16) * mm, "mid": v(408, -18) * mm, "end": v(410, -16) * mm});
            skLineSegment(sketch, "E106.16.0.6", {"start": v(410, 16) * mm, "end": v(410, 12) * mm});
            skArc(sketch, "E106.16.0.7", {"start": v(410, 16) * mm, "mid": v(408, 18) * mm, "end": v(406, 16) * mm});
            skCircle(sketch, "E106.16.0.8", {"center": v(408, 0) * mm, "radius": 7 * mm});
            skArc(sketch, "E106.17.0.0", {"start": v(434, -12) * mm, "mid": v(432, -10) * mm, "end": v(430, -12) * mm});
            skArc(sketch, "E106.17.0.1", {"start": v(430, 12) * mm, "mid": v(432, 10) * mm, "end": v(434, 12) * mm});
            skLineSegment(sketch, "E106.17.0.2", {"start": v(430, 16) * mm, "end": v(430, 12) * mm});
            skLineSegment(sketch, "E106.17.0.3", {"start": v(434, -16) * mm, "end": v(434, -12) * mm});
            skLineSegment(sketch, "E106.17.0.4", {"start": v(430, -16) * mm, "end": v(430, -12) * mm});
            skArc(sketch, "E106.17.0.5", {"start": v(430, -16) * mm, "mid": v(432, -18) * mm, "end": v(434, -16) * mm});
            skLineSegment(sketch, "E106.17.0.6", {"start": v(434, 16) * mm, "end": v(434, 12) * mm});
            skArc(sketch, "E106.17.0.7", {"start": v(434, 16) * mm, "mid": v(432, 18) * mm, "end": v(430, 16) * mm});
            skCircle(sketch, "E106.17.0.8", {"center": v(432, 0) * mm, "radius": 7 * mm});
            skArc(sketch, "E106.18.0.0", {"start": v(458, -12) * mm, "mid": v(456, -10) * mm, "end": v(454, -12) * mm});
            skArc(sketch, "E106.18.0.1", {"start": v(454, 12) * mm, "mid": v(456, 10) * mm, "end": v(458, 12) * mm});
            skLineSegment(sketch, "E106.18.0.2", {"start": v(454, 16) * mm, "end": v(454, 12) * mm});
            skLineSegment(sketch, "E106.18.0.3", {"start": v(458, -16) * mm, "end": v(458, -12) * mm});
            skLineSegment(sketch, "E106.18.0.4", {"start": v(454, -16) * mm, "end": v(454, -12) * mm});
            skArc(sketch, "E106.18.0.5", {"start": v(454, -16) * mm, "mid": v(456, -18) * mm, "end": v(458, -16) * mm});
            skLineSegment(sketch, "E106.18.0.6", {"start": v(458, 16) * mm, "end": v(458, 12) * mm});
            skArc(sketch, "E106.18.0.7", {"start": v(458, 16) * mm, "mid": v(456, 18) * mm, "end": v(454, 16) * mm});
            skCircle(sketch, "E106.18.0.8", {"center": v(456, 0) * mm, "radius": 7 * mm});
            skArc(sketch, "E106.19.0.0", {"start": v(482, -12) * mm, "mid": v(480, -10) * mm, "end": v(478, -12) * mm});
            skArc(sketch, "E106.19.0.1", {"start": v(478, 12) * mm, "mid": v(480, 10) * mm, "end": v(482, 12) * mm});
            skLineSegment(sketch, "E106.19.0.2", {"start": v(478, 16) * mm, "end": v(478, 12) * mm});
            skLineSegment(sketch, "E106.19.0.3", {"start": v(482, -16) * mm, "end": v(482, -12) * mm});
            skLineSegment(sketch, "E106.19.0.4", {"start": v(478, -16) * mm, "end": v(478, -12) * mm});
            skArc(sketch, "E106.19.0.5", {"start": v(478, -16) * mm, "mid": v(480, -18) * mm, "end": v(482, -16) * mm});
            skLineSegment(sketch, "E106.19.0.6", {"start": v(482, 16) * mm, "end": v(482, 12) * mm});
            skArc(sketch, "E106.19.0.7", {"start": v(482, 16) * mm, "mid": v(480, 18) * mm, "end": v(478, 16) * mm});
            skCircle(sketch, "E106.19.0.8", {"center": v(480, 0) * mm, "radius": 7 * mm});
            skArc(sketch, "E106.20.0.0", {"start": v(506, -12) * mm, "mid": v(504, -10) * mm, "end": v(502, -12) * mm});
            skArc(sketch, "E106.20.0.1", {"start": v(502, 12) * mm, "mid": v(504, 10) * mm, "end": v(506, 12) * mm});
            skLineSegment(sketch, "E106.20.0.2", {"start": v(502, 16) * mm, "end": v(502, 12) * mm});
            skLineSegment(sketch, "E106.20.0.3", {"start": v(506, -16) * mm, "end": v(506, -12) * mm});
            skLineSegment(sketch, "E106.20.0.4", {"start": v(502, -16) * mm, "end": v(502, -12) * mm});
            skArc(sketch, "E106.20.0.5", {"start": v(502, -16) * mm, "mid": v(504, -18) * mm, "end": v(506, -16) * mm});
            skLineSegment(sketch, "E106.20.0.6", {"start": v(506, 16) * mm, "end": v(506, 12) * mm});
            skArc(sketch, "E106.20.0.7", {"start": v(506, 16) * mm, "mid": v(504, 18) * mm, "end": v(502, 16) * mm});
            skCircle(sketch, "E106.20.0.8", {"center": v(504, 0) * mm, "radius": 7 * mm});
            skArc(sketch, "E106.21.0.0", {"start": v(530, -12) * mm, "mid": v(528, -10) * mm, "end": v(526, -12) * mm});
            skArc(sketch, "E106.21.0.1", {"start": v(526, 12) * mm, "mid": v(528, 10) * mm, "end": v(530, 12) * mm});
            skLineSegment(sketch, "E106.21.0.2", {"start": v(526, 16) * mm, "end": v(526, 12) * mm});
            skLineSegment(sketch, "E106.21.0.3", {"start": v(530, -16) * mm, "end": v(530, -12) * mm});
            skLineSegment(sketch, "E106.21.0.4", {"start": v(526, -16) * mm, "end": v(526, -12) * mm});
            skArc(sketch, "E106.21.0.5", {"start": v(526, -16) * mm, "mid": v(528, -18) * mm, "end": v(530, -16) * mm});
            skLineSegment(sketch, "E106.21.0.6", {"start": v(530, 16) * mm, "end": v(530, 12) * mm});
            skArc(sketch, "E106.21.0.7", {"start": v(530, 16) * mm, "mid": v(528, 18) * mm, "end": v(526, 16) * mm});
            skCircle(sketch, "E106.21.0.8", {"center": v(528, 0) * mm, "radius": 7 * mm});
            skArc(sketch, "E106.22.0.0", {"start": v(554, -12) * mm, "mid": v(552, -10) * mm, "end": v(550, -12) * mm});
            skArc(sketch, "E106.22.0.1", {"start": v(550, 12) * mm, "mid": v(552, 10) * mm, "end": v(554, 12) * mm});
            skLineSegment(sketch, "E106.22.0.2", {"start": v(550, 16) * mm, "end": v(550, 12) * mm});
            skLineSegment(sketch, "E106.22.0.3", {"start": v(554, -16) * mm, "end": v(554, -12) * mm});
            skLineSegment(sketch, "E106.22.0.4", {"start": v(550, -16) * mm, "end": v(550, -12) * mm});
            skArc(sketch, "E106.22.0.5", {"start": v(550, -16) * mm, "mid": v(552, -18) * mm, "end": v(554, -16) * mm});
            skLineSegment(sketch, "E106.22.0.6", {"start": v(554, 16) * mm, "end": v(554, 12) * mm});
            skArc(sketch, "E106.22.0.7", {"start": v(554, 16) * mm, "mid": v(552, 18) * mm, "end": v(550, 16) * mm});
            skCircle(sketch, "E106.22.0.8", {"center": v(552, 0) * mm, "radius": 7 * mm});
            skArc(sketch, "E106.23.0.0", {"start": v(578, -12) * mm, "mid": v(576, -10) * mm, "end": v(574, -12) * mm});
            skArc(sketch, "E106.23.0.1", {"start": v(574, 12) * mm, "mid": v(576, 10) * mm, "end": v(578, 12) * mm});
            skLineSegment(sketch, "E106.23.0.2", {"start": v(574, 16) * mm, "end": v(574, 12) * mm});
            skLineSegment(sketch, "E106.23.0.3", {"start": v(578, -16) * mm, "end": v(578, -12) * mm});
            skLineSegment(sketch, "E106.23.0.4", {"start": v(574, -16) * mm, "end": v(574, -12) * mm});
            skArc(sketch, "E106.23.0.5", {"start": v(574, -16) * mm, "mid": v(576, -18) * mm, "end": v(578, -16) * mm});
            skLineSegment(sketch, "E106.23.0.6", {"start": v(578, 16) * mm, "end": v(578, 12) * mm});
            skArc(sketch, "E106.23.0.7", {"start": v(578, 16) * mm, "mid": v(576, 18) * mm, "end": v(574, 16) * mm});
            skCircle(sketch, "E106.23.0.8", {"center": v(576, 0) * mm, "radius": 7 * mm});
            skArc(sketch, "E106.24.0.0", {"start": v(602, -12) * mm, "mid": v(600, -10) * mm, "end": v(598, -12) * mm});
            skArc(sketch, "E106.24.0.1", {"start": v(598, 12) * mm, "mid": v(600, 10) * mm, "end": v(602, 12) * mm});
            skLineSegment(sketch, "E106.24.0.2", {"start": v(598, 16) * mm, "end": v(598, 12) * mm});
            skLineSegment(sketch, "E106.24.0.3", {"start": v(602, -16) * mm, "end": v(602, -12) * mm});
            skLineSegment(sketch, "E106.24.0.4", {"start": v(598, -16) * mm, "end": v(598, -12) * mm});
            skArc(sketch, "E106.24.0.5", {"start": v(598, -16) * mm, "mid": v(600, -18) * mm, "end": v(602, -16) * mm});
            skLineSegment(sketch, "E106.24.0.6", {"start": v(602, 16) * mm, "end": v(602, 12) * mm});
            skArc(sketch, "E106.24.0.7", {"start": v(602, 16) * mm, "mid": v(600, 18) * mm, "end": v(598, 16) * mm});
            skCircle(sketch, "E106.24.0.8", {"center": v(600, 0) * mm, "radius": 7 * mm});
            skArc(sketch, "E106.25.0.0", {"start": v(626, -12) * mm, "mid": v(624, -10) * mm, "end": v(622, -12) * mm});
            skArc(sketch, "E106.25.0.1", {"start": v(622, 12) * mm, "mid": v(624, 10) * mm, "end": v(626, 12) * mm});
            skLineSegment(sketch, "E106.25.0.2", {"start": v(622, 16) * mm, "end": v(622, 12) * mm});
            skLineSegment(sketch, "E106.25.0.3", {"start": v(626, -16) * mm, "end": v(626, -12) * mm});
            skLineSegment(sketch, "E106.25.0.4", {"start": v(622, -16) * mm, "end": v(622, -12) * mm});
            skArc(sketch, "E106.25.0.5", {"start": v(622, -16) * mm, "mid": v(624, -18) * mm, "end": v(626, -16) * mm});
            skLineSegment(sketch, "E106.25.0.6", {"start": v(626, 16) * mm, "end": v(626, 12) * mm});
            skArc(sketch, "E106.25.0.7", {"start": v(626, 16) * mm, "mid": v(624, 18) * mm, "end": v(622, 16) * mm});
            skCircle(sketch, "E106.25.0.8", {"center": v(624, 0) * mm, "radius": 7 * mm});
            skArc(sketch, "E106.26.0.0", {"start": v(650, -12) * mm, "mid": v(648, -10) * mm, "end": v(646, -12) * mm});
            skArc(sketch, "E106.26.0.1", {"start": v(646, 12) * mm, "mid": v(648, 10) * mm, "end": v(650, 12) * mm});
            skLineSegment(sketch, "E106.26.0.2", {"start": v(646, 16) * mm, "end": v(646, 12) * mm});
            skLineSegment(sketch, "E106.26.0.3", {"start": v(650, -16) * mm, "end": v(650, -12) * mm});
            skLineSegment(sketch, "E106.26.0.4", {"start": v(646, -16) * mm, "end": v(646, -12) * mm});
            skArc(sketch, "E106.26.0.5", {"start": v(646, -16) * mm, "mid": v(648, -18) * mm, "end": v(650, -16) * mm});
            skLineSegment(sketch, "E106.26.0.6", {"start": v(650, 16) * mm, "end": v(650, 12) * mm});
            skArc(sketch, "E106.26.0.7", {"start": v(650, 16) * mm, "mid": v(648, 18) * mm, "end": v(646, 16) * mm});
            skCircle(sketch, "E106.26.0.8", {"center": v(648, 0) * mm, "radius": 7 * mm});
            skArc(sketch, "E106.27.0.0", {"start": v(674, -12) * mm, "mid": v(672, -10) * mm, "end": v(670, -12) * mm});
            skArc(sketch, "E106.27.0.1", {"start": v(670, 12) * mm, "mid": v(672, 10) * mm, "end": v(674, 12) * mm});
            skLineSegment(sketch, "E106.27.0.2", {"start": v(670, 16) * mm, "end": v(670, 12) * mm});
            skLineSegment(sketch, "E106.27.0.3", {"start": v(674, -16) * mm, "end": v(674, -12) * mm});
            skLineSegment(sketch, "E106.27.0.4", {"start": v(670, -16) * mm, "end": v(670, -12) * mm});
            skArc(sketch, "E106.27.0.5", {"start": v(670, -16) * mm, "mid": v(672, -18) * mm, "end": v(674, -16) * mm});
            skLineSegment(sketch, "E106.27.0.6", {"start": v(674, 16) * mm, "end": v(674, 12) * mm});
            skArc(sketch, "E106.27.0.7", {"start": v(674, 16) * mm, "mid": v(672, 18) * mm, "end": v(670, 16) * mm});
            skCircle(sketch, "E106.27.0.8", {"center": v(672, 0) * mm, "radius": 7 * mm});
            skArc(sketch, "E106.28.0.0", {"start": v(698, -12) * mm, "mid": v(696, -10) * mm, "end": v(694, -12) * mm});
            skArc(sketch, "E106.28.0.1", {"start": v(694, 12) * mm, "mid": v(696, 10) * mm, "end": v(698, 12) * mm});
            skLineSegment(sketch, "E106.28.0.2", {"start": v(694, 16) * mm, "end": v(694, 12) * mm});
            skLineSegment(sketch, "E106.28.0.3", {"start": v(698, -16) * mm, "end": v(698, -12) * mm});
            skLineSegment(sketch, "E106.28.0.4", {"start": v(694, -16) * mm, "end": v(694, -12) * mm});
            skArc(sketch, "E106.28.0.5", {"start": v(694, -16) * mm, "mid": v(696, -18) * mm, "end": v(698, -16) * mm});
            skLineSegment(sketch, "E106.28.0.6", {"start": v(698, 16) * mm, "end": v(698, 12) * mm});
            skArc(sketch, "E106.28.0.7", {"start": v(698, 16) * mm, "mid": v(696, 18) * mm, "end": v(694, 16) * mm});
            skCircle(sketch, "E106.28.0.8", {"center": v(696, 0) * mm, "radius": 7 * mm});
            skArc(sketch, "E106.29.0.0", {"start": v(722, -12) * mm, "mid": v(720, -10) * mm, "end": v(718, -12) * mm});
            skArc(sketch, "E106.29.0.1", {"start": v(718, 12) * mm, "mid": v(720, 10) * mm, "end": v(722, 12) * mm});
            skLineSegment(sketch, "E106.29.0.2", {"start": v(718, 16) * mm, "end": v(718, 12) * mm});
            skLineSegment(sketch, "E106.29.0.3", {"start": v(722, -16) * mm, "end": v(722, -12) * mm});
            skLineSegment(sketch, "E106.29.0.4", {"start": v(718, -16) * mm, "end": v(718, -12) * mm});
            skArc(sketch, "E106.29.0.5", {"start": v(718, -16) * mm, "mid": v(720, -18) * mm, "end": v(722, -16) * mm});
            skLineSegment(sketch, "E106.29.0.6", {"start": v(722, 16) * mm, "end": v(722, 12) * mm});
            skArc(sketch, "E106.29.0.7", {"start": v(722, 16) * mm, "mid": v(720, 18) * mm, "end": v(718, 16) * mm});
            skCircle(sketch, "E106.29.0.8", {"center": v(720, 0) * mm, "radius": 7 * mm});
            skArc(sketch, "E106.30.0.0", {"start": v(746, -12) * mm, "mid": v(744, -10) * mm, "end": v(742, -12) * mm});
            skArc(sketch, "E106.30.0.1", {"start": v(742, 12) * mm, "mid": v(744, 10) * mm, "end": v(746, 12) * mm});
            skLineSegment(sketch, "E106.30.0.2", {"start": v(742, 16) * mm, "end": v(742, 12) * mm});
            skLineSegment(sketch, "E106.30.0.3", {"start": v(746, -16) * mm, "end": v(746, -12) * mm});
            skLineSegment(sketch, "E106.30.0.4", {"start": v(742, -16) * mm, "end": v(742, -12) * mm});
            skArc(sketch, "E106.30.0.5", {"start": v(742, -16) * mm, "mid": v(744, -18) * mm, "end": v(746, -16) * mm});
            skLineSegment(sketch, "E106.30.0.6", {"start": v(746, 16) * mm, "end": v(746, 12) * mm});
            skArc(sketch, "E106.30.0.7", {"start": v(746, 16) * mm, "mid": v(744, 18) * mm, "end": v(742, 16) * mm});
            skCircle(sketch, "E106.30.0.8", {"center": v(744, 0) * mm, "radius": 7 * mm});
            skArc(sketch, "E106.31.0.0", {"start": v(770, -12) * mm, "mid": v(768, -10) * mm, "end": v(766, -12) * mm});
            skArc(sketch, "E106.31.0.1", {"start": v(766, 12) * mm, "mid": v(768, 10) * mm, "end": v(770, 12) * mm});
            skLineSegment(sketch, "E106.31.0.2", {"start": v(766, 16) * mm, "end": v(766, 12) * mm});
            skLineSegment(sketch, "E106.31.0.3", {"start": v(770, -16) * mm, "end": v(770, -12) * mm});
            skLineSegment(sketch, "E106.31.0.4", {"start": v(766, -16) * mm, "end": v(766, -12) * mm});
            skArc(sketch, "E106.31.0.5", {"start": v(766, -16) * mm, "mid": v(768, -18) * mm, "end": v(770, -16) * mm});
            skLineSegment(sketch, "E106.31.0.6", {"start": v(770, 16) * mm, "end": v(770, 12) * mm});
            skArc(sketch, "E106.31.0.7", {"start": v(770, 16) * mm, "mid": v(768, 18) * mm, "end": v(766, 16) * mm});
            skCircle(sketch, "E106.31.0.8", {"center": v(768, 0) * mm, "radius": 7 * mm});
            skArc(sketch, "E106.32.0.0", {"start": v(794, -12) * mm, "mid": v(792, -10) * mm, "end": v(790, -12) * mm});
            skArc(sketch, "E106.32.0.1", {"start": v(790, 12) * mm, "mid": v(792, 10) * mm, "end": v(794, 12) * mm});
            skLineSegment(sketch, "E106.32.0.2", {"start": v(790, 16) * mm, "end": v(790, 12) * mm});
            skLineSegment(sketch, "E106.32.0.3", {"start": v(794, -16) * mm, "end": v(794, -12) * mm});
            skLineSegment(sketch, "E106.32.0.4", {"start": v(790, -16) * mm, "end": v(790, -12) * mm});
            skArc(sketch, "E106.32.0.5", {"start": v(790, -16) * mm, "mid": v(792, -18) * mm, "end": v(794, -16) * mm});
            skLineSegment(sketch, "E106.32.0.6", {"start": v(794, 16) * mm, "end": v(794, 12) * mm});
            skArc(sketch, "E106.32.0.7", {"start": v(794, 16) * mm, "mid": v(792, 18) * mm, "end": v(790, 16) * mm});
            skCircle(sketch, "E106.32.0.8", {"center": v(792, 0) * mm, "radius": 7 * mm});
            skArc(sketch, "E106.33.0.0", {"start": v(818, -12) * mm, "mid": v(816, -10) * mm, "end": v(814, -12) * mm});
            skArc(sketch, "E106.33.0.1", {"start": v(814, 12) * mm, "mid": v(816, 10) * mm, "end": v(818, 12) * mm});
            skLineSegment(sketch, "E106.33.0.2", {"start": v(814, 16) * mm, "end": v(814, 12) * mm});
            skLineSegment(sketch, "E106.33.0.3", {"start": v(818, -16) * mm, "end": v(818, -12) * mm});
            skLineSegment(sketch, "E106.33.0.4", {"start": v(814, -16) * mm, "end": v(814, -12) * mm});
            skArc(sketch, "E106.33.0.5", {"start": v(814, -16) * mm, "mid": v(816, -18) * mm, "end": v(818, -16) * mm});
            skLineSegment(sketch, "E106.33.0.6", {"start": v(818, 16) * mm, "end": v(818, 12) * mm});
            skArc(sketch, "E106.33.0.7", {"start": v(818, 16) * mm, "mid": v(816, 18) * mm, "end": v(814, 16) * mm});
            skCircle(sketch, "E106.33.0.8", {"center": v(816, 0) * mm, "radius": 7 * mm});
            skArc(sketch, "E106.34.0.0", {"start": v(842, -12) * mm, "mid": v(840, -10) * mm, "end": v(838, -12) * mm});
            skArc(sketch, "E106.34.0.1", {"start": v(838, 12) * mm, "mid": v(840, 10) * mm, "end": v(842, 12) * mm});
            skLineSegment(sketch, "E106.34.0.2", {"start": v(838, 16) * mm, "end": v(838, 12) * mm});
            skLineSegment(sketch, "E106.34.0.3", {"start": v(842, -16) * mm, "end": v(842, -12) * mm});
            skLineSegment(sketch, "E106.34.0.4", {"start": v(838, -16) * mm, "end": v(838, -12) * mm});
            skArc(sketch, "E106.34.0.5", {"start": v(838, -16) * mm, "mid": v(840, -18) * mm, "end": v(842, -16) * mm});
            skLineSegment(sketch, "E106.34.0.6", {"start": v(842, 16) * mm, "end": v(842, 12) * mm});
            skArc(sketch, "E106.34.0.7", {"start": v(842, 16) * mm, "mid": v(840, 18) * mm, "end": v(838, 16) * mm});
            skCircle(sketch, "E106.34.0.8", {"center": v(840, 0) * mm, "radius": 7 * mm});
            skArc(sketch, "E106.35.0.0", {"start": v(866, -12) * mm, "mid": v(864, -10) * mm, "end": v(862, -12) * mm});
            skArc(sketch, "E106.35.0.1", {"start": v(862, 12) * mm, "mid": v(864, 10) * mm, "end": v(866, 12) * mm});
            skLineSegment(sketch, "E106.35.0.2", {"start": v(862, 16) * mm, "end": v(862, 12) * mm});
            skLineSegment(sketch, "E106.35.0.3", {"start": v(866, -16) * mm, "end": v(866, -12) * mm});
            skLineSegment(sketch, "E106.35.0.4", {"start": v(862, -16) * mm, "end": v(862, -12) * mm});
            skArc(sketch, "E106.35.0.5", {"start": v(862, -16) * mm, "mid": v(864, -18) * mm, "end": v(866, -16) * mm});
            skLineSegment(sketch, "E106.35.0.6", {"start": v(866, 16) * mm, "end": v(866, 12) * mm});
            skArc(sketch, "E106.35.0.7", {"start": v(866, 16) * mm, "mid": v(864, 18) * mm, "end": v(862, 16) * mm});
            skCircle(sketch, "E106.35.0.8", {"center": v(864, 0) * mm, "radius": 7 * mm});
            skArc(sketch, "E106.36.0.0", {"start": v(890, -12) * mm, "mid": v(888, -10) * mm, "end": v(886, -12) * mm});
            skArc(sketch, "E106.36.0.1", {"start": v(886, 12) * mm, "mid": v(888, 10) * mm, "end": v(890, 12) * mm});
            skLineSegment(sketch, "E106.36.0.2", {"start": v(886, 16) * mm, "end": v(886, 12) * mm});
            skLineSegment(sketch, "E106.36.0.3", {"start": v(890, -16) * mm, "end": v(890, -12) * mm});
            skLineSegment(sketch, "E106.36.0.4", {"start": v(886, -16) * mm, "end": v(886, -12) * mm});
            skArc(sketch, "E106.36.0.5", {"start": v(886, -16) * mm, "mid": v(888, -18) * mm, "end": v(890, -16) * mm});
            skLineSegment(sketch, "E106.36.0.6", {"start": v(890, 16) * mm, "end": v(890, 12) * mm});
            skArc(sketch, "E106.36.0.7", {"start": v(890, 16) * mm, "mid": v(888, 18) * mm, "end": v(886, 16) * mm});
            skCircle(sketch, "E106.36.0.8", {"center": v(888, 0) * mm, "radius": 7 * mm});
            skArc(sketch, "E106.37.0.0", {"start": v(914, -12) * mm, "mid": v(912, -10) * mm, "end": v(910, -12) * mm});
            skArc(sketch, "E106.37.0.1", {"start": v(910, 12) * mm, "mid": v(912, 10) * mm, "end": v(914, 12) * mm});
            skLineSegment(sketch, "E106.37.0.2", {"start": v(910, 16) * mm, "end": v(910, 12) * mm});
            skLineSegment(sketch, "E106.37.0.3", {"start": v(914, -16) * mm, "end": v(914, -12) * mm});
            skLineSegment(sketch, "E106.37.0.4", {"start": v(910, -16) * mm, "end": v(910, -12) * mm});
            skArc(sketch, "E106.37.0.5", {"start": v(910, -16) * mm, "mid": v(912, -18) * mm, "end": v(914, -16) * mm});
            skLineSegment(sketch, "E106.37.0.6", {"start": v(914, 16) * mm, "end": v(914, 12) * mm});
            skArc(sketch, "E106.37.0.7", {"start": v(914, 16) * mm, "mid": v(912, 18) * mm, "end": v(910, 16) * mm});
            skCircle(sketch, "E106.37.0.8", {"center": v(912, 0) * mm, "radius": 7 * mm});
            skArc(sketch, "E106.38.0.0", {"start": v(938, -12) * mm, "mid": v(936, -10) * mm, "end": v(934, -12) * mm});
            skArc(sketch, "E106.38.0.1", {"start": v(934, 12) * mm, "mid": v(936, 10) * mm, "end": v(938, 12) * mm});
            skLineSegment(sketch, "E106.38.0.2", {"start": v(934, 16) * mm, "end": v(934, 12) * mm});
            skLineSegment(sketch, "E106.38.0.3", {"start": v(938, -16) * mm, "end": v(938, -12) * mm});
            skLineSegment(sketch, "E106.38.0.4", {"start": v(934, -16) * mm, "end": v(934, -12) * mm});
            skArc(sketch, "E106.38.0.5", {"start": v(934, -16) * mm, "mid": v(936, -18) * mm, "end": v(938, -16) * mm});
            skLineSegment(sketch, "E106.38.0.6", {"start": v(938, 16) * mm, "end": v(938, 12) * mm});
            skArc(sketch, "E106.38.0.7", {"start": v(938, 16) * mm, "mid": v(936, 18) * mm, "end": v(934, 16) * mm});
            skCircle(sketch, "E106.38.0.8", {"center": v(936, 0) * mm, "radius": 7 * mm});
            skArc(sketch, "E106.39.0.0", {"start": v(962, -12) * mm, "mid": v(960, -10) * mm, "end": v(958, -12) * mm});
            skArc(sketch, "E106.39.0.1", {"start": v(958, 12) * mm, "mid": v(960, 10) * mm, "end": v(962, 12) * mm});
            skLineSegment(sketch, "E106.39.0.2", {"start": v(958, 16) * mm, "end": v(958, 12) * mm});
            skLineSegment(sketch, "E106.39.0.3", {"start": v(962, -16) * mm, "end": v(962, -12) * mm});
            skLineSegment(sketch, "E106.39.0.4", {"start": v(958, -16) * mm, "end": v(958, -12) * mm});
            skArc(sketch, "E106.39.0.5", {"start": v(958, -16) * mm, "mid": v(960, -18) * mm, "end": v(962, -16) * mm});
            skLineSegment(sketch, "E106.39.0.6", {"start": v(962, 16) * mm, "end": v(962, 12) * mm});
            skArc(sketch, "E106.39.0.7", {"start": v(962, 16) * mm, "mid": v(960, 18) * mm, "end": v(958, 16) * mm});
            skCircle(sketch, "E106.39.0.8", {"center": v(960, 0) * mm, "radius": 7 * mm});
            skArc(sketch, "E106.40.0.0", {"start": v(986, -12) * mm, "mid": v(984, -10) * mm, "end": v(982, -12) * mm});
            skArc(sketch, "E106.40.0.1", {"start": v(982, 12) * mm, "mid": v(984, 10) * mm, "end": v(986, 12) * mm});
            skLineSegment(sketch, "E106.40.0.2", {"start": v(982, 16) * mm, "end": v(982, 12) * mm});
            skLineSegment(sketch, "E106.40.0.3", {"start": v(986, -16) * mm, "end": v(986, -12) * mm});
            skLineSegment(sketch, "E106.40.0.4", {"start": v(982, -16) * mm, "end": v(982, -12) * mm});
            skArc(sketch, "E106.40.0.5", {"start": v(982, -16) * mm, "mid": v(984, -18) * mm, "end": v(986, -16) * mm});
            skLineSegment(sketch, "E106.40.0.6", {"start": v(986, 16) * mm, "end": v(986, 12) * mm});
            skArc(sketch, "E106.40.0.7", {"start": v(986, 16) * mm, "mid": v(984, 18) * mm, "end": v(982, 16) * mm});
            skCircle(sketch, "E106.40.0.8", {"center": v(984, 0) * mm, "radius": 7 * mm});
            skArc(sketch, "E106.41.0.0", {"start": v(1010, -12) * mm, "mid": v(1008, -10) * mm, "end": v(1006, -12) * mm});
            skArc(sketch, "E106.41.0.1", {"start": v(1006, 12) * mm, "mid": v(1008, 10) * mm, "end": v(1010, 12) * mm});
            skLineSegment(sketch, "E106.41.0.2", {"start": v(1006, 16) * mm, "end": v(1006, 12) * mm});
            skLineSegment(sketch, "E106.41.0.3", {"start": v(1010, -16) * mm, "end": v(1010, -12) * mm});
            skLineSegment(sketch, "E106.41.0.4", {"start": v(1006, -16) * mm, "end": v(1006, -12) * mm});
            skArc(sketch, "E106.41.0.5", {"start": v(1006, -16) * mm, "mid": v(1008, -18) * mm, "end": v(1010, -16) * mm});
            skLineSegment(sketch, "E106.41.0.6", {"start": v(1010, 16) * mm, "end": v(1010, 12) * mm});
            skArc(sketch, "E106.41.0.7", {"start": v(1010, 16) * mm, "mid": v(1008, 18) * mm, "end": v(1006, 16) * mm});
            skCircle(sketch, "E106.41.0.8", {"center": v(1008, 0) * mm, "radius": 7 * mm});
            skArc(sketch, "E106.42.0.0", {"start": v(1034, -12) * mm, "mid": v(1032, -10) * mm, "end": v(1030, -12) * mm});
            skArc(sketch, "E106.42.0.1", {"start": v(1030, 12) * mm, "mid": v(1032, 10) * mm, "end": v(1034, 12) * mm});
            skLineSegment(sketch, "E106.42.0.2", {"start": v(1030, 16) * mm, "end": v(1030, 12) * mm});
            skLineSegment(sketch, "E106.42.0.3", {"start": v(1034, -16) * mm, "end": v(1034, -12) * mm});
            skLineSegment(sketch, "E106.42.0.4", {"start": v(1030, -16) * mm, "end": v(1030, -12) * mm});
            skArc(sketch, "E106.42.0.5", {"start": v(1030, -16) * mm, "mid": v(1032, -18) * mm, "end": v(1034, -16) * mm});
            skLineSegment(sketch, "E106.42.0.6", {"start": v(1034, 16) * mm, "end": v(1034, 12) * mm});
            skArc(sketch, "E106.42.0.7", {"start": v(1034, 16) * mm, "mid": v(1032, 18) * mm, "end": v(1030, 16) * mm});
            skCircle(sketch, "E106.42.0.8", {"center": v(1032, 0) * mm, "radius": 7 * mm});
            skArc(sketch, "E106.43.0.0", {"start": v(1058, -12) * mm, "mid": v(1056, -10) * mm, "end": v(1054, -12) * mm});
            skArc(sketch, "E106.43.0.1", {"start": v(1054, 12) * mm, "mid": v(1056, 10) * mm, "end": v(1058, 12) * mm});
            skLineSegment(sketch, "E106.43.0.2", {"start": v(1054, 16) * mm, "end": v(1054, 12) * mm});
            skLineSegment(sketch, "E106.43.0.3", {"start": v(1058, -16) * mm, "end": v(1058, -12) * mm});
            skLineSegment(sketch, "E106.43.0.4", {"start": v(1054, -16) * mm, "end": v(1054, -12) * mm});
            skArc(sketch, "E106.43.0.5", {"start": v(1054, -16) * mm, "mid": v(1056, -18) * mm, "end": v(1058, -16) * mm});
            skLineSegment(sketch, "E106.43.0.6", {"start": v(1058, 16) * mm, "end": v(1058, 12) * mm});
            skArc(sketch, "E106.43.0.7", {"start": v(1058, 16) * mm, "mid": v(1056, 18) * mm, "end": v(1054, 16) * mm});
            skCircle(sketch, "E106.43.0.8", {"center": v(1056, 0) * mm, "radius": 7 * mm});
            skArc(sketch, "E106.44.0.0", {"start": v(1082, -12) * mm, "mid": v(1080, -10) * mm, "end": v(1078, -12) * mm});
            skArc(sketch, "E106.44.0.1", {"start": v(1078, 12) * mm, "mid": v(1080, 10) * mm, "end": v(1082, 12) * mm});
            skLineSegment(sketch, "E106.44.0.2", {"start": v(1078, 16) * mm, "end": v(1078, 12) * mm});
            skLineSegment(sketch, "E106.44.0.3", {"start": v(1082, -16) * mm, "end": v(1082, -12) * mm});
            skLineSegment(sketch, "E106.44.0.4", {"start": v(1078, -16) * mm, "end": v(1078, -12) * mm});
            skArc(sketch, "E106.44.0.5", {"start": v(1078, -16) * mm, "mid": v(1080, -18) * mm, "end": v(1082, -16) * mm});
            skLineSegment(sketch, "E106.44.0.6", {"start": v(1082, 16) * mm, "end": v(1082, 12) * mm});
            skArc(sketch, "E106.44.0.7", {"start": v(1082, 16) * mm, "mid": v(1080, 18) * mm, "end": v(1078, 16) * mm});
            skCircle(sketch, "E106.44.0.8", {"center": v(1080, 0) * mm, "radius": 7 * mm});
            skArc(sketch, "E106.45.0.0", {"start": v(1106, -12) * mm, "mid": v(1104, -10) * mm, "end": v(1102, -12) * mm});
            skArc(sketch, "E106.45.0.1", {"start": v(1102, 12) * mm, "mid": v(1104, 10) * mm, "end": v(1106, 12) * mm});
            skLineSegment(sketch, "E106.45.0.2", {"start": v(1102, 16) * mm, "end": v(1102, 12) * mm});
            skLineSegment(sketch, "E106.45.0.3", {"start": v(1106, -16) * mm, "end": v(1106, -12) * mm});
            skLineSegment(sketch, "E106.45.0.4", {"start": v(1102, -16) * mm, "end": v(1102, -12) * mm});
            skArc(sketch, "E106.45.0.5", {"start": v(1102, -16) * mm, "mid": v(1104, -18) * mm, "end": v(1106, -16) * mm});
            skLineSegment(sketch, "E106.45.0.6", {"start": v(1106, 16) * mm, "end": v(1106, 12) * mm});
            skArc(sketch, "E106.45.0.7", {"start": v(1106, 16) * mm, "mid": v(1104, 18) * mm, "end": v(1102, 16) * mm});
            skCircle(sketch, "E106.45.0.8", {"center": v(1104, 0) * mm, "radius": 7 * mm});
            skArc(sketch, "E106.46.0.0", {"start": v(1130, -12) * mm, "mid": v(1128, -10) * mm, "end": v(1126, -12) * mm});
            skArc(sketch, "E106.46.0.1", {"start": v(1126, 12) * mm, "mid": v(1128, 10) * mm, "end": v(1130, 12) * mm});
            skLineSegment(sketch, "E106.46.0.2", {"start": v(1126, 16) * mm, "end": v(1126, 12) * mm});
            skLineSegment(sketch, "E106.46.0.3", {"start": v(1130, -16) * mm, "end": v(1130, -12) * mm});
            skLineSegment(sketch, "E106.46.0.4", {"start": v(1126, -16) * mm, "end": v(1126, -12) * mm});
            skArc(sketch, "E106.46.0.5", {"start": v(1126, -16) * mm, "mid": v(1128, -18) * mm, "end": v(1130, -16) * mm});
            skLineSegment(sketch, "E106.46.0.6", {"start": v(1130, 16) * mm, "end": v(1130, 12) * mm});
            skArc(sketch, "E106.46.0.7", {"start": v(1130, 16) * mm, "mid": v(1128, 18) * mm, "end": v(1126, 16) * mm});
            skCircle(sketch, "E106.46.0.8", {"center": v(1128, 0) * mm, "radius": 7 * mm});
            skArc(sketch, "E106.47.0.0", {"start": v(1154, -12) * mm, "mid": v(1152, -10) * mm, "end": v(1150, -12) * mm});
            skArc(sketch, "E106.47.0.1", {"start": v(1150, 12) * mm, "mid": v(1152, 10) * mm, "end": v(1154, 12) * mm});
            skLineSegment(sketch, "E106.47.0.2", {"start": v(1150, 16) * mm, "end": v(1150, 12) * mm});
            skLineSegment(sketch, "E106.47.0.3", {"start": v(1154, -16) * mm, "end": v(1154, -12) * mm});
            skLineSegment(sketch, "E106.47.0.4", {"start": v(1150, -16) * mm, "end": v(1150, -12) * mm});
            skArc(sketch, "E106.47.0.5", {"start": v(1150, -16) * mm, "mid": v(1152, -18) * mm, "end": v(1154, -16) * mm});
            skLineSegment(sketch, "E106.47.0.6", {"start": v(1154, 16) * mm, "end": v(1154, 12) * mm});
            skArc(sketch, "E106.47.0.7", {"start": v(1154, 16) * mm, "mid": v(1152, 18) * mm, "end": v(1150, 16) * mm});
            skCircle(sketch, "E106.47.0.8", {"center": v(1152, 0) * mm, "radius": 7 * mm});
            skArc(sketch, "E106.48.0.0", {"start": v(1178, -12) * mm, "mid": v(1176, -10) * mm, "end": v(1174, -12) * mm});
            skArc(sketch, "E106.48.0.1", {"start": v(1174, 12) * mm, "mid": v(1176, 10) * mm, "end": v(1178, 12) * mm});
            skLineSegment(sketch, "E106.48.0.2", {"start": v(1174, 16) * mm, "end": v(1174, 12) * mm});
            skLineSegment(sketch, "E106.48.0.3", {"start": v(1178, -16) * mm, "end": v(1178, -12) * mm});
            skLineSegment(sketch, "E106.48.0.4", {"start": v(1174, -16) * mm, "end": v(1174, -12) * mm});
            skArc(sketch, "E106.48.0.5", {"start": v(1174, -16) * mm, "mid": v(1176, -18) * mm, "end": v(1178, -16) * mm});
            skLineSegment(sketch, "E106.48.0.6", {"start": v(1178, 16) * mm, "end": v(1178, 12) * mm});
            skArc(sketch, "E106.48.0.7", {"start": v(1178, 16) * mm, "mid": v(1176, 18) * mm, "end": v(1174, 16) * mm});
            skCircle(sketch, "E106.48.0.8", {"center": v(1176, 0) * mm, "radius": 7 * mm});
            skLineSegment(sketch, "E106.direction1", {"start": v(22, -16) * mm, "end": v(46, -16) * mm, "construction": true});
            skSolve(sketch);
        }
        {
            var Q0;
            Q0=makeQuery(id+"F42.imprint","IMPRINT",FACE,{"disambiguationData":[TD([[makeQuery(id+"F42.imprint","IMPRINT",EDGE,{"derivedFrom":sQuery(id+"F42.wireOp",EDGE,"E97")}),1.0]])]});
            var Q1;
            Q1=makeQuery(id+"F42.imprint","IMPRINT",FACE,{"disambiguationData":[TD([[makeQuery(id+"F42.imprint","IMPRINT",EDGE,{"derivedFrom":sQuery(id+"F42.wireOp",EDGE,"E98")}),1.0]])]});
            var Q2;
            Q2=makeQuery(id+"F42.imprint","IMPRINT",FACE,{"disambiguationData":[TD([[makeQuery(id+"F42.imprint","IMPRINT",EDGE,{"derivedFrom":sQuery(id+"F42.wireOp",EDGE,"E99")}),1.0]])]});
            extrude(context, id + "F43", {"entities" : qUnion([Q0, Q1, Q2]), "operationType" : NewBodyOperationType.REMOVE, "oppositeDirection" : true, "depth" : 25 * mm, "offsetDistance" : 25 * mm});
        }
        {
            var Q0;
            Q0=makeQuery(id+"F42.imprint","IMPRINT",FACE,{"disambiguationData":[TD([[makeQuery(id+"F42.imprint","IMPRINT",EDGE,{"derivedFrom":sQuery(id+"F42.wireOp",EDGE,"E106.1.0.8")}),1.0]])]});
            var Q1;
            Q1=makeQuery(id+"F42.imprint","IMPRINT",FACE,{"disambiguationData":[TD([[makeQuery(id+"F42.imprint","IMPRINT",EDGE,{"derivedFrom":sQuery(id+"F42.wireOp",EDGE,"E106.1.0.1")}),1.0]])]});
            var Q2;
            Q2=makeQuery(id+"F42.imprint","IMPRINT",FACE,{"disambiguationData":[TD([[makeQuery(id+"F42.imprint","IMPRINT",EDGE,{"derivedFrom":sQuery(id+"F42.wireOp",EDGE,"E106.1.0.0")}),1.0]])]});
            extrude(context, id + "F44", {"entities" : qUnion([Q0, Q1, Q2]), "operationType" : NewBodyOperationType.REMOVE, "oppositeDirection" : true, "depth" : 25 * mm, "offsetDistance" : 25 * mm});
        }
        {
            var Q0;
            Q0=makeQuery(id+"F42.imprint","IMPRINT",FACE,{"disambiguationData":[TD([[makeQuery(id+"F42.imprint","IMPRINT",EDGE,{"derivedFrom":sQuery(id+"F42.wireOp",EDGE,"E106.2.0.1")}),1.0]])]});
            var Q1;
            Q1=makeQuery(id+"F42.imprint","IMPRINT",FACE,{"disambiguationData":[TD([[makeQuery(id+"F42.imprint","IMPRINT",EDGE,{"derivedFrom":sQuery(id+"F42.wireOp",EDGE,"E106.2.0.8")}),1.0]])]});
            var Q2;
            Q2=makeQuery(id+"F42.imprint","IMPRINT",FACE,{"disambiguationData":[TD([[makeQuery(id+"F42.imprint","IMPRINT",EDGE,{"derivedFrom":sQuery(id+"F42.wireOp",EDGE,"E106.2.0.0")}),1.0]])]});
            extrude(context, id + "F45", {"entities" : qUnion([Q0, Q1, Q2]), "operationType" : NewBodyOperationType.REMOVE, "oppositeDirection" : true, "depth" : 25 * mm, "offsetDistance" : 25 * mm});
        }
        {
            var Q0;
            Q0=makeQuery(id+"F42.imprint","IMPRINT",FACE,{"disambiguationData":[TD([[makeQuery(id+"F42.imprint","IMPRINT",EDGE,{"derivedFrom":sQuery(id+"F42.wireOp",EDGE,"E106.3.0.8")}),1.0]])]});
            var Q1;
            Q1=makeQuery(id+"F42.imprint","IMPRINT",FACE,{"disambiguationData":[TD([[makeQuery(id+"F42.imprint","IMPRINT",EDGE,{"derivedFrom":sQuery(id+"F42.wireOp",EDGE,"E106.3.0.1")}),1.0]])]});
            var Q2;
            Q2=makeQuery(id+"F42.imprint","IMPRINT",FACE,{"disambiguationData":[TD([[makeQuery(id+"F42.imprint","IMPRINT",EDGE,{"derivedFrom":sQuery(id+"F42.wireOp",EDGE,"E106.3.0.0")}),1.0]])]});
            extrude(context, id + "F46", {"entities" : qUnion([Q0, Q1, Q2]), "operationType" : NewBodyOperationType.REMOVE, "oppositeDirection" : true, "depth" : 25 * mm, "offsetDistance" : 25 * mm});
        }
        {
            var Q0;
            Q0=makeQuery(id+"F42.imprint","IMPRINT",FACE,{"disambiguationData":[TD([[makeQuery(id+"F42.imprint","IMPRINT",EDGE,{"derivedFrom":sQuery(id+"F42.wireOp",EDGE,"E106.4.0.8")}),1.0]])]});
            var Q1;
            Q1=makeQuery(id+"F42.imprint","IMPRINT",FACE,{"disambiguationData":[TD([[makeQuery(id+"F42.imprint","IMPRINT",EDGE,{"derivedFrom":sQuery(id+"F42.wireOp",EDGE,"E106.4.0.1")}),1.0]])]});
            var Q2;
            Q2=makeQuery(id+"F42.imprint","IMPRINT",FACE,{"disambiguationData":[TD([[makeQuery(id+"F42.imprint","IMPRINT",EDGE,{"derivedFrom":sQuery(id+"F42.wireOp",EDGE,"E106.4.0.0")}),1.0]])]});
            extrude(context, id + "F47", {"entities" : qUnion([Q0, Q1, Q2]), "operationType" : NewBodyOperationType.REMOVE, "oppositeDirection" : true, "depth" : 25 * mm, "offsetDistance" : 25 * mm});
        }
        {
            var Q0;
            Q0=makeQuery(id+"F42.imprint","IMPRINT",FACE,{"disambiguationData":[TD([[makeQuery(id+"F42.imprint","IMPRINT",EDGE,{"derivedFrom":sQuery(id+"F42.wireOp",EDGE,"E106.5.0.8")}),1.0]])]});
            var Q1;
            Q1=makeQuery(id+"F42.imprint","IMPRINT",FACE,{"disambiguationData":[TD([[makeQuery(id+"F42.imprint","IMPRINT",EDGE,{"derivedFrom":sQuery(id+"F42.wireOp",EDGE,"E106.5.0.1")}),1.0]])]});
            var Q2;
            Q2=makeQuery(id+"F42.imprint","IMPRINT",FACE,{"disambiguationData":[TD([[makeQuery(id+"F42.imprint","IMPRINT",EDGE,{"derivedFrom":sQuery(id+"F42.wireOp",EDGE,"E106.6.0.1")}),1.0]])]});
            var Q3;
            Q3=makeQuery(id+"F42.imprint","IMPRINT",FACE,{"disambiguationData":[TD([[makeQuery(id+"F42.imprint","IMPRINT",EDGE,{"derivedFrom":sQuery(id+"F42.wireOp",EDGE,"E106.6.0.0")}),1.0]])]});
            var Q4;
            Q4=makeQuery(id+"F42.imprint","IMPRINT",FACE,{"disambiguationData":[TD([[makeQuery(id+"F42.imprint","IMPRINT",EDGE,{"derivedFrom":sQuery(id+"F42.wireOp",EDGE,"E106.5.0.0")}),1.0]])]});
            var Q5;
            Q5=makeQuery(id+"F42.imprint","IMPRINT",FACE,{"disambiguationData":[TD([[makeQuery(id+"F42.imprint","IMPRINT",EDGE,{"derivedFrom":sQuery(id+"F42.wireOp",EDGE,"E106.6.0.8")}),1.0]])]});
            extrude(context, id + "F48", {"entities" : qUnion([Q0, Q1, Q2, Q3, Q4, Q5]), "operationType" : NewBodyOperationType.REMOVE, "oppositeDirection" : true, "depth" : 25 * mm, "offsetDistance" : 25 * mm});
        }
        {
            var Q0;
            Q0=makeQuery(id+"F42.imprint","IMPRINT",FACE,{"disambiguationData":[TD([[makeQuery(id+"F42.imprint","IMPRINT",EDGE,{"derivedFrom":sQuery(id+"F42.wireOp",EDGE,"E106.7.0.8")}),1.0]])]});
            var Q1;
            Q1=makeQuery(id+"F42.imprint","IMPRINT",FACE,{"disambiguationData":[TD([[makeQuery(id+"F42.imprint","IMPRINT",EDGE,{"derivedFrom":sQuery(id+"F42.wireOp",EDGE,"E106.7.0.1")}),1.0]])]});
            var Q2;
            Q2=makeQuery(id+"F42.imprint","IMPRINT",FACE,{"disambiguationData":[TD([[makeQuery(id+"F42.imprint","IMPRINT",EDGE,{"derivedFrom":sQuery(id+"F42.wireOp",EDGE,"E106.8.0.1")}),1.0]])]});
            var Q3;
            Q3=makeQuery(id+"F42.imprint","IMPRINT",FACE,{"disambiguationData":[TD([[makeQuery(id+"F42.imprint","IMPRINT",EDGE,{"derivedFrom":sQuery(id+"F42.wireOp",EDGE,"E106.8.0.8")}),1.0]])]});
            var Q4;
            Q4=makeQuery(id+"F42.imprint","IMPRINT",FACE,{"disambiguationData":[TD([[makeQuery(id+"F42.imprint","IMPRINT",EDGE,{"derivedFrom":sQuery(id+"F42.wireOp",EDGE,"E106.8.0.0")}),1.0]])]});
            var Q5;
            Q5=makeQuery(id+"F42.imprint","IMPRINT",FACE,{"disambiguationData":[TD([[makeQuery(id+"F42.imprint","IMPRINT",EDGE,{"derivedFrom":sQuery(id+"F42.wireOp",EDGE,"E106.7.0.0")}),1.0]])]});
            extrude(context, id + "F49", {"entities" : qUnion([Q0, Q1, Q2, Q3, Q4, Q5]), "operationType" : NewBodyOperationType.REMOVE, "oppositeDirection" : true, "depth" : 25 * mm, "offsetDistance" : 25 * mm});
        }
        {
            var Q0;
            Q0=makeQuery(id+"F42.imprint","IMPRINT",FACE,{"disambiguationData":[TD([[makeQuery(id+"F42.imprint","IMPRINT",EDGE,{"derivedFrom":sQuery(id+"F42.wireOp",EDGE,"E106.9.0.1")}),1.0]])]});
            var Q1;
            Q1=makeQuery(id+"F42.imprint","IMPRINT",FACE,{"disambiguationData":[TD([[makeQuery(id+"F42.imprint","IMPRINT",EDGE,{"derivedFrom":sQuery(id+"F42.wireOp",EDGE,"E106.9.0.8")}),1.0]])]});
            var Q2;
            Q2=makeQuery(id+"F42.imprint","IMPRINT",FACE,{"disambiguationData":[TD([[makeQuery(id+"F42.imprint","IMPRINT",EDGE,{"derivedFrom":sQuery(id+"F42.wireOp",EDGE,"E106.9.0.0")}),1.0]])]});
            var Q3;
            Q3=makeQuery(id+"F42.imprint","IMPRINT",FACE,{"disambiguationData":[TD([[makeQuery(id+"F42.imprint","IMPRINT",EDGE,{"derivedFrom":sQuery(id+"F42.wireOp",EDGE,"E106.10.0.0")}),1.0]])]});
            var Q4;
            Q4=makeQuery(id+"F42.imprint","IMPRINT",FACE,{"disambiguationData":[TD([[makeQuery(id+"F42.imprint","IMPRINT",EDGE,{"derivedFrom":sQuery(id+"F42.wireOp",EDGE,"E106.10.0.8")}),1.0]])]});
            var Q5;
            Q5=makeQuery(id+"F42.imprint","IMPRINT",FACE,{"disambiguationData":[TD([[makeQuery(id+"F42.imprint","IMPRINT",EDGE,{"derivedFrom":sQuery(id+"F42.wireOp",EDGE,"E106.10.0.1")}),1.0]])]});
            extrude(context, id + "F50", {"entities" : qUnion([Q0, Q1, Q2, Q3, Q4, Q5]), "operationType" : NewBodyOperationType.REMOVE, "oppositeDirection" : true, "depth" : 25 * mm, "offsetDistance" : 25 * mm});
        }
        {
            var Q0;
            Q0=makeQuery(id+"F42.imprint","IMPRINT",FACE,{"disambiguationData":[TD([[makeQuery(id+"F42.imprint","IMPRINT",EDGE,{"derivedFrom":sQuery(id+"F42.wireOp",EDGE,"E106.11.0.8")}),1.0]])]});
            var Q1;
            Q1=makeQuery(id+"F42.imprint","IMPRINT",FACE,{"disambiguationData":[TD([[makeQuery(id+"F42.imprint","IMPRINT",EDGE,{"derivedFrom":sQuery(id+"F42.wireOp",EDGE,"E106.11.0.1")}),1.0]])]});
            var Q2;
            Q2=makeQuery(id+"F42.imprint","IMPRINT",FACE,{"disambiguationData":[TD([[makeQuery(id+"F42.imprint","IMPRINT",EDGE,{"derivedFrom":sQuery(id+"F42.wireOp",EDGE,"E106.12.0.1")}),1.0]])]});
            var Q3;
            Q3=makeQuery(id+"F42.imprint","IMPRINT",FACE,{"disambiguationData":[TD([[makeQuery(id+"F42.imprint","IMPRINT",EDGE,{"derivedFrom":sQuery(id+"F42.wireOp",EDGE,"E106.12.0.8")}),1.0]])]});
            var Q4;
            Q4=makeQuery(id+"F42.imprint","IMPRINT",FACE,{"disambiguationData":[TD([[makeQuery(id+"F42.imprint","IMPRINT",EDGE,{"derivedFrom":sQuery(id+"F42.wireOp",EDGE,"E106.12.0.0")}),1.0]])]});
            var Q5;
            Q5=makeQuery(id+"F42.imprint","IMPRINT",FACE,{"disambiguationData":[TD([[makeQuery(id+"F42.imprint","IMPRINT",EDGE,{"derivedFrom":sQuery(id+"F42.wireOp",EDGE,"E106.11.0.0")}),1.0]])]});
            extrude(context, id + "F51", {"entities" : qUnion([Q0, Q1, Q2, Q3, Q4, Q5]), "operationType" : NewBodyOperationType.REMOVE, "oppositeDirection" : true, "depth" : 25 * mm, "offsetDistance" : 25 * mm});
        }
        {
            var Q0;
            Q0=makeQuery(id+"F42.imprint","IMPRINT",FACE,{"disambiguationData":[TD([[makeQuery(id+"F42.imprint","IMPRINT",EDGE,{"derivedFrom":sQuery(id+"F42.wireOp",EDGE,"E106.13.0.8")}),1.0]])]});
            var Q1;
            Q1=makeQuery(id+"F42.imprint","IMPRINT",FACE,{"disambiguationData":[TD([[makeQuery(id+"F42.imprint","IMPRINT",EDGE,{"derivedFrom":sQuery(id+"F42.wireOp",EDGE,"E106.13.0.1")}),1.0]])]});
            var Q2;
            Q2=makeQuery(id+"F42.imprint","IMPRINT",FACE,{"disambiguationData":[TD([[makeQuery(id+"F42.imprint","IMPRINT",EDGE,{"derivedFrom":sQuery(id+"F42.wireOp",EDGE,"E106.13.0.0")}),1.0]])]});
            var Q3;
            Q3=makeQuery(id+"F42.imprint","IMPRINT",FACE,{"disambiguationData":[TD([[makeQuery(id+"F42.imprint","IMPRINT",EDGE,{"derivedFrom":sQuery(id+"F42.wireOp",EDGE,"E106.14.0.0")}),1.0]])]});
            var Q4;
            Q4=makeQuery(id+"F42.imprint","IMPRINT",FACE,{"disambiguationData":[TD([[makeQuery(id+"F42.imprint","IMPRINT",EDGE,{"derivedFrom":sQuery(id+"F42.wireOp",EDGE,"E106.14.0.8")}),1.0]])]});
            var Q5;
            Q5=makeQuery(id+"F42.imprint","IMPRINT",FACE,{"disambiguationData":[TD([[makeQuery(id+"F42.imprint","IMPRINT",EDGE,{"derivedFrom":sQuery(id+"F42.wireOp",EDGE,"E106.14.0.1")}),1.0]])]});
            extrude(context, id + "F52", {"entities" : qUnion([Q0, Q1, Q2, Q3, Q4, Q5]), "operationType" : NewBodyOperationType.REMOVE, "oppositeDirection" : true, "depth" : 25 * mm, "offsetDistance" : 25 * mm});
        }
        {
            var Q0;
            Q0=makeQuery(id+"F42.imprint","IMPRINT",FACE,{"disambiguationData":[TD([[makeQuery(id+"F42.imprint","IMPRINT",EDGE,{"derivedFrom":sQuery(id+"F42.wireOp",EDGE,"E106.15.0.1")}),1.0]])]});
            var Q1;
            Q1=makeQuery(id+"F42.imprint","IMPRINT",FACE,{"disambiguationData":[TD([[makeQuery(id+"F42.imprint","IMPRINT",EDGE,{"derivedFrom":sQuery(id+"F42.wireOp",EDGE,"E106.16.0.1")}),1.0]])]});
            var Q2;
            Q2=makeQuery(id+"F42.imprint","IMPRINT",FACE,{"disambiguationData":[TD([[makeQuery(id+"F42.imprint","IMPRINT",EDGE,{"derivedFrom":sQuery(id+"F42.wireOp",EDGE,"E106.16.0.8")}),1.0]])]});
            var Q3;
            Q3=makeQuery(id+"F42.imprint","IMPRINT",FACE,{"disambiguationData":[TD([[makeQuery(id+"F42.imprint","IMPRINT",EDGE,{"derivedFrom":sQuery(id+"F42.wireOp",EDGE,"E106.15.0.8")}),1.0]])]});
            var Q4;
            Q4=makeQuery(id+"F42.imprint","IMPRINT",FACE,{"disambiguationData":[TD([[makeQuery(id+"F42.imprint","IMPRINT",EDGE,{"derivedFrom":sQuery(id+"F42.wireOp",EDGE,"E106.15.0.0")}),1.0]])]});
            var Q5;
            Q5=makeQuery(id+"F42.imprint","IMPRINT",FACE,{"disambiguationData":[TD([[makeQuery(id+"F42.imprint","IMPRINT",EDGE,{"derivedFrom":sQuery(id+"F42.wireOp",EDGE,"E106.16.0.0")}),1.0]])]});
            extrude(context, id + "F53", {"entities" : qUnion([Q0, Q1, Q2, Q3, Q4, Q5]), "operationType" : NewBodyOperationType.REMOVE, "oppositeDirection" : true, "depth" : 25 * mm, "offsetDistance" : 25 * mm});
        }
        {
            var Q0;
            Q0=makeQuery(id+"F42.imprint","IMPRINT",FACE,{"disambiguationData":[TD([[makeQuery(id+"F42.imprint","IMPRINT",EDGE,{"derivedFrom":sQuery(id+"F42.wireOp",EDGE,"E106.20.0.8")}),1.0]])]});
            var Q1;
            Q1=makeQuery(id+"F42.imprint","IMPRINT",FACE,{"disambiguationData":[TD([[makeQuery(id+"F42.imprint","IMPRINT",EDGE,{"derivedFrom":sQuery(id+"F42.wireOp",EDGE,"E106.20.0.1")}),1.0]])]});
            var Q2;
            Q2=makeQuery(id+"F42.imprint","IMPRINT",FACE,{"disambiguationData":[TD([[makeQuery(id+"F42.imprint","IMPRINT",EDGE,{"derivedFrom":sQuery(id+"F42.wireOp",EDGE,"E106.17.0.0")}),1.0]])]});
            var Q3;
            Q3=makeQuery(id+"F42.imprint","IMPRINT",FACE,{"disambiguationData":[TD([[makeQuery(id+"F42.imprint","IMPRINT",EDGE,{"derivedFrom":sQuery(id+"F42.wireOp",EDGE,"E106.20.0.0")}),1.0]])]});
            var Q4;
            Q4=makeQuery(id+"F42.imprint","IMPRINT",FACE,{"disambiguationData":[TD([[makeQuery(id+"F42.imprint","IMPRINT",EDGE,{"derivedFrom":sQuery(id+"F42.wireOp",EDGE,"E106.19.0.8")}),1.0]])]});
            var Q5;
            Q5=makeQuery(id+"F42.imprint","IMPRINT",FACE,{"disambiguationData":[TD([[makeQuery(id+"F42.imprint","IMPRINT",EDGE,{"derivedFrom":sQuery(id+"F42.wireOp",EDGE,"E106.17.0.8")}),1.0]])]});
            var Q6;
            Q6=makeQuery(id+"F42.imprint","IMPRINT",FACE,{"disambiguationData":[TD([[makeQuery(id+"F42.imprint","IMPRINT",EDGE,{"derivedFrom":sQuery(id+"F42.wireOp",EDGE,"E106.17.0.1")}),1.0]])]});
            var Q7;
            Q7=makeQuery(id+"F42.imprint","IMPRINT",FACE,{"disambiguationData":[TD([[makeQuery(id+"F42.imprint","IMPRINT",EDGE,{"derivedFrom":sQuery(id+"F42.wireOp",EDGE,"E106.18.0.0")}),1.0]])]});
            var Q8;
            Q8=makeQuery(id+"F42.imprint","IMPRINT",FACE,{"disambiguationData":[TD([[makeQuery(id+"F42.imprint","IMPRINT",EDGE,{"derivedFrom":sQuery(id+"F42.wireOp",EDGE,"E106.18.0.8")}),1.0]])]});
            var Q9;
            Q9=makeQuery(id+"F42.imprint","IMPRINT",FACE,{"disambiguationData":[TD([[makeQuery(id+"F42.imprint","IMPRINT",EDGE,{"derivedFrom":sQuery(id+"F42.wireOp",EDGE,"E106.18.0.1")}),1.0]])]});
            var Q10;
            Q10=makeQuery(id+"F42.imprint","IMPRINT",FACE,{"disambiguationData":[TD([[makeQuery(id+"F42.imprint","IMPRINT",EDGE,{"derivedFrom":sQuery(id+"F42.wireOp",EDGE,"E106.19.0.1")}),1.0]])]});
            var Q11;
            Q11=makeQuery(id+"F42.imprint","IMPRINT",FACE,{"disambiguationData":[TD([[makeQuery(id+"F42.imprint","IMPRINT",EDGE,{"derivedFrom":sQuery(id+"F42.wireOp",EDGE,"E106.19.0.0")}),1.0]])]});
            extrude(context, id + "F54", {"entities" : qUnion([Q0, Q1, Q2, Q3, Q4, Q5, Q6, Q7, Q8, Q9, Q10, Q11]), "operationType" : NewBodyOperationType.REMOVE, "oppositeDirection" : true, "depth" : 25 * mm, "offsetDistance" : 25 * mm});
        }
        {
            var Q0;
            Q0=makeQuery(id+"F42.imprint","IMPRINT",FACE,{"disambiguationData":[TD([[makeQuery(id+"F42.imprint","IMPRINT",EDGE,{"derivedFrom":sQuery(id+"F42.wireOp",EDGE,"E106.21.0.8")}),1.0]])]});
            var Q1;
            Q1=makeQuery(id+"F42.imprint","IMPRINT",FACE,{"disambiguationData":[TD([[makeQuery(id+"F42.imprint","IMPRINT",EDGE,{"derivedFrom":sQuery(id+"F42.wireOp",EDGE,"E106.22.0.1")}),1.0]])]});
            var Q2;
            Q2=makeQuery(id+"F42.imprint","IMPRINT",FACE,{"disambiguationData":[TD([[makeQuery(id+"F42.imprint","IMPRINT",EDGE,{"derivedFrom":sQuery(id+"F42.wireOp",EDGE,"E106.22.0.0")}),1.0]])]});
            var Q3;
            Q3=makeQuery(id+"F42.imprint","IMPRINT",FACE,{"disambiguationData":[TD([[makeQuery(id+"F42.imprint","IMPRINT",EDGE,{"derivedFrom":sQuery(id+"F42.wireOp",EDGE,"E106.23.0.0")}),1.0]])]});
            var Q4;
            Q4=makeQuery(id+"F42.imprint","IMPRINT",FACE,{"disambiguationData":[TD([[makeQuery(id+"F42.imprint","IMPRINT",EDGE,{"derivedFrom":sQuery(id+"F42.wireOp",EDGE,"E106.22.0.8")}),1.0]])]});
            var Q5;
            Q5=makeQuery(id+"F42.imprint","IMPRINT",FACE,{"disambiguationData":[TD([[makeQuery(id+"F42.imprint","IMPRINT",EDGE,{"derivedFrom":sQuery(id+"F42.wireOp",EDGE,"E106.23.0.1")}),1.0]])]});
            var Q6;
            Q6=makeQuery(id+"F42.imprint","IMPRINT",FACE,{"disambiguationData":[TD([[makeQuery(id+"F42.imprint","IMPRINT",EDGE,{"derivedFrom":sQuery(id+"F42.wireOp",EDGE,"E106.24.0.0")}),1.0]])]});
            var Q7;
            Q7=makeQuery(id+"F42.imprint","IMPRINT",FACE,{"disambiguationData":[TD([[makeQuery(id+"F42.imprint","IMPRINT",EDGE,{"derivedFrom":sQuery(id+"F42.wireOp",EDGE,"E106.23.0.8")}),1.0]])]});
            var Q8;
            Q8=makeQuery(id+"F42.imprint","IMPRINT",FACE,{"disambiguationData":[TD([[makeQuery(id+"F42.imprint","IMPRINT",EDGE,{"derivedFrom":sQuery(id+"F42.wireOp",EDGE,"E106.24.0.8")}),1.0]])]});
            var Q9;
            Q9=makeQuery(id+"F42.imprint","IMPRINT",FACE,{"disambiguationData":[TD([[makeQuery(id+"F42.imprint","IMPRINT",EDGE,{"derivedFrom":sQuery(id+"F42.wireOp",EDGE,"E106.24.0.1")}),1.0]])]});
            var Q10;
            Q10=makeQuery(id+"F42.imprint","IMPRINT",FACE,{"disambiguationData":[TD([[makeQuery(id+"F42.imprint","IMPRINT",EDGE,{"derivedFrom":sQuery(id+"F42.wireOp",EDGE,"E106.21.0.1")}),1.0]])]});
            var Q11;
            Q11=makeQuery(id+"F42.imprint","IMPRINT",FACE,{"disambiguationData":[TD([[makeQuery(id+"F42.imprint","IMPRINT",EDGE,{"derivedFrom":sQuery(id+"F42.wireOp",EDGE,"E106.21.0.0")}),1.0]])]});
            extrude(context, id + "F55", {"entities" : qUnion([Q0, Q1, Q2, Q3, Q4, Q5, Q6, Q7, Q8, Q9, Q10, Q11]), "operationType" : NewBodyOperationType.REMOVE, "oppositeDirection" : true, "depth" : 25 * mm, "offsetDistance" : 25 * mm});
        }
        {
            var Q0;
            Q0=makeQuery(id+"F42.imprint","IMPRINT",FACE,{"disambiguationData":[TD([[makeQuery(id+"F42.imprint","IMPRINT",EDGE,{"derivedFrom":sQuery(id+"F42.wireOp",EDGE,"E106.26.0.0")}),1.0]])]});
            var Q1;
            Q1=makeQuery(id+"F42.imprint","IMPRINT",FACE,{"disambiguationData":[TD([[makeQuery(id+"F42.imprint","IMPRINT",EDGE,{"derivedFrom":sQuery(id+"F42.wireOp",EDGE,"E106.25.0.8")}),1.0]])]});
            var Q2;
            Q2=makeQuery(id+"F42.imprint","IMPRINT",FACE,{"disambiguationData":[TD([[makeQuery(id+"F42.imprint","IMPRINT",EDGE,{"derivedFrom":sQuery(id+"F42.wireOp",EDGE,"E106.27.0.0")}),1.0]])]});
            var Q3;
            Q3=makeQuery(id+"F42.imprint","IMPRINT",FACE,{"disambiguationData":[TD([[makeQuery(id+"F42.imprint","IMPRINT",EDGE,{"derivedFrom":sQuery(id+"F42.wireOp",EDGE,"E106.26.0.8")}),1.0]])]});
            var Q4;
            Q4=makeQuery(id+"F42.imprint","IMPRINT",FACE,{"disambiguationData":[TD([[makeQuery(id+"F42.imprint","IMPRINT",EDGE,{"derivedFrom":sQuery(id+"F42.wireOp",EDGE,"E106.27.0.8")}),1.0]])]});
            var Q5;
            Q5=makeQuery(id+"F42.imprint","IMPRINT",FACE,{"disambiguationData":[TD([[makeQuery(id+"F42.imprint","IMPRINT",EDGE,{"derivedFrom":sQuery(id+"F42.wireOp",EDGE,"E106.27.0.1")}),1.0]])]});
            var Q6;
            Q6=makeQuery(id+"F42.imprint","IMPRINT",FACE,{"disambiguationData":[TD([[makeQuery(id+"F42.imprint","IMPRINT",EDGE,{"derivedFrom":sQuery(id+"F42.wireOp",EDGE,"E106.26.0.1")}),1.0]])]});
            var Q7;
            Q7=makeQuery(id+"F42.imprint","IMPRINT",FACE,{"disambiguationData":[TD([[makeQuery(id+"F42.imprint","IMPRINT",EDGE,{"derivedFrom":sQuery(id+"F42.wireOp",EDGE,"E106.28.0.1")}),1.0]])]});
            var Q8;
            Q8=makeQuery(id+"F42.imprint","IMPRINT",FACE,{"disambiguationData":[TD([[makeQuery(id+"F42.imprint","IMPRINT",EDGE,{"derivedFrom":sQuery(id+"F42.wireOp",EDGE,"E106.28.0.0")}),1.0]])]});
            var Q9;
            Q9=makeQuery(id+"F42.imprint","IMPRINT",FACE,{"disambiguationData":[TD([[makeQuery(id+"F42.imprint","IMPRINT",EDGE,{"derivedFrom":sQuery(id+"F42.wireOp",EDGE,"E106.28.0.8")}),1.0]])]});
            var Q10;
            Q10=makeQuery(id+"F42.imprint","IMPRINT",FACE,{"disambiguationData":[TD([[makeQuery(id+"F42.imprint","IMPRINT",EDGE,{"derivedFrom":sQuery(id+"F42.wireOp",EDGE,"E106.25.0.1")}),1.0]])]});
            var Q11;
            Q11=makeQuery(id+"F42.imprint","IMPRINT",FACE,{"disambiguationData":[TD([[makeQuery(id+"F42.imprint","IMPRINT",EDGE,{"derivedFrom":sQuery(id+"F42.wireOp",EDGE,"E106.25.0.0")}),1.0]])]});
            extrude(context, id + "F56", {"entities" : qUnion([Q0, Q1, Q2, Q3, Q4, Q5, Q6, Q7, Q8, Q9, Q10, Q11]), "operationType" : NewBodyOperationType.REMOVE, "oppositeDirection" : true, "depth" : 25 * mm, "offsetDistance" : 25 * mm});
        }
        {
            var Q0;
            Q0=makeQuery(id+"F42.imprint","IMPRINT",FACE,{"disambiguationData":[TD([[makeQuery(id+"F42.imprint","IMPRINT",EDGE,{"derivedFrom":sQuery(id+"F42.wireOp",EDGE,"E106.31.0.1")}),1.0]])]});
            var Q1;
            Q1=makeQuery(id+"F42.imprint","IMPRINT",FACE,{"disambiguationData":[TD([[makeQuery(id+"F42.imprint","IMPRINT",EDGE,{"derivedFrom":sQuery(id+"F42.wireOp",EDGE,"E106.31.0.0")}),1.0]])]});
            var Q2;
            Q2=makeQuery(id+"F42.imprint","IMPRINT",FACE,{"disambiguationData":[TD([[makeQuery(id+"F42.imprint","IMPRINT",EDGE,{"derivedFrom":sQuery(id+"F42.wireOp",EDGE,"E106.32.0.1")}),1.0]])]});
            var Q3;
            Q3=makeQuery(id+"F42.imprint","IMPRINT",FACE,{"disambiguationData":[TD([[makeQuery(id+"F42.imprint","IMPRINT",EDGE,{"derivedFrom":sQuery(id+"F42.wireOp",EDGE,"E106.32.0.0")}),1.0]])]});
            var Q4;
            Q4=makeQuery(id+"F42.imprint","IMPRINT",FACE,{"disambiguationData":[TD([[makeQuery(id+"F42.imprint","IMPRINT",EDGE,{"derivedFrom":sQuery(id+"F42.wireOp",EDGE,"E106.32.0.8")}),1.0]])]});
            var Q5;
            Q5=makeQuery(id+"F42.imprint","IMPRINT",FACE,{"disambiguationData":[TD([[makeQuery(id+"F42.imprint","IMPRINT",EDGE,{"derivedFrom":sQuery(id+"F42.wireOp",EDGE,"E106.31.0.8")}),1.0]])]});
            var Q6;
            Q6=makeQuery(id+"F42.imprint","IMPRINT",FACE,{"disambiguationData":[TD([[makeQuery(id+"F42.imprint","IMPRINT",EDGE,{"derivedFrom":sQuery(id+"F42.wireOp",EDGE,"E106.30.0.8")}),1.0]])]});
            var Q7;
            Q7=makeQuery(id+"F42.imprint","IMPRINT",FACE,{"disambiguationData":[TD([[makeQuery(id+"F42.imprint","IMPRINT",EDGE,{"derivedFrom":sQuery(id+"F42.wireOp",EDGE,"E106.30.0.1")}),1.0]])]});
            var Q8;
            Q8=makeQuery(id+"F42.imprint","IMPRINT",FACE,{"disambiguationData":[TD([[makeQuery(id+"F42.imprint","IMPRINT",EDGE,{"derivedFrom":sQuery(id+"F42.wireOp",EDGE,"E106.30.0.0")}),1.0]])]});
            var Q9;
            Q9=makeQuery(id+"F42.imprint","IMPRINT",FACE,{"disambiguationData":[TD([[makeQuery(id+"F42.imprint","IMPRINT",EDGE,{"derivedFrom":sQuery(id+"F42.wireOp",EDGE,"E106.29.0.8")}),1.0]])]});
            var Q10;
            Q10=makeQuery(id+"F42.imprint","IMPRINT",FACE,{"disambiguationData":[TD([[makeQuery(id+"F42.imprint","IMPRINT",EDGE,{"derivedFrom":sQuery(id+"F42.wireOp",EDGE,"E106.29.0.1")}),1.0]])]});
            var Q11;
            Q11=makeQuery(id+"F42.imprint","IMPRINT",FACE,{"disambiguationData":[TD([[makeQuery(id+"F42.imprint","IMPRINT",EDGE,{"derivedFrom":sQuery(id+"F42.wireOp",EDGE,"E106.29.0.0")}),1.0]])]});
            extrude(context, id + "F57", {"entities" : qUnion([Q0, Q1, Q2, Q3, Q4, Q5, Q6, Q7, Q8, Q9, Q10, Q11]), "operationType" : NewBodyOperationType.REMOVE, "oppositeDirection" : true, "depth" : 25 * mm, "offsetDistance" : 25 * mm});
        }
        {
            var Q0;
            Q0=makeQuery(id+"F42.imprint","IMPRINT",FACE,{"disambiguationData":[TD([[makeQuery(id+"F42.imprint","IMPRINT",EDGE,{"derivedFrom":sQuery(id+"F42.wireOp",EDGE,"E106.36.0.8")}),1.0]])]});
            var Q1;
            Q1=makeQuery(id+"F42.imprint","IMPRINT",FACE,{"disambiguationData":[TD([[makeQuery(id+"F42.imprint","IMPRINT",EDGE,{"derivedFrom":sQuery(id+"F42.wireOp",EDGE,"E106.36.0.1")}),1.0]])]});
            var Q2;
            Q2=makeQuery(id+"F42.imprint","IMPRINT",FACE,{"disambiguationData":[TD([[makeQuery(id+"F42.imprint","IMPRINT",EDGE,{"derivedFrom":sQuery(id+"F42.wireOp",EDGE,"E106.36.0.0")}),1.0]])]});
            var Q3;
            Q3=makeQuery(id+"F42.imprint","IMPRINT",FACE,{"disambiguationData":[TD([[makeQuery(id+"F42.imprint","IMPRINT",EDGE,{"derivedFrom":sQuery(id+"F42.wireOp",EDGE,"E106.35.0.8")}),1.0]])]});
            var Q4;
            Q4=makeQuery(id+"F42.imprint","IMPRINT",FACE,{"disambiguationData":[TD([[makeQuery(id+"F42.imprint","IMPRINT",EDGE,{"derivedFrom":sQuery(id+"F42.wireOp",EDGE,"E106.33.0.8")}),1.0]])]});
            var Q5;
            Q5=makeQuery(id+"F42.imprint","IMPRINT",FACE,{"disambiguationData":[TD([[makeQuery(id+"F42.imprint","IMPRINT",EDGE,{"derivedFrom":sQuery(id+"F42.wireOp",EDGE,"E106.34.0.0")}),1.0]])]});
            var Q6;
            Q6=makeQuery(id+"F42.imprint","IMPRINT",FACE,{"disambiguationData":[TD([[makeQuery(id+"F42.imprint","IMPRINT",EDGE,{"derivedFrom":sQuery(id+"F42.wireOp",EDGE,"E106.34.0.8")}),1.0]])]});
            var Q7;
            Q7=makeQuery(id+"F42.imprint","IMPRINT",FACE,{"disambiguationData":[TD([[makeQuery(id+"F42.imprint","IMPRINT",EDGE,{"derivedFrom":sQuery(id+"F42.wireOp",EDGE,"E106.34.0.1")}),1.0]])]});
            var Q8;
            Q8=makeQuery(id+"F42.imprint","IMPRINT",FACE,{"disambiguationData":[TD([[makeQuery(id+"F42.imprint","IMPRINT",EDGE,{"derivedFrom":sQuery(id+"F42.wireOp",EDGE,"E106.35.0.1")}),1.0]])]});
            var Q9;
            Q9=makeQuery(id+"F42.imprint","IMPRINT",FACE,{"disambiguationData":[TD([[makeQuery(id+"F42.imprint","IMPRINT",EDGE,{"derivedFrom":sQuery(id+"F42.wireOp",EDGE,"E106.35.0.0")}),1.0]])]});
            var Q10;
            Q10=makeQuery(id+"F42.imprint","IMPRINT",FACE,{"disambiguationData":[TD([[makeQuery(id+"F42.imprint","IMPRINT",EDGE,{"derivedFrom":sQuery(id+"F42.wireOp",EDGE,"E106.33.0.0")}),1.0]])]});
            var Q11;
            Q11=makeQuery(id+"F42.imprint","IMPRINT",FACE,{"disambiguationData":[TD([[makeQuery(id+"F42.imprint","IMPRINT",EDGE,{"derivedFrom":sQuery(id+"F42.wireOp",EDGE,"E106.33.0.1")}),1.0]])]});
            extrude(context, id + "F58", {"entities" : qUnion([Q0, Q1, Q2, Q3, Q4, Q5, Q6, Q7, Q8, Q9, Q10, Q11]), "operationType" : NewBodyOperationType.REMOVE, "oppositeDirection" : true, "depth" : 25 * mm, "offsetDistance" : 25 * mm});
        }
        {
            var Q0;
            Q0=makeQuery(id+"F42.imprint","IMPRINT",FACE,{"disambiguationData":[TD([[makeQuery(id+"F42.imprint","IMPRINT",EDGE,{"derivedFrom":sQuery(id+"F42.wireOp",EDGE,"E106.37.0.8")}),1.0]])]});
            var Q1;
            Q1=makeQuery(id+"F42.imprint","IMPRINT",FACE,{"disambiguationData":[TD([[makeQuery(id+"F42.imprint","IMPRINT",EDGE,{"derivedFrom":sQuery(id+"F42.wireOp",EDGE,"E106.38.0.1")}),1.0]])]});
            var Q2;
            Q2=makeQuery(id+"F42.imprint","IMPRINT",FACE,{"disambiguationData":[TD([[makeQuery(id+"F42.imprint","IMPRINT",EDGE,{"derivedFrom":sQuery(id+"F42.wireOp",EDGE,"E106.38.0.0")}),1.0]])]});
            var Q3;
            Q3=makeQuery(id+"F42.imprint","IMPRINT",FACE,{"disambiguationData":[TD([[makeQuery(id+"F42.imprint","IMPRINT",EDGE,{"derivedFrom":sQuery(id+"F42.wireOp",EDGE,"E106.39.0.0")}),1.0]])]});
            var Q4;
            Q4=makeQuery(id+"F42.imprint","IMPRINT",FACE,{"disambiguationData":[TD([[makeQuery(id+"F42.imprint","IMPRINT",EDGE,{"derivedFrom":sQuery(id+"F42.wireOp",EDGE,"E106.38.0.8")}),1.0]])]});
            var Q5;
            Q5=makeQuery(id+"F42.imprint","IMPRINT",FACE,{"disambiguationData":[TD([[makeQuery(id+"F42.imprint","IMPRINT",EDGE,{"derivedFrom":sQuery(id+"F42.wireOp",EDGE,"E106.39.0.1")}),1.0]])]});
            var Q6;
            Q6=makeQuery(id+"F42.imprint","IMPRINT",FACE,{"disambiguationData":[TD([[makeQuery(id+"F42.imprint","IMPRINT",EDGE,{"derivedFrom":sQuery(id+"F42.wireOp",EDGE,"E106.40.0.0")}),1.0]])]});
            var Q7;
            Q7=makeQuery(id+"F42.imprint","IMPRINT",FACE,{"disambiguationData":[TD([[makeQuery(id+"F42.imprint","IMPRINT",EDGE,{"derivedFrom":sQuery(id+"F42.wireOp",EDGE,"E106.39.0.8")}),1.0]])]});
            var Q8;
            Q8=makeQuery(id+"F42.imprint","IMPRINT",FACE,{"disambiguationData":[TD([[makeQuery(id+"F42.imprint","IMPRINT",EDGE,{"derivedFrom":sQuery(id+"F42.wireOp",EDGE,"E106.40.0.8")}),1.0]])]});
            var Q9;
            Q9=makeQuery(id+"F42.imprint","IMPRINT",FACE,{"disambiguationData":[TD([[makeQuery(id+"F42.imprint","IMPRINT",EDGE,{"derivedFrom":sQuery(id+"F42.wireOp",EDGE,"E106.40.0.1")}),1.0]])]});
            var Q10;
            Q10=makeQuery(id+"F42.imprint","IMPRINT",FACE,{"disambiguationData":[TD([[makeQuery(id+"F42.imprint","IMPRINT",EDGE,{"derivedFrom":sQuery(id+"F42.wireOp",EDGE,"E106.37.0.1")}),1.0]])]});
            var Q11;
            Q11=makeQuery(id+"F42.imprint","IMPRINT",FACE,{"disambiguationData":[TD([[makeQuery(id+"F42.imprint","IMPRINT",EDGE,{"derivedFrom":sQuery(id+"F42.wireOp",EDGE,"E106.37.0.0")}),1.0]])]});
            extrude(context, id + "F59", {"entities" : qUnion([Q0, Q1, Q2, Q3, Q4, Q5, Q6, Q7, Q8, Q9, Q10, Q11]), "operationType" : NewBodyOperationType.REMOVE, "oppositeDirection" : true, "depth" : 25 * mm, "offsetDistance" : 25 * mm});
        }
        {
            var Q0;
            Q0=makeQuery(id+"F42.imprint","IMPRINT",FACE,{"disambiguationData":[TD([[makeQuery(id+"F42.imprint","IMPRINT",EDGE,{"derivedFrom":sQuery(id+"F42.wireOp",EDGE,"E106.41.0.8")}),1.0]])]});
            var Q1;
            Q1=makeQuery(id+"F42.imprint","IMPRINT",FACE,{"disambiguationData":[TD([[makeQuery(id+"F42.imprint","IMPRINT",EDGE,{"derivedFrom":sQuery(id+"F42.wireOp",EDGE,"E106.42.0.8")}),1.0]])]});
            var Q2;
            Q2=makeQuery(id+"F42.imprint","IMPRINT",FACE,{"disambiguationData":[TD([[makeQuery(id+"F42.imprint","IMPRINT",EDGE,{"derivedFrom":sQuery(id+"F42.wireOp",EDGE,"E106.43.0.8")}),1.0]])]});
            var Q3;
            Q3=makeQuery(id+"F42.imprint","IMPRINT",FACE,{"disambiguationData":[TD([[makeQuery(id+"F42.imprint","IMPRINT",EDGE,{"derivedFrom":sQuery(id+"F42.wireOp",EDGE,"E106.44.0.8")}),1.0]])]});
            var Q4;
            Q4=makeQuery(id+"F42.imprint","IMPRINT",FACE,{"disambiguationData":[TD([[makeQuery(id+"F42.imprint","IMPRINT",EDGE,{"derivedFrom":sQuery(id+"F42.wireOp",EDGE,"E106.42.0.0")}),1.0]])]});
            var Q5;
            Q5=makeQuery(id+"F42.imprint","IMPRINT",FACE,{"disambiguationData":[TD([[makeQuery(id+"F42.imprint","IMPRINT",EDGE,{"derivedFrom":sQuery(id+"F42.wireOp",EDGE,"E106.43.0.0")}),1.0]])]});
            var Q6;
            Q6=makeQuery(id+"F42.imprint","IMPRINT",FACE,{"disambiguationData":[TD([[makeQuery(id+"F42.imprint","IMPRINT",EDGE,{"derivedFrom":sQuery(id+"F42.wireOp",EDGE,"E106.44.0.0")}),1.0]])]});
            var Q7;
            Q7=makeQuery(id+"F42.imprint","IMPRINT",FACE,{"disambiguationData":[TD([[makeQuery(id+"F42.imprint","IMPRINT",EDGE,{"derivedFrom":sQuery(id+"F42.wireOp",EDGE,"E106.43.0.1")}),1.0]])]});
            var Q8;
            Q8=makeQuery(id+"F42.imprint","IMPRINT",FACE,{"disambiguationData":[TD([[makeQuery(id+"F42.imprint","IMPRINT",EDGE,{"derivedFrom":sQuery(id+"F42.wireOp",EDGE,"E106.42.0.1")}),1.0]])]});
            var Q9;
            Q9=makeQuery(id+"F42.imprint","IMPRINT",FACE,{"disambiguationData":[TD([[makeQuery(id+"F42.imprint","IMPRINT",EDGE,{"derivedFrom":sQuery(id+"F42.wireOp",EDGE,"E106.44.0.1")}),1.0]])]});
            var Q10;
            Q10=makeQuery(id+"F42.imprint","IMPRINT",FACE,{"disambiguationData":[TD([[makeQuery(id+"F42.imprint","IMPRINT",EDGE,{"derivedFrom":sQuery(id+"F42.wireOp",EDGE,"E106.41.0.1")}),1.0]])]});
            var Q11;
            Q11=makeQuery(id+"F42.imprint","IMPRINT",FACE,{"disambiguationData":[TD([[makeQuery(id+"F42.imprint","IMPRINT",EDGE,{"derivedFrom":sQuery(id+"F42.wireOp",EDGE,"E106.41.0.0")}),1.0]])]});
            extrude(context, id + "F60", {"entities" : qUnion([Q0, Q1, Q2, Q3, Q4, Q5, Q6, Q7, Q8, Q9, Q10, Q11]), "operationType" : NewBodyOperationType.REMOVE, "oppositeDirection" : true, "depth" : 25 * mm, "offsetDistance" : 25 * mm});
        }
        {
            var Q0;
            Q0=makeQuery(id+"F42.imprint","IMPRINT",FACE,{"disambiguationData":[TD([[makeQuery(id+"F42.imprint","IMPRINT",EDGE,{"derivedFrom":sQuery(id+"F42.wireOp",EDGE,"E106.47.0.0")}),1.0]])]});
            var Q1;
            Q1=makeQuery(id+"F42.imprint","IMPRINT",FACE,{"disambiguationData":[TD([[makeQuery(id+"F42.imprint","IMPRINT",EDGE,{"derivedFrom":sQuery(id+"F42.wireOp",EDGE,"E106.48.0.0")}),1.0]])]});
            var Q2;
            Q2=makeQuery(id+"F42.imprint","IMPRINT",FACE,{"disambiguationData":[TD([[makeQuery(id+"F42.imprint","IMPRINT",EDGE,{"derivedFrom":sQuery(id+"F42.wireOp",EDGE,"E106.48.0.8")}),1.0]])]});
            var Q3;
            Q3=makeQuery(id+"F42.imprint","IMPRINT",FACE,{"disambiguationData":[TD([[makeQuery(id+"F42.imprint","IMPRINT",EDGE,{"derivedFrom":sQuery(id+"F42.wireOp",EDGE,"E106.47.0.8")}),1.0]])]});
            var Q4;
            Q4=makeQuery(id+"F42.imprint","IMPRINT",FACE,{"disambiguationData":[TD([[makeQuery(id+"F42.imprint","IMPRINT",EDGE,{"derivedFrom":sQuery(id+"F42.wireOp",EDGE,"E106.46.0.8")}),1.0]])]});
            var Q5;
            Q5=makeQuery(id+"F42.imprint","IMPRINT",FACE,{"disambiguationData":[TD([[makeQuery(id+"F42.imprint","IMPRINT",EDGE,{"derivedFrom":sQuery(id+"F42.wireOp",EDGE,"E106.46.0.0")}),1.0]])]});
            var Q6;
            Q6=makeQuery(id+"F42.imprint","IMPRINT",FACE,{"disambiguationData":[TD([[makeQuery(id+"F42.imprint","IMPRINT",EDGE,{"derivedFrom":sQuery(id+"F42.wireOp",EDGE,"E106.45.0.8")}),1.0]])]});
            var Q7;
            Q7=makeQuery(id+"F42.imprint","IMPRINT",FACE,{"disambiguationData":[TD([[makeQuery(id+"F42.imprint","IMPRINT",EDGE,{"derivedFrom":sQuery(id+"F42.wireOp",EDGE,"E106.47.0.1")}),1.0]])]});
            var Q8;
            Q8=makeQuery(id+"F42.imprint","IMPRINT",FACE,{"disambiguationData":[TD([[makeQuery(id+"F42.imprint","IMPRINT",EDGE,{"derivedFrom":sQuery(id+"F42.wireOp",EDGE,"E106.48.0.1")}),1.0]])]});
            var Q9;
            Q9=makeQuery(id+"F42.imprint","IMPRINT",FACE,{"disambiguationData":[TD([[makeQuery(id+"F42.imprint","IMPRINT",EDGE,{"derivedFrom":sQuery(id+"F42.wireOp",EDGE,"E106.46.0.1")}),1.0]])]});
            var Q10;
            Q10=makeQuery(id+"F42.imprint","IMPRINT",FACE,{"disambiguationData":[TD([[makeQuery(id+"F42.imprint","IMPRINT",EDGE,{"derivedFrom":sQuery(id+"F42.wireOp",EDGE,"E106.45.0.0")}),1.0]])]});
            var Q11;
            Q11=makeQuery(id+"F42.imprint","IMPRINT",FACE,{"disambiguationData":[TD([[makeQuery(id+"F42.imprint","IMPRINT",EDGE,{"derivedFrom":sQuery(id+"F42.wireOp",EDGE,"E106.45.0.1")}),1.0]])]});
            extrude(context, id + "F61", {"entities" : qUnion([Q0, Q1, Q2, Q3, Q4, Q5, Q6, Q7, Q8, Q9, Q10, Q11]), "operationType" : NewBodyOperationType.REMOVE, "oppositeDirection" : true, "depth" : 25 * mm, "offsetDistance" : 25 * mm});
        }
    });
